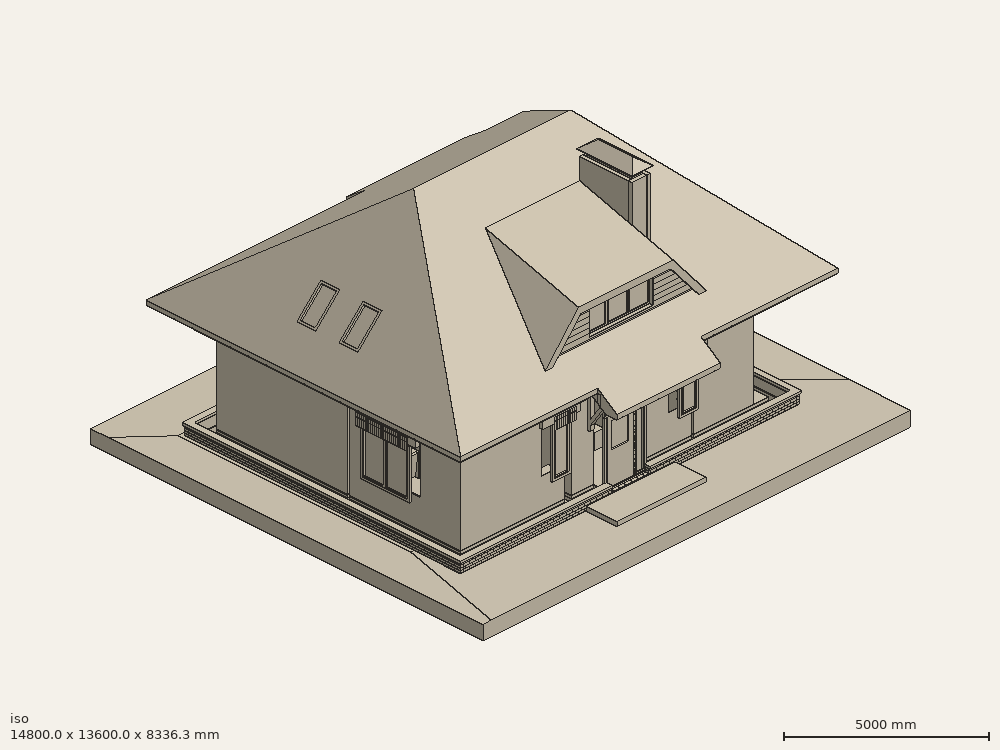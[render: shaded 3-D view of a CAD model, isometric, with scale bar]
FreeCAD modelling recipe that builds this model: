
FCSTD DOCUMENT  (FreeCAD 0.19R)
Label: 280522_90m2_w_smeta
License: All rights reserved
LicenseURL: http://en.wikipedia.org/wiki/All_rights_reserved
objects: Part::Part2DObjectPython×809, Part::FeaturePython×533, App::FeaturePython×150, Part::Feature×112, Part::Box×89, App::GeometryPython×67, Part::Extrusion×36, TechDraw::DrawViewAnnotation×36, Sketcher::SketchObject×34, Part::MultiFuse×31, Part::Cut×30, App::MaterialObjectPython×24, Part::MultiCommon×23, TechDraw::DrawLeaderLine×17, Part::Mirroring×17, App::DocumentObjectGroup×13, TechDraw::DrawViewArch×12, TechDraw::DrawSVGTemplate×10, TechDraw::DrawPage×10, Part::Cylinder×9, +10 more types
note: 1817 computed .brp shape members not serialized (recipe doc carries the construction recipe); baked Part::Feature solids carry a one-line shape summary decoded from their .brp

FEATURE [Part::Part2DObjectPython] Line1049  # Draft 2D object (typed FeaturePython)
  ChamferSize = 0
  Closed = true
  End = (3805,3080,0)
  FilletRadius = 0
  Length = 6815
  MakeFace = false
  Placement = pos=(4290,9800,0) rot=(0,0,1;1.5708rad)
  Points = (2) [(-6720,-6330,0),(-6720,485,0)]
  Start = (10620,3080,0)
  Subdivisions = 0
FEATURE [Sketcher::SketchObject] Sketch231  label="Профиль ПНО 120-8"
  FullyConstrained = false
  Placement = pos=(9420,5.68e-13,0) rot=(1,0,0;1.5708rad)
  sketch-geometry (19):
    g0: LineSegment StartX=0 StartY=0 StartZ=0 EndX=1190 EndY=0 EndZ=0
    g1: LineSegment StartX=1190 StartY=0 StartZ=0 EndX=1190 EndY=160 EndZ=0
    g2: LineSegment StartX=1190 StartY=160 StartZ=0 EndX=0 EndY=160 EndZ=0
    g3: LineSegment StartX=0 StartY=160 StartZ=0 EndX=0 EndY=0 EndZ=0
    g4: Circle CenterX=100 CenterY=80 CenterZ=0 NormalX=0 NormalY=0 NormalZ=1 AngleXU=0 Radius=50
    g5: Circle CenterX=240 CenterY=80 CenterZ=0 NormalX=0 NormalY=0 NormalZ=1 AngleXU=0 Radius=50
    g6: LineSegment StartX=100 StartY=80 StartZ=0 EndX=240 EndY=80 EndZ=0
    g7: Circle CenterX=380 CenterY=80 CenterZ=0 NormalX=0 NormalY=0 NormalZ=1 AngleXU=0 Radius=50
    g8: LineSegment StartX=240 StartY=80 StartZ=0 EndX=380 EndY=80 EndZ=0
    g9: Circle CenterX=520 CenterY=80 CenterZ=0 NormalX=0 NormalY=0 NormalZ=1 AngleXU=0 Radius=50
    g10: LineSegment StartX=380 StartY=80 StartZ=0 EndX=520 EndY=80 EndZ=0
    g11: Circle CenterX=660 CenterY=80 CenterZ=0 NormalX=0 NormalY=0 NormalZ=1 AngleXU=0 Radius=50
    g12: LineSegment StartX=520 StartY=80 StartZ=0 EndX=660 EndY=80 EndZ=0
    g13: Circle CenterX=800 CenterY=80 CenterZ=0 NormalX=0 NormalY=0 NormalZ=1 AngleXU=0 Radius=50
    g14: LineSegment StartX=660 StartY=80 StartZ=0 EndX=800 EndY=80 EndZ=0
    g15: Circle CenterX=940 CenterY=80 CenterZ=0 NormalX=0 NormalY=0 NormalZ=1 AngleXU=0 Radius=50
    g16: LineSegment StartX=800 StartY=80 StartZ=0 EndX=940 EndY=80 EndZ=0
    g17: Circle CenterX=1080 CenterY=80 CenterZ=0 NormalX=0 NormalY=0 NormalZ=1 AngleXU=0 Radius=50
    g18: LineSegment StartX=940 StartY=80 StartZ=0 EndX=1080 EndY=80 EndZ=0
  constraints (49):
    c: Coincident(g0,g1)
    c: Coincident(g1,g2)
    c: Coincident(g2,g3)
    c: Coincident(g3,g0)
    c: Horizontal(g0)
    c: Horizontal(g2)
    c: Vertical(g1)
    c: Vertical(g3)
    c: Coincident(g0,g-1)
    c: DistanceY(g3,g3) = 160
    c: DistanceX(g2,g2) = 1190
    c: Diameter(g4) = 100
    c: DistanceY(g4,g2) = 80
    c: Diameter(g5) = 100
    c: Coincident(g4,g6)
    c: Coincident(g5,g6)
    c: Distance(g6) = 140
    c: Angle(g6) = 0
    c: Diameter(g7) = 100
    c: Coincident(g5,g8)
    c: Coincident(g7,g8)
    c: Equal(g6,g8)
    c: Parallel(g8,g6)
    c: Diameter(g9) = 100
    c: Coincident(g7,g10)
    c: Coincident(g9,g10)
    c: Equal(g6,g10)
    c: Parallel(g10,g6)
    c: Diameter(g11) = 100
    c: Coincident(g9,g12)
    c: Coincident(g11,g12)
    c: Equal(g6,g12)
    c: Parallel(g12,g6)
    c: Diameter(g13) = 100
    c: Coincident(g11,g14)
    c: Coincident(g13,g14)
    c: Equal(g6,g14)
    c: Parallel(g14,g6)
    c: Diameter(g15) = 100
    c: Coincident(g13,g16)
    c: Coincident(g15,g16)
    c: Equal(g6,g16)
    c: Parallel(g16,g6)
    c: Diameter(g17) = 100
    c: Coincident(g15,g18)
    c: Coincident(g17,g18)
    c: Equal(g6,g18)
    c: Parallel(g18,g6)
    c: DistanceX(g2,g4) = 100
FEATURE [Part::Part2DObjectPython] Circle073  label="люк_контур 001"  # Draft 2D object (typed FeaturePython)
  FirstAngle = 0
  LastAngle = 0
  MakeFace = false
  Placement = pos=(32600,-2000,0) rot=(0,0,1;0rad)
  Radius = 350
FEATURE [Part::FeaturePython] Structure044  label="люк контур Д700"  # Arch/BIM 52 (typed FeaturePython)
  Base = -> Circle073
  FaceMaker = 0
  Height = 150
  HorizontalArea = 384845
  IfcData = complex_attributes={"OwnerHistory": {}, "IsNestedBy": {}, "IsDecomposedBy": {}, "IsDefinedBy": {}, "ObjectPlacement": {}, "Representation":... (+4 chars omitted)
  IfcType = 52
  Length = 0
  MoveBase = false
  MoveWithHost = false
  Nodes = (2) [(32600,-2000,0),(32600,-2000,-150)]
  NodesOffset = 0
  Normal = (0,0,-1)
  PerimeterLength = 2199.11
  VerticalArea = 329867
  Width = 100
FEATURE [Part::Part2DObjectPython] Line1077  # Draft 2D object (typed FeaturePython)
  ChamferSize = 0
  Closed = true
  End = (-50,-45,0)
  FilletRadius = 0
  Length = 10670
  MakeFace = false
  Placement = pos=(12060,265,0) rot=(0,0,1;0rad)
  Points = (2) [(-1440,-310,0),(-12110,-310,0)]
  Start = (10620,-45,0)
  Subdivisions = 0
FEATURE [App::FeaturePython] Dimension003  # Draft dimension (typed FeaturePython)
  Diameter = false
  Dimline = (12209.6,200,0)
  Direction = (0,0,0)
  Distance = 9480
  End = (11130,8925,0)
  Normal = (0,0,1)
  Start = (11130,-555,0)
FEATURE [Sketcher::SketchObject] Sketch248
  FullyConstrained = true
  Placement = pos=(2535,4425,0) rot=(1,0,0;1.5708rad)
  sketch-geometry (8):
    g0: LineSegment StartX=0 StartY=0 StartZ=0 EndX=900 EndY=0 EndZ=0
    g1: LineSegment StartX=900 StartY=0 StartZ=0 EndX=900 EndY=2400 EndZ=0
    g2: LineSegment StartX=900 StartY=2400 StartZ=0 EndX=0 EndY=2400 EndZ=0
    g3: LineSegment StartX=0 StartY=2400 StartZ=0 EndX=0 EndY=0 EndZ=0
    g4: LineSegment StartX=50 StartY=0 StartZ=0 EndX=850 EndY=0 EndZ=0
    g5: LineSegment StartX=850 StartY=0 StartZ=0 EndX=850 EndY=2350 EndZ=0
    g6: LineSegment StartX=850 StartY=2350 StartZ=0 EndX=50 EndY=2350 EndZ=0
    g7: LineSegment StartX=50 StartY=2350 StartZ=0 EndX=50 EndY=0 EndZ=0
  constraints (23):
    c: Coincident(g0,g1)
    c: Coincident(g1,g2)
    c: Coincident(g2,g3)
    c: Coincident(g3,g0)
    c: Horizontal(g0)
    c: Horizontal(g2)
    c: Vertical(g1)
    c: Vertical(g3)
    c: Coincident(g4,g5)
    c: Coincident(g5,g6)
    c: Coincident(g6,g7)
    c: Coincident(g7,g4)
    c: Horizontal(g4)
    c: Horizontal(g6)
    c: Vertical(g5)
    c: Vertical(g7)
    c: DistanceY(g1) = 2400  'Height'
    c: DistanceX(g0) = 900  'Width'
    c: DistanceY(g6,g2) = 50  'Frame1'
    c: DistanceX(g2,g6) = 50  'Frame2'
    c: DistanceX(g4,g0) = 50  'Frame3'
    c: DistanceY(g0,g4) = 0
    c: Coincident(g0,g-1)
FEATURE [Part::Part2DObjectPython] Wire460  label="границы участка"  # Draft 2D object (typed FeaturePython)
  ChamferSize = 0
  Closed = true
  End = (24467.8,29583.2,0)
  FilletRadius = 0
  Length = 156987
  MakeFace = false
  Placement = pos=(22704.1,-9881.8,0) rot=(0,0,1;0.025758rad)
  Points = (7) [(0,0,0),(-3118.22,176.296,0),(-9989.98,2199.83,0),(-22349.9,2518.26,0),(-33551.4,825.818,0),(-40981.4,39865.2,0),(2779.54,39406.5,0)]
  Start = (22704.1,-9881.8,0)
  Subdivisions = 0
FEATURE [Part::FeaturePython] Structure133  label="грунт в границах участка"  # Arch/BIM 52 (typed FeaturePython)
  Base = -> Wire460
  FaceMaker = 0
  Height = 1000
  HorizontalArea = 1.47224e+09
  IfcData = complex_attributes={"OwnerHistory": {}, "IsNestedBy": {}, "IsDecomposedBy": {}, "IsDefinedBy": {}, "ObjectPlacement": {}, "Representation":... (+4 chars omitted)
  IfcType = 52
  Length = 0
  MoveBase = false
  MoveWithHost = false
  Nodes = (2) [(5892.5,11504.2,0),(5892.5,11504.2,-1000)]
  NodesOffset = 0
  Normal = (0,0,-1)
  PerimeterLength = 156987
  Placement = pos=(0,0,-320) rot=(0,0,1;0rad)
  VerticalArea = 1.56987e+08
  Width = 100
FEATURE [Part::Part2DObjectPython] Wire464  label="мауэрлат003"  # Draft 2D object (typed FeaturePython)
  ChamferSize = 0
  Closed = true
  End = (14568.5,-7412.72,0)
  FilletRadius = 0
  Length = 30000
  MakeFace = false
  Placement = pos=(20304,-1451.15,0) rot=(0,0,-1;0.229406rad)
  Points = (4) [(3770.46,-7109.62,0),(3770.46,-109.624,0),(-4229.54,-109.624,0),(-4229.54,-7109.62,0)]
  Start = (22359,-9231.91,0)
  Subdivisions = 0
FEATURE [Part::Part2DObjectPython] Rectangle2375  # Draft 2D object (typed FeaturePython)
  ChamferSize = 0
  Columns = 1
  FilletRadius = 0
  Height = 150
  Length = 800
  MakeFace = true
  Placement = pos=(-1461.06,-5083.09,0) rot=(0,0,-1;1.39508rad)
  Rows = 1
FEATURE [Part::Part2DObjectPython] Rectangle2376  # Draft 2D object (typed FeaturePython)
  ChamferSize = 0
  Columns = 1
  FilletRadius = 0
  Height = 150
  Length = 500
  MakeFace = true
  Placement = pos=(-6959.67,-6719.51,0) rot=(0,0,1;1.74651rad)
  Rows = 1
FEATURE [Part::Part2DObjectPython] Rectangle2377  # Draft 2D object (typed FeaturePython)
  ChamferSize = 0
  Columns = 1
  FilletRadius = 0
  Height = 2300
  Length = 6000
  MakeFace = false
  Placement = pos=(-1444.48,-4318.42,0) rot=(0,0,1;3.31731rad)
  Rows = 1
FEATURE [Part::FeaturePython] Roof011  label="Навес над парковкой"  # Arch/BIM 113 (typed FeaturePython)
  Angles = [90,10,90,10]
  Base = -> Wire464
  BorderLength = 0
  Face = 0
  Flip = false
  Heights = [0,617.144,0,617.144]
  HorizontalArea = 5.6e+07
  IdRel = [0,0,0,0]
  IfcType = 113
  MoveBase = false
  MoveWithHost = false
  Overhang = [0,0,0,0]
  PerimeterLength = 30000
  Placement = pos=(0,0,2500) rot=(0,0,1;0rad)
  PredefinedType = 0
  RidgeLength = 0
  Runs = [0,3500,0,3500]
  Thickness = [150,150,150,150]
  VerticalArea = 7.00644e+06
FEATURE [Part::FeaturePython] Structure135  label="Structure134"  # Arch/BIM 52 (typed FeaturePython)
  Base = -> Rectangle2375
  FaceMaker = 0
  Height = 1800
  HorizontalArea = 120000
  IfcData = complex_attributes={"OwnerHistory": {}, "IsNestedBy": {}, "IsDecomposedBy": {}, "IsDefinedBy": {}, "ObjectPlacement": {}, "Representation":... (+4 chars omitted)
  IfcType = 52
  Length = 0
  MoveBase = false
  MoveWithHost = false
  Nodes = (2) [(-35.6948,-25773.1,0),(-35.6948,-25773.1,1800)]
  NodesOffset = 0
  Normal = (0,0,0)
  PerimeterLength = 1900
  VerticalArea = 3.42e+06
  Width = 100
FEATURE [Part::FeaturePython] Structure136  label="Structure135"  # Arch/BIM 52 (typed FeaturePython)
  Base = -> Rectangle2376
  FaceMaker = 0
  Height = 600
  HorizontalArea = 75000
  IfcData = complex_attributes={"OwnerHistory": {}, "IsNestedBy": {}, "IsDecomposedBy": {}, "IsDefinedBy": {}, "ObjectPlacement": {}, "Representation":... (+4 chars omitted)
  IfcType = 52
  Length = 0
  MoveBase = false
  MoveWithHost = false
  Nodes = (2) [(1351.07,-25965.1,0),(1351.07,-25965.1,600)]
  NodesOffset = 0
  Normal = (0,0,0)
  PerimeterLength = 1300
  Placement = pos=(0,-4e-15,1240) rot=(0,0,1;0rad)
  VerticalArea = 780000
  Width = 100
FEATURE [Part::FeaturePython] Wall097  label="Wall007"  # Arch/BIM 166 (typed FeaturePython)
  Align = 1
  Area = 4.067e+07
  Base = -> Rectangle2377
  BlockHeight = 0
  BlockLength = 0
  CountBroken = 0
  CountEntire = 0
  Face = 0
  Height = 2450
  HorizontalArea = 2.595e+06
  IfcType = 166
  Joint = 0
  Length = 16600
  MakeBlocks = false
  MoveBase = false
  MoveWithHost = false
  Normal = (0,0,0)
  OffsetFirst = 0
  OffsetSecond = 0
  PerimeterLength = 12600
  Placement = pos=(0,0,-150) rot=(0,0,1;0rad)
  PredefinedType = 0
  Subtractions = -> [Structure136,Structure135]
  VerticalArea = 7.564e+07
  Width = 150
FEATURE [Sketcher::SketchObject] Sketch250  label="Габарит человека"
  FullyConstrained = false
  Placement = pos=(0,0,0) rot=(1,0,0;1.5708rad)
  sketch-geometry (21):
    g0: LineSegment StartX=-250 StartY=0 StartZ=0 EndX=250 EndY=0 EndZ=0
    g1: LineSegment StartX=250 StartY=0 StartZ=0 EndX=250 EndY=1750 EndZ=0
    g2: LineSegment StartX=250 StartY=1750 StartZ=0 EndX=-250 EndY=1750 EndZ=0
    g3: LineSegment StartX=-250 StartY=1750 StartZ=0 EndX=-250 EndY=0 EndZ=0
    g4: LineSegment StartX=85 StartY=1500 StartZ=0 EndX=85 EndY=1750 EndZ=0
    g5: LineSegment StartX=85 StartY=1750 StartZ=0 EndX=-85 EndY=1750 EndZ=0
    g6: LineSegment StartX=-85 StartY=1750 StartZ=0 EndX=-85 EndY=1500 EndZ=0
    g7: LineSegment StartX=250 StartY=750 StartZ=0 EndX=250 EndY=1500 EndZ=0
    g8: LineSegment StartX=-250 StartY=1500 StartZ=0 EndX=-250 EndY=750 EndZ=0
    g9: LineSegment StartX=-110 StartY=0 StartZ=0 EndX=110 EndY=0 EndZ=0
    g10: LineSegment StartX=110 StartY=0 StartZ=0 EndX=175 EndY=750 EndZ=0
    g11: LineSegment StartX=-175 StartY=750 StartZ=0 EndX=-110 EndY=0 EndZ=0
    g12: GeomPoint X=0 Y=750 Z=0
    g13: GeomPoint X=-110 Y=0 Z=0
    g14: GeomPoint X=110 Y=0 Z=0
    g15: GeomPoint X=175 Y=750 Z=0
    g16: GeomPoint X=-175 Y=750 Z=0
    g17: LineSegment StartX=-250 StartY=1500 StartZ=0 EndX=-85 EndY=1500 EndZ=0
    g18: LineSegment StartX=85 StartY=1500 StartZ=0 EndX=250 EndY=1500 EndZ=0
    g19: LineSegment StartX=-250 StartY=750 StartZ=0 EndX=-175 EndY=750 EndZ=0
    g20: LineSegment StartX=175 StartY=750 StartZ=0 EndX=250 EndY=750 EndZ=0
  constraints (50):
    c: Coincident(g0,g1)
    c: Coincident(g1,g2)
    c: Coincident(g2,g3)
    c: Coincident(g3,g0)
    c: Horizontal(g0)
    c: Horizontal(g2)
    c: Vertical(g1)
    c: Vertical(g3)
    c: Symmetric(g0,g0,g-1)
    c: DistanceX(g2,g2) = 500
    c: DistanceY(g1,g1) = 1750
    c: Coincident(g4,g5)
    c: Coincident(g5,g6)
    c: Horizontal(g5)
    c: Vertical(g4)
    c: Vertical(g6)
    c: Vertical(g7)
    c: Vertical(g8)
    c: Coincident(g9,g10)
    c: DistanceX(g5,g5) = 170
    c: DistanceY(g4,g4) = 250
    c: PointOnObject(g4,g2)
    c: Symmetric(g6,g4,g-2)
    c: PointOnObject(g8,g3)
    c: PointOnObject(g7,g1)
    c: Coincident(g9,g11)
    c: DistanceX(g9,g9) = 220
    c: DistanceY(g0,g7) = 750
    c: PointOnObject(g12,g-2)
    c: Coincident(g13,g9)
    c: Coincident(g14,g9)
    c: Symmetric(g13,g14,g-2)
    c: PointOnObject(g14,g0)
    c: Coincident(g15,g10)
    c: Symmetric(g15,g16,g-2)
    c: DistanceX(g16,g15) = 350
    c: Coincident(g17,g8)
    c: Coincident(g17,g6)
    c: Horizontal(g17)
    c: Coincident(g18,g4)
    c: Coincident(g18,g7)
    c: Horizontal(g18)
    c: Coincident(g19,g8)
    c: Coincident(g19,g11)
    c: Horizontal(g19)
    c: Coincident(g20,g10)
    c: Coincident(g20,g7)
    c: Horizontal(g20)
    c: Equal(g19,g20)
    c: Equal(g11,g10)
FEATURE [Part::Extrusion] Extrude007  label="Габарит человека 001"
  Base = -> Sketch250
  Dir = (0,-1,2e-16)
  DirMode = 2
  FaceMakerClass = Part::FaceMakerBullseye
  LengthFwd = 290
  LengthRev = 0
  Placement = pos=(5755,5100,0) rot=(0,0,1;1.5708rad)
  Solid = true
  Symmetric = false
FEATURE [Part::Extrusion] Extrude008  label="Габарит человека 002"
  Base = -> Sketch250
  Dir = (0,-1,2e-16)
  DirMode = 2
  FaceMakerClass = Part::FaceMakerBullseye
  LengthFwd = 290
  LengthRev = 0
  Placement = pos=(6196.11,7744.63,925) rot=(0,0,1;0rad)
  Solid = true
  Symmetric = false
FEATURE [Part::Part2DObjectPython] Rectangle2381  # Draft 2D object (typed FeaturePython)
  ChamferSize = 0
  Columns = 1
  FilletRadius = 0
  Height = 1045
  Length = 3080
  MakeFace = false
  Placement = pos=(3745,-1680,0) rot=(0,0,1;0rad)
  Rows = 1
FEATURE [Image::ImagePlane] ImagePlane  label="План участка"
  Placement = pos=(-131.116,19324.2,-1100) rot=(0,0,1;3.16732rad)
  XSize = 103541
  YSize = 98696.8
FEATURE [Sketcher::SketchObject] Sketch251
  FullyConstrained = true
  Placement = pos=(6110,75,0) rot=(0.57735,0.57735,0.57735;2.0944rad)
  sketch-geometry (8):
    g0: LineSegment StartX=0 StartY=0 StartZ=0 EndX=900 EndY=0 EndZ=0
    g1: LineSegment StartX=900 StartY=0 StartZ=0 EndX=900 EndY=2400 EndZ=0
    g2: LineSegment StartX=900 StartY=2400 StartZ=0 EndX=0 EndY=2400 EndZ=0
    g3: LineSegment StartX=0 StartY=2400 StartZ=0 EndX=0 EndY=0 EndZ=0
    g4: LineSegment StartX=50 StartY=0 StartZ=0 EndX=850 EndY=0 EndZ=0
    g5: LineSegment StartX=850 StartY=0 StartZ=0 EndX=850 EndY=2350 EndZ=0
    g6: LineSegment StartX=850 StartY=2350 StartZ=0 EndX=50 EndY=2350 EndZ=0
    g7: LineSegment StartX=50 StartY=2350 StartZ=0 EndX=50 EndY=0 EndZ=0
  constraints (23):
    c: Coincident(g0,g1)
    c: Coincident(g1,g2)
    c: Coincident(g2,g3)
    c: Coincident(g3,g0)
    c: Horizontal(g0)
    c: Horizontal(g2)
    c: Vertical(g1)
    c: Vertical(g3)
    c: Coincident(g4,g5)
    c: Coincident(g5,g6)
    c: Coincident(g6,g7)
    c: Coincident(g7,g4)
    c: Horizontal(g4)
    c: Horizontal(g6)
    c: Vertical(g5)
    c: Vertical(g7)
    c: DistanceY(g1) = 2400  'Height'
    c: DistanceX(g0) = 900  'Width'
    c: DistanceY(g6,g2) = 50  'Frame1'
    c: DistanceX(g2,g6) = 50  'Frame2'
    c: DistanceX(g4,g0) = 50  'Frame3'
    c: DistanceY(g0,g4) = 0
    c: Coincident(g0,g-1)
FEATURE [App::FeaturePython] Dimension004  # Draft dimension (typed FeaturePython)
  Diameter = false
  Dimline = (-1400,-400,0)
  Direction = (0,0,0)
  Distance = 3315
  End = (-1654.18,3080,0)
  Normal = (0,0,1)
  Start = (-1654.18,-235,0)
FEATURE [App::FeaturePython] Dimension006  # Draft dimension (typed FeaturePython)
  Diameter = false
  Dimline = (-1400,3680,0)
  Direction = (0,0,0)
  Distance = 5525
  End = (-1654.18,8605,0)
  Normal = (0,0,1)
  Start = (-1654.18,3080,0)
FEATURE [Part::Part2DObjectPython] Line1184  label="Line1179"  # Draft 2D object (typed FeaturePython)
  ChamferSize = 0
  Closed = true
  End = (7880,-565,0)
  FilletRadius = 0
  Length = 770
  MakeFace = true
  Placement = pos=(7760,-565,0) rot=(0,0,-1;0rad)
  Points = (2) [(-650,1.36424e-12,0),(120,1.36424e-12,0)]
  Start = (7110,-565,0)
  Subdivisions = 0
FEATURE [Part::Part2DObjectPython] Line1186  # Draft 2D object (typed FeaturePython)
  ChamferSize = 0
  Closed = true
  End = (4890,8935,0)
  FilletRadius = 0
  Length = 3760
  MakeFace = true
  Placement = pos=(1650,8935,0) rot=(0,0,1;0rad)
  Points = (2) [(-520,0,0),(3240,0,0)]
  Start = (1130,8935,0)
  Subdivisions = 0
FEATURE [Part::Part2DObjectPython] Line1191  label="Line1184"  # Draft 2D object (typed FeaturePython)
  ChamferSize = 0
  Closed = true
  End = (3460,-565,0)
  FilletRadius = 0
  Length = 770
  MakeFace = true
  Placement = pos=(4120,-595,0) rot=(0,0,-1;0rad)
  Points = (2) [(-1430,30,0),(-660,30,0)]
  Start = (2690,-565,0)
  Subdivisions = 0
FEATURE [Sketcher::SketchObject] Sketch260
  FullyConstrained = true
  Placement = pos=(4160,4425,-180) rot=(1,0,0;1.5708rad)
  sketch-geometry (8):
    g0: LineSegment StartX=0 StartY=0 StartZ=0 EndX=900 EndY=0 EndZ=0
    g1: LineSegment StartX=900 StartY=0 StartZ=0 EndX=900 EndY=2400 EndZ=0
    g2: LineSegment StartX=900 StartY=2400 StartZ=0 EndX=0 EndY=2400 EndZ=0
    g3: LineSegment StartX=0 StartY=2400 StartZ=0 EndX=0 EndY=0 EndZ=0
    g4: LineSegment StartX=50 StartY=0 StartZ=0 EndX=850 EndY=0 EndZ=0
    g5: LineSegment StartX=850 StartY=0 StartZ=0 EndX=850 EndY=2350 EndZ=0
    g6: LineSegment StartX=850 StartY=2350 StartZ=0 EndX=50 EndY=2350 EndZ=0
    g7: LineSegment StartX=50 StartY=2350 StartZ=0 EndX=50 EndY=0 EndZ=0
  constraints (23):
    c: Coincident(g0,g1)
    c: Coincident(g1,g2)
    c: Coincident(g2,g3)
    c: Coincident(g3,g0)
    c: Horizontal(g0)
    c: Horizontal(g2)
    c: Vertical(g1)
    c: Vertical(g3)
    c: Coincident(g4,g5)
    c: Coincident(g5,g6)
    c: Coincident(g6,g7)
    c: Coincident(g7,g4)
    c: Horizontal(g4)
    c: Horizontal(g6)
    c: Vertical(g5)
    c: Vertical(g7)
    c: DistanceY(g1) = 2400  'Height'
    c: DistanceX(g0) = 900  'Width'
    c: DistanceY(g6,g2) = 50  'Frame1'
    c: DistanceX(g2,g6) = 50  'Frame2'
    c: DistanceX(g4,g0) = 50  'Frame3'
    c: DistanceY(g0,g4) = 0
    c: Coincident(g0,g-1)
FEATURE [Part::Part2DObjectPython] Line1200  label="Line1202"  # Draft 2D object (typed FeaturePython)
  ChamferSize = 0
  Closed = true
  End = (6155,1715,0)
  FilletRadius = 0
  Length = 1760
  MakeFace = false
  Placement = pos=(3685,600,0) rot=(0,0,-1;1.5708rad)
  Points = (2) [(645,2470,0),(-1115,2470,0)]
  Start = (6155,-45,0)
  Subdivisions = 0
FEATURE [Part::Extrusion] Extrude012  label="Габарит человека 003"
  Base = -> Sketch250
  Dir = (0,-1,2e-16)
  DirMode = 2
  FaceMakerClass = Part::FaceMakerBullseye
  LengthFwd = 290
  LengthRev = 0
  Placement = pos=(9805.7,6221.35,3145) rot=(0,0,1;0rad)
  Solid = true
  Symmetric = false
FEATURE [Part::Extrusion] Extrude022  label="Габарит человека 004"
  Base = -> Sketch250
  Dir = (0,-1,2e-16)
  DirMode = 2
  FaceMakerClass = Part::FaceMakerBullseye
  LengthFwd = 290
  LengthRev = 0
  Placement = pos=(5569.37,1334.73,3145) rot=(0,0,1;0rad)
  Solid = true
  Symmetric = false
FEATURE [Part::Part2DObjectPython] Rectangle556  label="вытяжка осн мал"  # Draft 2D object (typed FeaturePython)
  ChamferSize = 0
  Columns = 1
  FilletRadius = 0
  Height = 400
  Length = 300
  MakeFace = false
  Placement = pos=(9777.57,514.584,1900) rot=(0,0,-1;0.785398rad)
  Rows = 1
FEATURE [Part::Box] Box3145  label="ТВ"
  AttacherType = Attacher::AttachEngine3D
  Height = 750
  Length = 1400
  Placement = pos=(6905,7240,620) rot=(0,0,-1;1.5708rad)
  Width = 100
FEATURE [Part::Part2DObjectPython] Rectangle555  label="вытяжка осн бол"  # Draft 2D object (typed FeaturePython)
  ChamferSize = 0
  Columns = 1
  FilletRadius = 0
  Height = 600
  Length = 500
  MakeFace = false
  Placement = pos=(9636.15,514.584,1850) rot=(0,0,-1;0.785398rad)
  Rows = 1
FEATURE [Part::Loft] Loft001  label="вытяжка"
  Closed = false
  MaxDegree = 5
  Ruled = false
  Sections = -> [Rectangle555,Rectangle556]
  Solid = true
FEATURE [Part::Feature] Fusion013  label="стул005"
  Placement = pos=(9140,3600,0) rot=(0,0,1;0rad)
  shape: bbox 480 x 520 x 910 mm, 35 faces (baked)
FEATURE [Part::Feature] Fusion014  label="стул006"
  Placement = pos=(9160,3800,0) rot=(0,0,1;0rad)
  shape: bbox 480 x 520 x 910 mm, 35 faces (baked)
FEATURE [Part::Feature] Fusion015  label="стул007"
  Placement = pos=(9122.81,3800,0) rot=(0,0,1;0rad)
  shape: bbox 480 x 520 x 910 mm, 35 faces (baked)
FEATURE [Part::Feature] Fusion016  label="стул008"
  Placement = pos=(9122.81,3597.78,0) rot=(0,0,1;0rad)
  shape: bbox 480 x 520 x 910 mm, 35 faces (baked)
FEATURE [Part::Box] Box3157  label="шкаф 60 одежда 004"
  AttacherType = Attacher::AttachEngine3D
  Height = 2700
  Length = 2400
  Placement = pos=(-30,3875,0) rot=(0,0,1;0rad)
  Width = 600
FEATURE [Part::Box] Box3159  label="ТВ001"
  AttacherType = Attacher::AttachEngine3D
  Height = 750
  Length = 1200
  Placement = pos=(3400,7060,620) rot=(0,0,-1;1.5708rad)
  Width = 75
FEATURE [Part::Box] Box3163  label="обувница"
  AttacherType = Attacher::AttachEngine3D
  Height = 500
  Length = 350
  Placement = pos=(5727.31,1101.01,0) rot=(0,0,1;0rad)
  Width = 400
FEATURE [Part::Box] Box3175  label="Холодильник"
  AttacherType = Attacher::AttachEngine3D
  Height = 1600
  Length = 600
  Placement = pos=(8035,2385,0) rot=(0,0,1;3.14159rad)
  Width = 600
FEATURE [Part::Box] Box3179  label="шкаф 60 кухонный 003"
  AttacherType = Attacher::AttachEngine3D
  Height = 850
  Length = 600
  Placement = pos=(7435,1785,1600) rot=(0,0,1;0rad)
  Width = 600
FEATURE [Part::Box] Box3192  label="кофеварка"
  AttacherType = Attacher::AttachEngine3D
  Height = 250
  Length = 200
  Placement = pos=(10566,2712.21,850) rot=(0,0,1;1.5708rad)
  Width = 250
FEATURE [Part::Cylinder] Cylinder001  label="чайник"
  Angle = 360
  AttacherType = Attacher::AttachEngine3D
  Height = 250
  Placement = pos=(10499.3,2623.31,850) rot=(0,0,1;1.5708rad)
  Radius = 75
FEATURE [Part::Box] Box3195  label="шкаф 45 кухонный 003"
  AttacherType = Attacher::AttachEngine3D
  Height = 300
  Length = 1350
  Placement = pos=(8035,1185,2450) rot=(0,0,1;1.5708rad)
  Width = 600
FEATURE [Part::Part2DObjectPython] Rectangle2795  label="Д90-002"  # Draft 2D object (typed FeaturePython)
  ChamferSize = 0
  Columns = 1
  FilletRadius = 0
  Height = 150
  Length = 920
  MakeFace = true
  Placement = pos=(3825,4765,0) rot=(0,0,1;1.5708rad)
  Rows = 1
FEATURE [Part::FeaturePython] Structure023  label="Проём-ниша-Д90-018"  # Arch/BIM 52 (typed FeaturePython)
  Base = -> Rectangle2795
  FaceMaker = 0
  Height = 1859
  HorizontalArea = 138000
  IfcData = complex_attributes={"OwnerHistory": {}, "IsNestedBy": {}, "IsDecomposedBy": {}, "IsDefinedBy": {}, "ObjectPlacement": {}, "Representation":... (+4 chars omitted)
  IfcType = 52
  Length = 0
  MoveBase = false
  MoveWithHost = false
  Nodes = (2) [(8900,5350,0),(8900,5350,2180)]
  NodesOffset = 0
  Normal = (0,0,0)
  PerimeterLength = 2140
  Placement = pos=(0,0,262) rot=(0,0,1;0rad)
  VerticalArea = 3978260
  Width = 100
FEATURE [Part::Part2DObjectPython] Rectangle2807  label="ПР-003"  # Draft 2D object (typed FeaturePython)
  ChamferSize = 0
  Columns = 1
  FilletRadius = 0
  Height = 290
  Length = 1570
  MakeFace = true
  Placement = pos=(6025,3225,0) rot=(0,0,1;3.14159rad)
  Rows = 1
FEATURE [Part::FeaturePython] Structure020  label="Проём-ПР002"  # Arch/BIM 52 (typed FeaturePython)
  Base = -> Rectangle2807
  FaceMaker = 0
  Height = 2780
  HorizontalArea = 455300
  IfcData = complex_attributes={"OwnerHistory": {}, "IsNestedBy": {}, "IsDecomposedBy": {}, "IsDefinedBy": {}, "ObjectPlacement": {}, "Representation":... (+4 chars omitted)
  IfcType = 52
  Length = 0
  MoveBase = false
  MoveWithHost = false
  Nodes = (2) [(650,-4000,0),(650,-4000,2250)]
  NodesOffset = 0
  Normal = (0,0,0)
  PerimeterLength = 3720
  Placement = pos=(0,0,-200) rot=(0,0,1;0rad)
  VerticalArea = 10341600
  Width = 100
FEATURE [Part::Part2DObjectPython] Line1266  label="Line1267"  # Draft 2D object (typed FeaturePython)
  ChamferSize = 0
  Closed = true
  End = (-570,1265,0)
  FilletRadius = 0
  Length = 1810
  MakeFace = true
  Placement = pos=(-570,3075,0) rot=(0,0,-1;1.5708rad)
  Points = (2) [(0,0,0),(1810,0,0)]
  Start = (-570,3075,0)
  Subdivisions = 0
FEATURE [Part::Part2DObjectPython] Line1271  label="Line1272"  # Draft 2D object (typed FeaturePython)
  ChamferSize = 0
  Closed = true
  End = (7415,1135,0)
  FilletRadius = 0
  Length = 530
  MakeFace = false
  Placement = pos=(10065,4485,0) rot=(0,0,-1;1.5708rad)
  Points = (2) [(3350,-2120,0),(3350,-2650,0)]
  Start = (7945,1135,0)
  Subdivisions = 0
FEATURE [Part::Box] Box3204  label="шкаф 001"
  AttacherType = Attacher::AttachEngine3D
  Height = 2700
  Length = 600
  Placement = pos=(2370,3175,0) rot=(0,0,1;1.5708rad)
  Width = 600
FEATURE [Spreadsheet::Sheet] Spreadsheet
  cells = C1=N/N; D1=Помещение; E1=Площадь; C2=1); D2==<<Столовая>>.Label; E2==<<Столовая>>.Shape.Area; C3=2); D3==<<Кухня>>.Label; E3==<<Кухня>>.Shape.Area; C4=3); D4==<<Коридор>>.Label; E4==<<Коридор>>.Shape.Area; C5=4); D5==<<Санузел>>.Label; E5==<<Санузел>>.Shape.Area; C6=5); D6==<<Ванная>>.Label; E6==<<Ванная>>.Shape.Area; C7=6); D7==<<Прихожая (ТГ)>>.Label; E7==<<Прихожая (ТГ)>>.Shape.Area; C8=7); D8==<<Спальня>>.Label; E8==<<Спальня>>.Shape.Area; C9=8); D9==<<Кабинет>>.Label; E9==<<Кабинет>>.Shape.Area; D10=Итого:; E10==sum(E2:E9); D11==<<Тёплый контур (Площадь этажа)>>.Label; E11==<<Тёплый контур (Площадь этажа)>>.Shape.Area; C13=N/N; D13=Помещение; E13=Площадь; C14=1); D14==<<Холл мансарды>>.Label; E14==<<Холл мансарды>>.Shape.Area; C15=2); D15==<<СУ мансарды>>.Label; E15==<<СУ мансарды>>.Shape.Area; C16=3); D16==<<Спальня #1>>.Label; E16==<<Спальня #1>>.Shape.Area; C17=4); D17==<<Детская #1>>.Label; E17==<<Детская #1>>.Shape.Area; C18=5); D18==<<Детская #2>>.Label; E18==<<Детская #2>>.Shape.Area; C19=6); D19==<<Кладовка>>.Label; E19==<<Кладовка>>.Shape.Area; D20=Итого:; E20==sum(E14:E18); D21=Общая:; E21==E10 + E20; D24=Площадь остекления фрамуг в ТГ фактическая (без учёта остекл.двери):; E24==<<frame001>>.Shape.Area + <<frame002>>.Shape.Area; D25=Площадь ТГ; E25==<<Прихожая (ТГ)>>.Shape.Area; D26=Высота потолка h; E26=2800; D27=Объём ТГ; E27==E25 * E26; D28=Требуемая площадь остекления на 1m^3:; E28=30000; D29=Необходимая площадь остекления из расчета 0.03м^2 на 1m^3:; E29==E27 / E28; D31=Площадь кровли без учёта кукушки; E31==<<Wire1112>>.Shape.Area + <<Wire1113>>.Shape.Area + <<Wire1114>>.Shape.Area + <<Wire1115>>.Shape.Area; B34=Объёмы материалов:; B35=Кирпич полнотелый 1нф (кладка); D35=Итого:; E35==sum(E36:E40); D36==<<Несущая стена 2.1нф 250мм внутренняя001>>.Label; E36==<<Несущая стена 2.1нф 250мм внутренняя001>>.Shape.Volume; D37==<<Несущая стена 2.1нф 250мм внутренняя002>>.Label; E37==<<Несущая стена 2.1нф 250мм внутренняя002>>.Shape.Volume; D38==<<Несущая стена 2.1нф 250мм внутренняя 003>>.Label; E38==<<Несущая стена 2.1нф 250мм внутренняя 003>>.Shape.Volume; D39==<<Кладка под стойки>>.Label; E39==<<Кладка под стойки>>.Shape.Volume; D40==<<Кладка в уровне армпояса 2.1нф>>.Label; E40==<<Кладка в уровне армпояса 2.1нф>>.Shape.Volume; B42=Блок поризованый поротерм 38Т или аналог (кладка); D42=Итого:; E42==sum(E43:E44); D43==<<Внешняя стена Поротерм 38Т 380мм>>.Label; E43==<<Внешняя стена Поротерм 38Т 380мм>>.Shape.Volume; D44==<<Аттиковая стена Поротерм 38Т 380мм>>.Label; E44==<<Аттиковая стена Поротерм 38Т 380мм>>.Shape.Volume; B47=Кирпич облицовочный 1нф; D47=Итого:; E47==sum(E48:E49); D48==<<Облицовка 1nf кирпич>>.Label; E48==<<Облицовка 1nf кирпич>>.Shape.Volume; D49==<<облицовка дымохода шидель>>.Label; E49==<<облицовка дымохода шидель>>.Shape.Volume; B51=Отлив (вибропресс. бордюрный камень 1000х200х80мм); D51==<<Отлив (вибропресс. бордюрный камень 1000х200х80мм)>>.Label; E51==<<Отлив (вибропресс. бордюрный камень 1000х200х80мм)>>.Shape.Volume; B52=Облицовка цоколя (камень бетонный СКЦ2Л-24) ; D52==<<Отделка цоколя>>.Label; E52==<<Отделка цоколя>>.Shape.Volume; B54=Утеплитель XPS; D54=Итого:; E54==sum(E55:E61); D55==<<утепление торца ростверка XPS 50mm>>.Label; E55==<<утепление торца ростверка XPS 50mm>>.Shape.Volume; D56==<<Утепление цоколя XPS 50mm>>.Label; E56==<<Утепление цоколя XPS 50mm>>.Shape.Volume; D57==<<Утепление перемычек XPS 100+30mm>>.Label; E57==<<Утепление перемычек XPS 100+30mm>>.Shape.Volume; D58==<<Утепление пола 100мм XPS>>.Label; E58==<<Утепление пола 100мм XPS>>.Shape.Volume; D59==<<Утепление перекрытия XPS 100+20mm>>.Label; E59==<<Утепление пола 100мм XPS>>.Shape.Volume; D60==<<Утепление армпояса XPS 100mm>>.Label; E60==<<Утепление перекрытия XPS 100+20mm>>.Shape.Volume; D61==<<Утепление в уровне перекрытия XPS 100mm>>.Label; E61==<<Утепление в уровне перекрытия XPS 100mm>>.Shape.Volume; B63=Утеплитель PPS; D63=Итого:; E63==sum(E64:E65); D64==<<Деформационная подкладка и утепление PPS 50-100mm>>.Label; E64==<<Деформационная подкладка и утепление PPS 50-100mm>>.Shape.Volume; B66=Бетон (без учёта армирования):; D66=Итого:; E66==sum(E67:E74); D67==<<Плита ростверка 001>>.Label; E67==<<Плита ростверка 001>>.Shape.Volume; D68==<<Перемычки по ГОСТ 948-2016>>.Label; E68==<<Перемычки по ГОСТ 948-2016>>.Shape.Volume; D69==<<Внешние элементы>>.Label; E69==<<Внешние элементы>>.Shape.Volume; D70==<<Армпояс в уровне перекрытия 001>>.Label; E70==<<Армпояс в уровне перекрытия 001>>.Shape.Volume; D71==<<Армпояс под мауэрлат>>.Label; E71==<<Армпояс под мауэрлат>>.Shape.Volume; D72==<<Лестница забежная>>.Label; E72==<<Лестница забежная>>.Shape.Volume; D73==<<монолитный участок>>.Label; E73==<<монолитный участок>>.Shape.Volume; D74==<<монолитный участок001>>.Label; E74==<<монолитный участок001>>.Shape.Volume; B76=Перегородки (силикатный блок 80мм):; D76==<<Перегородки>>.Label; E76==<<Перегородки>>.Shape.Volume; B78=Стяжки:; D78=Итого:; E78==sum(E79:E80); D79==<<Стяжка мансарды 45мм>>.Label; E79==<<Стяжка мансарды 45мм>>.Shape.Volume; D80==<<Стяжка тёплого пола 80mm>>.Label; E80==<<Стяжка тёплого пола 80mm>>.Shape.Volume; B84=Дерево на стропильную систему  Сух. Ас.; D84=Итого:; E84==sum(E85:E87); D85==<<Стропилка (доска 50х200 сухая антисептированная)>>.Label; E85==<<Стропилка (доска 50х200 сухая антисептированная)>>.Shape.Volume; D86==<<Стойки и прогоны>>.Label; E86==<<Стойки и прогоны>>.Shape.Volume; D87==<<Элементы арх.декора>>.Label; E87==<<Элементы арх.декора>>.Shape.Volume
FEATURE [Part::Part2DObjectPython] ShapeString138  # Draft 2D object (typed FeaturePython)
  FontFile = <path>
  Placement = pos=(8506.65,5599.61,0) rot=(0,0,1;0rad)
  Size = 250
  String = 1
  Tracking = 0
FEATURE [Part::Part2DObjectPython] Circle088  # Draft 2D object (typed FeaturePython)
  Area = 0
  FirstAngle = 0
  LastAngle = 0
  MakeFace = false
  Placement = pos=(8600,5700,0) rot=(0,0,1;0rad)
  Radius = 200
FEATURE [Part::Part2DObjectPython] Circle089  label="Circle090"  # Draft 2D object (typed FeaturePython)
  Area = 0
  FirstAngle = 0
  LastAngle = 0
  MakeFace = false
  Placement = pos=(9000,1500,0) rot=(0,0,1;0rad)
  Radius = 200
FEATURE [Part::Part2DObjectPython] ShapeString139  # Draft 2D object (typed FeaturePython)
  FontFile = <path>
  Placement = pos=(8906.65,1399.61,0) rot=(0,0,1;0rad)
  Size = 250
  String = 2
  Tracking = 0
FEATURE [Part::Part2DObjectPython] Circle090  label="Circle091"  # Draft 2D object (typed FeaturePython)
  Area = 0
  FirstAngle = 0
  LastAngle = 0
  MakeFace = false
  Placement = pos=(4100,3800,0) rot=(0,0,1;0rad)
  Radius = 200
FEATURE [Part::Part2DObjectPython] ShapeString140  # Draft 2D object (typed FeaturePython)
  FontFile = <path>
  Placement = pos=(4006.65,3699.61,0) rot=(0,0,1;0rad)
  Size = 250
  String = 3
  Tracking = 0
FEATURE [Part::Part2DObjectPython] Circle091  label="Circle092"  # Draft 2D object (typed FeaturePython)
  Area = 0
  FirstAngle = 0
  LastAngle = 0
  MakeFace = false
  Placement = pos=(5300,1600,0) rot=(0,0,1;0rad)
  Radius = 200
FEATURE [Part::Part2DObjectPython] ShapeString141  # Draft 2D object (typed FeaturePython)
  FontFile = <path>
  Placement = pos=(5206.65,1499.61,0) rot=(0,0,1;0rad)
  Size = 250
  String = 6
  Tracking = 0
FEATURE [Part::Part2DObjectPython] Circle092  label="Circle093"  # Draft 2D object (typed FeaturePython)
  Area = 0
  FirstAngle = 0
  LastAngle = 0
  MakeFace = false
  Placement = pos=(6700,600,0) rot=(0,0,1;0rad)
  Radius = 200
FEATURE [Part::Part2DObjectPython] ShapeString142  # Draft 2D object (typed FeaturePython)
  FontFile = <path>
  Placement = pos=(6606.65,499.608,0) rot=(0,0,1;0rad)
  Size = 250
  String = 4
  Tracking = 0
FEATURE [Part::Part2DObjectPython] Circle093  label="Circle094"  # Draft 2D object (typed FeaturePython)
  Area = 0
  FirstAngle = 0
  LastAngle = 0
  MakeFace = false
  Placement = pos=(4731.92,5564.63,0) rot=(0,0,1;0rad)
  Radius = 200
FEATURE [Part::Part2DObjectPython] ShapeString143  # Draft 2D object (typed FeaturePython)
  FontFile = <path>
  Placement = pos=(4638.57,5464.24,0) rot=(0,0,1;0rad)
  Size = 250
  String = 5
  Tracking = 0
FEATURE [Part::Part2DObjectPython] Circle094  label="Circle095"  # Draft 2D object (typed FeaturePython)
  Area = 0
  FirstAngle = 0
  LastAngle = 0
  MakeFace = false
  Placement = pos=(2500,1900,0) rot=(0,0,1;0rad)
  Radius = 200
FEATURE [Part::Part2DObjectPython] ShapeString144  # Draft 2D object (typed FeaturePython)
  FontFile = <path>
  Placement = pos=(2406.65,1799.61,0) rot=(0,0,1;0rad)
  Size = 250
  String = 8
  Tracking = 0
FEATURE [Part::Part2DObjectPython] Circle095  label="Circle096"  # Draft 2D object (typed FeaturePython)
  Area = 0
  FirstAngle = 0
  LastAngle = 0
  MakeFace = false
  Placement = pos=(2653.52,6475,0) rot=(0,0,1;0rad)
  Radius = 200
FEATURE [Part::Part2DObjectPython] ShapeString145  # Draft 2D object (typed FeaturePython)
  FontFile = <path>
  Placement = pos=(2560.17,6374.61,0) rot=(0,0,1;0rad)
  Size = 250
  String = 7
  Tracking = 0
FEATURE [Part::Box] Box3209  label="ДШ001"
  AttacherType = Attacher::AttachEngine3D
  Height = 500
  Length = 500
  Placement = pos=(8035,1775,450) rot=(0,0,1;3.14159rad)
  Width = 580
FEATURE [Part::Box] Box3211  label="камин топка 700"
  AttacherType = Attacher::AttachEngine3D
  Height = 500
  Length = 750
  Placement = pos=(7285,2725,600) rot=(0,0,1;0rad)
  Width = 500
FEATURE [Part::Part2DObjectPython] Line1316  # Draft 2D object (typed FeaturePython)
  ChamferSize = 0
  Closed = true
  End = (2380,3165,0)
  FilletRadius = 0
  Length = 1175
  MakeFace = false
  Placement = pos=(1825,6465,0) rot=(0,0,-1;1.5708rad)
  Points = (2) [(3300,1730,0),(3300,555,0)]
  Start = (3555,3165,0)
  Subdivisions = 0
FEATURE [Part::Part2DObjectPython] Line1323  # Draft 2D object (typed FeaturePython)
  ChamferSize = 0
  Closed = true
  End = (7095,2655,0)
  FilletRadius = 0
  Length = 300
  MakeFace = false
  Placement = pos=(8675,3240,0) rot=(0,0,1;0rad)
  Points = (2) [(-1580,-285,0),(-1580,-585,0)]
  Start = (7095,2955,0)
  Subdivisions = 0
FEATURE [Part::Part2DObjectPython] Line1324  # Draft 2D object (typed FeaturePython)
  ChamferSize = 0
  Closed = true
  End = (7985,-45,0)
  FilletRadius = 0
  Length = 1220
  MakeFace = false
  Placement = pos=(9525,2015,0) rot=(0,0,1;0rad)
  Points = (2) [(-1540,-840,0),(-1540,-2060,0)]
  Start = (7985,1175,0)
  Subdivisions = 0
FEATURE [Part::Part2DObjectPython] Line1326  # Draft 2D object (typed FeaturePython)
  Area = 0
  ChamferSize = 0
  Closed = true
  End = (14200,6200,0)
  FilletRadius = 0
  Length = 1100
  MakeFace = true
  Placement = pos=(14200,7300,0) rot=(0,0,1;0rad)
  Points = (2) [(0,0,0),(0,-1100,0)]
  Start = (14200,7300,0)
  Subdivisions = 0
FEATURE [Part::Part2DObjectPython] Line1327  # Draft 2D object (typed FeaturePython)
  Area = 0
  ChamferSize = 0
  Closed = false
  End = (14200,7300,0)
  FilletRadius = 0
  Length = 282.843
  MakeFace = true
  Placement = pos=(14000,7500,0) rot=(0,0,1;0rad)
  Points = (2) [(0,0,0),(200,-200,0)]
  Start = (14000,7500,0)
  Subdivisions = 0
FEATURE [Part::Part2DObjectPython] Line1328  # Draft 2D object (typed FeaturePython)
  Area = 0
  ChamferSize = 0
  Closed = false
  End = (14400,7500,0)
  FilletRadius = 0
  Length = 282.843
  MakeFace = true
  Placement = pos=(14200,7300,0) rot=(0,0,1;0rad)
  Points = (2) [(0,0,0),(200,200,0)]
  Start = (14200,7300,0)
  Subdivisions = 0
FEATURE [Part::Part2DObjectPython] Line1329  # Draft 2D object (typed FeaturePython)
  Area = 0
  ChamferSize = 0
  Closed = false
  End = (14000,6600,0)
  FilletRadius = 0
  Length = 447.214
  MakeFace = true
  Placement = pos=(14200,6200,0) rot=(0,0,1;0rad)
  Points = (2) [(0,0,0),(-200,400,0)]
  Start = (14200,6200,0)
  Subdivisions = 0
FEATURE [Part::Part2DObjectPython] Line1330  # Draft 2D object (typed FeaturePython)
  Area = 0
  ChamferSize = 0
  Closed = false
  End = (14400,6600,0)
  FilletRadius = 0
  Length = 447.214
  MakeFace = true
  Placement = pos=(14200,6200,0) rot=(0,0,1;0rad)
  Points = (2) [(0,0,0),(200,400,0)]
  Start = (14200,6200,0)
  Subdivisions = 0
FEATURE [Part::Part2DObjectPython] ShapeString189  # Draft 2D object (typed FeaturePython)
  FontFile = <path>
  Placement = pos=(14073,5909.03,0) rot=(0,0,1;0rad)
  Size = 250
  String = С
  Tracking = 0
FEATURE [Part::Part2DObjectPython] ShapeString191  # Draft 2D object (typed FeaturePython)
  FontFile = <path>
  Placement = pos=(14006.7,7599.61,0) rot=(0,0,1;0rad)
  Size = 250
  String = Юг
  Tracking = 0
FEATURE [Part::Part2DObjectPython] Rectangle3074  label="Тёплый контур (Площадь этажа)"  # Draft 2D object (typed FeaturePython)
  Area = 89504600
  ChamferSize = 0
  Columns = 1
  FilletRadius = 0
  Height = 8420
  Length = 10630
  MakeFace = true
  Placement = pos=(-30,-25,0) rot=(0,0,1;0rad)
  Rows = 1
FEATURE [Part::Part2DObjectPython] Rectangle3095  label="ПР-001"  # Draft 2D object (typed FeaturePython)
  ChamferSize = 0
  Columns = 1
  FilletRadius = 0
  Height = 2655
  Length = 290
  MakeFace = true
  Placement = pos=(9840,2935,0) rot=(0,0,1;1.5708rad)
  Rows = 1
FEATURE [Part::FeaturePython] Structure317  label="Проём-ПР001"  # Arch/BIM 52 (typed FeaturePython)
  Base = -> Rectangle3095
  FaceMaker = 0
  Height = 2780
  HorizontalArea = 769950
  IfcData = complex_attributes={"OwnerHistory": {}, "IsNestedBy": {}, "IsDecomposedBy": {}, "IsDefinedBy": {}, "ObjectPlacement": {}, "Representation":... (+4 chars omitted)
  IfcType = 52
  Length = 0
  MoveBase = false
  MoveWithHost = false
  Nodes = (2) [(8200,3800,0),(8200,3800,2250)]
  NodesOffset = 0
  Normal = (0,0,0)
  PerimeterLength = 5890
  Placement = pos=(0,0,-200) rot=(0,0,1;0rad)
  VerticalArea = 16374200
  Width = 100
FEATURE [App::FeaturePython] Dimension002  # Draft dimension (typed FeaturePython)
  Diameter = false
  Dimline = (6500,-1110.73,0)
  Direction = (0,0,0)
  Distance = 11690
  End = (11130,-555,0)
  Normal = (0,0,1)
  Start = (-560,-555,0)
FEATURE [App::FeaturePython] Dimension012  # Draft dimension (typed FeaturePython)
  Diameter = false
  Dimline = (3300,1300,0)
  Direction = (0,0,0)
  Distance = 3250
  End = (3555,3205,0)
  Normal = (0,0,1)
  Start = (3555,-45,0)
FEATURE [App::FeaturePython] Dimension018  # Draft dimension (typed FeaturePython)
  Diameter = false
  Dimline = (6400,3500,0)
  Direction = (0,0,0)
  Distance = 290
  End = (6025,3225,0)
  Normal = (0,0,1)
  Start = (6025,2935,0)
FEATURE [Part::Part2DObjectPython] Line1357  # Draft 2D object (typed FeaturePython)
  ChamferSize = 0
  Closed = true
  End = (7105,4475,0)
  FilletRadius = 0
  Length = 4725
  MakeFace = false
  Placement = pos=(-600,5755,0) rot=(0,0,-1;0rad)
  Points = (2) [(2980,-1280,0),(7705,-1280,0)]
  Start = (2380,4475,0)
  Subdivisions = 0
FEATURE [Part::Part2DObjectPython] Line1358  # Draft 2D object (typed FeaturePython)
  ChamferSize = 0
  Closed = true
  End = (7055,1525,0)
  FilletRadius = 0
  Length = 860
  MakeFace = false
  Placement = pos=(8150,155,0) rot=(0,0,-1;0rad)
  Points = (2) [(-1955,1370,0),(-1095,1370,0)]
  Start = (6195,1525,0)
  Subdivisions = 0
FEATURE [Part::Part2DObjectPython] Line1360  # Draft 2D object (typed FeaturePython)
  ChamferSize = 0
  Closed = true
  End = (4945,6535,0)
  FilletRadius = 0
  Length = 800
  MakeFace = false
  Placement = pos=(5015,7415,0) rot=(0,0,1;1.5708rad)
  Points = (2) [(-880,-730,0),(-880,70,0)]
  Start = (5745,6535,0)
  Subdivisions = 0
FEATURE [Part::Part2DObjectPython] Rectangle3159  # Draft 2D object (typed FeaturePython)
  Area = 0
  ChamferSize = 0
  Columns = 1
  FilletRadius = 0
  Height = 250
  Length = 920
  MakeFace = false
  Placement = pos=(6940,5803.61,0) rot=(0,0,1;0rad)
  Rows = 1
FEATURE [Part::Extrusion] Extrude088  label="ПНО 55-12-8"
  Base = -> Sketch231
  Dir = (0,3880,0)
  DirMode = 0
  FaceMakerClass = Part::FaceMakerBullseye
  LengthFwd = 5480
  LengthRev = 0
  Placement = pos=(10,3085,2800) rot=(0,0,1;0rad)
  Solid = true
  Symmetric = false
FEATURE [Part::Box] Box3218  label="шкаф 003"
  AttacherType = Attacher::AttachEngine3D
  Height = 2650
  Length = 2960
  Placement = pos=(4425,-25,0) rot=(0,0,1;1.5708rad)
  Width = 600
FEATURE [Part::Cylinder] Cylinder002  label="БКН 150л"
  Angle = 360
  AttacherType = Attacher::AttachEngine3D
  Height = 1100
  Placement = pos=(6777.68,2563.8,0) rot=(0,0,1;0rad)
  Radius = 260
FEATURE [Part::Box] Box3220  label="Котёл 24кВт одноконтурн. закртытая камера"
  AttacherType = Attacher::AttachEngine3D
  Height = 700
  Length = 400
  Placement = pos=(6735,2195,1300) rot=(0,0,-1;1.5708rad)
  Width = 300
FEATURE [Part::Cylinder] Cylinder003  label="бак расширительный"
  Angle = 360
  AttacherType = Attacher::AttachEngine3D
  Height = 400
  Placement = pos=(6350.76,2737.83,2200) rot=(0,0,1;0rad)
  Radius = 175
FEATURE [Part::Box] Box3222  label="грёбенка и насосы"
  AttacherType = Attacher::AttachEngine3D
  Height = 900
  Length = 150
  Placement = pos=(7035,1575,0) rot=(0,0,1;1.5708rad)
  Width = 800
FEATURE [Part::Box] Box3223  label="Котёл электр. (резерв)"
  AttacherType = Attacher::AttachEngine3D
  Height = 700
  Length = 150
  Placement = pos=(6500,1575,1300) rot=(0,0,1;1.5708rad)
  Width = 200
FEATURE [Part::Part2DObjectPython] Line1390  # Draft 2D object (typed FeaturePython)
  ChamferSize = 0
  Closed = true
  End = (-50,3825,0)
  FilletRadius = 0
  Length = 2430
  MakeFace = false
  Placement = pos=(7425,5335,0) rot=(0,0,-1;1.5708rad)
  Points = (2) [(1510,-5045,0),(1510,-7475,0)]
  Start = (2380,3825,0)
  Subdivisions = 0
FEATURE [Part::FeaturePython] Structure342  label="Структура006"  # Arch/BIM 52 (typed FeaturePython)
  FaceMaker = 0
  Height = 450
  HorizontalArea = 1.04e+06
  IfcData = attributes={"GlobalId": {"name": "GlobalId", "type": "IfcGloballyUniqueId", "is_enum": false, "enum_values": []}, "Description": {"... (+484 chars omitted),+1 more (map truncated)
  IfcType = 52
  Length = 0
  MoveBase = false
  MoveWithHost = false
  Nodes = (2) [(6409.93,5722.83,0),(6409.93,5722.83,450)]
  NodesOffset = 0
  Normal = (0,0,1)
  PerimeterLength = 4500
  Placement = pos=(0,0,150) rot=(0,0,1;0rad)
  VerticalArea = 2.025e+06
  Width = 100
FEATURE [Part::Part2DObjectPython] Line1391  # Draft 2D object (typed FeaturePython)
  ChamferSize = 0
  Closed = true
  End = (6795,5675,0)
  FilletRadius = 0
  Length = 1200
  MakeFace = false
  Placement = pos=(6800,9505,0) rot=(0,0,1;0rad)
  Points = (2) [(-5,-2630,0),(-5,-3830,0)]
  Start = (6795,6875,0)
  Subdivisions = 0
FEATURE [Sketcher::SketchObject] Sketch309
  FullyConstrained = true
  Placement = pos=(3535,7375,0) rot=(0.57735,0.57735,0.57735;2.0944rad)
  sketch-geometry (8):
    g0: LineSegment StartX=0 StartY=0 StartZ=0 EndX=900 EndY=0 EndZ=0
    g1: LineSegment StartX=900 StartY=0 StartZ=0 EndX=900 EndY=2100 EndZ=0
    g2: LineSegment StartX=900 StartY=2100 StartZ=0 EndX=0 EndY=2100 EndZ=0
    g3: LineSegment StartX=0 StartY=2100 StartZ=0 EndX=0 EndY=0 EndZ=0
    g4: LineSegment StartX=50 StartY=0 StartZ=0 EndX=850 EndY=0 EndZ=0
    g5: LineSegment StartX=850 StartY=0 StartZ=0 EndX=850 EndY=2050 EndZ=0
    g6: LineSegment StartX=850 StartY=2050 StartZ=0 EndX=50 EndY=2050 EndZ=0
    g7: LineSegment StartX=50 StartY=2050 StartZ=0 EndX=50 EndY=0 EndZ=0
  constraints (23):
    c: Coincident(g0,g1)
    c: Coincident(g1,g2)
    c: Coincident(g2,g3)
    c: Coincident(g3,g0)
    c: Horizontal(g0)
    c: Horizontal(g2)
    c: Vertical(g1)
    c: Vertical(g3)
    c: Coincident(g4,g5)
    c: Coincident(g5,g6)
    c: Coincident(g6,g7)
    c: Coincident(g7,g4)
    c: Horizontal(g4)
    c: Horizontal(g6)
    c: Vertical(g5)
    c: Vertical(g7)
    c: DistanceY(g1) = 2100  'Height'
    c: DistanceX(g0) = 900  'Width'
    c: DistanceY(g6,g2) = 50  'Frame1'
    c: DistanceX(g2,g6) = 50  'Frame2'
    c: DistanceX(g4,g0) = 50  'Frame3'
    c: DistanceY(g0,g4) = 0
    c: Coincident(g0,g-1)
FEATURE [Part::Part2DObjectPython] Wire812  # Draft 2D object (typed FeaturePython)
  Area = 0
  ChamferSize = 0
  Closed = true
  End = (6020,5565,0)
  FilletRadius = 0
  Length = 2372.43
  MakeFace = false
  Placement = pos=(6875,5565,0) rot=(0,0,-1;1.5708rad)
  Points = (10) [(6.36646e-12,-45,0),(360,-45,0),(360,-184.29,0),(393.033,-216.967,0),(410,-275,0),(410,-625,0),(393.033,-683.033,0),(360,-715.711,0),(360,-855,0),+1 more]
  Start = (6830,5565,0)
  Subdivisions = 0
FEATURE [Part::FeaturePython] Structure346  label="Структура007"  # Arch/BIM 52 (typed FeaturePython)
  FaceMaker = 0
  Height = 100
  HorizontalArea = 120171
  IfcData = attributes={"GlobalId": {"name": "GlobalId", "type": "IfcGloballyUniqueId", "is_enum": false, "enum_values": []}, "Description": {"... (+484 chars omitted),+1 more (map truncated)
  IfcType = 52
  Length = 0
  MoveBase = false
  MoveWithHost = false
  Nodes = (2) [(6380,5325,0),(6380,5325,100)]
  NodesOffset = 0
  Normal = (0,0,1)
  PerimeterLength = 1371.24
  Placement = pos=(0,0,900) rot=(0,0,1;0rad)
  VerticalArea = 137124
  Width = 100
FEATURE [Part::Box] Box3228  label="Ниша-дровник"
  AttacherType = Attacher::AttachEngine3D
  Height = 350
  Length = 700
  Placement = pos=(7285,2725,150) rot=(0,0,1;0rad)
  Width = 500
FEATURE [Part::Box] Box3229  label="шкаф 60 кухонный 013"
  AttacherType = Attacher::AttachEngine3D
  Height = 850
  Length = 600
  Placement = pos=(7435,1785,1600) rot=(0,0,-1;1.5708rad)
  Width = 600
FEATURE [Part::Box] Box3230  label="шкаф 60 кухонный 001"
  AttacherType = Attacher::AttachEngine3D
  Height = 1600
  Length = 600
  Placement = pos=(7435,1785,0) rot=(0,0,-1;1.5708rad)
  Width = 600
FEATURE [Part::Box] Box3231  label="МВ_001"
  AttacherType = Attacher::AttachEngine3D
  Height = 350
  Length = 500
  Placement = pos=(8035,1775,1000) rot=(0,0,1;3.14159rad)
  Width = 580
FEATURE [Part::Box] Box3232  label="МВ_002"
  AttacherType = Attacher::AttachEngine3D
  Height = 350
  Length = 500
  Placement = pos=(7535,1195,1000) rot=(0,0,1;0rad)
  Width = 580
FEATURE [Part::Box] Box3233  label="ДШ_002"
  AttacherType = Attacher::AttachEngine3D
  Height = 500
  Length = 500
  Placement = pos=(7535,1195,450) rot=(0,0,1;0rad)
  Width = 580
FEATURE [Part::Part2DObjectPython] Wire817  label="кровля_контур_обрезки"  # Draft 2D object (typed FeaturePython)
  Area = 0
  ChamferSize = 0
  Closed = true
  End = (3495,-1255,0)
  FilletRadius = 0
  Length = 50640
  MakeFace = false
  Placement = pos=(-1210,-1210,0) rot=(0,0,1;0rad)
  Points = (12) [(-50,-45,0),(-50,10835,0),(7565,10835,0),(7565,11510,0),(11665,11510,0),(11665,10835,0),(13040,10835,0),(13040,-45,0),(8285,-45,0),(8285,-720,0),+2 more]
  Start = (-1260,-1255,0)
  Subdivisions = 0
FEATURE [Part::Part2DObjectPython] Rectangle3216  # Draft 2D object (typed FeaturePython)
  Area = 0
  ChamferSize = 0
  Columns = 1
  FilletRadius = 0
  Height = 5500
  Length = 13500
  MakeFace = false
  Placement = pos=(-1465,1435,0) rot=(0,0,-1;0rad)
  Rows = 1
FEATURE [Part::FeaturePython] Structure360  label="Вентстояк вычитаемы объём 003"  # Arch/BIM 52 (typed FeaturePython)
  FaceMaker = 0
  GlobalId = 0eTNl8duH9Xv7LHx2JWCfz
  Height = 8000
  HorizontalArea = 561600
  IfcData = IfcUID=0eTNl8duH9Xv7LHx2JWCfz,attributes={"GlobalId": {"value": "0eTNl8duH9Xv7LHx2JWCfz"}},+1 more (map truncated)
  IfcType = 52
  Length = 0
  MoveBase = false
  MoveWithHost = false
  Nodes = (2) [(4985,3930,0),(4985,3930,6000)]
  NodesOffset = 0
  Normal = (0,0,0)
  PerimeterLength = 3840
  Placement = pos=(0,0,-200) rot=(0,0,1;0rad)
  VerticalArea = 3.072e+07
  Width = 100
FEATURE [Part::Part2DObjectPython] Line1465  # Draft 2D object (typed FeaturePython)
  Area = 0
  ChamferSize = 0
  Closed = true
  End = (8191.11,4054.69,3200)
  FilletRadius = 0
  Length = 3200
  MakeFace = true
  Placement = pos=(7846.11,4054.69,0) rot=(0,0,1;0rad)
  Points = (2) [(345,1.81899e-12,0),(345,1.81899e-12,3200)]
  Start = (8191.11,4054.69,0)
  Subdivisions = 0
FEATURE [Part::Part2DObjectPython] Rectangle3284  # Draft 2D object (typed FeaturePython)
  Area = 0
  ChamferSize = 0
  Columns = 1
  FilletRadius = 0
  Height = 11690
  Length = 3590
  MakeFace = false
  Placement = pos=(-560,5980,0) rot=(0,0,-1;1.5708rad)
  Rows = 1
FEATURE [Part::Part2DObjectPython] Line1478  # Draft 2D object (typed FeaturePython)
  Area = 0
  ChamferSize = 0
  Closed = true
  End = (8915,2029.8,6981)
  FilletRadius = 0
  Length = 0
  MakeFace = false
  Placement = pos=(8915,2029.8,6981) rot=(0,0,1;0rad)
  Points = (2) [(0,0,0),(0,0,0)]
  Start = (8915,2029.8,6981)
  Subdivisions = 0
FEATURE [Part::Part2DObjectPython] Line1479  # Draft 2D object (typed FeaturePython)
  Area = 0
  ChamferSize = 0
  Closed = true
  End = (10270,682.149,2381)
  FilletRadius = 0
  Length = 400
  MakeFace = false
  Placement = pos=(10270,682.149,6981) rot=(0,0,1;0rad)
  Points = (2) [(0,2.50111e-12,-5000),(0,2.27374e-12,-4600)]
  Start = (10270,682.149,1981)
  Subdivisions = 0
FEATURE [Part::Part2DObjectPython] Line1481  # Draft 2D object (typed FeaturePython)
  Area = 0
  ChamferSize = 0
  Closed = false
  End = (9448,-1570,3275.2)
  FilletRadius = 0
  Length = 6000
  MakeFace = false
  Placement = pos=(3448,-1570,3275.2) rot=(1,0,0;0.610865rad)
  Points = (2) [(0,0,0),(6000,0,1.36424e-12)]
  Start = (3448,-1570,3275.2)
  Subdivisions = 0
FEATURE [Part::Part2DObjectPython] Line1482  # Draft 2D object (typed FeaturePython)
  Area = 0
  ChamferSize = 0
  Closed = false
  End = (9448,-1447.13,3361.23)
  FilletRadius = 0
  Length = 6000
  MakeFace = false
  Placement = pos=(3448,-1447.13,3361.23) rot=(1,0,0;0.610865rad)
  Points = (2) [(0,0,0),(6000,2.27374e-13,-9.09495e-13)]
  Start = (3448,-1447.13,3361.23)
  Subdivisions = 0
FEATURE [Part::Part2DObjectPython] Line1483  # Draft 2D object (typed FeaturePython)
  Area = 0
  ChamferSize = 0
  Closed = false
  End = (9448,-1447.13,3461.23)
  FilletRadius = 0
  Length = 6000
  MakeFace = false
  Placement = pos=(3448,-1447.13,3461.23) rot=(1,0,0;0.610865rad)
  Points = (2) [(0,0,0),(6000,2.27374e-13,-9.09495e-13)]
  Start = (3448,-1447.13,3461.23)
  Subdivisions = 0
FEATURE [Part::Part2DObjectPython] Line1484  # Draft 2D object (typed FeaturePython)
  Area = 0
  ChamferSize = 0
  Closed = false
  End = (9448,-1570,3375.2)
  FilletRadius = 0
  Length = 6000
  MakeFace = false
  Placement = pos=(3448,-1570,3375.2) rot=(1,0,0;0.610865rad)
  Points = (2) [(0,0,0),(6000,0,0)]
  Start = (3448,-1570,3375.2)
  Subdivisions = 0
FEATURE [Part::FeaturePython] Pipe014  label="Снегозадержатели 010"  # Arch/BIM 98 (typed FeaturePython)
  Base = -> Line1481
  Diameter = 25
  GlobalId = 3FGB4W65b7$RelxxBEC_I3
  HorizontalArea = 0
  IfcData = IfcUID=3FGB4W65b7$RelxxBEC_I3,+2 more (map truncated)
  IfcType = 98
  Length = 6000
  MoveBase = false
  MoveWithHost = false
  OffsetEnd = 0
  OffsetStart = 0
  PerimeterLength = 0
  Placement = pos=(0,0,50) rot=(0,0,1;0rad)
  PredefinedType = 0
  VerticalArea = 0
  WallThickness = 0
FEATURE [Part::FeaturePython] Pipe015  label="Снегозадержатели 011"  # Arch/BIM 98 (typed FeaturePython)
  Base = -> Line1482
  Diameter = 25
  GlobalId = 0m162zSxL9MvR8JxGsHhMh
  HorizontalArea = 0
  IfcData = IfcUID=0m162zSxL9MvR8JxGsHhMh,+2 more (map truncated)
  IfcType = 98
  Length = 6000
  MoveBase = false
  MoveWithHost = false
  OffsetEnd = 0
  OffsetStart = 0
  PerimeterLength = 0
  Placement = pos=(0,0,50) rot=(0,0,1;0rad)
  PredefinedType = 0
  VerticalArea = 0
  WallThickness = 0
FEATURE [Part::FeaturePython] Pipe016  label="Снегозадержатели 012"  # Arch/BIM 98 (typed FeaturePython)
  Base = -> Line1483
  Diameter = 25
  GlobalId = 1BHvc1NuD0qQo1xGtb2qrX
  HorizontalArea = 0
  IfcData = IfcUID=1BHvc1NuD0qQo1xGtb2qrX,+2 more (map truncated)
  IfcType = 98
  Length = 6000
  MoveBase = false
  MoveWithHost = false
  OffsetEnd = 0
  OffsetStart = 0
  PerimeterLength = 0
  Placement = pos=(0,0,50) rot=(0,0,1;0rad)
  PredefinedType = 0
  VerticalArea = 0
  WallThickness = 0
FEATURE [Part::FeaturePython] Pipe017  label="Снегозадержатели 001"  # Arch/BIM 98 (typed FeaturePython)
  Base = -> Line1484
  Diameter = 25
  GlobalId = 3Gvi8SLif8WfTz7jjSrXL2
  HorizontalArea = 0
  IfcData = IfcUID=3Gvi8SLif8WfTz7jjSrXL2,+2 more (map truncated)
  IfcType = 98
  Length = 6000
  MoveBase = false
  MoveWithHost = false
  OffsetEnd = 0
  OffsetStart = 0
  PerimeterLength = 0
  Placement = pos=(0,0,50) rot=(0,0,1;0rad)
  PredefinedType = 0
  VerticalArea = 0
  WallThickness = 0
FEATURE [Part::Part2DObjectPython] Line1486  # Draft 2D object (typed FeaturePython)
  Area = 0
  ChamferSize = 0
  Closed = true
  End = (3835,9940,3275.2)
  FilletRadius = 0
  Length = 4460
  MakeFace = false
  Placement = pos=(8295,9940,3275.2) rot=(0,0.300706,0.953717;3.14159rad)
  Points = (2) [(0,0,0),(4460,-5.92209e-05,-8.45762e-05)]
  Start = (8295,9940,3275.2)
  Subdivisions = 0
FEATURE [Part::Part2DObjectPython] Line1487  # Draft 2D object (typed FeaturePython)
  Area = 0
  ChamferSize = 0
  Closed = false
  End = (3835,9817.13,3361.23)
  FilletRadius = 0
  Length = 4460
  MakeFace = false
  Placement = pos=(8295,9817.13,3361.23) rot=(0,0.300706,0.953717;3.14159rad)
  Points = (2) [(0,0,0),(4460,0,0)]
  Start = (8295,9817.13,3361.23)
  Subdivisions = 0
FEATURE [Part::Part2DObjectPython] Line1488  # Draft 2D object (typed FeaturePython)
  Area = 0
  ChamferSize = 0
  Closed = false
  End = (3835,9817.13,3461.23)
  FilletRadius = 0
  Length = 4460
  MakeFace = false
  Placement = pos=(8295,9817.13,3461.23) rot=(0,0.300706,0.953717;3.14159rad)
  Points = (2) [(0,0,0),(4460,1.81899e-12,-1.81899e-12)]
  Start = (8295,9817.13,3461.23)
  Subdivisions = 0
FEATURE [Part::Part2DObjectPython] Line1489  # Draft 2D object (typed FeaturePython)
  Area = 0
  ChamferSize = 0
  Closed = false
  End = (3835,9940,3375.2)
  FilletRadius = 0
  Length = 4460
  MakeFace = false
  Placement = pos=(8295,9940,3375.2) rot=(0,0.300706,0.953717;3.14159rad)
  Points = (2) [(0,0,0),(4460,0,0)]
  Start = (8295,9940,3375.2)
  Subdivisions = 0
FEATURE [Part::FeaturePython] Pipe018  label="Снегозадержатели 013"  # Arch/BIM 98 (typed FeaturePython)
  Base = -> Line1486
  Diameter = 25
  GlobalId = 0psA13S1r3kfjsLgw5ftBB
  HorizontalArea = 0
  IfcData = IfcUID=0psA13S1r3kfjsLgw5ftBB,+2 more (map truncated)
  IfcType = 98
  Length = 4460
  MoveBase = false
  MoveWithHost = false
  OffsetEnd = 0
  OffsetStart = 0
  PerimeterLength = 0
  Placement = pos=(0,0,50) rot=(0,0,1;0rad)
  PredefinedType = 0
  VerticalArea = 0
  WallThickness = 0
FEATURE [Part::FeaturePython] Pipe019  label="Снегозадержатели 014"  # Arch/BIM 98 (typed FeaturePython)
  Base = -> Line1487
  Diameter = 25
  GlobalId = 1ajV3GjIH90PewpSEaAIL9
  HorizontalArea = 0
  IfcData = IfcUID=1ajV3GjIH90PewpSEaAIL9,+2 more (map truncated)
  IfcType = 98
  Length = 4460
  MoveBase = false
  MoveWithHost = false
  OffsetEnd = 0
  OffsetStart = 0
  PerimeterLength = 0
  Placement = pos=(0,0,50) rot=(0,0,1;0rad)
  PredefinedType = 0
  VerticalArea = 0
  WallThickness = 0
FEATURE [Part::FeaturePython] Pipe020  label="Снегозадержатели 015"  # Arch/BIM 98 (typed FeaturePython)
  Base = -> Line1488
  Diameter = 25
  GlobalId = 3F76V0rxL2cvmgn6TVRcv1
  HorizontalArea = 0
  IfcData = IfcUID=3F76V0rxL2cvmgn6TVRcv1,+2 more (map truncated)
  IfcType = 98
  Length = 4460
  MoveBase = false
  MoveWithHost = false
  OffsetEnd = 0
  OffsetStart = 0
  PerimeterLength = 0
  Placement = pos=(0,0,50) rot=(0,0,1;0rad)
  PredefinedType = 0
  VerticalArea = 0
  WallThickness = 0
FEATURE [Part::FeaturePython] Pipe021  label="Снегозадержатели 016"  # Arch/BIM 98 (typed FeaturePython)
  Base = -> Line1489
  Diameter = 25
  GlobalId = 2T$R0KaZDBcBfa4GgFt7Wm
  HorizontalArea = 0
  IfcData = IfcUID=2T$R0KaZDBcBfa4GgFt7Wm,+2 more (map truncated)
  IfcType = 98
  Length = 4460
  MoveBase = false
  MoveWithHost = false
  OffsetEnd = 0
  OffsetStart = 0
  PerimeterLength = 0
  Placement = pos=(0,0,50) rot=(0,0,1;0rad)
  PredefinedType = 0
  VerticalArea = 0
  WallThickness = 0
FEATURE [App::FeaturePython] Dimension024  # Draft dimension (typed FeaturePython)
  Diameter = false
  Dimline = (4200,3400,0)
  Direction = (0,0,0)
  Distance = 900
  End = (4455,3205,0)
  Normal = (0,0,1)
  Start = (3555,3205,0)
FEATURE [TechDraw::DrawSVGTemplate] Template001
  EditableTexts = Лист=6; Номер=ИЖС-2022.0003
  Height = 297
  Orientation = 1
  Width = 420
FEATURE [App::MaterialObjectPython] Material  label="Wood"  # material (typed FeaturePython)
  Description = A standard construction wood
  Material = AuthorAndLicense=Wood-Generic,CardName=Wood-Generic,Color=(1.0, 0.8196078431372549, 0.0, 1.0),Density=700 kg/m^3,+10 more (map truncated)
  ProductURL = https://en.wikipedia.org/wiki/Wood
  Transparency = 0
FEATURE [App::MaterialObjectPython] Material001  label="Concrete"  # material (typed FeaturePython)
  Description = A standard C-25 construction concrete
  Material = AuthorAndLicense=Concrete-Generic,CardName=Concrete-Generic,Color=(0.47058823529411764, 0.4627450980392157, 0.4627450980392157, 1.0),+13 more (map truncated)
  ProductURL = https://en.wikipedia.org/wiki/Concrete
  StandardCode = Masterformat 03 33 13
  Transparency = 50
FEATURE [App::MaterialObjectPython] Material002  label="XPS"  # material (typed FeaturePython)
  Description = XPS
  Material = AuthorAndLicense=ABS-Generic,CardName=ABS-Generic,Color=(0.9411764705882353, 0.5450980392156862, 0.5686274509803921, 1.0),Density=1060 kg/m^3,+15 more (map truncated)
  Transparency = 0
FEATURE [App::MaterialObjectPython] Material003  label="Red brick"  # material (typed FeaturePython)
  Description = A standard red brick
  Material = AuthorAndLicense=Concrete-Generic,CardName=Concrete-Generic,Color=(0.788235294117647, 0.2980392156862745, 0.18823529411764706, 1.0),+11 more (map truncated)
  Transparency = 0
FEATURE [Part::FeaturePython] Wall121  label="Перемычка облицовки 015"  # Arch/BIM 166 (typed FeaturePython)
  Align = 2
  Area = 1410000
  Base = -> Line1186
  BlockHeight = 250
  BlockLength = 66.7
  CountBroken = 51
  CountEntire = 47
  Face = 0
  GlobalId = 3Y7MnwAmX628ZvBXKl4dyB
  Height = 375
  HorizontalArea = 0
  IfcData = IfcUID=3Y7MnwAmX628ZvBXKl4dyB; attributes={"GlobalId": {"value": "3Y7MnwAmX628ZvBXKl4dyB"}}
  IfcType = 166
  Joint = 10
  Length = 3760
  MakeBlocks = true
  Material = -> Material003
  MoveBase = false
  MoveWithHost = false
  Normal = (0,0,1)
  OffsetFirst = 0
  OffsetSecond = 0
  PerimeterLength = 0
  Placement = pos=(0,0,2495) rot=(0,0,1;0rad)
  PredefinedType = 0
  VerticalArea = 0
  Width = 10
FEATURE [Part::FeaturePython] Wall123  label="Перемычка облицовки 017"  # Arch/BIM 166 (typed FeaturePython)
  Align = 2
  Area = 288750
  Base = -> Line1184
  BlockHeight = 250
  BlockLength = 66
  CountBroken = 12
  CountEntire = 8
  Face = 0
  GlobalId = 3lCsDqyJL5KvboFIYAEUQo
  Height = 375
  HorizontalArea = 0
  IfcData = IfcUID=3lCsDqyJL5KvboFIYAEUQo; attributes={"GlobalId": {"value": "3lCsDqyJL5KvboFIYAEUQo"}}
  IfcType = 166
  Joint = 10
  Length = 770
  MakeBlocks = true
  Material = -> Material003
  MoveBase = false
  MoveWithHost = false
  Normal = (0,0,1)
  OffsetFirst = 0
  OffsetSecond = 0
  PerimeterLength = 0
  Placement = pos=(0,0,2495) rot=(0,0,1;0rad)
  PredefinedType = 0
  VerticalArea = 0
  Width = 10
FEATURE [Part::FeaturePython] Wall124  label="Перемычка облицовки 018"  # Arch/BIM 166 (typed FeaturePython)
  Align = 2
  Area = 288750
  Base = -> Line1191
  BlockHeight = 250
  BlockLength = 66
  CountBroken = 12
  CountEntire = 8
  Face = 0
  GlobalId = 07ToIk0b17KwOPIvB7CAEx
  Height = 375
  HorizontalArea = 0
  IfcData = IfcUID=07ToIk0b17KwOPIvB7CAEx; attributes={"GlobalId": {"value": "07ToIk0b17KwOPIvB7CAEx"}}
  IfcType = 166
  Joint = 10
  Length = 770
  MakeBlocks = true
  Material = -> Material003
  MoveBase = false
  MoveWithHost = false
  Normal = (0,0,1)
  OffsetFirst = 0
  OffsetSecond = 0
  PerimeterLength = 0
  Placement = pos=(0,0,2495) rot=(0,0,1;0rad)
  PredefinedType = 0
  VerticalArea = 0
  Width = 10
FEATURE [Part::FeaturePython] Wall159  label="Перемычка облицовки 019"  # Arch/BIM 166 (typed FeaturePython)
  Align = 2
  Area = 678750
  Base = -> Line1266
  BlockHeight = 250
  BlockLength = 64
  CountBroken = 27
  CountEntire = 23
  Face = 0
  GlobalId = 0T7dyAI05B38PZhXyjg8rR
  Height = 375
  HorizontalArea = 0
  IfcData = IfcUID=0T7dyAI05B38PZhXyjg8rR; attributes={"GlobalId": {"value": "0T7dyAI05B38PZhXyjg8rR"}}
  IfcType = 166
  Joint = 10
  Length = 1810
  MakeBlocks = true
  Material = -> Material003
  MoveBase = false
  MoveWithHost = false
  Normal = (0,0,1)
  OffsetFirst = 0
  OffsetSecond = 0
  PerimeterLength = 0
  Placement = pos=(0,0,2495) rot=(0,0,1;0rad)
  PredefinedType = 0
  VerticalArea = 0
  Width = 10
FEATURE [App::MaterialObjectPython] Material004  label="Ceramic block"  # material (typed FeaturePython)
  Description = A standard Ceramic block LSR TK380
  Material = AuthorAndLicense=Concrete-Generic,CardName=Concrete-Generic,Color=(0.8627450980392157, 0.5803921568627451, 0.13725490196078433, 1.0),+11 more (map truncated)
  Transparency = 0
FEATURE [App::MaterialObjectPython] Material005  label="Wall ceramic plates"  # material (typed FeaturePython)
  Description = Wall ceramic plates
  Material = AuthorAndLicense=Concrete-Generic,CardName=Concrete-Generic,Color=(0.1450980392156863, 0.4745098039215686, 0.6980392156862745, 1.0),+11 more (map truncated)
  Transparency = 0
FEATURE [App::MaterialObjectPython] Material006  label="Glass mate"  # material (typed FeaturePython)
  Description = Generic soda-lime glass
  Material = AuthorAndLicense=Glass-Generic,CardName=Glass-Generic,Color=(0.8, 0.8, 0.8, 1.0),Density=2520 kg/m^3,Description=Generic soda-lime glass,+12 more (map truncated)
  ProductURL = https://en.wikipedia.org/wiki/Soda-lime_glass
  Transparency = 80
FEATURE [App::MaterialObjectPython] Material007  label="Stone wild"  # material (typed FeaturePython)
  Description = Stone wild
  Material = AuthorAndLicense=Concrete-Generic,CardName=Concrete-Generic,Color=(0.49019607843137253, 0.49019607843137253, 0.49019607843137253, 1.0),+11 more (map truncated)
  Transparency = 0
FEATURE [App::MaterialObjectPython] Material008  label="Wall cement"  # material (typed FeaturePython)
  Description = Wall cement
  Material = AuthorAndLicense=Concrete-Generic,CardName=Concrete-Generic,Color=(0.8, 0.8, 0.8, 1.0),CompressiveStrength=25 MPa,Density=2400 kg/m^3,+9 more (map truncated)
  Transparency = 0
FEATURE [App::MaterialObjectPython] Material009  label="Silicate blocks"  # material (typed FeaturePython)
  Description = Silicate blocks
  Material = AuthorAndLicense=Concrete-Generic,CardName=Concrete-Generic,Color=(0.8313725490196079, 0.7647058823529411, 0.7647058823529411, 1.0),+11 more (map truncated)
  Transparency = 0
FEATURE [Part::FeaturePython] Wall162  label="перегородка 042"  # Arch/BIM 166 (typed FeaturePython)
  Align = 2
  Area = 1.59e+06
  Base = -> Line1271
  BlockHeight = 250
  BlockLength = 0
  CountBroken = 0
  CountEntire = 0
  Face = 0
  Height = 3000
  HorizontalArea = 42400
  IfcType = 166
  Joint = 0
  Length = 530
  MakeBlocks = false
  Material = -> Material009
  MoveBase = false
  MoveWithHost = false
  Normal = (0,0,0)
  OffsetFirst = 0
  OffsetSecond = 300
  PerimeterLength = 1220
  Placement = pos=(0,0,-200) rot=(0,0,1;0rad)
  PredefinedType = 0
  VerticalArea = 3.66e+06
  Width = 80
FEATURE [Part::FeaturePython] Wall187  label="перегородка 044"  # Arch/BIM 166 (typed FeaturePython)
  Align = 2
  Area = 900000
  Base = -> Line1323
  BlockHeight = 250
  BlockLength = 0
  CountBroken = 0
  CountEntire = 0
  Face = 0
  Height = 3000
  HorizontalArea = 24000
  IfcType = 166
  Joint = 0
  Length = 300
  MakeBlocks = false
  Material = -> Material009
  MoveBase = false
  MoveWithHost = false
  Normal = (0,0,0)
  OffsetFirst = 0
  OffsetSecond = 300
  PerimeterLength = 760
  Placement = pos=(0,0,-200) rot=(0,0,1;0rad)
  PredefinedType = 0
  VerticalArea = 2280000
  Width = 80
FEATURE [Part::FeaturePython] Wall223  label="перегородка (сил.блок 500х250х80) 004"  # Arch/BIM 166 (typed FeaturePython)
  Align = 2
  Area = 2580000
  Base = -> Line1358
  BlockHeight = 250
  BlockLength = 0
  CountBroken = 0
  CountEntire = 0
  Face = 0
  GlobalId = 1OB118XG9DJPL5jtZdDHzR
  Height = 3000
  HorizontalArea = 68800
  IfcData = IfcUID=1OB118XG9DJPL5jtZdDHzR; attributes={"GlobalId": {"value": "1OB118XG9DJPL5jtZdDHzR"}}
  IfcType = 166
  Joint = 0
  Length = 860
  MakeBlocks = false
  Material = -> Material009
  MoveBase = false
  MoveWithHost = false
  Normal = (0,0,0)
  OffsetFirst = 300
  OffsetSecond = 50
  PerimeterLength = 1880
  Placement = pos=(0,0,-200) rot=(0,0,1;0rad)
  PredefinedType = 0
  VerticalArea = 5640000
  Width = 80
FEATURE [Part::FeaturePython] Wall225  label="перегородка 052"  # Arch/BIM 166 (typed FeaturePython)
  Align = 2
  Area = 2400000
  Base = -> Line1360
  BlockHeight = 250
  BlockLength = 0
  CountBroken = 0
  CountEntire = 0
  Face = 0
  Height = 3000
  HorizontalArea = 64000
  IfcType = 166
  Joint = 0
  Length = 800
  MakeBlocks = false
  Material = -> Material009
  MoveBase = false
  MoveWithHost = false
  Normal = (0,0,0)
  OffsetFirst = 0
  OffsetSecond = 300
  PerimeterLength = 1760
  Placement = pos=(0,0,-200) rot=(0,0,1;0rad)
  PredefinedType = 0
  VerticalArea = 5280000
  Width = 80
FEATURE [Part::FeaturePython] Wall230  label="перегородка (сил.блок 500х250х80) 006"  # Arch/BIM 166 (typed FeaturePython)
  Align = 2
  Area = 7290000
  Base = -> Line1390
  BlockHeight = 250
  BlockLength = 0
  CountBroken = 0
  CountEntire = 0
  Face = 0
  Height = 3000
  HorizontalArea = 194400
  IfcType = 166
  Joint = 0
  Length = 2430
  MakeBlocks = false
  Material = -> Material009
  MoveBase = false
  MoveWithHost = false
  Normal = (0,0,0)
  OffsetFirst = 300
  OffsetSecond = 50
  PerimeterLength = 5020
  Placement = pos=(0,0,-200) rot=(0,0,1;0rad)
  PredefinedType = 0
  VerticalArea = 15060000
  Width = 80
FEATURE [App::MaterialObjectPython] Material010  label="Steel-Generic"  # material (typed FeaturePython)
  Description = This is a blend Steel material card. The values are at the low end of the spectrum. If you need a more precise material definition use the more specialised steel cards.
  Material = AuthorAndLicense=Steel-Generic,CardName=Steel-Generic,Color=(0.3803921568627451, 0.3803921568627451, 0.3803921568627451, 1.0),Density=7900 kg/m^3,+13 more (map truncated)
  ProductURL = https://en.wikipedia.org/wiki/Steel
  Transparency = 0
FEATURE [Part::FeaturePython] Pipe008  label="Дымоход 120 коакс."  # Arch/BIM 98 (typed FeaturePython)
  Base = -> Line1479
  Diameter = 120
  GlobalId = 11JHR0lR55LRzzbgV05jpw
  HorizontalArea = 0
  IfcData = IfcUID=11JHR0lR55LRzzbgV05jpw,+2 more (map truncated)
  IfcType = 98
  Length = 400
  Material = -> Material010
  MoveBase = false
  MoveWithHost = false
  OffsetEnd = 0
  OffsetStart = 0
  PerimeterLength = 0
  Placement = pos=(-3385,1312.85,0) rot=(0,0,1;0rad)
  PredefinedType = 0
  VerticalArea = 0
  WallThickness = 0
FEATURE [App::MaterialObjectPython] Material011  label="Polypropylene"  # material (typed FeaturePython)
  Material = AuthorAndLicense=PP-Generic,CardName=PP-Generic,Color=(0.38823529411764707, 0.38823529411764707, 0.38823529411764707, 1.0),CompressiveStrength=10 MPa,+15 more (map truncated)
  ProductURL = https://en.wikipedia.org/wiki/Polypropylene
  Transparency = 0
FEATURE [Part::FeaturePython] Window020  label="Д-90-004"  # Arch/BIM 41 (typed FeaturePython)
  Area = 2160000
  Base = -> Sketch248
  Frame = 50
  GlobalId = 00iW5F1Zz0_RepVZ61wedb
  Height = 2400
  HoleDepth = 0
  HoleWire = 0
  HorizontalArea = 0
  IfcData = IfcUID=00iW5F1Zz0_RepVZ61wedb; attributes={"OverallHeight": {"value": 2400.0}, "OverallWidth": {"value": 900.0}, "GlobalId": {"value": "00iW5F1Zz0_RepVZ61wedb"}}
  IfcType = 41
  LouvreSpacing = 0
  LouvreWidth = 0
  Material = -> Material011
  MoveBase = false
  MoveWithHost = true
  Normal = (0,1,0)
  Opening = 0
  OperationType = 0
  OverallHeight = 2400
  OverallWidth = 900
  PerimeterLength = 0
  Placement = pos=(0,25,0) rot=(0,0,1;0rad)
  PredefinedType = 0
  Preset = 6
  SymbolElevation = false
  SymbolPlan = false
  VerticalArea = 0
  Width = 900
  WindowParts = OuterFrame | Frame | Wire0,Wire1 | 0.0+V | 0.00+V | Door | Solid panel | Wire1 | 50.0 | 0.0+V
  expr: OverallHeight = .Height.Value
  expr: OverallWidth = .Width.Value
FEATURE [Part::FeaturePython] Window021  label="Д-90-003"  # Arch/BIM 41 (typed FeaturePython)
  Area = 2160000
  Base = -> Sketch251
  Frame = 50
  GlobalId = 29QgZPyov5qAVey2RViV7P
  Height = 2400
  HoleDepth = 0
  HoleWire = 0
  HorizontalArea = 0
  IfcData = IfcUID=29QgZPyov5qAVey2RViV7P; attributes={"OverallHeight": {"value": 2400.0}, "OverallWidth": {"value": 900.0}, "GlobalId": {"value": "29QgZPyov5qAVey2RViV7P"}}
  IfcType = 41
  LouvreSpacing = 0
  LouvreWidth = 0
  Material = -> Material011
  MoveBase = false
  MoveWithHost = true
  Normal = (1,0,0)
  Opening = 0
  OperationType = 0
  OverallHeight = 2400
  OverallWidth = 900
  PerimeterLength = 0
  Placement = pos=(25,0,0) rot=(0,0,1;0rad)
  PredefinedType = 0
  Preset = 6
  SymbolElevation = false
  SymbolPlan = false
  VerticalArea = 0
  Width = 900
  WindowParts = OuterFrame | Frame | Wire0,Wire1 | 0.0+V | 0.00+V | Door | Solid panel | Wire1 | 50.0 | 0.0+V
  expr: OverallHeight = .Height.Value
  expr: OverallWidth = .Width.Value
FEATURE [Part::FeaturePython] Window026  label="Д-90-002"  # Arch/BIM 41 (typed FeaturePython)
  Area = 2160000
  Base = -> Sketch260
  Frame = 50
  GlobalId = 3IW9J8Pfn69QiBWvx91KEB
  Height = 2400
  HoleDepth = 0
  HoleWire = 0
  HorizontalArea = 0
  IfcData = IfcUID=3IW9J8Pfn69QiBWvx91KEB; attributes={"OverallHeight": {"value": 2400.0}, "OverallWidth": {"value": 900.0}, "GlobalId": {"value": "3IW9J8Pfn69QiBWvx91KEB"}}
  IfcType = 41
  LouvreSpacing = 0
  LouvreWidth = 0
  Material = -> Material011
  MoveBase = false
  MoveWithHost = true
  Normal = (0,1,0)
  Opening = 0
  OperationType = 0
  OverallHeight = 2400
  OverallWidth = 900
  PerimeterLength = 0
  Placement = pos=(0,30,180) rot=(0,0,1;0rad)
  PredefinedType = 0
  Preset = 6
  SymbolElevation = false
  SymbolPlan = false
  VerticalArea = 0
  Width = 900
  WindowParts = OuterFrame | Frame | Wire0,Wire1 | 0.0+V | 0.00+V | Door | Solid panel | Wire1 | 50.0 | 0.0+V
  expr: OverallHeight = .Height.Value
  expr: OverallWidth = .Width.Value
FEATURE [Part::FeaturePython] Window052  label="Д-90-001"  # Arch/BIM 41 (typed FeaturePython)
  Area = 1890000
  Base = -> Sketch309
  Frame = 50
  GlobalId = 1cijn4gZv3rAlY7HDrqfh6
  Height = 2100
  HoleDepth = 0
  HoleWire = 0
  HorizontalArea = 0
  IfcData = IfcUID=1cijn4gZv3rAlY7HDrqfh6; attributes={"OverallHeight": {"value": 2100.0}, "OverallWidth": {"value": 900.0}, "GlobalId": {"value": "1cijn4gZv3rAlY7HDrqfh6"}}
  IfcType = 41
  LouvreSpacing = 0
  LouvreWidth = 0
  Material = -> Material011
  MoveBase = false
  MoveWithHost = true
  Normal = (-1,0,0)
  Opening = 0
  OperationType = 0
  OverallHeight = 2100
  OverallWidth = 900
  PerimeterLength = 0
  Placement = pos=(50,1.819e-12,0) rot=(0,0,1;0rad)
  PredefinedType = 0
  Preset = 6
  SymbolElevation = false
  SymbolPlan = false
  VerticalArea = 0
  Width = 900
  WindowParts = OuterFrame | Frame | Wire0,Wire1 | 0.0+V | 0.00+V | Door | Solid panel | Wire1 | 50.0 | 0.0+V
  expr: OverallWidth = .Width.Value
  expr: OverallHeight = .Height.Value
FEATURE [Part::FeaturePython] Structure384  label="Вентстояк вычитаемы объём 007"  # Arch/BIM 52 (typed FeaturePython)
  FaceMaker = 0
  Height = 4000
  HorizontalArea = 1.1584e+06
  IfcData = complex_attributes={"OwnerHistory": {}, "IsNestedBy": {}, "IsDecomposedBy": {}, "IsDefinedBy": {}, "ObjectPlacement": {}, "Representation":... (+4 chars omitted)
  IfcType = 52
  Length = 0
  MoveBase = false
  MoveWithHost = false
  Nodes = (2) [(7235,1875,0),(7235,1875,4000)]
  NodesOffset = 0
  Normal = (0,0,0)
  PerimeterLength = 4900
  Placement = pos=(0,0,2800) rot=(0,0,1;0rad)
  VerticalArea = 19600000
  Width = 100
FEATURE [Part::Part2DObjectPython] Line1532  label="Перемычки_042"  # Draft 2D object (typed FeaturePython)
  Area = 0
  ChamferSize = 0
  Closed = true
  End = (10067.5,3080,0)
  FilletRadius = 0
  Length = 3110
  MakeFace = true
  Placement = pos=(6306.5,3080,0) rot=(0,0,1;0rad)
  Points = (2) [(651,0,0),(3761,0,0)]
  Start = (6957.5,3080,0)
  Subdivisions = 0
FEATURE [Part::Part2DObjectPython] Line1533  label="Перемычки_043"  # Draft 2D object (typed FeaturePython)
  Area = 0
  ChamferSize = 0
  Closed = true
  End = (6295,3080,0)
  FilletRadius = 0
  Length = 2070
  MakeFace = true
  Placement = pos=(3574,3080,0) rot=(0,0,1;0rad)
  Points = (2) [(651,0,0),(2721,0,0)]
  Start = (4225,3080,0)
  Subdivisions = 0
FEATURE [Part::Part2DObjectPython] Line1540  label="Перемычки_048"  # Draft 2D object (typed FeaturePython)
  Area = 0
  ChamferSize = 0
  Closed = true
  End = (3680,8470,0)
  FilletRadius = 0
  Length = 1290
  MakeFace = true
  Placement = pos=(3680,7097,0) rot=(0,0,1;1.5708rad)
  Points = (2) [(83,1.36424e-12,0),(1373,0,0)]
  Start = (3680,7180,0)
  Subdivisions = 0
FEATURE [Part::FeaturePython] Wall277  label="Перемычка 5ПБ 31-27 001"  # Arch/BIM 166 (typed FeaturePython)
  Align = 2
  Area = 684200
  Base = -> Line1532
  BlockHeight = 0
  BlockLength = 0
  CountBroken = 0
  CountEntire = 0
  Face = 0
  GlobalId = 0sYYehG3D7NAgPHO$7$lOP
  Height = 220
  HorizontalArea = 777500
  IfcData = IfcUID=0sYYehG3D7NAgPHO$7$lOP,+2 more (map truncated)
  IfcType = 166
  Joint = 0
  Length = 3110
  MakeBlocks = false
  Material = -> Material001
  MoveBase = false
  MoveWithHost = false
  Normal = (0,0,-1)
  OffsetFirst = 0
  OffsetSecond = 0
  PerimeterLength = 6720
  Placement = pos=(0,-1.819e-12,2800) rot=(0,0,1;0rad)
  PredefinedType = 0
  VerticalArea = 1478400
  Width = 250
FEATURE [Part::FeaturePython] Wall278  label="Перемычка 5ПБ 21-27 002"  # Arch/BIM 166 (typed FeaturePython)
  Align = 2
  Area = 455400
  Base = -> Line1533
  BlockHeight = 0
  BlockLength = 0
  CountBroken = 0
  CountEntire = 0
  Face = 0
  GlobalId = 0U$bER0DTA2wM7MkZ_5muC
  Height = 220
  HorizontalArea = 517500
  IfcData = IfcUID=0U$bER0DTA2wM7MkZ_5muC,+2 more (map truncated)
  IfcType = 166
  Joint = 0
  Length = 2070
  MakeBlocks = false
  Material = -> Material001
  MoveBase = false
  MoveWithHost = false
  Normal = (0,0,-1)
  OffsetFirst = 0
  OffsetSecond = 0
  PerimeterLength = 4640
  Placement = pos=(0,-1.819e-12,2800) rot=(0,0,1;0rad)
  PredefinedType = 0
  VerticalArea = 1020800
  Width = 250
FEATURE [Part::FeaturePython] Wall004  label="Несущая стена 2.1нф 250мм внутренняя 003"  # Arch/BIM 166 (typed FeaturePython)
  Align = 2
  Area = 2.0445e+07
  Base = -> Line1049
  BlockHeight = 231
  BlockLength = 0
  CountBroken = 0
  CountEntire = 0
  Face = 0
  GlobalId = 1uw9ZyZ5vAkuN6nr$sWkBP
  Height = 3000
  HorizontalArea = 0
  IfcData = IfcUID=1uw9ZyZ5vAkuN6nr$sWkBP; attributes={"GlobalId": {"value": "1uw9ZyZ5vAkuN6nr$sWkBP"}}
  IfcType = 166
  Joint = 0
  Length = 6815
  MakeBlocks = true
  Material = -> Material009
  MoveBase = false
  MoveWithHost = false
  Normal = (0,0,1)
  OffsetFirst = 0
  OffsetSecond = 500
  PerimeterLength = 0
  Placement = pos=(0,0,-200) rot=(0,0,1;0rad)
  PredefinedType = 0
  Subtractions = -> [Structure317,Structure020,Wall278,Wall277]
  VerticalArea = 0
  Width = 250
FEATURE [Part::FeaturePython] Wall281  label="Перем.2шт. 3ПБ 13-37 001"  # Arch/BIM 166 (typed FeaturePython)
  Align = 2
  Area = 283800
  Base = -> Line1540
  BlockHeight = 0
  BlockLength = 0
  CountBroken = 0
  CountEntire = 0
  Face = 0
  GlobalId = 0GYkMrihr4SvLL6ceY8F$x
  Height = 220
  HorizontalArea = 322500
  IfcData = IfcUID=0GYkMrihr4SvLL6ceY8F$x,+2 more (map truncated)
  IfcType = 166
  Joint = 0
  Length = 1290
  MakeBlocks = false
  Material = -> Material001
  MoveBase = false
  MoveWithHost = false
  Normal = (0,0,0)
  OffsetFirst = 0
  OffsetSecond = 0
  PerimeterLength = 3080
  Placement = pos=(-4.55e-13,-1.819e-12,2121) rot=(0,0,1;0rad)
  PredefinedType = 0
  VerticalArea = 677600
  Width = 250
FEATURE [TechDraw::DrawSVGTemplate] Template002
  EditableTexts = Лист=4; Номер=ИЖС-2022.0003
  Height = 297
  Orientation = 1
  Width = 420
FEATURE [App::FeaturePython] Dimension026  # Draft dimension (typed FeaturePython)
  Diameter = false
  Dimline = (4465.71,3338.72,0)
  Direction = (0,0,0)
  Distance = 1300
  End = (5890,3225,0)
  Normal = (0,0,1)
  Start = (4590,3225,0)
FEATURE [App::FeaturePython] Dimension027  # Draft dimension (typed FeaturePython)
  Diameter = false
  Dimline = (9700,3400,0)
  Direction = (0,0,0)
  Distance = 780
  End = (10600,3225,0)
  Normal = (0,0,1)
  Start = (9820,3225,0)
FEATURE [Part::Part2DObjectPython] Circle123  label="Circle124"  # Draft 2D object (typed FeaturePython)
  Area = 0
  FirstAngle = 0
  LastAngle = 0
  MakeFace = false
  Placement = pos=(-1854.18,8605,0) rot=(0,0,1;0rad)
  Radius = 200
FEATURE [Part::Part2DObjectPython] ShapeString193  # Draft 2D object (typed FeaturePython)
  FontFile = <path>
  Placement = pos=(-1950.61,8511.85,0) rot=(0,0,1;0rad)
  Size = 200
  String = C
  Tracking = 0
FEATURE [Part::Part2DObjectPython] Circle124  label="Circle125"  # Draft 2D object (typed FeaturePython)
  Area = 0
  FirstAngle = 0
  LastAngle = 0
  MakeFace = false
  Placement = pos=(-1854.18,3080,0) rot=(0,0,1;0rad)
  Radius = 200
FEATURE [Part::Part2DObjectPython] ShapeString194  # Draft 2D object (typed FeaturePython)
  FontFile = <path>
  Placement = pos=(-1933.86,2991.01,0) rot=(0,0,1;0rad)
  Size = 200
  String = B
  Tracking = 0
FEATURE [Part::Part2DObjectPython] Circle125  label="Circle126"  # Draft 2D object (typed FeaturePython)
  Area = 0
  FirstAngle = 0
  LastAngle = 0
  MakeFace = false
  Placement = pos=(-1854.18,-235,0) rot=(0,0,1;0rad)
  Radius = 200
FEATURE [Part::Part2DObjectPython] ShapeString195  # Draft 2D object (typed FeaturePython)
  FontFile = <path>
  Placement = pos=(-1941.5,-327.945,0) rot=(0,0,1;0rad)
  Size = 200
  String = A
  Tracking = 0
FEATURE [Part::Part2DObjectPython] Circle126  label="Circle127"  # Draft 2D object (typed FeaturePython)
  Area = 0
  FirstAngle = 0
  LastAngle = 0
  MakeFace = false
  Placement = pos=(-240,10797.3,0) rot=(0,0,1;0rad)
  Radius = 200
FEATURE [Part::Part2DObjectPython] ShapeString196  # Draft 2D object (typed FeaturePython)
  FontFile = <path>
  Placement = pos=(-319.076,10705,0) rot=(0,0,1;0rad)
  Size = 200
  String = 1
  Tracking = 0
FEATURE [Part::Part2DObjectPython] Circle127  label="Circle128"  # Draft 2D object (typed FeaturePython)
  Area = 0
  FirstAngle = 0
  LastAngle = 0
  MakeFace = false
  Placement = pos=(3680,10797.3,0) rot=(0,0,1;0rad)
  Radius = 200
FEATURE [Part::Part2DObjectPython] ShapeString197  # Draft 2D object (typed FeaturePython)
  FontFile = <path>
  Placement = pos=(3597.38,10713.8,0) rot=(0,0,1;0rad)
  Size = 200
  String = 2
  Tracking = 0
FEATURE [Part::Part2DObjectPython] Circle128  label="Circle129"  # Draft 2D object (typed FeaturePython)
  Area = 0
  FirstAngle = 0
  LastAngle = 0
  MakeFace = false
  Placement = pos=(6980,10797.3,0) rot=(0,0,1;0rad)
  Radius = 200
FEATURE [Part::Part2DObjectPython] ShapeString198  # Draft 2D object (typed FeaturePython)
  FontFile = <path>
  Placement = pos=(6908.07,10701.1,0) rot=(0,0,1;0rad)
  Size = 200
  String = 3
  Tracking = 0
FEATURE [Part::Part2DObjectPython] Circle129  label="Circle130"  # Draft 2D object (typed FeaturePython)
  Area = 0
  FirstAngle = 0
  LastAngle = 0
  MakeFace = false
  Placement = pos=(7230,10797.3,0) rot=(0,0,1;0rad)
  Radius = 200
FEATURE [Part::Part2DObjectPython] ShapeString199  # Draft 2D object (typed FeaturePython)
  FontFile = <path>
  Placement = pos=(7144.17,10703.7,0) rot=(0,0,1;0rad)
  Size = 200
  String = 4
  Tracking = 0
FEATURE [Part::Part2DObjectPython] Circle130  label="Circle131"  # Draft 2D object (typed FeaturePython)
  Area = 0
  FirstAngle = 0
  LastAngle = 0
  MakeFace = false
  Placement = pos=(10810,10797.3,0) rot=(0,0,1;0rad)
  Radius = 200
FEATURE [Part::Part2DObjectPython] ShapeString200  # Draft 2D object (typed FeaturePython)
  FontFile = <path>
  Placement = pos=(10740.3,10697.4,0) rot=(0,0,1;0rad)
  Size = 200
  String = 5
  Tracking = 0
FEATURE [TechDraw::DrawViewAnnotation] Annotation007
  Font = DejaVu Sans
  LineSpace = 80
  LockPosition = false
  MaxWidth = -1
  Rotation = 0
  ScaleType = 0
  Text = \u041f\u043b\u0430\u043d \u043f\u0435\u0440\u0432\u043e\u0433\u043e \u044d\u0442\u0430\u0436\u0430  \u043d\u0430 \u043e\u0442\u043c\u0435\u0442\u043a\u0435 +0.0
  TextSize = 6
  TextStyle = 0
  X = 335.399
  Y = 26.794
FEATURE [TechDraw::DrawViewAnnotation] Annotation008  label="Name001"
  Font = DejaVu Sans
  LineSpace = 80
  LockPosition = false
  MaxWidth = -1
  Rotation = 0
  ScaleType = 0
  Text = \u0420\u0430\u0437\u0440\u0435\u0437 \u043f\u043e \u0410-\u0410
  TextSize = 6
  TextStyle = 0
  X = 224.146
  Y = 272.252
FEATURE [App::FeaturePython] Dimension029  # Draft dimension (typed FeaturePython)
  Diameter = false
  Dimline = (0,5100,-400)
  Direction = (0,0,0)
  Distance = 200
  End = (0,8000,0)
  Normal = (1,0,0)
  Start = (0,8000,-200)
FEATURE [Part::Part2DObjectPython] Wire462  label="мауэрлат002"  # Draft 2D object (typed FeaturePython)
  ChamferSize = 0
  Closed = true
  End = (19975.3,6053.49,0)
  FilletRadius = 0
  Length = 12600
  MakeFace = false
  Placement = pos=(19796.7,2057.48,0) rot=(0,0,-1;1.61546rad)
  Points = (4) [(0,0,0),(0,2300,0),(-4000,2300,0),(-4000,-1.09139e-11,0)]
  Start = (19796.7,2057.48,0)
  Subdivisions = 0
FEATURE [Part::FeaturePython] Roof010  label="Крыша001"  # Arch/BIM 113 (typed FeaturePython)
  Angles = [90,14.6,90,14.6]
  Base = -> Wire462
  BorderLength = 15406.9
  Face = 0
  Flip = false
  Heights = [0,299.553,0,299.553]
  HorizontalArea = 1.26e+07
  IdRel = [0,0,0,0]
  IfcType = 113
  MoveBase = false
  MoveWithHost = false
  Overhang = [250,250,250,250]
  PerimeterLength = 14600
  Placement = pos=(0,0,2200) rot=(0,0,1;0rad)
  PredefinedType = 0
  RidgeLength = 10286.9
  Runs = [250,1150,250,1150]
  Thickness = [150,150,150,150]
  VerticalArea = 2.26308e+06
FEATURE [Part::Part2DObjectPython] Rectangle2373  # Draft 2D object (typed FeaturePython)
  ChamferSize = 0
  Columns = 1
  FilletRadius = 0
  Height = 150
  Length = 800
  MakeFace = true
  Placement = pos=(19854.7,3356.19,0) rot=(0,0,-1;1.61546rad)
  Rows = 1
FEATURE [Part::FeaturePython] Structure131  label="Structure130"  # Arch/BIM 52 (typed FeaturePython)
  Base = -> Rectangle2373
  FaceMaker = 0
  Height = 1800
  HorizontalArea = 120000
  IfcData = complex_attributes={"OwnerHistory": {}, "IsNestedBy": {}, "IsDecomposedBy": {}, "IsDefinedBy": {}, "ObjectPlacement": {}, "Representation":... (+4 chars omitted)
  IfcType = 52
  Length = 0
  MoveBase = false
  MoveWithHost = false
  Nodes = (2) [(-35.6948,-25773.1,0),(-35.6948,-25773.1,1800)]
  NodesOffset = 0
  Normal = (0,0,0)
  PerimeterLength = 1900
  VerticalArea = 3.42e+06
  Width = 100
FEATURE [Part::Part2DObjectPython] Rectangle2370  # Draft 2D object (typed FeaturePython)
  ChamferSize = 0
  Columns = 1
  FilletRadius = 0
  Height = 500
  Length = 150
  MakeFace = true
  Placement = pos=(20252.9,2187.24,0) rot=(0,0,-1;1.61546rad)
  Rows = 1
FEATURE [Part::FeaturePython] Structure130  label="Structure129"  # Arch/BIM 52 (typed FeaturePython)
  Base = -> Rectangle2370
  FaceMaker = 0
  Height = 600
  HorizontalArea = 75000
  IfcData = complex_attributes={"OwnerHistory": {}, "IsNestedBy": {}, "IsDecomposedBy": {}, "IsDefinedBy": {}, "ObjectPlacement": {}, "Representation":... (+4 chars omitted)
  IfcType = 52
  Length = 0
  MoveBase = false
  MoveWithHost = false
  Nodes = (2) [(-938.622,-26279,0),(-938.622,-26279,600)]
  NodesOffset = 0
  Normal = (0,0,0)
  PerimeterLength = 1300
  Placement = pos=(0,-4e-15,1240) rot=(0,0,1;0rad)
  VerticalArea = 780000
  Width = 100
FEATURE [Part::Part2DObjectPython] Rectangle2372  # Draft 2D object (typed FeaturePython)
  ChamferSize = 0
  Columns = 1
  FilletRadius = 0
  Height = 150
  Length = 500
  MakeFace = true
  Placement = pos=(19910.5,4604.94,0) rot=(0,0,-1;1.61546rad)
  Rows = 1
FEATURE [Part::FeaturePython] Structure128  label="Structure"  # Arch/BIM 52 (typed FeaturePython)
  Base = -> Rectangle2372
  FaceMaker = 0
  Height = 600
  HorizontalArea = 75000
  IfcData = complex_attributes={"OwnerHistory": {}, "IsNestedBy": {}, "IsDecomposedBy": {}, "IsDefinedBy": {}, "ObjectPlacement": {}, "Representation":... (+4 chars omitted)
  IfcType = 52
  Length = 0
  MoveBase = false
  MoveWithHost = false
  Nodes = (2) [(1351.07,-25965.1,0),(1351.07,-25965.1,600)]
  NodesOffset = 0
  Normal = (0,0,0)
  PerimeterLength = 1300
  Placement = pos=(0,-4e-15,1240) rot=(0,0,1;0rad)
  VerticalArea = 780000
  Width = 100
FEATURE [Part::Part2DObjectPython] Rectangle2368  # Draft 2D object (typed FeaturePython)
  ChamferSize = 0
  Columns = 1
  FilletRadius = 0
  Height = 2300
  Length = 4000
  MakeFace = false
  Placement = pos=(19975.3,6053.49,0) rot=(0,0,-1;1.61546rad)
  Rows = 1
FEATURE [Part::FeaturePython] Wall094  label="Wall005"  # Arch/BIM 166 (typed FeaturePython)
  Align = 1
  Area = 30870000
  Base = -> Rectangle2368
  BlockHeight = 0
  BlockLength = 0
  CountBroken = 0
  CountEntire = 0
  Face = 0
  Height = 2450
  HorizontalArea = 0
  IfcType = 166
  Joint = 0
  Length = 12600
  MakeBlocks = false
  MoveBase = false
  MoveWithHost = false
  Normal = (0,0,0)
  OffsetFirst = 0
  OffsetSecond = 0
  PerimeterLength = 0
  Placement = pos=(0,0,-150) rot=(0,0,1;0rad)
  PredefinedType = 0
  Subtractions = -> [Structure128,Structure130,Structure131]
  VerticalArea = 0
  Width = 150
FEATURE [Part::FeaturePython] Wall096  label="Wall006"  # Arch/BIM 166 (typed FeaturePython)
  Align = 0
  Area = 6300000
  Base = -> Rectangle2368
  BlockHeight = 0
  BlockLength = 0
  CountBroken = 0
  CountEntire = 0
  Face = 0
  Height = 500
  HorizontalArea = 1.18e+06
  IfcType = 166
  Joint = 0
  Length = 12600
  MakeBlocks = false
  MoveBase = false
  MoveWithHost = false
  Normal = (0,0,-1)
  Offset = 50
  OffsetFirst = 0
  OffsetSecond = 0
  PerimeterLength = 12200
  Placement = pos=(0,0,-150) rot=(0,0,1;0rad)
  PredefinedType = 0
  VerticalArea = 1.18e+07
  Width = 100
FEATURE [App::GeometryPython] BuildingPart032  label="Баня (перевозная)"  # Arch/BIM 10 (typed FeaturePython)
  Area = 37170000
  BuildingType = 0
  CompositionType = 0
  ElevationOfRefHeight = 0
  ElevationOfTerrain = 0
  Group = -> [Wall094,Roof010,Wall096]
  Height = 0
  HeightPropagate = true
  IfcType = 10
  LevelOffset = 0
  LongName = Баня (перевозная)
FEATURE [Part::Part2DObjectPython] Rectangle3343  label="Контур Строения001"  # Draft 2D object (typed FeaturePython)
  Area = 0
  ChamferSize = 0
  Columns = 1
  FilletRadius = 0
  Height = 9480
  Length = 11690
  MakeFace = false
  Placement = pos=(-560,-555,0) rot=(0,0,1;0rad)
  Rows = 1
FEATURE [App::FeaturePython] Text  label="1fl House"  # WARN: FeaturePython — macro-defined, semantics opaque (R4)
  Placement = pos=(60,-286,0) rot=(0,0,1;0rad)
FEATURE [Part::Feature] Human
  Placement = pos=(2300,-1000,-200) rot=(0,0,1;0rad)
  shape: bbox 490.6 x 1.43e-06 x 1712 mm, 1 faces, 0 solids (baked)
FEATURE [Part::FeaturePython] Axis001006  label="Горизонтальные оси"  # WARN: FeaturePython — macro-defined, semantics opaque (R4)
  Angles = [0,0,0]
  Distances = [320,3315,5525]
  Length = 13677.3
  Placement = pos=(12023.1,-555,0) rot=(0,0,1;1.5708rad)
  expr: .Placement.Base.y = Rectangle3343.Placement.Base.y
  expr: .Placement.Base.x = Rectangle3343.Placement.Base.x + Length * 0.92
  expr: Length = Rectangle3343.Length * 1.17
FEATURE [Part::FeaturePython] Axis001007  label="Вертикальные Оси"  # WARN: FeaturePython — macro-defined, semantics opaque (R4)
  Angles = [0,0,0,0,0]
  Distances = [320,3920,3300,250,3580]
  Length = 12892.8
  Placement = pos=(-560,-2295.53,0) rot=(0,0,1;0rad)
  expr: .Placement.Base.x = Rectangle3343.Placement.Base.x
  expr: .Placement.Base.y = Rectangle3343.Placement.Base.y - Length * 0.135
  expr: Length = Rectangle3343.Height * 1.36
FEATURE [App::FeaturePython] AxisSystem002  label="Оси 1й этаж"  # WARN: FeaturePython — macro-defined, semantics opaque (R4)
  Axes = -> [Axis001006,Axis001007]
FEATURE [App::DocumentObjectGroup] App__DocumentObjectGroup  label="Разметка Строения"
  Group = -> [Rectangle3343,Text,AxisSystem002]
FEATURE [Part::Part2DObjectPython] Line1583  label="облицовка_стены_032"  # Draft 2D object (typed FeaturePython)
  ChamferSize = 0
  Closed = true
  End = (11000,8925,0)
  FilletRadius = 0
  Length = 11560
  MakeFace = false
  Placement = pos=(-480,9475,0) rot=(0,0,1;0rad)
  Points = (2) [(-80,-550,0),(11480,-550,0)]
  Start = (-560,8925,0)
  Subdivisions = 0
FEATURE [Part::Part2DObjectPython] Line1584  label="облицовка_стены_033"  # Draft 2D object (typed FeaturePython)
  ChamferSize = 0
  Closed = true
  End = (-430,-555,0)
  FilletRadius = 0
  Length = 11430
  MakeFace = false
  Placement = pos=(12780,-555,0) rot=(0,0,1;0rad)
  Points = (2) [(-1780,2.84217e-12,0),(-13210,2.84217e-12,0)]
  Start = (11000,-555,0)
  Subdivisions = 0
FEATURE [Part::Part2DObjectPython] Line1585  label="облицовка_стены_034"  # Draft 2D object (typed FeaturePython)
  ChamferSize = 0
  Closed = true
  End = (-560,-555,0)
  FilletRadius = 0
  Length = 9350
  MakeFace = false
  Placement = pos=(-545,-765,0) rot=(0,0,1;0rad)
  Points = (2) [(-15,9560,0),(-15,210,0)]
  Start = (-560,8795,0)
  Subdivisions = 0
FEATURE [Part::Part2DObjectPython] Line1586  label="облицовка_стены_035"  # Draft 2D object (typed FeaturePython)
  ChamferSize = 0
  Closed = true
  End = (11130,8925,0)
  FilletRadius = 0
  Length = 9480
  MakeFace = false
  Placement = pos=(12865,4225,0) rot=(0,0,1;0rad)
  Points = (2) [(-1735,-4780,0),(-1735,4700,0)]
  Start = (11130,-555,0)
  Subdivisions = 0
FEATURE [Part::Part2DObjectPython] Line1587  label="контрфорс_линия_005"  # Draft 2D object (typed FeaturePython)
  ChamferSize = 0
  Closed = true
  End = (3730,-635,0)
  FilletRadius = 0
  Length = 380
  MakeFace = false
  Placement = pos=(3940,-635,0) rot=(0,0,1;0rad)
  Points = (2) [(170,1.02318e-12,0),(-210,9.09495e-13,0)]
  Start = (4110,-635,0)
  Subdivisions = 0
FEATURE [Part::FeaturePython] Wall306  label="Контрфорс 005"  # Arch/BIM 166 (typed FeaturePython)
  Align = 0
  Area = 702240
  Base = -> Line1587
  BlockHeight = 67
  BlockLength = 250
  CountBroken = 24
  CountEntire = 24
  Face = 0
  GlobalId = 342k6QohT2QOnSo3Rt4Yr5
  Height = 1848
  HorizontalArea = 0
  IfcData = IfcUID=342k6QohT2QOnSo3Rt4Yr5; attributes={"GlobalId": {"value": "342k6QohT2QOnSo3Rt4Yr5"}}
  IfcType = 166
  Joint = 10
  Length = 380
  MakeBlocks = true
  Material = -> Material003
  MoveBase = false
  MoveWithHost = false
  Normal = (0,0,0)
  OffsetFirst = 120
  OffsetSecond = 250
  PerimeterLength = 0
  Placement = pos=(0,0,185) rot=(0,0,1;0rad)
  PredefinedType = 0
  VerticalArea = 0
  Width = 120
FEATURE [Part::Part2DObjectPython] Line1588  label="контрфорс_линия_006"  # Draft 2D object (typed FeaturePython)
  ChamferSize = 0
  Closed = true
  End = (6460,-635,0)
  FilletRadius = 0
  Length = 380
  MakeFace = false
  Placement = pos=(6670,-635,0) rot=(0,0,1;0rad)
  Points = (2) [(170,1.02318e-12,0),(-210,9.09495e-13,0)]
  Start = (6840,-635,0)
  Subdivisions = 0
FEATURE [Part::FeaturePython] Wall307  label="Контрфорс 006"  # Arch/BIM 166 (typed FeaturePython)
  Align = 0
  Area = 702240
  Base = -> Line1588
  BlockHeight = 67
  BlockLength = 250
  CountBroken = 24
  CountEntire = 24
  Face = 0
  GlobalId = 2QQuq56G56SBKvMoDbUykg
  Height = 1848
  HorizontalArea = 0
  IfcData = IfcUID=2QQuq56G56SBKvMoDbUykg; attributes={"GlobalId": {"value": "2QQuq56G56SBKvMoDbUykg"}}
  IfcType = 166
  Joint = 10
  Length = 380
  MakeBlocks = true
  Material = -> Material003
  MoveBase = false
  MoveWithHost = false
  Normal = (0,0,0)
  OffsetFirst = 250
  OffsetSecond = 120
  PerimeterLength = 0
  Placement = pos=(0,0,185) rot=(0,0,1;0rad)
  PredefinedType = 0
  VerticalArea = 0
  Width = 120
FEATURE [Part::Part2DObjectPython] Line1589  label="контрфорс_линия_007"  # Draft 2D object (typed FeaturePython)
  ChamferSize = 0
  Closed = true
  End = (6590,9005,0)
  FilletRadius = 0
  Length = 380
  MakeFace = false
  Placement = pos=(6800,9005,0) rot=(0,0,1;0rad)
  Points = (2) [(170,0,0),(-210,0,0)]
  Start = (6970,9005,0)
  Subdivisions = 0
FEATURE [Part::FeaturePython] Wall308  label="Контрфорс 007"  # Arch/BIM 166 (typed FeaturePython)
  Align = 1
  Area = 702240
  Base = -> Line1589
  BlockHeight = 67
  BlockLength = 250
  CountBroken = 24
  CountEntire = 24
  Face = 0
  GlobalId = 3waotNP91F$e4vFRfeMs10
  Height = 1848
  HorizontalArea = 0
  IfcData = IfcUID=3waotNP91F$e4vFRfeMs10; attributes={"GlobalId": {"value": "3waotNP91F$e4vFRfeMs10"}}
  IfcType = 166
  Joint = 10
  Length = 380
  MakeBlocks = true
  Material = -> Material003
  MoveBase = false
  MoveWithHost = false
  Normal = (0,0,0)
  OffsetFirst = 120
  OffsetSecond = 250
  PerimeterLength = 0
  Placement = pos=(0,0,185) rot=(0,0,1;0rad)
  PredefinedType = 0
  VerticalArea = 0
  Width = 120
FEATURE [Part::Part2DObjectPython] Line1590  label="контрфорс_линия_008"  # Draft 2D object (typed FeaturePython)
  ChamferSize = 0
  Closed = true
  End = (9840,9005,0)
  FilletRadius = 0
  Length = 380
  MakeFace = false
  Placement = pos=(10050,9005,0) rot=(0,0,1;0rad)
  Points = (2) [(170,0,0),(-210,0,0)]
  Start = (10220,9005,0)
  Subdivisions = 0
FEATURE [Part::FeaturePython] Wall309  label="Контрфорс 008"  # Arch/BIM 166 (typed FeaturePython)
  Align = 1
  Area = 702240
  Base = -> Line1590
  BlockHeight = 67
  BlockLength = 250
  CountBroken = 24
  CountEntire = 24
  Face = 0
  GlobalId = 0Yg83kwN5EPeGAKGfacmqk
  Height = 1848
  HorizontalArea = 0
  IfcData = IfcUID=0Yg83kwN5EPeGAKGfacmqk; attributes={"GlobalId": {"value": "0Yg83kwN5EPeGAKGfacmqk"}}
  IfcType = 166
  Joint = 10
  Length = 380
  MakeBlocks = true
  Material = -> Material003
  MoveBase = false
  MoveWithHost = false
  Normal = (0,0,0)
  OffsetFirst = 250
  OffsetSecond = 120
  PerimeterLength = 0
  Placement = pos=(0,0,185) rot=(0,0,1;0rad)
  PredefinedType = 0
  VerticalArea = 0
  Width = 120
FEATURE [App::DocumentObjectGroup] Group128  label="NotSupportedForExport_to_IFC"
FEATURE [App::MaterialObjectPython] Material012  label="Wood_mebel"  # material (typed FeaturePython)
  Description = A standard construction wood
  Material = AuthorAndLicense=Wood-Generic,CardName=Wood-Generic,Color=(0.34509803921568627, 0.6627450980392157, 0.5058823529411764, 1.0),Density=700 kg/m^3,+10 more (map truncated)
  ProductURL = https://en.wikipedia.org/wiki/Wood
  Transparency = 0
FEATURE [App::MaterialObjectPython] Material013  label="ceramic other"  # material (typed FeaturePython)
  Description = ceramic other
  Material = AuthorAndLicense=Concrete-Generic,CardName=Concrete-Generic,Color=(0.8117647058823529, 0.8117647058823529, 0.8117647058823529, 1.0),+11 more (map truncated)
  Transparency = 0
FEATURE [Part::FeaturePython] Structure347  label="Раковина 81х45 Hatria Area"  # Arch/BIM 52 (typed FeaturePython)
  Base = -> Wire812
  FaceMaker = 0
  GlobalId = 2d5W_OQQf2Fxkoe6wMEOb9
  Height = 150
  HorizontalArea = 314998
  IfcData = IfcUID=2d5W_OQQf2Fxkoe6wMEOb9,+2 more (map truncated)
  IfcType = 52
  Length = 0
  Material = -> Material013
  MoveBase = false
  MoveWithHost = false
  Nodes = (2) [(-2856.79,7112.64,0),(-2856.79,7112.64,600)]
  NodesOffset = 0
  Normal = (0,0,1)
  PerimeterLength = 2372.43
  Placement = pos=(0,0,850) rot=(0,0,1;0rad)
  Subtractions = -> [Structure346]
  VerticalArea = 355865
  Width = 100
FEATURE [App::MaterialObjectPython] Material014  label="Wood (laminate)"  # material (typed FeaturePython)
  Description = A standard construction wood
  Material = AuthorAndLicense=Wood-Generic,CardName=Wood-Generic,Color=(0.8196078431372549, 0.8196078431372549, 0.8196078431372549, 1.0),Density=700 kg/m^3,+10 more (map truncated)
  ProductURL = https://en.wikipedia.org/wiki/Wood
  Transparency = 0
FEATURE [App::MaterialObjectPython] Material015  label="Other mebel"  # material (typed FeaturePython)
  Description = Other mebel
  Material = AuthorAndLicense=Wood-Generic,CardName=Wood-Generic,Color=(0.6196078431372549, 0.6941176470588235, 0.7568627450980392, 1.0),Density=700 kg/m^3,+9 more (map truncated)
  Transparency = 0
FEATURE [Part::FeaturePython] Structure277  label="Structure020"  # Arch/BIM 52 (typed FeaturePython)
  FaceMaker = 0
  GlobalId = 2DDa$j80P5hvQ3LPUQNes4
  Height = 200
  HorizontalArea = 236963
  IfcData = IfcUID=2DDa$j80P5hvQ3LPUQNes4,attributes={"GlobalId": {"value": "2DDa$j80P5hvQ3LPUQNes4"}},+1 more (map truncated)
  IfcType = 52
  Length = 0
  Material = -> Material015
  MoveBase = false
  MoveWithHost = false
  Nodes = (2) [(1656.58,7240.7,0),(1656.58,7240.7,200)]
  NodesOffset = 0
  Normal = (0,0,0)
  PerimeterLength = 2357.08
  Placement = pos=(0,0,400) rot=(0,0,1;0rad)
  VerticalArea = 471416
  Width = 100
FEATURE [Part::FeaturePython] Structure278  label="Structure021"  # Arch/BIM 52 (typed FeaturePython)
  FaceMaker = 0
  GlobalId = 3Z9IWRZuT13weCYbg7_Khd
  Height = 200
  HorizontalArea = 236963
  IfcData = IfcUID=3Z9IWRZuT13weCYbg7_Khd,attributes={"GlobalId": {"value": "3Z9IWRZuT13weCYbg7_Khd"}},+1 more (map truncated)
  IfcType = 52
  Length = 0
  Material = -> Material015
  MoveBase = false
  MoveWithHost = false
  Nodes = (2) [(156.577,7240.7,0),(156.577,7240.7,200)]
  NodesOffset = 0
  Normal = (0,0,0)
  PerimeterLength = 2357.08
  Placement = pos=(0,0,400) rot=(0,0,1;0rad)
  VerticalArea = 471416
  Width = 100
FEATURE [Part::FeaturePython] Structure275  label="Structure018"  # Arch/BIM 52 (typed FeaturePython)
  FaceMaker = 0
  GlobalId = 1sWNXrsjP3FQ$2jjEvDesy
  Height = 400
  HorizontalArea = 749463
  IfcData = IfcUID=1sWNXrsjP3FQ$2jjEvDesy,attributes={"GlobalId": {"value": "1sWNXrsjP3FQ$2jjEvDesy"}},+1 more (map truncated)
  IfcType = 52
  Length = 0
  Material = -> Material015
  MoveBase = false
  MoveWithHost = false
  Nodes = (2) [(182.895,-1383.89,0),(182.895,-1383.89,400)]
  NodesOffset = 0
  Normal = (0,0,0)
  PerimeterLength = 5557.08
  Placement = pos=(0,0,400) rot=(0,0,1;0rad)
  VerticalArea = 2.22283e+06
  Width = 100
FEATURE [Part::FeaturePython] Structure276  label="Structure019"  # Arch/BIM 52 (typed FeaturePython)
  FaceMaker = 0
  GlobalId = 3fmvKSc5DEWOPxKz6nUpvm
  Height = 400
  HorizontalArea = 2.37446e+06
  IfcData = IfcUID=3fmvKSc5DEWOPxKz6nUpvm,attributes={"GlobalId": {"value": "3fmvKSc5DEWOPxKz6nUpvm"}},+1 more (map truncated)
  IfcType = 52
  Length = 0
  Material = -> Material015
  MoveBase = false
  MoveWithHost = false
  Nodes = (2) [(906.577,7240.7,0),(906.577,7240.7,400)]
  NodesOffset = 0
  Normal = (0,0,0)
  PerimeterLength = 6857.08
  VerticalArea = 2.74283e+06
  Width = 100
FEATURE [Part::FeaturePython] Structure279  label="Structure143"  # Arch/BIM 52 (typed FeaturePython)
  FaceMaker = 0
  GlobalId = 3TZavIZkH49B1D2AaSuAzL
  Height = 400
  HorizontalArea = 434963
  IfcData = IfcUID=3TZavIZkH49B1D2AaSuAzL,attributes={"GlobalId": {"value": "3TZavIZkH49B1D2AaSuAzL"}},+1 more (map truncated)
  IfcType = 52
  Length = 0
  Material = -> Material015
  MoveBase = false
  MoveWithHost = false
  Nodes = (2) [(906.577,7240.7,0),(906.577,7240.7,400)]
  NodesOffset = 0
  Normal = (0,0,0)
  PerimeterLength = 2597.08
  VerticalArea = 1.03883e+06
  Width = 100
FEATURE [App::GeometryPython] BuildingPart065  label="Диван 250x162L"  # Arch/BIM 52 (typed FeaturePython)
  Area = 0
  GlobalId = 1oZyr4jbn08vwhGg8DOzPQ
  Group = -> [Structure275,Structure278,Structure276,Structure277,Structure279]
  Height = 0
  HeightPropagate = true
  IfcData = IfcUID=1oZyr4jbn08vwhGg8DOzPQ,attributes={"GlobalId": {"value": "1oZyr4jbn08vwhGg8DOzPQ"}},+1 more (map truncated)
  IfcType = 52
  LevelOffset = 0
FEATURE [App::MaterialObjectPython] Material016  label="PVC"  # material (typed FeaturePython)
  Material = AuthorAndLicense=PVC-Generic,CardName=PVC-Generic,Color=(0.10980392156862745, 0.050980392156862744, 0.050980392156862744, 1.0),Density=1380 kg/m^3,+13 more (map truncated)
  ProductURL = https://en.wikipedia.org/wiki/Polyvinyl_chloride
  Transparency = 0
FEATURE [App::MaterialObjectPython] Material017  label="Steel (white)"  # material (typed FeaturePython)
  Material = AuthorAndLicense=Steel-Generic,CardName=Steel-Generic,Color=(0.6549019607843137, 0.8823529411764706, 0.9058823529411765, 1.0),Density=7900 kg/m^3,+12 more (map truncated)
  ProductURL = https://en.wikipedia.org/wiki/Steel
  Transparency = 0
FEATURE [App::MaterialObjectPython] Material018  label="Concrete (not transparent)"  # material (typed FeaturePython)
  Description = A standard C-25 construction concrete
  Material = AuthorAndLicense=Concrete-Generic,CardName=Concrete-Generic,Color=(0.47058823529411764, 0.4627450980392157, 0.4627450980392157, 1.0),+13 more (map truncated)
  ProductURL = https://en.wikipedia.org/wiki/Concrete
  StandardCode = Masterformat 03 33 13
  Transparency = 0
FEATURE [Part::FeaturePython] Structure140  label="габарит крыльца001"  # Arch/BIM 52 (typed FeaturePython)
  Base = -> Rectangle2381
  FaceMaker = 0
  Height = 150
  HorizontalArea = 3218600
  IfcData = complex_attributes={"OwnerHistory": {}, "IsNestedBy": {}, "IsDecomposedBy": {}, "IsDefinedBy": {}, "ObjectPlacement": {}, "Representation":... (+4 chars omitted)
  IfcType = 52
  Length = 0
  Material = -> Material018
  MoveBase = false
  MoveWithHost = false
  Nodes = (2) [(5975,-1250,0),(5975,-1250,-350)]
  NodesOffset = 0
  Normal = (0,0,-1)
  PerimeterLength = 8250
  Placement = pos=(0,0,-50) rot=(0,0,1;0rad)
  VerticalArea = 1237500
  Width = 100
FEATURE [App::FeaturePython] Dimension032  # Draft dimension (typed FeaturePython)
  Diameter = false
  Dimline = (6200,3100,0)
  Direction = (0,0,0)
  Distance = 1200
  End = (2470,4425,0)
  Normal = (0,0,1)
  Start = (2470,3225,0)
FEATURE [App::FeaturePython] Dimension034  # Draft dimension (typed FeaturePython)
  Diameter = false
  Dimline = (5200,1000,0)
  Direction = (0,0,0)
  Distance = 1680
  End = (6105,2935,0)
  Normal = (0,0,1)
  Start = (4425,2935,0)
FEATURE [App::FeaturePython] Dimension035  # Draft dimension (typed FeaturePython)
  Diameter = false
  Dimline = (7645.91,7467.32,0)
  Direction = (0,0,0)
  Distance = 1000
  End = (7355,8395,0)
  Normal = (0,0,1)
  Start = (7355,7395,0)
FEATURE [App::FeaturePython] Dimension036  # Draft dimension (typed FeaturePython)
  Diameter = false
  Dimline = (6300,1900,0)
  Direction = (0,0,0)
  Distance = 940
  End = (7045,1635,0)
  Normal = (0,0,1)
  Start = (6105,1635,0)
FEATURE [App::FeaturePython] Dimension037  # Draft dimension (typed FeaturePython)
  Diameter = false
  Dimline = (6000,4700,0)
  Direction = (0,0,0)
  Distance = 1040
  End = (6690,5575,0)
  Normal = (0,0,1)
  Start = (6690,4535,0)
FEATURE [App::FeaturePython] Dimension038  # Draft dimension (typed FeaturePython)
  Diameter = false
  Dimline = (4700,1000,0)
  Direction = (0,0,0)
  Distance = 2960
  End = (3825,2935,0)
  Normal = (0,0,1)
  Start = (3825,-25,0)
FEATURE [App::FeaturePython] Dimension039  # Draft dimension (typed FeaturePython)
  Diameter = false
  Dimline = (6000,2300,0)
  Direction = (0,0,0)
  Distance = 1360
  End = (7045,2935,0)
  Normal = (0,0,1)
  Start = (7045,1575,0)
FEATURE [App::FeaturePython] Dimension047  # Draft dimension (typed FeaturePython)
  Diameter = false
  Dimline = (6800,100,0)
  Direction = (0,0,0)
  Distance = 1710
  End = (7925,-25,0)
  Normal = (0,0,1)
  Start = (6215,-25,0)
FEATURE [App::FeaturePython] Dimension048  # Draft dimension (typed FeaturePython)
  Diameter = false
  Dimline = (4500,4600,0)
  Direction = (0,0,0)
  Distance = 1900
  End = (5725,4535,0)
  Normal = (0,0,1)
  Start = (3825,4535,0)
FEATURE [App::FeaturePython] Dimension049  # Draft dimension (typed FeaturePython)
  Diameter = false
  Dimline = (2200,1800,0)
  Direction = (0,0,0)
  Distance = 3140
  End = (-30,3115,0)
  Normal = (0,0,1)
  Start = (-30,-25,0)
FEATURE [App::FeaturePython] Dimension050  # Draft dimension (typed FeaturePython)
  Diameter = false
  Dimline = (2900,600,0)
  Direction = (0,0,0)
  Distance = 3565
  End = (3535,-25,0)
  Normal = (0,0,1)
  Start = (-30,-25,0)
FEATURE [App::FeaturePython] Dimension053  # Draft dimension (typed FeaturePython)
  Diameter = false
  Dimline = (1770,9200,0)
  Direction = (0,0,0)
  Distance = 1830
  End = (3080,8925,0)
  Normal = (0,0,1)
  Start = (1250,8925,0)
FEATURE [App::FeaturePython] Dimension054  # Draft dimension (typed FeaturePython)
  Diameter = false
  Dimline = (2500,7900,0)
  Direction = (0,0,0)
  Distance = 3565
  End = (3535,8395,0)
  Normal = (0,0,1)
  Start = (-30,8395,0)
FEATURE [App::FeaturePython] Dimension055  # Draft dimension (typed FeaturePython)
  Diameter = false
  Dimline = (7370,5300,0)
  Direction = (0,0,0)
  Distance = 3475
  End = (10600,4395,0)
  Normal = (0,0,1)
  Start = (7125,4395,0)
FEATURE [App::FeaturePython] Dimension056  # Draft dimension (typed FeaturePython)
  Diameter = false
  Dimline = (4495,3400,0)
  Direction = (0,0,0)
  Distance = 1570
  End = (6025,3205,0)
  Normal = (0,0,1)
  Start = (4455,3205,0)
FEATURE [App::FeaturePython] Dimension057  # Draft dimension (typed FeaturePython)
  Diameter = false
  Dimline = (2200,4700,0)
  Direction = (0,0,0)
  Distance = 650
  End = (2370,4525,0)
  Normal = (0,0,1)
  Start = (2370,3875,0)
FEATURE [App::FeaturePython] Dimension058  # Draft dimension (typed FeaturePython)
  Diameter = false
  Dimline = (8400,1100,0)
  Direction = (0,0,0)
  Distance = 2565
  End = (10600,1185,0)
  Normal = (0,0,1)
  Start = (8035,1185,0)
FEATURE [App::FeaturePython] Dimension059  # Draft dimension (typed FeaturePython)
  Diameter = false
  Dimline = (10500,2600,0)
  Direction = (0,0,0)
  Distance = 2220
  End = (10270,3975,0)
  Normal = (0,0,1)
  Start = (10270,1755,0)
FEATURE [App::FeaturePython] Dimension060  # Draft dimension (typed FeaturePython)
  Diameter = false
  Dimline = (3100,5800,0)
  Direction = (0,0,0)
  Distance = 3870
  End = (3535,8395,0)
  Normal = (0,0,1)
  Start = (3535,4525,0)
FEATURE [App::FeaturePython] Dimension061  # Draft dimension (typed FeaturePython)
  Diameter = false
  Dimline = (8000,6000,0)
  Direction = (0,0,0)
  Distance = 5170
  End = (10600,8395,0)
  Normal = (0,0,1)
  Start = (10600,3225,0)
FEATURE [App::FeaturePython] Dimension062  # Draft dimension (typed FeaturePython)
  Diameter = false
  Dimline = (8300,2627.24,0)
  Direction = (0,0,0)
  Distance = 1370
  End = (8035,2555,0)
  Normal = (0,0,1)
  Start = (8035,1185,0)
FEATURE [App::FeaturePython] Dimension063  # Draft dimension (typed FeaturePython)
  Diameter = false
  Dimline = (9300,3400,0)
  Direction = (0,0,0)
  Distance = 2615
  End = (9820,3225,0)
  Normal = (0,0,1)
  Start = (7205,3225,0)
FEATURE [App::FeaturePython] Dimension064  # Draft dimension (typed FeaturePython)
  Diameter = false
  Dimline = (3500,4600,0)
  Direction = (0,0,0)
  Distance = 900
  End = (3435,4525,0)
  Normal = (0,0,1)
  Start = (2535,4525,0)
FEATURE [TechDraw::DrawViewAnnotation] Annotation009  label="a_077"
  Font = osifont
  LineSpace = 80
  LockPosition = true
  MaxWidth = -1
  Rotation = 0
  ScaleType = 0
  Text = \u0410\u0440\u043c\u043f\u043e\u044f\u0441 180x140mm
  TextSize = 4
  TextStyle = 0
  X = 256.728
  Y = 224.794
FEATURE [TechDraw::DrawViewAnnotation] Annotation010  label="a_078"
  Font = osifont
  LineSpace = 80
  LockPosition = true
  MaxWidth = -1
  Rotation = 0
  ScaleType = 0
  Text = XPS 80mm
  TextSize = 4
  TextStyle = 0
  X = 265.062
  Y = 229.944
FEATURE [TechDraw::DrawViewAnnotation] Annotation011  label="a_079"
  Font = osifont
  LineSpace = 80
  LockPosition = true
  MaxWidth = -1
  Rotation = 0
  ScaleType = 0
  Text = \u041a\u0438\u0440\u043f\u0438\u0447 2.1 \u043d\u0444
  TextSize = 4
  TextStyle = 0
  X = 260.909
  Y = 212.329
FEATURE [TechDraw::DrawViewAnnotation] Annotation012  label="a_080"
  Font = osifont
  LineSpace = 80
  LockPosition = true
  MaxWidth = -1
  Rotation = 0
  ScaleType = 0
  Text = \u041c\u0430\u0443\u044d\u0440\u043b\u0430\u0442 150\u0445150mm
  TextSize = 4
  TextStyle = 0
  X = 256.196
  Y = 218.755
FEATURE [TechDraw::DrawLeaderLine] LeaderLine
  AutoHorizontal = true
  EndSymbol = 7
  LeaderParent = -> Annotation010
  LockPosition = true
  Rotation = 0
  Scalable = false
  ScaleType = 0
  StartSymbol = 7
  WayPoints = (3) [(0,0,0),(9.82636,-670.069,0),(-263.143,-670.069,0)]
  X = 17.2239
  Y = -68.3719
FEATURE [TechDraw::DrawLeaderLine] LeaderLine001
  AutoHorizontal = true
  EndSymbol = 7
  LeaderParent = -> Annotation012
  LockPosition = true
  Rotation = 0
  Scalable = false
  ScaleType = 0
  StartSymbol = 7
  WayPoints = (3) [(0,0,0),(10.0885,-535.699,0),(-399.504,-535.699,0)]
  X = 22.6678
  Y = -54.1973
FEATURE [TechDraw::DrawLeaderLine] LeaderLine002
  AutoHorizontal = true
  EndSymbol = 7
  LeaderParent = -> Annotation009
  LockPosition = true
  Rotation = 0
  Scalable = false
  ScaleType = 0
  StartSymbol = 7
  WayPoints = (3) [(0,0,0),(10.0885,-626.495,0),(-400.513,-626.495,0)]
  X = 23.346
  Y = -63.2619
FEATURE [TechDraw::DrawLeaderLine] LeaderLine003
  AutoHorizontal = true
  EndSymbol = 7
  LeaderParent = -> Annotation011
  LockPosition = true
  Rotation = 0
  Scalable = false
  ScaleType = 0
  StartSymbol = 7
  WayPoints = (3) [(0,0,0),(11.2011,-497.917,0),(-281.712,-497.917,0)]
  X = 15.6278
  Y = -50.7269
FEATURE [TechDraw::DrawViewAnnotation] Annotation013  label="a_082"
  Font = osifont
  LineSpace = 80
  LockPosition = true
  MaxWidth = -1
  Rotation = 0
  ScaleType = 0
  Text = XPS 100mm
  TextSize = 4
  TextStyle = 0
  X = 118.3
  Y = 198.428
FEATURE [TechDraw::DrawViewAnnotation] Annotation014  label="a_083"
  Font = osifont
  LineSpace = 80
  LockPosition = true
  MaxWidth = -1
  Rotation = 0
  ScaleType = 0
  Text = \u041f\u043e\u043a\u0440\u044b\u0442\u0438\u0435 \u043f\u043e\u043b\u0430 20mm
  TextSize = 4
  TextStyle = 0
  X = 109.298
  Y = 208.784
FEATURE [TechDraw::DrawViewAnnotation] Annotation015  label="a_084"
  Font = osifont
  LineSpace = 80
  LockPosition = true
  MaxWidth = -1
  Rotation = 0
  ScaleType = 0
  Text = \u0421\u0442\u044f\u0436\u043a\u0430 \u043f\u043e\u043b\u0430 50mm
  TextSize = 4
  TextStyle = 0
  X = 111.999
  Y = 203.648
FEATURE [TechDraw::DrawViewAnnotation] Annotation016  label="a_076"
  Font = osifont
  LineSpace = 80
  LockPosition = true
  MaxWidth = -1
  Rotation = 0
  ScaleType = 0
  Text = \u041e\u0431\u043b\u0438\u0446\u043e\u0432\u043e\u0447\u043d\u044b\u0439 \u043a\u0438\u0440\u043f\u0438\u0447 1\u043d\u0444
  TextSize = 4
  TextStyle = 0
  X = 250.884
  Y = 234.906
FEATURE [TechDraw::DrawLeaderLine] LeaderLine004
  AutoHorizontal = true
  EndSymbol = 7
  LeaderParent = -> Annotation016
  LockPosition = true
  Rotation = 0
  Scalable = false
  ScaleType = 0
  StartSymbol = 7
  WayPoints = (3) [(0,0,0),(17.4485,-744.208,0),(-570.424,-744.208,0)]
  X = 33.3756
  Y = -74.7769
FEATURE [TechDraw::DrawViewAnnotation] Annotation017  label="a_001"
  Font = osifont
  LineSpace = 80
  LockPosition = true
  MaxWidth = -1
  Rotation = 0
  ScaleType = 0
  Text = XPS 100mm
  TextSize = 4
  TextStyle = 0
  X = 301.631
  Y = 118.628
FEATURE [TechDraw::DrawViewAnnotation] Annotation018  label="a_028"
  Font = osifont
  LineSpace = 80
  LockPosition = true
  MaxWidth = -1
  Rotation = 0
  ScaleType = 0
  Text = XPS 80mm
  TextSize = 4
  TextStyle = 0
  X = 313.482
  Y = 140.167
FEATURE [TechDraw::DrawViewAnnotation] Annotation019  label="a_029"
  Font = osifont
  LineSpace = 80
  LockPosition = true
  MaxWidth = -1
  Rotation = 0
  ScaleType = 0
  Text = \u041f\u0435\u0440\u0435\u043c\u044b\u0447\u043a\u0430 \u043c\u043e\u043d\u043e\u043b\u0438\u0442\u043d\u0430\u044f
  TextSize = 4
  TextStyle = 0
  X = 311.808
  Y = 112.937
FEATURE [TechDraw::DrawViewAnnotation] Annotation020  label="a_030"
  Font = osifont
  LineSpace = 80
  LockPosition = true
  MaxWidth = -1
  Rotation = 0
  ScaleType = 0
  Text = \u041a\u0430\u043c\u0435\u043d\u044c \u043e\u0431\u043b\u0438\u0446\u043e\u0432\u043e\u0447\u043d\u044b\u0439
  TextSize = 4
  TextStyle = 0
  X = 311.983
  Y = 123.571
FEATURE [TechDraw::DrawViewAnnotation] Annotation021  label="a_031"
  Font = osifont
  LineSpace = 80
  LockPosition = true
  MaxWidth = -1
  Rotation = 0
  ScaleType = 0
  Text = \u041a\u0438\u0440\u043f\u0438\u0447 1\u043d\u0444
  TextSize = 4
  TextStyle = 0
  X = 320.081
  Y = 135.139
FEATURE [TechDraw::DrawViewAnnotation] Annotation022  label="a_032"
  Font = osifont
  LineSpace = 80
  LockPosition = true
  MaxWidth = -1
  Rotation = 0
  ScaleType = 0
  Text = \u0411\u043b\u043e\u043a 380\u043c\u043c \u041b\u0421\u0420 10.7\u043d\u0444 "\u0422\u0451\u043f\u043b\u044b\u0439"
  TextSize = 4
  TextStyle = 0
  X = 68.8072
  Y = 136.929
FEATURE [TechDraw::DrawViewAnnotation] Annotation023  label="a_033"
  Font = osifont
  LineSpace = 80
  LockPosition = true
  MaxWidth = -1
  Rotation = 0
  ScaleType = 0
  Text = XPS 100mm
  TextSize = 4
  TextStyle = 0
  X = 97.5568
  Y = 118.043
FEATURE [TechDraw::DrawViewAnnotation] Annotation024  label="a_034"
  Font = osifont
  LineSpace = 80
  LockPosition = true
  MaxWidth = -1
  Rotation = 0
  ScaleType = 0
  Text = \u0421\u0442\u044f\u0436\u043a\u0430 \u0442\u0451\u043f\u043b\u043e\u0433\u043e \u043f\u043e\u043b\u0430 80mm
  TextSize = 4
  TextStyle = 0
  X = 83.3647
  Y = 122.395
FEATURE [TechDraw::DrawViewAnnotation] Annotation025  label="a_035"
  Font = osifont
  LineSpace = 80
  LockPosition = true
  MaxWidth = -1
  Rotation = 0
  ScaleType = 0
  Text = \u041f\u043e\u043a\u0440\u044b\u0442\u0438\u0435 \u043f\u043e\u043b\u0430 20mm
  TextSize = 4
  TextStyle = 0
  X = 88.1001
  Y = 127.174
FEATURE [TechDraw::DrawViewAnnotation] Annotation026  label="a_036"
  Font = osifont
  LineSpace = 80
  LockPosition = true
  MaxWidth = -1
  Rotation = 0
  ScaleType = 0
  Text = \u041f\u043b\u0438\u0442\u044b \u043e\u0431\u043b\u0435\u0433\u0447\u0451\u043d\u043d\u044b\u0435 160mm
  TextSize = 4
  TextStyle = 0
  X = 104.49
  Y = 193.218
FEATURE [TechDraw::DrawLeaderLine] LeaderLine005
  AutoHorizontal = true
  EndSymbol = 7
  LeaderParent = -> Annotation026
  LockPosition = true
  Rotation = 0
  Scalable = false
  ScaleType = 0
  StartSymbol = 7
  WayPoints = (3) [(0,0,0),(-2.30237,-441.288,0),(-511.894,-441.288,0)]
  X = 27.6874
  Y = -45.469
FEATURE [TechDraw::DrawLeaderLine] LeaderLine006
  AutoHorizontal = true
  EndSymbol = 7
  LeaderParent = -> Annotation023
  LockPosition = true
  Rotation = 0
  Scalable = false
  ScaleType = 0
  StartSymbol = 7
  WayPoints = (4) [(0,0,0),(0,-112.671,0),(-241.304,-298.052,0),(-700.128,-298.052,0)]
  X = 33.001
  Y = -31.105
FEATURE [TechDraw::DrawLeaderLine] LeaderLine007
  AutoHorizontal = true
  EndSymbol = 7
  LeaderParent = -> Annotation022
  LockPosition = true
  Rotation = 0
  Scalable = false
  ScaleType = 0
  StartSymbol = 7
  WayPoints = (3) [(0,0,0),(-234.053,-148.301,0),(-811.115,-148.301,0)]
  X = 52.2554
  Y = -15.2644
FEATURE [TechDraw::DrawLeaderLine] LeaderLine008
  AutoHorizontal = true
  EndSymbol = 7
  LeaderParent = -> Annotation019
  LockPosition = true
  Rotation = 0
  Scalable = false
  ScaleType = 0
  StartSymbol = 7
  WayPoints = (3) [(0,0,0),(123.191,316.527,0),(538.433,316.527,0)]
  X = -33.8955
  Y = 30.8346
FEATURE [TechDraw::DrawLeaderLine] LeaderLine009
  AutoHorizontal = true
  EndSymbol = 7
  LeaderParent = -> Annotation017
  LockPosition = true
  Rotation = 0
  Scalable = false
  ScaleType = 0
  StartSymbol = 7
  WayPoints = (3) [(0,0,0),(99.3175,258.506,0),(299.176,258.506,0)]
  X = -19.5842
  Y = 24.9219
FEATURE [TechDraw::DrawLeaderLine] LeaderLine010
  AutoHorizontal = true
  EndSymbol = 7
  LeaderParent = -> Annotation020
  LockPosition = true
  Rotation = 0
  Scalable = false
  ScaleType = 0
  StartSymbol = 7
  WayPoints = (3) [(0,0,0),(77.3527,184.314,0),(465.976,184.314,0)]
  X = -27.3933
  Y = 17.9304
FEATURE [TechDraw::DrawLeaderLine] LeaderLine011
  AutoHorizontal = true
  EndSymbol = 7
  LeaderParent = -> Annotation021
  LockPosition = true
  Rotation = 0
  Scalable = false
  ScaleType = 0
  StartSymbol = 7
  WayPoints = (3) [(0,0,0),(246.354,145.817,0),(563.314,145.817,0)]
  X = -40.3095
  Y = 13.3285
FEATURE [TechDraw::DrawLeaderLine] LeaderLine012
  AutoHorizontal = true
  EndSymbol = 7
  LeaderParent = -> Annotation018
  LockPosition = true
  Rotation = 0
  Scalable = false
  ScaleType = 0
  StartSymbol = 7
  WayPoints = (3) [(0,0,0),(226.991,110.973,0),(407.743,110.973,0)]
  X = -31.4229
  Y = 10.0706
FEATURE [App::FeaturePython] Dimension065  # Draft dimension (typed FeaturePython)
  Diameter = false
  Dimline = (0,5100,1600)
  Direction = (0,0,0)
  Distance = 2800
  End = (0,3665,2800)
  Normal = (1,0,0)
  Start = (0,3665,0)
FEATURE [App::FeaturePython] Dimension066  # Draft dimension (typed FeaturePython)
  Diameter = false
  Dimline = (0,5100,2700)
  Direction = (0,0,0)
  Distance = 335
  End = (0,3665,3135)
  Normal = (1,0,0)
  Start = (0,3665,2800)
FEATURE [App::FeaturePython] Dimension067  # Draft dimension (typed FeaturePython)
  Diameter = false
  Dimline = (0,5100,4100)
  Direction = (0,0,0)
  Distance = 498
  End = (0,3665,3633)
  Normal = (1,0,0)
  Start = (0,3665,3135)
FEATURE [App::FeaturePython] Dimension071  # Draft dimension (typed FeaturePython)
  Diameter = false
  Dimline = (0,11400,-400)
  Direction = (0,0,0)
  Distance = 7180
  End = (0,3730,6980)
  Normal = (1,0,0)
  Start = (0,3730,-200)
FEATURE [App::GeometryPython] BuildingPart100  label="Размеры (side)"  # Arch/BIM 52 (typed FeaturePython)
  Area = 0
  GlobalId = 27k3ICoRP4zxJkZ2CvXEQH
  Group = -> [Dimension029,Dimension065,Dimension066,Dimension067,Dimension071]
  Height = 0
  HeightPropagate = true
  IfcData = IfcUID=27k3ICoRP4zxJkZ2CvXEQH,+2 more (map truncated)
  IfcType = 52
  LevelOffset = 0
  Placement = pos=(0,0,0) rot=(0.57735,0.57735,0.57735;2.0944rad)
FEATURE [App::MaterialObjectPython] Material019  label="Red brick (solid)"  # material (typed FeaturePython)
  Description = A standard red brick
  Material = AuthorAndLicense=Concrete-Generic,CardName=Concrete-Generic,Color=(0.6666666666666666, 0.0, 0.0, 1.0),CompressiveStrength=25 MPa,Density=2400 kg/m^3,+9 more (map truncated)
  Transparency = 0
FEATURE [Part::Part2DObjectPython] Wire890  # Draft 2D object (typed FeaturePython)
  Area = 0
  ChamferSize = 0
  Closed = true
  End = (11000,-425,0)
  FilletRadius = 0
  Length = 41300
  MakeFace = false
  Placement = pos=(-430,-410,0) rot=(0,0,1;0rad)
  Points = (4) [(0,-15,0),(0,9205,0),(11430,9205,0),(11430,-15,0)]
  Start = (-430,-425,0)
  Subdivisions = 0
FEATURE [Part::FeaturePython] Wall312  label="Отделка цоколя 15mm"  # Arch/BIM 166 (typed FeaturePython)
  Align = 0
  Area = 14455000
  Base = -> Wire890
  BlockHeight = 80
  BlockLength = 1000
  CountBroken = 4
  CountEntire = 39
  Face = 0
  Height = 350
  HorizontalArea = 642000
  IfcData = attributes={"GlobalId": {"name": "GlobalId", "type": "IfcGloballyUniqueId", "is_enum": false, "enum_values": []}, "Description": {"... (+533 chars omitted),+1 more (map truncated)
  IfcType = 166
  Joint = 0
  Length = 41300
  MakeBlocks = false
  Material = -> Material018
  MoveBase = false
  MoveWithHost = false
  Normal = (0,0,-1)
  Offset = 180
  OffsetFirst = 0
  OffsetSecond = 0
  PerimeterLength = 42860
  Placement = pos=(0,0,-120) rot=(0,0,1;0rad)
  PredefinedType = 0
  VerticalArea = 29960000
  Width = 15
FEATURE [TechDraw::DrawViewAnnotation] Annotation  label="a_092"
  Font = osifont
  LineSpace = 80
  LockPosition = true
  MaxWidth = -1
  Rotation = 0
  Scale = 0.02
  ScaleType = 0
  Text = \u041e\u0442\u0434\u0435\u043b\u043a\u0430 \u0446\u043e\u043a\u043e\u043b\u044f 15mm
  TextSize = 4
  TextStyle = 0
  X = 85.2969
  Y = 88.0815
FEATURE [TechDraw::DrawViewAnnotation] Annotation027  label="a_093"
  Font = osifont
  LineSpace = 80
  LockPosition = true
  MaxWidth = -1
  Rotation = 0
  Scale = 0.02
  ScaleType = 0
  Text = XPS 50mm
  TextSize = 4
  TextStyle = 0
  X = 95.3409
  Y = 93.1161
FEATURE [TechDraw::DrawViewAnnotation] Annotation028  label="a_094"
  Font = osifont
  LineSpace = 80
  LockPosition = true
  MaxWidth = -1
  Rotation = 0
  Scale = 0.02
  ScaleType = 0
  Text = \u041a\u0430\u043c\u0435\u043d\u044c \u0431\u043e\u0440\u0434\u044e\u0440\u043d\u044b\u0439 1000\u044580\u0445200mm
  TextSize = 4
  TextStyle = 0
  X = 74.5727
  Y = 97.7244
FEATURE [TechDraw::DrawLeaderLine] LeaderLine013
  AutoHorizontal = true
  EndSymbol = 7
  LeaderParent = -> Annotation
  LockPosition = true
  Rotation = 0
  Scalable = false
  ScaleType = 0
  StartSymbol = 7
  WayPoints = (3) [(0,0,0),(-95.8036,-29.0684,0),(-464.748,-29.0684,0)]
  X = 1397.61
  Y = -181.771
FEATURE [TechDraw::DrawLeaderLine] LeaderLine014
  AutoHorizontal = true
  EndSymbol = 7
  LeaderParent = -> Annotation027
  LockPosition = true
  Rotation = 0
  Scalable = false
  ScaleType = 0
  StartSymbol = 7
  WayPoints = (3) [(0,0,0),(-103.814,-76.5886,0),(-277.347,-76.5886,0)]
  X = 939.794
  Y = -403.983
FEATURE [TechDraw::DrawLeaderLine] LeaderLine015
  AutoHorizontal = true
  EndSymbol = 7
  LeaderParent = -> Annotation028
  LockPosition = true
  Rotation = 0
  Scalable = false
  ScaleType = 0
  StartSymbol = 7
  WayPoints = (3) [(0,0,0),(-108.706,-86.9646,0),(-695.382,-86.9646,0)]
  X = 2006.85
  Y = -452.409
FEATURE [TechDraw::DrawViewAnnotation] Annotation029  label="a_095"
  Font = osifont
  LineSpace = 80
  LockPosition = true
  MaxWidth = -1
  Rotation = 0
  Scale = 0.02
  ScaleType = 0
  Text = \u041a\u0438\u0440\u043f\u0438\u0447 \u043f\u043e\u043b\u043d\u043e\u0442\u0435\u043b\u044b\u0439 1\u043d\u0444
  TextSize = 4
  TextStyle = 0
  X = 313.34
  Y = 91.6882
FEATURE [TechDraw::DrawLeaderLine] LeaderLine016
  AutoHorizontal = true
  EndSymbol = 7
  LeaderParent = -> Annotation029
  LockPosition = true
  Rotation = 0
  Scalable = false
  ScaleType = 0
  StartSymbol = 7
  WayPoints = (3) [(0,0,0),(77.064,-40.1375,0),(501.188,-40.1375,0)]
  X = -1439.22
  Y = -222.205
FEATURE [App::DocumentObjectGroup] Group127  label="Выноски"
  Group = -> [LeaderLine,LeaderLine001,LeaderLine002,LeaderLine003,LeaderLine004,LeaderLine005,LeaderLine006,LeaderLine007,LeaderLine008,LeaderLine009,LeaderLine010,LeaderLine011,LeaderLine012,LeaderLine013,LeaderLine014,LeaderLine015,LeaderLine016]
FEATURE [TechDraw::DrawSVGTemplate] Template
  EditableTexts = Лист=3; Номер=ИЖС-2022.0003
  Height = 297
  Orientation = 1
  Width = 420
FEATURE [TechDraw::DrawViewSpreadsheet] Sheet
  CellEnd = E11
  CellStart = C1
  Font = osifont
  LineWidth = 0.35
  LockPosition = false
  Rotation = 0
  Scale = 1.2
  ScaleType = 2
  Source = -> Spreadsheet
  Symbol = <blob: 7357 chars omitted>
  TextSize = 14
  X = 163.883
  Y = 205.479
FEATURE [TechDraw::DrawViewAnnotation] Annotation030
  Font = osifont
  LineSpace = 80
  LockPosition = false
  MaxWidth = -1
  Rotation = 0
  ScaleType = 0
  Text = \u042d\u043a\u0441\u043f\u043b\u0438\u043a\u0430\u0446\u0438\u044f \u043f\u043e\u043c\u0435\u0449\u0435\u043d\u0438\u0439 1-\u0433\u043e \u044d\u0442\u0430\u0436\u0430:
  TextSize = 8
  TextStyle = 0
  X = 122.298
  Y = 263.723
FEATURE [Part::Part2DObjectPython] Line1604  label="Калитка 001"  # Draft 2D object (typed FeaturePython)
  Area = 0
  ChamferSize = 0
  Closed = true
  End = (22239.4,-9321.03,0)
  FilletRadius = 0
  Length = 1200
  MakeFace = true
  Placement = pos=(10551.1,-7521.93,0) rot=(0,0,1;0.025758rad)
  Points = (2) [(11942.9,-938.898,0),(11638,-2099.53,0)]
  Start = (22514.2,-8152.93,0)
  Subdivisions = 0
FEATURE [Part::FeaturePython] Wall319  label="Калитка 002"  # Arch/BIM 166 (typed FeaturePython)
  Align = 1
  Area = 2.16e+06
  Base = -> Line1604
  BlockHeight = 2000
  BlockLength = 150
  CountBroken = 8
  CountEntire = 0
  Face = 0
  Height = 1800
  HorizontalArea = 0
  IfcData = attributes={"GlobalId": {"name": "GlobalId", "type": "IfcGloballyUniqueId", "is_enum": false, "enum_values": []}, "Description": {"... (+533 chars omitted),+1 more (map truncated)
  IfcType = 166
  Joint = 10
  Length = 1200
  MakeBlocks = true
  Material = -> Material010
  MoveBase = false
  MoveWithHost = false
  Normal = (0,0,0)
  Offset = 50
  OffsetFirst = 90
  OffsetSecond = 0
  PerimeterLength = 0
  Placement = pos=(0,0,-120) rot=(0,0,1;0rad)
  PredefinedType = 0
  VerticalArea = 0
  Width = 50
FEATURE [Part::Part2DObjectPython] Line1613  # Draft 2D object (typed FeaturePython)
  Area = 0
  ChamferSize = 0
  Closed = false
  End = (3735,5360,0)
  FilletRadius = 0
  Length = 250
  MakeFace = true
  Placement = pos=(3485,5360,0) rot=(0,0,1;0rad)
  Points = (2) [(0,0,0),(250,0,0)]
  Start = (3485,5360,0)
  Subdivisions = 0
FEATURE [Part::FeaturePython] Wall336  label="Кладка под стойки 001"  # Arch/BIM 166 (typed FeaturePython)
  Align = 2
  Area = 37500
  Base = -> Line1613
  BlockHeight = 65
  BlockLength = 250
  CountBroken = 1
  CountEntire = 0
  Face = 0
  Height = 150
  HorizontalArea = 62500
  IfcData = attributes={"GlobalId": {"name": "GlobalId", "type": "IfcGloballyUniqueId", "is_enum": false, "enum_values": []}, "Description": {"... (+533 chars omitted),+1 more (map truncated)
  IfcType = 166
  Joint = 12000
  Length = 250
  MakeBlocks = false
  Material = -> Material008
  MoveBase = false
  MoveWithHost = false
  Normal = (0,0,0)
  OffsetFirst = 120
  OffsetSecond = 200
  PerimeterLength = 1000
  Placement = pos=(0,0,2960) rot=(0,0,1;0rad)
  PredefinedType = 0
  VerticalArea = 150000
  Width = 250
FEATURE [Part::Part2DObjectPython] Line1614  # Draft 2D object (typed FeaturePython)
  Area = 0
  ChamferSize = 0
  Closed = true
  End = (6980,5675,0)
  FilletRadius = 0
  Length = 1160
  MakeFace = true
  Placement = pos=(6980,5155,0) rot=(0,0,1;1.5708rad)
  Points = (2) [(-640,0,0),(520,0,0)]
  Start = (6980,4515,0)
  Subdivisions = 0
FEATURE [Part::FeaturePython] Wall337  label="Кладка под стойки 002"  # Arch/BIM 166 (typed FeaturePython)
  Align = 2
  Area = 359600
  Base = -> Line1614
  BlockHeight = 65
  BlockLength = 250
  CountBroken = 1
  CountEntire = 0
  Face = 0
  Height = 310
  HorizontalArea = 290000
  IfcData = attributes={"GlobalId": {"name": "GlobalId", "type": "IfcGloballyUniqueId", "is_enum": false, "enum_values": []}, "Description": {"... (+533 chars omitted),+1 more (map truncated)
  IfcType = 166
  Joint = 12000
  Length = 1160
  MakeBlocks = false
  Material = -> Material008
  MoveBase = false
  MoveWithHost = false
  Normal = (0,0,0)
  OffsetFirst = 120
  OffsetSecond = 200
  PerimeterLength = 2820
  Placement = pos=(0,-1.819e-12,2800) rot=(0,0,1;0rad)
  PredefinedType = 0
  VerticalArea = 874200
  Width = 250
FEATURE [Part::Part2DObjectPython] Line1615  # Draft 2D object (typed FeaturePython)
  Area = 0
  ChamferSize = 0
  Closed = false
  End = (3735,3010,0)
  FilletRadius = 0
  Length = 250
  MakeFace = true
  Placement = pos=(3485,3010,0) rot=(0,0,1;0rad)
  Points = (2) [(0,0,0),(250,0,0)]
  Start = (3485,3010,0)
  Subdivisions = 0
FEATURE [Part::FeaturePython] Wall338  label="Кладка под стойки 003"  # Arch/BIM 166 (typed FeaturePython)
  Align = 2
  Area = 37500
  Base = -> Line1615
  BlockHeight = 65
  BlockLength = 250
  CountBroken = 1
  CountEntire = 0
  Face = 0
  Height = 150
  HorizontalArea = 62500
  IfcData = attributes={"GlobalId": {"name": "GlobalId", "type": "IfcGloballyUniqueId", "is_enum": false, "enum_values": []}, "Description": {"... (+533 chars omitted),+1 more (map truncated)
  IfcType = 166
  Joint = 12000
  Length = 250
  MakeBlocks = false
  Material = -> Material008
  MoveBase = false
  MoveWithHost = false
  Normal = (0,0,0)
  OffsetFirst = 120
  OffsetSecond = 200
  PerimeterLength = 1000
  Placement = pos=(0,0,2960) rot=(0,0,1;0rad)
  PredefinedType = 0
  VerticalArea = 150000
  Width = 250
FEATURE [Part::Part2DObjectPython] Line1616  # Draft 2D object (typed FeaturePython)
  Area = 0
  ChamferSize = 0
  Closed = false
  End = (7110,3010,0)
  FilletRadius = 0
  Length = 250
  MakeFace = true
  Placement = pos=(6860,3010,0) rot=(0,0,1;0rad)
  Points = (2) [(0,0,0),(250,0,0)]
  Start = (6860,3010,0)
  Subdivisions = 0
FEATURE [Part::FeaturePython] Wall339  label="Кладка под стойки 004"  # Arch/BIM 166 (typed FeaturePython)
  Align = 2
  Area = 37500
  Base = -> Line1616
  BlockHeight = 65
  BlockLength = 250
  CountBroken = 1
  CountEntire = 0
  Face = 0
  Height = 150
  HorizontalArea = 62500
  IfcData = attributes={"GlobalId": {"name": "GlobalId", "type": "IfcGloballyUniqueId", "is_enum": false, "enum_values": []}, "Description": {"... (+533 chars omitted),+1 more (map truncated)
  IfcType = 166
  Joint = 12000
  Length = 250
  MakeBlocks = false
  Material = -> Material008
  MoveBase = false
  MoveWithHost = false
  Normal = (0,0,0)
  OffsetFirst = 120
  OffsetSecond = 200
  PerimeterLength = 1000
  Placement = pos=(0,0,2960) rot=(0,0,1;0rad)
  PredefinedType = 0
  VerticalArea = 150000
  Width = 250
FEATURE [Part::Part2DObjectPython] Line1626  # Draft 2D object (typed FeaturePython)
  Area = 0
  ChamferSize = 0
  Closed = false
  End = (3200,-1930,0)
  FilletRadius = 0
  Length = 2
  MakeFace = true
  Placement = pos=(3198,-1930,0) rot=(0,0,1;0rad)
  Points = (2) [(0,0,0),(2,0,0)]
  Start = (3198,-1930,0)
  Subdivisions = 0
FEATURE [TechDraw::DrawSVGTemplate] Template003
  EditableTexts = Лист=5; Номер=ИЖС-2022.0003
  Height = 297
  Orientation = 1
  Width = 420
FEATURE [TechDraw::DrawViewAnnotation] Annotation031
  Font = osifont
  LineSpace = 80
  LockPosition = false
  MaxWidth = -1
  Rotation = 0
  ScaleType = 0
  Text = \u041f\u043b\u0430\u043d \u043c\u0430\u043d\u0441\u0430\u0440\u0434\u043d\u043e\u0433\u043e \u044d\u0442\u0430\u0436\u0430 \u043d\u0430 \u043e\u0442\u043c\u0435\u0442\u043a\u0435 +3.145
  TextSize = 6
  TextStyle = 0
  X = 199.786
  Y = 278.442
FEATURE [Part::Part2DObjectPython] Rectangle3398  # Draft 2D object (typed FeaturePython)
  Area = 0
  ChamferSize = 0
  Columns = 1
  FilletRadius = 0
  Height = 8000
  Length = 7000
  MakeFace = false
  Placement = pos=(21300,-8800,0) rot=(0,0,1;1.33971rad)
  Rows = 1
FEATURE [Part::FeaturePython] Structure437  label="Парковка"  # Arch/BIM 118 (typed FeaturePython)
  Base = -> Rectangle3398
  FaceMaker = 0
  Height = 200
  HorizontalArea = 5.6e+07
  IfcData = attributes={"GlobalId": {"name": "GlobalId", "type": "IfcGloballyUniqueId", "is_enum": false, "enum_values": []}, "Description": {"... (+453 chars omitted),+1 more (map truncated)
  IfcType = 118
  Length = 7000
  MoveBase = false
  MoveWithHost = false
  Nodes = (4) [(19575,-8688.32,0),(20865.3,-2828.71,0),(14029.1,-1323.35,0),(12738.8,-7182.97,0)]
  NodesOffset = 0
  Normal = (0,0,-1)
  PerimeterLength = 30000
  Placement = pos=(0,0,-210) rot=(0,0,1;0rad)
  PredefinedType = 0
  VerticalArea = 6e+06
  Width = 6500
FEATURE [Part::Part2DObjectPython] Rectangle3402  # Draft 2D object (typed FeaturePython)
  Area = 1.38e+07
  ChamferSize = 0
  Columns = 1
  FilletRadius = 0
  Height = 2300
  Length = 6000
  MakeFace = true
  Placement = pos=(-6950.03,-7631.87,0) rot=(0,0,1;0.175714rad)
  Rows = 1
FEATURE [Part::Part2DObjectPython] Line1707  # Draft 2D object (typed FeaturePython)
  Area = 0
  ChamferSize = 0
  Closed = false
  End = (17067.1,-8206.73,0)
  FilletRadius = 0
  Length = 5200
  MakeFace = true
  Placement = pos=(22128.9,-9397.73,0) rot=(0,0,-1;0.231091rad)
  Points = (2) [(0,0,0),(-5200,-3.00133e-11,0)]
  Start = (22128.9,-9397.73,0)
  Subdivisions = 0
FEATURE [Part::FeaturePython] Wall315  label="Створка ворот 4.7м"  # Arch/BIM 166 (typed FeaturePython)
  Align = 0
  Area = 9.36e+06
  Base = -> Line1707
  BlockHeight = 2000
  BlockLength = 150
  CountBroken = 33
  CountEntire = 0
  Face = 0
  Height = 1800
  HorizontalArea = 0
  IfcData = attributes={"GlobalId": {"name": "GlobalId", "type": "IfcGloballyUniqueId", "is_enum": false, "enum_values": []}, "Description": {"... (+533 chars omitted),+1 more (map truncated)
  IfcType = 166
  Joint = 10
  Length = 5200
  MakeBlocks = true
  Material = -> Material010
  MoveBase = false
  MoveWithHost = false
  Normal = (0,0,0)
  Offset = 125
  OffsetFirst = 100
  OffsetSecond = 0
  PerimeterLength = 0
  Placement = pos=(0,1.3642e-12,-120) rot=(0,0,1;0rad)
  PredefinedType = 0
  VerticalArea = 0
  Width = 50
FEATURE [Part::Part2DObjectPython] Line1708  # Draft 2D object (typed FeaturePython)
  Area = 0
  ChamferSize = 0
  Closed = true
  End = (17187.3,-8132.31,0)
  FilletRadius = 0
  Length = 5000
  MakeFace = true
  Placement = pos=(22054.4,-9277.51,0) rot=(0,0,1;1.33971rad)
  Points = (2) [(0.000188671,0.000898576,0),(0.000129816,5000,0)]
  Start = (22054.4,-9277.51,0)
  Subdivisions = 0
FEATURE [Part::FeaturePython] Wall314  label="Проём ворот 5м"  # Arch/BIM 166 (typed FeaturePython)
  Align = 0
  Area = 1e+07
  Base = -> Line1708
  BlockHeight = 0
  BlockLength = 0
  CountBroken = 0
  CountEntire = 0
  Face = 0
  Height = 2000
  HorizontalArea = 1e+06
  IfcData = attributes={"GlobalId": {"name": "GlobalId", "type": "IfcGloballyUniqueId", "is_enum": false, "enum_values": []}, "Description": {"... (+533 chars omitted),+1 more (map truncated)
  IfcType = 166
  Joint = 0
  Length = 5000
  MakeBlocks = false
  MoveBase = false
  MoveWithHost = false
  Normal = (0,0,0)
  OffsetFirst = 0
  OffsetSecond = 0
  PerimeterLength = 10400
  Placement = pos=(0,0,-320) rot=(0,0,1;0rad)
  PredefinedType = 0
  VerticalArea = 2.08e+07
  Width = 200
FEATURE [Part::FeaturePython] Space  label="Проём ворот"  # Arch/BIM 122 (typed FeaturePython)
  Area = 1e+06
  AutoPower = false
  Base = -> Wall314
  CompositionType = 0
  Conditioning = 0
  ElevationWithFlooring = -320
  EquipmentPower = 0
  FloorThickness = 0
  HorizontalArea = 1e+06
  IfcData = attributes={"GlobalId": {"name": "GlobalId", "type": "IfcGloballyUniqueId", "is_enum": false, "enum_values": []}, "Description": {"... (+888 chars omitted),+1 more (map truncated)
  IfcType = 122
  Internal = true
  LightingPower = 0
  LongName = Space
  MoveBase = false
  MoveWithHost = false
  NumberOfPeople = 0
  PerimeterLength = 10400
  PredefinedType = 0
  SpaceType = 0
  VerticalArea = 2.08e+07
  expr: ElevationWithFlooring = .Shape.BoundBox.ZMin
FEATURE [Part::Part2DObjectPython] Line1709  # Draft 2D object (typed FeaturePython)
  Area = 0
  ChamferSize = 0
  Closed = false
  End = (9400,-6300,0)
  FilletRadius = 0
  Length = 8000
  MakeFace = true
  Placement = pos=(17187.3,-8132.31,0) rot=(0,0,1;1.33971rad)
  Points = (2) [(0,0,0),(3.91992e-10,8000,0)]
  Start = (17187.3,-8132.31,0)
  Subdivisions = 0
FEATURE [Part::FeaturePython] Wall313  label="Зона отката ворот 7.5м"  # Arch/BIM 166 (typed FeaturePython)
  Align = 0
  Area = 1.6e+07
  Base = -> Line1709
  BlockHeight = 0
  BlockLength = 0
  CountBroken = 0
  CountEntire = 0
  Face = 0
  Height = 2000
  HorizontalArea = 1.6e+06
  IfcData = attributes={"GlobalId": {"name": "GlobalId", "type": "IfcGloballyUniqueId", "is_enum": false, "enum_values": []}, "Description": {"... (+533 chars omitted),+1 more (map truncated)
  IfcType = 166
  Joint = 0
  Length = 8000
  MakeBlocks = false
  MoveBase = false
  MoveWithHost = false
  Normal = (0,0,0)
  OffsetFirst = 0
  OffsetSecond = 0
  PerimeterLength = 16400
  Placement = pos=(0,0,-320) rot=(0,0,1;0rad)
  PredefinedType = 0
  VerticalArea = 3.28e+07
  Width = 200
FEATURE [Part::FeaturePython] Space001  label="Зона отката ворот "  # Arch/BIM 122 (typed FeaturePython)
  Area = 1.6e+06
  AutoPower = false
  Base = -> Wall313
  CompositionType = 0
  Conditioning = 0
  ElevationWithFlooring = -320
  EquipmentPower = 0
  FloorThickness = 0
  HorizontalArea = 1.6e+06
  IfcData = attributes={"GlobalId": {"name": "GlobalId", "type": "IfcGloballyUniqueId", "is_enum": false, "enum_values": []}, "Description": {"... (+888 chars omitted),+1 more (map truncated)
  IfcType = 122
  Internal = true
  LightingPower = 0
  LongName = Space
  MoveBase = false
  MoveWithHost = false
  NumberOfPeople = 0
  PerimeterLength = 16400
  PredefinedType = 0
  SpaceType = 0
  VerticalArea = 3.28e+07
  expr: ElevationWithFlooring = .Shape.BoundBox.ZMin
FEATURE [Part::FeaturePython] Structure458  label="Крыша бытовки"  # Arch/BIM 118 (typed FeaturePython)
  Base = -> Rectangle3402
  FaceMaker = 0
  Height = 50
  HorizontalArea = 1.38e+07
  IfcData = attributes={"GlobalId": {"name": "GlobalId", "type": "IfcGloballyUniqueId", "is_enum": false, "enum_values": []}, "Description": {"... (+453 chars omitted),+1 more (map truncated)
  IfcType = 118
  Length = 2300
  MoveBase = false
  MoveWithHost = false
  Nodes = (4) [(-5840.87,-8273.6,0),(66.7383,-7224.73,0),(-335.328,-4960.14,0),(-6242.94,-6009.01,0)]
  NodesOffset = 0
  Normal = (0,0,0)
  PerimeterLength = 16600
  Placement = pos=(0,0,2300) rot=(0,0,1;0rad)
  PredefinedType = 0
  VerticalArea = 830000
  Width = 6000
FEATURE [App::GeometryPython] BuildingPart033  label="хозблок (бытовка)"  # Arch/BIM 10 (typed FeaturePython)
  Area = 4.067e+07
  BuildingType = 0
  CompositionType = 0
  ElevationOfRefHeight = 0
  ElevationOfTerrain = 0
  Group = -> [Wall097,Structure458]
  Height = 0
  HeightPropagate = true
  IfcType = 10
  LevelOffset = 0
  LongName = хозблок (бытовка)
FEATURE [App::FeaturePython] Dimension072  # Draft dimension (typed FeaturePython)
  Diameter = false
  Dimline = (-1400,7200,0)
  Direction = (0,0,0)
  Distance = 738.353
  End = (-800,7685.58,0)
  Normal = (0,0,1)
  Start = (-800,6947.23,0)
FEATURE [App::FeaturePython] Dimension073  # Draft dimension (typed FeaturePython)
  Diameter = false
  Dimline = (-1400,7200,0)
  Direction = (0,0,0)
  Distance = 3217.23
  End = (-800,6947.23,0)
  Normal = (0,0,1)
  Start = (-800,3730,0)
FEATURE [App::FeaturePython] Dimension074  # Draft dimension (typed FeaturePython)
  Diameter = false
  Dimline = (-1400,7685.58,0)
  Direction = (0,0,0)
  Distance = 914.422
  End = (-800,8600,0)
  Normal = (0,0,1)
  Start = (-800,7685.58,0)
FEATURE [App::FeaturePython] Dimension075  # Draft dimension (typed FeaturePython)
  Diameter = false
  Dimline = (0,5100,2400)
  Direction = (0,0,0)
  Distance = 6448.76
  End = (0,6954.38,3045)
  Normal = (1,0,0)
  Start = (0,505.619,3045)
FEATURE [App::FeaturePython] Dimension076  # Draft dimension (typed FeaturePython)
  Diameter = false
  Dimline = (0,8900,4000)
  Direction = (0,0,0)
  Distance = 3013.88
  End = (0,9000,6796.88)
  Normal = (1,0,0)
  Start = (0,9000,3783)
FEATURE [App::FeaturePython] Dimension077  # Draft dimension (typed FeaturePython)
  Diameter = false
  Dimline = (0,5000,1500)
  Direction = (0,0,0)
  Distance = 9740
  End = (0,8600,3300)
  Normal = (1,0,0)
  Start = (0,-1140,3300)
FEATURE [App::FeaturePython] Dimension078  # Draft dimension (typed FeaturePython)
  Diameter = false
  Dimline = (0,5000,2000)
  Direction = (0,0,0)
  Distance = 7911.16
  End = (0,7685.58,2200)
  Normal = (1,0,0)
  Start = (0,-225.578,2200)
FEATURE [Part::Part2DObjectPython] Rectangle3389  # Draft 2D object (typed FeaturePython)
  Area = 2.45e+07
  ChamferSize = 0
  Columns = 1
  FilletRadius = 0
  Height = 7000
  Length = 3500
  MakeFace = true
  Placement = pos=(22359,-9231.91,0) rot=(0,0,1;1.34139rad)
  Rows = 1
FEATURE [Part::Part2DObjectPython] Line1687  # Draft 2D object (typed FeaturePython)
  Area = 0
  ChamferSize = 0
  Closed = false
  End = (-3580.3,-8530.19,0)
  FilletRadius = 0
  Length = 1000
  MakeFace = true
  Placement = pos=(-3755.12,-7545.59,0) rot=(0,0,1;1.52614rad)
  Points = (2) [(0,0,0),(-975.816,-218.595,0)]
  Start = (-3755.12,-7545.59,0)
  Subdivisions = 0
FEATURE [Part::Part2DObjectPython] Line1688  # Draft 2D object (typed FeaturePython)
  Area = 0
  ChamferSize = 0
  Closed = false
  End = (7519.32,-7540,0)
  FilletRadius = 0
  Length = 1000
  MakeFace = true
  Placement = pos=(7519.32,-6540,0) rot=(0,0,1;1.52614rad)
  Points = (2) [(0,0,0),(-999.003,-44.6455,0)]
  Start = (7519.32,-6540,0)
  Subdivisions = 0
FEATURE [Part::Part2DObjectPython] Line1689  # Draft 2D object (typed FeaturePython)
  Area = 0
  ChamferSize = 0
  Closed = false
  End = (9687.65,-6293.74,0)
  FilletRadius = 0
  Length = 12000
  MakeFace = true
  Placement = pos=(21282.4,-9385.88,0) rot=(0,0,1;1.52614rad)
  Points = (2) [(0,0,0),(2571.4,11721.3,0)]
  Start = (21282.4,-9385.88,0)
  Subdivisions = 0
FEATURE [Part::Part2DObjectPython] Line1690  # Draft 2D object (typed FeaturePython)
  Area = 0
  ChamferSize = 0
  Closed = false
  End = (1996.8,-7540,0)
  FilletRadius = 0
  Length = 1000
  MakeFace = true
  Placement = pos=(1996.8,-6540,0) rot=(0,0,1;1.52614rad)
  Points = (2) [(0,0,0),(-999.003,-44.6455,0)]
  Start = (1996.8,-6540,0)
  Subdivisions = 0
FEATURE [Part::Part2DObjectPython] Line1692  # Draft 2D object (typed FeaturePython)
  Area = 0
  ChamferSize = 0
  Closed = false
  End = (1996.8,-7540,0)
  FilletRadius = 0
  Length = 1000
  MakeFace = true
  Placement = pos=(1821.99,-6555.4,0) rot=(0,0,1;1.52614rad)
  Points = (2) [(0,0,0),(-975.816,-218.595,0)]
  Start = (1821.99,-6555.4,0)
  Subdivisions = 0
FEATURE [Part::Part2DObjectPython] Line1693  # Draft 2D object (typed FeaturePython)
  Area = 0
  ChamferSize = 0
  Closed = false
  End = (-9993.23,-8653.14,0)
  FilletRadius = 0
  Length = 12000
  MakeFace = true
  Placement = pos=(1821.99,-6555.4,0) rot=(0,0,1;1.52614rad)
  Points = (2) [(0,0,0),(-2623.14,11709.8,0)]
  Start = (1821.99,-6555.4,0)
  Subdivisions = 0
FEATURE [Part::Part2DObjectPython] Line1694  # Draft 2D object (typed FeaturePython)
  Area = 0
  ChamferSize = 0
  Closed = false
  End = (-9662.73,-8594.46,0)
  FilletRadius = 0
  Length = 12000
  MakeFace = true
  Placement = pos=(2152.5,-6496.72,0) rot=(0,0,1;1.52614rad)
  Points = (2) [(0,0,0),(-2623.14,11709.8,0)]
  Start = (2152.5,-6496.72,0)
  Subdivisions = 0
FEATURE [Part::Part2DObjectPython] Line1695  # Draft 2D object (typed FeaturePython)
  Area = 0
  ChamferSize = 0
  Closed = false
  End = (12611.1,-6540,0)
  FilletRadius = 0
  Length = 12000
  MakeFace = true
  Placement = pos=(611.062,-6540,0) rot=(0,0,1;1.52614rad)
  Points = (2) [(0,0,0),(535.746,-11988,0)]
  Start = (611.062,-6540,0)
  Subdivisions = 0
FEATURE [Part::Part2DObjectPython] Rectangle3390  # Draft 2D object (typed FeaturePython)
  Area = 144400
  ChamferSize = 0
  Columns = 1
  FilletRadius = 0
  Height = 380
  Length = 380
  MakeFace = true
  Placement = pos=(22825.7,-9411.26,0) rot=(0,0,1;1.52614rad)
  Rows = 1
FEATURE [Part::Part2DObjectPython] Rectangle3392  # Draft 2D object (typed FeaturePython)
  Area = 144400
  ChamferSize = 0
  Columns = 1
  FilletRadius = 0
  Height = 380
  Length = 380
  MakeFace = true
  Placement = pos=(24404.1,-9481.8,0) rot=(0,0,1;1.52614rad)
  Rows = 1
FEATURE [Part::Part2DObjectPython] Rectangle3393  # Draft 2D object (typed FeaturePython)
  Area = 144400
  ChamferSize = 0
  Columns = 1
  FilletRadius = 0
  Height = 380
  Length = 380
  MakeFace = true
  Placement = pos=(24644.3,-4107.17,0) rot=(0,0,1;1.52614rad)
  Rows = 1
FEATURE [Part::Part2DObjectPython] Rectangle3395  # Draft 2D object (typed FeaturePython)
  Area = 520000
  ChamferSize = 0
  Columns = 1
  FilletRadius = 0
  Height = 100
  Length = 5200
  MakeFace = true
  Placement = pos=(24037,-9185.12,0) rot=(0,0,1;1.52614rad)
  Rows = 1
FEATURE [Part::Part2DObjectPython] Circle135  label="Circle136"  # Draft 2D object (typed FeaturePython)
  Area = 1.05683e+06
  FirstAngle = 0
  LastAngle = 0
  MakeFace = true
  Placement = pos=(22885.9,-1376.75,0) rot=(0,0,1;1.52614rad)
  Radius = 580
FEATURE [Part::Part2DObjectPython] Line1697  # Draft 2D object (typed FeaturePython)
  Area = 0
  ChamferSize = 0
  Closed = false
  End = (24764.4,-1419.85,0)
  FilletRadius = 0
  Length = 1500
  MakeFace = false
  Placement = pos=(23265.9,-1352.88,0) rot=(0,0,1;1.52614rad)
  Points = (2) [(0,0,0),(-2.50111e-12,-1500,0)]
  Start = (23265.9,-1352.88,0)
  Subdivisions = 0
FEATURE [Part::Part2DObjectPython] Line1699  # Draft 2D object (typed FeaturePython)
  Area = 0
  ChamferSize = 0
  Closed = false
  End = (24840.3,278.455,0)
  FilletRadius = 0
  Length = 1300
  MakeFace = false
  Placement = pos=(23541.6,336.495,0) rot=(0,0,1;1.52614rad)
  Points = (2) [(0,0,0),(6.82121e-13,-1300,0)]
  Start = (23541.6,336.495,0)
  Subdivisions = 0
FEATURE [Part::Part2DObjectPython] Circle136  label="Circle137"  # Draft 2D object (typed FeaturePython)
  Area = 1.05683e+06
  FirstAngle = 0
  LastAngle = 0
  MakeFace = true
  Placement = pos=(22961.8,321.557,0) rot=(0,0,1;1.52614rad)
  Radius = 580
FEATURE [Part::Part2DObjectPython] Line1702  # Draft 2D object (typed FeaturePython)
  Area = 0
  ChamferSize = 0
  Closed = true
  End = (14388.6,662.218,0)
  FilletRadius = 0
  Length = 8000
  MakeFace = true
  Placement = pos=(22381.9,303.842,0) rot=(0,0,1;1.52614rad)
  Points = (2) [(38.1281,1.43103,0),(1.15288,8001.35,0)]
  Start = (22382.2,341.996,0)
  Subdivisions = 0
FEATURE [Part::Part2DObjectPython] Rectangle3400  # Draft 2D object (typed FeaturePython)
  Area = 2.45e+07
  ChamferSize = 0
  Columns = 1
  FilletRadius = 0
  Height = 7000
  Length = 3500
  MakeFace = true
  Placement = pos=(22181.1,-5596.2,0) rot=(0,0,1;1.34139rad)
  Rows = 1
FEATURE [Part::Part2DObjectPython] Line1704  # Draft 2D object (typed FeaturePython)
  Area = 0
  ChamferSize = 0
  Closed = false
  End = (14360.8,-420.719,0)
  FilletRadius = 0
  Length = 5100
  MakeFace = false
  Placement = pos=(19455.7,-648.412,0) rot=(0,0,1;0.025758rad)
  Points = (2) [(0,0,0),(-5087.36,358.837,0)]
  Start = (19455.7,-648.412,0)
  Subdivisions = 0
FEATURE [Part::Part2DObjectPython] Circle140  label="Circle141"  # Draft 2D object (typed FeaturePython)
  Area = 1.05683e+06
  FirstAngle = 0
  LastAngle = 0
  MakeFace = true
  Placement = pos=(21460.2,-1031.22,0) rot=(0,0,1;1.52614rad)
  Radius = 580
FEATURE [Part::Part2DObjectPython] Circle141  label="Circle142"  # Draft 2D object (typed FeaturePython)
  Area = 1.05683e+06
  FirstAngle = 0
  LastAngle = 0
  MakeFace = true
  Placement = pos=(20034.5,-685.694,0) rot=(0,0,1;1.52614rad)
  Radius = 580
FEATURE [Part::Part2DObjectPython] Line1705  # Draft 2D object (typed FeaturePython)
  Area = 0
  ChamferSize = 0
  Closed = true
  End = (22885.9,-1376.75,0)
  FilletRadius = 0
  Length = 2933.93
  MakeFace = false
  Placement = pos=(19875.5,-436.151,0) rot=(0,0,1;0.025758rad)
  Points = (2) [(152.568,-253.556,0),(2985.21,-1017.82,0)]
  Start = (20034.5,-685.694,0)
  Subdivisions = 0
FEATURE [Part::Part2DObjectPython] Circle142  label="Circle143"  # Draft 2D object (typed FeaturePython)
  Area = 1.05683e+06
  FirstAngle = 0
  LastAngle = 0
  MakeFace = true
  Placement = pos=(-7874.87,-6660.56,0) rot=(0,0,1;1.52614rad)
  Radius = 580
FEATURE [Part::Part2DObjectPython] Rectangle3401  # Draft 2D object (typed FeaturePython)
  Area = 9.2e+06
  ChamferSize = 0
  Columns = 1
  FilletRadius = 0
  Height = 2300
  Length = 4000
  MakeFace = true
  Placement = pos=(23704,1728.87,0) rot=(0,0,1;1.52614rad)
  Rows = 1
FEATURE [Part::Part2DObjectPython] Line1706  # Draft 2D object (typed FeaturePython)
  Area = 0
  ChamferSize = 0
  Closed = false
  End = (-8436.54,-6805.24,0)
  FilletRadius = 0
  Length = 1200
  MakeFace = true
  Placement = pos=(-9598.6,-7104.59,0) rot=(0,0,1;1.52614rad)
  Points = (2) [(0,0,0),(350.925,-1147.54,0)]
  Start = (-9598.6,-7104.59,0)
  Subdivisions = 0
FEATURE [Part::Part2DObjectPython] Line1710  # Draft 2D object (typed FeaturePython)
  Area = 0
  ChamferSize = 0
  Closed = false
  End = (14360.8,-7540,0)
  FilletRadius = 0
  Length = 6000
  MakeFace = true
  Placement = pos=(14360.8,-1540,0) rot=(0,0,-1;0.04466rad)
  Points = (2) [(0,0,0),(267.873,-5994.02,0)]
  Start = (14360.8,-1540,0)
  Subdivisions = 0
FEATURE [Part::Part2DObjectPython] Line1711  # Draft 2D object (typed FeaturePython)
  Area = 0
  ChamferSize = 0
  Closed = false
  End = (22185.4,-9292.56,0)
  FilletRadius = 0
  Length = 1800
  MakeFace = true
  Placement = pos=(23983.6,-9372.92,0) rot=(0,0,-1;0.04466rad)
  Points = (2) [(0,0,0),(-1800,-8.73115e-11,0)]
  Start = (23983.6,-9372.92,0)
  Subdivisions = 0
FEATURE [Part::Part2DObjectPython] Line1712  # Draft 2D object (typed FeaturePython)
  Area = 0
  ChamferSize = 0
  Closed = false
  End = (10611.1,-6540,0)
  FilletRadius = 0
  Length = 12157.5
  MakeFace = true
  Placement = pos=(22450.1,-9304.39,0) rot=(0,0,-1;0.04466rad)
  Points = (2) [(0,0,0),(-11950.7,2233.07,0)]
  Start = (22450.1,-9304.39,0)
  Subdivisions = 0
FEATURE [Part::Part2DObjectPython] Line1713  # Draft 2D object (typed FeaturePython)
  Area = 0
  ChamferSize = 0
  Closed = false
  End = (24571.4,-3723.53,0)
  FilletRadius = 0
  Length = 90
  MakeFace = true
  Placement = pos=(24661.3,-3727.55,0) rot=(0,0,-1;0.04466rad)
  Points = (2) [(0,0,0),(-90,1.36424e-12,0)]
  Start = (24661.3,-3727.55,0)
  Subdivisions = 0
FEATURE [Part::Part2DObjectPython] Rectangle3403  label="Контур Строения002"  # Draft 2D object (typed FeaturePython)
  Area = 0
  ChamferSize = 0
  Columns = 1
  FilletRadius = 0
  Height = 8540
  Length = 13640
  MakeFace = false
  Placement = pos=(-560,-540,0) rot=(0,0,1;0rad)
  Rows = 1
FEATURE [Part::Part2DObjectPython] Line1714  # Draft 2D object (typed FeaturePython)
  Area = 0
  ChamferSize = 0
  Closed = false
  End = (-34430.2,9739.91,0)
  FilletRadius = 0
  Length = 7432.67
  MakeFace = true
  Placement = pos=(-41420.8,7214.83,0) rot=(0,0,-1;0.04466rad)
  Points = (2) [(0,0,0),(6870.9,2834.66,0)]
  Start = (-41420.8,7214.83,0)
  Subdivisions = 0
FEATURE [Part::Part2DObjectPython] Line1715  # Draft 2D object (typed FeaturePython)
  Area = 0
  ChamferSize = 0
  Closed = false
  End = (-41420.8,7214.83,0)
  FilletRadius = 0
  Length = 5559.77
  MakeFace = true
  Placement = pos=(-39131,2148.46,0) rot=(0,0,-1;0.04466rad)
  Points = (2) [(0,0,0),(-2513.65,4959.09,0)]
  Start = (-39131,2148.46,0)
  Subdivisions = 0
FEATURE [Part::Part2DObjectPython] Line1716  # Draft 2D object (typed FeaturePython)
  Area = 0
  ChamferSize = 0
  Closed = false
  End = (39960.8,38650.8,0)
  FilletRadius = 0
  Length = 6490.01
  MakeFace = true
  Placement = pos=(37704.2,32565.7,0) rot=(0,0,-1;0.04466rad)
  Points = (2) [(0,0,0),(1982.64,6179.75,0)]
  Start = (37704.2,32565.7,0)
  Subdivisions = 0
FEATURE [Part::Part2DObjectPython] Line1717  # Draft 2D object (typed FeaturePython)
  Area = 0
  ChamferSize = 0
  Closed = false
  End = (39960.8,38650.8,0)
  FilletRadius = 0
  Length = 8107.57
  MakeFace = true
  Placement = pos=(32209.4,41027.5,0) rot=(0,0,-1;0.04466rad)
  Points = (2) [(0,0,0),(7849.75,-2028.32,0)]
  Start = (32209.4,41027.5,0)
  Subdivisions = 0
FEATURE [Part::Part2DObjectPython] Line1718  # Draft 2D object (typed FeaturePython)
  Area = 0
  ChamferSize = 0
  Closed = false
  End = (6260,-6540,0)
  FilletRadius = 0
  Length = 6000
  MakeFace = true
  Placement = pos=(6260,-540,0) rot=(0,0,1;1.52614rad)
  Points = (2) [(0,0,0),(-5994.02,-267.873,0)]
  Start = (6260,-540,0)
  Subdivisions = 0
FEATURE [Part::Part2DObjectPython] Line1719  # Draft 2D object (typed FeaturePython)
  Area = 0
  ChamferSize = 0
  Closed = false
  End = (6198,-7540,0)
  FilletRadius = 0
  Length = 5610
  MakeFace = true
  Placement = pos=(6198,-1930,0) rot=(0,0,1;1.52614rad)
  Points = (2) [(0,0,0),(-5604.41,-250.461,0)]
  Start = (6198,-1930,0)
  Subdivisions = 0
FEATURE [Sketcher::SketchObject] Sketch369
  FullyConstrained = true
  Placement = pos=(2535,3115,0) rot=(1,0,0;1.5708rad)
  sketch-geometry (8):
    g0: LineSegment StartX=0 StartY=0 StartZ=0 EndX=900 EndY=0 EndZ=0
    g1: LineSegment StartX=900 StartY=0 StartZ=0 EndX=900 EndY=2400 EndZ=0
    g2: LineSegment StartX=900 StartY=2400 StartZ=0 EndX=0 EndY=2400 EndZ=0
    g3: LineSegment StartX=0 StartY=2400 StartZ=0 EndX=0 EndY=0 EndZ=0
    g4: LineSegment StartX=50 StartY=0 StartZ=0 EndX=850 EndY=0 EndZ=0
    g5: LineSegment StartX=850 StartY=0 StartZ=0 EndX=850 EndY=2350 EndZ=0
    g6: LineSegment StartX=850 StartY=2350 StartZ=0 EndX=50 EndY=2350 EndZ=0
    g7: LineSegment StartX=50 StartY=2350 StartZ=0 EndX=50 EndY=0 EndZ=0
  constraints (23):
    c: Coincident(g0,g1)
    c: Coincident(g1,g2)
    c: Coincident(g2,g3)
    c: Coincident(g3,g0)
    c: Horizontal(g0)
    c: Horizontal(g2)
    c: Vertical(g1)
    c: Vertical(g3)
    c: Coincident(g4,g5)
    c: Coincident(g5,g6)
    c: Coincident(g6,g7)
    c: Coincident(g7,g4)
    c: Horizontal(g4)
    c: Horizontal(g6)
    c: Vertical(g5)
    c: Vertical(g7)
    c: DistanceY(g1) = 2400  'Height'
    c: DistanceX(g0) = 900  'Width'
    c: DistanceY(g6,g2) = 50  'Frame1'
    c: DistanceX(g2,g6) = 50  'Frame2'
    c: DistanceX(g4,g0) = 50  'Frame3'
    c: DistanceY(g0,g4) = 0
    c: Coincident(g0,g-1)
FEATURE [Part::FeaturePython] Window068  label="Д-90-006"  # Arch/BIM 41 (typed FeaturePython)
  Area = 2160000
  Base = -> Sketch369
  Frame = 50
  GlobalId = 00iW5F1Zz0_RepVZ61wedb
  Height = 2400
  HoleDepth = 0
  HoleWire = 0
  HorizontalArea = 0
  IfcData = IfcUID=00iW5F1Zz0_RepVZ61wedb; attributes={"OverallHeight": {"value": 2400.0}, "OverallWidth": {"value": 900.0}, "GlobalId": {"value": "00iW5F1Zz0_RepVZ61wedb"}}
  IfcType = 41
  LouvreSpacing = 0
  LouvreWidth = 0
  Material = -> Material011
  MoveBase = false
  MoveWithHost = true
  Normal = (0,1,0)
  Opening = 0
  OperationType = 0
  OverallHeight = 2400
  OverallWidth = 900
  PerimeterLength = 0
  Placement = pos=(0,30,0) rot=(0,0,1;0rad)
  PredefinedType = 0
  Preset = 6
  SymbolElevation = false
  SymbolPlan = false
  VerticalArea = 0
  Width = 900
  WindowParts = OuterFrame | Frame | Wire0,Wire1 | 0.0+V | 0.00+V | Door | Solid panel | Wire1 | 50.0 | 0.0+V
  expr: OverallWidth = .Width.Value
  expr: OverallHeight = .Height.Value
FEATURE [Sketcher::SketchObject] Sketch371
  FullyConstrained = true
  Placement = pos=(3145,8805,955) rot=(0,0.707107,0.707107;3.14159rad)
  sketch-geometry (24):
    g0: LineSegment StartX=0 StartY=0 StartZ=0 EndX=1960 EndY=0 EndZ=0
    g1: LineSegment StartX=1960 StartY=0 StartZ=0 EndX=1960 EndY=1605 EndZ=0
    g2: LineSegment StartX=1960 StartY=1605 StartZ=0 EndX=0 EndY=1605 EndZ=0
    g3: LineSegment StartX=0 StartY=1605 StartZ=0 EndX=0 EndY=0 EndZ=0
    g4: LineSegment StartX=70 StartY=70 StartZ=0 EndX=1890 EndY=70 EndZ=0
    g5: LineSegment StartX=1890 StartY=70 StartZ=0 EndX=1890 EndY=1535 EndZ=0
    g6: LineSegment StartX=1890 StartY=1535 StartZ=0 EndX=70 EndY=1535 EndZ=0
    g7: LineSegment StartX=70 StartY=1535 StartZ=0 EndX=70 EndY=70 EndZ=0
    g8: LineSegment StartX=77 StartY=77 StartZ=0 EndX=976.5 EndY=77 EndZ=0
    g9: LineSegment StartX=976.5 StartY=77 StartZ=0 EndX=976.5 EndY=1528 EndZ=0
    g10: LineSegment StartX=976.5 StartY=1528 StartZ=0 EndX=77 EndY=1528 EndZ=0
    g11: LineSegment StartX=77 StartY=1528 StartZ=0 EndX=77 EndY=77 EndZ=0
    g12: LineSegment StartX=117 StartY=117 StartZ=0 EndX=936.5 EndY=117 EndZ=0
    g13: LineSegment StartX=936.5 StartY=117 StartZ=0 EndX=936.5 EndY=1488 EndZ=0
    g14: LineSegment StartX=936.5 StartY=1488 StartZ=0 EndX=117 EndY=1488 EndZ=0
    g15: LineSegment StartX=117 StartY=1488 StartZ=0 EndX=117 EndY=117 EndZ=0
    g16: LineSegment StartX=983.5 StartY=77 StartZ=0 EndX=1883 EndY=77 EndZ=0
    g17: LineSegment StartX=1883 StartY=77 StartZ=0 EndX=1883 EndY=1528 EndZ=0
    g18: LineSegment StartX=1883 StartY=1528 StartZ=0 EndX=983.5 EndY=1528 EndZ=0
    g19: LineSegment StartX=983.5 StartY=1528 StartZ=0 EndX=983.5 EndY=77 EndZ=0
    g20: LineSegment StartX=1023.5 StartY=117 StartZ=0 EndX=1843 EndY=117 EndZ=0
    g21: LineSegment StartX=1843 StartY=117 StartZ=0 EndX=1843 EndY=1488 EndZ=0
    g22: LineSegment StartX=1843 StartY=1488 StartZ=0 EndX=1023.5 EndY=1488 EndZ=0
    g23: LineSegment StartX=1023.5 StartY=1488 StartZ=0 EndX=1023.5 EndY=117 EndZ=0
  constraints (71):
    c: Coincident(g0,g1)
    c: Coincident(g1,g2)
    c: Coincident(g2,g3)
    c: Coincident(g3,g0)
    c: Horizontal(g0)
    c: Horizontal(g2)
    c: Vertical(g1)
    c: Vertical(g3)
    c: Coincident(g4,g5)
    c: Coincident(g5,g6)
    c: Coincident(g6,g7)
    c: Coincident(g7,g4)
    c: Horizontal(g4)
    c: Horizontal(g6)
    c: Vertical(g5)
    c: Vertical(g7)
    c: DistanceY(g1) = 1605  'Height'
    c: DistanceX(g0) = 1960  'Width'
    c: DistanceY(g6,g2) = 70  'Frame1'
    c: DistanceX(g2,g6) = 70  'Frame2'
    c: DistanceX(g4,g0) = 70  'Frame3'
    c: DistanceY(g0,g4) = 70  'Frame4'
    c: Coincident(g0,g-1)
    c: Coincident(g8,g9)
    c: Coincident(g9,g10)
    c: Coincident(g10,g11)
    c: Coincident(g11,g8)
    c: Horizontal(g8)
    c: Horizontal(g10)
    c: Vertical(g9)
    c: Vertical(g11)
    c: Coincident(g12,g13)
    c: Coincident(g13,g14)
    c: Coincident(g14,g15)
    c: Coincident(g15,g12)
    c: Horizontal(g12)
    c: Horizontal(g14)
    c: Vertical(g13)
    c: Vertical(g15)
    c: Coincident(g16,g17)
    c: Coincident(g17,g18)
    c: Coincident(g18,g19)
    c: Coincident(g19,g16)
    c: Horizontal(g16)
    c: Horizontal(g18)
    c: Vertical(g17)
    c: Vertical(g19)
    c: Coincident(g20,g21)
    c: Coincident(g21,g22)
    c: Coincident(g22,g23)
    c: Coincident(g23,g20)
    c: Horizontal(g20)
    c: Horizontal(g22)
    c: Vertical(g21)
    c: Vertical(g23)
    c: DistanceY(g8,g12) = 40
    c: DistanceX(g8,g12) = 40
    c: DistanceX(g21,g17) = 40
    c: DistanceY(g21,g17) = 40
    c: DistanceX(g16,g20) = 40
    c: DistanceX(g14,g10) = 40
    c: Equal(g22,g14)
    c: DistanceY(g8,g16) = 0
    c: DistanceY(g10,g18) = 0
    c: DistanceX(g4,g8) = 7
    c: DistanceY(g4,g8) = 7
    c: DistanceX(g6,g18) = -7
    c: DistanceY(g6,g18) = -7
    c: DistanceX(g9,g19) = 7
    c: PointOnObject(g13,g22)
    c: PointOnObject(g20,g12)
FEATURE [Part::FeaturePython] Window069  label="ОК-5-001"  # Arch/BIM 170 (typed FeaturePython)
  Area = 3145800
  Base = -> Sketch371
  Frame = 70
  Height = 1605
  HoleDepth = 0
  HoleWire = 0
  HorizontalArea = 0
  IfcData = attributes={"GlobalId": {"name": "GlobalId", "type": "IfcGloballyUniqueId", "is_enum": false, "enum_values": []}, "Description": {"... (+1231 chars omitted),+1 more (map truncated)
  IfcType = 170
  LouvreSpacing = 0
  LouvreWidth = 0
  Material = -> Material011
  MoveBase = false
  MoveWithHost = true
  Normal = (0,-1,2e-16)
  Opening = 0
  OverallHeight = 1605
  OverallWidth = 1960
  PartitioningType = 0
  PerimeterLength = 0
  PredefinedType = 0
  Preset = 3
  SymbolElevation = false
  SymbolPlan = false
  VerticalArea = 0
  Width = 1960
  WindowParts = OuterFrame | Frame | Wire0,Wire1 | 0.0+V | 0.00+V | LeftFrame | Frame | Wire2,Wire3,Edge8,Mode1 | 0.00+V | 0.0+V | LeftGlass | Glass panel | Wire3 | 8.0 | 40.0+V | RightFrame | Frame | Wire4,Wire5,Edge6,Mode2 | 0.00+V | 0.0+V | RightGlass | Glass panel | Wire5 | 8.0 | 40.0+V
  expr: OverallWidth = .Width.Value
  expr: OverallHeight = .Height.Value
FEATURE [Sketcher::SketchObject] Sketch372
  FullyConstrained = true
  Placement = pos=(-440,3020,955) rot=(0.57735,-0.57735,-0.57735;2.0944rad)
  sketch-geometry (24):
    g0: LineSegment StartX=0 StartY=0 StartZ=0 EndX=1700 EndY=0 EndZ=0
    g1: LineSegment StartX=1700 StartY=0 StartZ=0 EndX=1700 EndY=1605 EndZ=0
    g2: LineSegment StartX=1700 StartY=1605 StartZ=0 EndX=0 EndY=1605 EndZ=0
    g3: LineSegment StartX=0 StartY=1605 StartZ=0 EndX=0 EndY=0 EndZ=0
    g4: LineSegment StartX=70 StartY=70 StartZ=0 EndX=1630 EndY=70 EndZ=0
    g5: LineSegment StartX=1630 StartY=70 StartZ=0 EndX=1630 EndY=1535 EndZ=0
    g6: LineSegment StartX=1630 StartY=1535 StartZ=0 EndX=70 EndY=1535 EndZ=0
    g7: LineSegment StartX=70 StartY=1535 StartZ=0 EndX=70 EndY=70 EndZ=0
    g8: LineSegment StartX=77 StartY=77 StartZ=0 EndX=846.5 EndY=77 EndZ=0
    g9: LineSegment StartX=846.5 StartY=77 StartZ=0 EndX=846.5 EndY=1528 EndZ=0
    g10: LineSegment StartX=846.5 StartY=1528 StartZ=0 EndX=77 EndY=1528 EndZ=0
    g11: LineSegment StartX=77 StartY=1528 StartZ=0 EndX=77 EndY=77 EndZ=0
    g12: LineSegment StartX=117 StartY=117 StartZ=0 EndX=806.5 EndY=117 EndZ=0
    g13: LineSegment StartX=806.5 StartY=117 StartZ=0 EndX=806.5 EndY=1488 EndZ=0
    g14: LineSegment StartX=806.5 StartY=1488 StartZ=0 EndX=117 EndY=1488 EndZ=0
    g15: LineSegment StartX=117 StartY=1488 StartZ=0 EndX=117 EndY=117 EndZ=0
    g16: LineSegment StartX=853.5 StartY=77 StartZ=0 EndX=1623 EndY=77 EndZ=0
    g17: LineSegment StartX=1623 StartY=77 StartZ=0 EndX=1623 EndY=1528 EndZ=0
    g18: LineSegment StartX=1623 StartY=1528 StartZ=0 EndX=853.5 EndY=1528 EndZ=0
    g19: LineSegment StartX=853.5 StartY=1528 StartZ=0 EndX=853.5 EndY=77 EndZ=0
    g20: LineSegment StartX=893.5 StartY=117 StartZ=0 EndX=1583 EndY=117 EndZ=0
    g21: LineSegment StartX=1583 StartY=117 StartZ=0 EndX=1583 EndY=1488 EndZ=0
    g22: LineSegment StartX=1583 StartY=1488 StartZ=0 EndX=893.5 EndY=1488 EndZ=0
    g23: LineSegment StartX=893.5 StartY=1488 StartZ=0 EndX=893.5 EndY=117 EndZ=0
  constraints (71):
    c: Coincident(g0,g1)
    c: Coincident(g1,g2)
    c: Coincident(g2,g3)
    c: Coincident(g3,g0)
    c: Horizontal(g0)
    c: Horizontal(g2)
    c: Vertical(g1)
    c: Vertical(g3)
    c: Coincident(g4,g5)
    c: Coincident(g5,g6)
    c: Coincident(g6,g7)
    c: Coincident(g7,g4)
    c: Horizontal(g4)
    c: Horizontal(g6)
    c: Vertical(g5)
    c: Vertical(g7)
    c: DistanceY(g1) = 1605  'Height'
    c: DistanceX(g0) = 1700  'Width'
    c: DistanceY(g6,g2) = 70  'Frame1'
    c: DistanceX(g2,g6) = 70  'Frame2'
    c: DistanceX(g4,g0) = 70  'Frame3'
    c: DistanceY(g0,g4) = 70  'Frame4'
    c: Coincident(g0,g-1)
    c: Coincident(g8,g9)
    c: Coincident(g9,g10)
    c: Coincident(g10,g11)
    c: Coincident(g11,g8)
    c: Horizontal(g8)
    c: Horizontal(g10)
    c: Vertical(g9)
    c: Vertical(g11)
    c: Coincident(g12,g13)
    c: Coincident(g13,g14)
    c: Coincident(g14,g15)
    c: Coincident(g15,g12)
    c: Horizontal(g12)
    c: Horizontal(g14)
    c: Vertical(g13)
    c: Vertical(g15)
    c: Coincident(g16,g17)
    c: Coincident(g17,g18)
    c: Coincident(g18,g19)
    c: Coincident(g19,g16)
    c: Horizontal(g16)
    c: Horizontal(g18)
    c: Vertical(g17)
    c: Vertical(g19)
    c: Coincident(g20,g21)
    c: Coincident(g21,g22)
    c: Coincident(g22,g23)
    c: Coincident(g23,g20)
    c: Horizontal(g20)
    c: Horizontal(g22)
    c: Vertical(g21)
    c: Vertical(g23)
    c: DistanceY(g8,g12) = 40
    c: DistanceX(g8,g12) = 40
    c: DistanceX(g21,g17) = 40
    c: DistanceY(g21,g17) = 40
    c: DistanceX(g16,g20) = 40
    c: DistanceX(g14,g10) = 40
    c: Equal(g22,g14)
    c: DistanceY(g8,g16) = 0
    c: DistanceY(g10,g18) = 0
    c: DistanceX(g4,g8) = 7
    c: DistanceY(g4,g8) = 7
    c: DistanceX(g6,g18) = -7
    c: DistanceY(g6,g18) = -7
    c: DistanceX(g9,g19) = 7
    c: PointOnObject(g13,g22)
    c: PointOnObject(g20,g12)
FEATURE [Part::FeaturePython] Window070  label="ОК-2-001"  # Arch/BIM 170 (typed FeaturePython)
  Area = 2728500
  Base = -> Sketch372
  Frame = 70
  Height = 1605
  HoleDepth = 0
  HoleWire = 0
  HorizontalArea = 0
  IfcData = attributes={"GlobalId": {"name": "GlobalId", "type": "IfcGloballyUniqueId", "is_enum": false, "enum_values": []}, "Description": {"... (+1231 chars omitted),+1 more (map truncated)
  IfcType = 170
  LouvreSpacing = 0
  LouvreWidth = 0
  Material = -> Material011
  MoveBase = false
  MoveWithHost = true
  Normal = (1,0,0)
  Opening = 0
  OverallHeight = 1605
  OverallWidth = 1700
  PartitioningType = 0
  PerimeterLength = 0
  PredefinedType = 0
  Preset = 3
  SymbolElevation = false
  SymbolPlan = false
  VerticalArea = 0
  Width = 1700
  WindowParts = <same value as first occurrence — deduplicated (x4 in doc)>
  expr: OverallWidth = .Width.Value
  expr: OverallHeight = .Height.Value
FEATURE [Sketcher::SketchObject] Sketch373
  FullyConstrained = true
  Placement = pos=(11010,3540,955) rot=(0.57735,0.57735,0.57735;2.0944rad)
  sketch-geometry (24):
    g0: LineSegment StartX=0 StartY=0 StartZ=0 EndX=1700 EndY=0 EndZ=0
    g1: LineSegment StartX=1700 StartY=0 StartZ=0 EndX=1700 EndY=1605 EndZ=0
    g2: LineSegment StartX=1700 StartY=1605 StartZ=0 EndX=0 EndY=1605 EndZ=0
    g3: LineSegment StartX=0 StartY=1605 StartZ=0 EndX=0 EndY=0 EndZ=0
    g4: LineSegment StartX=70 StartY=70 StartZ=0 EndX=1630 EndY=70 EndZ=0
    g5: LineSegment StartX=1630 StartY=70 StartZ=0 EndX=1630 EndY=1535 EndZ=0
    g6: LineSegment StartX=1630 StartY=1535 StartZ=0 EndX=70 EndY=1535 EndZ=0
    g7: LineSegment StartX=70 StartY=1535 StartZ=0 EndX=70 EndY=70 EndZ=0
    g8: LineSegment StartX=77 StartY=77 StartZ=0 EndX=846.5 EndY=77 EndZ=0
    g9: LineSegment StartX=846.5 StartY=77 StartZ=0 EndX=846.5 EndY=1528 EndZ=0
    g10: LineSegment StartX=846.5 StartY=1528 StartZ=0 EndX=77 EndY=1528 EndZ=0
    g11: LineSegment StartX=77 StartY=1528 StartZ=0 EndX=77 EndY=77 EndZ=0
    g12: LineSegment StartX=117 StartY=117 StartZ=0 EndX=806.5 EndY=117 EndZ=0
    g13: LineSegment StartX=806.5 StartY=117 StartZ=0 EndX=806.5 EndY=1488 EndZ=0
    g14: LineSegment StartX=806.5 StartY=1488 StartZ=0 EndX=117 EndY=1488 EndZ=0
    g15: LineSegment StartX=117 StartY=1488 StartZ=0 EndX=117 EndY=117 EndZ=0
    g16: LineSegment StartX=853.5 StartY=77 StartZ=0 EndX=1623 EndY=77 EndZ=0
    g17: LineSegment StartX=1623 StartY=77 StartZ=0 EndX=1623 EndY=1528 EndZ=0
    g18: LineSegment StartX=1623 StartY=1528 StartZ=0 EndX=853.5 EndY=1528 EndZ=0
    g19: LineSegment StartX=853.5 StartY=1528 StartZ=0 EndX=853.5 EndY=77 EndZ=0
    g20: LineSegment StartX=893.5 StartY=117 StartZ=0 EndX=1583 EndY=117 EndZ=0
    g21: LineSegment StartX=1583 StartY=117 StartZ=0 EndX=1583 EndY=1488 EndZ=0
    g22: LineSegment StartX=1583 StartY=1488 StartZ=0 EndX=893.5 EndY=1488 EndZ=0
    g23: LineSegment StartX=893.5 StartY=1488 StartZ=0 EndX=893.5 EndY=117 EndZ=0
  constraints (71):
    c: Coincident(g0,g1)
    c: Coincident(g1,g2)
    c: Coincident(g2,g3)
    c: Coincident(g3,g0)
    c: Horizontal(g0)
    c: Horizontal(g2)
    c: Vertical(g1)
    c: Vertical(g3)
    c: Coincident(g4,g5)
    c: Coincident(g5,g6)
    c: Coincident(g6,g7)
    c: Coincident(g7,g4)
    c: Horizontal(g4)
    c: Horizontal(g6)
    c: Vertical(g5)
    c: Vertical(g7)
    c: DistanceY(g1) = 1605  'Height'
    c: DistanceX(g0) = 1700  'Width'
    c: DistanceY(g6,g2) = 70  'Frame1'
    c: DistanceX(g2,g6) = 70  'Frame2'
    c: DistanceX(g4,g0) = 70  'Frame3'
    c: DistanceY(g0,g4) = 70  'Frame4'
    c: Coincident(g0,g-1)
    c: Coincident(g8,g9)
    c: Coincident(g9,g10)
    c: Coincident(g10,g11)
    c: Coincident(g11,g8)
    c: Horizontal(g8)
    c: Horizontal(g10)
    c: Vertical(g9)
    c: Vertical(g11)
    c: Coincident(g12,g13)
    c: Coincident(g13,g14)
    c: Coincident(g14,g15)
    c: Coincident(g15,g12)
    c: Horizontal(g12)
    c: Horizontal(g14)
    c: Vertical(g13)
    c: Vertical(g15)
    c: Coincident(g16,g17)
    c: Coincident(g17,g18)
    c: Coincident(g18,g19)
    c: Coincident(g19,g16)
    c: Horizontal(g16)
    c: Horizontal(g18)
    c: Vertical(g17)
    c: Vertical(g19)
    c: Coincident(g20,g21)
    c: Coincident(g21,g22)
    c: Coincident(g22,g23)
    c: Coincident(g23,g20)
    c: Horizontal(g20)
    c: Horizontal(g22)
    c: Vertical(g21)
    c: Vertical(g23)
    c: DistanceY(g8,g12) = 40
    c: DistanceX(g8,g12) = 40
    c: DistanceX(g21,g17) = 40
    c: DistanceY(g21,g17) = 40
    c: DistanceX(g16,g20) = 40
    c: DistanceX(g14,g10) = 40
    c: Equal(g22,g14)
    c: DistanceY(g8,g16) = 0
    c: DistanceY(g10,g18) = 0
    c: DistanceX(g4,g8) = 7
    c: DistanceY(g4,g8) = 7
    c: DistanceX(g6,g18) = -7
    c: DistanceY(g6,g18) = -7
    c: DistanceX(g9,g19) = 7
    c: PointOnObject(g13,g22)
    c: PointOnObject(g20,g12)
FEATURE [Part::FeaturePython] Window071  label="ОК-4-001"  # Arch/BIM 170 (typed FeaturePython)
  Area = 2728500
  Base = -> Sketch373
  Frame = 70
  Height = 1605
  HoleDepth = 0
  HoleWire = 0
  HorizontalArea = 0
  IfcData = attributes={"GlobalId": {"name": "GlobalId", "type": "IfcGloballyUniqueId", "is_enum": false, "enum_values": []}, "Description": {"... (+1231 chars omitted),+1 more (map truncated)
  IfcType = 170
  LouvreSpacing = 0
  LouvreWidth = 0
  Material = -> Material011
  MoveBase = false
  MoveWithHost = true
  Normal = (-1,0,0)
  Opening = 0
  OverallHeight = 1605
  OverallWidth = 1700
  PartitioningType = 0
  PerimeterLength = 0
  PredefinedType = 0
  Preset = 3
  SymbolElevation = false
  SymbolPlan = false
  VerticalArea = 0
  Width = 1700
  WindowParts = <same value as first occurrence — deduplicated (x4 in doc)>
  expr: OverallWidth = .Width.Value
  expr: OverallHeight = .Height.Value
FEATURE [Sketcher::SketchObject] Sketch375
  FullyConstrained = true
  Placement = pos=(2745,-435,955) rot=(1,0,0;1.5708rad)
  sketch-geometry (16):
    g0: LineSegment StartX=0 StartY=0 StartZ=0 EndX=660 EndY=0 EndZ=0
    g1: LineSegment StartX=660 StartY=0 StartZ=0 EndX=660 EndY=1605 EndZ=0
    g2: LineSegment StartX=660 StartY=1605 StartZ=0 EndX=0 EndY=1605 EndZ=0
    g3: LineSegment StartX=0 StartY=1605 StartZ=0 EndX=0 EndY=0 EndZ=0
    g4: LineSegment StartX=70 StartY=70 StartZ=0 EndX=590 EndY=70 EndZ=0
    g5: LineSegment StartX=590 StartY=70 StartZ=0 EndX=590 EndY=1535 EndZ=0
    g6: LineSegment StartX=590 StartY=1535 StartZ=0 EndX=70 EndY=1535 EndZ=0
    g7: LineSegment StartX=70 StartY=1535 StartZ=0 EndX=70 EndY=70 EndZ=0
    g8: LineSegment StartX=77 StartY=77 StartZ=0 EndX=583 EndY=77 EndZ=0
    g9: LineSegment StartX=583 StartY=77 StartZ=0 EndX=583 EndY=1528 EndZ=0
    g10: LineSegment StartX=583 StartY=1528 StartZ=0 EndX=77 EndY=1528 EndZ=0
    g11: LineSegment StartX=77 StartY=1528 StartZ=0 EndX=77 EndY=77 EndZ=0
    g12: LineSegment StartX=117 StartY=117 StartZ=0 EndX=543 EndY=117 EndZ=0
    g13: LineSegment StartX=543 StartY=117 StartZ=0 EndX=543 EndY=1488 EndZ=0
    g14: LineSegment StartX=543 StartY=1488 StartZ=0 EndX=117 EndY=1488 EndZ=0
    g15: LineSegment StartX=117 StartY=1488 StartZ=0 EndX=117 EndY=117 EndZ=0
  constraints (47):
    c: Coincident(g0,g1)
    c: Coincident(g1,g2)
    c: Coincident(g2,g3)
    c: Coincident(g3,g0)
    c: Horizontal(g0)
    c: Horizontal(g2)
    c: Vertical(g1)
    c: Vertical(g3)
    c: Coincident(g4,g5)
    c: Coincident(g5,g6)
    c: Coincident(g6,g7)
    c: Coincident(g7,g4)
    c: Horizontal(g4)
    c: Horizontal(g6)
    c: Vertical(g5)
    c: Vertical(g7)
    c: DistanceY(g1) = 1605  'Height'
    c: DistanceX(g0) = 660  'Width'
    c: DistanceY(g6,g2) = 70  'Frame1'
    c: DistanceX(g2,g6) = 70  'Frame2'
    c: DistanceX(g4,g0) = 70  'Frame3'
    c: DistanceY(g0,g4) = 70  'Frame4'
    c: Coincident(g0,g-1)
    c: Coincident(g8,g9)
    c: Coincident(g9,g10)
    c: Coincident(g10,g11)
    c: Coincident(g11,g8)
    c: Horizontal(g8)
    c: Horizontal(g10)
    c: Vertical(g9)
    c: Vertical(g11)
    c: Coincident(g12,g13)
    c: Coincident(g13,g14)
    c: Coincident(g14,g15)
    c: Coincident(g15,g12)
    c: Horizontal(g12)
    c: Horizontal(g14)
    c: Vertical(g13)
    c: Vertical(g15)
    c: DistanceX(g8,g12) = 40
    c: DistanceY(g8,g12) = 40
    c: DistanceX(g14,g10) = 40
    c: DistanceY(g14,g10) = 40
    c: DistanceX(g4,g8) = 7
    c: DistanceY(g4,g8) = 7
    c: DistanceX(g10,g6) = 7
    c: DistanceY(g10,g6) = 7
FEATURE [Part::FeaturePython] Window073  label="ОК-1-001"  # Arch/BIM 170 (typed FeaturePython)
  Area = 1059300
  Base = -> Sketch375
  Frame = 70
  Height = 1605
  HoleDepth = 0
  HoleWire = 0
  HorizontalArea = 0
  IfcData = attributes={"GlobalId": {"name": "GlobalId", "type": "IfcGloballyUniqueId", "is_enum": false, "enum_values": []}, "Description": {"... (+1230 chars omitted),+1 more (map truncated)
  IfcType = 170
  LouvreSpacing = 0
  LouvreWidth = 0
  Material = -> Material011
  MoveBase = false
  MoveWithHost = true
  Normal = (0,1,-2e-16)
  Opening = 0
  OverallHeight = 1605
  OverallWidth = 660
  PartitioningType = 0
  PerimeterLength = 0
  PredefinedType = 0
  Preset = 2
  SymbolElevation = false
  SymbolPlan = false
  VerticalArea = 0
  Width = 660
  WindowParts = OuterFrame | Frame | Wire0,Wire1 | 0.0+V | 0.00+V | InnerFrame | Frame | Wire2,Wire3,Edge8,Mode1 | 0.00+V | 0.0+V | InnerGlass | Glass panel | Wire3 | 8.0 | 40.0+V
  expr: OverallWidth = .Width.Value
  expr: OverallHeight = .Height.Value
FEATURE [Sketcher::SketchObject] Sketch376
  FullyConstrained = true
  Placement = pos=(7165,-435,955) rot=(1,0,0;1.5708rad)
  sketch-geometry (16):
    g0: LineSegment StartX=0 StartY=0 StartZ=0 EndX=660 EndY=0 EndZ=0
    g1: LineSegment StartX=660 StartY=0 StartZ=0 EndX=660 EndY=1605 EndZ=0
    g2: LineSegment StartX=660 StartY=1605 StartZ=0 EndX=0 EndY=1605 EndZ=0
    g3: LineSegment StartX=0 StartY=1605 StartZ=0 EndX=0 EndY=0 EndZ=0
    g4: LineSegment StartX=70 StartY=70 StartZ=0 EndX=590 EndY=70 EndZ=0
    g5: LineSegment StartX=590 StartY=70 StartZ=0 EndX=590 EndY=1535 EndZ=0
    g6: LineSegment StartX=590 StartY=1535 StartZ=0 EndX=70 EndY=1535 EndZ=0
    g7: LineSegment StartX=70 StartY=1535 StartZ=0 EndX=70 EndY=70 EndZ=0
    g8: LineSegment StartX=77 StartY=77 StartZ=0 EndX=583 EndY=77 EndZ=0
    g9: LineSegment StartX=583 StartY=77 StartZ=0 EndX=583 EndY=1528 EndZ=0
    g10: LineSegment StartX=583 StartY=1528 StartZ=0 EndX=77 EndY=1528 EndZ=0
    g11: LineSegment StartX=77 StartY=1528 StartZ=0 EndX=77 EndY=77 EndZ=0
    g12: LineSegment StartX=117 StartY=117 StartZ=0 EndX=543 EndY=117 EndZ=0
    g13: LineSegment StartX=543 StartY=117 StartZ=0 EndX=543 EndY=1488 EndZ=0
    g14: LineSegment StartX=543 StartY=1488 StartZ=0 EndX=117 EndY=1488 EndZ=0
    g15: LineSegment StartX=117 StartY=1488 StartZ=0 EndX=117 EndY=117 EndZ=0
  constraints (47):
    c: Coincident(g0,g1)
    c: Coincident(g1,g2)
    c: Coincident(g2,g3)
    c: Coincident(g3,g0)
    c: Horizontal(g0)
    c: Horizontal(g2)
    c: Vertical(g1)
    c: Vertical(g3)
    c: Coincident(g4,g5)
    c: Coincident(g5,g6)
    c: Coincident(g6,g7)
    c: Coincident(g7,g4)
    c: Horizontal(g4)
    c: Horizontal(g6)
    c: Vertical(g5)
    c: Vertical(g7)
    c: DistanceY(g1) = 1605  'Height'
    c: DistanceX(g0) = 660  'Width'
    c: DistanceY(g6,g2) = 70  'Frame1'
    c: DistanceX(g2,g6) = 70  'Frame2'
    c: DistanceX(g4,g0) = 70  'Frame3'
    c: DistanceY(g0,g4) = 70  'Frame4'
    c: Coincident(g0,g-1)
    c: Coincident(g8,g9)
    c: Coincident(g9,g10)
    c: Coincident(g10,g11)
    c: Coincident(g11,g8)
    c: Horizontal(g8)
    c: Horizontal(g10)
    c: Vertical(g9)
    c: Vertical(g11)
    c: Coincident(g12,g13)
    c: Coincident(g13,g14)
    c: Coincident(g14,g15)
    c: Coincident(g15,g12)
    c: Horizontal(g12)
    c: Horizontal(g14)
    c: Vertical(g13)
    c: Vertical(g15)
    c: DistanceX(g8,g12) = 40
    c: DistanceY(g8,g12) = 40
    c: DistanceX(g14,g10) = 40
    c: DistanceY(g14,g10) = 40
    c: DistanceX(g4,g8) = 7
    c: DistanceY(g4,g8) = 7
    c: DistanceX(g10,g6) = 7
    c: DistanceY(g10,g6) = 7
FEATURE [Part::FeaturePython] Window074  label="ОК-1-002"  # Arch/BIM 170 (typed FeaturePython)
  Area = 1059300
  Base = -> Sketch376
  Frame = 70
  Height = 1605
  HoleDepth = 0
  HoleWire = 0
  HorizontalArea = 0
  IfcData = attributes={"GlobalId": {"name": "GlobalId", "type": "IfcGloballyUniqueId", "is_enum": false, "enum_values": []}, "Description": {"... (+1230 chars omitted),+1 more (map truncated)
  IfcType = 170
  LouvreSpacing = 0
  LouvreWidth = 0
  Material = -> Material011
  MoveBase = false
  MoveWithHost = true
  Normal = (0,1,-2e-16)
  Opening = 0
  OverallHeight = 1605
  OverallWidth = 660
  PartitioningType = 0
  PerimeterLength = 0
  PredefinedType = 0
  Preset = 2
  SymbolElevation = false
  SymbolPlan = false
  VerticalArea = 0
  Width = 660
  WindowParts = OuterFrame | Frame | Wire0,Wire1 | 0.0+V | 0.00+V | InnerFrame | Frame | Wire2,Wire3,Edge6,Mode2 | 0.00+V | 0.0+V | InnerGlass | Glass panel | Wire3 | 8.0 | 40.0+V
  expr: OverallWidth = .Width.Value
  expr: OverallHeight = .Height.Value
FEATURE [Sketcher::SketchObject] Sketch379
  FullyConstrained = true
  Placement = pos=(9385,8805,-70) rot=(0,0.707107,0.707107;3.14159rad)
  sketch-geometry (24):
    g0: LineSegment StartX=0 StartY=0 StartZ=0 EndX=1960 EndY=0 EndZ=0
    g1: LineSegment StartX=1960 StartY=0 StartZ=0 EndX=1960 EndY=2630 EndZ=0
    g2: LineSegment StartX=1960 StartY=2630 StartZ=0 EndX=0 EndY=2630 EndZ=0
    g3: LineSegment StartX=0 StartY=2630 StartZ=0 EndX=0 EndY=0 EndZ=0
    g4: LineSegment StartX=70 StartY=70 StartZ=0 EndX=1890 EndY=70 EndZ=0
    g5: LineSegment StartX=1890 StartY=70 StartZ=0 EndX=1890 EndY=2560 EndZ=0
    g6: LineSegment StartX=1890 StartY=2560 StartZ=0 EndX=70 EndY=2560 EndZ=0
    g7: LineSegment StartX=70 StartY=2560 StartZ=0 EndX=70 EndY=70 EndZ=0
    g8: LineSegment StartX=77 StartY=77 StartZ=0 EndX=976.5 EndY=77 EndZ=0
    g9: LineSegment StartX=976.5 StartY=77 StartZ=0 EndX=976.5 EndY=2553 EndZ=0
    g10: LineSegment StartX=976.5 StartY=2553 StartZ=0 EndX=77 EndY=2553 EndZ=0
    g11: LineSegment StartX=77 StartY=2553 StartZ=0 EndX=77 EndY=77 EndZ=0
    g12: LineSegment StartX=117 StartY=117 StartZ=0 EndX=936.5 EndY=117 EndZ=0
    g13: LineSegment StartX=936.5 StartY=117 StartZ=0 EndX=936.5 EndY=2513 EndZ=0
    g14: LineSegment StartX=936.5 StartY=2513 StartZ=0 EndX=117 EndY=2513 EndZ=0
    g15: LineSegment StartX=117 StartY=2513 StartZ=0 EndX=117 EndY=117 EndZ=0
    g16: LineSegment StartX=983.5 StartY=77 StartZ=0 EndX=1883 EndY=77 EndZ=0
    g17: LineSegment StartX=1883 StartY=77 StartZ=0 EndX=1883 EndY=2553 EndZ=0
    g18: LineSegment StartX=1883 StartY=2553 StartZ=0 EndX=983.5 EndY=2553 EndZ=0
    g19: LineSegment StartX=983.5 StartY=2553 StartZ=0 EndX=983.5 EndY=77 EndZ=0
    g20: LineSegment StartX=1023.5 StartY=117 StartZ=0 EndX=1843 EndY=117 EndZ=0
    g21: LineSegment StartX=1843 StartY=117 StartZ=0 EndX=1843 EndY=2513 EndZ=0
    g22: LineSegment StartX=1843 StartY=2513 StartZ=0 EndX=1023.5 EndY=2513 EndZ=0
    g23: LineSegment StartX=1023.5 StartY=2513 StartZ=0 EndX=1023.5 EndY=117 EndZ=0
  constraints (71):
    c: Coincident(g0,g1)
    c: Coincident(g1,g2)
    c: Coincident(g2,g3)
    c: Coincident(g3,g0)
    c: Horizontal(g0)
    c: Horizontal(g2)
    c: Vertical(g1)
    c: Vertical(g3)
    c: Coincident(g4,g5)
    c: Coincident(g5,g6)
    c: Coincident(g6,g7)
    c: Coincident(g7,g4)
    c: Horizontal(g4)
    c: Horizontal(g6)
    c: Vertical(g5)
    c: Vertical(g7)
    c: DistanceY(g1) = 2630  'Height'
    c: DistanceX(g0) = 1960  'Width'
    c: DistanceY(g6,g2) = 70  'Frame1'
    c: DistanceX(g2,g6) = 70  'Frame2'
    c: DistanceX(g4,g0) = 70  'Frame3'
    c: DistanceY(g0,g4) = 70  'Frame4'
    c: Coincident(g0,g-1)
    c: Coincident(g8,g9)
    c: Coincident(g9,g10)
    c: Coincident(g10,g11)
    c: Coincident(g11,g8)
    c: Horizontal(g8)
    c: Horizontal(g10)
    c: Vertical(g9)
    c: Vertical(g11)
    c: Coincident(g12,g13)
    c: Coincident(g13,g14)
    c: Coincident(g14,g15)
    c: Coincident(g15,g12)
    c: Horizontal(g12)
    c: Horizontal(g14)
    c: Vertical(g13)
    c: Vertical(g15)
    c: Coincident(g16,g17)
    c: Coincident(g17,g18)
    c: Coincident(g18,g19)
    c: Coincident(g19,g16)
    c: Horizontal(g16)
    c: Horizontal(g18)
    c: Vertical(g17)
    c: Vertical(g19)
    c: Coincident(g20,g21)
    c: Coincident(g21,g22)
    c: Coincident(g22,g23)
    c: Coincident(g23,g20)
    c: Horizontal(g20)
    c: Horizontal(g22)
    c: Vertical(g21)
    c: Vertical(g23)
    c: DistanceY(g8,g12) = 40
    c: DistanceX(g8,g12) = 40
    c: DistanceX(g21,g17) = 40
    c: DistanceY(g21,g17) = 40
    c: DistanceX(g16,g20) = 40
    c: DistanceX(g14,g10) = 40
    c: Equal(g22,g14)
    c: DistanceY(g8,g16) = 0
    c: DistanceY(g10,g18) = 0
    c: DistanceX(g4,g8) = 7
    c: DistanceY(g4,g8) = 7
    c: DistanceX(g6,g18) = -7
    c: DistanceY(g6,g18) = -7
    c: DistanceX(g9,g19) = 7
    c: PointOnObject(g13,g22)
    c: PointOnObject(g12,g20)
FEATURE [Part::FeaturePython] Window077  label="ОК-6-001"  # Arch/BIM 170 (typed FeaturePython)
  Area = 5154800
  Base = -> Sketch379
  Frame = 70
  Height = 2630
  HoleDepth = 0
  HoleWire = 0
  HorizontalArea = 0
  IfcData = attributes={"GlobalId": {"name": "GlobalId", "type": "IfcGloballyUniqueId", "is_enum": false, "enum_values": []}, "Description": {"... (+1231 chars omitted),+1 more (map truncated)
  IfcType = 170
  LouvreSpacing = 0
  LouvreWidth = 0
  Material = -> Material011
  MoveBase = false
  MoveWithHost = true
  Normal = (0,-1,2e-16)
  Opening = 0
  OverallHeight = 2630
  OverallWidth = 1960
  PartitioningType = 0
  PerimeterLength = 0
  PredefinedType = 0
  Preset = 5
  SymbolElevation = false
  SymbolPlan = false
  VerticalArea = 0
  Width = 1960
  WindowParts = OuterFrame | Frame | Wire0,Wire1 | 50.0+V | 0.00+V | LeftFrame | Frame | Wire2,Wire3 | 50.0 | 0.0+V | LeftGlass | Glass panel | Wire3 | 5.0 | 25.0+V | RightFrame | Frame | Wire4,Wire5 | 50.0 | 50.0+V | RightGlass | Glass panel | Wire5 | 5.0 | 75.0+V
  expr: OverallWidth = .Width.Value
  expr: OverallHeight = .Height.Value
FEATURE [App::FeaturePython] Dimension079  # Draft dimension (typed FeaturePython)
  Diameter = false
  Dimline = (3400,1900,0)
  Direction = (0,0,0)
  Distance = 290
  End = (3825,2905,0)
  Normal = (0,0,1)
  Start = (3535,2905,0)
FEATURE [App::FeaturePython] Dimension080  # Draft dimension (typed FeaturePython)
  Diameter = false
  Dimline = (900,9200,0)
  Direction = (0,0,0)
  Distance = 1810
  End = (1250,8925,0)
  Normal = (0,0,1)
  Start = (-560,8925,0)
FEATURE [App::FeaturePython] Dimension081  # Draft dimension (typed FeaturePython)
  Diameter = false
  Dimline = (3080,9200,0)
  Direction = (0,0,0)
  Distance = 900
  End = (3980,8925,0)
  Normal = (0,0,1)
  Start = (3080,8925,0)
FEATURE [App::FeaturePython] Dimension082  # Draft dimension (typed FeaturePython)
  Diameter = false
  Dimline = (5150,9200,0)
  Direction = (0,0,0)
  Distance = 790
  End = (4770,8925,0)
  Normal = (0,0,1)
  Start = (3980,8925,0)
FEATURE [App::FeaturePython] Dimension083  # Draft dimension (typed FeaturePython)
  Diameter = false
  Dimline = (6980,9200,0)
  Direction = (0,0,0)
  Distance = 2720
  End = (7490,8925,0)
  Normal = (0,0,1)
  Start = (4770,8925,0)
FEATURE [App::FeaturePython] Dimension084  # Draft dimension (typed FeaturePython)
  Diameter = false
  Dimline = (9050,9200,0)
  Direction = (0,0,0)
  Distance = 1830
  End = (9320,8925,0)
  Normal = (0,0,1)
  Start = (7490,8925,0)
FEATURE [App::FeaturePython] Dimension085  # Draft dimension (typed FeaturePython)
  Diameter = false
  Dimline = (10360,9200,0)
  Direction = (0,0,0)
  Distance = 1810
  End = (11130,8925,0)
  Normal = (0,0,1)
  Start = (9320,8925,0)
FEATURE [App::FeaturePython] Dimension086  # Draft dimension (typed FeaturePython)
  Diameter = false
  Dimline = (4370,7900,0)
  Direction = (0,0,0)
  Distance = 4765
  End = (10600,8395,0)
  Normal = (0,0,1)
  Start = (5835,8395,0)
FEATURE [App::FeaturePython] Dimension092  # Draft dimension (typed FeaturePython)
  Diameter = false
  Dimline = (6900,-800,0)
  Direction = (0,0,0)
  Distance = 1290
  End = (7230,-555,0)
  Normal = (0,0,1)
  Start = (5940,-555,0)
FEATURE [App::FeaturePython] Dimension094  # Draft dimension (typed FeaturePython)
  Diameter = false
  Dimline = (8150,-800,0)
  Direction = (0,0,0)
  Distance = 3370
  End = (11130,-555,0)
  Normal = (0,0,1)
  Start = (7760,-555,0)
FEATURE [App::FeaturePython] Dimension095  # Draft dimension (typed FeaturePython)
  Diameter = false
  Dimline = (11700,1460,0)
  Direction = (0,0,0)
  Distance = 2080
  End = (11130,1525,0)
  Normal = (0,0,1)
  Start = (11130,-555,0)
FEATURE [App::FeaturePython] Dimension096  # Draft dimension (typed FeaturePython)
  Diameter = false
  Dimline = (11700,2640,0)
  Direction = (0,0,0)
  Distance = 1050
  End = (11130,2575,0)
  Normal = (0,0,1)
  Start = (11130,1525,0)
FEATURE [App::FeaturePython] Dimension097  # Draft dimension (typed FeaturePython)
  Diameter = false
  Dimline = (11700,3475,0)
  Direction = (0,0,0)
  Distance = 1030
  End = (11130,3605,0)
  Normal = (0,0,1)
  Start = (11130,2575,0)
FEATURE [App::FeaturePython] Dimension099  # Draft dimension (typed FeaturePython)
  Diameter = false
  Dimline = (11700,6725,0)
  Direction = (0,0,0)
  Distance = 3750
  End = (11130,8925,0)
  Normal = (0,0,1)
  Start = (11130,5175,0)
FEATURE [Part::Part2DObjectPython] Line1730  # Draft 2D object (typed FeaturePython)
  Area = 0
  ChamferSize = 0
  Closed = false
  End = (9000,9100,0)
  FilletRadius = 0
  Length = 200
  MakeFace = true
  Placement = pos=(9000,9300,0) rot=(0,0,1;0rad)
  Points = (2) [(0,0,0),(0,-200,0)]
  Start = (9000,9300,0)
  Subdivisions = 0
FEATURE [Part::Part2DObjectPython] Line1731  # Draft 2D object (typed FeaturePython)
  Area = 0
  ChamferSize = 0
  Closed = false
  End = (5900,9100,0)
  FilletRadius = 0
  Length = 200
  MakeFace = true
  Placement = pos=(5900,9300,0) rot=(0,0,1;0rad)
  Points = (2) [(0,0,0),(0,-200,0)]
  Start = (5900,9300,0)
  Subdivisions = 0
FEATURE [Part::Part2DObjectPython] Line1732  # Draft 2D object (typed FeaturePython)
  Area = 0
  ChamferSize = 0
  Closed = false
  End = (5900,-1400,0)
  FilletRadius = 0
  Length = 200
  MakeFace = true
  Placement = pos=(5900,-1600,0) rot=(0,0,1;0rad)
  Points = (2) [(0,0,0),(0,200,0)]
  Start = (5900,-1600,0)
  Subdivisions = 0
FEATURE [Part::Part2DObjectPython] Line1733  # Draft 2D object (typed FeaturePython)
  Area = 0
  ChamferSize = 0
  Closed = false
  End = (9000,-1400,0)
  FilletRadius = 0
  Length = 200
  MakeFace = true
  Placement = pos=(9000,-1600,0) rot=(0,0,1;0rad)
  Points = (2) [(0,0,0),(0,200,0)]
  Start = (9000,-1600,0)
  Subdivisions = 0
FEATURE [Part::Part2DObjectPython] Line1734  # Draft 2D object (typed FeaturePython)
  Area = 0
  ChamferSize = 0
  Closed = false
  End = (9000,-1600,0)
  FilletRadius = 0
  Length = 250
  MakeFace = true
  Placement = pos=(9250,-1600,0) rot=(0,0,1;0rad)
  Points = (2) [(0,0,0),(-250,0,0)]
  Start = (9250,-1600,0)
  Subdivisions = 0
FEATURE [Part::Part2DObjectPython] ShapeString205  # Draft 2D object (typed FeaturePython)
  FontFile = <path>
  Placement = pos=(9309.21,-1566.26,0) rot=(0,0,1;0rad)
  Size = 150
  String = А
  Tracking = 0
FEATURE [Part::Part2DObjectPython] ShapeString206  # Draft 2D object (typed FeaturePython)
  FontFile = <path>
  Placement = pos=(9309.21,9333.74,0) rot=(0,0,1;0rad)
  Size = 150
  String = А
  Tracking = 0
FEATURE [Part::Part2DObjectPython] Line1735  # Draft 2D object (typed FeaturePython)
  Area = 0
  ChamferSize = 0
  Closed = false
  End = (9000,9300,0)
  FilletRadius = 0
  Length = 250
  MakeFace = true
  Placement = pos=(9250,9300,0) rot=(0,0,1;0rad)
  Points = (2) [(0,0,0),(-250,0,0)]
  Start = (9250,9300,0)
  Subdivisions = 0
FEATURE [Part::Part2DObjectPython] Line1736  # Draft 2D object (typed FeaturePython)
  Area = 0
  ChamferSize = 0
  Closed = false
  End = (5900,-1600,0)
  FilletRadius = 0
  Length = 250
  MakeFace = true
  Placement = pos=(6150,-1600,0) rot=(0,0,1;0rad)
  Points = (2) [(0,0,0),(-250,0,0)]
  Start = (6150,-1600,0)
  Subdivisions = 0
FEATURE [Part::Part2DObjectPython] ShapeString207  # Draft 2D object (typed FeaturePython)
  FontFile = <path>
  Placement = pos=(6209.21,-1566.26,0) rot=(0,0,1;0rad)
  Size = 150
  String = B
  Tracking = 0
FEATURE [Part::Part2DObjectPython] ShapeString208  # Draft 2D object (typed FeaturePython)
  FontFile = <path>
  Placement = pos=(6209.21,9333.74,0) rot=(0,0,1;0rad)
  Size = 150
  String = B
  Tracking = 0
FEATURE [Part::Part2DObjectPython] Line1737  # Draft 2D object (typed FeaturePython)
  Area = 0
  ChamferSize = 0
  Closed = false
  End = (5900,9300,0)
  FilletRadius = 0
  Length = 250
  MakeFace = true
  Placement = pos=(6150,9300,0) rot=(0,0,1;0rad)
  Points = (2) [(0,0,0),(-250,0,0)]
  Start = (6150,9300,0)
  Subdivisions = 0
FEATURE [App::GeometryPython] BuildingPart114  label="разрезы"  # Arch/BIM 172 (typed FeaturePython)
  Area = 0
  Group = -> [Line1730,Line1731,Line1732,Line1733,Line1734,ShapeString205,ShapeString206,Line1735,Line1736,ShapeString207,ShapeString208,Line1737]
  Height = 0
  HeightPropagate = true
  IfcData = attributes={"GlobalId": {"name": "GlobalId", "type": "IfcGloballyUniqueId", "is_enum": false, "enum_values": []}, "Description": {"... (+484 chars omitted),+1 more (map truncated)
  IfcType = 172
  LevelOffset = 0
  PredefinedType = 0
FEATURE [TechDraw::DrawSVGTemplate] Template004
  EditableTexts = Дата_разработки=27.05.22,Лист=1,Листов=10,Масштаб=1:50,Материал1=Разработано @<owner>,Материал2=при участии сообщества "Forumhouse.ru",+7 more (map truncated)
  Height = 297
  Orientation = 1
  Width = 420
FEATURE [TechDraw::DrawViewAnnotation] Annotation032
  Font = osifont
  LineSpace = 80
  LockPosition = false
  MaxWidth = -1
  Rotation = 0
  ScaleType = 0
  Text = \u0440\u0438\u0441. 1   \u0421\u0435\u0432\u0435\u0440\u043d\u044b\u0439 \u0444\u0430\u0441\u0430\u0434
  TextSize = 6
  TextStyle = 0
  X = 142.66
  Y = 87.7129
FEATURE [TechDraw::DrawViewAnnotation] Annotation033
  Font = osifont
  LineSpace = 80
  LockPosition = false
  MaxWidth = -1
  Rotation = 0
  ScaleType = 0
  Text = \u0440\u0438\u0441. 2  \u042e\u0436\u043d\u044b\u0439 \u0444\u0430\u0441\u0430\u0434
  TextSize = 6
  TextStyle = 0
  X = 304.904
  Y = 88.6165
FEATURE [TechDraw::DrawSVGTemplate] Template005
  EditableTexts = Лист=7; Номер=ИЖС-2022.0003
  Height = 297
  Orientation = 1
  Width = 420
FEATURE [TechDraw::DrawViewAnnotation] Annotation034
  Font = osifont
  LineSpace = 80
  LockPosition = true
  MaxWidth = -1
  Rotation = 0
  ScaleType = 0
  Text = \u0416\u0438\u043b\u043e\u0439 \u0434\u043e\u043c \u0441 \u043c\u0430\u043d\u0441\u0430\u0440\u0434\u043e\u0439
  TextSize = 10
  TextStyle = 0
  X = 209.673
  Y = 248.467
FEATURE [TechDraw::DrawViewAnnotation] Annotation035
  Font = osifont
  LineSpace = 80
  LockPosition = true
  MaxWidth = -1
  Rotation = 0
  ScaleType = 0
  Text = \u044d\u0441\u043a\u0438\u0437\u043d\u044b\u0439 \u043f\u0440\u043e\u0435\u043a\u0442
  TextSize = 6
  TextStyle = 0
  X = 210.327
  Y = 238.34
FEATURE [TechDraw::DrawSVGTemplate] Template006
  EditableTexts = Лист=2; Номер=ИЖС-2022.0003
  Height = 297
  Orientation = 1
  Width = 420
FEATURE [TechDraw::DrawViewAnnotation] Annotation036
  Font = osifont
  LineSpace = 80
  LockPosition = false
  MaxWidth = -1
  Rotation = 0
  ScaleType = 0
  Text = \u0424\u0430\u0441\u0430\u0434\u044b
  TextSize = 8
  TextStyle = 0
  X = 215.522
  Y = 275.743
FEATURE [TechDraw::DrawViewAnnotation] Annotation037
  Font = Ubuntu Light
  LineSpace = 80
  LockPosition = false
  MaxWidth = -1
  Rotation = 0
  ScaleType = 0
  Text = \u0420\u0430\u0437\u0440\u0435\u0437 \u043f\u043e \u0412-\u0412
  TextSize = 6
  TextStyle = 0
  X = 223.092
  Y = 272.533
FEATURE [Part::FeaturePython] Component167  label="стул015"  # Arch/BIM 0 (typed FeaturePython)
  HorizontalArea = 0
  IfcData = attributes={"GlobalId": {"name": "GlobalId", "type": "IfcGloballyUniqueId", "is_enum": false, "enum_values": []}, "Description": {"... (+538 chars omitted),+1 more (map truncated)
  IfcType = 0
  Material = -> Material014
  MoveBase = false
  MoveWithHost = false
  PerimeterLength = 0
  Placement = pos=(-505.618,3912.19,3145) rot=(0,0,-1;1.5708rad)
  PredefinedType = 0
  VerticalArea = 0
FEATURE [Part::FeaturePython] Component169  label="стул016"  # Arch/BIM 0 (typed FeaturePython)
  HorizontalArea = 0
  IfcData = attributes={"GlobalId": {"name": "GlobalId", "type": "IfcGloballyUniqueId", "is_enum": false, "enum_values": []}, "Description": {"... (+538 chars omitted),+1 more (map truncated)
  IfcType = 0
  Material = -> Material014
  MoveBase = false
  MoveWithHost = false
  PerimeterLength = 0
  Placement = pos=(-505.618,5252.19,3145) rot=(0,0,-1;1.5708rad)
  PredefinedType = 0
  VerticalArea = 0
FEATURE [App::FeaturePython] Dimension101  # Draft dimension (typed FeaturePython)
  Diameter = false
  Dimline = (2600,4100,0)
  Direction = (0,0,0)
  Distance = 100
  End = (2470,4425,0)
  Normal = (0,0,1)
  Start = (2370,4425,0)
FEATURE [Part::Part2DObjectPython] Line1745  # Draft 2D object (typed FeaturePython)
  ChamferSize = 0
  Closed = true
  End = (2420,4435,0)
  FilletRadius = 0
  Length = 1230
  MakeFace = false
  Placement = pos=(4665,6735,0) rot=(0,0,-1;1.5708rad)
  Points = (2) [(3530,-2245,0),(2300,-2245,0)]
  Start = (2420,3205,0)
  Subdivisions = 0
FEATURE [Part::FeaturePython] Wall402  label="перегородка (сил.блок 500х250х80) 008"  # Arch/BIM 166 (typed FeaturePython)
  Align = 2
  Area = 3690000
  Base = -> Line1745
  BlockHeight = 250
  BlockLength = 0
  CountBroken = 0
  CountEntire = 0
  Face = 0
  Height = 3000
  HorizontalArea = 98400
  IfcType = 166
  Joint = 0
  Length = 1230
  MakeBlocks = false
  Material = -> Material009
  MoveBase = false
  MoveWithHost = false
  Normal = (0,0,0)
  OffsetFirst = 300
  OffsetSecond = 50
  PerimeterLength = 2620
  Placement = pos=(0,0,-200) rot=(0,0,1;0rad)
  PredefinedType = 0
  VerticalArea = 7.86e+06
  Width = 80
FEATURE [Part::FeaturePython] Component170  label="унитаз с инсталляцией 005"  # Arch/BIM 0 (typed FeaturePython)
  HorizontalArea = 0
  IfcData = attributes={"GlobalId": {"name": "GlobalId", "type": "IfcGloballyUniqueId", "is_enum": false, "enum_values": []}, "Description": {"... (+538 chars omitted),+1 more (map truncated)
  IfcType = 0
  Material = -> Material013
  MoveBase = false
  MoveWithHost = false
  PerimeterLength = 0
  Placement = pos=(-6025,425,0) rot=(0,0,1;0rad)
  PredefinedType = 0
  VerticalArea = 0
FEATURE [App::FeaturePython] Dimension102  # Draft dimension (typed FeaturePython)
  Diameter = false
  Dimline = (2810,4600,0)
  Direction = (0,0,0)
  Distance = 2400
  End = (2370,4395,0)
  Normal = (0,0,1)
  Start = (-30,4395,0)
FEATURE [App::FeaturePython] Dimension103  # Draft dimension (typed FeaturePython)
  Diameter = false
  Dimline = (9700,2000,0)
  Direction = (0,0,0)
  Distance = 2960
  End = (10600,2935,0)
  Normal = (0,0,1)
  Start = (10600,-25,0)
FEATURE [App::FeaturePython] Dimension104  # Draft dimension (typed FeaturePython)
  Diameter = false
  Dimline = (4561.04,7137.93,0)
  Direction = (0,0,0)
  Distance = 1100
  End = (4925,8395,0)
  Normal = (0,0,1)
  Start = (3825,8395,0)
FEATURE [Part::FeaturePython] Structure471  label="Раковина 81х45 Hatria Area001"  # Arch/BIM 172 (typed FeaturePython)
  CloneOf = -> Structure347
  FaceMaker = 0
  Height = 150
  HorizontalArea = 314998
  IfcData = attributes={"GlobalId": {"name": "GlobalId", "type": "IfcGloballyUniqueId", "is_enum": false, "enum_values": []}, "Description": {"... (+484 chars omitted),+1 more (map truncated)
  IfcType = 172
  Length = 0
  Material = -> Material013
  MoveBase = false
  MoveWithHost = false
  Nodes = (2) [(6425,5369.88,0),(6425,5369.88,150)]
  NodesOffset = 0
  Normal = (0,0,0)
  PerimeterLength = 2372.43
  Placement = pos=(-880,2225,850) rot=(0,0,1;0rad)
  PredefinedType = 0
  VerticalArea = 355865
  Width = 100
FEATURE [Part::Part2DObjectPython] ShapeString209  # Draft 2D object (typed FeaturePython)
  FontFile = <path>
  Placement = pos=(4889.17,3675.69,0) rot=(0,0,1;0rad)
  Size = 250
  String = 1
  Tracking = 0
FEATURE [Part::Part2DObjectPython] Circle145  label="Circle146"  # Draft 2D object (typed FeaturePython)
  Area = 0
  FirstAngle = 0
  LastAngle = 0
  MakeFace = false
  Placement = pos=(4982.52,3776.08,0) rot=(0,0,1;0rad)
  Radius = 200
FEATURE [Part::Part2DObjectPython] Circle146  label="Circle147"  # Draft 2D object (typed FeaturePython)
  Area = 0
  FirstAngle = 0
  LastAngle = 0
  MakeFace = false
  Placement = pos=(5584.01,1482.03,0) rot=(0,0,1;0rad)
  Radius = 200
FEATURE [Part::Part2DObjectPython] ShapeString210  # Draft 2D object (typed FeaturePython)
  FontFile = <path>
  Placement = pos=(5490.66,1381.63,0) rot=(0,0,1;0rad)
  Size = 250
  String = 2
  Tracking = 0
FEATURE [Part::Part2DObjectPython] Circle147  label="Circle148"  # Draft 2D object (typed FeaturePython)
  Area = 0
  FirstAngle = 0
  LastAngle = 0
  MakeFace = false
  Placement = pos=(8300,3700,0) rot=(0,0,1;0rad)
  Radius = 200
FEATURE [Part::Part2DObjectPython] ShapeString211  # Draft 2D object (typed FeaturePython)
  FontFile = <path>
  Placement = pos=(8206.65,3599.61,0) rot=(0,0,1;0rad)
  Size = 250
  String = 3
  Tracking = 0
FEATURE [Part::Part2DObjectPython] Circle149  label="Circle150"  # Draft 2D object (typed FeaturePython)
  Area = 0
  FirstAngle = 0
  LastAngle = 0
  MakeFace = false
  Placement = pos=(2000,5300,0) rot=(0,0,1;0rad)
  Radius = 200
FEATURE [Part::Part2DObjectPython] ShapeString213  # Draft 2D object (typed FeaturePython)
  FontFile = <path>
  Placement = pos=(1906.65,5199.61,0) rot=(0,0,1;0rad)
  Size = 250
  String = 4
  Tracking = 0
FEATURE [Part::Part2DObjectPython] Circle150  label="Circle151"  # Draft 2D object (typed FeaturePython)
  Area = 0
  FirstAngle = 0
  LastAngle = 0
  MakeFace = false
  Placement = pos=(2000,3100,0) rot=(0,0,1;0rad)
  Radius = 200
FEATURE [Part::Part2DObjectPython] ShapeString214  # Draft 2D object (typed FeaturePython)
  FontFile = <path>
  Placement = pos=(1906.65,2999.61,0) rot=(0,0,1;0rad)
  Size = 250
  String = 5
  Tracking = 0
FEATURE [Part::Part2DObjectPython] Line1746  # Draft 2D object (typed FeaturePython)
  Area = 0
  ChamferSize = 0
  Closed = true
  End = (13000,5100,0)
  FilletRadius = 0
  Length = 1100
  MakeFace = true
  Placement = pos=(13000,6200,0) rot=(0,0,1;0rad)
  Points = (2) [(0,0,0),(0,-1100,0)]
  Start = (13000,6200,0)
  Subdivisions = 0
FEATURE [Part::Part2DObjectPython] Line1747  # Draft 2D object (typed FeaturePython)
  Area = 0
  ChamferSize = 0
  Closed = false
  End = (13000,6200,0)
  FilletRadius = 0
  Length = 282.843
  MakeFace = true
  Placement = pos=(12800,6400,0) rot=(0,0,1;0rad)
  Points = (2) [(0,0,0),(200,-200,0)]
  Start = (12800,6400,0)
  Subdivisions = 0
FEATURE [Part::Part2DObjectPython] Line1748  # Draft 2D object (typed FeaturePython)
  Area = 0
  ChamferSize = 0
  Closed = false
  End = (13200,6400,0)
  FilletRadius = 0
  Length = 282.843
  MakeFace = true
  Placement = pos=(13000,6200,0) rot=(0,0,1;0rad)
  Points = (2) [(0,0,0),(200,200,0)]
  Start = (13000,6200,0)
  Subdivisions = 0
FEATURE [Part::Part2DObjectPython] Line1749  # Draft 2D object (typed FeaturePython)
  Area = 0
  ChamferSize = 0
  Closed = false
  End = (12800,5500,0)
  FilletRadius = 0
  Length = 447.214
  MakeFace = true
  Placement = pos=(13000,5100,0) rot=(0,0,1;0rad)
  Points = (2) [(0,0,0),(-200,400,0)]
  Start = (13000,5100,0)
  Subdivisions = 0
FEATURE [Part::Part2DObjectPython] Line1750  # Draft 2D object (typed FeaturePython)
  Area = 0
  ChamferSize = 0
  Closed = false
  End = (13200,5500,0)
  FilletRadius = 0
  Length = 447.214
  MakeFace = true
  Placement = pos=(13000,5100,0) rot=(0,0,1;0rad)
  Points = (2) [(0,0,0),(200,400,0)]
  Start = (13000,5100,0)
  Subdivisions = 0
FEATURE [Part::Part2DObjectPython] ShapeString218  # Draft 2D object (typed FeaturePython)
  FontFile = <path>
  Placement = pos=(12906.7,4699.61,0) rot=(0,0,1;0rad)
  Size = 250
  String = С
  Tracking = 0
FEATURE [Part::Part2DObjectPython] ShapeString219  # Draft 2D object (typed FeaturePython)
  FontFile = <path>
  Placement = pos=(12806.7,6499.61,0) rot=(0,0,1;0rad)
  Size = 250
  String = Юг
  Tracking = 0
FEATURE [App::FeaturePython] Dimension112  # Draft dimension (typed FeaturePython)
  Diameter = false
  Dimline = (7400,6400,0)
  Direction = (0,0,0)
  Distance = 3337.27
  End = (10397.3,7595,0)
  Normal = (0,0,1)
  Start = (7060,7595,0)
FEATURE [App::FeaturePython] Dimension126  # Draft dimension (typed FeaturePython)
  Diameter = false
  Dimline = (4900,2100,0)
  Direction = (0,0,0)
  Distance = 2810
  End = (4235,2785,0)
  Normal = (0,0,1)
  Start = (4235,-25,0)
FEATURE [App::FeaturePython] Dimension127  # Draft dimension (typed FeaturePython)
  Diameter = false
  Dimline = (7300,3300,0)
  Direction = (0,0,0)
  Distance = 900
  End = (7060,3985,0)
  Normal = (0,0,1)
  Start = (7060,3085,0)
FEATURE [App::FeaturePython] Dimension130  # Draft dimension (typed FeaturePython)
  Diameter = false
  Dimline = (8600,5100,0)
  Direction = (0,0,0)
  Distance = 6820
  End = (10128.6,7595,0)
  Normal = (0,0,1)
  Start = (10128.6,775,0)
FEATURE [App::FeaturePython] Dimension132  # Draft dimension (typed FeaturePython)
  Diameter = false
  Dimline = (8100,2200,0)
  Direction = (0,0,0)
  Distance = 2842.27
  End = (10397.3,775,0)
  Normal = (0,0,1)
  Start = (7555,775,0)
FEATURE [App::FeaturePython] Dimension133  # Draft dimension (typed FeaturePython)
  Diameter = false
  Dimline = (1200,3200,0)
  Direction = (0,0,0)
  Distance = 1245
  End = (-30,4135,0)
  Normal = (0,0,1)
  Start = (-30,2890,0)
FEATURE [App::FeaturePython] Dimension137  # Draft dimension (typed FeaturePython)
  Diameter = false
  Dimline = (5200,6200,0)
  Direction = (0,0,0)
  Distance = 850
  End = (5085,5485,0)
  Normal = (0,0,1)
  Start = (4235,5485,0)
FEATURE [App::FeaturePython] Dimension139  # Draft dimension (typed FeaturePython)
  Diameter = false
  Dimline = (5800,2600,0)
  Direction = (0,0,0)
  Distance = 2660
  End = (6895,-25,0)
  Normal = (0,0,1)
  Start = (4235,-25,0)
FEATURE [App::FeaturePython] Dimension145  # Draft dimension (typed FeaturePython)
  Diameter = false
  Dimline = (2336.59,6053.05,0)
  Direction = (0,0,0)
  Distance = 3362.27
  End = (3535,4235,0)
  Normal = (0,0,1)
  Start = (172.727,4235,0)
FEATURE [App::FeaturePython] Dimension148  # Draft dimension (typed FeaturePython)
  Diameter = false
  Dimline = (1600,5164.85,0)
  Direction = (0,0,0)
  Distance = 3360
  End = (-30,7595,0)
  Normal = (0,0,1)
  Start = (-30,4235,0)
FEATURE [App::FeaturePython] Dimension150  # Draft dimension (typed FeaturePython)
  Diameter = false
  Dimline = (9700,4300,0)
  Direction = (0,0,0)
  Distance = 2590
  End = (10590,5480,0)
  Normal = (0,0,1)
  Start = (10590,2890,0)
FEATURE [App::GeometryPython] BuildingPart128  label="Направление открывания дверей001"  # Arch/BIM 172 (typed FeaturePython)
  Area = 0
  Height = 0
  HeightPropagate = true
  IfcData = attributes={"GlobalId": {"name": "GlobalId", "type": "IfcGloballyUniqueId", "is_enum": false, "enum_values": []}, "Description": {"... (+484 chars omitted),+1 more (map truncated)
  IfcType = 172
  LevelOffset = 0
  PredefinedType = 0
FEATURE [App::FeaturePython] Dimension154  # Draft dimension (typed FeaturePython)
  Diameter = false
  Dimline = (4000,4400,0)
  Direction = (0,0,0)
  Distance = 2600
  End = (3685,5485,0)
  Normal = (0,0,1)
  Start = (3685,2885,0)
FEATURE [App::FeaturePython] Dimension155  # Draft dimension (typed FeaturePython)
  Diameter = false
  Dimline = (1600,4000,0)
  Direction = (0,0,0)
  Distance = 3360
  End = (4135,4135,0)
  Normal = (0,0,1)
  Start = (4135,775,0)
FEATURE [App::FeaturePython] Dimension159  # Draft dimension (typed FeaturePython)
  Diameter = false
  Dimline = (4454.17,6900,0)
  Direction = (0,0,0)
  Distance = 2110
  End = (4235,7595,0)
  Normal = (0,0,1)
  Start = (4235,5485,0)
FEATURE [App::FeaturePython] Dimension164  # Draft dimension (typed FeaturePython)
  Diameter = false
  Dimline = (2600,5300,0)
  Direction = (0,0,0)
  Distance = 900
  End = (3535,5205,0)
  Normal = (0,0,1)
  Start = (3535,4305,0)
FEATURE [App::FeaturePython] Dimension165  # Draft dimension (typed FeaturePython)
  Diameter = false
  Dimline = (1200,4185,0)
  Direction = (0,0,0)
  Distance = 1245
  End = (-30,5480,0)
  Normal = (0,0,1)
  Start = (-30,4235,0)
FEATURE [App::FeaturePython] Dimension167  # Draft dimension (typed FeaturePython)
  Diameter = false
  Dimline = (5400,1100,0)
  Direction = (0,0,0)
  Distance = 2660
  End = (6895,855,0)
  Normal = (0,0,1)
  Start = (4235,855,0)
FEATURE [App::FeaturePython] Dimension168  # Draft dimension (typed FeaturePython)
  Diameter = false
  Dimline = (2600,2600,0)
  Direction = (0,0,0)
  Distance = 900
  End = (3535,4065,0)
  Normal = (0,0,1)
  Start = (3535,3165,0)
FEATURE [App::FeaturePython] Dimension177  # Draft dimension (typed FeaturePython)
  Diameter = false
  Dimline = (3300,5700,0)
  Direction = (0,0,0)
  Distance = 2010
  End = (4135,7595,0)
  Normal = (0,0,1)
  Start = (4135,5585,0)
FEATURE [App::GeometryPython] BuildingPart129  label="разрезы001"  # Arch/BIM 172 (typed FeaturePython)
  Area = 0
  Height = 0
  HeightPropagate = true
  IfcData = attributes={"GlobalId": {"name": "GlobalId", "type": "IfcGloballyUniqueId", "is_enum": false, "enum_values": []}, "Description": {"... (+484 chars omitted),+1 more (map truncated)
  IfcType = 172
  LevelOffset = 0
  PredefinedType = 0
FEATURE [App::FeaturePython] Dimension180  # Draft dimension (typed FeaturePython)
  Diameter = false
  Dimline = (5400,4900,0)
  Direction = (0,0,0)
  Distance = 1000
  End = (5600,5485,0)
  Normal = (0,0,1)
  Start = (5600,4485,0)
FEATURE [App::MaterialObjectPython] Material020  label="Стекловата"  # material (typed FeaturePython)
  Description = Утепление стекловатой
  Material = AuthorAndLicense=ABS-Generic,CardName=ABS-Generic,Color=(0.9019607843137255, 0.8588235294117647, 0.5843137254901961, 1.0),Density=1060 kg/m^3,+15 more (map truncated)
  Transparency = 0
FEATURE [Part::Part2DObjectPython] Rectangle3445  label="Шкаф Cersanit Moduo 60_001"  # Draft 2D object (typed FeaturePython)
  Area = 84000
  ChamferSize = 0
  Columns = 1
  FilletRadius = 0
  Height = 600
  Length = 140
  MakeFace = true
  Placement = pos=(3825,6525,0) rot=(0,0,1;0rad)
  Rows = 1
FEATURE [Part::FeaturePython] Structure477  label="Шкаф Cersanit Moduo 60_002"  # Arch/BIM 52 (typed FeaturePython)
  Base = -> Rectangle3445
  FaceMaker = 0
  GlobalId = 2d5W_OQQf2Fxkoe6wMEOb9
  Height = 800
  HorizontalArea = 84000
  IfcData = IfcUID=2d5W_OQQf2Fxkoe6wMEOb9,+2 more (map truncated)
  IfcType = 52
  Length = 0
  Material = -> Material013
  MoveBase = false
  MoveWithHost = false
  Nodes = (2) [(-2856.79,7112.64,0),(-2856.79,7112.64,600)]
  NodesOffset = 0
  Normal = (0,0,-1)
  PerimeterLength = 1480
  Placement = pos=(0,0,1075) rot=(0,0,1;0rad)
  VerticalArea = 1184000
  Width = 100
FEATURE [Part::FeaturePython] Structure478  label="Шкаф Cersanit Moduo 60_003"  # Arch/BIM 52 (typed FeaturePython)
  Base = -> Rectangle3445
  FaceMaker = 0
  GlobalId = 2d5W_OQQf2Fxkoe6wMEOb9
  Height = 800
  HorizontalArea = 84000
  IfcData = IfcUID=2d5W_OQQf2Fxkoe6wMEOb9,+2 more (map truncated)
  IfcType = 52
  Length = 0
  Material = -> Material013
  MoveBase = false
  MoveWithHost = false
  Nodes = (2) [(-2856.79,7112.64,0),(-2856.79,7112.64,600)]
  NodesOffset = 0
  Normal = (0,0,1)
  PerimeterLength = 1480
  Placement = pos=(0,0,1075) rot=(0,0,1;0rad)
  VerticalArea = 1184000
  Width = 100
FEATURE [Part::Part2DObjectPython] Rectangle3463  # Draft 2D object (typed FeaturePython)
  Area = 400
  ChamferSize = 0
  Columns = 1
  FilletRadius = 0
  Height = 20
  Length = 20
  MakeFace = true
  Placement = pos=(-50,-45,0) rot=(0,0,1;0rad)
  Rows = 1
FEATURE [Part::Part2DObjectPython] Rectangle3518  # Draft 2D object (typed FeaturePython)
  Area = 0
  ChamferSize = 0
  Columns = 1
  FilletRadius = 75
  Height = 620
  Length = 235
  MakeFace = false
  Placement = pos=(4027.5,5535,0) rot=(0,0,1;3.14159rad)
  Rows = 1
FEATURE [Part::Part2DObjectPython] Rectangle3519  label="Раковина «Cersanit» Moduo 80 Slim_003"  # Draft 2D object (typed FeaturePython)
  Area = 312000
  ChamferSize = 0
  Columns = 1
  FilletRadius = 0
  Height = 390
  Length = 800
  MakeFace = true
  Placement = pos=(3695,5625,0) rot=(0,0,-1;1.5708rad)
  Rows = 1
FEATURE [Part::FeaturePython] Structure482  label="Структура025"  # Arch/BIM 52 (typed FeaturePython)
  Base = -> Rectangle3518
  FaceMaker = 0
  Height = 100
  HorizontalArea = 140871
  IfcData = attributes={"GlobalId": {"name": "GlobalId", "type": "IfcGloballyUniqueId", "is_enum": false, "enum_values": []}, "Description": {"... (+484 chars omitted),+1 more (map truncated)
  IfcType = 52
  Length = 0
  MoveBase = false
  MoveWithHost = false
  Nodes = (2) [(6380,5325,0),(6380,5325,100)]
  NodesOffset = 0
  Normal = (0,0,1)
  PerimeterLength = 1581.24
  Placement = pos=(0,0,800) rot=(0,0,1;0rad)
  VerticalArea = 158124
  Width = 100
FEATURE [Part::FeaturePython] Structure483  label="Раковина Cersanit Moduo 80 S-UM-MOD80SL/1 001"  # Arch/BIM 52 (typed FeaturePython)
  Base = -> Rectangle3519
  FaceMaker = 0
  GlobalId = 2d5W_OQQf2Fxkoe6wMEOb9
  Height = 55
  HorizontalArea = 171129
  IfcData = IfcUID=2d5W_OQQf2Fxkoe6wMEOb9,+2 more (map truncated)
  IfcType = 52
  Length = 0
  Material = -> Material013
  MoveBase = false
  MoveWithHost = false
  Nodes = (2) [(-2856.79,7112.64,0),(-2856.79,7112.64,600)]
  NodesOffset = 0
  Normal = (0,0,1)
  PerimeterLength = 2380
  Placement = pos=(0,0,845) rot=(0,0,1;0rad)
  Subtractions = -> [Structure482]
  VerticalArea = 217868
  Width = 100
FEATURE [Part::FeaturePython] Structure484  label="Раковина «Cersanit» Moduo 80 Slim (тумба)001"  # Arch/BIM 52 (typed FeaturePython)
  Base = -> Rectangle3519
  FaceMaker = 0
  GlobalId = 2d5W_OQQf2Fxkoe6wMEOb9
  Height = 570
  HorizontalArea = 312000
  IfcData = IfcUID=2d5W_OQQf2Fxkoe6wMEOb9,+2 more (map truncated)
  IfcType = 52
  Length = 0
  Material = -> Material013
  MoveBase = false
  MoveWithHost = false
  Nodes = (2) [(-2856.79,7112.64,0),(-2856.79,7112.64,600)]
  NodesOffset = 0
  Normal = (0,0,-1)
  PerimeterLength = 2380
  Placement = pos=(0,0,845) rot=(0,0,1;0rad)
  VerticalArea = 1356600
  Width = 100
FEATURE [Part::FeaturePython] Component183  label="унитаз с инсталляцией 006"  # Arch/BIM 0 (typed FeaturePython)
  HorizontalArea = 0
  IfcData = attributes={"GlobalId": {"name": "GlobalId", "type": "IfcGloballyUniqueId", "is_enum": false, "enum_values": []}, "Description": {"... (+538 chars omitted),+1 more (map truncated)
  IfcType = 0
  Material = -> Material013
  MoveBase = false
  MoveWithHost = false
  PerimeterLength = 0
  Placement = pos=(-3875,-5075,0) rot=(0,0,1;0rad)
  PredefinedType = 0
  VerticalArea = 0
FEATURE [Part::FeaturePython] Array073  label="ПНО 55-12-8 3шт. 001"  # Draft array (typed FeaturePython)
  Angle = 360
  ArrayType = 0
  Axis = (0,0,1)
  Base = -> Extrude088
  Center = (0,0,0)
  Fuse = false
  IntervalAxis = (0,0,0)
  IntervalX = (1230,0,0)
  IntervalY = (0,0,0)
  IntervalZ = (0,0,1)
  NumberPolar = 1
  NumberX = 3
  NumberY = 1
  NumberZ = 1
  Placement = pos=(-2485,1.364e-12,0) rot=(0,0,1;0rad)
FEATURE [Part::Cylinder] Cylinder005  label="труба вытяжки"
  Angle = 360
  AttacherType = Attacher::AttachEngine3D
  Height = 850
  Placement = pos=(10025.1,549.939,1900) rot=(0,0,1;0.785398rad)
  Radius = 100
FEATURE [Part::Part2DObjectPython] Wire975  # Draft 2D object (typed FeaturePython)
  Area = 0
  ChamferSize = 0
  Closed = true
  End = (4925,8395,0)
  FilletRadius = 0
  Length = 5200
  MakeFace = false
  Placement = pos=(5595,9270,0) rot=(0,0,1;3.14159rad)
  Points = (4) [(-130,875,0),(-130,2675,0),(670,2675,0),(670,875,0)]
  Start = (5725,8395,0)
  Subdivisions = 0
FEATURE [Part::FeaturePython] Wall240  label="Облицовка ванны плиткой 30мм"  # Arch/BIM 166 (typed FeaturePython)
  Align = 0
  Area = 2.964e+06
  Base = -> Wire975
  BlockHeight = 0
  BlockLength = 0
  CountBroken = 0
  CountEntire = 0
  Face = 0
  GlobalId = 36KkLHJl1D_AUwy3AkMKZ7
  Height = 570
  HorizontalArea = 250000
  IfcData = IfcUID=36KkLHJl1D_AUwy3AkMKZ7,+2 more (map truncated)
  IfcType = 166
  Joint = 0
  Length = 5200
  MakeBlocks = false
  Material = -> Material005
  MoveBase = false
  MoveWithHost = false
  Normal = (0,0,0)
  OffsetFirst = 0
  OffsetSecond = 0
  PerimeterLength = 5200
  PredefinedType = 0
  VerticalArea = 5.7e+06
  Width = 50
FEATURE [Part::FeaturePython] Structure343  label="Ванна 180х90"  # Arch/BIM 52 (typed FeaturePython)
  FaceMaker = 0
  GlobalId = 2VbcwV0QPCqROXcrzT3$_s
  Height = 600
  HorizontalArea = 1.44e+06
  IfcData = IfcUID=2VbcwV0QPCqROXcrzT3$_s,+2 more (map truncated)
  IfcType = 52
  Length = 0
  Material = -> Material013
  MoveBase = false
  MoveWithHost = false
  Nodes = (2) [(-2856.79,7112.64,0),(-2856.79,7112.64,600)]
  NodesOffset = 0
  Normal = (0,0,1)
  PerimeterLength = 5200
  Subtractions = -> [Structure342,Wall240]
  VerticalArea = 4.917e+06
  Width = 100
FEATURE [Part::FeaturePython] Structure523  label="LACK ЛАКК Тумба под ТВ, 160x35x36 см 001"  # Arch/BIM 52 (typed FeaturePython)
  FaceMaker = 0
  GlobalId = 02q3nx$AH4fB0PqHacSjsk
  Height = 360
  HorizontalArea = 560000
  IfcData = IfcUID=02q3nx$AH4fB0PqHacSjsk,+2 more (map truncated)
  IfcType = 52
  Length = 0
  Material = -> Material015
  MoveBase = false
  MoveWithHost = false
  Nodes = (2) [(4185,6330,0),(4185,6330,360)]
  NodesOffset = 0
  Normal = (0,0,1)
  PerimeterLength = 3900
  Placement = pos=(-825,130,0) rot=(0,0,1;0rad)
  VerticalArea = 1404000
  Width = 100
FEATURE [Part::Cylinder] Cylinder006  label="стул полубарный"
  Angle = 360
  AttacherType = Attacher::AttachEngine3D
  Height = 100
  Placement = pos=(9300,5580,500) rot=(0,0,1;1.5708rad)
  Radius = 200
FEATURE [Part::Cylinder] Cylinder007  label="стул полубарный001"
  Angle = 360
  AttacherType = Attacher::AttachEngine3D
  Height = 30
  Placement = pos=(9300,5580,0) rot=(0,0,1;1.5708rad)
  Radius = 200
FEATURE [Part::Cylinder] Cylinder008  label="стул полубарный002"
  Angle = 360
  AttacherType = Attacher::AttachEngine3D
  Height = 500
  Placement = pos=(9300,5580,30) rot=(0,0,1;1.5708rad)
  Radius = 25
FEATURE [Part::Compound] Compound006  label="стул полубарный003"
  Links = -> [Cylinder006,Cylinder007,Cylinder008]
FEATURE [Part::Box] Box3143  label="комод"
  AttacherType = Attacher::AttachEngine3D
  Height = 800
  Length = 450
  Placement = pos=(3500,0,0) rot=(0,0,1;1.5708rad)
  Width = 1200
FEATURE [Part::Box] Box3236  label="тумбочка 001"
  AttacherType = Attacher::AttachEngine3D
  Height = 500
  Length = 400
  Placement = pos=(-15,5145,0) rot=(0,0,1;0rad)
  Width = 400
FEATURE [Part::Box] Box3237  label="тумбочка 002"
  AttacherType = Attacher::AttachEngine3D
  Height = 500
  Length = 400
  Placement = pos=(-15,7375,0) rot=(0,0,1;0rad)
  Width = 400
FEATURE [Part::Part2DObjectPython] Rectangle3675  # Draft 2D object (typed FeaturePython)
  ChamferSize = 0
  Columns = 1
  FilletRadius = 25
  Height = 250
  Length = 2090
  MakeFace = false
  Placement = pos=(125,10,0) rot=(0,0,1;0rad)
  Rows = 1
FEATURE [Part::Part2DObjectPython] Rectangle3676  # Draft 2D object (typed FeaturePython)
  ChamferSize = 0
  Columns = 1
  FilletRadius = 25
  Height = 910
  Length = 2090
  MakeFace = false
  Placement = pos=(125,10,0) rot=(0,0,1;0rad)
  Rows = 1
  Support = -> [Rectangle3675]
FEATURE [Part::Part2DObjectPython] Rectangle3677  # Draft 2D object (typed FeaturePython)
  ChamferSize = 0
  Columns = 1
  FilletRadius = 25
  Height = 910
  Length = 230
  MakeFace = false
  Placement = pos=(125,10,0) rot=(0,0,1;0rad)
  Rows = 1
FEATURE [Part::FeaturePython] Structure524  # Arch/BIM 52 (typed FeaturePython)
  Base = -> Rectangle3677
  FaceMaker = 0
  GlobalId = 2DDa$j80P5hvQ3LPUQNes4
  Height = 200
  HorizontalArea = 208763
  IfcData = IfcUID=2DDa$j80P5hvQ3LPUQNes4,attributes={"GlobalId": {"value": "2DDa$j80P5hvQ3LPUQNes4"}},+1 more (map truncated)
  IfcType = 52
  Length = 0
  Material = -> Material015
  MoveBase = false
  MoveWithHost = false
  Nodes = (2) [(1656.58,7240.7,0),(1656.58,7240.7,200)]
  NodesOffset = 0
  Normal = (0,0,0)
  PerimeterLength = 2237.08
  Placement = pos=(0,0,400) rot=(0,0,1;0rad)
  VerticalArea = 447416
  Width = 100
FEATURE [Part::FeaturePython] Structure526  # Arch/BIM 52 (typed FeaturePython)
  Base = -> Rectangle3675
  FaceMaker = 0
  GlobalId = 1sWNXrsjP3FQ$2jjEvDesy
  Height = 400
  HorizontalArea = 521963
  IfcData = IfcUID=1sWNXrsjP3FQ$2jjEvDesy,attributes={"GlobalId": {"value": "1sWNXrsjP3FQ$2jjEvDesy"}},+1 more (map truncated)
  IfcType = 52
  Length = 0
  Material = -> Material015
  MoveBase = false
  MoveWithHost = false
  Nodes = (2) [(182.895,-1383.89,0),(182.895,-1383.89,400)]
  NodesOffset = 0
  Normal = (0,0,0)
  PerimeterLength = 4637.08
  Placement = pos=(0,0,400) rot=(0,0,1;0rad)
  VerticalArea = 1.85483e+06
  Width = 100
FEATURE [Part::Part2DObjectPython] Rectangle3678  # Draft 2D object (typed FeaturePython)
  ChamferSize = 0
  Columns = 1
  FilletRadius = 25
  Height = 910
  Length = 230
  MakeFace = false
  Placement = pos=(1985,10,0) rot=(0,0,1;0rad)
  Rows = 1
FEATURE [Part::FeaturePython] Structure525  # Arch/BIM 52 (typed FeaturePython)
  Base = -> Rectangle3678
  FaceMaker = 0
  GlobalId = 3Z9IWRZuT13weCYbg7_Khd
  Height = 200
  HorizontalArea = 208763
  IfcData = IfcUID=3Z9IWRZuT13weCYbg7_Khd,attributes={"GlobalId": {"value": "3Z9IWRZuT13weCYbg7_Khd"}},+1 more (map truncated)
  IfcType = 52
  Length = 0
  Material = -> Material015
  MoveBase = false
  MoveWithHost = false
  Nodes = (2) [(156.577,7240.7,0),(156.577,7240.7,200)]
  NodesOffset = 0
  Normal = (0,0,0)
  PerimeterLength = 2237.08
  Placement = pos=(0,0,400) rot=(0,0,1;0rad)
  VerticalArea = 447416
  Width = 100
FEATURE [Part::FeaturePython] Structure527  # Arch/BIM 52 (typed FeaturePython)
  Base = -> Rectangle3676
  FaceMaker = 0
  GlobalId = 3fmvKSc5DEWOPxKz6nUpvm
  Height = 400
  HorizontalArea = 1.90136e+06
  IfcData = IfcUID=3fmvKSc5DEWOPxKz6nUpvm,attributes={"GlobalId": {"value": "3fmvKSc5DEWOPxKz6nUpvm"}},+1 more (map truncated)
  IfcType = 52
  Length = 0
  Material = -> Material015
  MoveBase = false
  MoveWithHost = false
  Nodes = (2) [(906.577,7240.7,0),(906.577,7240.7,400)]
  NodesOffset = 0
  Normal = (0,0,0)
  PerimeterLength = 5957.08
  VerticalArea = 2.38283e+06
  Width = 100
FEATURE [App::GeometryPython] BuildingPart132  label="BACKABRO БАККАБРУ 3-местный диван-кровать, Идекулла 001"  # Arch/BIM 172 (typed FeaturePython)
  Area = 0
  Group = -> [Structure524,Structure525,Structure526,Structure527]
  Height = 0
  HeightPropagate = true
  IfcData = attributes={"GlobalId": {"name": "GlobalId", "type": "IfcGloballyUniqueId", "is_enum": false, "enum_values": []}, "Description": {"... (+484 chars omitted),+1 more (map truncated)
  IfcType = 172
  LevelOffset = 0
  PredefinedType = 0
FEATURE [Part::Part2DObjectPython] Line1899  # Draft 2D object (typed FeaturePython)
  ChamferSize = 0
  Closed = true
  End = (11140,5295,0)
  FilletRadius = 0
  Length = 3890
  MakeFace = true
  Placement = pos=(11140,1915,0) rot=(0,0,1;1.5708rad)
  Points = (2) [(-510,0,0),(3380,9.09495e-12,0)]
  Start = (11140,1405,0)
  Subdivisions = 0
FEATURE [Part::FeaturePython] Wall412  label="Перемычка облицовки 020"  # Arch/BIM 166 (typed FeaturePython)
  Align = 2
  Area = 1.45875e+06
  Base = -> Line1899
  BlockHeight = 250
  BlockLength = 66.3
  CountBroken = 53
  CountEntire = 49
  Face = 0
  GlobalId = 2CDkG$u1H6yg879o_wXiaT
  Height = 375
  HorizontalArea = 0
  IfcData = IfcUID=2CDkG$u1H6yg879o_wXiaT; attributes={"GlobalId": {"value": "2CDkG$u1H6yg879o_wXiaT"}}
  IfcType = 166
  Joint = 10
  Length = 3890
  MakeBlocks = true
  Material = -> Material003
  MoveBase = false
  MoveWithHost = false
  Normal = (0,0,1)
  OffsetFirst = 0
  OffsetSecond = 0
  PerimeterLength = 0
  Placement = pos=(0,0,2495) rot=(0,0,1;0rad)
  PredefinedType = 0
  VerticalArea = 0
  Width = 10
FEATURE [Part::Part2DObjectPython] Line1901  # Draft 2D object (typed FeaturePython)
  ChamferSize = 0
  Closed = true
  End = (9440,8935,0)
  FilletRadius = 0
  Length = 2070
  MakeFace = true
  Placement = pos=(7370,8935,0) rot=(0,0,1;0rad)
  Points = (2) [(0,0,0),(2070,0,0)]
  Start = (7370,8935,0)
  Subdivisions = 0
FEATURE [Part::FeaturePython] Wall414  label="Перемычка облицовки 022"  # Arch/BIM 166 (typed FeaturePython)
  Align = 2
  Area = 776250
  Base = -> Line1901
  BlockHeight = 250
  BlockLength = 66.5
  CountBroken = 29
  CountEntire = 25
  Face = 0
  GlobalId = 3Y7MnwAmX628ZvBXKl4dyB
  Height = 375
  HorizontalArea = 0
  IfcData = IfcUID=3Y7MnwAmX628ZvBXKl4dyB; attributes={"GlobalId": {"value": "3Y7MnwAmX628ZvBXKl4dyB"}}
  IfcType = 166
  Joint = 10
  Length = 2070
  MakeBlocks = true
  Material = -> Material003
  MoveBase = false
  MoveWithHost = false
  Normal = (0,0,1)
  OffsetFirst = 0
  OffsetSecond = 0
  PerimeterLength = 0
  Placement = pos=(0,0,2495) rot=(0,0,1;0rad)
  PredefinedType = 0
  VerticalArea = 0
  Width = 10
FEATURE [Part::Part2DObjectPython] Line1902  # Draft 2D object (typed FeaturePython)
  ChamferSize = 0
  Closed = true
  End = (6060,-565,0)
  FilletRadius = 0
  Length = 1550
  MakeFace = true
  Placement = pos=(5810,-595,0) rot=(0,0,-1;0rad)
  Points = (2) [(-1300,30,0),(250,30,0)]
  Start = (4510,-565,0)
  Subdivisions = 0
FEATURE [Part::FeaturePython] Wall415  label="Перемычка облицовки 023"  # Arch/BIM 166 (typed FeaturePython)
  Align = 2
  Area = 581250
  Base = -> Line1902
  BlockHeight = 250
  BlockLength = 67
  CountBroken = 22
  CountEntire = 18
  Face = 0
  GlobalId = 07ToIk0b17KwOPIvB7CAEx
  Height = 375
  HorizontalArea = 0
  IfcData = IfcUID=07ToIk0b17KwOPIvB7CAEx; attributes={"GlobalId": {"value": "07ToIk0b17KwOPIvB7CAEx"}}
  IfcType = 166
  Joint = 10
  Length = 1550
  MakeBlocks = true
  Material = -> Material003
  MoveBase = false
  MoveWithHost = false
  Normal = (0,0,1)
  OffsetFirst = 0
  OffsetSecond = 0
  PerimeterLength = 0
  Placement = pos=(0,0,2495) rot=(0,0,1;0rad)
  PredefinedType = 0
  VerticalArea = 0
  Width = 10
FEATURE [App::GeometryPython] BuildingPart038  label="Перемычки облицовки 1nf"  # Arch/BIM 52 (typed FeaturePython)
  Area = 5482500
  GlobalId = 0KtQz4WtXFJO7H9uDU_qkV
  Group = -> [Wall121,Wall123,Wall124,Wall159,Wall412,Wall414,Wall415]
  Height = 0
  HeightPropagate = true
  IfcData = IfcUID=0KtQz4WtXFJO7H9uDU_qkV,attributes={"GlobalId": {"value": "0KtQz4WtXFJO7H9uDU_qkV"}},+1 more (map truncated)
  IfcType = 52
  LevelOffset = 0
FEATURE [Sketcher::SketchObject] Sketch396
  FullyConstrained = true
  Placement = pos=(6005,-435,-70) rot=(0,0.707107,0.707107;3.14159rad)
  sketch-geometry (16):
    g0: LineSegment StartX=-2.84e-14 StartY=0 StartZ=0 EndX=450 EndY=0 EndZ=0
    g1: LineSegment StartX=450 StartY=0 StartZ=0 EndX=450 EndY=2155 EndZ=0
    g2: LineSegment StartX=450 StartY=2155 StartZ=0 EndX=0 EndY=2155 EndZ=0
    g3: LineSegment StartX=-2.84e-14 StartY=2155 StartZ=0 EndX=-2.84e-14 EndY=0 EndZ=0
    g4: LineSegment StartX=70 StartY=70 StartZ=0 EndX=380 EndY=70 EndZ=0
    g5: LineSegment StartX=380 StartY=70 StartZ=0 EndX=380 EndY=2085 EndZ=0
    g6: LineSegment StartX=380 StartY=2085 StartZ=0 EndX=70 EndY=2085 EndZ=0
    g7: LineSegment StartX=70 StartY=2085 StartZ=0 EndX=70 EndY=70 EndZ=0
    g8: LineSegment StartX=77 StartY=77 StartZ=0 EndX=373 EndY=77 EndZ=0
    g9: LineSegment StartX=373 StartY=77 StartZ=0 EndX=373 EndY=2078 EndZ=0
    g10: LineSegment StartX=373 StartY=2078 StartZ=0 EndX=77 EndY=2078 EndZ=0
    g11: LineSegment StartX=77 StartY=2078 StartZ=0 EndX=77 EndY=77 EndZ=0
    g12: LineSegment StartX=117 StartY=117 StartZ=0 EndX=333 EndY=117 EndZ=0
    g13: LineSegment StartX=333 StartY=117 StartZ=0 EndX=333 EndY=2038 EndZ=0
    g14: LineSegment StartX=333 StartY=2038 StartZ=0 EndX=117 EndY=2038 EndZ=0
    g15: LineSegment StartX=117 StartY=2038 StartZ=0 EndX=117 EndY=117 EndZ=0
  constraints (47):
    c: Coincident(g0,g1)
    c: Coincident(g1,g2)
    c: Coincident(g2,g3)
    c: Coincident(g3,g0)
    c: Horizontal(g0)
    c: Horizontal(g2)
    c: Vertical(g1)
    c: Vertical(g3)
    c: Coincident(g4,g5)
    c: Coincident(g5,g6)
    c: Coincident(g6,g7)
    c: Coincident(g7,g4)
    c: Horizontal(g4)
    c: Horizontal(g6)
    c: Vertical(g5)
    c: Vertical(g7)
    c: DistanceY(g1) = 2155  'Height'
    c: DistanceX(g0) = 450  'Width'
    c: DistanceY(g6,g2) = 70  'Frame1'
    c: DistanceX(g2,g6) = 70  'Frame2'
    c: DistanceX(g4,g0) = 70  'Frame3'
    c: DistanceY(g0,g4) = 70  'Frame4'
    c: Coincident(g0,g-1)
    c: Coincident(g8,g9)
    c: Coincident(g9,g10)
    c: Coincident(g10,g11)
    c: Coincident(g11,g8)
    c: Horizontal(g8)
    c: Horizontal(g10)
    c: Vertical(g9)
    c: Vertical(g11)
    c: Coincident(g12,g13)
    c: Coincident(g13,g14)
    c: Coincident(g14,g15)
    c: Coincident(g15,g12)
    c: Horizontal(g12)
    c: Horizontal(g14)
    c: Vertical(g13)
    c: Vertical(g15)
    c: DistanceX(g8,g12) = 40
    c: DistanceY(g8,g12) = 40
    c: DistanceX(g14,g10) = 40
    c: DistanceY(g14,g10) = 40
    c: DistanceX(g4,g8) = 7
    c: DistanceY(g4,g8) = 7
    c: DistanceX(g10,g6) = 7
    c: DistanceY(g10,g6) = 7
FEATURE [Part::FeaturePython] Window090  label="ОК-3-001"  # Arch/BIM 170 (typed FeaturePython)
  Area = 969750
  Base = -> Sketch396
  Frame = 70
  Height = 2155
  HoleDepth = 0
  HoleWire = 0
  HorizontalArea = 0
  IfcData = attributes={"GlobalId": {"name": "GlobalId", "type": "IfcGloballyUniqueId", "is_enum": false, "enum_values": []}, "Description": {"... (+1230 chars omitted),+1 more (map truncated)
  IfcType = 170
  LouvreSpacing = 0
  LouvreWidth = 0
  Material = -> Material011
  MoveBase = false
  MoveWithHost = true
  Normal = (0,0,0)
  Opening = 0
  OverallHeight = 2155
  OverallWidth = 450
  PartitioningType = 0
  PerimeterLength = 0
  PredefinedType = 0
  Preset = 2
  SymbolElevation = false
  SymbolPlan = false
  VerticalArea = 0
  Width = 450
  WindowParts = OuterFrame | Frame | Wire0,Wire1 | 0.0+V | 0.00+V | InnerFrame | Frame | Wire2,Wire3,Edge8,Mode2 | 0.00+V | 0.0+V | InnerGlass | Glass panel | Wire3 | 8.0 | 40.0+V
  expr: OverallHeight = .Height.Value
  expr: OverallWidth = .Width.Value
FEATURE [Sketcher::SketchObject] Sketch397
  FullyConstrained = true
  Placement = pos=(5625,-435,-70) rot=(0,0.707107,0.707107;3.14159rad)
  sketch-geometry (16):
    g0: LineSegment StartX=0 StartY=0 StartZ=0 EndX=1060 EndY=0 EndZ=0
    g1: LineSegment StartX=1060 StartY=0 StartZ=0 EndX=1060 EndY=2155 EndZ=0
    g2: LineSegment StartX=1060 StartY=2155 StartZ=0 EndX=0 EndY=2155 EndZ=0
    g3: LineSegment StartX=0 StartY=2155 StartZ=0 EndX=0 EndY=0 EndZ=0
    g4: LineSegment StartX=76 StartY=70 StartZ=0 EndX=990 EndY=70 EndZ=0
    g5: LineSegment StartX=990 StartY=70 StartZ=0 EndX=990 EndY=2085 EndZ=0
    g6: LineSegment StartX=990 StartY=2085 StartZ=0 EndX=76 EndY=2085 EndZ=0
    g7: LineSegment StartX=76 StartY=2085 StartZ=0 EndX=76 EndY=70 EndZ=0
    g8: LineSegment StartX=83 StartY=77 StartZ=0 EndX=983 EndY=77 EndZ=0
    g9: LineSegment StartX=983 StartY=77 StartZ=0 EndX=983 EndY=2078 EndZ=0
    g10: LineSegment StartX=983 StartY=2078 StartZ=0 EndX=83 EndY=2078 EndZ=0
    g11: LineSegment StartX=83 StartY=2078 StartZ=0 EndX=83 EndY=77 EndZ=0
    g12: LineSegment StartX=233 StartY=1112 StartZ=0 EndX=833 EndY=1112 EndZ=0
    g13: LineSegment StartX=833 StartY=1112 StartZ=0 EndX=833 EndY=1928 EndZ=0
    g14: LineSegment StartX=833 StartY=1928 StartZ=0 EndX=233 EndY=1928 EndZ=0
    g15: LineSegment StartX=233 StartY=1928 StartZ=0 EndX=233 EndY=1112 EndZ=0
  constraints (47):
    c: Coincident(g0,g1)
    c: Coincident(g1,g2)
    c: Coincident(g2,g3)
    c: Coincident(g3,g0)
    c: Horizontal(g0)
    c: Horizontal(g2)
    c: Vertical(g1)
    c: Vertical(g3)
    c: Coincident(g4,g5)
    c: Coincident(g5,g6)
    c: Coincident(g6,g7)
    c: Coincident(g7,g4)
    c: Horizontal(g4)
    c: Horizontal(g6)
    c: Vertical(g5)
    c: Vertical(g7)
    c: DistanceY(g1) = 2155  'Height'
    c: DistanceX(g0) = 1060  'Width'
    c: DistanceY(g6,g2) = 70  'Frame1'
    c: DistanceX(g2,g6) = 76  'Frame2'
    c: DistanceX(g4,g0) = 70  'Frame3'
    c: DistanceY(g0,g4) = 70  'Frame4'
    c: Coincident(g0,g-1)
    c: Coincident(g8,g9)
    c: Coincident(g9,g10)
    c: Coincident(g10,g11)
    c: Coincident(g11,g8)
    c: Horizontal(g8)
    c: Horizontal(g10)
    c: Vertical(g9)
    c: Vertical(g11)
    c: Coincident(g12,g13)
    c: Coincident(g13,g14)
    c: Coincident(g14,g15)
    c: Coincident(g15,g12)
    c: Horizontal(g12)
    c: Horizontal(g14)
    c: Vertical(g13)
    c: Vertical(g15)
    c: DistanceX(g8,g12) = 150
    c: DistanceY(g8,g12) = 1035
    c: DistanceX(g14,g10) = 150
    c: DistanceY(g14,g10) = 150
    c: DistanceX(g4,g8) = 7
    c: DistanceY(g4,g8) = 7
    c: DistanceX(g10,g6) = 7
    c: DistanceY(g10,g6) = 7
FEATURE [Part::FeaturePython] Window091  label="Д-2-001"  # Arch/BIM 170 (typed FeaturePython)
  Area = 2284300
  Base = -> Sketch397
  Frame = 70
  Height = 2155
  HoleDepth = 0
  HoleWire = 0
  HorizontalArea = 0
  IfcData = attributes={"GlobalId": {"name": "GlobalId", "type": "IfcGloballyUniqueId", "is_enum": false, "enum_values": []}, "Description": {"... (+1231 chars omitted),+1 more (map truncated)
  IfcType = 170
  LouvreSpacing = 0
  LouvreWidth = 0
  Material = -> Material011
  MoveBase = false
  MoveWithHost = true
  Normal = (0,0,0)
  Opening = 0
  OverallHeight = 2155
  OverallWidth = 1060
  PartitioningType = 0
  PerimeterLength = 0
  PredefinedType = 0
  Preset = 2
  SymbolElevation = false
  SymbolPlan = false
  VerticalArea = 0
  Width = 1060
  WindowParts = OuterFrame | Frame | Wire0,Wire1 | 0.0+V | 0.00+V | InnerFrame | Frame | Wire2,Wire3,Edge6,Mode2 | 0.00+V | 0.0+V | InnerGlass | Glass panel | Wire3 | 8.0 | 40.0+V
  expr: OverallWidth = .Width.Value
  expr: OverallHeight = .Height.Value
FEATURE [Part::Cut] Cut075
  Base = -> Box3230
  Tool = -> Box3231
FEATURE [Part::Cut] Cut076  label="Колонна с ДШ и МВ"
  Base = -> Cut075
  Tool = -> Box3209
FEATURE [Part::Part2DObjectPython] Line1903  # Draft 2D object (typed FeaturePython)
  ChamferSize = 0
  Closed = true
  End = (4455,3165,0)
  FilletRadius = 0
  Length = 1570
  MakeFace = false
  Placement = pos=(9225,3160,0) rot=(0,0,-1;1.5708rad)
  Points = (2) [(-5,-3200,0),(-5,-4770,0)]
  Start = (6025,3165,0)
  Subdivisions = 0
FEATURE [Part::Part2DObjectPython] Line1904  # Draft 2D object (typed FeaturePython)
  ChamferSize = 0
  Closed = true
  End = (8025,2605,0)
  FilletRadius = 0
  Length = 610
  MakeFace = false
  Placement = pos=(9510,1235,0) rot=(0,0,-1;0rad)
  Points = (2) [(-2095,1370,0),(-1485,1370,0)]
  Start = (7415,2605,0)
  Subdivisions = 0
FEATURE [Part::FeaturePython] Wall417  label="перегородка (сил.блок 500х250х80) 010"  # Arch/BIM 166 (typed FeaturePython)
  Align = 2
  Area = 1830000
  Base = -> Line1904
  BlockHeight = 250
  BlockLength = 0
  CountBroken = 0
  CountEntire = 0
  Face = 0
  GlobalId = 1OB118XG9DJPL5jtZdDHzR
  Height = 3000
  HorizontalArea = 48800
  IfcData = IfcUID=1OB118XG9DJPL5jtZdDHzR; attributes={"GlobalId": {"value": "1OB118XG9DJPL5jtZdDHzR"}}
  IfcType = 166
  Joint = 0
  Length = 610
  MakeBlocks = false
  Material = -> Material009
  MoveBase = false
  MoveWithHost = false
  Normal = (0,0,0)
  OffsetFirst = 300
  OffsetSecond = 50
  PerimeterLength = 1380
  Placement = pos=(0,0,-200) rot=(0,0,1;0rad)
  PredefinedType = 0
  VerticalArea = 4140000
  Width = 80
FEATURE [Part::Part2DObjectPython] Line1906  # Draft 2D object (typed FeaturePython)
  ChamferSize = 0
  Closed = true
  End = (5785,5595,4.547e-13)
  FilletRadius = 0
  Length = 2820
  MakeFace = false
  Placement = pos=(4415,6120,0) rot=(0,0,-1;1.5708rad)
  Points = (2) [(-2295,1370,0),(525,1370,4.54747e-13)]
  Start = (5785,8415,0)
  Subdivisions = 0
FEATURE [Part::Part2DObjectPython] Line1907  # Draft 2D object (typed FeaturePython)
  ChamferSize = 0
  Closed = true
  End = (5825,5635,0)
  FilletRadius = 0
  Length = 1030
  MakeFace = false
  Placement = pos=(10345,5630,0) rot=(0,0,-1;1.5708rad)
  Points = (2) [(-5,-3490,0),(-5,-4520,0)]
  Start = (6855,5635,0)
  Subdivisions = 0
FEATURE [Part::Part2DObjectPython] Wire985  label="Ванная"  # Draft 2D object (typed FeaturePython)
  Area = 8.3924e+06
  ChamferSize = 0
  Closed = true
  End = (5725,6475,0)
  FilletRadius = 0
  Length = 15340
  MakeFace = true
  Placement = pos=(5825,5575,0) rot=(0,0,1;3.14159rad)
  Points = (10) [(100,-3.63798e-12,0),(-1010,-3.63798e-12,0),(-1010,1040,0),(2000,1040,0),(2000,-2820,0),(100,-2820,0),(100,-1020,0),(900,-1020,0),(900,-900,0),+1 more]
  Start = (5725,5575,0)
  Subdivisions = 0
FEATURE [Part::Part2DObjectPython] Wire989  label="Санузел"  # Draft 2D object (typed FeaturePython)
  Area = 2200800
  ChamferSize = 0
  Closed = true
  End = (6215,1465,0)
  FilletRadius = 0
  Length = 6400
  MakeFace = true
  Placement = pos=(7550,2965,0) rot=(0,0,1;0rad)
  Points = (6) [(-1335,-2990,0),(375,-2990,0),(375,-1890,0),(-515,-1890,0),(-515,-1500,0),(-1335,-1500,0)]
  Start = (6215,-25,0)
  Subdivisions = 0
FEATURE [Part::Part2DObjectPython] Wire990  label="Коридор"  # Draft 2D object (typed FeaturePython)
  Area = 5586000
  ChamferSize = 0
  Closed = true
  End = (7125,3225,0)
  FilletRadius = 0
  Length = 11710
  MakeFace = true
  Placement = pos=(3220,2905,0) rot=(0,0,1;0rad)
  Points = (4) [(-750,320,0),(-750,1520,0),(3905,1520,0),(3905,320,0)]
  Start = (2470,3225,0)
  Subdivisions = 0
FEATURE [Part::Part2DObjectPython] Wire992  label="Спальня"  # Draft 2D object (typed FeaturePython)
  Area = 15356550
  ChamferSize = 0
  Closed = true
  End = (2370,3875,0)
  FilletRadius = 0
  Length = 16170
  MakeFace = true
  Placement = pos=(-30,4265,0) rot=(0,0,1;0rad)
  Points = (6) [(2.98428e-13,-390,0),(2.98428e-13,4130,0),(3565,4130,0),(3565,260,0),(2400,260,0),(2400,-390,0)]
  Start = (-30,3875,0)
  Subdivisions = 0
FEATURE [Part::Part2DObjectPython] Wire1000  label="санузел001"  # Draft 2D object (typed FeaturePython)
  Area = 0
  ChamferSize = 0
  Closed = true
  End = (7035,1465,0)
  FilletRadius = 0
  Length = 6400
  MakeFace = false
  Placement = pos=(7550,2965,0) rot=(0,0,1;0rad)
  Points = (6) [(-515,-1890,0),(375,-1890,0),(375,-2990,0),(-1335,-2990,0),(-1335,-1500,0),(-515,-1500,0)]
  Start = (7035,1075,0)
  Subdivisions = 0
FEATURE [Part::Part2DObjectPython] Rectangle3715  # Draft 2D object (typed FeaturePython)
  Area = 0
  ChamferSize = 0
  Columns = 1
  FilletRadius = 0
  Height = 1200
  Length = 2500
  MakeFace = false
  Placement = pos=(6835,5316.27,2220) rot=(0.664306,0.342629,-0.664306;3.80178rad)
  Rows = 1
FEATURE [Part::FeaturePython] Structure546  label="Структура028"  # Arch/BIM 172 (typed FeaturePython)
  Base = -> Rectangle3715
  FaceMaker = 0
  Height = 1000
  HorizontalArea = 0
  IfcData = attributes={"GlobalId": {"name": "GlobalId", "type": "IfcGloballyUniqueId", "is_enum": false, "enum_values": []}, "Description": {"... (+484 chars omitted),+1 more (map truncated)
  IfcType = 172
  Length = 0
  MoveBase = false
  MoveWithHost = false
  Nodes = (2) [(8788.46,3195,2817.12),(8788.46,5305,2817.12)]
  NodesOffset = 0
  Normal = (0,0,0)
  PerimeterLength = 0
  Placement = pos=(9.09e-13,217.459,1318.04) rot=(0,0,1;0rad)
  PredefinedType = 0
  VerticalArea = 6e+06
  Width = 100
FEATURE [Part::FeaturePython] Wall420  label="перегородка (сил.блок 500х250х80) 013"  # Arch/BIM 166 (typed FeaturePython)
  Align = 2
  Area = 2.2866e+06
  Base = -> Line1907
  BlockHeight = 250
  BlockLength = 0
  CountBroken = 0
  CountEntire = 0
  Face = 0
  GlobalId = 2YMQSCXEvDBOywm4rK59sv
  Height = 2220
  HorizontalArea = 82400
  IfcData = IfcUID=2YMQSCXEvDBOywm4rK59sv; attributes={"GlobalId": {"value": "2YMQSCXEvDBOywm4rK59sv"}}
  IfcType = 166
  Joint = 0
  Length = 1030
  MakeBlocks = false
  Material = -> Material009
  MoveBase = false
  MoveWithHost = false
  Normal = (0,0,0)
  OffsetFirst = 300
  OffsetSecond = 50
  PerimeterLength = 2220
  Placement = pos=(0,0,-200) rot=(0,0,1;0rad)
  PredefinedType = 0
  Subtractions = -> [Structure546]
  VerticalArea = 4.87744e+06
  Width = 80
FEATURE [Part::Cylinder] Cylinder010  label="ГА 80л вертикальный"
  Angle = 360
  AttacherType = Attacher::AttachEngine3D
  Height = 820
  Placement = pos=(6350.76,2737.83,0) rot=(0,0,1;0rad)
  Radius = 190
FEATURE [App::FeaturePython] Dimension184  # Draft dimension (typed FeaturePython)
  Diameter = false
  Dimline = (7165,-800,0)
  Direction = (0,0,0)
  Distance = 530
  End = (7760,-555,0)
  Normal = (0,0,1)
  Start = (7230,-555,0)
FEATURE [App::FeaturePython] Dimension185  # Draft dimension (typed FeaturePython)
  Diameter = false
  Dimline = (4800,7600,0)
  Direction = (0,0,0)
  Distance = 120
  End = (4925,6595,0)
  Normal = (0,0,1)
  Start = (4925,6475,0)
FEATURE [App::FeaturePython] Dimension186  # Draft dimension (typed FeaturePython)
  Diameter = false
  Dimline = (7100,900,0)
  Direction = (0,0,0)
  Distance = 820
  End = (7035,1525,0)
  Normal = (0,0,1)
  Start = (6215,1525,0)
FEATURE [Part::Part2DObjectPython] ShapeString238  # Draft 2D object (typed FeaturePython)
  FontFile = <path>
  Placement = pos=(907.682,395.127,0) rot=(0,0,1;0rad)
  Size = 130
  String = 209x91
  Tracking = 0
FEATURE [Part::Part2DObjectPython] ShapeString239  # Draft 2D object (typed FeaturePython)
  FontFile = <path>
  Placement = pos=(704.405,3541.96,0) rot=(0,0,1;0rad)
  Size = 130
  String = 170x60
  Tracking = 0
FEATURE [Part::Part2DObjectPython] ShapeString240  # Draft 2D object (typed FeaturePython)
  FontFile = <path>
  Placement = pos=(706.605,6422.3,0) rot=(0,0,1;0rad)
  Size = 130
  String = 210x180
  Tracking = 0
FEATURE [Part::Part2DObjectPython] ShapeString243  # Draft 2D object (typed FeaturePython)
  FontFile = <path>
  Placement = pos=(9521.61,4412.3,0) rot=(0,0,1;0rad)
  Size = 130
  String = 140x80
  Tracking = 0
FEATURE [Part::Part2DObjectPython] ShapeString244  # Draft 2D object (typed FeaturePython)
  FontFile = <path>
  Placement = pos=(10134.8,6665.28,0) rot=(0,0,1;1.5708rad)
  Size = 130
  String = 250x95
  Tracking = 0
FEATURE [Part::Part2DObjectPython] ShapeString245  # Draft 2D object (typed FeaturePython)
  FontFile = <path>
  Placement = pos=(5389.26,7203.62,0) rot=(0,0,1;1.5708rad)
  Size = 130
  String = 180x80
  Tracking = 0
FEATURE [Part::Part2DObjectPython] ShapeString246  # Draft 2D object (typed FeaturePython)
  FontFile = <path>
  Placement = pos=(6267.24,4814.55,0) rot=(0,0,1;1.5708rad)
  Size = 130
  String = 104x111
  Tracking = 0
FEATURE [App::FeaturePython] Dimension187  # Draft dimension (typed FeaturePython)
  Diameter = false
  Dimline = (7262.97,739.621,0)
  Direction = (0,0,0)
  Distance = 1100
  End = (7875,1075,0)
  Normal = (0,0,1)
  Start = (7875,-25,0)
FEATURE [Part::Part2DObjectPython] Rectangle3721  label="монолитный участок 001"  # Draft 2D object (typed FeaturePython)
  Area = 0
  ChamferSize = 0
  Columns = 1
  FilletRadius = 0
  Height = 1200
  Length = 1130
  MakeFace = false
  Placement = pos=(5815,3075,0) rot=(0,0,1;0rad)
  Rows = 1
FEATURE [Part::FeaturePython] Structure551  label="монолитный участок"  # Arch/BIM 172 (typed FeaturePython)
  Base = -> Rectangle3721
  FaceMaker = 0
  Height = 160
  HorizontalArea = 1356000
  IfcData = attributes={"GlobalId": {"name": "GlobalId", "type": "IfcGloballyUniqueId", "is_enum": false, "enum_values": []}, "Description": {"... (+484 chars omitted),+1 more (map truncated)
  IfcType = 172
  Length = 0
  Material = -> Material018
  MoveBase = false
  MoveWithHost = false
  Nodes = (2) [(6380,3675,0),(6380,3675,160)]
  NodesOffset = 0
  Normal = (0,0,0)
  PerimeterLength = 4660
  Placement = pos=(0,0,2800) rot=(0,0,1;0rad)
  PredefinedType = 0
  VerticalArea = 745600
  Width = 100
FEATURE [Part::FeaturePython] Component212  label="Компонент041"  # Arch/BIM 0 (typed FeaturePython)
  Base = -> Wire817
  HorizontalArea = 0
  IfcData = attributes={"GlobalId": {"name": "GlobalId", "type": "IfcGloballyUniqueId", "is_enum": false, "enum_values": []}, "Description": {"... (+538 chars omitted),+1 more (map truncated)
  IfcType = 0
  MoveBase = false
  MoveWithHost = false
  PerimeterLength = 0
  Placement = pos=(-1210,-1210,0) rot=(0,0,1;0rad)
  PredefinedType = 0
  VerticalArea = 0
FEATURE [Part::Part2DObjectPython] Wire1003  label="кровля_контур_002"  # Draft 2D object (typed FeaturePython)
  Area = 0
  ChamferSize = 0
  Closed = true
  End = (-1215,9580,0)
  FilletRadius = 0
  Length = 47580
  MakeFace = false
  Placement = pos=(15200,-1120,0) rot=(0,0,1;0rad)
  Points = (4) [(-16415,-90,0),(-3415,-90,0),(-3415,10700,0),(-16415,10700,0)]
  Start = (-1215,-1210,0)
  Subdivisions = 0
FEATURE [Part::Extrusion] Extrude099019  label="Extrude099021"
  Base = -> Wire817
  Dir = (0,0,1)
  DirMode = 2
  FaceMakerClass = Part::FaceMakerBullseye
  LengthFwd = 5000
  LengthRev = 0
  Placement = pos=(0,0,2720) rot=(0,0,1;0rad)
  Solid = true
  Symmetric = false
FEATURE [Part::FeaturePython] Roof026  label="roof_4_side_cut_inside"  # Arch/BIM 113 (typed FeaturePython)
  Angles = [35,45,35,45]
  Base = -> Wire1003
  BorderLength = 0
  Face = 0
  Flip = false
  Heights = [3777.62,5500,3777.62,5500]
  HorizontalArea = 186094500
  IdRel = [-1,-1,-1,-1]
  IfcData = attributes={"GlobalId": {"name": "GlobalId", "type": "IfcGloballyUniqueId", "is_enum": false, "enum_values": []}, "Description": {"... (+613 chars omitted),+1 more (map truncated)
  IfcType = 113
  Material = -> Material007
  MoveBase = false
  MoveWithHost = false
  Overhang = [1000,775,1000,775]
  PerimeterLength = 0
  Placement = pos=(0,-2.27e-13,3250) rot=(0,0,1;0rad)
  PredefinedType = 0
  RidgeLength = 0
  Runs = [5500,5500,5500,5500]
  Thickness = [5500,4750,5500,4750]
  VerticalArea = 3.67322e+08
FEATURE [Sketcher::SketchObject] Sketch364
  FullyConstrained = false
  MapMode = 5
  Placement = pos=(10929,-710.046,-122.202) rot=(0.57735,0.57735,0.57735;2.0944rad)
  sketch-geometry (10):
    g0: LineSegment StartX=8591.88 StartY=1733.04 StartZ=0 EndX=8591.88 EndY=3413.04 EndZ=0
    g1: LineSegment StartX=8591.88 StartY=3413.04 StartZ=0 EndX=9574.86 EndY=2724.75 EndZ=0
    g2: LineSegment StartX=9574.86 StartY=2724.75 StartZ=0 EndX=9517.51 EndY=2642.83 EndZ=0
    g3: LineSegment StartX=9517.51 StartY=2642.83 StartZ=0 EndX=9312.72 EndY=2786.22 EndZ=0
    g4: LineSegment StartX=9312.72 StartY=2786.22 StartZ=0 EndX=8691.88 EndY=1899.58 EndZ=0
    g5: LineSegment StartX=8691.88 StartY=1899.58 StartZ=0 EndX=8691.88 EndY=1733.04 EndZ=0
    g6: LineSegment StartX=8691.88 StartY=1733.04 StartZ=0 EndX=8591.88 EndY=1733.04 EndZ=0
    g7: LineSegment StartX=8691.88 StartY=2073.92 StartZ=0 EndX=8691.88 EndY=3220.94 EndZ=0
    g8: LineSegment StartX=8691.88 StartY=3220.94 StartZ=0 EndX=9230.8 EndY=2843.58 EndZ=0
    g9: LineSegment StartX=9230.8 StartY=2843.58 StartZ=0 EndX=8691.88 EndY=2073.92 EndZ=0
  constraints (28):
    c: Vertical(g0)
    c: Coincident(g1,g2)
    c: Coincident(g2,g3)
    c: Coincident(g3,g4)
    c: Coincident(g4,g5)
    c: Vertical(g5)
    c: Coincident(g5,g6)
    c: Coincident(g6,g0)
    c: Vertical(g7)
    c: Coincident(g7,g8)
    c: Coincident(g8,g9)
    c: Coincident(g9,g7)
    c: Parallel(g4,g9)
    c: Horizontal(g6)
    c: Parallel(g3,g1)
    c: Parallel(g9,g2)
    c: Parallel(g8,g3)
    c: Distance(g8,g4) = 100
    c: Distance(g8,g1) = 100
    c: Distance(g3,g1) = 100
    c: Distance(g7,g0) = 100
    c: DistanceX(g6,g6) = 100
    c: Coincident(g0,g1)
    c: Distance(g1) = 1200
    c: DistanceY(g0,g0) = 1680
    c: Angle(g4,g3) = 1.5708
    c: Distance(g3) = 250
    c: Angle(g1) = -0.610865
FEATURE [Part::Extrusion] Extrude099002  label="Подкосы крыльца 017"
  Base = -> Sketch364
  Dir = (1,0,0)
  DirMode = 2
  FaceMakerClass = Part::FaceMakerBullseye
  LengthFwd = 150
  LengthRev = 0
  Placement = pos=(17654,7326.23,420) rot=(0,0,1;3.14159rad)
  Solid = true
  Symmetric = false
FEATURE [Part::Extrusion] Extrude099003  label="Подкосы крыльца 018"
  Base = -> Sketch364
  Dir = (1,0,0)
  DirMode = 2
  FaceMakerClass = Part::FaceMakerBullseye
  LengthFwd = 150
  LengthRev = 0
  Placement = pos=(-974,1043.77,420) rot=(0,0,1;0rad)
  Solid = true
  Symmetric = false
FEATURE [Part::Extrusion] Extrude099004  label="Подкосы крыльца 019"
  Base = -> Sketch364
  Dir = (1,0,0)
  DirMode = 2
  FaceMakerClass = Part::FaceMakerBullseye
  LengthFwd = 150
  LengthRev = 0
  Placement = pos=(-4224,1043.77,420) rot=(0,0,1;0rad)
  Solid = true
  Symmetric = false
FEATURE [Part::Extrusion] Extrude099005  label="Подкосы крыльца 020"
  Base = -> Sketch364
  Dir = (1,0,0)
  DirMode = 2
  FaceMakerClass = Part::FaceMakerBullseye
  LengthFwd = 150
  LengthRev = 0
  Placement = pos=(14924,7326.23,420) rot=(0,0,1;3.14159rad)
  Solid = true
  Symmetric = false
FEATURE [Part::FeaturePython] Roof027  label="Кровля 2скатн003"  # Arch/BIM 113 (typed FeaturePython)
  Angles = [35,90,35,90]
  Base = -> Rectangle3216
  BorderLength = 40428.5
  Face = 0
  Flip = false
  Heights = [1925.57,0,1925.57,0]
  HorizontalArea = 7.425e+07
  IdRel = [-1,-1,-1,-1]
  IfcData = attributes={"GlobalId": {"name": "GlobalId", "type": "IfcGloballyUniqueId", "is_enum": false, "enum_values": []}, "Description": {"... (+613 chars omitted),+1 more (map truncated)
  IfcType = 113
  Material = -> Material007
  MoveBase = false
  MoveWithHost = false
  Overhang = [0,0,0,0]
  PerimeterLength = 38000
  Placement = pos=(0,0,4317.05) rot=(0,0,1;0rad)
  PredefinedType = 0
  RidgeLength = 13500
  Runs = [4500,4500,4500,4500]
  Thickness = [350,250,350,250]
  VerticalArea = 1.62363e+07
FEATURE [Part::Extrusion] Extrude099005002
  Base = -> Rectangle3284
  Dir = (0,0,1)
  DirMode = 2
  FaceMakerClass = Part::FaceMakerBullseye
  LengthFwd = 5000
  LengthRev = 0
  Placement = pos=(0,0,2500) rot=(0,0,1;0rad)
  Solid = true
  Symmetric = false
FEATURE [Part::FeaturePython] Structure560  label="Вентстояк вычитаемы объём 009"  # Arch/BIM 52 (typed FeaturePython)
  FaceMaker = 0
  GlobalId = 2VgUxAGbH6UvSFD9GbSn_n
  Height = 4000
  HorizontalArea = 1.1584e+06
  IfcData = IfcUID=2VgUxAGbH6UvSFD9GbSn_n,attributes={"GlobalId": {"value": "2VgUxAGbH6UvSFD9GbSn_n"}},+1 more (map truncated)
  IfcType = 52
  Length = 0
  MoveBase = false
  MoveWithHost = false
  Nodes = (2) [(7235,1875,0),(7235,1875,4000)]
  NodesOffset = 0
  Normal = (0,0,0)
  PerimeterLength = 4900
  Placement = pos=(0,0,2800) rot=(0,0,1;0rad)
  VerticalArea = 19600000
  Width = 100
FEATURE [Part::Part2DObjectPython] Line1936  label="облицовка ВШ_линия_009"  # Draft 2D object (typed FeaturePython)
  ChamferSize = 0
  Closed = true
  End = (6915,970,0)
  FilletRadius = 0
  Length = 510
  MakeFace = false
  Placement = pos=(7125,970,0) rot=(0,0,1;0rad)
  Points = (2) [(300,-9.09495e-13,0),(-210,0,0)]
  Start = (7425,970,0)
  Subdivisions = 0
FEATURE [Part::FeaturePython] Wall431  label="облицовка ВШ  005"  # Arch/BIM 166 (typed FeaturePython)
  Align = 0
  Area = 2142000
  Base = -> Line1936
  BlockHeight = 65
  BlockLength = 250
  CountBroken = 112
  CountEntire = 28
  Face = 0
  GlobalId = 0NV5Z8QsLE8RP4h00TMdTp
  Height = 4200
  HorizontalArea = 61200
  IfcData = IfcUID=0NV5Z8QsLE8RP4h00TMdTp; attributes={"GlobalId": {"value": "0NV5Z8QsLE8RP4h00TMdTp"}}
  IfcType = 166
  Joint = 10
  Length = 510
  MakeBlocks = false
  Material = -> Material003
  MoveBase = false
  MoveWithHost = false
  Normal = (0,0,0)
  OffsetFirst = 0
  OffsetSecond = 120
  PerimeterLength = 1260
  Placement = pos=(0,0,2960) rot=(0,0,1;0rad)
  PredefinedType = 0
  VerticalArea = 5292000
  Width = 120
FEATURE [Part::Part2DObjectPython] Line1937  label="облицовка ВШ_линия_010"  # Draft 2D object (typed FeaturePython)
  ChamferSize = 0
  Closed = true
  End = (7555,2780,0)
  FilletRadius = 0
  Length = 510
  MakeFace = false
  Placement = pos=(7345,2780,0) rot=(0,0,1;3.14159rad)
  Points = (2) [(300,9.09495e-13,0),(-210,9.09495e-13,0)]
  Start = (7045,2780,0)
  Subdivisions = 0
FEATURE [Part::FeaturePython] Wall432  label="облицовка ВШ  006"  # Arch/BIM 166 (typed FeaturePython)
  Align = 0
  Area = 2142000
  Base = -> Line1937
  BlockHeight = 65
  BlockLength = 250
  CountBroken = 112
  CountEntire = 28
  Face = 0
  GlobalId = 2TkovYGMD8r9zraP45mHkR
  Height = 4200
  HorizontalArea = 61200
  IfcData = IfcUID=2TkovYGMD8r9zraP45mHkR; attributes={"GlobalId": {"value": "2TkovYGMD8r9zraP45mHkR"}}
  IfcType = 166
  Joint = 10
  Length = 510
  MakeBlocks = false
  Material = -> Material003
  MoveBase = false
  MoveWithHost = false
  Normal = (0,0,0)
  OffsetFirst = 0
  OffsetSecond = 120
  PerimeterLength = 1260
  Placement = pos=(0,0,2960) rot=(0,0,1;0rad)
  PredefinedType = 0
  VerticalArea = 5292000
  Width = 120
FEATURE [Part::Part2DObjectPython] Line1938  label="облицовка ВШ_линия_011"  # Draft 2D object (typed FeaturePython)
  ChamferSize = 0
  Closed = true
  End = (6915,2780,0)
  FilletRadius = 0
  Length = 1680
  MakeFace = false
  Placement = pos=(7215,2000,0) rot=(0,0,1;3.14159rad)
  Points = (2) [(300,900,0),(300,-780,0)]
  Start = (6915,1100,0)
  Subdivisions = 0
FEATURE [Part::FeaturePython] Wall433  label="облицовка ВШ  007"  # Arch/BIM 166 (typed FeaturePython)
  Align = 0
  Area = 7.056e+06
  Base = -> Line1938
  BlockHeight = 65
  BlockLength = 250
  CountBroken = 84
  CountEntire = 308
  Face = 0
  GlobalId = 0woF2TLZD1r929WxYa3eSK
  Height = 4200
  HorizontalArea = 201600
  IfcData = IfcUID=0woF2TLZD1r929WxYa3eSK; attributes={"GlobalId": {"value": "0woF2TLZD1r929WxYa3eSK"}}
  IfcType = 166
  Joint = 10
  Length = 1680
  MakeBlocks = false
  Material = -> Material003
  MoveBase = false
  MoveWithHost = false
  Normal = (0,0,0)
  OffsetFirst = 0
  OffsetSecond = 120
  PerimeterLength = 3600
  Placement = pos=(0,0,2960) rot=(0,0,1;0rad)
  PredefinedType = 0
  VerticalArea = 1.512e+07
  Width = 120
FEATURE [Part::Part2DObjectPython] Line1939  label="облицовка ВШ_линия_012"  # Draft 2D object (typed FeaturePython)
  ChamferSize = 0
  Closed = true
  End = (7555,970,0)
  FilletRadius = 0
  Length = 1680
  MakeFace = false
  Placement = pos=(7255,710,0) rot=(0,0,1;0rad)
  Points = (2) [(300,1940,0),(300,260,0)]
  Start = (7555,2650,0)
  Subdivisions = 0
FEATURE [Part::FeaturePython] Wall434  label="облицовка ВШ  008"  # Arch/BIM 166 (typed FeaturePython)
  Align = 0
  Area = 7.056e+06
  Base = -> Line1939
  BlockHeight = 65
  BlockLength = 250
  CountBroken = 84
  CountEntire = 308
  Face = 0
  GlobalId = 0uV1Y0I5TBPurrni9deYxv
  Height = 4200
  HorizontalArea = 201600
  IfcData = IfcUID=0uV1Y0I5TBPurrni9deYxv; attributes={"GlobalId": {"value": "0uV1Y0I5TBPurrni9deYxv"}}
  IfcType = 166
  Joint = 10
  Length = 1680
  MakeBlocks = false
  Material = -> Material003
  MoveBase = false
  MoveWithHost = false
  Normal = (0,0,0)
  OffsetFirst = 0
  OffsetSecond = 120
  PerimeterLength = 3600
  Placement = pos=(0,0,2960) rot=(0,0,1;0rad)
  PredefinedType = 0
  VerticalArea = 1.512e+07
  Width = 120
FEATURE [Part::FeaturePython] Roof029  label="Крышка вентшахты001"  # Arch/BIM 113 (typed FeaturePython)
  Angles = [35,35,35,35]
  BorderLength = 5300
  Face = 0
  Flip = false
  GlobalId = 36hdyCWSLF5w0SQ7_aWhlx
  Heights = [224.066,245.073,224.066,245.073]
  HorizontalArea = 1.4134e+06
  IdRel = [-1,-1,-1,-1]
  IfcData = IfcUID=36hdyCWSLF5w0SQ7_aWhlx,+2 more (map truncated)
  IfcType = 113
  Material = -> Material007
  MoveBase = false
  MoveWithHost = false
  Overhang = [50,50,50,50]
  PerimeterLength = 0
  Placement = pos=(0,0,7400) rot=(0,0,1;0rad)
  PredefinedType = 0
  RidgeLength = 3505.54
  Runs = [350,350,350,350]
  Thickness = [10,10,10,10]
  VerticalArea = 64701.1
FEATURE [App::GeometryPython] BuildingPart133  label="облицовка дымохода шидель"  # Arch/BIM 172 (typed FeaturePython)
  Area = 1.8396e+07
  Group = -> [Wall434,Wall431,Wall432,Wall433,Roof029]
  Height = 0
  HeightPropagate = true
  IfcData = attributes={"GlobalId": {"name": "GlobalId", "type": "IfcGloballyUniqueId", "is_enum": false, "enum_values": []}, "Description": {"... (+484 chars omitted),+1 more (map truncated)
  IfcType = 172
  LevelOffset = 0
  Placement = pos=(0,0,5) rot=(0,0,1;0rad)
  PredefinedType = 0
FEATURE [App::MaterialObjectPython] Material021  label="Material"  # material (typed FeaturePython)
  Material = Name=Material; SectionColor=(0.0, 0.0, 0.0); Transparency=0
  Transparency = 0
FEATURE [Part::Part2DObjectPython] Wire1009  # Draft 2D object (typed FeaturePython)
  Area = 69637800
  ChamferSize = 0
  Closed = true
  End = (-1360,-1355,0)
  FilletRadius = 0
  Length = 37590
  MakeFace = true
  Placement = pos=(-1160,9525,0) rot=(0,0,1;0rad)
  Points = (6) [(-200,200,0),(7515,200,0),(7515,-5340,0),(4655,-5340,0),(4655,-10880,0),(-200,-10880,0)]
  Start = (-1360,9725,0)
  Subdivisions = 0
FEATURE [Part::Part2DObjectPython] Wire1010  # Draft 2D object (typed FeaturePython)
  Area = 35068200
  ChamferSize = 0
  Closed = true
  End = (10455,4185,0)
  FilletRadius = 0
  Length = 31870
  MakeFace = true
  Placement = pos=(8490,9525,0) rot=(0,0,1;0rad)
  Points = (6) [(1965,200,0),(3440,200,0),(3440,-10880,0),(-1415,-10880,0),(-1415,-5340,0),(1965,-5340,0)]
  Start = (10455,9725,0)
  Subdivisions = 0
FEATURE [Part::FeaturePython] Structure567  label="Структура031"  # Arch/BIM 172 (typed FeaturePython)
  Base = -> Wire1009
  FaceMaker = 0
  Height = 1000
  HorizontalArea = 69637800
  IfcData = attributes={"GlobalId": {"name": "GlobalId", "type": "IfcGloballyUniqueId", "is_enum": false, "enum_values": []}, "Description": {"... (+484 chars omitted),+1 more (map truncated)
  IfcType = 172
  Length = 0
  MoveBase = false
  MoveWithHost = false
  Nodes = (2) [(1146.63,4298.06,0),(1146.63,4298.06,1000)]
  NodesOffset = 0
  Normal = (0,0,1)
  PerimeterLength = 37590
  Placement = pos=(0,0,2495.76) rot=(0,0,1;0rad)
  PredefinedType = 0
  VerticalArea = 37590000
  Width = 100
FEATURE [Part::FeaturePython] Structure568  label="Структура032"  # Arch/BIM 172 (typed FeaturePython)
  Base = -> Wire1010
  FaceMaker = 0
  Height = 1000
  HorizontalArea = 35068200
  IfcData = attributes={"GlobalId": {"name": "GlobalId", "type": "IfcGloballyUniqueId", "is_enum": false, "enum_values": []}, "Description": {"... (+484 chars omitted),+1 more (map truncated)
  IfcType = 172
  Length = 0
  MoveBase = false
  MoveWithHost = false
  Nodes = (2) [(11141.9,4555.57,0),(11141.9,4555.57,1000)]
  NodesOffset = 0
  Normal = (0,0,1)
  PerimeterLength = 31870
  Placement = pos=(0,0,2495.76) rot=(0,0,1;0rad)
  PredefinedType = 0
  VerticalArea = 31870000
  Width = 100
FEATURE [Part::MultiFuse] Fusion076
  Shapes = -> [Structure568,Structure567]
FEATURE [Part::Part2DObjectPython] Line1949  # Draft 2D object (typed FeaturePython)
  Area = 0
  ChamferSize = 0
  Closed = false
  End = (6108.5,8805,0)
  FilletRadius = 0
  Length = 819.5
  MakeFace = true
  Placement = pos=(6928,8805,0) rot=(0,0,1;0rad)
  Points = (2) [(0,0,0),(-819.5,0,0)]
  Start = (6928,8805,0)
  Subdivisions = 0
FEATURE [Part::FeaturePython] Wall444  label="раскладка вычет 002"  # Arch/BIM 166 (typed FeaturePython)
  Align = 2
  Area = 1.8365e+06
  Base = -> Line1949
  BlockHeight = 275
  BlockLength = 260
  CountBroken = 17
  CountEntire = 7
  Face = 0
  Height = 2241
  HorizontalArea = 0
  IfcData = attributes={"GlobalId": {"name": "GlobalId", "type": "IfcGloballyUniqueId", "is_enum": false, "enum_values": []}, "Description": {"... (+533 chars omitted),+1 more (map truncated)
  IfcType = 166
  Joint = 10
  Length = 819.5
  MakeBlocks = true
  MoveBase = false
  MoveWithHost = false
  Normal = (0,0,0)
  OffsetFirst = 0
  OffsetSecond = 0
  PerimeterLength = 0
  Placement = pos=(0,-20,47) rot=(0,0,1;0rad)
  PredefinedType = 0
  VerticalArea = 0
  Width = 10
FEATURE [Part::FeaturePython] Wall443  label="раскладка окна 003"  # Arch/BIM 166 (typed FeaturePython)
  Align = 2
  Area = 1.8365e+06
  Base = -> Line1949
  BlockHeight = 0
  BlockLength = 0
  CountBroken = 0
  CountEntire = 0
  Face = 0
  Height = 2241
  HorizontalArea = 0
  IfcData = attributes={"GlobalId": {"name": "GlobalId", "type": "IfcGloballyUniqueId", "is_enum": false, "enum_values": []}, "Description": {"... (+533 chars omitted),+1 more (map truncated)
  IfcType = 166
  Joint = 0
  Length = 819.5
  MakeBlocks = false
  Material = -> Material011
  MoveBase = false
  MoveWithHost = false
  Normal = (0,0,0)
  OffsetFirst = 0
  OffsetSecond = 0
  PerimeterLength = 0
  Placement = pos=(0,-20,47) rot=(0,0,1;0rad)
  PredefinedType = 0
  Subtractions = -> [Wall444]
  VerticalArea = 0
  Width = 10
FEATURE [Part::FeaturePython] Wall445  label="раскладка окна 004"  # Arch/BIM 166 (typed FeaturePython)
  Align = 2
  Area = 1.8365e+06
  BlockHeight = 0
  BlockLength = 0
  CloneOf = -> Wall443
  CountBroken = 0
  CountEntire = 0
  Face = 0
  Height = 2241
  HorizontalArea = 0
  IfcData = attributes={"GlobalId": {"name": "GlobalId", "type": "IfcGloballyUniqueId", "is_enum": false, "enum_values": []}, "Description": {"... (+533 chars omitted),+1 more (map truncated)
  IfcType = 166
  Joint = 0
  Length = 819.5
  MakeBlocks = false
  Material = -> Material011
  MoveBase = false
  MoveWithHost = false
  Normal = (0,0,0)
  OffsetFirst = 0
  OffsetSecond = 0
  PerimeterLength = 0
  Placement = pos=(-906.5,-70,47) rot=(0,0,1;0rad)
  PredefinedType = 0
  VerticalArea = 0
  Width = 10
FEATURE [Part::Part2DObjectPython] Line1950  # Draft 2D object (typed FeaturePython)
  Area = 0
  ChamferSize = 0
  Closed = false
  End = (9750.5,8805,0)
  FilletRadius = 0
  Length = 539.5
  MakeFace = true
  Placement = pos=(10290,8805,0) rot=(0,0,1;0rad)
  Points = (2) [(0,0,0),(-539.5,0,0)]
  Start = (10290,8805,0)
  Subdivisions = 0
FEATURE [Part::FeaturePython] Wall446  label="раскладка вычет 003"  # Arch/BIM 166 (typed FeaturePython)
  Align = 2
  Area = 1.20902e+06
  Base = -> Line1950
  BlockHeight = 275
  BlockLength = 265
  CountBroken = 16
  CountEntire = 0
  Face = 0
  Height = 2241
  HorizontalArea = 0
  IfcData = attributes={"GlobalId": {"name": "GlobalId", "type": "IfcGloballyUniqueId", "is_enum": false, "enum_values": []}, "Description": {"... (+533 chars omitted),+1 more (map truncated)
  IfcType = 166
  Joint = 10
  Length = 539.5
  MakeBlocks = true
  MoveBase = false
  MoveWithHost = false
  Normal = (0,0,0)
  OffsetFirst = 0
  OffsetSecond = 0
  PerimeterLength = 0
  Placement = pos=(0,-20,47) rot=(0,0,1;0rad)
  PredefinedType = 0
  VerticalArea = 0
  Width = 10
FEATURE [Part::FeaturePython] Wall447  label="раскладка окна 005"  # Arch/BIM 166 (typed FeaturePython)
  Align = 2
  Area = 1.20902e+06
  Base = -> Line1950
  BlockHeight = 0
  BlockLength = 0
  CountBroken = 0
  CountEntire = 0
  Face = 0
  Height = 2241
  HorizontalArea = 0
  IfcData = attributes={"GlobalId": {"name": "GlobalId", "type": "IfcGloballyUniqueId", "is_enum": false, "enum_values": []}, "Description": {"... (+533 chars omitted),+1 more (map truncated)
  IfcType = 166
  Joint = 0
  Length = 539.5
  MakeBlocks = false
  Material = -> Material011
  MoveBase = false
  MoveWithHost = false
  Normal = (0,0,0)
  OffsetFirst = 0
  OffsetSecond = 0
  PerimeterLength = 0
  Placement = pos=(0,-20,47) rot=(0,0,1;0rad)
  PredefinedType = 0
  Subtractions = -> [Wall446]
  VerticalArea = 0
  Width = 10
FEATURE [Part::FeaturePython] Wall448  label="раскладка окна 006"  # Arch/BIM 166 (typed FeaturePython)
  Align = 2
  Area = 1.20902e+06
  BlockHeight = 0
  BlockLength = 0
  CloneOf = -> Wall447
  CountBroken = 0
  CountEntire = 0
  Face = 0
  Height = 2241
  HorizontalArea = 0
  IfcData = attributes={"GlobalId": {"name": "GlobalId", "type": "IfcGloballyUniqueId", "is_enum": false, "enum_values": []}, "Description": {"... (+533 chars omitted),+1 more (map truncated)
  IfcType = 166
  Joint = 0
  Length = 539.5
  MakeBlocks = false
  Material = -> Material011
  MoveBase = false
  MoveWithHost = false
  Normal = (0,0,0)
  OffsetFirst = 0
  OffsetSecond = 0
  PerimeterLength = 0
  Placement = pos=(-624.758,-20,47) rot=(0,0,1;0rad)
  PredefinedType = 0
  VerticalArea = 0
  Width = 10
FEATURE [Part::FeaturePython] Wall449  label="раскладка окна 007"  # Arch/BIM 166 (typed FeaturePython)
  Align = 2
  Area = 1.20902e+06
  BlockHeight = 0
  BlockLength = 0
  CloneOf = -> Wall447
  CountBroken = 0
  CountEntire = 0
  Face = 0
  Height = 2241
  HorizontalArea = 0
  IfcData = attributes={"GlobalId": {"name": "GlobalId", "type": "IfcGloballyUniqueId", "is_enum": false, "enum_values": []}, "Description": {"... (+533 chars omitted),+1 more (map truncated)
  IfcType = 166
  Joint = 0
  Length = 539.5
  MakeBlocks = false
  Material = -> Material011
  MoveBase = false
  MoveWithHost = false
  Normal = (0,0,0)
  OffsetFirst = 0
  OffsetSecond = 0
  PerimeterLength = 0
  Placement = pos=(-7280,-20,47) rot=(0,0,1;0rad)
  PredefinedType = 0
  VerticalArea = 0
  Width = 10
FEATURE [Part::FeaturePython] Wall450  label="раскладка окна 008"  # Arch/BIM 166 (typed FeaturePython)
  Align = 2
  Area = 1.20902e+06
  BlockHeight = 0
  BlockLength = 0
  CloneOf = -> Wall447
  CountBroken = 0
  CountEntire = 0
  Face = 0
  Height = 2241
  HorizontalArea = 0
  IfcData = attributes={"GlobalId": {"name": "GlobalId", "type": "IfcGloballyUniqueId", "is_enum": false, "enum_values": []}, "Description": {"... (+533 chars omitted),+1 more (map truncated)
  IfcType = 166
  Joint = 0
  Length = 539.5
  MakeBlocks = false
  Material = -> Material011
  MoveBase = false
  MoveWithHost = false
  Normal = (0,0,0)
  OffsetFirst = 0
  OffsetSecond = 0
  PerimeterLength = 0
  Placement = pos=(-7904.76,-20,47) rot=(0,0,1;0rad)
  PredefinedType = 0
  VerticalArea = 0
  Width = 10
FEATURE [Part::Part2DObjectPython] Line1952  # Draft 2D object (typed FeaturePython)
  Area = 0
  ChamferSize = 0
  Closed = false
  End = (12570,2438,0)
  FilletRadius = 0
  Length = 351
  MakeFace = true
  Placement = pos=(12570,2087,0) rot=(0,0,1;0rad)
  Points = (2) [(0,0,0),(0,351,0)]
  Start = (12570,2087,0)
  Subdivisions = 0
FEATURE [Part::Part2DObjectPython] Line1953  # Draft 2D object (typed FeaturePython)
  Area = 0
  ChamferSize = 0
  Closed = false
  End = (12570,3564,0)
  FilletRadius = 0
  Length = 417
  MakeFace = true
  Placement = pos=(12570,3147,0) rot=(0,0,1;0rad)
  Points = (2) [(0,0,0),(0,417,0)]
  Start = (12570,3147,0)
  Subdivisions = 0
FEATURE [Part::Part2DObjectPython] Line1954  # Draft 2D object (typed FeaturePython)
  Area = 0
  ChamferSize = 0
  Closed = false
  End = (8618,-435,0)
  FilletRadius = 0
  Length = 686
  MakeFace = true
  Placement = pos=(7932,-435,0) rot=(0,0,1;0rad)
  Points = (2) [(0,0,0),(686,-2.27374e-13,0)]
  Start = (7932,-435,0)
  Subdivisions = 0
FEATURE [Part::Part2DObjectPython] Line1955  # Draft 2D object (typed FeaturePython)
  Area = 0
  ChamferSize = 0
  Closed = false
  End = (-440,2603.5,0)
  FilletRadius = 0
  Length = 559.5
  MakeFace = true
  Placement = pos=(-440,3163,0) rot=(0,0,1;0rad)
  Points = (2) [(0,0,0),(-2.27374e-13,-559.5,0)]
  Start = (-440,3163,0)
  Subdivisions = 0
FEATURE [Part::Part2DObjectPython] Line1961  # Draft 2D object (typed FeaturePython)
  Area = 0
  ChamferSize = 0
  Closed = false
  End = (12570,5786.5,0)
  FilletRadius = 0
  Length = 559.5
  MakeFace = true
  Placement = pos=(12570,5227,0) rot=(0,0,-1;1.5708rad)
  Points = (2) [(0,0,0),(-559.5,0,0)]
  Start = (12570,5227,0)
  Subdivisions = 0
FEATURE [Part::FeaturePython] Wall451  label="раскладка вычет 004"  # Arch/BIM 166 (typed FeaturePython)
  Align = 2
  Area = 711124
  Base = -> Line1961
  BlockHeight = 310
  BlockLength = 265
  CountBroken = 8
  CountEntire = 0
  Face = 0
  Height = 1271
  HorizontalArea = 0
  IfcData = attributes={"GlobalId": {"name": "GlobalId", "type": "IfcGloballyUniqueId", "is_enum": false, "enum_values": []}, "Description": {"... (+533 chars omitted),+1 more (map truncated)
  IfcType = 166
  Joint = 10
  Length = 559.5
  MakeBlocks = true
  MoveBase = false
  MoveWithHost = false
  Normal = (0,0,0)
  OffsetFirst = 0
  OffsetSecond = 0
  PerimeterLength = 0
  Placement = pos=(-35,0,1007) rot=(0,0,1;0rad)
  PredefinedType = 0
  VerticalArea = 0
  Width = 10
FEATURE [Part::FeaturePython] Wall452  label="раскладка окна 009"  # Arch/BIM 166 (typed FeaturePython)
  Align = 2
  Area = 711124
  Base = -> Line1961
  BlockHeight = 0
  BlockLength = 0
  CountBroken = 0
  CountEntire = 0
  Face = 0
  Height = 1271
  HorizontalArea = 0
  IfcData = attributes={"GlobalId": {"name": "GlobalId", "type": "IfcGloballyUniqueId", "is_enum": false, "enum_values": []}, "Description": {"... (+533 chars omitted),+1 more (map truncated)
  IfcType = 166
  Joint = 0
  Length = 559.5
  MakeBlocks = false
  Material = -> Material011
  MoveBase = false
  MoveWithHost = false
  Normal = (0,0,0)
  OffsetFirst = 0
  OffsetSecond = 0
  PerimeterLength = 0
  Placement = pos=(-35,0,1007) rot=(0,0,1;0rad)
  PredefinedType = 0
  Subtractions = -> [Wall451]
  VerticalArea = 0
  Width = 10
FEATURE [Part::FeaturePython] Wall453  label="раскладка окна 010"  # Arch/BIM 166 (typed FeaturePython)
  Align = 2
  Area = 711124
  BlockHeight = 0
  BlockLength = 0
  CloneOf = -> Wall452
  CountBroken = 0
  CountEntire = 0
  Face = 0
  Height = 1271
  HorizontalArea = 0
  IfcData = attributes={"GlobalId": {"name": "GlobalId", "type": "IfcGloballyUniqueId", "is_enum": false, "enum_values": []}, "Description": {"... (+533 chars omitted),+1 more (map truncated)
  IfcType = 166
  Joint = 0
  Length = 559.5
  MakeBlocks = false
  Material = -> Material011
  MoveBase = false
  MoveWithHost = false
  Normal = (0,0,0)
  OffsetFirst = 0
  OffsetSecond = 0
  PerimeterLength = 0
  Placement = pos=(-35,616.394,1007.28) rot=(0,0,1;0rad)
  PredefinedType = 0
  VerticalArea = 0
  Width = 10
FEATURE [Part::FeaturePython] Wall454  label="раскладка вычет 005"  # Arch/BIM 166 (typed FeaturePython)
  Align = 2
  Area = 507072
  Base = -> Line1953
  BlockHeight = 310
  BlockLength = 199
  CountBroken = 8
  CountEntire = 0
  Face = 0
  Height = 1216
  HorizontalArea = 0
  IfcData = attributes={"GlobalId": {"name": "GlobalId", "type": "IfcGloballyUniqueId", "is_enum": false, "enum_values": []}, "Description": {"... (+533 chars omitted),+1 more (map truncated)
  IfcType = 166
  Joint = 10
  Length = 417
  MakeBlocks = true
  MoveBase = false
  MoveWithHost = false
  Normal = (0,0,0)
  OffsetFirst = 0
  OffsetSecond = 0
  PerimeterLength = 0
  Placement = pos=(-35,0,4077) rot=(0,0,1;0rad)
  PredefinedType = 0
  VerticalArea = 0
  Width = 10
FEATURE [Part::FeaturePython] Wall455  label="раскладка окна 011"  # Arch/BIM 166 (typed FeaturePython)
  Align = 2
  Area = 507072
  Base = -> Line1953
  BlockHeight = 0
  BlockLength = 0
  CountBroken = 0
  CountEntire = 0
  Face = 0
  Height = 1216
  HorizontalArea = 0
  IfcData = attributes={"GlobalId": {"name": "GlobalId", "type": "IfcGloballyUniqueId", "is_enum": false, "enum_values": []}, "Description": {"... (+533 chars omitted),+1 more (map truncated)
  IfcType = 166
  Joint = 0
  Length = 417
  MakeBlocks = false
  Material = -> Material011
  MoveBase = false
  MoveWithHost = false
  Normal = (0,0,0)
  OffsetFirst = 0
  OffsetSecond = 0
  PerimeterLength = 0
  Placement = pos=(-35,0,4077) rot=(0,0,1;0rad)
  PredefinedType = 0
  Subtractions = -> [Wall454]
  VerticalArea = 0
  Width = 10
FEATURE [Part::FeaturePython] Wall456  label="раскладка окна 012"  # Arch/BIM 166 (typed FeaturePython)
  Align = 2
  Area = 507072
  BlockHeight = 0
  BlockLength = 0
  CloneOf = -> Wall455
  CountBroken = 0
  CountEntire = 0
  Face = 0
  Height = 1216
  HorizontalArea = 0
  IfcData = attributes={"GlobalId": {"name": "GlobalId", "type": "IfcGloballyUniqueId", "is_enum": false, "enum_values": []}, "Description": {"... (+533 chars omitted),+1 more (map truncated)
  IfcType = 166
  Joint = 0
  Length = 417
  MakeBlocks = false
  Material = -> Material011
  MoveBase = false
  MoveWithHost = false
  Normal = (0,0,0)
  OffsetFirst = 0
  OffsetSecond = 0
  PerimeterLength = 0
  Placement = pos=(-35,504,4077) rot=(0,0,1;0rad)
  PredefinedType = 0
  VerticalArea = 0
  Width = 10
FEATURE [Part::FeaturePython] Wall457  label="раскладка окна 013"  # Arch/BIM 166 (typed FeaturePython)
  Align = 2
  Area = 507072
  BlockHeight = 0
  BlockLength = 0
  CloneOf = -> Wall455
  CountBroken = 0
  CountEntire = 0
  Face = 0
  Height = 1216
  HorizontalArea = 0
  IfcData = attributes={"GlobalId": {"name": "GlobalId", "type": "IfcGloballyUniqueId", "is_enum": false, "enum_values": []}, "Description": {"... (+533 chars omitted),+1 more (map truncated)
  IfcType = 166
  Joint = 0
  Length = 417
  MakeBlocks = false
  Material = -> Material011
  MoveBase = false
  MoveWithHost = false
  Normal = (0,0,0)
  OffsetFirst = 0
  OffsetSecond = 0
  PerimeterLength = 0
  Placement = pos=(-35,1155,4077) rot=(0,0,1;0rad)
  PredefinedType = 0
  VerticalArea = 0
  Width = 10
FEATURE [Part::FeaturePython] Wall458  label="раскладка окна 014"  # Arch/BIM 166 (typed FeaturePython)
  Align = 2
  Area = 507072
  BlockHeight = 0
  BlockLength = 0
  CloneOf = -> Wall455
  CountBroken = 0
  CountEntire = 0
  Face = 0
  Height = 1216
  HorizontalArea = 0
  IfcData = attributes={"GlobalId": {"name": "GlobalId", "type": "IfcGloballyUniqueId", "is_enum": false, "enum_values": []}, "Description": {"... (+533 chars omitted),+1 more (map truncated)
  IfcType = 166
  Joint = 0
  Length = 417
  MakeBlocks = false
  Material = -> Material011
  MoveBase = false
  MoveWithHost = false
  Normal = (0,0,0)
  OffsetFirst = 0
  OffsetSecond = 0
  PerimeterLength = 0
  Placement = pos=(-35,1659,4077) rot=(0,0,1;0rad)
  PredefinedType = 0
  VerticalArea = 0
  Width = 10
FEATURE [Part::Part2DObjectPython] Line1963  # Draft 2D object (typed FeaturePython)
  Area = 0
  ChamferSize = 0
  Closed = false
  End = (-440,4806,0)
  FilletRadius = 0
  Length = 417
  MakeFace = true
  Placement = pos=(-440,5223,0) rot=(0,0,1;0rad)
  Points = (2) [(0,0,0),(-5.68434e-14,-417,0)]
  Start = (-440,5223,0)
  Subdivisions = 0
FEATURE [Part::FeaturePython] Wall460  label="раскладка вычет 006"  # Arch/BIM 166 (typed FeaturePython)
  Align = 2
  Area = 507072
  Base = -> Line1963
  BlockHeight = 310
  BlockLength = 199
  CountBroken = 8
  CountEntire = 0
  Face = 0
  Height = 1216
  HorizontalArea = 0
  IfcData = attributes={"GlobalId": {"name": "GlobalId", "type": "IfcGloballyUniqueId", "is_enum": false, "enum_values": []}, "Description": {"... (+533 chars omitted),+1 more (map truncated)
  IfcType = 166
  Joint = 10
  Length = 417
  MakeBlocks = true
  MoveBase = false
  MoveWithHost = false
  Normal = (0,0,0)
  OffsetFirst = 0
  OffsetSecond = 0
  PerimeterLength = 0
  Placement = pos=(35,0,4077) rot=(0,0,1;0rad)
  PredefinedType = 0
  VerticalArea = 0
  Width = 10
FEATURE [Part::FeaturePython] Wall459  label="раскладка окна 015"  # Arch/BIM 166 (typed FeaturePython)
  Align = 2
  Area = 507072
  Base = -> Line1963
  BlockHeight = 0
  BlockLength = 0
  CountBroken = 0
  CountEntire = 0
  Face = 0
  Height = 1216
  HorizontalArea = 0
  IfcData = attributes={"GlobalId": {"name": "GlobalId", "type": "IfcGloballyUniqueId", "is_enum": false, "enum_values": []}, "Description": {"... (+533 chars omitted),+1 more (map truncated)
  IfcType = 166
  Joint = 0
  Length = 417
  MakeBlocks = false
  Material = -> Material011
  MoveBase = false
  MoveWithHost = false
  Normal = (0,0,0)
  OffsetFirst = 0
  OffsetSecond = 0
  PerimeterLength = 0
  Placement = pos=(35,0,4077) rot=(0,0,1;0rad)
  PredefinedType = 0
  Subtractions = -> [Wall460]
  VerticalArea = 0
  Width = 10
FEATURE [Part::FeaturePython] Wall461  label="раскладка окна 016"  # Arch/BIM 166 (typed FeaturePython)
  Align = 2
  Area = 507072
  BlockHeight = 0
  BlockLength = 0
  CloneOf = -> Wall459
  CountBroken = 0
  CountEntire = 0
  Face = 0
  Height = 1216
  HorizontalArea = 0
  IfcData = attributes={"GlobalId": {"name": "GlobalId", "type": "IfcGloballyUniqueId", "is_enum": false, "enum_values": []}, "Description": {"... (+533 chars omitted),+1 more (map truncated)
  IfcType = 166
  Joint = 0
  Length = 417
  MakeBlocks = false
  Material = -> Material011
  MoveBase = false
  MoveWithHost = false
  Normal = (0,0,0)
  OffsetFirst = 0
  OffsetSecond = 0
  PerimeterLength = 0
  Placement = pos=(35,-504,4077) rot=(0,0,1;0rad)
  PredefinedType = 0
  VerticalArea = 0
  Width = 10
FEATURE [Part::FeaturePython] Wall462  label="раскладка окна 017"  # Arch/BIM 166 (typed FeaturePython)
  Align = 2
  Area = 507072
  BlockHeight = 0
  BlockLength = 0
  CloneOf = -> Wall459
  CountBroken = 0
  CountEntire = 0
  Face = 0
  Height = 1216
  HorizontalArea = 0
  IfcData = attributes={"GlobalId": {"name": "GlobalId", "type": "IfcGloballyUniqueId", "is_enum": false, "enum_values": []}, "Description": {"... (+533 chars omitted),+1 more (map truncated)
  IfcType = 166
  Joint = 0
  Length = 417
  MakeBlocks = false
  Material = -> Material011
  MoveBase = false
  MoveWithHost = false
  Normal = (0,0,0)
  OffsetFirst = 0
  OffsetSecond = 0
  PerimeterLength = 0
  Placement = pos=(35,-1155,4077) rot=(0,0,1;0rad)
  PredefinedType = 0
  VerticalArea = 0
  Width = 10
FEATURE [Part::FeaturePython] Wall463  label="раскладка окна 018"  # Arch/BIM 166 (typed FeaturePython)
  Align = 2
  Area = 507072
  BlockHeight = 0
  BlockLength = 0
  CloneOf = -> Wall459
  CountBroken = 0
  CountEntire = 0
  Face = 0
  Height = 1216
  HorizontalArea = 0
  IfcData = attributes={"GlobalId": {"name": "GlobalId", "type": "IfcGloballyUniqueId", "is_enum": false, "enum_values": []}, "Description": {"... (+533 chars omitted),+1 more (map truncated)
  IfcType = 166
  Joint = 0
  Length = 417
  MakeBlocks = false
  Material = -> Material011
  MoveBase = false
  MoveWithHost = false
  Normal = (0,0,0)
  OffsetFirst = 0
  OffsetSecond = 0
  PerimeterLength = 0
  Placement = pos=(35,-1659,4077) rot=(0,0,1;0rad)
  PredefinedType = 0
  VerticalArea = 0
  Width = 10
FEATURE [Part::FeaturePython] Wall464  label="раскладка вычет 007"  # Arch/BIM 166 (typed FeaturePython)
  Align = 2
  Area = 711124
  Base = -> Line1955
  BlockHeight = 310
  BlockLength = 265
  CountBroken = 8
  CountEntire = 0
  Face = 0
  Height = 1271
  HorizontalArea = 0
  IfcData = attributes={"GlobalId": {"name": "GlobalId", "type": "IfcGloballyUniqueId", "is_enum": false, "enum_values": []}, "Description": {"... (+533 chars omitted),+1 more (map truncated)
  IfcType = 166
  Joint = 10
  Length = 559.5
  MakeBlocks = true
  MoveBase = false
  MoveWithHost = false
  Normal = (0,0,0)
  OffsetFirst = 0
  OffsetSecond = 0
  PerimeterLength = 0
  Placement = pos=(35,-9.91129,1007) rot=(0,0,1;0rad)
  PredefinedType = 0
  VerticalArea = 0
  Width = 10
FEATURE [Part::FeaturePython] Wall465  label="раскладка окна 019"  # Arch/BIM 166 (typed FeaturePython)
  Align = 2
  Area = 711124
  Base = -> Line1955
  BlockHeight = 0
  BlockLength = 0
  CountBroken = 0
  CountEntire = 0
  Face = 0
  Height = 1271
  HorizontalArea = 0
  IfcData = attributes={"GlobalId": {"name": "GlobalId", "type": "IfcGloballyUniqueId", "is_enum": false, "enum_values": []}, "Description": {"... (+533 chars omitted),+1 more (map truncated)
  IfcType = 166
  Joint = 0
  Length = 559.5
  MakeBlocks = false
  Material = -> Material011
  MoveBase = false
  MoveWithHost = false
  Normal = (0,0,0)
  OffsetFirst = 0
  OffsetSecond = 0
  PerimeterLength = 0
  Placement = pos=(35,-9.91129,1007) rot=(0,0,1;0rad)
  PredefinedType = 0
  Subtractions = -> [Wall464]
  VerticalArea = 0
  Width = 10
FEATURE [Part::FeaturePython] Wall466  label="раскладка окна 020"  # Arch/BIM 166 (typed FeaturePython)
  Align = 2
  Area = 711124
  BlockHeight = 0
  BlockLength = 0
  CloneOf = -> Wall465
  CountBroken = 0
  CountEntire = 0
  Face = 0
  Height = 1271
  HorizontalArea = 0
  IfcData = attributes={"GlobalId": {"name": "GlobalId", "type": "IfcGloballyUniqueId", "is_enum": false, "enum_values": []}, "Description": {"... (+533 chars omitted),+1 more (map truncated)
  IfcType = 166
  Joint = 0
  Length = 559.5
  MakeBlocks = false
  Material = -> Material011
  MoveBase = false
  MoveWithHost = false
  Normal = (0,0,0)
  OffsetFirst = 0
  OffsetSecond = 0
  PerimeterLength = 0
  Placement = pos=(35,-646.5,1007) rot=(0,0,1;0rad)
  PredefinedType = 0
  VerticalArea = 0
  Width = 10
FEATURE [Part::FeaturePython] Wall467  label="раскладка вычет 008"  # Arch/BIM 166 (typed FeaturePython)
  Align = 2
  Area = 786591
  Base = -> Line1952
  BlockHeight = 310
  BlockLength = 0
  CountBroken = 0
  CountEntire = 0
  Face = 0
  Height = 2241
  HorizontalArea = 0
  IfcData = attributes={"GlobalId": {"name": "GlobalId", "type": "IfcGloballyUniqueId", "is_enum": false, "enum_values": []}, "Description": {"... (+533 chars omitted),+1 more (map truncated)
  IfcType = 166
  Joint = 10
  Length = 351
  MakeBlocks = true
  MoveBase = false
  MoveWithHost = false
  Normal = (0,0,0)
  OffsetFirst = 0
  OffsetSecond = 0
  PerimeterLength = 0
  Placement = pos=(-35,0,77) rot=(0,0,1;0rad)
  PredefinedType = 0
  VerticalArea = 0
  Width = 10
FEATURE [Part::FeaturePython] Wall468  label="раскладка окна 021"  # Arch/BIM 166 (typed FeaturePython)
  Align = 2
  Area = 786591
  Base = -> Line1952
  BlockHeight = 0
  BlockLength = 0
  CountBroken = 0
  CountEntire = 0
  Face = 0
  Height = 2241
  HorizontalArea = 0
  IfcData = attributes={"GlobalId": {"name": "GlobalId", "type": "IfcGloballyUniqueId", "is_enum": false, "enum_values": []}, "Description": {"... (+533 chars omitted),+1 more (map truncated)
  IfcType = 166
  Joint = 0
  Length = 351
  MakeBlocks = false
  Material = -> Material011
  MoveBase = false
  MoveWithHost = false
  Normal = (0,0,0)
  OffsetFirst = 0
  OffsetSecond = 0
  PerimeterLength = 0
  Placement = pos=(-35,0,77) rot=(0,0,1;0rad)
  PredefinedType = 0
  Subtractions = -> [Wall467]
  VerticalArea = 0
  Width = 10
FEATURE [Part::FeaturePython] Wall469  label="раскладка вычет 009"  # Arch/BIM 166 (typed FeaturePython)
  Align = 2
  Area = 943936
  Base = -> Line1954
  BlockHeight = 270
  BlockLength = 335
  CountBroken = 10
  CountEntire = 0
  Face = 0
  Height = 1376
  HorizontalArea = 0
  IfcData = attributes={"GlobalId": {"name": "GlobalId", "type": "IfcGloballyUniqueId", "is_enum": false, "enum_values": []}, "Description": {"... (+533 chars omitted),+1 more (map truncated)
  IfcType = 166
  Joint = 10
  Length = 686
  MakeBlocks = true
  MoveBase = false
  MoveWithHost = false
  Normal = (0,0,0)
  OffsetFirst = 0
  OffsetSecond = 0
  PerimeterLength = 0
  Placement = pos=(0,35,1077) rot=(0,0,1;0rad)
  PredefinedType = 0
  VerticalArea = 0
  Width = 10
FEATURE [Part::FeaturePython] Wall470  label="раскладка окна 022"  # Arch/BIM 166 (typed FeaturePython)
  Align = 2
  Area = 943936
  Base = -> Line1954
  BlockHeight = 0
  BlockLength = 0
  CountBroken = 0
  CountEntire = 0
  Face = 0
  Height = 1376
  HorizontalArea = 0
  IfcData = attributes={"GlobalId": {"name": "GlobalId", "type": "IfcGloballyUniqueId", "is_enum": false, "enum_values": []}, "Description": {"... (+533 chars omitted),+1 more (map truncated)
  IfcType = 166
  Joint = 0
  Length = 686
  MakeBlocks = false
  Material = -> Material011
  MoveBase = false
  MoveWithHost = false
  Normal = (0,0,0)
  OffsetFirst = 0
  OffsetSecond = 0
  PerimeterLength = 0
  Placement = pos=(0,35,1077) rot=(0,0,1;0rad)
  PredefinedType = 0
  Subtractions = -> [Wall469]
  VerticalArea = 0
  Width = 10
FEATURE [Part::FeaturePython] Wall471  label="раскладка окна 023"  # Arch/BIM 166 (typed FeaturePython)
  Align = 2
  Area = 943936
  BlockHeight = 0
  BlockLength = 0
  CloneOf = -> Wall470
  CountBroken = 0
  CountEntire = 0
  Face = 0
  Height = 1376
  HorizontalArea = 0
  IfcData = attributes={"GlobalId": {"name": "GlobalId", "type": "IfcGloballyUniqueId", "is_enum": false, "enum_values": []}, "Description": {"... (+533 chars omitted),+1 more (map truncated)
  IfcType = 166
  Joint = 0
  Length = 686
  MakeBlocks = false
  Material = -> Material011
  MoveBase = false
  MoveWithHost = false
  Normal = (0,0,0)
  OffsetFirst = 0
  OffsetSecond = 0
  PerimeterLength = 0
  Placement = pos=(-3642.29,35,1099.86) rot=(0,0,1;0rad)
  PredefinedType = 0
  VerticalArea = 0
  Width = 10
FEATURE [Part::Part2DObjectPython] Line1966  # Draft 2D object (typed FeaturePython)
  Area = 0
  ChamferSize = 0
  Closed = false
  End = (6736,-535,0)
  FilletRadius = 0
  Length = 562
  MakeFace = true
  Placement = pos=(6174,-535,0) rot=(0,0,1;0rad)
  Points = (2) [(0,0,0),(562,1.13687e-13,0)]
  Start = (6174,-535,0)
  Subdivisions = 0
FEATURE [Part::FeaturePython] Wall472  label="раскладка вычет 010"  # Arch/BIM 166 (typed FeaturePython)
  Align = 2
  Area = 450724
  Base = -> Line1966
  BlockHeight = 260
  BlockLength = 270
  CountBroken = 6
  CountEntire = 0
  Face = 0
  Height = 802
  HorizontalArea = 0
  IfcData = attributes={"GlobalId": {"name": "GlobalId", "type": "IfcGloballyUniqueId", "is_enum": false, "enum_values": []}, "Description": {"... (+533 chars omitted),+1 more (map truncated)
  IfcType = 166
  Joint = 10
  Length = 562
  MakeBlocks = true
  MoveBase = false
  MoveWithHost = false
  Normal = (0,0,0)
  OffsetFirst = 0
  OffsetSecond = 0
  PerimeterLength = 0
  Placement = pos=(0,27,1114) rot=(0,0,1;0rad)
  PredefinedType = 0
  VerticalArea = 0
  Width = 10
FEATURE [Part::FeaturePython] Wall473  label="раскладка окна 024"  # Arch/BIM 166 (typed FeaturePython)
  Align = 2
  Area = 450724
  Base = -> Line1966
  BlockHeight = 0
  BlockLength = 0
  CountBroken = 0
  CountEntire = 0
  Face = 0
  Height = 802
  HorizontalArea = 0
  IfcData = attributes={"GlobalId": {"name": "GlobalId", "type": "IfcGloballyUniqueId", "is_enum": false, "enum_values": []}, "Description": {"... (+533 chars omitted),+1 more (map truncated)
  IfcType = 166
  Joint = 0
  Length = 562
  MakeBlocks = false
  Material = -> Material011
  MoveBase = false
  MoveWithHost = false
  Normal = (0,0,0)
  OffsetFirst = 0
  OffsetSecond = 0
  PerimeterLength = 0
  Placement = pos=(0,27,1114) rot=(0,0,1;0rad)
  PredefinedType = 0
  Subtractions = -> [Wall472]
  VerticalArea = 0
  Width = 10
FEATURE [Part::Part2DObjectPython] Line1967  # Draft 2D object (typed FeaturePython)
  Area = 0
  ChamferSize = 0
  Closed = false
  End = (12570,3213,0)
  FilletRadius = 0
  Length = 431
  MakeFace = true
  Placement = pos=(12570,2782,0) rot=(0,0,1;0rad)
  Points = (2) [(0,0,0),(0,431,0)]
  Start = (12570,2782,0)
  Subdivisions = 0
FEATURE [Part::FeaturePython] Wall475  label="раскладка вычет 011"  # Arch/BIM 166 (typed FeaturePython)
  Align = 2
  Area = 441775
  Base = -> Line1967
  BlockHeight = 250
  BlockLength = 210
  CountBroken = 8
  CountEntire = 0
  Face = 0
  Height = 1025
  HorizontalArea = 0
  IfcData = attributes={"GlobalId": {"name": "GlobalId", "type": "IfcGloballyUniqueId", "is_enum": false, "enum_values": []}, "Description": {"... (+533 chars omitted),+1 more (map truncated)
  IfcType = 166
  Joint = 10
  Length = 431
  MakeBlocks = true
  MoveBase = false
  MoveWithHost = false
  Normal = (0,0,0)
  OffsetFirst = 0
  OffsetSecond = 0
  PerimeterLength = 0
  Placement = pos=(-35,0,1187) rot=(0,0,1;0rad)
  PredefinedType = 0
  VerticalArea = 0
  Width = 10
FEATURE [Part::FeaturePython] Wall474  label="раскладка окна 025"  # Arch/BIM 166 (typed FeaturePython)
  Align = 2
  Area = 441775
  Base = -> Line1967
  BlockHeight = 0
  BlockLength = 0
  CountBroken = 0
  CountEntire = 0
  Face = 0
  Height = 1025
  HorizontalArea = 0
  IfcData = attributes={"GlobalId": {"name": "GlobalId", "type": "IfcGloballyUniqueId", "is_enum": false, "enum_values": []}, "Description": {"... (+533 chars omitted),+1 more (map truncated)
  IfcType = 166
  Joint = 0
  Length = 431
  MakeBlocks = false
  Material = -> Material011
  MoveBase = false
  MoveWithHost = false
  Normal = (0,0,0)
  OffsetFirst = 0
  OffsetSecond = 0
  PerimeterLength = 0
  Placement = pos=(-35,0,1187) rot=(0,0,1;0rad)
  PredefinedType = 0
  Subtractions = -> [Wall475]
  VerticalArea = 0
  Width = 10
FEATURE [Part::FeaturePython] Component223  label="Снегозадержатели 017"  # Arch/BIM 0 (typed FeaturePython)
  Base = -> Pipe014
  HorizontalArea = 0
  IfcData = attributes={"GlobalId": {"name": "GlobalId", "type": "IfcGloballyUniqueId", "is_enum": false, "enum_values": []}, "Description": {"... (+538 chars omitted),+1 more (map truncated)
  IfcType = 0
  Material = -> Material007
  MoveBase = false
  MoveWithHost = false
  PerimeterLength = 0
  Placement = pos=(0,0,50) rot=(0,0,1;0rad)
  PredefinedType = 0
  VerticalArea = 0
FEATURE [Part::FeaturePython] Component224  label="Снегозадержатели 018"  # Arch/BIM 0 (typed FeaturePython)
  Base = -> Pipe015
  HorizontalArea = 0
  IfcData = attributes={"GlobalId": {"name": "GlobalId", "type": "IfcGloballyUniqueId", "is_enum": false, "enum_values": []}, "Description": {"... (+538 chars omitted),+1 more (map truncated)
  IfcType = 0
  Material = -> Material007
  MoveBase = false
  MoveWithHost = false
  PerimeterLength = 0
  Placement = pos=(0,0,50) rot=(0,0,1;0rad)
  PredefinedType = 0
  VerticalArea = 0
FEATURE [Part::FeaturePython] Component225  label="Снегозадержатели 019"  # Arch/BIM 0 (typed FeaturePython)
  Base = -> Pipe016
  HorizontalArea = 0
  IfcData = attributes={"GlobalId": {"name": "GlobalId", "type": "IfcGloballyUniqueId", "is_enum": false, "enum_values": []}, "Description": {"... (+538 chars omitted),+1 more (map truncated)
  IfcType = 0
  Material = -> Material007
  MoveBase = false
  MoveWithHost = false
  PerimeterLength = 0
  Placement = pos=(0,0,50) rot=(0,0,1;0rad)
  PredefinedType = 0
  VerticalArea = 0
FEATURE [Part::FeaturePython] Component226  label="Снегозадержатели 020"  # Arch/BIM 0 (typed FeaturePython)
  Base = -> Pipe017
  HorizontalArea = 0
  IfcData = attributes={"GlobalId": {"name": "GlobalId", "type": "IfcGloballyUniqueId", "is_enum": false, "enum_values": []}, "Description": {"... (+538 chars omitted),+1 more (map truncated)
  IfcType = 0
  Material = -> Material007
  MoveBase = false
  MoveWithHost = false
  PerimeterLength = 0
  Placement = pos=(0,0,50) rot=(0,0,1;0rad)
  PredefinedType = 0
  VerticalArea = 0
FEATURE [Part::FeaturePython] Component227  label="Снегозадержатели 021"  # Arch/BIM 0 (typed FeaturePython)
  Base = -> Pipe018
  HorizontalArea = 0
  IfcData = attributes={"GlobalId": {"name": "GlobalId", "type": "IfcGloballyUniqueId", "is_enum": false, "enum_values": []}, "Description": {"... (+538 chars omitted),+1 more (map truncated)
  IfcType = 0
  Material = -> Material007
  MoveBase = false
  MoveWithHost = false
  PerimeterLength = 0
  Placement = pos=(0,0,50) rot=(0,0,1;0rad)
  PredefinedType = 0
  VerticalArea = 0
FEATURE [Part::FeaturePython] Component228  label="Снегозадержатели 022"  # Arch/BIM 0 (typed FeaturePython)
  Base = -> Pipe019
  HorizontalArea = 0
  IfcData = attributes={"GlobalId": {"name": "GlobalId", "type": "IfcGloballyUniqueId", "is_enum": false, "enum_values": []}, "Description": {"... (+538 chars omitted),+1 more (map truncated)
  IfcType = 0
  Material = -> Material007
  MoveBase = false
  MoveWithHost = false
  PerimeterLength = 0
  Placement = pos=(0,0,50) rot=(0,0,1;0rad)
  PredefinedType = 0
  VerticalArea = 0
FEATURE [Part::FeaturePython] Component229  label="Снегозадержатели 023"  # Arch/BIM 0 (typed FeaturePython)
  Base = -> Pipe020
  HorizontalArea = 0
  IfcData = attributes={"GlobalId": {"name": "GlobalId", "type": "IfcGloballyUniqueId", "is_enum": false, "enum_values": []}, "Description": {"... (+538 chars omitted),+1 more (map truncated)
  IfcType = 0
  Material = -> Material007
  MoveBase = false
  MoveWithHost = false
  PerimeterLength = 0
  Placement = pos=(0,0,50) rot=(0,0,1;0rad)
  PredefinedType = 0
  VerticalArea = 0
FEATURE [Part::FeaturePython] Component230  label="Снегозадержатели 024"  # Arch/BIM 0 (typed FeaturePython)
  Base = -> Pipe021
  HorizontalArea = 0
  IfcData = attributes={"GlobalId": {"name": "GlobalId", "type": "IfcGloballyUniqueId", "is_enum": false, "enum_values": []}, "Description": {"... (+538 chars omitted),+1 more (map truncated)
  IfcType = 0
  Material = -> Material007
  MoveBase = false
  MoveWithHost = false
  PerimeterLength = 0
  Placement = pos=(0,0,50) rot=(0,0,1;0rad)
  PredefinedType = 0
  VerticalArea = 0
FEATURE [App::GeometryPython] BuildingPart084  label="Снегозадержатели"  # Arch/BIM 52 (typed FeaturePython)
  Area = 0
  GlobalId = 10iOlZVPHFee_$fCiLahbp
  Group = -> [Component223,Component224,Component225,Component226,Component227,Component228,Component229,Component230]
  Height = 0
  HeightPropagate = true
  IfcData = IfcUID=10iOlZVPHFee_$fCiLahbp,+2 more (map truncated)
  IfcType = 52
  LevelOffset = 0
FEATURE [Part::FeaturePython] Structure574  label="облицовка камина 001"  # Arch/BIM 172 (typed FeaturePython)
  FaceMaker = 0
  Height = 2580
  HorizontalArea = 473100
  IfcData = attributes={"GlobalId": {"name": "GlobalId", "type": "IfcGloballyUniqueId", "is_enum": false, "enum_values": []}, "Description": {"... (+484 chars omitted),+1 more (map truncated)
  IfcType = 172
  Length = 0
  MoveBase = false
  MoveWithHost = false
  Nodes = (2) [(7620,2940,0),(7620,2940,2580)]
  NodesOffset = 0
  Normal = (0,0,0)
  PerimeterLength = 2800
  PredefinedType = 0
  VerticalArea = 7224000
  Width = 100
FEATURE [Part::Cut] Cut084
  Base = -> Structure574
  Tool = -> Box3211
FEATURE [Part::Cut] Cut085
  Base = -> Cut084
  Tool = -> Box3228
FEATURE [Part::FeaturePython] Component240  label="облицовка камина 01"  # Arch/BIM 0 (typed FeaturePython)
  Base = -> Cut085
  HorizontalArea = 0
  IfcData = attributes={"GlobalId": {"name": "GlobalId", "type": "IfcGloballyUniqueId", "is_enum": false, "enum_values": []}, "Description": {"... (+538 chars omitted),+1 more (map truncated)
  IfcType = 0
  MoveBase = false
  MoveWithHost = false
  PerimeterLength = 0
  PredefinedType = 0
  VerticalArea = 0
FEATURE [Part::FeaturePython] Structure575  label="Основание дымохода +300мм"  # Arch/BIM 172 (typed FeaturePython)
  FaceMaker = 0
  Height = 300
  HorizontalArea = 561600
  IfcData = attributes={"GlobalId": {"name": "GlobalId", "type": "IfcGloballyUniqueId", "is_enum": false, "enum_values": []}, "Description": {"... (+484 chars omitted),+1 more (map truncated)
  IfcType = 172
  Length = 0
  Material = -> Material007
  MoveBase = false
  MoveWithHost = false
  Nodes = (2) [(7235,1875,0),(7235,1875,300)]
  NodesOffset = 0
  Normal = (0,0,0)
  PerimeterLength = 3840
  PredefinedType = 0
  VerticalArea = 1.152e+06
  Width = 100
FEATURE [Part::Part2DObjectPython] Line1974  # Draft 2D object (typed FeaturePython)
  Area = 0
  ChamferSize = 0
  Closed = true
  End = (6893,-535,0)
  FilletRadius = 0
  Length = 876
  MakeFace = true
  Placement = pos=(6047,-535,0) rot=(0,0,1;0rad)
  Points = (2) [(-30,5.68434e-13,0),(846,5.68434e-13,0)]
  Start = (6017,-535,0)
  Subdivisions = 0
FEATURE [Part::FeaturePython] Wall483  label="раскладка вычет 012"  # Arch/BIM 166 (typed FeaturePython)
  Align = 2
  Area = 199728
  Base = -> Line1974
  BlockHeight = 260
  BlockLength = 285
  CountBroken = 3
  CountEntire = 0
  Face = 0
  Height = 228
  HorizontalArea = 8560
  IfcData = attributes={"GlobalId": {"name": "GlobalId", "type": "IfcGloballyUniqueId", "is_enum": false, "enum_values": []}, "Description": {"... (+533 chars omitted),+1 more (map truncated)
  IfcType = 166
  Joint = 10
  Length = 876
  MakeBlocks = true
  MoveBase = false
  MoveWithHost = false
  Normal = (0,0,0)
  OffsetFirst = 0
  OffsetSecond = 0
  PerimeterLength = 0
  Placement = pos=(0,35,2197) rot=(0,0,1;0rad)
  PredefinedType = 0
  VerticalArea = 404016
  Width = 10
FEATURE [Part::FeaturePython] Wall484  label="раскладка окна 026"  # Arch/BIM 166 (typed FeaturePython)
  Align = 2
  Area = 199728
  Base = -> Line1974
  BlockHeight = 0
  BlockLength = 0
  CountBroken = 0
  CountEntire = 0
  Face = 0
  Height = 228
  HorizontalArea = 200
  IfcData = attributes={"GlobalId": {"name": "GlobalId", "type": "IfcGloballyUniqueId", "is_enum": false, "enum_values": []}, "Description": {"... (+533 chars omitted),+1 more (map truncated)
  IfcType = 166
  Joint = 0
  Length = 876
  MakeBlocks = false
  Material = -> Material011
  MoveBase = false
  MoveWithHost = false
  Normal = (0,0,0)
  OffsetFirst = 0
  OffsetSecond = 0
  PerimeterLength = 1832
  Placement = pos=(0,35,2197) rot=(0,0,1;0rad)
  PredefinedType = 0
  Subtractions = -> [Wall483]
  VerticalArea = 18240
  Width = 10
FEATURE [Sketcher::SketchObject] Sketch406
  FullyConstrained = true
  Placement = pos=(6450,-175,4350) rot=(0,0.707107,0.707107;3.14159rad)
  sketch-geometry (32):
    g0: LineSegment StartX=0 StartY=0 StartZ=0 EndX=2350 EndY=0 EndZ=0
    g1: LineSegment StartX=2350 StartY=0 StartZ=0 EndX=2350 EndY=950 EndZ=0
    g2: LineSegment StartX=2350 StartY=950 StartZ=0 EndX=0 EndY=950 EndZ=0
    g3: LineSegment StartX=0 StartY=950 StartZ=0 EndX=0 EndY=0 EndZ=0
    g4: LineSegment StartX=70 StartY=70 StartZ=0 EndX=2280 EndY=70 EndZ=0
    g5: LineSegment StartX=2280 StartY=70 StartZ=0 EndX=2280 EndY=880 EndZ=0
    g6: LineSegment StartX=2280 StartY=880 StartZ=0 EndX=70 EndY=880 EndZ=0
    g7: LineSegment StartX=70 StartY=880 StartZ=0 EndX=70 EndY=70 EndZ=0
    g8: LineSegment StartX=77 StartY=77 StartZ=0 EndX=804.333 EndY=77 EndZ=0
    g9: LineSegment StartX=804.333 StartY=77 StartZ=0 EndX=804.333 EndY=873 EndZ=0
    g10: LineSegment StartX=804.333 StartY=873 StartZ=0 EndX=77 EndY=873 EndZ=0
    g11: LineSegment StartX=77 StartY=873 StartZ=0 EndX=77 EndY=77 EndZ=0
    g12: LineSegment StartX=117 StartY=117 StartZ=0 EndX=764.333 EndY=117 EndZ=0
    g13: LineSegment StartX=764.333 StartY=117 StartZ=0 EndX=764.333 EndY=833 EndZ=0
    g14: LineSegment StartX=764.333 StartY=833 StartZ=0 EndX=117 EndY=833 EndZ=0
    g15: LineSegment StartX=117 StartY=833 StartZ=0 EndX=117 EndY=117 EndZ=0
    g16: LineSegment StartX=1545.67 StartY=77 StartZ=0 EndX=2273 EndY=77 EndZ=0
    g17: LineSegment StartX=2273 StartY=77 StartZ=0 EndX=2273 EndY=873 EndZ=0
    g18: LineSegment StartX=2273 StartY=873 StartZ=0 EndX=1545.67 EndY=873 EndZ=0
    g19: LineSegment StartX=1545.67 StartY=873 StartZ=0 EndX=1545.67 EndY=77 EndZ=0
    g20: LineSegment StartX=1585.67 StartY=117 StartZ=0 EndX=2233 EndY=117 EndZ=0
    g21: LineSegment StartX=2233 StartY=117 StartZ=0 EndX=2233 EndY=833 EndZ=0
    g22: LineSegment StartX=2233 StartY=833 StartZ=0 EndX=1585.67 EndY=833 EndZ=0
    g23: LineSegment StartX=1585.67 StartY=833 StartZ=0 EndX=1585.67 EndY=117 EndZ=0
    g24: LineSegment StartX=1538.67 StartY=873 StartZ=0 EndX=811.333 EndY=873 EndZ=0
    g25: LineSegment StartX=811.333 StartY=873 StartZ=0 EndX=811.333 EndY=77 EndZ=0
    g26: LineSegment StartX=1498.67 StartY=833 StartZ=0 EndX=851.333 EndY=833 EndZ=0
    g27: LineSegment StartX=851.333 StartY=833 StartZ=0 EndX=851.333 EndY=117 EndZ=0
    g28: LineSegment StartX=851.333 StartY=117 StartZ=0 EndX=1498.67 EndY=117 EndZ=0
    g29: LineSegment StartX=811.333 StartY=77 StartZ=0 EndX=1538.67 EndY=77 EndZ=0
    g30: LineSegment StartX=1498.67 StartY=117 StartZ=0 EndX=1498.67 EndY=833 EndZ=0
    g31: LineSegment StartX=1538.67 StartY=77 StartZ=0 EndX=1538.67 EndY=873 EndZ=0
  constraints (95):
    c: Coincident(g0,g1)
    c: Coincident(g1,g2)
    c: Coincident(g2,g3)
    c: Coincident(g3,g0)
    c: Horizontal(g0)
    c: Horizontal(g2)
    c: Vertical(g1)
    c: Vertical(g3)
    c: Coincident(g4,g5)
    c: Coincident(g5,g6)
    c: Coincident(g6,g7)
    c: Coincident(g7,g4)
    c: Horizontal(g4)
    c: Horizontal(g6)
    c: Vertical(g5)
    c: Vertical(g7)
    c: DistanceY(g1) = 950  'Height'
    c: DistanceX(g0) = 2350  'Width'
    c: DistanceY(g6,g2) = 70  'Frame1'
    c: DistanceX(g2,g6) = 70  'Frame2'
    c: DistanceX(g4,g0) = 70  'Frame3'
    c: DistanceY(g0,g4) = 70  'Frame4'
    c: Coincident(g0,g-1)
    c: Coincident(g8,g9)
    c: Coincident(g9,g10)
    c: Coincident(g10,g11)
    c: Coincident(g11,g8)
    c: Horizontal(g8)
    c: Horizontal(g10)
    c: Vertical(g9)
    c: Vertical(g11)
    c: Coincident(g12,g13)
    c: Coincident(g13,g14)
    c: Coincident(g14,g15)
    c: Coincident(g15,g12)
    c: Horizontal(g12)
    c: Horizontal(g14)
    c: Vertical(g13)
    c: Vertical(g15)
    c: Coincident(g16,g17)
    c: Coincident(g17,g18)
    c: Coincident(g18,g19)
    c: Coincident(g19,g16)
    c: Horizontal(g16)
    c: Horizontal(g18)
    c: Vertical(g17)
    c: Vertical(g19)
    c: Coincident(g20,g21)
    c: Coincident(g21,g22)
    c: Coincident(g22,g23)
    c: Coincident(g23,g20)
    c: Horizontal(g20)
    c: Horizontal(g22)
    c: Vertical(g21)
    c: Vertical(g23)
    c: DistanceY(g8,g12) = 40
    c: DistanceX(g8,g12) = 40
    c: DistanceX(g21,g17) = 40
    c: DistanceY(g21,g17) = 40
    c: DistanceX(g16,g20) = 40
    c: DistanceX(g14,g10) = 40
    c: DistanceY(g8,g16) = 0
    c: DistanceY(g10,g18) = 0
    c: DistanceX(g4,g8) = 7
    c: DistanceY(g4,g8) = 7
    c: DistanceX(g6,g18) = -7
    c: DistanceY(g6,g18) = -7
    c: PointOnObject(g13,g22)
    c: PointOnObject(g20,g12)
    c: Coincident(g29,g31)
    c: Coincident(g31,g24)
    c: Coincident(g24,g25)
    c: Coincident(g25,g29)
    c: Horizontal(g29)
    c: Horizontal(g24)
    c: Vertical(g31)
    c: Vertical(g25)
    c: Coincident(g28,g30)
    c: Coincident(g30,g26)
    c: Coincident(g26,g27)
    c: Coincident(g27,g28)
    c: Horizontal(g28)
    c: Horizontal(g26)
    c: Vertical(g30)
    c: Vertical(g27)
    c: DistanceY(g29,g28) = 40
    c: DistanceX(g29,g28) = 40
    c: DistanceX(g26,g24) = 40
    c: DistanceY(g24,g9) = 0
    c: DistanceY(g26,g24) = 40
    c: DistanceY(g8,g25) = 0
    c: DistanceX(g8,g25) = 7
    c: DistanceX(g29,g16) = 7
    c: Equal(g14,g26)
    c: Equal(g26,g22)
FEATURE [Part::FeaturePython] Window100  label="ОК-10_1-001"  # Arch/BIM 170 (typed FeaturePython)
  Area = 2232500
  Base = -> Sketch406
  Frame = 70
  Height = 950
  HoleDepth = 0
  HoleWire = 0
  HorizontalArea = 0
  IfcData = attributes={"GlobalId": {"name": "GlobalId", "type": "IfcGloballyUniqueId", "is_enum": false, "enum_values": []}, "Description": {"... (+1230 chars omitted),+1 more (map truncated)
  IfcType = 170
  LouvreSpacing = 0
  LouvreWidth = 0
  Material = -> Material011
  MoveBase = false
  MoveWithHost = true
  Normal = (0,0,0)
  Opening = 0
  OverallHeight = 950
  OverallWidth = 2350
  PartitioningType = 0
  PerimeterLength = 0
  PredefinedType = 0
  Preset = 3
  SymbolElevation = false
  SymbolPlan = false
  VerticalArea = 0
  Width = 2350
  WindowParts = OuterFrame | Frame | Wire0,Wire1 | 0.0+V | 0.00+V | LeftFrame | Frame | Wire2,Wire3,Edge8,Mode2 | 0.00+V | 0.0+V | LeftGlass | Glass panel | Wire3 | 8.0 | 40.0+V | RightFrame | Frame | Wire4,Wire5,Edge6,Mode1 | 0.00+V | 0.0+V | RightGlass | Glass panel | Wire5 | 8.0 | 40.0+V
  expr: OverallHeight = .Height.Value
  expr: OverallWidth = .Width.Value
FEATURE [Sketcher::SketchObject] Sketch407
  ExternalGeometry = -> [Window100]
  FullyConstrained = true
  Placement = pos=(4380,-175,4242) rot=(1,0,0;1.5708rad)
  sketch-geometry (8):
    g0: LineSegment StartX=531.333 StartY=185 StartZ=0 EndX=1258.67 EndY=185 EndZ=0
    g1: LineSegment StartX=1258.67 StartY=185 StartZ=0 EndX=1258.67 EndY=981 EndZ=0
    g2: LineSegment StartX=1258.67 StartY=981 StartZ=0 EndX=531.333 EndY=981 EndZ=0
    g3: LineSegment StartX=531.333 StartY=981 StartZ=0 EndX=531.333 EndY=185 EndZ=0
    g4: LineSegment StartX=571.333 StartY=225 StartZ=0 EndX=1218.67 EndY=225 EndZ=0
    g5: LineSegment StartX=1218.67 StartY=225 StartZ=0 EndX=1218.67 EndY=941 EndZ=0
    g6: LineSegment StartX=1218.67 StartY=941 StartZ=0 EndX=571.333 EndY=941 EndZ=0
    g7: LineSegment StartX=571.333 StartY=941 StartZ=0 EndX=571.333 EndY=225 EndZ=0
  constraints (24):
    c: Coincident(g0,g1)
    c: Coincident(g1,g2)
    c: Coincident(g2,g3)
    c: Coincident(g3,g0)
    c: Horizontal(g0)
    c: Horizontal(g2)
    c: Vertical(g1)
    c: Vertical(g3)
    c: Coincident(g4,g5)
    c: Coincident(g5,g6)
    c: Coincident(g6,g7)
    c: Coincident(g7,g4)
    c: Horizontal(g4)
    c: Horizontal(g6)
    c: Vertical(g5)
    c: Vertical(g7)
    c: DistanceY(g6,g2) = 40  'Frame1'
    c: DistanceX(g2,g6) = 40  'Frame2'
    c: DistanceX(g4,g0) = 40  'Frame3'
    c: DistanceY(g0,g4) = 40  'Frame4'
    c: DistanceX(g-3,g2) = 7
    c: DistanceX(g1,g-4) = 7
    c: DistanceY(g1,g-4) = 0
    c: DistanceY(g-3,g0) = 0
FEATURE [Part::FeaturePython] Window101  label="ОК-10_2-001"  # Arch/BIM 170 (typed FeaturePython)
  Area = 792000
  Base = -> Sketch407
  Frame = 35
  Height = 880
  HoleDepth = 0
  HoleWire = 0
  HorizontalArea = 0
  IfcData = attributes={"GlobalId": {"name": "GlobalId", "type": "IfcGloballyUniqueId", "is_enum": false, "enum_values": []}, "Description": {"... (+1229 chars omitted),+1 more (map truncated)
  IfcType = 170
  LouvreSpacing = 0
  LouvreWidth = 0
  Material = -> Material011
  MoveBase = false
  MoveWithHost = true
  Normal = (2e-16,1,2e-16)
  Opening = 0
  OverallHeight = 880
  OverallWidth = 900
  PartitioningType = 0
  PerimeterLength = 0
  PredefinedType = 0
  Preset = 1
  SymbolElevation = false
  SymbolPlan = false
  VerticalArea = 0
  Width = 900
  WindowParts = OuterFrame | Frame | Wire0,Wire1 | 35.0+V | 0.00+V | Glass | Glass panel | Wire1 | 7.0 | 35.0+V
  expr: OverallWidth = .Width.Value
  expr: OverallHeight = .Height.Value
FEATURE [Part::Part2DObjectPython] Line1976  # Draft 2D object (typed FeaturePython)
  Area = 0
  ChamferSize = 0
  Closed = false
  End = (5957.67,-165,0)
  FilletRadius = 0
  Length = 820.667
  MakeFace = true
  Placement = pos=(5137,-165,0) rot=(0,0,1;0rad)
  Points = (2) [(0,0,0),(820.667,2.84217e-14,0)]
  Start = (5137,-165,0)
  Subdivisions = 0
FEATURE [Part::FeaturePython] Wall486  label="раскладка вычет 013"  # Arch/BIM 166 (typed FeaturePython)
  Align = 2
  Area = 530151
  Base = -> Line1976
  BlockHeight = 210
  BlockLength = 265
  CountBroken = 7
  CountEntire = 2
  Face = 0
  Height = 646
  HorizontalArea = 0
  IfcData = attributes={"GlobalId": {"name": "GlobalId", "type": "IfcGloballyUniqueId", "is_enum": false, "enum_values": []}, "Description": {"... (+533 chars omitted),+1 more (map truncated)
  IfcType = 166
  Joint = 10
  Length = 820.667
  MakeBlocks = true
  MoveBase = false
  MoveWithHost = false
  Normal = (0,0,0)
  OffsetFirst = 0
  OffsetSecond = 0
  PerimeterLength = 0
  Placement = pos=(0,35,4287) rot=(0,0,1;0rad)
  PredefinedType = 0
  VerticalArea = 0
  Width = 10
FEATURE [Part::FeaturePython] Wall485  label="раскладка окна 027"  # Arch/BIM 166 (typed FeaturePython)
  Align = 2
  Area = 530151
  Base = -> Line1976
  BlockHeight = 0
  BlockLength = 0
  CountBroken = 0
  CountEntire = 0
  Face = 0
  Height = 646
  HorizontalArea = 0
  IfcData = attributes={"GlobalId": {"name": "GlobalId", "type": "IfcGloballyUniqueId", "is_enum": false, "enum_values": []}, "Description": {"... (+533 chars omitted),+1 more (map truncated)
  IfcType = 166
  Joint = 0
  Length = 820.667
  MakeBlocks = false
  Material = -> Material011
  MoveBase = false
  MoveWithHost = false
  Normal = (0,0,0)
  OffsetFirst = 0
  OffsetSecond = 0
  PerimeterLength = 0
  Placement = pos=(0,35,4287) rot=(0,0,1;0rad)
  PredefinedType = 0
  Subtractions = -> [Wall486]
  VerticalArea = 0
  Width = 10
FEATURE [Part::FeaturePython] Wall487  label="раскладка окна 028"  # Arch/BIM 166 (typed FeaturePython)
  Align = 2
  Area = 530151
  BlockHeight = 0
  BlockLength = 0
  CloneOf = -> Wall485
  CountBroken = 0
  CountEntire = 0
  Face = 0
  Height = 646
  HorizontalArea = 0
  IfcData = attributes={"GlobalId": {"name": "GlobalId", "type": "IfcGloballyUniqueId", "is_enum": false, "enum_values": []}, "Description": {"... (+533 chars omitted),+1 more (map truncated)
  IfcType = 166
  Joint = 0
  Length = 820.667
  MakeBlocks = false
  Material = -> Material011
  MoveBase = false
  MoveWithHost = false
  Normal = (0,0,0)
  OffsetFirst = 0
  OffsetSecond = 0
  PerimeterLength = 0
  Placement = pos=(907.667,35,4287) rot=(0,0,1;0rad)
  PredefinedType = 0
  VerticalArea = 0
  Width = 10
FEATURE [Part::FeaturePython] Wall488  label="раскладка окна 029"  # Arch/BIM 166 (typed FeaturePython)
  Align = 2
  Area = 530151
  BlockHeight = 0
  BlockLength = 0
  CloneOf = -> Wall485
  CountBroken = 0
  CountEntire = 0
  Face = 0
  Height = 646
  HorizontalArea = 0
  IfcData = attributes={"GlobalId": {"name": "GlobalId", "type": "IfcGloballyUniqueId", "is_enum": false, "enum_values": []}, "Description": {"... (+533 chars omitted),+1 more (map truncated)
  IfcType = 166
  Joint = 0
  Length = 820.667
  MakeBlocks = false
  Material = -> Material011
  MoveBase = false
  MoveWithHost = false
  Normal = (0,0,0)
  OffsetFirst = 0
  OffsetSecond = 0
  PerimeterLength = 0
  Placement = pos=(1815.33,35,4287) rot=(0,0,1;0rad)
  PredefinedType = 0
  VerticalArea = 0
  Width = 10
FEATURE [App::GeometryPython] BuildingPart134  label="Раскладка окон"  # Arch/BIM 172 (typed FeaturePython)
  Area = 2.07673e+07
  Group = -> [Wall443,Wall445,Wall447,Wall448,Wall449,Wall450,Wall452,Wall453,Wall455,Wall456,Wall457,Wall458,Wall459,Wall461,Wall462,Wall463,Wall465,Wall466,Wall468,Wall470,Wall471,Wall473,Wall474,Wall484,Wall487,Wall485,Wall488]
  Height = 0
  HeightPropagate = true
  IfcData = attributes={"GlobalId": {"name": "GlobalId", "type": "IfcGloballyUniqueId", "is_enum": false, "enum_values": []}, "Description": {"... (+484 chars omitted),+1 more (map truncated)
  IfcType = 172
  LevelOffset = 0
  PredefinedType = 0
FEATURE [Part::Part2DObjectPython] Rectangle3793  # Draft 2D object (typed FeaturePython)
  Area = 0
  ChamferSize = 0
  Columns = 1
  FilletRadius = 0
  Height = 4250
  Length = 6000
  MakeFace = false
  Placement = pos=(2285,-450,0) rot=(0,0,1;0rad)
  Rows = 1
FEATURE [Part::Extrusion] Extrude099005005  label="cut_contour"
  Base = -> Rectangle3793
  Dir = (0,0,1)
  DirMode = 2
  FaceMakerClass = Part::FaceMakerBullseye
  LengthFwd = 7500
  LengthRev = 0
  Solid = true
  Symmetric = false
FEATURE [Part::Box] Box3075  label="спинка001"
  AttacherType = Attacher::AttachEngine3D
  Height = 510
  Length = 50
  Placement = pos=(3000,-3950,400) rot=(0,0,-1;1.5708rad)
  Width = 480
FEATURE [Part::Box] Box3074  label="ножка008"
  AttacherType = Attacher::AttachEngine3D
  Height = 400
  Length = 40
  Placement = pos=(3440,-3480,0) rot=(0,0,-1;1.5708rad)
  Width = 40
FEATURE [Part::Box] Box3072  label="ножка006"
  AttacherType = Attacher::AttachEngine3D
  Height = 400
  Length = 40
  Placement = pos=(3000,-3479.98,0) rot=(0,0,-1;1.5708rad)
  Width = 40
FEATURE [Part::Box] Box3070  label="сиденье001"
  AttacherType = Attacher::AttachEngine3D
  Height = 50
  Length = 520
  Placement = pos=(3000,-3480,400) rot=(0,0,-1;1.5708rad)
  Width = 480
FEATURE [Part::Box] Box3071  label="ножка005"
  AttacherType = Attacher::AttachEngine3D
  Height = 400
  Length = 40
  Placement = pos=(3440,-3960,0) rot=(0,0,-1;1.5708rad)
  Width = 40
FEATURE [Part::Box] Box3073  label="ножка007"
  AttacherType = Attacher::AttachEngine3D
  Height = 400
  Length = 40
  Placement = pos=(3000,-3960,0) rot=(0,0,-1;1.5708rad)
  Width = 40
FEATURE [Part::Part2DObjectPython] Rectangle007  label="кровать_2_сп_005"  # Draft 2D object (typed FeaturePython)
  ChamferSize = 0
  Columns = 1
  FilletRadius = 25
  Height = 1800
  Length = 2100
  MakeFace = false
  Placement = pos=(3000,-4100,0) rot=(1,0,0;3.14159rad)
  Rows = 1
FEATURE [Part::Extrusion] Extrude037  label="кровать_15_сп_002"
  Base = -> Rectangle007
  Dir = (0,0,1)
  DirMode = 0
  FaceMakerClass = Part::FaceMakerBullseye
  LengthFwd = 250
  LengthRev = 0
  Placement = pos=(0,0,250) rot=(0,0,1;0rad)
  Solid = true
  Symmetric = false
FEATURE [Part::Part2DObjectPython] Rectangle009  label="подушка_001"  # Draft 2D object (typed FeaturePython)
  ChamferSize = 0
  Columns = 1
  FilletRadius = 75
  Height = 600
  Length = 500
  MakeFace = false
  Placement = pos=(3100,-4335.52,0) rot=(1,0,0;3.14159rad)
  Rows = 1
FEATURE [Part::Extrusion] Extrude034  label="подушка_005"
  Base = -> Rectangle009
  Dir = (0,0,1)
  DirMode = 0
  FaceMakerClass = Part::FaceMakerBullseye
  LengthFwd = 150
  LengthRev = 0
  Placement = pos=(0,0,500) rot=(0,0,1;0rad)
  Solid = true
  Symmetric = false
FEATURE [Part::MultiFuse] Fusion003  label="стул001"
  Shapes = -> [Box3072,Box3073,Box3071,Box3070,Box3074,Box3075]
FEATURE [Part::Box] Box3148  label="ножка039"
  AttacherType = Attacher::AttachEngine3D
  Height = 720
  Length = 40
  Placement = pos=(4860,-3700,0) rot=(0,0,-1;1.5708rad)
  Width = 40
FEATURE [Part::Box] Box3147  label="ножка038"
  AttacherType = Attacher::AttachEngine3D
  Height = 720
  Length = 40
  Placement = pos=(6300,-3700,0) rot=(0,0,-1;1.5708rad)
  Width = 40
FEATURE [Part::Box] Box3149  label="ножка040"
  AttacherType = Attacher::AttachEngine3D
  Height = 720
  Length = 40
  Placement = pos=(4862.77,-3057.86,0) rot=(0,0,-1;1.5708rad)
  Width = 40
FEATURE [Part::Box] Box3146  label="ножка037"
  AttacherType = Attacher::AttachEngine3D
  Height = 720
  Length = 40
  Placement = pos=(6300,-3060,0) rot=(0,0,-1;1.5708rad)
  Width = 40
FEATURE [Part::Box] Box3150  label="столешница006"
  AttacherType = Attacher::AttachEngine3D
  Height = 30
  Length = 800
  Placement = pos=(4800,-3000,720) rot=(0,0,-1;1.5708rad)
  Width = 1600
FEATURE [Part::Fillet] Fillet002
  Base = -> Box3150
  Edges = 4 edges r=50: [Edge1,Edge3,Edge5,Edge7]
FEATURE [Part::MultiFuse] Fusion011  label="стол обед"
  Shapes = -> [Box3149,Box3146,Box3147,Box3148,Fillet002]
FEATURE [Part::Part2DObjectPython] Rectangle542  label="подушка_011"  # Draft 2D object (typed FeaturePython)
  ChamferSize = 0
  Columns = 1
  FilletRadius = 75
  Height = 600
  Length = 500
  MakeFace = false
  Placement = pos=(3100,-5064.48,0) rot=(1,0,0;3.14159rad)
  Rows = 1
FEATURE [Part::Extrusion] Extrude054  label="подушка_012"
  Base = -> Rectangle542
  Dir = (0,0,1)
  DirMode = 0
  FaceMakerClass = Part::FaceMakerBullseye
  LengthFwd = 150
  LengthRev = 0
  Placement = pos=(0,0,500) rot=(0,0,1;0rad)
  Solid = true
  Symmetric = false
FEATURE [Part::Feature] Fusion011001  label="стол обеденный 140х80 001"
  Placement = pos=(4350,7850,0) rot=(0,0,1;0rad)
  shape: bbox 1400 x 800 x 750 mm, 30 faces (baked)
FEATURE [Part::Box] Box3244  label="ножка041"
  AttacherType = Attacher::AttachEngine3D
  Height = 40
  Length = 650
  Placement = pos=(2038.54,-3659.82,0) rot=(0,0,-1;0.523599rad)
  Width = 40
FEATURE [Part::Box] Box3245  label="ножка042"
  AttacherType = Attacher::AttachEngine3D
  Height = 40
  Length = 650
  Placement = pos=(2601.46,-3625.18,0) rot=(0,0,1;3.66519rad)
  Width = 40
FEATURE [Part::Box] Box3246  label="спинка002"
  AttacherType = Attacher::AttachEngine3D
  Height = 700
  Length = 70
  Placement = pos=(2000,-4060.52,408.531) rot=(0.060935,0.060935,-0.99628;1.57452rad)
  Width = 660
FEATURE [Part::Box] Box3247  label="сиденье002"
  AttacherType = Attacher::AttachEngine3D
  Height = 70
  Length = 650
  Placement = pos=(2000,-3480,400) rot=(0,0,-1;1.5708rad)
  Width = 660
FEATURE [Part::Box] Box3249  label="ножка044"
  AttacherType = Attacher::AttachEngine3D
  Height = 40
  Length = 650
  Placement = pos=(2310,-3480,0) rot=(0,0,-1;1.5708rad)
  Width = 40
FEATURE [Part::Box] Box3250  label="ножка045"
  AttacherType = Attacher::AttachEngine3D
  Height = 30
  Length = 450
  Placement = pos=(2580,-3653.18,650) rot=(0,0,-1;1.5708rad)
  Width = 80
FEATURE [Part::Box] Box3251  label="ножка046"
  AttacherType = Attacher::AttachEngine3D
  Height = 30
  Length = 450
  Placement = pos=(2000,-3653.18,650) rot=(0,0,-1;1.5708rad)
  Width = 80
FEATURE [Part::Cylinder] Cylinder011  label="Пуфик001"
  Angle = 360
  AttacherType = Attacher::AttachEngine3D
  Height = 400
  Placement = pos=(2330,-3805,0) rot=(0,0,1;1.5708rad)
  Radius = 30
FEATURE [Part::MultiFuse] Fusion011003  label="кресло 001"
  Placement = pos=(-1318.79,6916.61,0) rot=(0,0,1;0rad)
  Shapes = -> [Box3244,Box3245,Box3246,Box3247,Box3249,Box3250,Box3251,Cylinder011]
FEATURE [Part::Feature] Fusion011003001  label="кресло 002"
  Placement = pos=(-1395,6951.91,0) rot=(0,0,1;0rad)
  shape: bbox 660 x 735.3 x 1103 mm, 80 faces (baked)
FEATURE [Part::Box] Box3252  label="ножка 001"
  AttacherType = Attacher::AttachEngine3D
  Height = 750
  Length = 50
  Placement = pos=(3007.32,-4107.32,0) rot=(0,0,-1;1.5708rad)
  Width = 50
FEATURE [Part::Box] Box3253  label="ножка 010"
  AttacherType = Attacher::AttachEngine3D
  Height = 300
  Length = 50
  Placement = pos=(5042.68,-4107.32,0) rot=(0,0,-1;1.5708rad)
  Width = 50
FEATURE [Part::Box] Box3254  label="ножка 011"
  AttacherType = Attacher::AttachEngine3D
  Height = 300
  Length = 50
  Placement = pos=(5042.68,-5842.68,0) rot=(0,0,-1;1.5708rad)
  Width = 50
FEATURE [Part::Box] Box3255  label="ножка 012"
  AttacherType = Attacher::AttachEngine3D
  Height = 750
  Length = 50
  Placement = pos=(3007.32,-5842.68,0) rot=(0,0,-1;1.5708rad)
  Width = 50
FEATURE [Part::Box] Box3256  label="стенка001"
  AttacherType = Attacher::AttachEngine3D
  Height = 250
  Length = 1685.36
  Placement = pos=(3007.32,-4157.32,500) rot=(0,0,-1;1.5708rad)
  Width = 40
FEATURE [Part::Fillet] Fillet
  Base = -> Extrude054
  Edges = 8 edges r=50: [Edge4,Edge7,Edge10,Edge13,Edge16,Edge19,Edge22,Edge24]
FEATURE [Part::Fillet] Fillet003
  Base = -> Extrude034
  Edges = 8 edges r=50: [Edge4,Edge7,Edge10,Edge13,Edge16,Edge19,Edge22,Edge24]
FEATURE [Part::MultiFuse] Fusion011003002  label="кровать 180х210 001"
  Shapes = -> [Fillet,Fillet003,Box3256,Box3255,Box3254,Box3253,Box3252,Extrude037]
FEATURE [Part::Feature] Fusion011003002001  label="кровать 180х210 002"
  Placement = pos=(-3015,11460,0) rot=(0,0,1;0rad)
  shape: bbox 2100 x 1800 x 750 mm, 84 faces (baked)
FEATURE [Part::Box] Box3257  label="ножка047"
  AttacherType = Attacher::AttachEngine3D
  Height = 720
  Length = 40
  Placement = pos=(-1000,-3200,0) rot=(0,0,-1;1.5708rad)
  Width = 40
FEATURE [Part::Box] Box3258  label="ножка048"
  AttacherType = Attacher::AttachEngine3D
  Height = 150
  Length = 40
  Placement = pos=(260,-3710,0) rot=(0,0,-1;1.5708rad)
  Width = 40
FEATURE [Part::Box] Box3259  label="ножка049"
  AttacherType = Attacher::AttachEngine3D
  Height = 150
  Length = 40
  Placement = pos=(260,-3200,0) rot=(0,0,-1;1.5708rad)
  Width = 40
FEATURE [Part::Box] Box3260  label="столешница007"
  AttacherType = Attacher::AttachEngine3D
  Height = 30
  Length = 550
  Placement = pos=(-1000,-3200,720) rot=(0,0,-1;1.5708rad)
  Width = 1300
FEATURE [Part::Box] Box3261  label="ножка050"
  AttacherType = Attacher::AttachEngine3D
  Height = 720
  Length = 40
  Placement = pos=(-1000,-3710,0) rot=(0,0,-1;1.5708rad)
  Width = 40
FEATURE [Part::Box] Box3262  label="тумбочка 003"
  AttacherType = Attacher::AttachEngine3D
  Height = 570
  Length = 400
  Placement = pos=(-100,-3750,150) rot=(0,0,1;0rad)
  Width = 550
FEATURE [Part::Box] Box3263  label="ножка051"
  AttacherType = Attacher::AttachEngine3D
  Height = 150
  Length = 40
  Placement = pos=(-100,-3200,0) rot=(0,0,-1;1.5708rad)
  Width = 40
FEATURE [Part::Box] Box3264  label="ножка052"
  AttacherType = Attacher::AttachEngine3D
  Height = 150
  Length = 40
  Placement = pos=(-100,-3710,0) rot=(0,0,-1;1.5708rad)
  Width = 40
FEATURE [Part::MultiFuse] Fusion011003002002  label="стол письменный 130х55х75 001"
  Shapes = -> [Box3257,Box3258,Box3259,Box3260,Box3261,Box3262,Box3263,Box3264]
FEATURE [Part::Mirroring] mirror016  label="стол письменный 130х55х75 001 (mirrored)"
  Base = (400,-3800,0)
  Normal = (1,0,0)
  Source = -> Fusion011003002002
FEATURE [Part::Feature] Fusion011003002002002  label="кровать 180х210 003"
  Placement = pos=(13498.4,10589.6,3145) rot=(0,0,-1;1.5708rad)
  shape: bbox 1800 x 2100 x 750 mm, 84 faces (baked)
FEATURE [Part::Box] Box3265  label="тумбочка 004"
  AttacherType = Attacher::AttachEngine3D
  Height = 500
  Length = 400
  Placement = pos=(9413.44,7585,3145) rot=(0,0,-1;1.5708rad)
  Width = 400
FEATURE [Part::Box] Box3266  label="тумбочка 005"
  AttacherType = Attacher::AttachEngine3D
  Height = 500
  Length = 400
  Placement = pos=(7183.44,7585,3145) rot=(0,0,-1;1.5708rad)
  Width = 400
FEATURE [Part::Feature] Fusion011003002002003  label="кресло 003"
  Placement = pos=(13649.2,6500,3145) rot=(0,0,-1;1.5708rad)
  shape: bbox 735.3 x 660 x 1103 mm, 80 faces (baked)
FEATURE [Part::Box] Box3267  label="стенка002"
  AttacherType = Attacher::AttachEngine3D
  Height = 250
  Length = 1085.36
  Placement = pos=(207.32,-5457.32,500) rot=(0,0,-1;1.5708rad)
  Width = 40
FEATURE [Part::Part2DObjectPython] Rectangle3798  label="кровать_2_сп_006"  # Draft 2D object (typed FeaturePython)
  ChamferSize = 0
  Columns = 1
  FilletRadius = 25
  Height = 1200
  Length = 2100
  MakeFace = false
  Placement = pos=(200,-5400,0) rot=(1,0,0;3.14159rad)
  Rows = 1
FEATURE [Part::Extrusion] Extrude099005007  label="кровать_15_сп_003"
  Base = -> Rectangle3798
  Dir = (0,0,1)
  DirMode = 0
  FaceMakerClass = Part::FaceMakerBullseye
  LengthFwd = 250
  LengthRev = 0
  Placement = pos=(0,0,250) rot=(0,0,1;0rad)
  Solid = true
  Symmetric = false
FEATURE [Part::Part2DObjectPython] Rectangle3799  label="подушка_014"  # Draft 2D object (typed FeaturePython)
  ChamferSize = 0
  Columns = 1
  FilletRadius = 75
  Height = 600
  Length = 500
  MakeFace = false
  Placement = pos=(300,-5700,0) rot=(1,0,0;3.14159rad)
  Rows = 1
FEATURE [Part::Extrusion] Extrude099005008  label="подушка_013"
  Base = -> Rectangle3799
  Dir = (0,0,1)
  DirMode = 0
  FaceMakerClass = Part::FaceMakerBullseye
  LengthFwd = 150
  LengthRev = 0
  Placement = pos=(0,0,500) rot=(0,0,1;0rad)
  Solid = true
  Symmetric = false
FEATURE [Part::Fillet] Fillet004
  Base = -> Extrude099005008
  Edges = 8 edges r=50: [Edge4,Edge7,Edge10,Edge13,Edge16,Edge19,Edge22,Edge24]
FEATURE [Part::Box] Box3268  label="ножка 013"
  AttacherType = Attacher::AttachEngine3D
  Height = 750
  Length = 50
  Placement = pos=(207.322,-6542.68,0) rot=(0,0,-1;1.5708rad)
  Width = 50
FEATURE [Part::Box] Box3269  label="ножка 014"
  AttacherType = Attacher::AttachEngine3D
  Height = 750
  Length = 50
  Placement = pos=(207.322,-5407.32,0) rot=(0,0,-1;1.5708rad)
  Width = 50
FEATURE [Part::Box] Box3270  label="ножка 015"
  AttacherType = Attacher::AttachEngine3D
  Height = 300
  Length = 50
  Placement = pos=(2242.68,-5407.32,0) rot=(0,0,-1;1.5708rad)
  Width = 50
FEATURE [Part::Box] Box3271  label="ножка 016"
  AttacherType = Attacher::AttachEngine3D
  Height = 300
  Length = 50
  Placement = pos=(2242.68,-6542.68,0) rot=(0,0,-1;1.5708rad)
  Width = 50
FEATURE [Part::MultiFuse] Fusion011003002002005  label="кровать 120х210 001"
  Shapes = -> [Extrude099005007,Fillet004,Box3267,Box3268,Box3269,Box3270,Box3271]
FEATURE [Part::Feature] Fusion011003002002005001  label="кровать 120х210 002"
  Placement = pos=(3080,-4615,3145) rot=(0,0,1;3.14159rad)
  shape: bbox 2100 x 1200 x 750 mm, 66 faces (baked)
FEATURE [Part::Feature] Fusion011003002002005002  label="кровать 120х210 003"
  Placement = pos=(3080,985,3145) rot=(0,0,1;3.14159rad)
  shape: bbox 2100 x 1200 x 750 mm, 66 faces (baked)
FEATURE [Part::Box] Box3272  label="ножка053"
  AttacherType = Attacher::AttachEngine3D
  Height = 650
  Length = 40
  Placement = pos=(-950,-4510,0) rot=(0,0,-1;1.5708rad)
  Width = 500
FEATURE [Part::Box] Box3273  label="столешница008"
  AttacherType = Attacher::AttachEngine3D
  Height = 30
  Length = 650
  Placement = pos=(-1000,-3200,720) rot=(0,0,-1;1.5708rad)
  Width = 1510
FEATURE [Part::Box] Box3274  label="ножка054"
  AttacherType = Attacher::AttachEngine3D
  Height = 720
  Length = 650
  Placement = pos=(470,-3200,0) rot=(0,0,-1;1.5708rad)
  Width = 40
FEATURE [Part::Box] Box3276  label="ножка055"
  AttacherType = Attacher::AttachEngine3D
  Height = 150
  Length = 40
  Placement = pos=(260,-3710,0) rot=(0,0,-1;1.5708rad)
  Width = 40
FEATURE [Part::Box] Box3280  label="столешница009"
  AttacherType = Attacher::AttachEngine3D
  Height = 30
  Length = 1350
  Placement = pos=(-950,-3200,650) rot=(0,0,-1;1.5708rad)
  Width = 500
FEATURE [Part::Box] Box3281  label="ножка059"
  AttacherType = Attacher::AttachEngine3D
  Height = 720
  Length = 650
  Placement = pos=(-1000,-3200,0) rot=(0,0,-1;1.5708rad)
  Width = 40
FEATURE [Part::Box] Box3283  label="ножка061"
  AttacherType = Attacher::AttachEngine3D
  Height = 200
  Length = 40
  Placement = pos=(-960,-3200,420) rot=(0,0,-1;1.5708rad)
  Width = 1430
FEATURE [Part::MultiFuse] Fusion011003002002005003  label="MALM МАЛЬМ Письменный стол с выдвижной панелью 151x65 см 001"
  Shapes = -> [Box3272,Box3273,Box3274,Box3276,Box3280,Box3281,Box3283]
FEATURE [Sketcher::SketchObject] Sketch408
  FullyConstrained = true
  Placement = pos=(3535,3165,3145) rot=(0.57735,0.57735,0.57735;2.0944rad)
  sketch-geometry (8):
    g0: LineSegment StartX=0 StartY=0 StartZ=0 EndX=900 EndY=0 EndZ=0
    g1: LineSegment StartX=900 StartY=0 StartZ=0 EndX=900 EndY=2400 EndZ=0
    g2: LineSegment StartX=900 StartY=2400 StartZ=0 EndX=0 EndY=2400 EndZ=0
    g3: LineSegment StartX=0 StartY=2400 StartZ=0 EndX=0 EndY=0 EndZ=0
    g4: LineSegment StartX=50 StartY=0 StartZ=0 EndX=850 EndY=0 EndZ=0
    g5: LineSegment StartX=850 StartY=0 StartZ=0 EndX=850 EndY=2350 EndZ=0
    g6: LineSegment StartX=850 StartY=2350 StartZ=0 EndX=50 EndY=2350 EndZ=0
    g7: LineSegment StartX=50 StartY=2350 StartZ=0 EndX=50 EndY=0 EndZ=0
  constraints (23):
    c: Coincident(g0,g1)
    c: Coincident(g1,g2)
    c: Coincident(g2,g3)
    c: Coincident(g3,g0)
    c: Horizontal(g0)
    c: Horizontal(g2)
    c: Vertical(g1)
    c: Vertical(g3)
    c: Coincident(g4,g5)
    c: Coincident(g5,g6)
    c: Coincident(g6,g7)
    c: Coincident(g7,g4)
    c: Horizontal(g4)
    c: Horizontal(g6)
    c: Vertical(g5)
    c: Vertical(g7)
    c: DistanceY(g1) = 2400  'Height'
    c: DistanceX(g0) = 900  'Width'
    c: DistanceY(g6,g2) = 50  'Frame1'
    c: DistanceX(g2,g6) = 50  'Frame2'
    c: DistanceX(g4,g0) = 50  'Frame3'
    c: DistanceY(g0,g4) = 0
    c: Coincident(g0,g-1)
FEATURE [Part::FeaturePython] Window102  label="Д-90-007"  # Arch/BIM 41 (typed FeaturePython)
  Area = 2160000
  Base = -> Sketch408
  Frame = 50
  GlobalId = 29QgZPyov5qAVey2RViV7P
  Height = 2400
  HoleDepth = 0
  HoleWire = 0
  HorizontalArea = 0
  IfcData = IfcUID=29QgZPyov5qAVey2RViV7P; attributes={"OverallHeight": {"value": 2400.0}, "OverallWidth": {"value": 900.0}, "GlobalId": {"value": "29QgZPyov5qAVey2RViV7P"}}
  IfcType = 41
  LouvreSpacing = 0
  LouvreWidth = 0
  Material = -> Material011
  MoveBase = false
  MoveWithHost = true
  Normal = (0,0,0)
  Opening = 0
  OperationType = 0
  OverallHeight = 2400
  OverallWidth = 900
  PerimeterLength = 0
  Placement = pos=(25,0,0) rot=(0,0,1;0rad)
  PredefinedType = 0
  Preset = 6
  SymbolElevation = false
  SymbolPlan = false
  VerticalArea = 0
  Width = 900
  WindowParts = OuterFrame | Frame | Wire0,Wire1 | 0.0+V | 0.00+V | Door | Solid panel | Wire1 | 50.0 | 0.0+V
  expr: OverallWidth = .Width.Value
  expr: OverallHeight = .Height.Value
FEATURE [Sketcher::SketchObject] Sketch409
  FullyConstrained = true
  Placement = pos=(4925,2785,3145) rot=(1,0,0;1.5708rad)
  sketch-geometry (8):
    g0: LineSegment StartX=0 StartY=0 StartZ=0 EndX=900 EndY=0 EndZ=0
    g1: LineSegment StartX=900 StartY=0 StartZ=0 EndX=900 EndY=2400 EndZ=0
    g2: LineSegment StartX=900 StartY=2400 StartZ=0 EndX=0 EndY=2400 EndZ=0
    g3: LineSegment StartX=0 StartY=2400 StartZ=0 EndX=0 EndY=0 EndZ=0
    g4: LineSegment StartX=50 StartY=0 StartZ=0 EndX=850 EndY=0 EndZ=0
    g5: LineSegment StartX=850 StartY=0 StartZ=0 EndX=850 EndY=2350 EndZ=0
    g6: LineSegment StartX=850 StartY=2350 StartZ=0 EndX=50 EndY=2350 EndZ=0
    g7: LineSegment StartX=50 StartY=2350 StartZ=0 EndX=50 EndY=0 EndZ=0
  constraints (23):
    c: Coincident(g0,g1)
    c: Coincident(g1,g2)
    c: Coincident(g2,g3)
    c: Coincident(g3,g0)
    c: Horizontal(g0)
    c: Horizontal(g2)
    c: Vertical(g1)
    c: Vertical(g3)
    c: Coincident(g4,g5)
    c: Coincident(g5,g6)
    c: Coincident(g6,g7)
    c: Coincident(g7,g4)
    c: Horizontal(g4)
    c: Horizontal(g6)
    c: Vertical(g5)
    c: Vertical(g7)
    c: DistanceY(g1) = 2400  'Height'
    c: DistanceX(g0) = 900  'Width'
    c: DistanceY(g6,g2) = 50  'Frame1'
    c: DistanceX(g2,g6) = 50  'Frame2'
    c: DistanceX(g4,g0) = 50  'Frame3'
    c: DistanceY(g0,g4) = 0
    c: Coincident(g0,g-1)
FEATURE [Part::FeaturePython] Window103  label="Д-90-008"  # Arch/BIM 41 (typed FeaturePython)
  Area = 2160000
  Base = -> Sketch409
  Frame = 50
  GlobalId = 00iW5F1Zz0_RepVZ61wedb
  Height = 2400
  HoleDepth = 0
  HoleWire = 0
  HorizontalArea = 0
  IfcData = IfcUID=00iW5F1Zz0_RepVZ61wedb; attributes={"OverallHeight": {"value": 2400.0}, "OverallWidth": {"value": 900.0}, "GlobalId": {"value": "00iW5F1Zz0_RepVZ61wedb"}}
  IfcType = 41
  LouvreSpacing = 0
  LouvreWidth = 0
  Material = -> Material011
  MoveBase = false
  MoveWithHost = true
  Normal = (0,0,0)
  Opening = 0
  OperationType = 0
  OverallHeight = 2400
  OverallWidth = 900
  PerimeterLength = 0
  Placement = pos=(0,75,0) rot=(0,0,1;0rad)
  PredefinedType = 0
  Preset = 6
  SymbolElevation = false
  SymbolPlan = false
  VerticalArea = 0
  Width = 900
  WindowParts = OuterFrame | Frame | Wire0,Wire1 | 0.0+V | 0.00+V | Door | Solid panel | Wire1 | 50.0 | 0.0+V
  expr: OverallHeight = .Height.Value
  expr: OverallWidth = .Width.Value
FEATURE [Sketcher::SketchObject] Sketch410
  FullyConstrained = true
  Placement = pos=(3535,4305,3145) rot=(0.57735,0.57735,0.57735;2.0944rad)
  sketch-geometry (8):
    g0: LineSegment StartX=0 StartY=0 StartZ=0 EndX=900 EndY=0 EndZ=0
    g1: LineSegment StartX=900 StartY=0 StartZ=0 EndX=900 EndY=2400 EndZ=0
    g2: LineSegment StartX=900 StartY=2400 StartZ=0 EndX=0 EndY=2400 EndZ=0
    g3: LineSegment StartX=0 StartY=2400 StartZ=0 EndX=0 EndY=0 EndZ=0
    g4: LineSegment StartX=50 StartY=0 StartZ=0 EndX=850 EndY=0 EndZ=0
    g5: LineSegment StartX=850 StartY=0 StartZ=0 EndX=850 EndY=2350 EndZ=0
    g6: LineSegment StartX=850 StartY=2350 StartZ=0 EndX=50 EndY=2350 EndZ=0
    g7: LineSegment StartX=50 StartY=2350 StartZ=0 EndX=50 EndY=0 EndZ=0
  constraints (23):
    c: Coincident(g0,g1)
    c: Coincident(g1,g2)
    c: Coincident(g2,g3)
    c: Coincident(g3,g0)
    c: Horizontal(g0)
    c: Horizontal(g2)
    c: Vertical(g1)
    c: Vertical(g3)
    c: Coincident(g4,g5)
    c: Coincident(g5,g6)
    c: Coincident(g6,g7)
    c: Coincident(g7,g4)
    c: Horizontal(g4)
    c: Horizontal(g6)
    c: Vertical(g5)
    c: Vertical(g7)
    c: DistanceY(g1) = 2400  'Height'
    c: DistanceX(g0) = 900  'Width'
    c: DistanceY(g6,g2) = 50  'Frame1'
    c: DistanceX(g2,g6) = 50  'Frame2'
    c: DistanceX(g4,g0) = 50  'Frame3'
    c: DistanceY(g0,g4) = 0
    c: Coincident(g0,g-1)
FEATURE [Part::FeaturePython] Window104  label="Д-90-009"  # Arch/BIM 41 (typed FeaturePython)
  Area = 2160000
  Base = -> Sketch410
  Frame = 50
  GlobalId = 29QgZPyov5qAVey2RViV7P
  Height = 2400
  HoleDepth = 0
  HoleWire = 0
  HorizontalArea = 0
  IfcData = IfcUID=29QgZPyov5qAVey2RViV7P; attributes={"OverallHeight": {"value": 2400.0}, "OverallWidth": {"value": 900.0}, "GlobalId": {"value": "29QgZPyov5qAVey2RViV7P"}}
  IfcType = 41
  LouvreSpacing = 0
  LouvreWidth = 0
  Material = -> Material011
  MoveBase = false
  MoveWithHost = true
  Normal = (0,0,0)
  Opening = 0
  OperationType = 0
  OverallHeight = 2400
  OverallWidth = 900
  PerimeterLength = 0
  Placement = pos=(25,0,0) rot=(0,0,1;0rad)
  PredefinedType = 0
  Preset = 6
  SymbolElevation = false
  SymbolPlan = false
  VerticalArea = 0
  Width = 900
  WindowParts = OuterFrame | Frame | Wire0,Wire1 | 0.0+V | 0.00+V | Door | Solid panel | Wire1 | 50.0 | 0.0+V
  expr: OverallHeight = .Height.Value
  expr: OverallWidth = .Width.Value
FEATURE [Sketcher::SketchObject] Sketch411
  FullyConstrained = true
  Placement = pos=(6960,3085,3145) rot=(0.57735,0.57735,0.57735;2.0944rad)
  sketch-geometry (8):
    g0: LineSegment StartX=0 StartY=0 StartZ=0 EndX=900 EndY=0 EndZ=0
    g1: LineSegment StartX=900 StartY=0 StartZ=0 EndX=900 EndY=2400 EndZ=0
    g2: LineSegment StartX=900 StartY=2400 StartZ=0 EndX=0 EndY=2400 EndZ=0
    g3: LineSegment StartX=0 StartY=2400 StartZ=0 EndX=0 EndY=0 EndZ=0
    g4: LineSegment StartX=50 StartY=0 StartZ=0 EndX=850 EndY=0 EndZ=0
    g5: LineSegment StartX=850 StartY=0 StartZ=0 EndX=850 EndY=2350 EndZ=0
    g6: LineSegment StartX=850 StartY=2350 StartZ=0 EndX=50 EndY=2350 EndZ=0
    g7: LineSegment StartX=50 StartY=2350 StartZ=0 EndX=50 EndY=0 EndZ=0
  constraints (23):
    c: Coincident(g0,g1)
    c: Coincident(g1,g2)
    c: Coincident(g2,g3)
    c: Coincident(g3,g0)
    c: Horizontal(g0)
    c: Horizontal(g2)
    c: Vertical(g1)
    c: Vertical(g3)
    c: Coincident(g4,g5)
    c: Coincident(g5,g6)
    c: Coincident(g6,g7)
    c: Coincident(g7,g4)
    c: Horizontal(g4)
    c: Horizontal(g6)
    c: Vertical(g5)
    c: Vertical(g7)
    c: DistanceY(g1) = 2400  'Height'
    c: DistanceX(g0) = 900  'Width'
    c: DistanceY(g6,g2) = 50  'Frame1'
    c: DistanceX(g2,g6) = 50  'Frame2'
    c: DistanceX(g4,g0) = 50  'Frame3'
    c: DistanceY(g0,g4) = 0
    c: Coincident(g0,g-1)
FEATURE [Part::FeaturePython] Window105  label="Д-90-010"  # Arch/BIM 41 (typed FeaturePython)
  Area = 2160000
  Base = -> Sketch411
  Frame = 50
  GlobalId = 29QgZPyov5qAVey2RViV7P
  Height = 2400
  HoleDepth = 0
  HoleWire = 0
  HorizontalArea = 0
  IfcData = IfcUID=29QgZPyov5qAVey2RViV7P; attributes={"OverallHeight": {"value": 2400.0}, "OverallWidth": {"value": 900.0}, "GlobalId": {"value": "29QgZPyov5qAVey2RViV7P"}}
  IfcType = 41
  LouvreSpacing = 0
  LouvreWidth = 0
  Material = -> Material011
  MoveBase = false
  MoveWithHost = true
  Normal = (0,0,0)
  Opening = 0
  OperationType = 0
  OverallHeight = 2400
  OverallWidth = 900
  PerimeterLength = 0
  Placement = pos=(30,0,0) rot=(0,0,1;0rad)
  PredefinedType = 0
  Preset = 6
  SymbolElevation = false
  SymbolPlan = false
  VerticalArea = 0
  Width = 900
  WindowParts = OuterFrame | Frame | Wire0,Wire1 | 0.0+V | 0.00+V | Door | Solid panel | Wire1 | 50.0 | 0.0+V
  expr: OverallHeight = .Height.Value
  expr: OverallWidth = .Width.Value
FEATURE [App::GeometryPython] BuildingPart  label="Окна и двери (мансарда)"  # Arch/BIM 52 (typed FeaturePython)
  Area = 8640000
  GlobalId = 2ZdcXw_FbERwG8YjxnAt$R
  Group = -> [Window102,Window103,Window104,Window105]
  Height = 0
  HeightPropagate = true
  IfcData = IfcUID=2ZdcXw_FbERwG8YjxnAt$R,+2 more (map truncated)
  IfcType = 52
  LevelOffset = 0
  Placement = pos=(0,0,5) rot=(0,0,1;0rad)
FEATURE [App::FeaturePython] Dimension188  # Draft dimension (typed FeaturePython)
  Diameter = false
  Dimline = (9416.95,2364.92,0)
  Direction = (0,0,0)
  Distance = 202.728
  End = (10600,2890,0)
  Normal = (0,0,1)
  Start = (10397.3,2890,0)
FEATURE [App::FeaturePython] Dimension189  # Draft dimension (typed FeaturePython)
  Diameter = false
  Dimline = (4800,4100,0)
  Direction = (0,0,0)
  Distance = 3225
  End = (6910,5485,0)
  Normal = (0,0,1)
  Start = (3685,5485,0)
FEATURE [Part::Part2DObjectPython] Wire1016  label="Детская #2"  # Draft 2D object (typed FeaturePython)
  Area = 1.27556e+07
  ChamferSize = 0
  Closed = true
  End = (4135,7595,0)
  FilletRadius = 0
  Length = 15050
  MakeFace = true
  Placement = pos=(9050,1075,0) rot=(0,0,1;3.14159rad)
  Points = (8) [(4915,-4510,0),(5515,-4510,0),(5515,-3160,0),(9080,-3160,0),(9080,-4405,0),(8877.27,-4405,0),(8877.27,-6520,0),(4915,-6520,0)]
  Start = (4135,5585,0)
  Subdivisions = 0
FEATURE [TechDraw::DrawViewSpreadsheet] Sheet001
  CellEnd = E21
  CellStart = C13
  Font = osifont
  LineWidth = 0.35
  LockPosition = false
  Rotation = 0
  Scale = 1.2
  ScaleType = 2
  Source = -> Spreadsheet
  Symbol = <blob: 6069 chars omitted>
  TextSize = 14
  X = 163.093
  Y = 91.4305
FEATURE [TechDraw::DrawViewAnnotation] Annotation038
  Font = osifont
  LineSpace = 80
  LockPosition = false
  MaxWidth = -1
  Rotation = 0
  ScaleType = 0
  Text = \u042d\u043a\u0441\u043f\u043b\u0438\u043a\u0430\u0446\u0438\u044f \u043f\u043e\u043c\u0435\u0449\u0435\u043d\u0438\u0439 \u043c\u0430\u043d\u0441\u0430\u0440\u0434\u043d\u043e\u0433\u043e \u044d\u0442\u0430\u0436\u0430:
  TextSize = 8
  TextStyle = 0
  X = 135.126
  Y = 138.264
FEATURE [TechDraw::DrawPage] Page  label="Экспликация"
  KeepUpdated = false
  NextBalloonIndex = 1
  ProjectionType = 0
  Template = -> Template
  Views = -> [Sheet,Annotation030,Sheet001,Annotation038]
FEATURE [Part::Part2DObjectPython] Wire1017  # Draft 2D object (typed FeaturePython)
  Area = 1.44e+06
  ChamferSize = 0
  Closed = true
  End = (6015,2785,0)
  FilletRadius = 0
  Length = 5200
  MakeFace = true
  Placement = pos=(6685,3660,0) rot=(0,0,1;3.14159rad)
  Points = (4) [(-130,875,0),(-130,2675,0),(670,2675,0),(670,875,0)]
  Start = (6815,2785,0)
  Subdivisions = 0
FEATURE [Part::Part2DObjectPython] Wire1018  # Draft 2D object (typed FeaturePython)
  Area = 0
  ChamferSize = 0
  Closed = true
  End = (6115,2680,0)
  FilletRadius = 0
  Length = 4400
  MakeFace = false
  Placement = pos=(6530,3615,0) rot=(0,0,1;3.14159rad)
  Points = (4) [(-185,935,0),(-185,2535,0),(415,2535,0),(415,935,0)]
  Start = (6715,2680,0)
  Subdivisions = 0
FEATURE [Part::FeaturePython] Structure601  label="Структура038"  # Arch/BIM 52 (typed FeaturePython)
  Base = -> Wire1018
  FaceMaker = 0
  Height = 450
  HorizontalArea = 960000
  IfcData = attributes={"GlobalId": {"name": "GlobalId", "type": "IfcGloballyUniqueId", "is_enum": false, "enum_values": []}, "Description": {"... (+484 chars omitted),+1 more (map truncated)
  IfcType = 52
  Length = 0
  MoveBase = false
  MoveWithHost = false
  Nodes = (2) [(6409.93,5722.83,0),(6409.93,5722.83,450)]
  NodesOffset = 0
  Normal = (0,0,1)
  PerimeterLength = 4400
  Placement = pos=(0,0,3295) rot=(0,0,1;0rad)
  VerticalArea = 1.98e+06
  Width = 100
FEATURE [Part::FeaturePython] Structure602  label="Ванна 180х091"  # Arch/BIM 52 (typed FeaturePython)
  Base = -> Wire1017
  FaceMaker = 0
  GlobalId = 2VbcwV0QPCqROXcrzT3$_s
  Height = 600
  HorizontalArea = 1.44e+06
  IfcData = IfcUID=2VbcwV0QPCqROXcrzT3$_s,+2 more (map truncated)
  IfcType = 52
  Length = 0
  Material = -> Material013
  MoveBase = false
  MoveWithHost = false
  Nodes = (2) [(-2856.79,7112.64,0),(-2856.79,7112.64,600)]
  NodesOffset = 0
  Normal = (0,0,1)
  PerimeterLength = 5200
  Placement = pos=(0,0,3145) rot=(0,0,1;0rad)
  Subtractions = -> [Structure601]
  VerticalArea = 5.1e+06
  Width = 100
FEATURE [Part::FeaturePython] Structure605  label="Структура039"  # Arch/BIM 52 (typed FeaturePython)
  FaceMaker = 0
  Height = 100
  HorizontalArea = 100921
  IfcData = attributes={"GlobalId": {"name": "GlobalId", "type": "IfcGloballyUniqueId", "is_enum": false, "enum_values": []}, "Description": {"... (+484 chars omitted),+1 more (map truncated)
  IfcType = 52
  Length = 0
  MoveBase = false
  MoveWithHost = false
  Nodes = (2) [(6380,5325,0),(6380,5325,100)]
  NodesOffset = 0
  Normal = (0,0,1)
  PerimeterLength = 1241.24
  Placement = pos=(0,-410,3945) rot=(0,0,1;0rad)
  VerticalArea = 124124
  Width = 100
FEATURE [Part::FeaturePython] Component241012  label="унитаз с инсталляцией 007"  # Arch/BIM 0 (typed FeaturePython)
  HorizontalArea = 0
  IfcData = attributes={"GlobalId": {"name": "GlobalId", "type": "IfcGloballyUniqueId", "is_enum": false, "enum_values": []}, "Description": {"... (+538 chars omitted),+1 more (map truncated)
  IfcType = 0
  Material = -> Material013
  MoveBase = false
  MoveWithHost = false
  PerimeterLength = 0
  Placement = pos=(-5025,-5125,3145) rot=(0,0,-1;0rad)
  PredefinedType = 0
  VerticalArea = 0
FEATURE [Part::Part2DObjectPython] Wire1019  # Draft 2D object (typed FeaturePython)
  Area = 0
  ChamferSize = 0
  Closed = true
  End = (6015,2785,0)
  FilletRadius = 0
  Length = 5380
  MakeFace = false
  Placement = pos=(6565,2725,0) rot=(0,0,1;3.14159rad)
  Points = (4) [(-330,-60,0),(-330,1750,0),(550,1750,0),(550,-60,0)]
  Start = (6895,2785,0)
  Subdivisions = 0
FEATURE [Part::FeaturePython] Structure609  label="Структура040"  # Arch/BIM 52 (typed FeaturePython)
  FaceMaker = 0
  Height = 100
  HorizontalArea = 100921
  IfcData = attributes={"GlobalId": {"name": "GlobalId", "type": "IfcGloballyUniqueId", "is_enum": false, "enum_values": []}, "Description": {"... (+484 chars omitted),+1 more (map truncated)
  IfcType = 52
  Length = 0
  MoveBase = false
  MoveWithHost = false
  Nodes = (2) [(6380,5325,0),(6380,5325,100)]
  NodesOffset = 0
  Normal = (0,0,1)
  PerimeterLength = 1241.24
  Placement = pos=(0,-410,3945) rot=(0,0,1;0rad)
  VerticalArea = 124124
  Width = 100
FEATURE [Part::FeaturePython] Structure608  label="Раковина 120x45 001"  # Arch/BIM 52 (typed FeaturePython)
  FaceMaker = 0
  GlobalId = 2d5W_OQQf2Fxkoe6wMEOb9
  Height = 55
  HorizontalArea = 0
  IfcData = IfcUID=2d5W_OQQf2Fxkoe6wMEOb9,+2 more (map truncated)
  IfcType = 52
  Length = 0
  Material = -> Material013
  MoveBase = false
  MoveWithHost = false
  Nodes = (2) [(-2856.79,7112.64,0),(-2856.79,7112.64,600)]
  NodesOffset = 0
  Normal = (0,0,1)
  PerimeterLength = 0
  Placement = pos=(0,-410,3990) rot=(0,0,1;0rad)
  Subtractions = -> [Structure609,Structure605]
  VerticalArea = 0
  Width = 100
FEATURE [Part::FeaturePython] Structure610  label="Раковина 120x45 001 (тумба)"  # Arch/BIM 52 (typed FeaturePython)
  FaceMaker = 0
  GlobalId = 2d5W_OQQf2Fxkoe6wMEOb9
  Height = 570
  HorizontalArea = 540000
  IfcData = IfcUID=2d5W_OQQf2Fxkoe6wMEOb9,+2 more (map truncated)
  IfcType = 52
  Length = 0
  Material = -> Material013
  MoveBase = false
  MoveWithHost = false
  Nodes = (2) [(-2856.79,7112.64,0),(-2856.79,7112.64,600)]
  NodesOffset = 0
  Normal = (0,0,-1)
  PerimeterLength = 3300
  Placement = pos=(0,-410,3990) rot=(0,0,1;0rad)
  VerticalArea = 1881000
  Width = 100
FEATURE [Part::Box] Box3284  label="СМ001"
  AttacherType = Attacher::AttachEngine3D
  Height = 850
  Length = 600
  Placement = pos=(4235,2180,3145) rot=(0,0,1;0rad)
  Width = 600
FEATURE [Part::Part2DObjectPython] Line1995  label="Перемычки_051"  # Draft 2D object (typed FeaturePython)
  Area = 0
  ChamferSize = 0
  Closed = true
  End = (3680,5805,0)
  FilletRadius = 0
  Length = 1290
  MakeFace = true
  Placement = pos=(3680,4432,0) rot=(0,0,1;1.5708rad)
  Points = (2) [(83,0,0),(1373,0,0)]
  Start = (3680,4515,0)
  Subdivisions = 0
FEATURE [Part::FeaturePython] Wall497  label="Перемычка 3ПБ 13-37 001"  # Arch/BIM 166 (typed FeaturePython)
  Align = 0
  Area = 283800
  Base = -> Line1995
  BlockHeight = 0
  BlockLength = 0
  CountBroken = 0
  CountEntire = 0
  Face = 0
  GlobalId = 0GYkMrihr4SvLL6ceY8F$x
  Height = 220
  HorizontalArea = 154800
  IfcData = IfcUID=0GYkMrihr4SvLL6ceY8F$x,+2 more (map truncated)
  IfcType = 166
  Joint = 0
  Length = 1290
  MakeBlocks = false
  Material = -> Material001
  MoveBase = false
  MoveWithHost = false
  Normal = (0,0,0)
  Offset = 5
  OffsetFirst = 0
  OffsetSecond = 0
  PerimeterLength = 2820
  Placement = pos=(-4.55e-13,-1.819e-12,2121) rot=(0,0,1;0rad)
  PredefinedType = 0
  VerticalArea = 620400
  Width = 120
FEATURE [Part::Mirroring] mirror016002  label="MALM МАЛЬМ Письменный стол с выдвижной панелью 151x65 см 001 (mirrored)"
  Base = (-1200,-3100,0)
  Normal = (-1,0,0)
  Source = -> Fusion011003002002005003
FEATURE [Part::Part2DObjectPython] Line2039  # Draft 2D object (typed FeaturePython)
  Area = 0
  ChamferSize = 0
  Closed = true
  End = (8285,3010,9.536e-13)
  FilletRadius = 0
  Length = 6000
  MakeFace = true
  Placement = pos=(3096.1,2990,0) rot=(0,0,1;0rad)
  Points = (2) [(-811.102,20,0),(5188.9,20,9.53648e-13)]
  Start = (2285,3010,0)
  Subdivisions = 0
FEATURE [Part::Part2DObjectPython] Line2040  # Draft 2D object (typed FeaturePython)
  Area = 0
  ChamferSize = 0
  Closed = true
  End = (6910,2935,0)
  FilletRadius = 0
  Length = 2500
  MakeFace = true
  Placement = pos=(15920,575,0) rot=(0,0,1;1.5708rad)
  Points = (2) [(4860,9010,0),(2360,9010,0)]
  Start = (6910,5435,0)
  Subdivisions = 0
FEATURE [Part::FeaturePython] Wall556  label="прогон 001"  # Arch/BIM 166 (typed FeaturePython)
  Align = 1
  Area = 500000
  Base = -> Line2040
  BlockHeight = 0
  BlockLength = 0
  CountBroken = 0
  CountEntire = 0
  Face = 0
  GlobalId = 1B71KP0Y9AOfuyJlUXW0eC
  Height = 200
  HorizontalArea = 375000
  IfcData = IfcUID=1B71KP0Y9AOfuyJlUXW0eC; attributes={"GlobalId": {"value": "1B71KP0Y9AOfuyJlUXW0eC"}}
  IfcType = 166
  Joint = 0
  Length = 2500
  MakeBlocks = false
  Material = -> Material
  MoveBase = false
  MoveWithHost = false
  Normal = (0,0,0)
  OffsetFirst = 0
  OffsetSecond = 0
  PerimeterLength = 5300
  Placement = pos=(0,0,6220) rot=(0,0,1;0rad)
  PredefinedType = 0
  VerticalArea = 1.06e+06
  Width = 150
FEATURE [Part::FeaturePython] Wall557  label="прогон 002"  # Arch/BIM 166 (typed FeaturePython)
  Align = 1
  Area = 1200000
  Base = -> Line2039
  BlockHeight = 0
  BlockLength = 0
  CountBroken = 0
  CountEntire = 0
  Face = 0
  GlobalId = 1B71KP0Y9AOfuyJlUXW0eC
  Height = 200
  HorizontalArea = 900000
  IfcData = IfcUID=1B71KP0Y9AOfuyJlUXW0eC; attributes={"GlobalId": {"value": "1B71KP0Y9AOfuyJlUXW0eC"}}
  IfcType = 166
  Joint = 0
  Length = 6000
  MakeBlocks = false
  Material = -> Material
  MoveBase = false
  MoveWithHost = false
  Normal = (0,0,0)
  Offset = 15
  OffsetFirst = 0
  OffsetSecond = 0
  PerimeterLength = 12300
  Placement = pos=(4.55e-13,-90,6070) rot=(0,0,1;0rad)
  PredefinedType = 0
  VerticalArea = 2.46e+06
  Width = 150
FEATURE [Part::Part2DObjectPython] Line2041  # Draft 2D object (typed FeaturePython)
  Area = 0
  ChamferSize = 0
  Closed = true
  End = (3535,5435,9.095e-13)
  FilletRadius = 0
  Length = 2500
  MakeFace = true
  Placement = pos=(3555,-7095,0) rot=(0,0,1;1.5708rad)
  Points = (2) [(10030,20,0),(12530,20,9.09495e-13)]
  Start = (3535,2935,0)
  Subdivisions = 0
FEATURE [Part::FeaturePython] Wall558  label="прогон 003"  # Arch/BIM 166 (typed FeaturePython)
  Align = 1
  Area = 500000
  Base = -> Line2041
  BlockHeight = 0
  BlockLength = 0
  CountBroken = 0
  CountEntire = 0
  Face = 0
  GlobalId = 1B71KP0Y9AOfuyJlUXW0eC
  Height = 200
  HorizontalArea = 375000
  IfcData = IfcUID=1B71KP0Y9AOfuyJlUXW0eC; attributes={"GlobalId": {"value": "1B71KP0Y9AOfuyJlUXW0eC"}}
  IfcType = 166
  Joint = 0
  Length = 2500
  MakeBlocks = false
  Material = -> Material
  MoveBase = false
  MoveWithHost = false
  Normal = (0,0,0)
  OffsetFirst = 0
  OffsetSecond = 0
  PerimeterLength = 5300
  Placement = pos=(0,0,6220) rot=(0,0,1;0rad)
  PredefinedType = 0
  VerticalArea = 1060000
  Width = 150
FEATURE [Part::Part2DObjectPython] Line2042  # Draft 2D object (typed FeaturePython)
  Area = 0
  ChamferSize = 0
  Closed = true
  End = (2285,5360,0)
  FilletRadius = 0
  Length = 6000
  MakeFace = true
  Placement = pos=(-211.102,-345,0) rot=(0,0,1;0rad)
  Points = (2) [(8496.1,5705,0),(2496.1,5705,0)]
  Start = (8285,5360,0)
  Subdivisions = 0
FEATURE [Part::FeaturePython] Wall559  label="прогон 004"  # Arch/BIM 166 (typed FeaturePython)
  Align = 2
  Area = 1200000
  Base = -> Line2042
  BlockHeight = 0
  BlockLength = 0
  CountBroken = 0
  CountEntire = 0
  Face = 0
  GlobalId = 1B71KP0Y9AOfuyJlUXW0eC
  Height = 200
  HorizontalArea = 900000
  IfcData = IfcUID=1B71KP0Y9AOfuyJlUXW0eC; attributes={"GlobalId": {"value": "1B71KP0Y9AOfuyJlUXW0eC"}}
  IfcType = 166
  Joint = 0
  Length = 6000
  MakeBlocks = false
  Material = -> Material
  MoveBase = false
  MoveWithHost = false
  Normal = (0,0,0)
  Offset = 15
  OffsetFirst = 0
  OffsetSecond = 0
  PerimeterLength = 12300
  Placement = pos=(0,0,6070) rot=(0,0,1;0rad)
  PredefinedType = 0
  VerticalArea = 2460000
  Width = 150
FEATURE [Part::FeaturePython] Structure621  label="Проём-Д90-027"  # Arch/BIM 52 (typed FeaturePython)
  Base = -> Rectangle2807
  FaceMaker = 0
  Height = 2340
  HorizontalArea = 455300
  IfcData = complex_attributes={"OwnerHistory": {}, "IsNestedBy": {}, "IsDecomposedBy": {}, "IsDefinedBy": {}, "ObjectPlacement": {}, "Representation":... (+4 chars omitted)
  IfcType = 52
  Length = 0
  MoveBase = false
  MoveWithHost = false
  Nodes = (2) [(650,-4000,0),(650,-4000,2250)]
  NodesOffset = 0
  Normal = (0,0,0)
  PerimeterLength = 3720
  Placement = pos=(0,0,-200) rot=(0,0,1;0rad)
  VerticalArea = 8704800
  Width = 100
FEATURE [Part::FeaturePython] Structure622  label="Проём-Д90-028"  # Arch/BIM 52 (typed FeaturePython)
  Base = -> Rectangle2795
  FaceMaker = 0
  Height = 2335
  HorizontalArea = 138000
  IfcData = complex_attributes={"OwnerHistory": {}, "IsNestedBy": {}, "IsDecomposedBy": {}, "IsDefinedBy": {}, "ObjectPlacement": {}, "Representation":... (+4 chars omitted)
  IfcType = 52
  Length = 0
  MoveBase = false
  MoveWithHost = false
  Nodes = (2) [(8900,5350,0),(8900,5350,2180)]
  NodesOffset = 0
  Normal = (0,0,0)
  PerimeterLength = 2140
  Placement = pos=(0,0,-200) rot=(0,0,1;0rad)
  VerticalArea = 4996900
  Width = 100
FEATURE [Part::FeaturePython] Structure623  label="Проём-ПР355"  # Arch/BIM 52 (typed FeaturePython)
  Base = -> Rectangle3095
  FaceMaker = 0
  Height = 2780
  HorizontalArea = 769950
  IfcData = complex_attributes={"OwnerHistory": {}, "IsNestedBy": {}, "IsDecomposedBy": {}, "IsDefinedBy": {}, "ObjectPlacement": {}, "Representation":... (+4 chars omitted)
  IfcType = 52
  Length = 0
  MoveBase = false
  MoveWithHost = false
  Nodes = (2) [(8200,3800,0),(8200,3800,2250)]
  NodesOffset = 0
  Normal = (0,0,0)
  PerimeterLength = 5890
  Placement = pos=(0,0,-200) rot=(0,0,1;0rad)
  VerticalArea = 16374200
  Width = 100
FEATURE [Part::FeaturePython] Structure624  label="Проём-ПР356"  # Arch/BIM 52 (typed FeaturePython)
  FaceMaker = 0
  Height = 2780
  HorizontalArea = 235500
  IfcData = complex_attributes={"OwnerHistory": {}, "IsNestedBy": {}, "IsDecomposedBy": {}, "IsDefinedBy": {}, "ObjectPlacement": {}, "Representation":... (+4 chars omitted)
  IfcType = 52
  Length = 0
  MoveBase = false
  MoveWithHost = false
  Nodes = (2) [(8200,3800,0),(8200,3800,2250)]
  NodesOffset = 0
  Normal = (0,0,0)
  PerimeterLength = 3440
  Placement = pos=(0,0,-200) rot=(0,0,1;0rad)
  VerticalArea = 9563200
  Width = 100
FEATURE [Part::FeaturePython] Structure625  label="Вентстояк вычитаемы объём 010"  # Arch/BIM 52 (typed FeaturePython)
  FaceMaker = 0
  GlobalId = 0eTNl8duH9Xv7LHx2JWCfz
  Height = 3350
  HorizontalArea = 60000
  IfcData = IfcUID=0eTNl8duH9Xv7LHx2JWCfz,attributes={"GlobalId": {"value": "0eTNl8duH9Xv7LHx2JWCfz"}},+1 more (map truncated)
  IfcType = 52
  Length = 0
  MoveBase = false
  MoveWithHost = false
  Nodes = (2) [(4985,3930,0),(4985,3930,6000)]
  NodesOffset = 0
  Normal = (0,0,0)
  PerimeterLength = 1100
  Placement = pos=(0,0,-200) rot=(0,0,1;0rad)
  VerticalArea = 3685000
  Width = 100
FEATURE [Part::FeaturePython] Wall560  label="Несущая стена 2.1нф 250мм внутренняя001 вычет"  # Arch/BIM 166 (typed FeaturePython)
  Align = 2
  Area = 2.0445e+07
  Base = -> Line1049
  BlockHeight = 140
  BlockLength = 0
  CountBroken = 0
  CountEntire = 0
  Face = 0
  GlobalId = 1uw9ZyZ5vAkuN6nr$sWkBP
  Height = 3000
  HorizontalArea = 1.70375e+06
  IfcData = IfcUID=1uw9ZyZ5vAkuN6nr$sWkBP; attributes={"GlobalId": {"value": "1uw9ZyZ5vAkuN6nr$sWkBP"}}
  IfcType = 166
  Joint = 10
  Length = 6815
  MakeBlocks = false
  Material = -> Material009
  MoveBase = false
  MoveWithHost = false
  Normal = (0,0,-1)
  OffsetFirst = 0
  OffsetSecond = 500
  PerimeterLength = 14130
  Placement = pos=(0,0,2800) rot=(0,0,1;0rad)
  PredefinedType = 0
  Subtractions = -> [Structure622,Structure623,Structure621,Structure624,Structure625]
  VerticalArea = 2.28406e+07
  Width = 250
FEATURE [Part::Part2DObjectPython] Rectangle3833  # Draft 2D object (typed FeaturePython)
  ChamferSize = 0
  Columns = 1
  FilletRadius = 0
  Height = 1040
  Length = 1110
  MakeFace = false
  Placement = pos=(6835,5575,0) rot=(0,0,1;3.14159rad)
  Rows = 1
FEATURE [TechDraw::DrawSVGTemplate] Template008
  EditableTexts = Лист=8; Номер=ИЖС-2022.0003
  Height = 297
  Orientation = 1
  Width = 420
FEATURE [TechDraw::DrawSVGTemplate] Template009
  EditableTexts = Лист=9; Номер=ИЖС-2022.0003
  Height = 297
  Orientation = 1
  Width = 420
FEATURE [Part::Part2DObjectPython] Rectangle3836  label="ОК-66-003"  # Draft 2D object (typed FeaturePython)
  ChamferSize = 0
  Columns = 1
  FilletRadius = 0
  Height = 410
  Length = 660
  MakeFace = true
  Placement = pos=(7165,-435,0) rot=(0,0,1;0rad)
  Rows = 1
FEATURE [Part::Part2DObjectPython] Rectangle3837  label="ОК-66-004"  # Draft 2D object (typed FeaturePython)
  ChamferSize = 0
  Columns = 1
  FilletRadius = 0
  Height = 410
  Length = 660
  MakeFace = true
  Placement = pos=(2745,-435,0) rot=(0,0,1;0rad)
  Rows = 1
FEATURE [Part::Part2DObjectPython] Rectangle3838  # Draft 2D object (typed FeaturePython)
  ChamferSize = 0
  Columns = 1
  FilletRadius = 50
  Height = 500
  Length = 400
  MakeFace = false
  Placement = pos=(10100,1785,0) rot=(0,0,1;0rad)
  Rows = 1
FEATURE [Part::Extrusion] Extrude057  label="мойка_вырез"
  Base = -> Rectangle3838
  Dir = (0,0,1)
  DirMode = 0
  FaceMakerClass = Part::FaceMakerBullseye
  LengthFwd = 150
  LengthRev = 0
  Placement = pos=(0,0,700) rot=(0,0,1;0rad)
  Solid = true
  Symmetric = false
FEATURE [Part::Part2DObjectPython] Rectangle3839  label="четверть_530-005"  # Draft 2D object (typed FeaturePython)
  ChamferSize = 0
  Columns = 1
  FilletRadius = 0
  Height = 120
  Length = 530
  MakeFace = true
  Placement = pos=(2810,-555,0) rot=(0,0,1;0rad)
  Rows = 1
FEATURE [Part::FeaturePython] Structure426  label="Проём_четв._048"  # Arch/BIM 52 (typed FeaturePython)
  Base = -> Rectangle3839
  FaceMaker = 0
  Height = 1540
  HorizontalArea = 63600
  IfcData = complex_attributes={"OwnerHistory": {}, "IsNestedBy": {}, "IsDecomposedBy": {}, "IsDefinedBy": {}, "ObjectPlacement": {}, "Representation":... (+4 chars omitted)
  IfcType = 52
  Length = 0
  MoveBase = false
  MoveWithHost = false
  Nodes = (2) [(4618,-450,0),(4618,-450,1320)]
  NodesOffset = 0
  Normal = (0,0,0)
  PerimeterLength = 1300
  Placement = pos=(0,0,955) rot=(0,0,1;0rad)
  VerticalArea = 2002000
  Width = 100
FEATURE [Part::Part2DObjectPython] Rectangle3841  label="четверть_183-004"  # Draft 2D object (typed FeaturePython)
  ChamferSize = 0
  Columns = 1
  FilletRadius = 0
  Height = 120
  Length = 920
  MakeFace = true
  Placement = pos=(5550,-435,0) rot=(0,0,1;3.14159rad)
  Rows = 1
FEATURE [Part::FeaturePython] Structure148  label="Проём_четв._031"  # Arch/BIM 52 (typed FeaturePython)
  Base = -> Rectangle3841
  FaceMaker = 0
  Height = 2535
  HorizontalArea = 110400
  IfcData = complex_attributes={"OwnerHistory": {}, "IsNestedBy": {}, "IsDecomposedBy": {}, "IsDefinedBy": {}, "ObjectPlacement": {}, "Representation":... (+4 chars omitted)
  IfcType = 52
  Length = 0
  MoveBase = false
  MoveWithHost = false
  Nodes = (2) [(5775,-395,0),(5775,-395,2335)]
  NodesOffset = 0
  Normal = (0,0,0)
  PerimeterLength = 2080
  Placement = pos=(0,0,-40) rot=(0,0,1;0rad)
  VerticalArea = 5272800
  Width = 100
FEATURE [Part::Part2DObjectPython] Rectangle3842  label="четверть_790-006"  # Draft 2D object (typed FeaturePython)
  ChamferSize = 0
  Columns = 1
  FilletRadius = 0
  Height = 120
  Length = 1570
  MakeFace = true
  Placement = pos=(11010,5175,0) rot=(0,0,-1;1.5708rad)
  Rows = 1
FEATURE [Part::FeaturePython] Structure432  label="Проём_четв._053"  # Arch/BIM 52 (typed FeaturePython)
  Base = -> Rectangle3842
  FaceMaker = 0
  Height = 1540
  HorizontalArea = 188400
  IfcData = complex_attributes={"OwnerHistory": {}, "IsNestedBy": {}, "IsDecomposedBy": {}, "IsDefinedBy": {}, "ObjectPlacement": {}, "Representation":... (+4 chars omitted)
  IfcType = 52
  Length = 0
  MoveBase = false
  MoveWithHost = false
  Nodes = (2) [(1035,460,0),(1035,460,535)]
  NodesOffset = 0
  Normal = (0,0,0)
  PerimeterLength = 3380
  Placement = pos=(0,0,955) rot=(0,0,1;0rad)
  VerticalArea = 5.2052e+06
  Width = 100
FEATURE [Part::Part2DObjectPython] Rectangle3843  label="четверть_530-006"  # Draft 2D object (typed FeaturePython)
  ChamferSize = 0
  Columns = 1
  FilletRadius = 0
  Height = 120
  Length = 530
  MakeFace = true
  Placement = pos=(7230,-555,0) rot=(0,0,1;0rad)
  Rows = 1
FEATURE [Part::FeaturePython] Structure428  label="Проём_четв._050"  # Arch/BIM 52 (typed FeaturePython)
  Base = -> Rectangle3843
  FaceMaker = 0
  Height = 1540
  HorizontalArea = 63600
  IfcData = complex_attributes={"OwnerHistory": {}, "IsNestedBy": {}, "IsDecomposedBy": {}, "IsDefinedBy": {}, "ObjectPlacement": {}, "Representation":... (+4 chars omitted)
  IfcType = 52
  Length = 0
  MoveBase = false
  MoveWithHost = false
  Nodes = (2) [(5775,-395,0),(5775,-395,2335)]
  NodesOffset = 0
  Normal = (0,0,0)
  PerimeterLength = 1300
  Placement = pos=(0,0,955) rot=(0,0,1;0rad)
  VerticalArea = 2002000
  Width = 100
FEATURE [Part::Part2DObjectPython] Rectangle3847  label="Д80-008"  # Draft 2D object (typed FeaturePython)
  ChamferSize = 0
  Columns = 1
  FilletRadius = 0
  Height = 110
  Length = 900
  MakeFace = true
  Placement = pos=(6105,975,0) rot=(0,0,-1;1.5708rad)
  Rows = 1
FEATURE [Part::FeaturePython] Structure543  label="Проём-Д90-022"  # Arch/BIM 52 (typed FeaturePython)
  Base = -> Rectangle3847
  FaceMaker = 0
  Height = 2400
  HorizontalArea = 99000
  IfcData = complex_attributes={"OwnerHistory": {}, "IsNestedBy": {}, "IsDecomposedBy": {}, "IsDefinedBy": {}, "ObjectPlacement": {}, "Representation":... (+4 chars omitted)
  IfcType = 52
  Length = 0
  MoveBase = false
  MoveWithHost = false
  Nodes = (2) [(13000,6050,0),(13000,6050,2180)]
  NodesOffset = 0
  Normal = (0,0,0)
  PerimeterLength = 2020
  VerticalArea = 4.848e+06
  Width = 100
FEATURE [Part::FeaturePython] Wall128  label="перегородка (сил.блок 500х250х80) 003"  # Arch/BIM 166 (typed FeaturePython)
  Align = 2
  Area = 5280000
  Base = -> Line1200
  BlockHeight = 250
  BlockLength = 0
  CountBroken = 0
  CountEntire = 0
  Face = 0
  GlobalId = 239nej2f15XxZ4oxwr6VZE
  Height = 3000
  HorizontalArea = 212800
  IfcData = IfcUID=239nej2f15XxZ4oxwr6VZE; attributes={"GlobalId": {"value": "239nej2f15XxZ4oxwr6VZE"}}
  IfcType = 166
  Joint = 0
  Length = 1760
  MakeBlocks = false
  Material = -> Material009
  MoveBase = false
  MoveWithHost = false
  Normal = (0,0,0)
  OffsetFirst = 300
  OffsetSecond = 50
  PerimeterLength = 3680
  Placement = pos=(0,0,-200) rot=(0,0,1;0rad)
  PredefinedType = 0
  Subtractions = -> [Structure543]
  VerticalArea = 7.104e+06
  Width = 80
FEATURE [Part::Part2DObjectPython] Rectangle3848  label="Д90-034"  # Draft 2D object (typed FeaturePython)
  ChamferSize = 0
  Columns = 1
  FilletRadius = 0
  Height = 110
  Length = 900
  MakeFace = true
  Placement = pos=(4160,4425,0) rot=(0,0,1;0rad)
  Rows = 1
FEATURE [Part::FeaturePython] Structure026  label="Проём-Д90-020"  # Arch/BIM 52 (typed FeaturePython)
  Base = -> Rectangle3848
  FaceMaker = 0
  Height = 2400
  HorizontalArea = 99000
  IfcData = complex_attributes={"OwnerHistory": {}, "IsNestedBy": {}, "IsDecomposedBy": {}, "IsDefinedBy": {}, "ObjectPlacement": {}, "Representation":... (+4 chars omitted)
  IfcType = 52
  Length = 0
  MoveBase = false
  MoveWithHost = false
  Nodes = (2) [(13000,6050,0),(13000,6050,2180)]
  NodesOffset = 0
  Normal = (0,0,0)
  PerimeterLength = 2020
  VerticalArea = 4.848e+06
  Width = 100
FEATURE [Part::Part2DObjectPython] Rectangle3850  label="Д90-035"  # Draft 2D object (typed FeaturePython)
  ChamferSize = 0
  Columns = 1
  FilletRadius = 0
  Height = 100
  Length = 900
  MakeFace = true
  Placement = pos=(2535,4425,0) rot=(0,0,1;0rad)
  Rows = 1
FEATURE [Part::FeaturePython] Structure021  label="Проём-Д90-017"  # Arch/BIM 52 (typed FeaturePython)
  Base = -> Rectangle3850
  FaceMaker = 0
  Height = 2400
  HorizontalArea = 90000
  IfcData = complex_attributes={"OwnerHistory": {}, "IsNestedBy": {}, "IsDecomposedBy": {}, "IsDefinedBy": {}, "ObjectPlacement": {}, "Representation":... (+4 chars omitted)
  IfcType = 52
  Length = 0
  MoveBase = false
  MoveWithHost = false
  Nodes = (2) [(7500,3050,0),(7500,3050,2180)]
  NodesOffset = 0
  Normal = (0,0,0)
  PerimeterLength = 2000
  VerticalArea = 4.8e+06
  Width = 100
FEATURE [Part::Part2DObjectPython] Rectangle3851  label="Д90-036"  # Draft 2D object (typed FeaturePython)
  ChamferSize = 0
  Columns = 1
  FilletRadius = 0
  Height = 290
  Length = 920
  MakeFace = true
  Placement = pos=(3825,7365,0) rot=(0,0,1;1.5708rad)
  Rows = 1
FEATURE [Part::Part2DObjectPython] Rectangle3852  label="Д90-037"  # Draft 2D object (typed FeaturePython)
  ChamferSize = 0
  Columns = 1
  FilletRadius = 0
  Height = 110
  Length = 900
  MakeFace = true
  Placement = pos=(3435,3225,0) rot=(0,0,1;3.14159rad)
  Rows = 1
FEATURE [Part::FeaturePython] Structure024  label="Проём-Д90-019"  # Arch/BIM 52 (typed FeaturePython)
  Base = -> Rectangle3852
  FaceMaker = 0
  Height = 2400
  HorizontalArea = 99000
  IfcData = complex_attributes={"OwnerHistory": {}, "IsNestedBy": {}, "IsDecomposedBy": {}, "IsDefinedBy": {}, "ObjectPlacement": {}, "Representation":... (+4 chars omitted)
  IfcType = 52
  Length = 0
  MoveBase = false
  MoveWithHost = false
  Nodes = (2) [(5000,3050,0),(5000,3050,2180)]
  NodesOffset = 0
  Normal = (0,0,0)
  PerimeterLength = 2020
  VerticalArea = 4.848e+06
  Width = 100
FEATURE [Part::FeaturePython] Wall186  label="перегородка (сил.блок 500х250х80) 002"  # Arch/BIM 166 (typed FeaturePython)
  Align = 2
  Area = 3.525e+06
  Base = -> Line1316
  BlockHeight = 250
  BlockLength = 0
  CountBroken = 0
  CountEntire = 0
  Face = 0
  GlobalId = 1Rj7XWwfD1TACQSKytQJ$J
  Height = 3000
  HorizontalArea = 166000
  IfcData = IfcUID=1Rj7XWwfD1TACQSKytQJ$J; attributes={"GlobalId": {"value": "1Rj7XWwfD1TACQSKytQJ$J"}}
  IfcType = 166
  Joint = 0
  Length = 1175
  MakeBlocks = false
  Material = -> Material009
  MoveBase = false
  MoveWithHost = false
  Normal = (0,0,0)
  OffsetFirst = 300
  OffsetSecond = 0
  PerimeterLength = 2510
  Placement = pos=(0,0,-200) rot=(0,0,1;0rad)
  PredefinedType = 0
  Subtractions = -> [Structure024]
  VerticalArea = 3.594e+06
  Width = 80
FEATURE [Part::Part2DObjectPython] Rectangle3854  label="контур по облицовке001"  # Draft 2D object (typed FeaturePython)
  ChamferSize = 0
  Columns = 1
  FilletRadius = 0
  Height = 9480
  Length = 11690
  MakeFace = false
  Placement = pos=(-560,-555,0) rot=(0,0,1;0rad)
  Rows = 1
FEATURE [Part::Part2DObjectPython] Rectangle3855  # Draft 2D object (typed FeaturePython)
  ChamferSize = 0
  Columns = 1
  FilletRadius = 25
  Height = 300
  Length = 2500
  MakeFace = false
  Placement = pos=(10572.1,5743.68,0) rot=(0,0,1;1.5708rad)
  Rows = 1
FEATURE [Part::Part2DObjectPython] Rectangle3856  # Draft 2D object (typed FeaturePython)
  ChamferSize = 0
  Columns = 1
  FilletRadius = 25
  Height = 950
  Length = 2500
  MakeFace = true
  Placement = pos=(10572.1,5743.68,0) rot=(0,0,1;1.5708rad)
  Rows = 1
  Support = -> [Rectangle3855]
FEATURE [Part::Part2DObjectPython] Rectangle3857  # Draft 2D object (typed FeaturePython)
  ChamferSize = 0
  Columns = 1
  FilletRadius = 25
  Height = 950
  Length = 250
  MakeFace = false
  Placement = pos=(10572.1,5743.68,0) rot=(0,0,1;1.5708rad)
  Rows = 1
FEATURE [Part::Part2DObjectPython] Rectangle3858  # Draft 2D object (typed FeaturePython)
  ChamferSize = 0
  Columns = 1
  FilletRadius = 25
  Height = 950
  Length = 250
  MakeFace = false
  Placement = pos=(10572.1,7993.68,0) rot=(0,0,1;1.5708rad)
  Rows = 1
FEATURE [Part::Part2DObjectPython] Rectangle3859  # Draft 2D object (typed FeaturePython)
  ChamferSize = 0
  Columns = 1
  FilletRadius = 25
  Height = 670
  Length = 650
  MakeFace = true
  Placement = pos=(9622.13,7320,0) rot=(0,0,1;1.5708rad)
  Rows = 1
FEATURE [Part::Part2DObjectPython] Rectangle3861  label="четверть_131-003"  # Draft 2D object (typed FeaturePython)
  ChamferSize = 0
  Columns = 1
  FilletRadius = 0
  Height = 120
  Length = 1570
  MakeFace = true
  Placement = pos=(-560,2955,0) rot=(0,0,-1;1.5708rad)
  Rows = 1
FEATURE [Part::FeaturePython] Structure430  label="Проём_четв._051"  # Arch/BIM 52 (typed FeaturePython)
  Base = -> Rectangle3861
  FaceMaker = 0
  Height = 1540
  HorizontalArea = 188400
  IfcData = complex_attributes={"OwnerHistory": {}, "IsNestedBy": {}, "IsDecomposedBy": {}, "IsDefinedBy": {}, "ObjectPlacement": {}, "Representation":... (+4 chars omitted)
  IfcType = 52
  Length = 0
  MoveBase = false
  MoveWithHost = false
  Nodes = (2) [(1035,460,0),(1035,460,535)]
  NodesOffset = 0
  Normal = (0,0,0)
  PerimeterLength = 3380
  Placement = pos=(0,0,955) rot=(0,0,1;0rad)
  VerticalArea = 5205200
  Width = 100
FEATURE [Part::FeaturePython] Wall300  label="облицовка 019"  # Arch/BIM 166 (typed FeaturePython)
  Align = 1
  Area = 34548250
  Base = -> Line1585
  BlockHeight = 67
  BlockLength = 250
  CountBroken = 104
  CountEntire = 1558
  Face = 0
  GlobalId = 2BxWlk8bv7HwfTqswZTI_V
  Height = 3695
  HorizontalArea = 1310400
  IfcData = IfcUID=2BxWlk8bv7HwfTqswZTI_V; attributes={"GlobalId": {"value": "2BxWlk8bv7HwfTqswZTI_V"}}
  IfcType = 166
  Joint = 10
  Length = 9350
  MakeBlocks = false
  Material = -> Material003
  MoveBase = false
  MoveWithHost = false
  Normal = (0,0,0)
  OffsetFirst = 120
  OffsetSecond = 250
  PerimeterLength = 0
  Placement = pos=(0,0,185) rot=(0,0,1;0rad)
  PredefinedType = 0
  Subtractions = -> [Structure430]
  VerticalArea = 6.55173e+07
  Width = 120
FEATURE [Part::Part2DObjectPython] Rectangle3862  # Draft 2D object (typed FeaturePython)
  ChamferSize = 0
  Columns = 1
  FilletRadius = 30
  Height = 800
  Length = 1400
  MakeFace = true
  Placement = pos=(10550,4850,0) rot=(0,0,1;3.14159rad)
  Rows = 1
FEATURE [Part::Part2DObjectPython] Rectangle3863  # Draft 2D object (typed FeaturePython)
  ChamferSize = 0
  Columns = 1
  FilletRadius = 0
  Height = 300
  Length = 480
  MakeFace = true
  Placement = pos=(10440,4050,0) rot=(0,0,1;3.14159rad)
  Rows = 1
FEATURE [Part::Part2DObjectPython] Rectangle3864  # Draft 2D object (typed FeaturePython)
  ChamferSize = 0
  Columns = 1
  FilletRadius = 0
  Height = 300
  Length = 480
  MakeFace = true
  Placement = pos=(10440,5150,0) rot=(0,0,1;3.14159rad)
  Rows = 1
FEATURE [Part::Part2DObjectPython] ShapeString248  # Draft 2D object (typed FeaturePython)
  FontFile = <path>
  Placement = pos=(7663.67,1874.56,0) rot=(0,0,1;0rad)
  Size = 300
  String = *
  Tracking = 0
FEATURE [Part::Part2DObjectPython] ShapeString249  # Draft 2D object (typed FeaturePython)
  FontFile = <path>
  Placement = pos=(8106.61,232.49,0) rot=(0,0,1;0rad)
  Size = 200
  String = СМ
  Tracking = 0
FEATURE [Part::Part2DObjectPython] ShapeString250  # Draft 2D object (typed FeaturePython)
  FontFile = <path>
  Placement = pos=(10388.1,1241.94,0) rot=(0,0,1;1.5708rad)
  Size = 200
  String = ПМ
  Tracking = 0
FEATURE [Part::Part2DObjectPython] Rectangle3865  label="Камин001"  # Draft 2D object (typed FeaturePython)
  Area = 375000
  ChamferSize = 0
  Columns = 1
  FilletRadius = 0
  Height = 500
  Length = 750
  MakeFace = true
  Placement = pos=(7285,2725,0) rot=(0,0,1;0rad)
  Rows = 1
FEATURE [Part::Part2DObjectPython] Circle196  # Draft 2D object (typed FeaturePython)
  Area = 0
  FirstAngle = 0
  LastAngle = 0
  MakeFace = false
  Placement = pos=(10027.9,368.982,0) rot=(0,0,-1;0.785398rad)
  Radius = 75
FEATURE [Part::FeaturePython] Array079  # Draft array (typed FeaturePython)
  Angle = 360
  ArrayType = 0
  Axis = (0,0,1)
  Base = -> Circle196
  Center = (0,0,0)
  Fuse = false
  IntervalAxis = (0,0,0)
  IntervalX = (250,0,0)
  IntervalY = (0,250,0)
  IntervalZ = (0,0,1)
  NumberPolar = 1
  NumberX = 2
  NumberY = 2
  NumberZ = 1
  Placement = pos=(2499.4,7375.61,0) rot=(0,0,-1;0.785398rad)
FEATURE [Part::Extrusion] Extrude058  label="Панель индукционная"
  Base = -> Array079
  Dir = (0,0,1)
  DirMode = 2
  FaceMakerClass = Part::FaceMakerBullseye
  LengthFwd = 50
  LengthRev = 0
  Placement = pos=(0,0,810) rot=(0,0,1;0rad)
  Solid = true
  Symmetric = false
FEATURE [Part::Part2DObjectPython] ShapeString252  # Draft 2D object (typed FeaturePython)
  FontFile = <path>
  Placement = pos=(7503.41,1431.11,0) rot=(0,0,1;0rad)
  Size = 200
  String = ДШ
  Tracking = 0
FEATURE [Part::Part2DObjectPython] Rectangle3867  # Draft 2D object (typed FeaturePython)
  ChamferSize = 0
  Columns = 1
  FilletRadius = 0
  Height = 300
  Length = 480
  MakeFace = true
  Placement = pos=(9760,4050,0) rot=(0,0,1;3.14159rad)
  Rows = 1
FEATURE [Part::Part2DObjectPython] Rectangle3868  # Draft 2D object (typed FeaturePython)
  ChamferSize = 0
  Columns = 1
  FilletRadius = 0
  Height = 300
  Length = 480
  MakeFace = true
  Placement = pos=(9760,5150,0) rot=(0,0,1;3.14159rad)
  Rows = 1
FEATURE [Part::Part2DObjectPython] Line2048  # Draft 2D object (typed FeaturePython)
  Area = 0
  ChamferSize = 0
  Closed = false
  End = (9970,2335,0)
  FilletRadius = 0
  Length = 600
  MakeFace = true
  Placement = pos=(9721.34,1788.95,0) rot=(0,0,1;0.877215rad)
  Points = (2) [(0,0,0),(578.858,157.87,0)]
  Start = (9721.34,1788.95,0)
  Subdivisions = 0
FEATURE [Part::Part2DObjectPython] Rectangle3870  label="Контур_по_кладке002"  # Draft 2D object (typed FeaturePython)
  Area = 0
  ChamferSize = 0
  Columns = 1
  FilletRadius = 0
  Height = 8460
  Length = 10670
  MakeFace = false
  Placement = pos=(-50,-45,0) rot=(0,0,1;0rad)
  Rows = 1
FEATURE [Part::Part2DObjectPython] Rectangle3871  label="ОК-196-004"  # Draft 2D object (typed FeaturePython)
  ChamferSize = 0
  Columns = 1
  FilletRadius = 0
  Height = 410
  Length = 1440
  MakeFace = true
  Placement = pos=(6005,-25,0) rot=(0,0,1;3.14159rad)
  Rows = 1
FEATURE [Part::FeaturePython] Structure069  label="утепление пола в проёмах XPS 100mm 002"  # Arch/BIM 52 (typed FeaturePython)
  Base = -> Rectangle3871
  FaceMaker = 0
  GlobalId = 3Shc3AjDz99AkEi1PjraMs
  Height = 100
  HorizontalArea = 590400
  IfcData = IfcUID=3Shc3AjDz99AkEi1PjraMs,attributes={"GlobalId": {"value": "3Shc3AjDz99AkEi1PjraMs"}},+1 more (map truncated)
  IfcType = 52
  Length = 0
  Material = -> Material002
  MoveBase = false
  MoveWithHost = false
  Nodes = (2) [(-5285,230,0),(-5285,230,100)]
  NodesOffset = 0
  Normal = (0,0,1)
  PerimeterLength = 3700
  Placement = pos=(0,0,-200) rot=(0,0,1;0rad)
  VerticalArea = 370000
  Width = 100
FEATURE [Part::FeaturePython] Structure368  label="Стяжка тёплого пола  80 мм 001"  # Arch/BIM 52 (typed FeaturePython)
  Base = -> Rectangle3871
  FaceMaker = 0
  GlobalId = 22FHYXjNfD0ge3TUS_JU1i
  Height = 80
  HorizontalArea = 590400
  IfcData = IfcUID=22FHYXjNfD0ge3TUS_JU1i,attributes={"GlobalId": {"value": "22FHYXjNfD0ge3TUS_JU1i"}},+1 more (map truncated)
  IfcType = 52
  Length = 0
  Material = -> Material001
  MoveBase = false
  MoveWithHost = false
  Nodes = (2) [(-5285,230,0),(-5285,230,80)]
  NodesOffset = 0
  Normal = (0,0,1)
  PerimeterLength = 3700
  Placement = pos=(0,0,-100) rot=(0,0,1;0rad)
  VerticalArea = 296000
  Width = 100
FEATURE [Part::FeaturePython] Structure374  label="покрытие пола 20мм 001"  # Arch/BIM 52 (typed FeaturePython)
  Base = -> Rectangle3871
  FaceMaker = 0
  GlobalId = 2zjFlxA7P7zeUfdNFV2euI
  Height = 20
  HorizontalArea = 590400
  IfcData = IfcUID=2zjFlxA7P7zeUfdNFV2euI,attributes={"GlobalId": {"value": "2zjFlxA7P7zeUfdNFV2euI"}},+1 more (map truncated)
  IfcType = 52
  Length = 0
  Material = -> Material001
  MoveBase = false
  MoveWithHost = false
  Nodes = (2) [(-5285,230,0),(-5285,230,20)]
  NodesOffset = 0
  Normal = (0,0,1)
  PerimeterLength = 3700
  Placement = pos=(0,0,-20) rot=(0,0,1;0rad)
  VerticalArea = 74000
  Width = 20
FEATURE [Part::Part2DObjectPython] Rectangle3872  label="ОК-92-006"  # Draft 2D object (typed FeaturePython)
  ChamferSize = 0
  Columns = 1
  FilletRadius = 0
  Height = 410
  Length = 1700
  MakeFace = true
  Placement = pos=(10600,5240,0) rot=(0,0,-1;1.5708rad)
  Rows = 1
FEATURE [Part::Part2DObjectPython] Rectangle3873  label="ОК-196-005"  # Draft 2D object (typed FeaturePython)
  ChamferSize = 0
  Columns = 1
  FilletRadius = 0
  Height = 410
  Length = 1180
  MakeFace = true
  Placement = pos=(10600,2640,0) rot=(0,0,-1;1.5708rad)
  Rows = 1
FEATURE [Part::Part2DObjectPython] Rectangle3875  label="ОК-196-006"  # Draft 2D object (typed FeaturePython)
  ChamferSize = 0
  Columns = 1
  FilletRadius = 0
  Height = 410
  Length = 1960
  MakeFace = true
  Placement = pos=(1185,8395,0) rot=(0,0,1;0rad)
  Rows = 1
FEATURE [Part::Part2DObjectPython] Rectangle3877  # Draft 2D object (typed FeaturePython)
  ChamferSize = 0
  Columns = 1
  FilletRadius = 0
  Height = 1710
  Length = 290
  MakeFace = true
  Placement = pos=(6835,5685,0) rot=(0,0,1;0rad)
  Rows = 1
FEATURE [Part::FeaturePython] Structure339  label="Тумба под ТВ"  # Arch/BIM 52 (typed FeaturePython)
  Base = -> Rectangle3877
  FaceMaker = 0
  GlobalId = 02q3nx$AH4fB0PqHacSjsk
  Height = 550
  HorizontalArea = 495900
  IfcData = IfcUID=02q3nx$AH4fB0PqHacSjsk,+2 more (map truncated)
  IfcType = 52
  Length = 0
  Material = -> Material015
  MoveBase = false
  MoveWithHost = false
  Nodes = (2) [(6980,6540,0),(6980,6540,550)]
  NodesOffset = 0
  Normal = (0,0,1)
  PerimeterLength = 4000
  VerticalArea = 2200000
  Width = 100
FEATURE [Part::Part2DObjectPython] Arc151  label="Arc152"  # Draft 2D object (typed FeaturePython)
  Area = 0
  FirstAngle = 90
  LastAngle = 180
  MakeFace = false
  Placement = pos=(3385,3115,0) rot=(0,0,1;1.5708rad)
  Radius = 800
FEATURE [Part::Part2DObjectPython] Arc152  label="Arc153"  # Draft 2D object (typed FeaturePython)
  Area = 0
  FirstAngle = 90
  LastAngle = 180
  MakeFace = true
  Placement = pos=(3395,4525,0) rot=(0,0,1;0rad)
  Radius = 800
FEATURE [Part::Part2DObjectPython] Line2056  # Draft 2D object (typed FeaturePython)
  Area = 0
  ChamferSize = 0
  Closed = false
  End = (3395,4525,0)
  FilletRadius = 0
  Length = 800
  MakeFace = true
  Placement = pos=(3395,5325,0) rot=(0,0,1;0rad)
  Points = (2) [(0,0,0),(0,-800,0)]
  Start = (3395,5325,0)
  Subdivisions = 0
FEATURE [Part::Part2DObjectPython] Arc153  label="Arc154"  # Draft 2D object (typed FeaturePython)
  Area = 0
  FirstAngle = -180
  LastAngle = -90
  MakeFace = true
  Placement = pos=(6105,925,0) rot=(0,0,1;0rad)
  Radius = 800
FEATURE [Part::Part2DObjectPython] Arc154  label="Arc155"  # Draft 2D object (typed FeaturePython)
  Area = 0
  FirstAngle = 180
  LastAngle = 270
  MakeFace = true
  Placement = pos=(5010,4425,0) rot=(0,0,1;0rad)
  Radius = 800
FEATURE [Part::Part2DObjectPython] Line2057  # Draft 2D object (typed FeaturePython)
  Area = 0
  ChamferSize = 0
  Closed = false
  End = (5010,4425,0)
  FilletRadius = 0
  Length = 800
  MakeFace = true
  Placement = pos=(4310,3625,0) rot=(0,0,1;0rad)
  Points = (2) [(700,0,0),(700,800,0)]
  Start = (5010,3625,0)
  Subdivisions = 0
FEATURE [Part::Part2DObjectPython] Line2059  # Draft 2D object (typed FeaturePython)
  Area = 0
  ChamferSize = 0
  Closed = false
  End = (3385,2315,0)
  FilletRadius = 0
  Length = 800
  MakeFace = true
  Placement = pos=(3385,3260,0) rot=(0,0,1;0rad)
  Points = (2) [(0,-145,0),(0,-945,0)]
  Start = (3385,3115,0)
  Subdivisions = 0
FEATURE [Part::Part2DObjectPython] Rectangle3879  label="Контур по блоку ЛСР38 внешний001"  # Draft 2D object (typed FeaturePython)
  Area = 0
  ChamferSize = 0
  Columns = 1
  FilletRadius = 0
  Height = 9220
  Length = 11430
  MakeFace = false
  Placement = pos=(-430,-425,0) rot=(0,0,1;0rad)
  Rows = 1
FEATURE [Part::Part2DObjectPython] Wire1023  # Draft 2D object (typed FeaturePython)
  Area = 0
  ChamferSize = 0
  Closed = true
  End = (4925,8395,0)
  FilletRadius = 0
  Length = 5200
  MakeFace = false
  Placement = pos=(5595,9270,0) rot=(0,0,1;3.14159rad)
  Points = (4) [(-130,875,0),(-130,2675,0),(670,2675,0),(670,875,0)]
  Start = (5725,8395,0)
  Subdivisions = 0
FEATURE [Part::Part2DObjectPython] Wire1024  # Draft 2D object (typed FeaturePython)
  Area = 0
  ChamferSize = 0
  Closed = true
  End = (5000,8295,0)
  FilletRadius = 0
  Length = 4500
  MakeFace = false
  Placement = pos=(5440,9225,0) rot=(0,0,1;3.14159rad)
  Points = (4) [(-210,930,0),(-210,2530,0),(440,2530,0),(440,930,0)]
  Start = (5650,8295,0)
  Subdivisions = 0
FEATURE [Part::Part2DObjectPython] Circle197  # Draft 2D object (typed FeaturePython)
  Area = 0
  FirstAngle = 0
  LastAngle = 0
  MakeFace = false
  Placement = pos=(6505,5055,0) rot=(0,0,1;0rad)
  Radius = 100
FEATURE [Part::Part2DObjectPython] Line2060  # Draft 2D object (typed FeaturePython)
  Area = 0
  ChamferSize = 0
  Closed = false
  End = (6835,5055,0)
  FilletRadius = 0
  Length = 330
  MakeFace = false
  Placement = pos=(6505,5085,0) rot=(0,0,1;0rad)
  Points = (2) [(0,-30,0),(330,-30,0)]
  Start = (6505,5055,0)
  Subdivisions = 0
FEATURE [Part::Part2DObjectPython] Rectangle3881  label="четверть_183-005"  # Draft 2D object (typed FeaturePython)
  ChamferSize = 0
  Columns = 1
  FilletRadius = 0
  Height = 120
  Length = 1830
  MakeFace = true
  Placement = pos=(1250,8805,0) rot=(0,0,1;0rad)
  Rows = 1
FEATURE [Part::FeaturePython] Structure421  label="Проём_четв._045"  # Arch/BIM 52 (typed FeaturePython)
  Base = -> Rectangle3881
  FaceMaker = 0
  Height = 1540
  HorizontalArea = 219600
  IfcData = complex_attributes={"OwnerHistory": {}, "IsNestedBy": {}, "IsDecomposedBy": {}, "IsDefinedBy": {}, "ObjectPlacement": {}, "Representation":... (+4 chars omitted)
  IfcType = 52
  Length = 0
  MoveBase = false
  MoveWithHost = false
  Nodes = (2) [(5775,-395,0),(5775,-395,2335)]
  NodesOffset = 0
  Normal = (0,0,0)
  PerimeterLength = 3900
  Placement = pos=(0,0,955) rot=(0,0,1;0rad)
  VerticalArea = 6.006e+06
  Width = 100
FEATURE [Part::Part2DObjectPython] Rectangle3883  label="четверть_183-006"  # Draft 2D object (typed FeaturePython)
  ChamferSize = 0
  Columns = 1
  FilletRadius = 0
  Height = 120
  Length = 1050
  MakeFace = true
  Placement = pos=(11010,2575,0) rot=(0,0,-1;1.5708rad)
  Rows = 1
FEATURE [Part::FeaturePython] Structure431  label="Проём_четв._052"  # Arch/BIM 52 (typed FeaturePython)
  Base = -> Rectangle3883
  FaceMaker = 0
  Height = 1540
  HorizontalArea = 126000
  IfcData = complex_attributes={"OwnerHistory": {}, "IsNestedBy": {}, "IsDecomposedBy": {}, "IsDefinedBy": {}, "ObjectPlacement": {}, "Representation":... (+4 chars omitted)
  IfcType = 52
  Length = 0
  MoveBase = false
  MoveWithHost = false
  Nodes = (2) [(1035,460,0),(1035,460,535)]
  NodesOffset = 0
  Normal = (0,0,0)
  PerimeterLength = 2340
  Placement = pos=(0,0,955) rot=(0,0,1;0rad)
  VerticalArea = 3.6036e+06
  Width = 100
FEATURE [Part::FeaturePython] Wall305  label="облицовка 020"  # Arch/BIM 166 (typed FeaturePython)
  Align = 1
  Area = 35028600
  Base = -> Line1586
  BlockHeight = 67
  BlockLength = 250
  CountBroken = 144
  CountEntire = 1452
  Face = 0
  GlobalId = 0ylFaZ_Q11vgSu8iyeHdyc
  Height = 3695
  HorizontalArea = 1452000
  IfcData = IfcUID=0ylFaZ_Q11vgSu8iyeHdyc; attributes={"GlobalId": {"value": "0ylFaZ_Q11vgSu8iyeHdyc"}}
  IfcType = 166
  Joint = 10
  Length = 9480
  MakeBlocks = false
  Material = -> Material003
  MoveBase = false
  MoveWithHost = false
  Normal = (0,0,0)
  OffsetFirst = 120
  OffsetSecond = 250
  PerimeterLength = 0
  Placement = pos=(0,0,185) rot=(0,0,1;0rad)
  PredefinedType = 0
  Subtractions = -> [Structure431,Structure432]
  VerticalArea = 63613600
  Width = 120
FEATURE [Part::Part2DObjectPython] Line2061  # Draft 2D object (typed FeaturePython)
  Area = 0
  ChamferSize = 0
  Closed = false
  End = (4675,-555,0)
  FilletRadius = 0
  Length = 800
  MakeFace = true
  Placement = pos=(4675,-1355,0) rot=(0,0,1;1.5708rad)
  Points = (2) [(0,0,0),(800,3.63798e-12,0)]
  Start = (4675,-1355,0)
  Subdivisions = 0
FEATURE [Part::Part2DObjectPython] Arc156  label="Arc157"  # Draft 2D object (typed FeaturePython)
  Area = 0
  FirstAngle = -180
  LastAngle = -90
  MakeFace = true
  Placement = pos=(4675,-555,0) rot=(0,0,1;1.5708rad)
  Radius = 800
FEATURE [Part::Part2DObjectPython] Rectangle3885  # Draft 2D object (typed FeaturePython)
  ChamferSize = 0
  Columns = 1
  FilletRadius = 10
  Height = 1700
  Length = 600
  MakeFace = true
  Placement = pos=(70,3775,0) rot=(0,0,-1;1.5708rad)
  Rows = 1
FEATURE [Sketcher::SketchObject] Sketch413  label="кресло 45'015"
  FullyConstrained = false
  Placement = pos=(935,3128.39,0) rot=(0,0,1;3.14159rad)
  sketch-geometry (11):
    g0: LineSegment StartX=-280 StartY=-350 StartZ=0 EndX=280 EndY=-350 EndZ=0
    g1: LineSegment StartX=330 StartY=-300 StartZ=0 EndX=330 EndY=300 EndZ=0
    g2: LineSegment StartX=280 StartY=350 StartZ=0 EndX=-280 EndY=350 EndZ=0
    g3: LineSegment StartX=-330 StartY=300 StartZ=0 EndX=-330 EndY=-300 EndZ=0
    g4: ArcOfCircle CenterX=-280 CenterY=300 CenterZ=0 NormalX=0 NormalY=0 NormalZ=1 AngleXU=0 Radius=50 StartAngle=1.5708 EndAngle=3.14159
    g5: ArcOfCircle CenterX=280 CenterY=300 CenterZ=0 NormalX=0 NormalY=0 NormalZ=1 AngleXU=0 Radius=50 StartAngle=-9e-16 EndAngle=1.5708
    g6: ArcOfCircle CenterX=280 CenterY=-300 CenterZ=0 NormalX=0 NormalY=0 NormalZ=1 AngleXU=0 Radius=50 StartAngle=4.71239 EndAngle=6.28319
    g7: ArcOfCircle CenterX=-280 CenterY=-300 CenterZ=0 NormalX=0 NormalY=0 NormalZ=1 AngleXU=0 Radius=50 StartAngle=3.14159 EndAngle=4.71239
    g8: LineSegment StartX=-330 StartY=200 StartZ=0 EndX=330 EndY=200 EndZ=0
    g9: LineSegment StartX=-230 StartY=200 StartZ=0 EndX=-230 EndY=-350 EndZ=0
    g10: LineSegment StartX=230 StartY=200 StartZ=0 EndX=230 EndY=-350 EndZ=0
  constraints (29):
    c: Horizontal(g0)
    c: Vertical(g1)
    c: Vertical(g3)
    c: Tangent(g2,g4) = -1.5708
    c: Tangent(g3,g4) = -1.5708
    c: Tangent(g2,g5) = -1.5708
    c: Tangent(g1,g5) = -1.5708
    c: Tangent(g0,g6) = -1.5708
    c: Tangent(g1,g6) = -1.5708
    c: Tangent(g3,g7) = -1.5708
    c: Tangent(g0,g7) = -1.5708
    c: DistanceY(g0,g2) = 700
    c: DistanceX(g3,g1) = 660
    c: Equal(g4,g5)
    c: Equal(g7,g6)
    c: Radius(g5) = 50
    c: Symmetric(g2,g2,g-2)
    c: Symmetric(g2,g0,g-1)
    c: PointOnObject(g8,g3)
    c: PointOnObject(g8,g1)
    c: Horizontal(g8)
    c: DistanceY(g8,g2) = 150
    c: PointOnObject(g9,g8)
    c: PointOnObject(g9,g0)
    c: Vertical(g9)
    c: PointOnObject(g10,g0)
    c: Vertical(g10)
    c: DistanceX(g10,g8) = 100
    c: Symmetric(g10,g9,g-2)
FEATURE [Part::Part2DObjectPython] Rectangle3886  label="Шкаф 60 043"  # Draft 2D object (typed FeaturePython)
  Area = 0
  ChamferSize = 0
  Columns = 1
  FilletRadius = 0
  Height = 600
  Length = 600
  MakeFace = false
  Placement = pos=(8035,-25,0) rot=(0,0,1;0rad)
  Rows = 1
FEATURE [Part::Part2DObjectPython] Rectangle3887  label="TV 65" 002"  # Draft 2D object (typed FeaturePython)
  ChamferSize = 0
  Columns = 1
  FilletRadius = 0
  Height = 1450
  Length = 75
  MakeFace = false
  Placement = pos=(6980,7265,0) rot=(0,0,1;3.14159rad)
  Rows = 1
FEATURE [Part::Part2DObjectPython] Rectangle3888  # Draft 2D object (typed FeaturePython)
  Area = 126000
  ChamferSize = 0
  Columns = 1
  FilletRadius = 0
  Height = 150
  Length = 840
  MakeFace = true
  Placement = pos=(6205,1575,0) rot=(0,0,1;0rad)
  Rows = 1
FEATURE [Part::Part2DObjectPython] Rectangle3890  label="отделка инсталляции 004"  # Draft 2D object (typed FeaturePython)
  Area = 55000
  ChamferSize = 0
  Columns = 1
  FilletRadius = 0
  Height = 1100
  Length = 50
  MakeFace = true
  Placement = pos=(7875,-25,0) rot=(0,0,1;0rad)
  Rows = 1
FEATURE [Part::Part2DObjectPython] Rectangle3895  # Draft 2D object (typed FeaturePython)
  Area = 10000
  ChamferSize = 0
  Columns = 1
  FilletRadius = 0
  Height = 100
  Length = 100
  MakeFace = true
  Placement = pos=(3435,4425,0) rot=(0,0,1;0rad)
  Rows = 1
FEATURE [Part::Part2DObjectPython] Rectangle3896  # Draft 2D object (typed FeaturePython)
  Area = 98600
  ChamferSize = 0
  Columns = 1
  FilletRadius = 0
  Height = 340
  Length = 290
  MakeFace = true
  Placement = pos=(3535,4425,0) rot=(0,0,1;0rad)
  Rows = 1
FEATURE [Part::Part2DObjectPython] Rectangle3897  # Draft 2D object (typed FeaturePython)
  Area = 66000
  ChamferSize = 0
  Columns = 1
  FilletRadius = 0
  Height = 600
  Length = 110
  MakeFace = true
  Placement = pos=(6105,975,0) rot=(0,0,1;0rad)
  Rows = 1
FEATURE [Part::Part2DObjectPython] Rectangle3898  # Draft 2D object (typed FeaturePython)
  Area = 11000
  ChamferSize = 0
  Columns = 1
  FilletRadius = 0
  Height = 100
  Length = 110
  MakeFace = true
  Placement = pos=(6105,-25,0) rot=(0,0,1;0rad)
  Rows = 1
FEATURE [Part::Part2DObjectPython] Rectangle3899  # Draft 2D object (typed FeaturePython)
  Area = 36850
  ChamferSize = 0
  Columns = 1
  FilletRadius = 0
  Height = 110
  Length = 335
  MakeFace = true
  Placement = pos=(3825,4425,0) rot=(0,0,1;0rad)
  Rows = 1
FEATURE [Part::Part2DObjectPython] Rectangle3900  # Draft 2D object (typed FeaturePython)
  Area = 1.27e+06
  ChamferSize = 0
  Columns = 1
  FilletRadius = 0
  Height = 400
  Length = 3175
  MakeFace = true
  Placement = pos=(-430,-425,0) rot=(0,0,1;0rad)
  Rows = 1
FEATURE [Part::Part2DObjectPython] Rectangle3901  # Draft 2D object (typed FeaturePython)
  Area = 646000
  ChamferSize = 0
  Columns = 1
  FilletRadius = 0
  Height = 400
  Length = 1615
  MakeFace = true
  Placement = pos=(-430,8395,0) rot=(0,0,1;0rad)
  Rows = 1
FEATURE [Part::Part2DObjectPython] Rectangle3902  # Draft 2D object (typed FeaturePython)
  Area = 538000
  ChamferSize = 0
  Columns = 1
  FilletRadius = 0
  Height = 1345
  Length = 400
  MakeFace = true
  Placement = pos=(-430,-25,0) rot=(0,0,1;0rad)
  Rows = 1
FEATURE [Part::Part2DObjectPython] Rectangle3903  # Draft 2D object (typed FeaturePython)
  Area = 594000
  ChamferSize = 0
  Columns = 1
  FilletRadius = 0
  Height = 1485
  Length = 400
  MakeFace = true
  Placement = pos=(10600,-25,0) rot=(0,0,1;0rad)
  Rows = 1
FEATURE [Part::Part2DObjectPython] Rectangle3904  # Draft 2D object (typed FeaturePython)
  Area = 226200
  ChamferSize = 0
  Columns = 1
  FilletRadius = 0
  Height = 290
  Length = 780
  MakeFace = true
  Placement = pos=(9820,2935,0) rot=(0,0,1;0rad)
  Rows = 1
FEATURE [Part::Part2DObjectPython] Rectangle3905  # Draft 2D object (typed FeaturePython)
  Area = 56100
  ChamferSize = 0
  Columns = 1
  FilletRadius = 0
  Height = 110
  Length = 510
  MakeFace = true
  Placement = pos=(7415,1075,0) rot=(0,0,1;0rad)
  Rows = 1
FEATURE [Part::Part2DObjectPython] Rectangle3906  # Draft 2D object (typed FeaturePython)
  Area = 110000
  ChamferSize = 0
  Columns = 1
  FilletRadius = 0
  Height = 110
  Length = 1000
  MakeFace = true
  Placement = pos=(5835,5575,0) rot=(0,0,1;0rad)
  Rows = 1
FEATURE [Part::Part2DObjectPython] Rectangle3907  # Draft 2D object (typed FeaturePython)
  Area = 942500
  ChamferSize = 0
  Columns = 1
  FilletRadius = 0
  Height = 290
  Length = 3250
  MakeFace = true
  Placement = pos=(3825,-25,0) rot=(0,0,1;1.5708rad)
  Rows = 1
FEATURE [Part::Part2DObjectPython] Rectangle3908  # Draft 2D object (typed FeaturePython)
  Area = 188500
  ChamferSize = 0
  Columns = 1
  FilletRadius = 0
  Height = 290
  Length = 650
  MakeFace = true
  Placement = pos=(3825,2935,0) rot=(0,0,1;0rad)
  Rows = 1
FEATURE [Part::Part2DObjectPython] Rectangle3911  # Draft 2D object (typed FeaturePython)
  Area = 310200
  ChamferSize = 0
  Columns = 1
  FilletRadius = 0
  Height = 2820
  Length = 110
  MakeFace = true
  Placement = pos=(5725,5575,0) rot=(0,0,1;0rad)
  Rows = 1
FEATURE [Part::Part2DObjectPython] Rectangle3912  # Draft 2D object (typed FeaturePython)
  ChamferSize = 0
  Columns = 1
  FilletRadius = 0
  Height = 600
  Length = 600
  MakeFace = false
  Placement = pos=(9607.87,542.868,0) rot=(0,0,-1;0.785398rad)
  Rows = 1
FEATURE [Part::Part2DObjectPython] Rectangle3913  # Draft 2D object (typed FeaturePython)
  ChamferSize = 0
  Columns = 1
  FilletRadius = 0
  Height = 600
  Length = 600
  MakeFace = false
  Placement = pos=(7435,1185,0) rot=(0,0,1;0rad)
  Rows = 1
FEATURE [Part::Part2DObjectPython] Rectangle3915  # Draft 2D object (typed FeaturePython)
  ChamferSize = 0
  Columns = 1
  FilletRadius = 0
  Height = 1350
  Length = 600
  MakeFace = true
  Placement = pos=(7435,1185,0) rot=(0,0,1;0rad)
  Rows = 1
FEATURE [Part::Part2DObjectPython] Rectangle3918  label="четверть_530-007"  # Draft 2D object (typed FeaturePython)
  ChamferSize = 0
  Columns = 1
  FilletRadius = 0
  Height = 120
  Length = 390
  MakeFace = true
  Placement = pos=(5550,-555,0) rot=(0,0,1;0rad)
  Rows = 1
FEATURE [Part::FeaturePython] Structure489  label="Проём_четв._055"  # Arch/BIM 52 (typed FeaturePython)
  Base = -> Rectangle3918
  FaceMaker = 0
  Height = 2535
  HorizontalArea = 46800
  IfcData = complex_attributes={"OwnerHistory": {}, "IsNestedBy": {}, "IsDecomposedBy": {}, "IsDefinedBy": {}, "ObjectPlacement": {}, "Representation":... (+4 chars omitted)
  IfcType = 52
  Length = 0
  MoveBase = false
  MoveWithHost = false
  Nodes = (2) [(5775,-395,0),(5775,-395,2335)]
  NodesOffset = 0
  Normal = (0,0,0)
  PerimeterLength = 1020
  Placement = pos=(0,0,-40) rot=(0,0,1;0rad)
  VerticalArea = 2585700
  Width = 100
FEATURE [Part::FeaturePython] Wall299  label="облицовка 018"  # Arch/BIM 166 (typed FeaturePython)
  Align = 0
  Area = 42233850
  Base = -> Line1584
  BlockHeight = 67
  BlockLength = 250
  CountBroken = 162
  CountEntire = 1779
  Face = 0
  GlobalId = 3SgCB7ImHBKRjTRpndNtdS
  Height = 3695
  HorizontalArea = 1498800
  IfcData = IfcUID=3SgCB7ImHBKRjTRpndNtdS; attributes={"GlobalId": {"value": "3SgCB7ImHBKRjTRpndNtdS"}}
  IfcType = 166
  Joint = 10
  Length = 11430
  MakeBlocks = false
  Material = -> Material003
  MoveBase = false
  MoveWithHost = false
  Normal = (0,0,0)
  OffsetFirst = 120
  OffsetSecond = 250
  PerimeterLength = 0
  Placement = pos=(0,0,185) rot=(0,0,1;0rad)
  PredefinedType = 0
  Subtractions = -> [Structure426,Structure428,Structure148,Structure489]
  VerticalArea = 77331100
  Width = 120
FEATURE [Part::Part2DObjectPython] Rectangle3922  # Draft 2D object (typed FeaturePython)
  Area = 0
  ChamferSize = 0
  Columns = 1
  FilletRadius = 0
  Height = 550
  Length = 600
  MakeFace = false
  Placement = pos=(10000,2335,0) rot=(0,0,1;1.5708rad)
  Rows = 1
FEATURE [Part::Part2DObjectPython] Rectangle3924  # Draft 2D object (typed FeaturePython)
  ChamferSize = 0
  Columns = 1
  FilletRadius = 0
  Height = 1040
  Length = 1110
  MakeFace = true
  Placement = pos=(6835,5575,0) rot=(0,0,1;3.14159rad)
  Rows = 1
FEATURE [Part::Part2DObjectPython] Rectangle3925  # Draft 2D object (typed FeaturePython)
  Area = 2150000
  ChamferSize = 0
  Columns = 1
  FilletRadius = 0
  Height = 5375
  Length = 400
  MakeFace = true
  Placement = pos=(-430,3020,0) rot=(0,0,1;0rad)
  Rows = 1
FEATURE [Part::Part2DObjectPython] Rectangle3926  # Draft 2D object (typed FeaturePython)
  Area = 308000
  ChamferSize = 0
  Columns = 1
  FilletRadius = 0
  Height = 400
  Length = 770
  MakeFace = true
  Placement = pos=(3145,8395,0) rot=(0,0,1;0rad)
  Rows = 1
FEATURE [Part::Part2DObjectPython] Rectangle3927  # Draft 2D object (typed FeaturePython)
  Area = 1036000
  ChamferSize = 0
  Columns = 1
  FilletRadius = 0
  Height = 400
  Length = 2590
  MakeFace = true
  Placement = pos=(4835,8395,0) rot=(0,0,1;0rad)
  Rows = 1
FEATURE [Part::Part2DObjectPython] Rectangle3928  # Draft 2D object (typed FeaturePython)
  Area = 360000
  ChamferSize = 0
  Columns = 1
  FilletRadius = 0
  Height = 900
  Length = 400
  MakeFace = true
  Placement = pos=(10600,2640,0) rot=(0,0,1;0rad)
  Rows = 1
FEATURE [Part::Part2DObjectPython] Rectangle3929  # Draft 2D object (typed FeaturePython)
  Area = 464000
  ChamferSize = 0
  Columns = 1
  FilletRadius = 0
  Height = 400
  Length = 1160
  MakeFace = true
  Placement = pos=(3405,-425,0) rot=(0,0,1;0rad)
  Rows = 1
FEATURE [Part::Part2DObjectPython] Rectangle3930  # Draft 2D object (typed FeaturePython)
  Area = 464000
  ChamferSize = 0
  Columns = 1
  FilletRadius = 0
  Height = 400
  Length = 1160
  MakeFace = true
  Placement = pos=(6005,-425,0) rot=(0,0,1;0rad)
  Rows = 1
FEATURE [Part::Part2DObjectPython] Rectangle3931  # Draft 2D object (typed FeaturePython)
  Area = 1.27e+06
  ChamferSize = 0
  Columns = 1
  FilletRadius = 0
  Height = 400
  Length = 3175
  MakeFace = true
  Placement = pos=(7825,-425,0) rot=(0,0,1;0rad)
  Rows = 1
FEATURE [Part::Part2DObjectPython] Rectangle3932  # Draft 2D object (typed FeaturePython)
  Area = 333500
  ChamferSize = 0
  Columns = 1
  FilletRadius = 0
  Height = 1150
  Length = 290
  MakeFace = true
  Placement = pos=(6835,4535,0) rot=(0,0,1;0rad)
  Rows = 1
FEATURE [Part::Part2DObjectPython] Rectangle3933  # Draft 2D object (typed FeaturePython)
  Area = 1262000
  ChamferSize = 0
  Columns = 1
  FilletRadius = 0
  Height = 3155
  Length = 400
  MakeFace = true
  Placement = pos=(10600,5240,0) rot=(0,0,1;0rad)
  Rows = 1
FEATURE [Part::Part2DObjectPython] Rectangle3934  # Draft 2D object (typed FeaturePython)
  Area = 227150
  ChamferSize = 0
  Columns = 1
  FilletRadius = 0
  Height = 110
  Length = 2065
  MakeFace = true
  Placement = pos=(5060,4425,0) rot=(0,0,1;0rad)
  Rows = 1
FEATURE [Part::Part2DObjectPython] Rectangle3935  # Draft 2D object (typed FeaturePython)
  Area = 137854
  ChamferSize = 0
  Columns = 1
  FilletRadius = 50
  Height = 400
  Length = 350
  MakeFace = true
  Placement = pos=(5727.31,1101.01,0) rot=(0,0,1;0rad)
  Rows = 1
FEATURE [Part::Part2DObjectPython] Rectangle3937  # Draft 2D object (typed FeaturePython)
  Area = 240000
  ChamferSize = 0
  Columns = 1
  FilletRadius = 0
  Height = 100
  Length = 2400
  MakeFace = true
  Placement = pos=(-30,3775,0) rot=(0,0,1;0rad)
  Rows = 1
FEATURE [Part::Part2DObjectPython] Rectangle3938  label="Шкаф 60 044"  # Draft 2D object (typed FeaturePython)
  Area = 1.776e+06
  ChamferSize = 0
  Columns = 1
  FilletRadius = 0
  Height = 2960
  Length = 600
  MakeFace = true
  Placement = pos=(3825,-25,0) rot=(0,0,1;0rad)
  Rows = 1
FEATURE [Part::Part2DObjectPython] Rectangle3939  # Draft 2D object (typed FeaturePython)
  Area = 147200
  ChamferSize = 0
  Columns = 1
  FilletRadius = 0
  Height = 920
  Length = 160
  MakeFace = true
  Placement = pos=(3535,4765,0) rot=(0,0,1;0rad)
  Rows = 1
FEATURE [Part::Part2DObjectPython] Line2068  # Draft 2D object (typed FeaturePython)
  Area = 0
  ChamferSize = 0
  Closed = false
  End = (8613.86,762.87,0)
  FilletRadius = 0
  Length = 600
  MakeFace = true
  Placement = pos=(8035,605,0) rot=(0,0,1;0rad)
  Points = (2) [(0,0,0),(578.858,157.87,0)]
  Start = (8035,605,0)
  Subdivisions = 0
FEATURE [Part::Part2DObjectPython] Rectangle3941  # Draft 2D object (typed FeaturePython)
  Area = 12650
  ChamferSize = 0
  Columns = 1
  FilletRadius = 0
  Height = 110
  Length = 115
  MakeFace = true
  Placement = pos=(4475,3115,0) rot=(0,0,1;0rad)
  Rows = 1
FEATURE [Part::Part2DObjectPython] Rectangle3942  # Draft 2D object (typed FeaturePython)
  Area = 220000
  ChamferSize = 0
  Columns = 1
  FilletRadius = 0
  Height = 400
  Length = 550
  MakeFace = true
  Placement = pos=(5175,5825,0) rot=(0,0,1;0rad)
  Rows = 1
FEATURE [Part::Part2DObjectPython] Rectangle3943  # Draft 2D object (typed FeaturePython)
  Area = 220000
  ChamferSize = 0
  Columns = 1
  FilletRadius = 0
  Height = 400
  Length = 550
  MakeFace = true
  Placement = pos=(7875,725,0) rot=(0,0,1;3.14159rad)
  Rows = 1
FEATURE [Part::Part2DObjectPython] Rectangle3944  # Draft 2D object (typed FeaturePython)
  Area = 487200
  ChamferSize = 0
  Columns = 1
  FilletRadius = 0
  Height = 1680
  Length = 290
  MakeFace = true
  Placement = pos=(3535,5685,0) rot=(0,0,1;0rad)
  Rows = 1
FEATURE [Part::Part2DObjectPython] Rectangle3945  label="BACKABRO БАККАБРУ 3-местный диван-кровать, Идекулла синий002"  # Draft 2D object (typed FeaturePython)
  ChamferSize = 0
  Columns = 1
  FilletRadius = 25
  Height = 2090
  Length = 910
  MakeFace = true
  Placement = pos=(125,920,0) rot=(0,0,-1;1.5708rad)
  Rows = 1
FEATURE [Part::Part2DObjectPython] Rectangle3946  # Draft 2D object (typed FeaturePython)
  ChamferSize = 0
  Columns = 1
  FilletRadius = 0
  Height = 1620
  Length = 2070
  MakeFace = false
  Placement = pos=(360,2130,0) rot=(0,0,-1;1.5708rad)
  Rows = 1
FEATURE [Part::Part2DObjectPython] Rectangle3947  # Draft 2D object (typed FeaturePython)
  Area = 96000
  ChamferSize = 0
  Columns = 1
  FilletRadius = 0
  Height = 120
  Length = 800
  MakeFace = true
  Placement = pos=(4925,6475,0) rot=(0,0,1;0rad)
  Rows = 1
FEATURE [Part::Part2DObjectPython] Rectangle3948  label="LACK ЛАКК Тумба под ТВ, 160x35x36 см001"  # Draft 2D object (typed FeaturePython)
  ChamferSize = 0
  Columns = 1
  FilletRadius = 0
  Height = 1600
  Length = 350
  MakeFace = true
  Placement = pos=(3185,5660,0) rot=(0,0,1;0rad)
  Rows = 1
FEATURE [Part::Part2DObjectPython] Rectangle3949  # Draft 2D object (typed FeaturePython)
  Area = 120000
  ChamferSize = 0
  Columns = 1
  FilletRadius = 0
  Height = 1200
  Length = 100
  MakeFace = true
  Placement = pos=(2370,3225,0) rot=(0,0,1;0rad)
  Rows = 1
FEATURE [Part::Part2DObjectPython] Rectangle3950  # Draft 2D object (typed FeaturePython)
  Area = 91300
  ChamferSize = 0
  Columns = 1
  FilletRadius = 0
  Height = 110
  Length = 830
  MakeFace = true
  Placement = pos=(6215,1465,0) rot=(0,0,1;0rad)
  Rows = 1
FEATURE [Part::Part2DObjectPython] Rectangle3952  # Draft 2D object (typed FeaturePython)
  Area = 133100
  ChamferSize = 0
  Columns = 1
  FilletRadius = 0
  Height = 1210
  Length = 110
  MakeFace = true
  Placement = pos=(7925,-25,0) rot=(0,0,1;0rad)
  Rows = 1
FEATURE [Part::Part2DObjectPython] Rectangle3953  # Draft 2D object (typed FeaturePython)
  Area = 62000
  ChamferSize = 0
  Columns = 1
  FilletRadius = 0
  Height = 100
  Length = 620
  MakeFace = true
  Placement = pos=(7415,2555,0) rot=(0,0,1;0rad)
  Rows = 1
FEATURE [Part::Part2DObjectPython] Rectangle3954  # Draft 2D object (typed FeaturePython)
  Area = 18150
  ChamferSize = 0
  Columns = 1
  FilletRadius = 0
  Height = 110
  Length = 165
  MakeFace = true
  Placement = pos=(2370,3115,0) rot=(0,0,1;0rad)
  Rows = 1
FEATURE [Part::Part2DObjectPython] Rectangle3955  # Draft 2D object (typed FeaturePython)
  Area = 7800
  ChamferSize = 0
  Columns = 1
  FilletRadius = 0
  Height = 390
  Length = 20
  MakeFace = true
  Placement = pos=(7035,1075,0) rot=(0,0,1;0rad)
  Rows = 1
FEATURE [Part::Part2DObjectPython] Rectangle3957  # Draft 2D object (typed FeaturePython)
  Area = 16500
  ChamferSize = 0
  Columns = 1
  FilletRadius = 0
  Height = 100
  Length = 165
  MakeFace = true
  Placement = pos=(2370,4425,0) rot=(0,0,1;0rad)
  Rows = 1
FEATURE [Part::Part2DObjectPython] Rectangle3960  # Draft 2D object (typed FeaturePython)
  Area = 28000
  ChamferSize = 0
  Columns = 1
  FilletRadius = 0
  Height = 280
  Length = 100
  MakeFace = true
  Placement = pos=(7045,2655,0) rot=(0,0,1;0rad)
  Rows = 1
FEATURE [Part::Part2DObjectPython] Rectangle3961  # Draft 2D object (typed FeaturePython)
  ChamferSize = 0
  Columns = 1
  FilletRadius = 0
  Height = 1800
  Length = 2100
  MakeFace = true
  Placement = pos=(2085,7360,0) rot=(0,0,1;3.14159rad)
  Rows = 1
FEATURE [Part::Part2DObjectPython] Rectangle3962  # Draft 2D object (typed FeaturePython)
  Area = 0
  ChamferSize = 0
  Columns = 1
  FilletRadius = 0
  Height = 600
  Length = 350
  MakeFace = false
  Placement = pos=(119.996,6560,0) rot=(0,0,1;0rad)
  Rows = 1
FEATURE [Part::Part2DObjectPython] Rectangle3963  # Draft 2D object (typed FeaturePython)
  Area = 0
  ChamferSize = 0
  Columns = 1
  FilletRadius = 0
  Height = 600
  Length = 350
  MakeFace = false
  Placement = pos=(119.996,5780,0) rot=(0,0,1;0rad)
  Rows = 1
FEATURE [Part::Part2DObjectPython] Rectangle3964  # Draft 2D object (typed FeaturePython)
  Area = 160000
  ChamferSize = 0
  Columns = 1
  FilletRadius = 0
  Height = 400
  Length = 400
  MakeFace = true
  Placement = pos=(-15,7375,0) rot=(0,0,1;0rad)
  Rows = 1
FEATURE [Part::Part2DObjectPython] Rectangle3965  # Draft 2D object (typed FeaturePython)
  Area = 160000
  ChamferSize = 0
  Columns = 1
  FilletRadius = 0
  Height = 400
  Length = 400
  MakeFace = true
  Placement = pos=(-15,5145,0) rot=(0,0,1;0rad)
  Rows = 1
FEATURE [Part::Part2DObjectPython] Rectangle3966  label="TV 54" 004"  # Draft 2D object (typed FeaturePython)
  ChamferSize = 0
  Columns = 1
  FilletRadius = 0
  Height = 1200
  Length = 75
  MakeFace = false
  Placement = pos=(3475,7060,0) rot=(0,0,1;3.14159rad)
  Rows = 1
FEATURE [Part::Part2DObjectPython] Rectangle3967  label="Шкаф 60 046"  # Draft 2D object (typed FeaturePython)
  Area = 1440000
  ChamferSize = 0
  Columns = 1
  FilletRadius = 0
  Height = 600
  Length = 2400
  MakeFace = true
  Placement = pos=(-30,3875,0) rot=(0,0,1;0rad)
  Rows = 1
FEATURE [Part::Part2DObjectPython] Rectangle3968  label="Шкаф 60 047"  # Draft 2D object (typed FeaturePython)
  Area = 360000
  ChamferSize = 0
  Columns = 1
  FilletRadius = 0
  Height = 600
  Length = 600
  MakeFace = true
  Placement = pos=(1770,3175,0) rot=(0,0,1;0rad)
  Rows = 1
FEATURE [Part::Part2DObjectPython] Rectangle3971  # Draft 2D object (typed FeaturePython)
  Area = 31900
  ChamferSize = 0
  Columns = 1
  FilletRadius = 0
  Height = 110
  Length = 290
  MakeFace = true
  Placement = pos=(3535,8285,0) rot=(0,0,1;0rad)
  Rows = 1
FEATURE [Part::Part2DObjectPython] Rectangle3972  # Draft 2D object (typed FeaturePython)
  Area = 348000
  ChamferSize = 0
  Columns = 1
  FilletRadius = 0
  Height = 290
  Length = 1200
  MakeFace = true
  Placement = pos=(6005,2935,0) rot=(0,0,1;0rad)
  Rows = 1
FEATURE [Part::Part2DObjectPython] Rectangle3979  # Draft 2D object (typed FeaturePython)
  Area = 0
  ChamferSize = 0
  Columns = 1
  FilletRadius = 0
  Height = 800
  Length = 700
  MakeFace = false
  Placement = pos=(8450,4050,0) rot=(0,0,1;0rad)
  Rows = 1
FEATURE [Part::Part2DObjectPython] Rectangle3980  # Draft 2D object (typed FeaturePython)
  Area = 0
  ChamferSize = 0
  Columns = 1
  FilletRadius = 0
  Height = 300
  Length = 500
  MakeFace = false
  Placement = pos=(8580.5,4850,0) rot=(0,0,1;0rad)
  Rows = 1
FEATURE [Part::Part2DObjectPython] Rectangle3981  # Draft 2D object (typed FeaturePython)
  Area = 0
  ChamferSize = 0
  Columns = 1
  FilletRadius = 0
  Height = 300
  Length = 500
  MakeFace = false
  Placement = pos=(8580.5,3750,0) rot=(0,0,1;0rad)
  Rows = 1
FEATURE [Part::Part2DObjectPython] Rectangle3983  # Draft 2D object (typed FeaturePython)
  ChamferSize = 0
  Columns = 1
  FilletRadius = 0
  Height = 600
  Length = 600
  MakeFace = false
  Placement = pos=(10000,1135,0) rot=(0,0,1;0rad)
  Rows = 1
FEATURE [Part::Part2DObjectPython] Rectangle3984  # Draft 2D object (typed FeaturePython)
  ChamferSize = 0
  Columns = 1
  FilletRadius = 0
  Height = 600
  Length = 600
  MakeFace = false
  Placement = pos=(10000,1735,0) rot=(0,0,1;0rad)
  Rows = 1
FEATURE [Part::Part2DObjectPython] Rectangle3985  # Draft 2D object (typed FeaturePython)
  ChamferSize = 0
  Columns = 1
  FilletRadius = 0
  Height = 600
  Length = 600
  MakeFace = false
  Placement = pos=(10000,2335,0) rot=(0,0,1;0rad)
  Rows = 1
FEATURE [Part::Part2DObjectPython] Rectangle3986  # Draft 2D object (typed FeaturePython)
  Area = 0
  ChamferSize = 0
  Columns = 1
  FilletRadius = 0
  Height = 550
  Length = 600
  MakeFace = false
  Placement = pos=(10000,1135,0) rot=(0,0,1;1.5708rad)
  Rows = 1
FEATURE [Part::Part2DObjectPython] Rectangle3987  # Draft 2D object (typed FeaturePython)
  ChamferSize = 0
  Columns = 1
  FilletRadius = 0
  Height = 600
  Length = 600
  MakeFace = false
  Placement = pos=(7435,1785,0) rot=(0,0,1;0rad)
  Rows = 1
FEATURE [Part::Part2DObjectPython] Rectangle3988  # Draft 2D object (typed FeaturePython)
  Area = 0
  ChamferSize = 0
  Columns = 1
  FilletRadius = 0
  Height = 550
  Length = 600
  MakeFace = false
  Placement = pos=(8585,1185,0) rot=(0,0,1;1.5708rad)
  Rows = 1
FEATURE [Part::Part2DObjectPython] Wire1025  label="гардины 017"  # Draft 2D object (typed FeaturePython)
  Area = 0
  ChamferSize = 0
  Closed = false
  End = (70.7107,3600,0)
  FilletRadius = 50
  Length = 3860.22
  MakeFace = false
  Placement = pos=(70.7107,400,0) rot=(0,0,1;1.5708rad)
  Points = (33) [(0,0,0),(100,100,0),(200,0,0),(300,100,0),(400,0,0),(500,100,0),(600,0,0),(700,100,0),(800,0,0),(900,100,0),(1000,0,0),(1100,100,0),(1200,0,0),+20 more]
  Start = (70.7107,400,0)
  Subdivisions = 0
FEATURE [Part::Part2DObjectPython] Wire1026  label="гардины 018"  # Draft 2D object (typed FeaturePython)
  Area = 0
  ChamferSize = 0
  Closed = false
  End = (10581.6,8300,0)
  FilletRadius = 50
  Length = 3860.22
  MakeFace = false
  Placement = pos=(7381.65,8300,0) rot=(0,0,1;0rad)
  Points = (33) [(0,0,0),(100,100,0),(200,0,0),(300,100,0),(400,0,0),(500,100,0),(600,0,0),(700,100,0),(800,0,0),(900,100,0),(1000,0,0),(1100,100,0),(1200,0,0),+20 more]
  Start = (7381.65,8300,0)
  Subdivisions = 0
FEATURE [Part::Part2DObjectPython] Wire1027  label="гардины 019"  # Draft 2D object (typed FeaturePython)
  Area = 0
  ChamferSize = 0
  Closed = false
  End = (3350,8300,0)
  FilletRadius = 50
  Length = 3860.22
  MakeFace = false
  Placement = pos=(150,8300,0) rot=(0,0,1;0rad)
  Points = (33) [(0,0,0),(100,100,0),(200,0,0),(300,100,0),(400,0,0),(500,100,0),(600,0,0),(700,100,0),(800,0,0),(900,100,0),(1000,0,0),(1100,100,0),(1200,0,0),+20 more]
  Start = (150,8300,0)
  Subdivisions = 0
FEATURE [Part::Part2DObjectPython] Rectangle3993  # Draft 2D object (typed FeaturePython)
  Area = 11000
  ChamferSize = 0
  Columns = 1
  FilletRadius = 0
  Height = 110
  Length = 100
  MakeFace = true
  Placement = pos=(3435,3115,0) rot=(0,0,1;0rad)
  Rows = 1
FEATURE [Part::Part2DObjectPython] Rectangle3994  label="колонна 250мм 025"  # Draft 2D object (typed FeaturePython)
  Area = 584600
  ChamferSize = 0
  Columns = 1
  FilletRadius = 0
  Height = 1580
  Length = 370
  MakeFace = true
  Placement = pos=(7045,1075,0) rot=(0,0,1;0rad)
  Rows = 1
FEATURE [Part::Part2DObjectPython] Rectangle3996  # Draft 2D object (typed FeaturePython)
  Area = 12650
  ChamferSize = 0
  Columns = 1
  FilletRadius = 0
  Height = 110
  Length = 115
  MakeFace = true
  Placement = pos=(5890,3115,0) rot=(0,0,1;0rad)
  Rows = 1
FEATURE [Part::Part2DObjectPython] Circle206  label="Выпуск 90 мм 004"  # Draft 2D object (typed FeaturePython)
  Area = 0
  FirstAngle = 0
  LastAngle = 0
  MakeFace = false
  Placement = pos=(5790,6025,0) rot=(0,0,1;0rad)
  Radius = 45
FEATURE [Part::Part2DObjectPython] Rectangle3999  label="Инсталляция для унитаза (8 см) TECE 9300040 004"  # Draft 2D object (typed FeaturePython)
  Area = 0
  ChamferSize = 0
  Columns = 1
  FilletRadius = 0
  Height = 645
  Length = 80
  MakeFace = false
  Placement = pos=(5745,5702.5,0) rot=(0,0,1;0rad)
  Rows = 1
FEATURE [Part::Part2DObjectPython] Circle207  label="Выпуск 90 мм 005"  # Draft 2D object (typed FeaturePython)
  Area = 0
  FirstAngle = 0
  LastAngle = 0
  MakeFace = false
  Placement = pos=(7940,525,0) rot=(0,0,1;0rad)
  Radius = 45
FEATURE [Part::Part2DObjectPython] Rectangle4000  label="Инсталляция для унитаза (8 см) TECE 9300040 005"  # Draft 2D object (typed FeaturePython)
  Area = 0
  ChamferSize = 0
  Columns = 1
  FilletRadius = 0
  Height = 645
  Length = 80
  MakeFace = false
  Placement = pos=(7895,202.5,0) rot=(0,0,1;0rad)
  Rows = 1
FEATURE [Part::FeaturePython] Structure550  label="Проём-инсталляция-002"  # Arch/BIM 52 (typed FeaturePython)
  Base = -> Rectangle4000
  FaceMaker = 0
  Height = 1200
  HorizontalArea = 51600
  IfcData = complex_attributes={"OwnerHistory": {}, "IsNestedBy": {}, "IsDecomposedBy": {}, "IsDefinedBy": {}, "ObjectPlacement": {}, "Representation":... (+4 chars omitted)
  IfcType = 52
  Length = 0
  MoveBase = false
  MoveWithHost = false
  Nodes = (2) [(13000,6050,0),(13000,6050,2180)]
  NodesOffset = 0
  Normal = (0,0,0)
  PerimeterLength = 1450
  Placement = pos=(0,0,-20) rot=(0,0,1;0rad)
  VerticalArea = 1740000
  Width = 100
FEATURE [Part::FeaturePython] Wall188  label="перегородка 045"  # Arch/BIM 166 (typed FeaturePython)
  Align = 2
  Area = 3660000
  Base = -> Line1324
  BlockHeight = 250
  BlockLength = 0
  CountBroken = 0
  CountEntire = 0
  Face = 0
  Height = 3000
  HorizontalArea = 116950
  IfcType = 166
  Joint = 0
  Length = 1220
  MakeBlocks = false
  Material = -> Material009
  MoveBase = false
  MoveWithHost = false
  Normal = (0,0,0)
  OffsetFirst = 0
  OffsetSecond = 300
  PerimeterLength = 2600
  Placement = pos=(0,0,-200) rot=(0,0,1;0rad)
  PredefinedType = 0
  Subtractions = -> [Structure550]
  VerticalArea = 7872000
  Width = 80
FEATURE [Part::Part2DObjectPython] Rectangle4006  label="облицовка камина001"  # Draft 2D object (typed FeaturePython)
  ChamferSize = 0
  Columns = 1
  FilletRadius = 0
  Height = 830
  Length = 570
  MakeFace = false
  Placement = pos=(8035,2655,0) rot=(0,0,1;1.5708rad)
  Rows = 1
FEATURE [Part::Part2DObjectPython] Line2088  # Draft 2D object (typed FeaturePython)
  Area = 0
  ChamferSize = 0
  Closed = false
  End = (5813,2315,0)
  FilletRadius = 0
  Length = 800
  MakeFace = false
  Placement = pos=(5793,3115,0) rot=(0,0,1;3.14159rad)
  Points = (2) [(-20,0,0),(-20,800,0)]
  Start = (5813,3115,0)
  Subdivisions = 0
FEATURE [Part::Part2DObjectPython] Arc158  label="Arc159"  # Draft 2D object (typed FeaturePython)
  Area = 0
  FirstAngle = 0
  LastAngle = 90
  MakeFace = false
  Placement = pos=(4664.46,3114.95,3.1832e-12) rot=(0,0,-1;1.5708rad)
  Radius = 340
FEATURE [Part::Part2DObjectPython] Rectangle4009  # Draft 2D object (typed FeaturePython)
  Area = 0
  ChamferSize = 0
  Columns = 1
  FilletRadius = 0
  Height = 550
  Length = 150
  MakeFace = false
  Placement = pos=(8585,2385,0) rot=(0,0,1;1.5708rad)
  Rows = 1
FEATURE [Part::Part2DObjectPython] Line2089  # Draft 2D object (typed FeaturePython)
  Area = 0
  ChamferSize = 0
  Closed = false
  End = (8293.46,1843.52,0)
  FilletRadius = 0
  Length = 600
  MakeFace = true
  Placement = pos=(8035,2385,0) rot=(0,0,-1;1.39171rad)
  Points = (2) [(0,0,0),(578.858,157.87,0)]
  Start = (8035,2385,0)
  Subdivisions = 0
FEATURE [Part::Feature] Compound006003  label="шкаф 60х60 секция 001"
  Placement = pos=(-17875,-1045,0) rot=(0,0,1;0rad)
  shape: bbox 600 x 600 x 2e-07 mm, 0 faces, 0 solids (baked)
FEATURE [Part::Feature] Compound006004  label="шкаф 60х60 секция 002"
  Placement = pos=(-17875,-445,0) rot=(0,0,1;0rad)
  shape: bbox 600 x 600 x 2e-07 mm, 0 faces, 0 solids (baked)
FEATURE [Part::Feature] Compound006005  label="шкаф 60х60 секция 003"
  Placement = pos=(-17875,155,0) rot=(0,0,1;0rad)
  shape: bbox 600 x 600 x 2e-07 mm, 0 faces, 0 solids (baked)
FEATURE [Part::Feature] Compound006006  label="шкаф 60х60 секция 004"
  Placement = pos=(-17875,755,0) rot=(0,0,1;0rad)
  shape: bbox 600 x 600 x 2e-07 mm, 0 faces, 0 solids (baked)
FEATURE [Part::Part2DObjectPython] Rectangle4017  # Draft 2D object (typed FeaturePython)
  Area = 0
  ChamferSize = 0
  Columns = 1
  FilletRadius = 0
  Height = 150
  Length = 600
  MakeFace = false
  Placement = pos=(7435,2385,0) rot=(0,0,1;0rad)
  Rows = 1
FEATURE [Part::Part2DObjectPython] Line2091  # Draft 2D object (typed FeaturePython)
  Area = 0
  ChamferSize = 0
  Closed = false
  End = (6025,3080,0)
  FilletRadius = 0
  Length = 1530
  MakeFace = true
  Placement = pos=(4495,3080,0) rot=(0,0,1;0rad)
  Points = (2) [(0,0,0),(1530,0,0)]
  Start = (4495,3080,0)
  Subdivisions = 0
FEATURE [Part::Part2DObjectPython] Rectangle4018  label="Котёл газ 003"  # Draft 2D object (typed FeaturePython)
  Area = 120000
  ChamferSize = 0
  Columns = 1
  FilletRadius = 0
  Height = 300
  Length = 400
  MakeFace = true
  Placement = pos=(6735,2195,0) rot=(0,0,-1;1.5708rad)
  Rows = 1
FEATURE [Part::Part2DObjectPython] Circle208  # Draft 2D object (typed FeaturePython)
  Area = 212372
  FirstAngle = 0
  LastAngle = 0
  MakeFace = true
  Placement = pos=(6777.68,2563.8,0) rot=(0,0,1;0rad)
  Radius = 260
FEATURE [Part::Feature] Compound006012  label="шкаф 60х60 секция 007"
  Placement = pos=(-19930,2155,0) rot=(0,0,1;0rad)
  shape: bbox 600 x 600 x 2e-07 mm, 0 faces, 0 solids (baked)
FEATURE [Part::Feature] Compound006013  label="шкаф 60х60 секция 008"
  Placement = pos=(-19930,2855,0) rot=(0,0,1;0rad)
  shape: bbox 600 x 600 x 2e-07 mm, 0 faces, 0 solids (baked)
FEATURE [Part::Feature] Compound006014  label="шкаф 60х60 секция 009"
  Placement = pos=(-20530,2855,0) rot=(0,0,1;0rad)
  shape: bbox 600 x 600 x 2e-07 mm, 0 faces, 0 solids (baked)
FEATURE [Part::Feature] Compound006015  label="шкаф 60х60 секция 010"
  Placement = pos=(-21130,2855,0) rot=(0,0,1;0rad)
  shape: bbox 600 x 600 x 2e-07 mm, 0 faces, 0 solids (baked)
FEATURE [Part::Part2DObjectPython] Line2096  # Draft 2D object (typed FeaturePython)
  Area = 0
  ChamferSize = 0
  Closed = false
  End = (-30,8395,0)
  FilletRadius = 0
  Length = 10630
  MakeFace = true
  Placement = pos=(10600,8395,0) rot=(0,0,1;0rad)
  Points = (2) [(0,0,0),(-10630,0,0)]
  Start = (10600,8395,0)
  Subdivisions = 0
FEATURE [Part::Part2DObjectPython] Line2097  # Draft 2D object (typed FeaturePython)
  Area = 0
  ChamferSize = 0
  Closed = false
  End = (6105,925,0)
  FilletRadius = 0
  Length = 800
  MakeFace = true
  Placement = pos=(2735,8225,0) rot=(0,0,1;0rad)
  Points = (2) [(2570,-7300,0),(3370,-7300,0)]
  Start = (5305,925,0)
  Subdivisions = 0
FEATURE [Part::Part2DObjectPython] Arc160  label="Arc161"  # Draft 2D object (typed FeaturePython)
  Area = 0
  FirstAngle = -180
  LastAngle = -90
  MakeFace = true
  Placement = pos=(3535,8225,0) rot=(0,0,1;0rad)
  Radius = 800
FEATURE [Part::Part2DObjectPython] Line2098  # Draft 2D object (typed FeaturePython)
  Area = 0
  ChamferSize = 0
  Closed = false
  End = (3535,8225,0)
  FilletRadius = 0
  Length = 800
  MakeFace = true
  Placement = pos=(165,15525,0) rot=(0,0,1;0rad)
  Points = (2) [(2570,-7300,0),(3370,-7300,0)]
  Start = (2735,8225,0)
  Subdivisions = 0
FEATURE [Part::Part2DObjectPython] Rectangle4021  label="ОК-196-007"  # Draft 2D object (typed FeaturePython)
  ChamferSize = 0
  Columns = 1
  FilletRadius = 0
  Height = 410
  Length = 920
  MakeFace = true
  Placement = pos=(3915,8395,0) rot=(0,0,1;0rad)
  Rows = 1
FEATURE [Part::Part2DObjectPython] Rectangle4022  label="четверть_183-007"  # Draft 2D object (typed FeaturePython)
  ChamferSize = 0
  Columns = 1
  FilletRadius = 0
  Height = 120
  Length = 790
  MakeFace = true
  Placement = pos=(3980,8805,0) rot=(0,0,1;0rad)
  Rows = 1
FEATURE [Part::FeaturePython] Structure422  label="Проём_четв._046"  # Arch/BIM 52 (typed FeaturePython)
  Base = -> Rectangle4022
  FaceMaker = 0
  Height = 1540
  HorizontalArea = 94800
  IfcData = complex_attributes={"OwnerHistory": {}, "IsNestedBy": {}, "IsDecomposedBy": {}, "IsDefinedBy": {}, "ObjectPlacement": {}, "Representation":... (+4 chars omitted)
  IfcType = 52
  Length = 0
  MoveBase = false
  MoveWithHost = false
  Nodes = (2) [(5775,-395,0),(5775,-395,2335)]
  NodesOffset = 0
  Normal = (0,0,0)
  PerimeterLength = 1820
  Placement = pos=(0,0,955) rot=(0,0,1;0rad)
  VerticalArea = 2.8028e+06
  Width = 100
FEATURE [Part::Part2DObjectPython] Rectangle4023  # Draft 2D object (typed FeaturePython)
  Area = 646000
  ChamferSize = 0
  Columns = 1
  FilletRadius = 0
  Height = 400
  Length = 1615
  MakeFace = true
  Placement = pos=(9385,8395,0) rot=(0,0,1;0rad)
  Rows = 1
FEATURE [Part::Part2DObjectPython] Rectangle4024  label="четверть_790-008"  # Draft 2D object (typed FeaturePython)
  ChamferSize = 0
  Columns = 1
  FilletRadius = 0
  Height = 120
  Length = 1830
  MakeFace = true
  Placement = pos=(7490,8805,0) rot=(0,0,1;0rad)
  Rows = 1
FEATURE [Part::FeaturePython] Structure350  label="Проём_четв._044"  # Arch/BIM 52 (typed FeaturePython)
  Base = -> Rectangle4024
  FaceMaker = 0
  Height = 2535
  HorizontalArea = 219600
  IfcData = complex_attributes={"OwnerHistory": {}, "IsNestedBy": {}, "IsDecomposedBy": {}, "IsDefinedBy": {}, "ObjectPlacement": {}, "Representation":... (+4 chars omitted)
  IfcType = 52
  Length = 0
  MoveBase = false
  MoveWithHost = false
  Nodes = (2) [(5775,-395,0),(5775,-395,2335)]
  NodesOffset = 0
  Normal = (0,0,0)
  PerimeterLength = 3900
  Placement = pos=(0,0,-40) rot=(0,0,1;0rad)
  VerticalArea = 9.8865e+06
  Width = 100
FEATURE [Part::FeaturePython] Wall298  label="облицовка 017"  # Arch/BIM 166 (typed FeaturePython)
  Align = 0
  Area = 42714200
  Base = -> Line1583
  BlockHeight = 67
  BlockLength = 250
  CountBroken = 162
  CountEntire = 1623
  Face = 0
  GlobalId = 2NuME8GJTD0RJft756pcFm
  Height = 3695
  HorizontalArea = 1701600
  IfcData = IfcUID=2NuME8GJTD0RJft756pcFm; attributes={"GlobalId": {"value": "2NuME8GJTD0RJft756pcFm"}}
  IfcType = 166
  Joint = 10
  Length = 11560
  MakeBlocks = false
  Material = -> Material003
  MoveBase = false
  MoveWithHost = false
  Normal = (0,0,0)
  OffsetFirst = 120
  OffsetSecond = 250
  PerimeterLength = 0
  Placement = pos=(0,0,185) rot=(0,0,1;0rad)
  PredefinedType = 0
  Subtractions = -> [Structure421,Structure422,Structure350]
  VerticalArea = 71084600
  Width = 120
FEATURE [App::GeometryPython] BuildingPart102  label="Облицовка 1nf кирпич"  # Arch/BIM 52 (typed FeaturePython)
  Area = 157333860
  GlobalId = 28tVz6in97ivETWCX3RcDU
  Group = -> [Wall298,Wall299,Wall300,Wall305,Wall306,Wall307,Wall308,Wall309]
  Height = 0
  HeightPropagate = true
  IfcData = IfcUID=28tVz6in97ivETWCX3RcDU,attributes={"GlobalId": {"value": "28tVz6in97ivETWCX3RcDU"}},+1 more (map truncated)
  IfcType = 52
  LevelOffset = 0
FEATURE [Part::Part2DObjectPython] Rectangle4025  label="ОК-92-008"  # Draft 2D object (typed FeaturePython)
  ChamferSize = 0
  Columns = 1
  FilletRadius = 0
  Height = 410
  Length = 1960
  MakeFace = true
  Placement = pos=(7425,8395,0) rot=(0,0,1;0rad)
  Rows = 1
FEATURE [Part::FeaturePython] Structure066  label="утепление пола в проёмах XPS 100mm 001"  # Arch/BIM 52 (typed FeaturePython)
  Base = -> Rectangle4025
  FaceMaker = 0
  GlobalId = 3EKnpUeW1ADw6RKJbe9Fmo
  Height = 100
  HorizontalArea = 803600
  IfcData = IfcUID=3EKnpUeW1ADw6RKJbe9Fmo,attributes={"GlobalId": {"value": "3EKnpUeW1ADw6RKJbe9Fmo"}},+1 more (map truncated)
  IfcType = 52
  Length = 0
  Material = -> Material002
  MoveBase = false
  MoveWithHost = false
  Nodes = (2) [(4000,4250,0),(4000,4250,100)]
  NodesOffset = 0
  Normal = (0,0,1)
  PerimeterLength = 4740
  Placement = pos=(0,0,-200) rot=(0,0,1;0rad)
  VerticalArea = 474000
  Width = 100
FEATURE [Part::FeaturePython] Structure371  label="Стяжка тёплого пола  80 мм 008"  # Arch/BIM 52 (typed FeaturePython)
  Base = -> Rectangle4025
  FaceMaker = 0
  GlobalId = 1aGZ9vCCD9wP_BshGDICol
  Height = 80
  HorizontalArea = 803600
  IfcData = IfcUID=1aGZ9vCCD9wP_BshGDICol,attributes={"GlobalId": {"value": "1aGZ9vCCD9wP_BshGDICol"}},+1 more (map truncated)
  IfcType = 52
  Length = 0
  Material = -> Material001
  MoveBase = false
  MoveWithHost = false
  Nodes = (2) [(4000,4250,0),(4000,4250,100)]
  NodesOffset = 0
  Normal = (0,0,1)
  PerimeterLength = 4740
  Placement = pos=(0,0,-100) rot=(0,0,1;0rad)
  VerticalArea = 379200
  Width = 100
FEATURE [Part::FeaturePython] Structure377  label="покрытие пола 20мм 003"  # Arch/BIM 52 (typed FeaturePython)
  Base = -> Rectangle4025
  FaceMaker = 0
  GlobalId = 2T3KnpypPEbv6OyL_zSjC5
  Height = 20
  HorizontalArea = 803600
  IfcData = IfcUID=2T3KnpypPEbv6OyL_zSjC5,attributes={"GlobalId": {"value": "2T3KnpypPEbv6OyL_zSjC5"}},+1 more (map truncated)
  IfcType = 52
  Length = 0
  Material = -> Material001
  MoveBase = false
  MoveWithHost = false
  Nodes = (2) [(4000,4250,0),(4000,4250,100)]
  NodesOffset = 0
  Normal = (0,0,1)
  PerimeterLength = 4740
  Placement = pos=(0,0,-20) rot=(0,0,1;0rad)
  VerticalArea = 94800
  Width = 20
FEATURE [Part::Feature] Compound006016  label="шкаф 60х60 секция 011"
  Placement = pos=(-21730,2855,0) rot=(0,0,1;0rad)
  shape: bbox 600 x 600 x 2e-07 mm, 0 faces, 0 solids (baked)
FEATURE [Part::Part2DObjectPython] Line2099  # Draft 2D object (typed FeaturePython)
  Area = 0
  ChamferSize = 0
  Closed = false
  End = (4770,8925,0)
  FilletRadius = 0
  Length = 3260
  MakeFace = false
  Placement = pos=(1510,8925,0) rot=(0,0,1;0rad)
  Points = (2) [(0,0,0),(3260,0,0)]
  Start = (1510,8925,0)
  Subdivisions = 0
FEATURE [Part::Part2DObjectPython] Wire1031  # Draft 2D object (typed FeaturePython)
  Area = 0
  ChamferSize = 0
  Closed = false
  End = (6173.39,2925.02,0)
  FilletRadius = 50
  Length = 1460.99
  MakeFace = false
  Placement = pos=(6173.39,1725.02,0) rot=(0,0,1;3.14159rad)
  Points = (13) [(0,0,0),(100,-100,0),(0,-200,0),(100,-300,0),(0,-400,0),(100,-500,0),(0,-600,0),(100,-700,0),(0,-800,0),(100,-900,0),(0,-1000,0),(100,-1100,0),+1 more]
  Start = (6173.39,1725.02,0)
  Subdivisions = 0
FEATURE [Part::Feature] Compound006018  label="VENT 2-12x17 001"
  Placement = pos=(1015,-3950,0) rot=(0,0,1;0rad)
  shape: bbox 360 x 250 x 2e-07 mm, 0 faces, 0 solids (baked)
FEATURE [Part::Feature] Compound006019  label="VENT 2-12x17 002"
  Placement = pos=(1015,-3700,0) rot=(0,0,1;0rad)
  shape: bbox 360 x 250 x 2e-07 mm, 0 faces, 0 solids (baked)
FEATURE [Part::Feature] Compound006020  label="VENT 2-12x17 003"
  Placement = pos=(1015,-4200,0) rot=(0,0,1;0rad)
  shape: bbox 360 x 250 x 2e-07 mm, 0 faces, 0 solids (baked)
FEATURE [Part::Feature] Compound006021  label="UNI 14L20 001"
  Placement = pos=(115,-3450,0) rot=(0,0,1;0rad)
  shape: bbox 360 x 810 x 2e-07 mm, 0 faces, 0 solids (baked)
FEATURE [Part::Part2DObjectPython] Arc161  label="Arc162"  # Draft 2D object (typed FeaturePython)
  Area = 0
  FirstAngle = 0
  LastAngle = 90
  MakeFace = false
  Placement = pos=(5813,3115,0) rot=(0,0,1;3.14159rad)
  Radius = 800
FEATURE [Part::Part2DObjectPython] Line2101  # Draft 2D object (typed FeaturePython)
  Area = 0
  ChamferSize = 0
  Closed = false
  End = (4664.46,2774.95,3.1832e-12)
  FilletRadius = 0
  Length = 340
  MakeFace = false
  Placement = pos=(4644.46,3114.95,3.183e-12) rot=(0,0,1;3.14159rad)
  Points = (2) [(-20,0,0),(-20,340,0)]
  Start = (4664.46,3114.95,3.1832e-12)
  Subdivisions = 0
FEATURE [Part::Part2DObjectPython] Rectangle4038  label="Д130-001"  # Draft 2D object (typed FeaturePython)
  Area = 143000
  ChamferSize = 0
  Columns = 1
  FilletRadius = 0
  Height = 110
  Length = 1300
  MakeFace = true
  Placement = pos=(5890,3225,0) rot=(0,0,1;3.14159rad)
  Rows = 1
FEATURE [Part::Part2DObjectPython] Wire1035  # Draft 2D object (typed FeaturePython)
  Area = 0
  ChamferSize = 0
  Closed = true
  End = (10600,475,0)
  FilletRadius = 0
  Length = 1707.11
  MakeFace = false
  Placement = pos=(10300,-25,0) rot=(0,0,1;0rad)
  Points = (3) [(-200,0,0),(300,0,0),(300,500,0)]
  Start = (10100,-25,0)
  Subdivisions = 0
FEATURE [Part::Part2DObjectPython] Wire1036  # Draft 2D object (typed FeaturePython)
  Area = 2.67085e+06
  ChamferSize = 0
  Closed = true
  End = (8635,-25,0)
  FilletRadius = 0
  Length = 9308.58
  MakeFace = true
  Placement = pos=(8035,605,0) rot=(0,0,1;0rad)
  Points = (8) [(600,5.45697e-12,0),(1510.74,2.72848e-12,0),(1935,424.264,0),(1935,2330,0),(2565,2330,0),(2565,-130,0),(2065,-630,0),(600,-630,0)]
  Start = (8635,605,0)
  Subdivisions = 0
FEATURE [Part::Part2DObjectPython] Rectangle4039  # Draft 2D object (typed FeaturePython)
  ChamferSize = 0
  Columns = 1
  FilletRadius = 0
  Height = 600
  Length = 900
  MakeFace = false
  Placement = pos=(8635,-25,0) rot=(0,0,-1;0rad)
  Rows = 1
FEATURE [Part::Part2DObjectPython] Rectangle4040  # Draft 2D object (typed FeaturePython)
  Area = 0
  ChamferSize = 0
  Columns = 1
  FilletRadius = 0
  Height = 550
  Length = 900
  MakeFace = false
  Placement = pos=(8635,575,0) rot=(0,0,1;0rad)
  Rows = 1
FEATURE [Part::Part2DObjectPython] Rectangle4041  # Draft 2D object (typed FeaturePython)
  Area = 0
  ChamferSize = 0
  Columns = 1
  FilletRadius = 0
  Height = 100
  Length = 100
  MakeFace = false
  Placement = pos=(6835,7295,0) rot=(0,0,1;0rad)
  Rows = 1
FEATURE [Part::Part2DObjectPython] Line2105  # Draft 2D object (typed FeaturePython)
  Area = 0
  ChamferSize = 0
  Closed = true
  End = (6335.19,4275,0)
  FilletRadius = 0
  Length = 3120
  MakeFace = false
  Placement = pos=(6335.19,7441.51,0) rot=(0,0,1;0rad)
  Points = (2) [(0,-46.5137,0),(-0.00026024,-3166.51,0)]
  Start = (6335.19,7395,0)
  Subdivisions = 0
FEATURE [Part::Part2DObjectPython] Rectangle4042  # Draft 2D object (typed FeaturePython)
  Area = 0
  ChamferSize = 0
  Columns = 1
  FilletRadius = 0
  Height = 1000
  Length = 260
  MakeFace = false
  Placement = pos=(7095,7395,0) rot=(0,0,1;0rad)
  Rows = 1
FEATURE [Part::Part2DObjectPython] Rectangle4043  # Draft 2D object (typed FeaturePython)
  Area = 0
  ChamferSize = 0
  Columns = 1
  FilletRadius = 0
  Height = 260
  Length = 1000
  MakeFace = false
  Placement = pos=(5835,6875,0) rot=(0,0,1;0rad)
  Rows = 1
FEATURE [Part::FeaturePython] Array080  # Draft array (typed FeaturePython)
  Angle = 360
  ArrayType = 0
  Axis = (0,0,1)
  Base = -> Rectangle4043
  Center = (0,0,0)
  Fuse = false
  IntervalAxis = (0,0,0)
  IntervalX = (1,0,0)
  IntervalY = (0,-260,0)
  IntervalZ = (0,0,50)
  NumberCircles = 3
  NumberPolar = 5
  NumberX = 1
  NumberY = 11
  NumberZ = 1
  Placement = pos=(0,-2.728e-12,0) rot=(0,0,1;0rad)
  RadialDistance = 50
  Symmetry = 1
  TangentialDistance = 25
FEATURE [Part::Part2DObjectPython] Line2114  # Draft 2D object (typed FeaturePython)
  Area = 0
  ChamferSize = 0
  Closed = false
  End = (6584.54,7827.75,0)
  FilletRadius = 0
  Length = 257.794
  MakeFace = false
  Placement = pos=(6402.25,7645.46,0) rot=(0,0,1;0rad)
  Points = (2) [(0,0,0),(182.288,182.288,0)]
  Start = (6402.25,7645.46,0)
  Subdivisions = 0
FEATURE [Part::Part2DObjectPython] Line2115  # Draft 2D object (typed FeaturePython)
  Area = 0
  ChamferSize = 0
  Closed = false
  End = (6835.69,7895,0)
  FilletRadius = 0
  Length = 260
  MakeFace = false
  Placement = pos=(6584.54,7827.75,0) rot=(0,0,1;0rad)
  Points = (2) [(0,0,0),(251.152,67.2524,0)]
  Start = (6584.54,7827.75,0)
  Subdivisions = 0
FEATURE [Part::Part2DObjectPython] Line2116  # Draft 2D object (typed FeaturePython)
  Area = 0
  ChamferSize = 0
  Closed = false
  End = (6402.25,7645.46,0)
  FilletRadius = 0
  Length = 260
  MakeFace = false
  Placement = pos=(6335,7394.31,0) rot=(0,0,1;0rad)
  Points = (2) [(0,0,0),(67.2524,251.152,0)]
  Start = (6335,7394.31,0)
  Subdivisions = 0
FEATURE [Part::Part2DObjectPython] Wire1037  # Draft 2D object (typed FeaturePython)
  Area = 0
  ChamferSize = 0
  Closed = true
  End = (6835,7135,0)
  FilletRadius = 0
  Length = 2533.86
  MakeFace = false
  Placement = pos=(5835,7135,0) rot=(0,0,1;0rad)
  Points = (4) [(0,0,0),(0,343.39,0),(1000,176.672,0),(1000,0,0)]
  Start = (5835,7135,0)
  Subdivisions = 0
FEATURE [Part::Part2DObjectPython] Wire1038  # Draft 2D object (typed FeaturePython)
  Area = 0
  ChamferSize = 0
  Closed = true
  End = (6835,7311.67,0)
  FilletRadius = 0
  Length = 2800.12
  MakeFace = false
  Placement = pos=(5835,7478.39,0) rot=(0,0,1;0rad)
  Points = (4) [(0,0,0),(0,540.228,0),(1000,-117.607,0),(1000,-166.718,0)]
  Start = (5835,7478.39,0)
  Subdivisions = 0
FEATURE [Part::Part2DObjectPython] Wire1039  # Draft 2D object (typed FeaturePython)
  Area = 0
  ChamferSize = 0
  Closed = true
  End = (6835,7360.78,0)
  FilletRadius = 0
  Length = 3195.1
  MakeFace = false
  Placement = pos=(5835,8018.62,0) rot=(0,0,1;0rad)
  Points = (5) [(0,0,0),(0,376.382,0),(376.382,376.382,0),(1034.22,-623.618,0),(1000,-657.835,0)]
  Start = (5835,8018.62,0)
  Subdivisions = 0
FEATURE [Part::Part2DObjectPython] Wire1040  # Draft 2D object (typed FeaturePython)
  Area = 0
  ChamferSize = 0
  Closed = true
  End = (6918.33,7395,0)
  FilletRadius = 0
  Length = 2800.12
  MakeFace = false
  Placement = pos=(6869.22,7395,0) rot=(0,0,1;0rad)
  Points = (4) [(0,0,0),(-657.835,1000,0),(-117.607,1000,0),(49.1116,0,0)]
  Start = (6869.22,7395,0)
  Subdivisions = 0
FEATURE [Part::Part2DObjectPython] Wire1041  # Draft 2D object (typed FeaturePython)
  Area = 0
  ChamferSize = 0
  Closed = true
  End = (7095,7395,0)
  FilletRadius = 0
  Length = 2533.86
  MakeFace = false
  Placement = pos=(6918.33,7395,0) rot=(0,0,1;0rad)
  Points = (4) [(0,0,0),(-166.718,1000,0),(176.672,1000,0),(176.672,0,0)]
  Start = (6918.33,7395,0)
  Subdivisions = 0
FEATURE [Part::Part2DObjectPython] Wire1042  # Draft 2D object (typed FeaturePython)
  Area = 0
  ChamferSize = 0
  Closed = true
  End = (5575,5315,0)
  FilletRadius = 0
  Length = 2533.86
  MakeFace = false
  Placement = pos=(5751.67,5315,0) rot=(0,0,1;3.14159rad)
  Points = (4) [(0,0,0),(-166.718,1000,0),(176.672,1000,0),(176.672,0,0)]
  Start = (5751.67,5315,0)
  Subdivisions = 0
FEATURE [Part::Part2DObjectPython] Wire1043  # Draft 2D object (typed FeaturePython)
  Area = 0
  ChamferSize = 0
  Closed = true
  End = (5751.67,5315,0)
  FilletRadius = 0
  Length = 2800.12
  MakeFace = false
  Placement = pos=(5800.78,5315,0) rot=(0,0,1;3.14159rad)
  Points = (4) [(0,0,0),(-657.835,1000,0),(-117.607,1000,0),(49.1116,0,0)]
  Start = (5800.78,5315,0)
  Subdivisions = 0
FEATURE [Part::Part2DObjectPython] Wire1044  # Draft 2D object (typed FeaturePython)
  Area = 0
  ChamferSize = 0
  Closed = true
  End = (5835,5349.22,0)
  FilletRadius = 0
  Length = 3195.1
  MakeFace = false
  Placement = pos=(6835,4691.38,0) rot=(0,0,1;3.14159rad)
  Points = (5) [(0,0,0),(0,376.382,0),(376.382,376.382,0),(1034.22,-623.618,0),(1000,-657.835,0)]
  Start = (6835,4691.38,0)
  Subdivisions = 0
FEATURE [Part::Part2DObjectPython] Wire1045  # Draft 2D object (typed FeaturePython)
  Area = 0
  ChamferSize = 0
  Closed = true
  End = (5835,5398.33,0)
  FilletRadius = 0
  Length = 2800.12
  MakeFace = false
  Placement = pos=(6835,5231.61,0) rot=(0,0,1;3.14159rad)
  Points = (4) [(0,0,0),(0,540.228,0),(1000,-117.607,0),(1000,-166.718,0)]
  Start = (6835,5231.61,0)
  Subdivisions = 0
FEATURE [Part::Part2DObjectPython] Wire1046  # Draft 2D object (typed FeaturePython)
  Area = 0
  ChamferSize = 0
  Closed = true
  End = (5835,5575,0)
  FilletRadius = 0
  Length = 2533.86
  MakeFace = false
  Placement = pos=(6835,5575,0) rot=(0,0,1;3.14159rad)
  Points = (4) [(0,0,0),(0,343.39,0),(1000,176.672,0),(1000,0,0)]
  Start = (6835,5575,0)
  Subdivisions = 0
FEATURE [Part::Part2DObjectPython] Rectangle4045  # Draft 2D object (typed FeaturePython)
  Area = 0
  ChamferSize = 0
  Columns = 1
  FilletRadius = 0
  Height = 100
  Length = 100
  MakeFace = false
  Placement = pos=(5835.72,5415,0) rot=(0,0,1;3.14159rad)
  Rows = 1
FEATURE [Part::Part2DObjectPython] Line2121  # Draft 2D object (typed FeaturePython)
  Area = 0
  ChamferSize = 0
  Closed = false
  End = (6835,7895,0)
  FilletRadius = 0
  Length = 520
  MakeFace = true
  Placement = pos=(7355,7895,0) rot=(0,0,1;0rad)
  Points = (2) [(0,0,0),(-520,0,0)]
  Start = (7355,7895,0)
  Subdivisions = 0
FEATURE [Part::Part2DObjectPython] Line2122  # Draft 2D object (typed FeaturePython)
  Area = 0
  ChamferSize = 0
  Closed = false
  End = (9950,3080,0)
  FilletRadius = 0
  Length = 2725
  MakeFace = true
  Placement = pos=(7225,3080,0) rot=(0,0,1;0rad)
  Points = (2) [(0,0,0),(2725,-1.81899e-12,0)]
  Start = (7225,3080,0)
  Subdivisions = 0
FEATURE [Part::Part2DObjectPython] Line2124  # Draft 2D object (typed FeaturePython)
  Area = 0
  ChamferSize = 0
  Closed = false
  End = (11130,4185,0)
  FilletRadius = 0
  Length = 11690
  MakeFace = true
  Placement = pos=(-560,4185,0) rot=(0,0,1;0rad)
  Points = (2) [(0,0,0),(11690,0,0)]
  Start = (-560,4185,0)
  Subdivisions = 0
FEATURE [Part::Part2DObjectPython] Circle198  # Draft 2D object (typed FeaturePython)
  Area = 0
  FirstAngle = 0
  LastAngle = 0
  MakeFace = false
  Placement = pos=(4790,5755,0) rot=(0,0,1;0rad)
  Radius = 100
FEATURE [Part::Part2DObjectPython] Circle199  # Draft 2D object (typed FeaturePython)
  Area = 0
  FirstAngle = 0
  LastAngle = 0
  MakeFace = false
  Placement = pos=(4790,5755,0) rot=(0,0,1;0rad)
  Radius = 140
FEATURE [Part::Part2DObjectPython] Rectangle3889  label="проём в перекрытии под фан.стояк004"  # Draft 2D object (typed FeaturePython)
  ChamferSize = 0
  Columns = 1
  FilletRadius = 0
  Height = 640
  Length = 360
  MakeFace = false
  Placement = pos=(4610,5295,0) rot=(0,0,1;0rad)
  Rows = 1
FEATURE [Part::Part2DObjectPython] Circle209  # Draft 2D object (typed FeaturePython)
  Area = 0
  FirstAngle = 0
  LastAngle = 0
  MakeFace = false
  Placement = pos=(4790,5445,0) rot=(0,0,1;0rad)
  Radius = 110
FEATURE [Part::Part2DObjectPython] Circle210  # Draft 2D object (typed FeaturePython)
  Area = 0
  FirstAngle = 0
  LastAngle = 0
  MakeFace = false
  Placement = pos=(4790,5445,0) rot=(0,0,1;0rad)
  Radius = 70
FEATURE [Part::Feature] Compound006017  label="UNI 1420_001"
  Placement = pos=(3090,205,0) rot=(0,0,1;0rad)
  shape: bbox 360 x 640 x 2e-07 mm, 0 faces, 0 solids (baked)
FEATURE [Part::Part2DObjectPython] Rectangle4032  label="проём в перекрытии под фан.стояк006"  # Draft 2D object (typed FeaturePython)
  ChamferSize = 0
  Columns = 1
  FilletRadius = 0
  Height = 250
  Length = 360
  MakeFace = false
  Placement = pos=(6040,5295,0) rot=(0,0,1;0rad)
  Rows = 1
FEATURE [Part::Part2DObjectPython] Rectangle4033  label="проём в перекрытии под фан.стояк007"  # Draft 2D object (typed FeaturePython)
  ChamferSize = 0
  Columns = 1
  FilletRadius = 0
  Height = 170
  Length = 120
  MakeFace = false
  Placement = pos=(6240,5335,0) rot=(0,0,1;0rad)
  Rows = 1
FEATURE [Part::Part2DObjectPython] Rectangle4034  label="проём в перекрытии под фан.стояк008"  # Draft 2D object (typed FeaturePython)
  ChamferSize = 0
  Columns = 1
  FilletRadius = 0
  Height = 170
  Length = 120
  MakeFace = false
  Placement = pos=(6080,5335,0) rot=(0,0,1;0rad)
  Rows = 1
FEATURE [Part::Part2DObjectPython] Rectangle4035  label="проём в перекрытии под фан.стояк009"  # Draft 2D object (typed FeaturePython)
  ChamferSize = 0
  Columns = 1
  FilletRadius = 0
  Height = 810
  Length = 360
  MakeFace = false
  Placement = pos=(6940,5295,0) rot=(0,0,1;0rad)
  Rows = 1
FEATURE [Part::Part2DObjectPython] Circle213  # Draft 2D object (typed FeaturePython)
  Area = 0
  FirstAngle = 0
  LastAngle = 0
  MakeFace = false
  Placement = pos=(7120,5445,0) rot=(0,0,1;0rad)
  Radius = 110
FEATURE [Part::Part2DObjectPython] Circle214  # Draft 2D object (typed FeaturePython)
  Area = 0
  FirstAngle = 0
  LastAngle = 0
  MakeFace = false
  Placement = pos=(7120,5445,0) rot=(0,0,1;0rad)
  Radius = 70
FEATURE [Part::Part2DObjectPython] Circle215  # Draft 2D object (typed FeaturePython)
  Area = 0
  FirstAngle = 0
  LastAngle = 0
  MakeFace = false
  Placement = pos=(7120,5925,0) rot=(0,0,1;0rad)
  Radius = 140
FEATURE [Part::Part2DObjectPython] Circle216  # Draft 2D object (typed FeaturePython)
  Area = 0
  FirstAngle = 0
  LastAngle = 0
  MakeFace = false
  Placement = pos=(7120,5925,0) rot=(0,0,1;0rad)
  Radius = 100
FEATURE [Part::Part2DObjectPython] Rectangle4036  # Draft 2D object (typed FeaturePython)
  Area = 0
  ChamferSize = 0
  Columns = 1
  FilletRadius = 20
  Height = 100
  Length = 220
  MakeFace = false
  Placement = pos=(7010,5620,0) rot=(0,0,1;0rad)
  Rows = 1
FEATURE [Part::Part2DObjectPython] Clone2D011  label="Контур_по_кладке002 (2D)"  # Draft 2D object (typed FeaturePython)
  Fuse = false
  Objects = -> [Rectangle3870]
  Placement = pos=(-50,-45,0) rot=(0,0,1;0rad)
  Scale = (1,1,1)
FEATURE [Part::Part2DObjectPython] Clone2D012  label="Контур по блоку ЛСР38 внешний001 (2D)"  # Draft 2D object (typed FeaturePython)
  Fuse = false
  Objects = -> [Rectangle3879]
  Placement = pos=(-430,-425,0) rot=(0,0,1;0rad)
  Scale = (1,1,1)
FEATURE [Part::Part2DObjectPython] Clone2D013  label="контур по облицовке001 (2D)"  # Draft 2D object (typed FeaturePython)
  Fuse = false
  Objects = -> [Rectangle3854]
  Placement = pos=(-560,-555,0) rot=(0,0,1;0rad)
  Scale = (1,1,1)
FEATURE [Part::Part2DObjectPython] Rectangle4046  # Draft 2D object (typed FeaturePython)
  Area = 0
  ChamferSize = 0
  Columns = 1
  FilletRadius = 0
  Height = 8420
  Length = 10630
  MakeFace = false
  Placement = pos=(-30,-25,0) rot=(0,0,1;0rad)
  Rows = 1
FEATURE [Part::Part2DObjectPython] Clone2D015  label="Wire1041 (2D)"  # Draft 2D object (typed FeaturePython)
  Fuse = false
  Objects = -> [Wire1041]
  Placement = pos=(6918.33,7395,0) rot=(0,0,1;0rad)
  Scale = (1,1,1)
FEATURE [Part::Part2DObjectPython] Clone2D016  label="Wire1040 (2D)"  # Draft 2D object (typed FeaturePython)
  Fuse = false
  Objects = -> [Wire1040]
  Placement = pos=(6869.22,7395,0) rot=(0,0,1;0rad)
  Scale = (1,1,1)
FEATURE [Part::Part2DObjectPython] Clone2D017  label="Wire1039 (2D)"  # Draft 2D object (typed FeaturePython)
  Fuse = false
  Objects = -> [Wire1039]
  Placement = pos=(5835,8018.62,0) rot=(0,0,1;0rad)
  Scale = (1,1,1)
FEATURE [Part::Part2DObjectPython] Clone2D018  label="Wire1038 (2D)"  # Draft 2D object (typed FeaturePython)
  Fuse = false
  Objects = -> [Wire1038]
  Placement = pos=(5835,7478.39,0) rot=(0,0,1;0rad)
  Scale = (1,1,1)
FEATURE [Part::Part2DObjectPython] Clone2D019  label="Wire1037 (2D)"  # Draft 2D object (typed FeaturePython)
  Fuse = false
  Objects = -> [Wire1037]
  Placement = pos=(5835,7135,0) rot=(0,0,1;0rad)
  Scale = (1,1,1)
FEATURE [Part::Part2DObjectPython] Rectangle4051  label="четверть_790-010"  # Draft 2D object (typed FeaturePython)
  ChamferSize = 0
  Columns = 1
  FilletRadius = 0
  Height = 150
  Length = 2200
  MakeFace = true
  Placement = pos=(6385,-175,0) rot=(0,0,1;3.14159rad)
  Rows = 1
FEATURE [Part::FeaturePython] Structure577  label="Проём_четв._059"  # Arch/BIM 52 (typed FeaturePython)
  Base = -> Rectangle4051
  FaceMaker = 0
  Height = 820
  HorizontalArea = 330000
  IfcData = complex_attributes={"OwnerHistory": {}, "IsNestedBy": {}, "IsDecomposedBy": {}, "IsDefinedBy": {}, "ObjectPlacement": {}, "Representation":... (+4 chars omitted)
  IfcType = 52
  Length = 0
  MoveBase = false
  MoveWithHost = false
  Nodes = (2) [(1035,460,0),(1035,460,535)]
  NodesOffset = 0
  Normal = (0,0,0)
  PerimeterLength = 4700
  Placement = pos=(0,0,4415) rot=(0,0,1;0rad)
  VerticalArea = 3854000
  Width = 100
FEATURE [Part::Part2DObjectPython] Rectangle4052  label="ОК-92-010"  # Draft 2D object (typed FeaturePython)
  ChamferSize = 0
  Columns = 1
  FilletRadius = 0
  Height = 150
  Length = 2350
  MakeFace = true
  Placement = pos=(6450,-25,0) rot=(0,0,1;3.14159rad)
  Rows = 1
FEATURE [Part::FeaturePython] Structure578  label="Проём-ОК-92-005"  # Arch/BIM 52 (typed FeaturePython)
  Base = -> Rectangle4052
  FaceMaker = 0
  Height = 950
  HorizontalArea = 352500
  IfcData = complex_attributes={"OwnerHistory": {}, "IsNestedBy": {}, "IsDecomposedBy": {}, "IsDefinedBy": {}, "ObjectPlacement": {}, "Representation":... (+4 chars omitted)
  IfcType = 52
  Length = 0
  MoveBase = false
  MoveWithHost = false
  Nodes = (2) [(1035,250,0),(1035,250,600)]
  NodesOffset = 0
  Normal = (0,0,0)
  PerimeterLength = 5000
  Placement = pos=(0,0,4350) rot=(0,0,1;0rad)
  VerticalArea = 4750000
  Width = 100
FEATURE [Part::FeaturePython] Roof025  label="roof_4_side002"  # Arch/BIM 113 (typed FeaturePython)
  Angles = [35,45,35,45]
  Base = -> Wire1003
  BorderLength = 0
  Face = 0
  Flip = false
  Heights = [3777.62,5500,3777.62,5500]
  HorizontalArea = 0
  IdRel = [-1,-1,-1,-1]
  IfcData = attributes={"GlobalId": {"name": "GlobalId", "type": "IfcGloballyUniqueId", "is_enum": false, "enum_values": []}, "Description": {"... (+613 chars omitted),+1 more (map truncated)
  IfcType = 113
  Material = -> Material007
  MoveBase = false
  MoveWithHost = false
  Overhang = [1000,835,1000,835]
  PerimeterLength = 0
  Placement = pos=(0,0,3250) rot=(0,0,1;0rad)
  PredefinedType = 0
  RidgeLength = 0
  Runs = [5500,5500,5500,5500]
  Subtractions = -> [Structure578,Structure577]
  Thickness = [350,302,350,302]
  VerticalArea = 0
FEATURE [Part::MultiCommon] Common084  label="roof_4_side_001"
  Shapes = -> [Roof025,Extrude099019]
FEATURE [Part::FeaturePython] Clone006  label="UNI 14L20 002"  # Draft clone (typed FeaturePython)
  AttacherType = Attacher::AttachEngine3D
  Fuse = false
  Objects = -> [Compound006021]
  Placement = pos=(115,-3450,0) rot=(0,0,1;0rad)
  Scale = (1,1,1)
FEATURE [Part::FeaturePython] Clone007  label="VENT 2-12x17 004"  # Draft clone (typed FeaturePython)
  AttacherType = Attacher::AttachEngine3D
  Fuse = false
  Objects = -> [Compound006019]
  Placement = pos=(1015,-3700,0) rot=(0,0,1;0rad)
  Scale = (1,1,1)
FEATURE [Part::FeaturePython] Clone008  label="VENT 2-12x17 005"  # Draft clone (typed FeaturePython)
  AttacherType = Attacher::AttachEngine3D
  Fuse = false
  Objects = -> [Compound006018]
  Placement = pos=(1015,-3950,0) rot=(0,0,1;0rad)
  Scale = (1,1,1)
FEATURE [Part::FeaturePython] Clone009  label="VENT 2-12x17 006"  # Draft clone (typed FeaturePython)
  AttacherType = Attacher::AttachEngine3D
  Fuse = false
  Objects = -> [Compound006020]
  Placement = pos=(1015,-4200,0) rot=(0,0,1;0rad)
  Scale = (1,1,1)
FEATURE [Part::Part2DObjectPython] Rectangle4054  # Draft 2D object (typed FeaturePython)
  Area = 22500
  ChamferSize = 0
  Columns = 1
  FilletRadius = 0
  Height = 150
  Length = 150
  MakeFace = true
  Placement = pos=(3535,2935,0) rot=(0,0,1;0rad)
  Rows = 1
FEATURE [Part::FeaturePython] Structure441  label="Стойка под конёк 010"  # Arch/BIM 172 (typed FeaturePython)
  Base = -> Rectangle4054
  FaceMaker = 0
  Height = 2935
  HorizontalArea = 22500
  IfcData = attributes={"GlobalId": {"name": "GlobalId", "type": "IfcGloballyUniqueId", "is_enum": false, "enum_values": []}, "Description": {"... (+484 chars omitted),+1 more (map truncated)
  IfcType = 172
  Length = 0
  Material = -> Material
  MoveBase = false
  MoveWithHost = false
  Nodes = (2) [(3610,3010,0),(3610,3010,2935)]
  NodesOffset = 0
  Normal = (0,0,0)
  PerimeterLength = 600
  Placement = pos=(0,0,3135) rot=(0,0,1;0rad)
  PredefinedType = 0
  VerticalArea = 1761000
  Width = 100
FEATURE [Part::Part2DObjectPython] Rectangle4055  # Draft 2D object (typed FeaturePython)
  Area = 22500
  ChamferSize = 0
  Columns = 1
  FilletRadius = 0
  Height = 150
  Length = 150
  MakeFace = true
  Placement = pos=(3535,5285,0) rot=(0,0,1;0rad)
  Rows = 1
FEATURE [Part::FeaturePython] Structure442  label="Стойка под конёк 011"  # Arch/BIM 172 (typed FeaturePython)
  Base = -> Rectangle4055
  FaceMaker = 0
  Height = 2935
  HorizontalArea = 22500
  IfcData = attributes={"GlobalId": {"name": "GlobalId", "type": "IfcGloballyUniqueId", "is_enum": false, "enum_values": []}, "Description": {"... (+484 chars omitted),+1 more (map truncated)
  IfcType = 172
  Length = 0
  Material = -> Material
  MoveBase = false
  MoveWithHost = false
  Nodes = (2) [(3610,5360,0),(3610,5360,2935)]
  NodesOffset = 0
  Normal = (0,0,0)
  PerimeterLength = 600
  Placement = pos=(0,0,3135) rot=(0,0,1;0rad)
  PredefinedType = 0
  VerticalArea = 1761000
  Width = 100
FEATURE [Part::Part2DObjectPython] Rectangle4056  # Draft 2D object (typed FeaturePython)
  Area = 22500
  ChamferSize = 0
  Columns = 1
  FilletRadius = 0
  Height = 150
  Length = 150
  MakeFace = true
  Placement = pos=(6910,5285,0) rot=(0,0,1;0rad)
  Rows = 1
FEATURE [Part::FeaturePython] Structure440  label="Стойка под конёк 001"  # Arch/BIM 172 (typed FeaturePython)
  Base = -> Rectangle4056
  FaceMaker = 0
  Height = 2935
  HorizontalArea = 22500
  IfcData = attributes={"GlobalId": {"name": "GlobalId", "type": "IfcGloballyUniqueId", "is_enum": false, "enum_values": []}, "Description": {"... (+484 chars omitted),+1 more (map truncated)
  IfcType = 172
  Length = 0
  Material = -> Material
  MoveBase = false
  MoveWithHost = false
  Nodes = (2) [(6960,5360,0),(6960,5360,2935)]
  NodesOffset = 0
  Normal = (0,0,0)
  PerimeterLength = 600
  Placement = pos=(0,0,3135) rot=(0,0,1;0rad)
  PredefinedType = 0
  VerticalArea = 1761000
  Width = 100
FEATURE [Part::Part2DObjectPython] Rectangle4057  # Draft 2D object (typed FeaturePython)
  Area = 22500
  ChamferSize = 0
  Columns = 1
  FilletRadius = 0
  Height = 150
  Length = 150
  MakeFace = true
  Placement = pos=(6910,2935,0) rot=(0,0,1;0rad)
  Rows = 1
FEATURE [Part::FeaturePython] Structure443  label="Стойка под конёк 012"  # Arch/BIM 172 (typed FeaturePython)
  Base = -> Rectangle4057
  FaceMaker = 0
  Height = 2935
  HorizontalArea = 22500
  IfcData = attributes={"GlobalId": {"name": "GlobalId", "type": "IfcGloballyUniqueId", "is_enum": false, "enum_values": []}, "Description": {"... (+484 chars omitted),+1 more (map truncated)
  IfcType = 172
  Length = 0
  Material = -> Material
  MoveBase = false
  MoveWithHost = false
  Nodes = (2) [(6960,3010,0),(6960,3010,2935)]
  NodesOffset = 0
  Normal = (0,0,0)
  PerimeterLength = 600
  Placement = pos=(0,0,3135) rot=(0,0,1;0rad)
  PredefinedType = 0
  VerticalArea = 1761000
  Width = 100
FEATURE [Part::Part2DObjectPython] Line2125  # Draft 2D object (typed FeaturePython)
  Area = 0
  ChamferSize = 0
  Closed = false
  End = (5285,2800,0)
  FilletRadius = 0
  Length = 2965
  MakeFace = false
  Placement = pos=(5285,-165,0) rot=(0,0,1;0rad)
  Points = (2) [(0,0,0),(0,2965,0)]
  Start = (5285,-165,0)
  Subdivisions = 0
FEATURE [Part::Part2DObjectPython] Rectangle4059  label="Д90-210-001"  # Draft 2D object (typed FeaturePython)
  ChamferSize = 0
  Columns = 1
  FilletRadius = 0
  Height = 150
  Length = 900
  MakeFace = true
  Placement = pos=(3535,5205,0) rot=(0,0,-1;1.5708rad)
  Rows = 1
FEATURE [Part::FeaturePython] Structure558  label="Проём-Д90-024"  # Arch/BIM 52 (typed FeaturePython)
  Base = -> Rectangle4059
  FaceMaker = 0
  Height = 2400
  HorizontalArea = 135000
  IfcData = complex_attributes={"OwnerHistory": {}, "IsNestedBy": {}, "IsDecomposedBy": {}, "IsDefinedBy": {}, "ObjectPlacement": {}, "Representation":... (+4 chars omitted)
  IfcType = 52
  Length = 0
  MoveBase = false
  MoveWithHost = false
  Nodes = (2) [(13000,6050,0),(13000,6050,2180)]
  NodesOffset = 0
  Normal = (0,0,0)
  PerimeterLength = 2100
  Placement = pos=(0,0,3145) rot=(0,0,1;0rad)
  VerticalArea = 5.04e+06
  Width = 100
FEATURE [Part::Part2DObjectPython] Arc162  label="Arc163"  # Draft 2D object (typed FeaturePython)
  Area = 0
  FirstAngle = -180
  LastAngle = -90
  MakeFace = true
  Placement = pos=(3535,4355,0) rot=(0,0,-1;1.5708rad)
  Radius = 800
FEATURE [Part::Part2DObjectPython] Line2126  # Draft 2D object (typed FeaturePython)
  Area = 0
  ChamferSize = 0
  Closed = false
  End = (3535,4355,0)
  FilletRadius = 0
  Length = 800
  MakeFace = true
  Placement = pos=(2735,4355,0) rot=(0,0,1;0rad)
  Points = (2) [(0,0,0),(800,1.81899e-12,0)]
  Start = (2735,4355,0)
  Subdivisions = 0
FEATURE [Part::Part2DObjectPython] Line2127  # Draft 2D object (typed FeaturePython)
  Area = 0
  ChamferSize = 0
  Closed = false
  End = (3535,4015,0)
  FilletRadius = 0
  Length = 800
  MakeFace = true
  Placement = pos=(2735,4015,0) rot=(0,0,1;0rad)
  Points = (2) [(0,0,0),(800,1.36424e-12,0)]
  Start = (2735,4015,0)
  Subdivisions = 0
FEATURE [Part::Part2DObjectPython] Arc163  label="Arc164"  # Draft 2D object (typed FeaturePython)
  Area = 0
  FirstAngle = -180
  LastAngle = -90
  MakeFace = true
  Placement = pos=(3535,4015,0) rot=(0,0,1;0rad)
  Radius = 800
FEATURE [Part::Part2DObjectPython] Rectangle4060  label="Д90-210-010"  # Draft 2D object (typed FeaturePython)
  ChamferSize = 0
  Columns = 1
  FilletRadius = 0
  Height = 150
  Length = 900
  MakeFace = true
  Placement = pos=(3535,4065,0) rot=(0,0,-1;1.5708rad)
  Rows = 1
FEATURE [Part::FeaturePython] Structure559  label="Проём-Д90-025"  # Arch/BIM 52 (typed FeaturePython)
  Base = -> Rectangle4060
  FaceMaker = 0
  Height = 2400
  HorizontalArea = 135000
  IfcData = complex_attributes={"OwnerHistory": {}, "IsNestedBy": {}, "IsDecomposedBy": {}, "IsDefinedBy": {}, "ObjectPlacement": {}, "Representation":... (+4 chars omitted)
  IfcType = 52
  Length = 0
  MoveBase = false
  MoveWithHost = false
  Nodes = (2) [(13000,6050,0),(13000,6050,2180)]
  NodesOffset = 0
  Normal = (0,0,0)
  PerimeterLength = 2100
  Placement = pos=(0,0,3145) rot=(0,0,1;0rad)
  VerticalArea = 5.04e+06
  Width = 100
FEATURE [Part::Part2DObjectPython] Rectangle4061  label="Д90-210-011"  # Draft 2D object (typed FeaturePython)
  ChamferSize = 0
  Columns = 1
  FilletRadius = 0
  Height = 150
  Length = 900
  MakeFace = true
  Placement = pos=(7060,3085,0) rot=(0,0,1;1.5708rad)
  Rows = 1
FEATURE [Part::FeaturePython] Structure576  label="Проём-Д110-001"  # Arch/BIM 52 (typed FeaturePython)
  Base = -> Rectangle4061
  FaceMaker = 0
  Height = 2400
  HorizontalArea = 135000
  IfcData = complex_attributes={"OwnerHistory": {}, "IsNestedBy": {}, "IsDecomposedBy": {}, "IsDefinedBy": {}, "ObjectPlacement": {}, "Representation":... (+4 chars omitted)
  IfcType = 52
  Length = 0
  MoveBase = false
  MoveWithHost = false
  Nodes = (2) [(13000,6050,0),(13000,6050,2180)]
  NodesOffset = 0
  Normal = (0,0,0)
  PerimeterLength = 2100
  Placement = pos=(0,0,3145) rot=(0,0,1;0rad)
  VerticalArea = 5.04e+06
  Width = 100
FEATURE [Part::Part2DObjectPython] Arc164  label="Arc165"  # Draft 2D object (typed FeaturePython)
  Area = 0
  FirstAngle = -180
  LastAngle = -90
  MakeFace = true
  Placement = pos=(7060,3135,0) rot=(0,0,1;3.14159rad)
  Radius = 800
FEATURE [Part::Part2DObjectPython] Line2128  # Draft 2D object (typed FeaturePython)
  Area = 0
  ChamferSize = 0
  Closed = false
  End = (7860,3135,0)
  FilletRadius = 0
  Length = 800
  MakeFace = true
  Placement = pos=(7060,3135,0) rot=(0,0,1;0rad)
  Points = (2) [(0,0,0),(800,1.81899e-12,0)]
  Start = (7060,3135,0)
  Subdivisions = 0
FEATURE [Part::Part2DObjectPython] Rectangle4063  # Draft 2D object (typed FeaturePython)
  Area = 36000
  ChamferSize = 0
  Columns = 1
  FilletRadius = 0
  Height = 240
  Length = 150
  MakeFace = true
  Placement = pos=(3535,4065,0) rot=(0,0,1;0rad)
  Rows = 1
FEATURE [Part::Part2DObjectPython] Rectangle4064  # Draft 2D object (typed FeaturePython)
  Area = 195000
  ChamferSize = 0
  Columns = 1
  FilletRadius = 0
  Height = 1300
  Length = 150
  MakeFace = true
  Placement = pos=(6910,3985,0) rot=(0,0,1;0rad)
  Rows = 1
FEATURE [Part::Part2DObjectPython] Rectangle4066  # Draft 2D object (typed FeaturePython)
  Area = 561227
  ChamferSize = 0
  Columns = 1
  FilletRadius = 0
  Height = 100
  Length = 5612.27
  MakeFace = true
  Placement = pos=(72.7272,7595,0) rot=(0,0,1;0rad)
  Rows = 1
FEATURE [Part::Part2DObjectPython] Rectangle4067  # Draft 2D object (typed FeaturePython)
  Area = 343727
  ChamferSize = 0
  Columns = 1
  FilletRadius = 0
  Height = 100
  Length = 3437.27
  MakeFace = true
  Placement = pos=(7060,7595,0) rot=(0,0,1;0rad)
  Rows = 1
FEATURE [Part::Part2DObjectPython] Rectangle4068  # Draft 2D object (typed FeaturePython)
  Area = 366227
  ChamferSize = 0
  Columns = 1
  FilletRadius = 0
  Height = 100
  Length = 3662.27
  MakeFace = true
  Placement = pos=(72.7272,675,0) rot=(0,0,1;0rad)
  Rows = 1
FEATURE [Part::Part2DObjectPython] Rectangle4069  # Draft 2D object (typed FeaturePython)
  Area = 193000
  ChamferSize = 0
  Columns = 1
  FilletRadius = 0
  Height = 1930
  Length = 100
  MakeFace = true
  Placement = pos=(4135,855,0) rot=(0,0,1;0rad)
  Rows = 1
FEATURE [Part::Part2DObjectPython] Rectangle4070  # Draft 2D object (typed FeaturePython)
  Area = 296000
  ChamferSize = 0
  Columns = 1
  FilletRadius = 0
  Height = 2960
  Length = 100
  MakeFace = true
  Placement = pos=(6960,5435,0) rot=(0,0,1;0rad)
  Rows = 1
FEATURE [Part::Part2DObjectPython] Line2130  # Draft 2D object (typed FeaturePython)
  Area = 0
  ChamferSize = 0
  Closed = false
  End = (4975,1985,0)
  FilletRadius = 0
  Length = 800
  MakeFace = true
  Placement = pos=(4975,2785,0) rot=(0,0,-1;1.5708rad)
  Points = (2) [(0,0,0),(800,1.81899e-12,0)]
  Start = (4975,2785,0)
  Subdivisions = 0
FEATURE [Part::Part2DObjectPython] Arc166  label="Arc167"  # Draft 2D object (typed FeaturePython)
  Area = 0
  FirstAngle = -180
  LastAngle = -90
  MakeFace = true
  Placement = pos=(4975,2785,0) rot=(0,0,1;1.5708rad)
  Radius = 800
FEATURE [Part::Part2DObjectPython] Rectangle4071  label="Д90-210-012"  # Draft 2D object (typed FeaturePython)
  ChamferSize = 0
  Columns = 1
  FilletRadius = 0
  Height = 100
  Length = 900
  MakeFace = true
  Placement = pos=(5825,2885,0) rot=(0,0,1;3.14159rad)
  Rows = 1
FEATURE [Part::FeaturePython] Structure564  label="Проём-Д90-026"  # Arch/BIM 52 (typed FeaturePython)
  Base = -> Rectangle4071
  FaceMaker = 0
  Height = 2400
  HorizontalArea = 90000
  IfcData = complex_attributes={"OwnerHistory": {}, "IsNestedBy": {}, "IsDecomposedBy": {}, "IsDefinedBy": {}, "ObjectPlacement": {}, "Representation":... (+4 chars omitted)
  IfcType = 52
  Length = 0
  MoveBase = false
  MoveWithHost = false
  Nodes = (2) [(13000,6050,0),(13000,6050,2180)]
  NodesOffset = 0
  Normal = (0,0,0)
  PerimeterLength = 2000
  Placement = pos=(0,0,3145) rot=(0,0,1;0rad)
  VerticalArea = 4.8e+06
  Width = 100
FEATURE [Part::Part2DObjectPython] Rectangle4072  # Draft 2D object (typed FeaturePython)
  Area = 139000
  ChamferSize = 0
  Columns = 1
  FilletRadius = 0
  Height = 100
  Length = 1390
  MakeFace = true
  Placement = pos=(4925,2885,0) rot=(0,0,1;3.14159rad)
  Rows = 1
FEATURE [Part::Feature] Compound006022  label="шкаф 60х60 секция 012"
  Placement = pos=(-18165,1165,0) rot=(0,0,1;0rad)
  shape: bbox 600 x 600 x 2e-07 mm, 0 faces, 0 solids (baked)
FEATURE [Part::Part2DObjectPython] Rectangle4073  label="Шкаф 60 048"  # Draft 2D object (typed FeaturePython)
  Area = 1206000
  ChamferSize = 0
  Columns = 1
  FilletRadius = 0
  Height = 2010
  Length = 600
  MakeFace = true
  Placement = pos=(3535,5585,0) rot=(0,0,1;0rad)
  Rows = 1
FEATURE [Part::Feature] Compound006023  label="шкаф 60х60 секция 013"
  Placement = pos=(-18165,565,0) rot=(0,0,1;0rad)
  shape: bbox 600 x 600 x 2e-07 mm, 0 faces, 0 solids (baked)
FEATURE [Part::Feature] Compound006024  label="шкаф 60х60 секция 014"
  Placement = pos=(-18165,-35,0) rot=(0,0,1;0rad)
  shape: bbox 600 x 600 x 2e-07 mm, 0 faces, 0 solids (baked)
FEATURE [Part::Feature] Compound006025  label="шкаф 60х60 секция 015"
  Placement = pos=(-18165,5765,0) rot=(0,0,1;0rad)
  shape: bbox 600 x 600 x 2e-07 mm, 0 faces, 0 solids (baked)
FEATURE [Part::Feature] Compound006026  label="шкаф 60х60 секция 016"
  Placement = pos=(-18165,5165,0) rot=(0,0,1;0rad)
  shape: bbox 600 x 600 x 2e-07 mm, 0 faces, 0 solids (baked)
FEATURE [Part::Feature] Compound006027  label="шкаф 60х60 секция 017"
  Placement = pos=(-18165,4565,0) rot=(0,0,1;0rad)
  shape: bbox 600 x 600 x 2e-07 mm, 0 faces, 0 solids (baked)
FEATURE [Part::Part2DObjectPython] Line2132  # Draft 2D object (typed FeaturePython)
  Area = 0
  ChamferSize = 0
  Closed = false
  End = (3535,975,0)
  FilletRadius = 0
  Length = 160
  MakeFace = false
  Placement = pos=(3535,1135,0) rot=(0,0,1;0rad)
  Points = (2) [(0,0,0),(0,-160,0)]
  Start = (3535,1135,0)
  Subdivisions = 0
FEATURE [Part::Part2DObjectPython] Rectangle4076  # Draft 2D object (typed FeaturePython)
  Area = 100000
  ChamferSize = 0
  Columns = 1
  FilletRadius = 0
  Height = 1000
  Length = 100
  MakeFace = true
  Placement = pos=(6725,-25,0) rot=(0,0,1;0rad)
  Rows = 1
FEATURE [Part::Part2DObjectPython] Rectangle4077  # Draft 2D object (typed FeaturePython)
  Area = 12000
  ChamferSize = 0
  Columns = 1
  FilletRadius = 0
  Height = 80
  Length = 150
  MakeFace = true
  Placement = pos=(3535,3085,0) rot=(0,0,1;0rad)
  Rows = 1
FEATURE [Part::Part2DObjectPython] Rectangle4078  # Draft 2D object (typed FeaturePython)
  Area = 12000
  ChamferSize = 0
  Columns = 1
  FilletRadius = 0
  Height = 80
  Length = 150
  MakeFace = true
  Placement = pos=(3535,5205,0) rot=(0,0,1;0rad)
  Rows = 1
FEATURE [Part::Part2DObjectPython] Rectangle4079  # Draft 2D object (typed FeaturePython)
  Area = 70000
  ChamferSize = 0
  Columns = 1
  FilletRadius = 0
  Height = 100
  Length = 700
  MakeFace = true
  Placement = pos=(4235,5585,0) rot=(0,0,1;3.14159rad)
  Rows = 1
FEATURE [Part::Part2DObjectPython] Rectangle4080  # Draft 2D object (typed FeaturePython)
  Area = 7500
  ChamferSize = 0
  Columns = 1
  FilletRadius = 0
  Height = 50
  Length = 150
  MakeFace = true
  Placement = pos=(3535,2885,0) rot=(0,0,1;0rad)
  Rows = 1
FEATURE [Part::Part2DObjectPython] Rectangle4081  # Draft 2D object (typed FeaturePython)
  Area = 22500
  ChamferSize = 0
  Columns = 1
  FilletRadius = 0
  Height = 150
  Length = 150
  MakeFace = true
  Placement = pos=(6910,5435,0) rot=(0,0,1;0rad)
  Rows = 1
FEATURE [Part::Part2DObjectPython] Rectangle4082  # Draft 2D object (typed FeaturePython)
  Area = 281000
  ChamferSize = 0
  Columns = 1
  FilletRadius = 0
  Height = 2810
  Length = 100
  MakeFace = true
  Placement = pos=(4135,5585,0) rot=(0,0,1;0rad)
  Rows = 1
FEATURE [Part::Part2DObjectPython] Rectangle4087  # Draft 2D object (typed FeaturePython)
  Area = 123500
  ChamferSize = 0
  Columns = 1
  FilletRadius = 0
  Height = 100
  Length = 1235
  MakeFace = true
  Placement = pos=(7060,2885,0) rot=(0,0,1;3.14159rad)
  Rows = 1
FEATURE [Part::Part2DObjectPython] Rectangle4088  # Draft 2D object (typed FeaturePython)
  Area = 7500
  ChamferSize = 0
  Columns = 1
  FilletRadius = 0
  Height = 50
  Length = 150
  MakeFace = true
  Placement = pos=(6910,2885,0) rot=(0,0,1;0rad)
  Rows = 1
FEATURE [Part::Part2DObjectPython] Rectangle4093  # Draft 2D object (typed FeaturePython)
  Area = 391000
  ChamferSize = 0
  Columns = 1
  FilletRadius = 0
  Height = 3910
  Length = 100
  MakeFace = true
  Placement = pos=(5685,4485,0) rot=(0,0,1;0rad)
  Rows = 1
FEATURE [Part::Part2DObjectPython] Rectangle4094  # Draft 2D object (typed FeaturePython)
  Area = 60000
  ChamferSize = 0
  Columns = 1
  FilletRadius = 0
  Height = 100
  Length = 600
  MakeFace = true
  Placement = pos=(5685,5585,0) rot=(0,0,1;3.14159rad)
  Rows = 1
FEATURE [Part::Part2DObjectPython] Rectangle4095  # Draft 2D object (typed FeaturePython)
  Area = 7500
  ChamferSize = 0
  Columns = 1
  FilletRadius = 0
  Height = 50
  Length = 150
  MakeFace = true
  Placement = pos=(3535,5435,0) rot=(0,0,1;0rad)
  Rows = 1
FEATURE [Part::Part2DObjectPython] Rectangle4096  # Draft 2D object (typed FeaturePython)
  Area = 294227
  ChamferSize = 0
  Columns = 1
  FilletRadius = 0
  Height = 100
  Length = 2942.27
  MakeFace = true
  Placement = pos=(7555,675,0) rot=(0,0,1;0rad)
  Rows = 1
FEATURE [Part::Part2DObjectPython] Wire1050  # Draft 2D object (typed FeaturePython)
  Area = 0
  ChamferSize = 0
  Closed = true
  End = (7555,2780,0)
  FilletRadius = 0
  Length = 4900
  MakeFace = false
  Placement = pos=(5565,2905,0) rot=(0,0,1;0rad)
  Points = (4) [(1350,-125,0),(1350,-1935,0),(1990,-1935,0),(1990,-125,0)]
  Start = (6915,2780,0)
  Subdivisions = 0
FEATURE [Part::Part2DObjectPython] Rectangle4101  # Draft 2D object (typed FeaturePython)
  Area = 0
  ChamferSize = 0
  Columns = 1
  FilletRadius = 0
  Height = 1810
  Length = 640
  MakeFace = false
  Placement = pos=(6915,970,0) rot=(0,0,1;0rad)
  Rows = 1
FEATURE [Part::Part2DObjectPython] Rectangle4102  label="Шкаф 60 051"  # Draft 2D object (typed FeaturePython)
  Area = 360000
  ChamferSize = 0
  Columns = 1
  FilletRadius = 0
  Height = 600
  Length = 600
  MakeFace = true
  Placement = pos=(4235,2180,0) rot=(0,0,1;0rad)
  Rows = 1
FEATURE [Part::Part2DObjectPython] ShapeString254  # Draft 2D object (typed FeaturePython)
  FontFile = <path>
  Placement = pos=(4253.19,2402.94,0) rot=(0,0,1;0rad)
  Size = 200
  String = СМ
  Tracking = 0
FEATURE [Part::Part2DObjectPython] Rectangle4104  # Draft 2D object (typed FeaturePython)
  Area = 220000
  ChamferSize = 0
  Columns = 1
  FilletRadius = 0
  Height = 400
  Length = 550
  MakeFace = true
  Placement = pos=(6725,675,0) rot=(0,0,1;3.14159rad)
  Rows = 1
FEATURE [Part::Part2DObjectPython] Rectangle4107  label="Инсталляция для унитаза (8 см) TECE 9300040 006"  # Draft 2D object (typed FeaturePython)
  Area = 0
  ChamferSize = 0
  Columns = 1
  FilletRadius = 0
  Height = 645
  Length = 80
  MakeFace = false
  Placement = pos=(6745,152.5,0) rot=(0,0,1;0rad)
  Rows = 1
FEATURE [Part::Part2DObjectPython] Circle217  label="Выпуск 90 мм 006"  # Draft 2D object (typed FeaturePython)
  Area = 0
  FirstAngle = 0
  LastAngle = 0
  MakeFace = false
  Placement = pos=(6790,475,0) rot=(0,0,1;0rad)
  Radius = 45
FEATURE [Part::Part2DObjectPython] Rectangle4108  label="Шкаф 60 052"  # Draft 2D object (typed FeaturePython)
  Area = 510000
  ChamferSize = 0
  Columns = 1
  FilletRadius = 0
  Height = 600
  Length = 850
  MakeFace = true
  Placement = pos=(4235,6995,0) rot=(0,0,1;0rad)
  Rows = 1
FEATURE [Part::Part2DObjectPython] Rectangle4109  label="Шкаф 60 053"  # Draft 2D object (typed FeaturePython)
  Area = 1206000
  ChamferSize = 0
  Columns = 1
  FilletRadius = 0
  Height = 2010
  Length = 600
  MakeFace = true
  Placement = pos=(5085,5585,0) rot=(0,0,1;0rad)
  Rows = 1
FEATURE [Part::Part2DObjectPython] Rectangle4112  # Draft 2D object (typed FeaturePython)
  Area = 0
  ChamferSize = 0
  Columns = 1
  FilletRadius = 0
  Height = 800
  Length = 800
  MakeFace = false
  Placement = pos=(9800,-25,0) rot=(0,0,1;0rad)
  Rows = 1
FEATURE [Part::Part2DObjectPython] Rectangle4117  # Draft 2D object (typed FeaturePython)
  Area = 202500
  ChamferSize = 0
  Columns = 1
  FilletRadius = 0
  Height = 450
  Length = 450
  MakeFace = true
  Placement = pos=(9713.44,7585,0) rot=(0,0,1;3.14159rad)
  Rows = 1
FEATURE [Part::Feature] Compound006034  label="шкаф 60х60 секция 018"
  Placement = pos=(-14145,-245,0) rot=(0,0,1;0rad)
  shape: bbox 600 x 600 x 2e-07 mm, 0 faces, 0 solids (baked)
FEATURE [Part::Feature] Compound006035  label="шкаф 60х60 секция 019"
  Placement = pos=(-12502.7,-245,0) rot=(0,0,1;0rad)
  shape: bbox 600 x 600 x 2e-07 mm, 0 faces, 0 solids (baked)
FEATURE [Part::Feature] Compound006036  label="шкаф 60х60 секция 020"
  Placement = pos=(-11902.7,-245,0) rot=(0,0,1;0rad)
  shape: bbox 600 x 600 x 2e-07 mm, 0 faces, 0 solids (baked)
FEATURE [Sketcher::SketchObject] Sketch414  label="кресло 45'016"
  FullyConstrained = false
  Placement = pos=(9853.39,4170,0) rot=(0,0,1;1.5708rad)
  sketch-geometry (11):
    g0: LineSegment StartX=-280 StartY=-350 StartZ=0 EndX=280 EndY=-350 EndZ=0
    g1: LineSegment StartX=330 StartY=-300 StartZ=0 EndX=330 EndY=300 EndZ=0
    g2: LineSegment StartX=280 StartY=350 StartZ=0 EndX=-280 EndY=350 EndZ=0
    g3: LineSegment StartX=-330 StartY=300 StartZ=0 EndX=-330 EndY=-300 EndZ=0
    g4: ArcOfCircle CenterX=-280 CenterY=300 CenterZ=0 NormalX=0 NormalY=0 NormalZ=1 AngleXU=0 Radius=50 StartAngle=1.5708 EndAngle=3.14159
    g5: ArcOfCircle CenterX=280 CenterY=300 CenterZ=0 NormalX=0 NormalY=0 NormalZ=1 AngleXU=0 Radius=50 StartAngle=-9e-16 EndAngle=1.5708
    g6: ArcOfCircle CenterX=280 CenterY=-300 CenterZ=0 NormalX=0 NormalY=0 NormalZ=1 AngleXU=0 Radius=50 StartAngle=4.71239 EndAngle=6.28319
    g7: ArcOfCircle CenterX=-280 CenterY=-300 CenterZ=0 NormalX=0 NormalY=0 NormalZ=1 AngleXU=0 Radius=50 StartAngle=3.14159 EndAngle=4.71239
    g8: LineSegment StartX=-330 StartY=200 StartZ=0 EndX=330 EndY=200 EndZ=0
    g9: LineSegment StartX=-230 StartY=200 StartZ=0 EndX=-230 EndY=-350 EndZ=0
    g10: LineSegment StartX=230 StartY=200 StartZ=0 EndX=230 EndY=-350 EndZ=0
  constraints (29):
    c: Horizontal(g0)
    c: Vertical(g1)
    c: Vertical(g3)
    c: Tangent(g2,g4) = -1.5708
    c: Tangent(g3,g4) = -1.5708
    c: Tangent(g2,g5) = -1.5708
    c: Tangent(g1,g5) = -1.5708
    c: Tangent(g0,g6) = -1.5708
    c: Tangent(g1,g6) = -1.5708
    c: Tangent(g3,g7) = -1.5708
    c: Tangent(g0,g7) = -1.5708
    c: DistanceY(g0,g2) = 700
    c: DistanceX(g3,g1) = 660
    c: Equal(g4,g5)
    c: Equal(g7,g6)
    c: Radius(g5) = 50
    c: Symmetric(g2,g2,g-2)
    c: Symmetric(g2,g0,g-1)
    c: PointOnObject(g8,g3)
    c: PointOnObject(g8,g1)
    c: Horizontal(g8)
    c: DistanceY(g8,g2) = 150
    c: PointOnObject(g9,g8)
    c: PointOnObject(g9,g0)
    c: Vertical(g9)
    c: PointOnObject(g10,g0)
    c: Vertical(g10)
    c: DistanceX(g10,g8) = 100
    c: Symmetric(g10,g9,g-2)
FEATURE [Part::Part2DObjectPython] Rectangle4125  # Draft 2D object (typed FeaturePython)
  Area = 390500
  ChamferSize = 0
  Columns = 1
  FilletRadius = 0
  Height = 100
  Length = 3905
  MakeFace = true
  Placement = pos=(-370,4135,0) rot=(0,0,1;0rad)
  Rows = 1
FEATURE [Part::Part2DObjectPython] Rectangle4127  # Draft 2D object (typed FeaturePython)
  ChamferSize = 0
  Columns = 1
  FilletRadius = 10
  Height = 1200
  Length = 700
  MakeFace = true
  Placement = pos=(-20,2915,0) rot=(0,0,1;0rad)
  Rows = 1
FEATURE [Sketcher::SketchObject] Sketch416  label="кресло 45'018"
  FullyConstrained = false
  Placement = pos=(696.606,3515,0) rot=(0,0,-1;1.5708rad)
  sketch-geometry (11):
    g0: LineSegment StartX=-280 StartY=-350 StartZ=0 EndX=280 EndY=-350 EndZ=0
    g1: LineSegment StartX=330 StartY=-300 StartZ=0 EndX=330 EndY=300 EndZ=0
    g2: LineSegment StartX=280 StartY=350 StartZ=0 EndX=-280 EndY=350 EndZ=0
    g3: LineSegment StartX=-330 StartY=300 StartZ=0 EndX=-330 EndY=-300 EndZ=0
    g4: ArcOfCircle CenterX=-280 CenterY=300 CenterZ=0 NormalX=0 NormalY=0 NormalZ=1 AngleXU=0 Radius=50 StartAngle=1.5708 EndAngle=3.14159
    g5: ArcOfCircle CenterX=280 CenterY=300 CenterZ=0 NormalX=0 NormalY=0 NormalZ=1 AngleXU=0 Radius=50 StartAngle=-9e-16 EndAngle=1.5708
    g6: ArcOfCircle CenterX=280 CenterY=-300 CenterZ=0 NormalX=0 NormalY=0 NormalZ=1 AngleXU=0 Radius=50 StartAngle=4.71239 EndAngle=6.28319
    g7: ArcOfCircle CenterX=-280 CenterY=-300 CenterZ=0 NormalX=0 NormalY=0 NormalZ=1 AngleXU=0 Radius=50 StartAngle=3.14159 EndAngle=4.71239
    g8: LineSegment StartX=-330 StartY=200 StartZ=0 EndX=330 EndY=200 EndZ=0
    g9: LineSegment StartX=-230 StartY=200 StartZ=0 EndX=-230 EndY=-350 EndZ=0
    g10: LineSegment StartX=230 StartY=200 StartZ=0 EndX=230 EndY=-350 EndZ=0
  constraints (29):
    c: Horizontal(g0)
    c: Vertical(g1)
    c: Vertical(g3)
    c: Tangent(g2,g4) = -1.5708
    c: Tangent(g3,g4) = -1.5708
    c: Tangent(g2,g5) = -1.5708
    c: Tangent(g1,g5) = -1.5708
    c: Tangent(g0,g6) = -1.5708
    c: Tangent(g1,g6) = -1.5708
    c: Tangent(g3,g7) = -1.5708
    c: Tangent(g0,g7) = -1.5708
    c: DistanceY(g0,g2) = 700
    c: DistanceX(g3,g1) = 660
    c: Equal(g4,g5)
    c: Equal(g7,g6)
    c: Radius(g5) = 50
    c: Symmetric(g2,g2,g-2)
    c: Symmetric(g2,g0,g-1)
    c: PointOnObject(g8,g3)
    c: PointOnObject(g8,g1)
    c: Horizontal(g8)
    c: DistanceY(g8,g2) = 150
    c: PointOnObject(g9,g8)
    c: PointOnObject(g9,g0)
    c: Vertical(g9)
    c: PointOnObject(g10,g0)
    c: Vertical(g10)
    c: DistanceX(g10,g8) = 100
    c: Symmetric(g10,g9,g-2)
FEATURE [Part::Part2DObjectPython] Rectangle4128  # Draft 2D object (typed FeaturePython)
  ChamferSize = 0
  Columns = 1
  FilletRadius = 0
  Height = 1200
  Length = 2100
  MakeFace = true
  Placement = pos=(780,785,0) rot=(0,0,1;0rad)
  Rows = 1
FEATURE [Part::Mirroring] mirror016002002  label="Rectangle4127 (mirrored)"
  Base = (5285,4185,0)
  Normal = (0,-1,0)
  Source = -> Rectangle4127
FEATURE [Part::Mirroring] mirror016002003  label="кресло 45'018 (mirrored)"
  Base = (5285,4185,0)
  Normal = (0,-1,0)
  Source = -> Sketch416
FEATURE [Part::Mirroring] mirror016002004  label="Rectangle4128 (mirrored)"
  Base = (5285,4185,0)
  Normal = (0,-1,0)
  Source = -> Rectangle4128
FEATURE [Part::Part2DObjectPython] Wire1052  # Draft 2D object (typed FeaturePython)
  Area = 0
  ChamferSize = 0
  Closed = false
  End = (5054.98,5600,0)
  FilletRadius = 50
  Length = 981.15
  MakeFace = false
  Placement = pos=(4254.98,5600,0) rot=(0,0,1;0rad)
  Points = (9) [(0,0,0),(100,-100,0),(200,0,0),(300,-100,0),(400,0,0),(500,-100,0),(600,0,0),(700,-100,0),(800,0,0)]
  Start = (4254.98,5600,0)
  Subdivisions = 0
FEATURE [Part::Part2DObjectPython] Rectangle4129  label="Шкаф 60 054"  # Draft 2D object (typed FeaturePython)
  Area = 3.41073e+06
  ChamferSize = 0
  Columns = 1
  FilletRadius = 0
  Height = 1200
  Length = 2842.27
  MakeFace = true
  Placement = pos=(7555,775,0) rot=(0,0,1;0rad)
  Rows = 1
FEATURE [Part::Part2DObjectPython] Rectangle4132  # Draft 2D object (typed FeaturePython)
  ChamferSize = 0
  Columns = 1
  FilletRadius = 0
  Height = 1600
  Length = 2100
  MakeFace = true
  Placement = pos=(7653.44,7585,0) rot=(0,0,-1;1.5708rad)
  Rows = 1
FEATURE [Part::Part2DObjectPython] Rectangle4133  # Draft 2D object (typed FeaturePython)
  Area = 211500
  ChamferSize = 0
  Columns = 1
  FilletRadius = 0
  Height = 2115
  Length = 100
  MakeFace = true
  Placement = pos=(10397.3,775,0) rot=(0,0,1;0rad)
  Rows = 1
FEATURE [Part::Part2DObjectPython] Rectangle4135  # Draft 2D object (typed FeaturePython)
  Area = 202500
  ChamferSize = 0
  Columns = 1
  FilletRadius = 0
  Height = 450
  Length = 450
  MakeFace = true
  Placement = pos=(7643.44,7585,0) rot=(0,0,1;3.14159rad)
  Rows = 1
FEATURE [Part::Part2DObjectPython] Rectangle4140  # Draft 2D object (typed FeaturePython)
  Area = 0
  ChamferSize = 0
  Columns = 1
  FilletRadius = 0
  Height = 1260
  Length = 290
  MakeFace = false
  Placement = pos=(6835,4425,0) rot=(0,0,1;0rad)
  Rows = 1
FEATURE [Part::Part2DObjectPython] Rectangle4142  # Draft 2D object (typed FeaturePython)
  Area = 73000
  ChamferSize = 0
  Columns = 1
  FilletRadius = 0
  Height = 100
  Length = 730
  MakeFace = true
  Placement = pos=(7555,975,0) rot=(0,0,1;3.14159rad)
  Rows = 1
FEATURE [Part::Part2DObjectPython] Rectangle4143  # Draft 2D object (typed FeaturePython)
  Area = 90000
  ChamferSize = 0
  Columns = 1
  FilletRadius = 0
  Height = 900
  Length = 100
  MakeFace = true
  Placement = pos=(7455,-25,0) rot=(0,0,1;0rad)
  Rows = 1
FEATURE [Part::Part2DObjectPython] Rectangle4144  # Draft 2D object (typed FeaturePython)
  Area = 10272.8
  ChamferSize = 0
  Columns = 1
  FilletRadius = 0
  Height = 100
  Length = 102.728
  MakeFace = true
  Placement = pos=(10600,5580,0) rot=(0,0,1;3.14159rad)
  Rows = 1
FEATURE [Part::Part2DObjectPython] Rectangle4145  # Draft 2D object (typed FeaturePython)
  Area = 211500
  ChamferSize = 0
  Columns = 1
  FilletRadius = 0
  Height = 2115
  Length = 100
  MakeFace = true
  Placement = pos=(10397.3,5480,0) rot=(0,0,1;0rad)
  Rows = 1
FEATURE [Part::Part2DObjectPython] Rectangle4146  # Draft 2D object (typed FeaturePython)
  Area = 10272.8
  ChamferSize = 0
  Columns = 1
  FilletRadius = 0
  Height = 100
  Length = 102.728
  MakeFace = true
  Placement = pos=(10600,2890,0) rot=(0,0,1;3.14159rad)
  Rows = 1
FEATURE [Part::Part2DObjectPython] Rectangle4147  # Draft 2D object (typed FeaturePython)
  ChamferSize = 0
  Columns = 1
  FilletRadius = 10
  Height = 2500
  Length = 700
  MakeFace = true
  Placement = pos=(10590,5435,0) rot=(0,0,1;3.14159rad)
  Rows = 1
FEATURE [Part::Part2DObjectPython] Rectangle4148  # Draft 2D object (typed FeaturePython)
  Area = 10272.7
  ChamferSize = 0
  Columns = 1
  FilletRadius = 0
  Height = 100
  Length = 102.727
  MakeFace = true
  Placement = pos=(72.7272,5580,0) rot=(0,0,1;3.14159rad)
  Rows = 1
FEATURE [Part::Part2DObjectPython] Rectangle4149  # Draft 2D object (typed FeaturePython)
  Area = 10272.7
  ChamferSize = 0
  Columns = 1
  FilletRadius = 0
  Height = 100
  Length = 102.727
  MakeFace = true
  Placement = pos=(72.7272,2890,0) rot=(0,0,1;3.14159rad)
  Rows = 1
FEATURE [Part::Part2DObjectPython] Rectangle4150  # Draft 2D object (typed FeaturePython)
  Area = 211500
  ChamferSize = 0
  Columns = 1
  FilletRadius = 0
  Height = 2115
  Length = 100
  MakeFace = true
  Placement = pos=(72.7272,775,0) rot=(0,0,1;0rad)
  Rows = 1
FEATURE [Part::Part2DObjectPython] Rectangle4151  # Draft 2D object (typed FeaturePython)
  Area = 211500
  ChamferSize = 0
  Columns = 1
  FilletRadius = 0
  Height = 2115
  Length = 100
  MakeFace = true
  Placement = pos=(72.7272,5480,0) rot=(0,0,1;0rad)
  Rows = 1
FEATURE [Part::Part2DObjectPython] Rectangle4152  # Draft 2D object (typed FeaturePython)
  Area = 0
  ChamferSize = 0
  Columns = 1
  FilletRadius = 75
  Height = 450
  Length = 235
  MakeFace = false
  Placement = pos=(4352.5,1650,0) rot=(0,0,1;0rad)
  Rows = 1
FEATURE [Part::Part2DObjectPython] Rectangle4153  # Draft 2D object (typed FeaturePython)
  Area = 0
  ChamferSize = 0
  Columns = 1
  FilletRadius = 75
  Height = 450
  Length = 235
  MakeFace = false
  Placement = pos=(4352.5,1050,0) rot=(0,0,1;0rad)
  Rows = 1
FEATURE [Part::Part2DObjectPython] Rectangle4154  label="Раковина 120x45 003"  # Draft 2D object (typed FeaturePython)
  Area = 540000
  ChamferSize = 0
  Columns = 1
  FilletRadius = 0
  Height = 450
  Length = 1200
  MakeFace = true
  Placement = pos=(4685,975,0) rot=(0,0,1;1.5708rad)
  Rows = 1
FEATURE [Part::Part2DObjectPython] Rectangle4156  # Draft 2D object (typed FeaturePython)
  Area = 54000
  ChamferSize = 0
  Columns = 1
  FilletRadius = 0
  Height = 120
  Length = 450
  MakeFace = true
  Placement = pos=(4685,975,0) rot=(0,0,1;3.14159rad)
  Rows = 1
FEATURE [Part::Part2DObjectPython] Rectangle4162  # Draft 2D object (typed FeaturePython)
  Area = 0
  ChamferSize = 0
  Columns = 1
  FilletRadius = 0
  Height = 600
  Length = 600
  MakeFace = false
  Placement = pos=(3507.5,195,0) rot=(0,0,1;1.5708rad)
  Rows = 1
FEATURE [Part::Mirroring] mirror016002012  label="Rectangle4162 (mirrored)"
  Base = (5285,4185,0)
  Normal = (0,1,0)
  Source = -> Rectangle4162
FEATURE [Part::Part2DObjectPython] Wire1053  label="Столовая"  # Draft 2D object (typed FeaturePython)
  Area = 2.14616e+07
  ChamferSize = 0
  Closed = true
  End = (7125,5685,0)
  FilletRadius = 0
  Length = 19870
  MakeFace = true
  Placement = pos=(7125,3225,0) rot=(0,0,1;0rad)
  Points = (6) [(0,0,0),(3475,-4.54747e-12,0),(3475,5170,0),(-1290,5170,0),(-1290,2460,0),(0,2460,0)]
  Start = (7125,3225,0)
  Subdivisions = 0
FEATURE [Part::Part2DObjectPython] Wire1054  label="Кухня"  # Draft 2D object (typed FeaturePython)
  Area = 8.87215e+06
  ChamferSize = 0
  Closed = true
  End = (9950,3225,0)
  FilletRadius = 0
  Length = 12577.1
  MakeFace = true
  Placement = pos=(8035,3225,0) rot=(0,0,1;0rad)
  Points = (11) [(0,0,0),(0,-670,0),(-620,-670,0),(-620,-2040,0),(0,-2040,0),(0,-3250,0),(2065,-3250,0),(2565,-2750,0),(2565,-290,0),(1915,-290,0),(1915,0,0)]
  Start = (8035,3225,0)
  Subdivisions = 0
FEATURE [Part::Part2DObjectPython] Wire1055  label="Кабинет"  # Draft 2D object (typed FeaturePython)
  Area = 1.27898e+07
  ChamferSize = 0
  Closed = true
  End = (3535,-25,0)
  FilletRadius = 0
  Length = 14730
  MakeFace = true
  Placement = pos=(-30,-25,0) rot=(0,0,1;0rad)
  Points = (6) [(0,0,0),(0,3800,0),(2400,3800,0),(2400,3150,0),(3565,3150,0),(3565,-1.75504e-12,0)]
  Start = (-30,-25,0)
  Subdivisions = 0
FEATURE [Part::Part2DObjectPython] Wire1056  label="Холл мансарды"  # Draft 2D object (typed FeaturePython)
  Area = 7160000
  ChamferSize = 0
  Closed = true
  End = (6910,2885,0)
  FilletRadius = 0
  Length = 11650
  MakeFace = true
  Placement = pos=(3685,2885,0) rot=(0,0,1;0rad)
  Points = (6) [(0,0,0),(0,2600,0),(2000,2600,0),(2000,1600,0),(3225,1600,0),(3225,0,0)]
  Start = (3685,2885,0)
  Subdivisions = 0
FEATURE [Part::Part2DObjectPython] Wire1057  label="Кладовка"  # Draft 2D object (typed FeaturePython)
  Area = 2.9145e+06
  ChamferSize = 0
  Closed = true
  End = (5685,5585,0)
  FilletRadius = 0
  Length = 6920
  MakeFace = true
  Placement = pos=(4235,5585,0) rot=(0,0,1;0rad)
  Points = (4) [(0,0,0),(1.81899e-12,2010,0),(1450,2010,0),(1450,0,0)]
  Start = (4235,5585,0)
  Subdivisions = 0
FEATURE [Part::Part2DObjectPython] Wire1058  label="Спальня #1"  # Draft 2D object (typed FeaturePython)
  Area = 2.22915e+07
  ChamferSize = 0
  Closed = true
  End = (7060,5435,0)
  FilletRadius = 0
  Length = 20715
  MakeFace = true
  Placement = pos=(7100,7595,0) rot=(0,0,1;0rad)
  Points = (12) [(-40,0,0),(3297.27,-0.000488281,0),(3297.27,-2115,0),(3500,-2115,0),(3500,-4705,0),(3297.27,-4705,0),(3297.27,-6820,0),(455,-6820,0),(455,-4815,0),+3 more]
  Start = (7060,7595,0)
  Subdivisions = 0
FEATURE [Part::FeaturePython] Structure626  label="Структура041"  # Arch/BIM 172 (typed FeaturePython)
  Base = -> Rectangle4043
  FaceMaker = 0
  Height = 1295
  HorizontalArea = 260000
  IfcData = attributes={"GlobalId": {"name": "GlobalId", "type": "IfcGloballyUniqueId", "is_enum": false, "enum_values": []}, "Description": {"... (+484 chars omitted),+1 more (map truncated)
  IfcType = 172
  Length = 0
  MoveBase = false
  MoveWithHost = false
  Nodes = (2) [(6335,7005,0),(6335,7005,1295)]
  NodesOffset = 0
  Normal = (0,0,0)
  PerimeterLength = 2520
  PredefinedType = 0
  VerticalArea = 3.2634e+06
  Width = 100
FEATURE [Part::FeaturePython] Structure627  label="Структура042"  # Arch/BIM 172 (typed FeaturePython)
  Base = -> Wire1037
  FaceMaker = 0
  Height = 1110
  HorizontalArea = 260031
  IfcData = attributes={"GlobalId": {"name": "GlobalId", "type": "IfcGloballyUniqueId", "is_enum": false, "enum_values": []}, "Description": {"... (+484 chars omitted),+1 more (map truncated)
  IfcType = 172
  Length = 0
  MoveBase = false
  MoveWithHost = false
  Nodes = (2) [(6281.57,7269.47,0),(6281.57,7269.47,1110)]
  NodesOffset = 0
  Normal = (0,0,1)
  PerimeterLength = 2533.86
  PredefinedType = 0
  VerticalArea = 2.81259e+06
  Width = 100
FEATURE [Part::FeaturePython] Structure628  label="Структура043"  # Arch/BIM 172 (typed FeaturePython)
  Base = -> Wire1038
  FaceMaker = 0
  Height = 925
  HorizontalArea = 294670
  IfcData = attributes={"GlobalId": {"name": "GlobalId", "type": "IfcGloballyUniqueId", "is_enum": false, "enum_values": []}, "Description": {"... (+484 chars omitted),+1 more (map truncated)
  IfcType = 172
  Length = 0
  MoveBase = false
  MoveWithHost = false
  Nodes = (2) [(6196.11,7599.63,0),(6196.11,7599.63,925)]
  NodesOffset = 0
  Normal = (0,0,1)
  PerimeterLength = 2800.12
  PredefinedType = 0
  VerticalArea = 2.59011e+06
  Width = 100
FEATURE [Part::FeaturePython] Structure629  label="Структура044"  # Arch/BIM 172 (typed FeaturePython)
  Base = -> Wire1039
  FaceMaker = 0
  Height = 740
  HorizontalArea = 411184
  IfcData = attributes={"GlobalId": {"name": "GlobalId", "type": "IfcGloballyUniqueId", "is_enum": false, "enum_values": []}, "Description": {"... (+484 chars omitted),+1 more (map truncated)
  IfcType = 172
  Length = 0
  MoveBase = false
  MoveWithHost = false
  Nodes = (2) [(6260.15,7969.85,0),(6260.15,7969.85,740)]
  NodesOffset = 0
  Normal = (0,0,1)
  PerimeterLength = 3195.1
  PredefinedType = 0
  VerticalArea = 2.36437e+06
  Width = 100
FEATURE [Part::FeaturePython] Structure630  label="Структура045"  # Arch/BIM 172 (typed FeaturePython)
  Base = -> Wire1040
  FaceMaker = 0
  Height = 555
  HorizontalArea = 294670
  IfcData = attributes={"GlobalId": {"name": "GlobalId", "type": "IfcGloballyUniqueId", "is_enum": false, "enum_values": []}, "Description": {"... (+484 chars omitted),+1 more (map truncated)
  IfcType = 172
  Length = 0
  MoveBase = false
  MoveWithHost = false
  Nodes = (2) [(6630.37,8033.89,0),(6630.37,8033.89,555)]
  NodesOffset = 0
  Normal = (0,0,1)
  PerimeterLength = 2800.12
  PredefinedType = 0
  VerticalArea = 1.55406e+06
  Width = 100
FEATURE [Part::FeaturePython] Structure631  label="Структура046"  # Arch/BIM 172 (typed FeaturePython)
  Base = -> Wire1041
  FaceMaker = 0
  Height = 370
  HorizontalArea = 260031
  IfcData = attributes={"GlobalId": {"name": "GlobalId", "type": "IfcGloballyUniqueId", "is_enum": false, "enum_values": []}, "Description": {"... (+484 chars omitted),+1 more (map truncated)
  IfcType = 172
  Length = 0
  MoveBase = false
  MoveWithHost = false
  Nodes = (2) [(6960.53,7948.43,0),(6960.53,7948.43,370)]
  NodesOffset = 0
  Normal = (0,0,1)
  PerimeterLength = 2533.86
  PredefinedType = 0
  VerticalArea = 937530
  Width = 100
FEATURE [Part::FeaturePython] Structure632  label="Структура047"  # Arch/BIM 172 (typed FeaturePython)
  Base = -> Rectangle4042
  FaceMaker = 0
  Height = 185
  HorizontalArea = 260000
  IfcData = attributes={"GlobalId": {"name": "GlobalId", "type": "IfcGloballyUniqueId", "is_enum": false, "enum_values": []}, "Description": {"... (+484 chars omitted),+1 more (map truncated)
  IfcType = 172
  Length = 0
  MoveBase = false
  MoveWithHost = false
  Nodes = (2) [(7225,7895,0),(7225,7895,185)]
  NodesOffset = 0
  Normal = (0,0,0)
  PerimeterLength = 2520
  PredefinedType = 0
  VerticalArea = 466200
  Width = 100
FEATURE [Part::FeaturePython] Structure633  label="Структура048"  # Arch/BIM 172 (typed FeaturePython)
  Base = -> Wire1042
  FaceMaker = 0
  Height = 925
  HorizontalArea = 260031
  IfcData = attributes={"GlobalId": {"name": "GlobalId", "type": "IfcGloballyUniqueId", "is_enum": false, "enum_values": []}, "Description": {"... (+484 chars omitted),+1 more (map truncated)
  IfcType = 172
  Length = 0
  MoveBase = false
  MoveWithHost = false
  Nodes = (2) [(5709.47,4761.57,0),(5709.47,4761.57,-925)]
  NodesOffset = 0
  Normal = (0,0,0)
  PerimeterLength = 2533.86
  Placement = pos=(0,0,3145) rot=(0,0,1;0rad)
  PredefinedType = 0
  VerticalArea = 2.34382e+06
  Width = 100
FEATURE [Part::FeaturePython] Structure634  label="Структура049"  # Arch/BIM 172 (typed FeaturePython)
  Base = -> Wire1043
  FaceMaker = 0
  Height = 740
  HorizontalArea = 294670
  IfcData = attributes={"GlobalId": {"name": "GlobalId", "type": "IfcGloballyUniqueId", "is_enum": false, "enum_values": []}, "Description": {"... (+484 chars omitted),+1 more (map truncated)
  IfcType = 172
  Length = 0
  MoveBase = false
  MoveWithHost = false
  Nodes = (2) [(6039.63,4676.11,0),(6039.63,4676.11,-740)]
  NodesOffset = 0
  Normal = (0,0,0)
  PerimeterLength = 2800.12
  Placement = pos=(0,0,2960) rot=(0,0,1;0rad)
  PredefinedType = 0
  VerticalArea = 2.07209e+06
  Width = 100
FEATURE [Part::FeaturePython] Structure635  label="Структура050"  # Arch/BIM 172 (typed FeaturePython)
  Base = -> Wire1044
  FaceMaker = 0
  Height = 555
  HorizontalArea = 411184
  IfcData = attributes={"GlobalId": {"name": "GlobalId", "type": "IfcGloballyUniqueId", "is_enum": false, "enum_values": []}, "Description": {"... (+484 chars omitted),+1 more (map truncated)
  IfcType = 172
  Length = 0
  MoveBase = false
  MoveWithHost = false
  Nodes = (2) [(6409.85,4740.15,0),(6409.85,4740.15,-555)]
  NodesOffset = 0
  Normal = (0,0,0)
  PerimeterLength = 3195.1
  Placement = pos=(0,0,2775) rot=(0,0,1;0rad)
  PredefinedType = 0
  VerticalArea = 1.77328e+06
  Width = 100
FEATURE [Part::FeaturePython] Structure636  label="Структура051"  # Arch/BIM 172 (typed FeaturePython)
  Base = -> Wire1045
  FaceMaker = 0
  Height = 370
  HorizontalArea = 294670
  IfcData = attributes={"GlobalId": {"name": "GlobalId", "type": "IfcGloballyUniqueId", "is_enum": false, "enum_values": []}, "Description": {"... (+484 chars omitted),+1 more (map truncated)
  IfcType = 172
  Length = 0
  MoveBase = false
  MoveWithHost = false
  Nodes = (2) [(6473.89,5110.37,0),(6473.89,5110.37,-370)]
  NodesOffset = 0
  Normal = (0,0,0)
  PerimeterLength = 2800.12
  Placement = pos=(0,0,2590) rot=(0,0,1;0rad)
  PredefinedType = 0
  VerticalArea = 1.03604e+06
  Width = 100
FEATURE [Part::FeaturePython] Structure637  label="Структура052"  # Arch/BIM 172 (typed FeaturePython)
  Base = -> Wire1046
  FaceMaker = 0
  Height = 185
  HorizontalArea = 260031
  IfcData = attributes={"GlobalId": {"name": "GlobalId", "type": "IfcGloballyUniqueId", "is_enum": false, "enum_values": []}, "Description": {"... (+484 chars omitted),+1 more (map truncated)
  IfcType = 172
  Length = 0
  MoveBase = false
  MoveWithHost = false
  Nodes = (2) [(6388.43,5440.53,0),(6388.43,5440.53,-185)]
  NodesOffset = 0
  Normal = (0,0,0)
  PerimeterLength = 2533.86
  Placement = pos=(0,0,2405) rot=(0,0,1;0rad)
  PredefinedType = 0
  VerticalArea = 468765
  Width = 100
FEATURE [Part::Part2DObjectPython] Rectangle4163  # Draft 2D object (typed FeaturePython)
  Area = 327600
  ChamferSize = 0
  Columns = 1
  FilletRadius = 0
  Height = 1260
  Length = 260
  MakeFace = true
  Placement = pos=(5575,4315,0) rot=(0,0,1;0rad)
  Rows = 1
FEATURE [Part::FeaturePython] Structure638  label="Структура053"  # Arch/BIM 172 (typed FeaturePython)
  Base = -> Rectangle4163
  FaceMaker = 0
  Height = 2590
  HorizontalArea = 327600
  IfcData = attributes={"GlobalId": {"name": "GlobalId", "type": "IfcGloballyUniqueId", "is_enum": false, "enum_values": []}, "Description": {"... (+484 chars omitted),+1 more (map truncated)
  IfcType = 172
  Length = 0
  MoveBase = false
  MoveWithHost = false
  Nodes = (2) [(5705,4945,0),(5705,4945,2590)]
  NodesOffset = 0
  Normal = (0,0,0)
  PerimeterLength = 3040
  PredefinedType = 0
  VerticalArea = 7873600
  Width = 100
FEATURE [Part::Part2DObjectPython] Rectangle4165  # Draft 2D object (typed FeaturePython)
  Area = 100800
  ChamferSize = 0
  Columns = 1
  FilletRadius = 0
  Height = 1260
  Length = 80
  MakeFace = true
  Placement = pos=(5575,4315,0) rot=(0,0,1;0rad)
  Rows = 1
FEATURE [Part::FeaturePython] Structure640  label="Структура055"  # Arch/BIM 172 (typed FeaturePython)
  Base = -> Rectangle4165
  FaceMaker = 0
  Height = 2960
  HorizontalArea = 100800
  IfcData = attributes={"GlobalId": {"name": "GlobalId", "type": "IfcGloballyUniqueId", "is_enum": false, "enum_values": []}, "Description": {"... (+484 chars omitted),+1 more (map truncated)
  IfcType = 172
  Length = 0
  MoveBase = false
  MoveWithHost = false
  Nodes = (2) [(5615,4945,0),(5615,4945,2960)]
  NodesOffset = 0
  Normal = (0,0,0)
  PerimeterLength = 2680
  PredefinedType = 0
  VerticalArea = 7932800
  Width = 100
FEATURE [Part::FeaturePython] Stairs  # Arch/BIM 128 (typed FeaturePython)
  AbsTop = (0,0,1480)
  Align = 0
  BlondelRatio = 0
  Flight = 0
  Height = 3000
  HorizontalArea = 0
  IfcData = attributes={"GlobalId": {"name": "GlobalId", "type": "IfcGloballyUniqueId", "is_enum": false, "enum_values": []}, "Description": {"... (+760 chars omitted),+1 more (map truncated)
  IfcType = 128
  LandingDepth = 0
  Landings = 0
  Length = 4500
  MoveBase = false
  MoveWithHost = false
  Nosing = 0
  NumberOfSteps = 8
  OutlineLeft = (2) [(0,-60,1085),(1820,-60,2380)]
  OutlineLeftAll = (2) [(0,-60,1085),(1820,-60,2380)]
  OutlineRight = (2) [(1820,-940,2380),(0,-940,1085)]
  OutlineRightAll = (2) [(1820,-940,2380),(0,-940,1085)]
  PerimeterLength = 0
  Placement = pos=(6835,7135,1110) rot=(0,0,-1;1.5708rad)
  PredefinedType = 0
  RailingHeightLeft = 900
  RailingHeightRight = 900
  RailingLeft = Rail
  RailingOffsetLeft = 60
  RailingOffsetRight = 60
  RailingRight = Rail001
  RiserHeight = 185
  RiserHeightEnforce = 185
  RiserThickness = 0
  StringerOverlap = 0
  StringerWidth = 0
  Structure = 1
  StructureOffset = 0
  StructureThickness = 150
  TreadDepth = 260
  TreadDepthEnforce = 260
  TreadThickness = 0
  VerticalArea = 0
  Width = 1000
  Winders = 0
FEATURE [Part::MultiFuse] Fusion011003002002005003006
  Shapes = -> [Structure626,Structure627,Structure628,Structure629,Structure630,Structure631,Structure632,Structure633,Structure634,Structure635,Structure636,Structure637,Stairs]
FEATURE [Part::MultiFuse] Fusion011003002002005003007
  Shapes = -> [Structure638,Structure640]
FEATURE [Part::Cut] Cut105002
  Base = -> Fusion011003002002005003006
  Tool = -> Fusion011003002002005003007
FEATURE [Part::Part2DObjectPython] Wire1061  # Draft 2D object (typed FeaturePython)
  Area = 68485.6
  ChamferSize = 0
  Closed = true
  End = (0,4535,2220)
  FilletRadius = 0
  Length = 1126.73
  MakeFace = true
  Placement = pos=(0,4315,2220) rot=(0.57735,0.57735,0.57735;2.0944rad)
  Points = (5) [(0,0,0),(0,370,0),(110,291.731,0),(220,291.731,0),(220,0,0)]
  Start = (0,4315,2220)
  Subdivisions = 0
FEATURE [Part::FeaturePython] Structure642  label="Структура057"  # Arch/BIM 172 (typed FeaturePython)
  Base = -> Wire1061
  FaceMaker = 0
  Height = 1200
  HorizontalArea = 0
  IfcData = attributes={"GlobalId": {"name": "GlobalId", "type": "IfcGloballyUniqueId", "is_enum": false, "enum_values": []}, "Description": {"... (+484 chars omitted),+1 more (map truncated)
  IfcType = 172
  Length = 0
  MoveBase = false
  MoveWithHost = false
  Nodes = (2) [(-4420.39,-105.39,2271.28),(-5620.39,-105.39,2271.28)]
  NodesOffset = 0
  Normal = (0,0,0)
  PerimeterLength = 1952.76
  Placement = pos=(6835,0,0) rot=(0,0,1;0rad)
  PredefinedType = 0
  VerticalArea = 931048
  Width = 100
FEATURE [Part::Cut] Cut105003
  Base = -> Cut105002
  Tool = -> Structure642
FEATURE [Part::Feature] Cut105003001
  shape: bbox 1780 x 4080 x 3145 mm, 90 faces (baked)
FEATURE [Part::FeaturePython] Component241023  label="лестница_001"  # Arch/BIM 0 (typed FeaturePython)
  Base = -> Cut105003001
  HorizontalArea = 0
  IfcData = attributes={"GlobalId": {"name": "GlobalId", "type": "IfcGloballyUniqueId", "is_enum": false, "enum_values": []}, "Description": {"... (+538 chars omitted),+1 more (map truncated)
  IfcType = 0
  Material = -> Material018
  MoveBase = false
  MoveWithHost = false
  PerimeterLength = 0
  PredefinedType = 0
  VerticalArea = 0
FEATURE [Part::Part2DObjectPython] Line2141  # Draft 2D object (typed FeaturePython)
  ChamferSize = 0
  Closed = true
  End = (3680,-45,0)
  FilletRadius = 0
  Length = 8460
  MakeFace = false
  Placement = pos=(-3040,2085,0) rot=(0,0,1;3.14159rad)
  Points = (2) [(-6720,-6330,0),(-6720,2130,0)]
  Start = (3680,8415,0)
  Subdivisions = 0
FEATURE [Part::FeaturePython] Structure643  label="Проём-Д90-029"  # Arch/BIM 52 (typed FeaturePython)
  Base = -> Rectangle3851
  FaceMaker = 0
  Height = 2321
  HorizontalArea = 266800
  IfcData = complex_attributes={"OwnerHistory": {}, "IsNestedBy": {}, "IsDecomposedBy": {}, "IsDefinedBy": {}, "ObjectPlacement": {}, "Representation":... (+4 chars omitted)
  IfcType = 52
  Length = 0
  MoveBase = false
  MoveWithHost = false
  Nodes = (2) [(650,-4000,0),(650,-4000,2250)]
  NodesOffset = 0
  Normal = (0,0,0)
  PerimeterLength = 2420
  Placement = pos=(0,0,-200) rot=(0,0,1;0rad)
  VerticalArea = 5.61682e+06
  Width = 100
FEATURE [Part::Part2DObjectPython] Rectangle4167  label="ПР13_001"  # Draft 2D object (typed FeaturePython)
  ChamferSize = 0
  Columns = 1
  FilletRadius = 0
  Height = 1310
  Length = 290
  MakeFace = true
  Placement = pos=(3825,4515,0) rot=(0,0,1;3.14159rad)
  Rows = 1
FEATURE [Part::FeaturePython] Structure644  label="Проём-ПР13"  # Arch/BIM 52 (typed FeaturePython)
  Base = -> Rectangle4167
  FaceMaker = 0
  Height = 2780
  HorizontalArea = 379900
  IfcData = complex_attributes={"OwnerHistory": {}, "IsNestedBy": {}, "IsDecomposedBy": {}, "IsDefinedBy": {}, "ObjectPlacement": {}, "Representation":... (+4 chars omitted)
  IfcType = 52
  Length = 0
  MoveBase = false
  MoveWithHost = false
  Nodes = (2) [(8200,3800,0),(8200,3800,2250)]
  NodesOffset = 0
  Normal = (0,0,0)
  PerimeterLength = 3200
  Placement = pos=(0,0,-200) rot=(0,0,1;0rad)
  VerticalArea = 8.896e+06
  Width = 100
FEATURE [Part::Part2DObjectPython] Line2143  label="Перемычки_066"  # Draft 2D object (typed FeaturePython)
  Area = 0
  ChamferSize = 0
  Closed = true
  End = (3680,4765,0)
  FilletRadius = 0
  Length = 1810
  MakeFace = true
  Placement = pos=(3680,2304,0) rot=(0,0,1;1.5708rad)
  Points = (2) [(651,0,0),(2461,0,0)]
  Start = (3680,2955,0)
  Subdivisions = 0
FEATURE [Part::FeaturePython] Wall564  label="Перемычка 5ПБ 18-27 001"  # Arch/BIM 166 (typed FeaturePython)
  Align = 2
  Area = 398200
  Base = -> Line2143
  BlockHeight = 0
  BlockLength = 0
  CountBroken = 0
  CountEntire = 0
  Face = 0
  GlobalId = 0U$bER0DTA2wM7MkZ_5muC
  Height = 220
  HorizontalArea = 452500
  IfcData = IfcUID=0U$bER0DTA2wM7MkZ_5muC,+2 more (map truncated)
  IfcType = 166
  Joint = 0
  Length = 1810
  MakeBlocks = false
  Material = -> Material001
  MoveBase = false
  MoveWithHost = false
  Normal = (0,0,-1)
  OffsetFirst = 0
  OffsetSecond = 0
  PerimeterLength = 4120
  Placement = pos=(0,-1.819e-12,2800) rot=(0,0,1;0rad)
  PredefinedType = 0
  VerticalArea = 906400
  Width = 250
FEATURE [Part::FeaturePython] Wall222  label="перегородка (сил.блок 500х250х80) 025"  # Arch/BIM 166 (typed FeaturePython)
  Align = 2
  Area = 14175000
  Base = -> Line1357
  BlockHeight = 250
  BlockLength = 0
  CountBroken = 0
  CountEntire = 0
  Face = 0
  Height = 3000
  HorizontalArea = 522000
  IfcType = 166
  Joint = 0
  Length = 4725
  MakeBlocks = false
  Material = -> Material009
  MoveBase = false
  MoveWithHost = false
  Normal = (0,0,0)
  OffsetFirst = 300
  OffsetSecond = 50
  PerimeterLength = 0
  Placement = pos=(0,0,-200) rot=(0,0,1;0rad)
  PredefinedType = 0
  Subtractions = -> [Structure026,Structure021,Wall564]
  VerticalArea = 20883200
  Width = 80
FEATURE [Part::Part2DObjectPython] Rectangle4168  label="ОК-144-006"  # Draft 2D object (typed FeaturePython)
  ChamferSize = 0
  Columns = 1
  FilletRadius = 0
  Height = 410
  Length = 1700
  MakeFace = true
  Placement = pos=(-30,1320,0) rot=(0,0,1;1.5708rad)
  Rows = 1
FEATURE [Part::FeaturePython] Structure645  label="Проём_внеш.стена_029"  # Arch/BIM 52 (typed FeaturePython)
  Base = -> Rectangle4168
  FaceMaker = 0
  Height = 1617
  HorizontalArea = 697000
  IfcData = complex_attributes={"OwnerHistory": {}, "IsNestedBy": {}, "IsDecomposedBy": {}, "IsDefinedBy": {}, "ObjectPlacement": {}, "Representation":... (+4 chars omitted)
  IfcType = 52
  Length = 0
  MoveBase = false
  MoveWithHost = false
  Nodes = (2) [(-8120,-170,0),(-8120,-170,1500)]
  NodesOffset = 0
  Normal = (0,0,0)
  PerimeterLength = 4220
  Placement = pos=(0,0,955) rot=(0,0,1;0rad)
  VerticalArea = 6.82374e+06
  Width = 100
FEATURE [Part::FeaturePython] Structure646  label="Проём_внеш.стена_030"  # Arch/BIM 52 (typed FeaturePython)
  Base = -> Rectangle3871
  FaceMaker = 0
  Height = 2772
  HorizontalArea = 590400
  IfcData = complex_attributes={"OwnerHistory": {}, "IsNestedBy": {}, "IsDecomposedBy": {}, "IsDefinedBy": {}, "ObjectPlacement": {}, "Representation":... (+4 chars omitted)
  IfcType = 52
  Length = 0
  MoveBase = false
  MoveWithHost = false
  Nodes = (2) [(6195,-230,0),(6195,-230,2541)]
  NodesOffset = 0
  Normal = (0,0,0)
  PerimeterLength = 3700
  Placement = pos=(0,0,-200) rot=(0,0,1;0rad)
  VerticalArea = 10256400
  Width = 100
FEATURE [Part::FeaturePython] Structure647  label="Проём_внеш.стена_028"  # Arch/BIM 52 (typed FeaturePython)
  Base = -> Rectangle3872
  FaceMaker = 0
  Height = 1617
  HorizontalArea = 697000
  IfcData = complex_attributes={"OwnerHistory": {}, "IsNestedBy": {}, "IsDecomposedBy": {}, "IsDefinedBy": {}, "ObjectPlacement": {}, "Representation":... (+4 chars omitted)
  IfcType = 52
  Length = 0
  MoveBase = false
  MoveWithHost = false
  Nodes = (2) [(4745,-225,0),(4745,-225,1350)]
  NodesOffset = 0
  Normal = (0,0,0)
  PerimeterLength = 4220
  Placement = pos=(0,0,955) rot=(0,0,1;0rad)
  VerticalArea = 6.82374e+06
  Width = 100
FEATURE [Part::FeaturePython] Structure648  label="Проём_внеш.стена_001"  # Arch/BIM 52 (typed FeaturePython)
  Base = -> Rectangle3873
  FaceMaker = 0
  Height = 1617
  HorizontalArea = 483800
  IfcData = complex_attributes={"OwnerHistory": {}, "IsNestedBy": {}, "IsDecomposedBy": {}, "IsDefinedBy": {}, "ObjectPlacement": {}, "Representation":... (+4 chars omitted)
  IfcType = 52
  Length = 0
  MoveBase = false
  MoveWithHost = false
  Nodes = (2) [(1035,250,0),(1035,250,600)]
  NodesOffset = 0
  Normal = (0,0,0)
  PerimeterLength = 3180
  Placement = pos=(0,0,955) rot=(0,0,1;0rad)
  VerticalArea = 5142060
  Width = 100
FEATURE [Part::FeaturePython] Structure649  label="Проём_внеш.стена_027"  # Arch/BIM 52 (typed FeaturePython)
  Base = -> Rectangle4025
  FaceMaker = 0
  Height = 2772
  HorizontalArea = 803600
  IfcData = complex_attributes={"OwnerHistory": {}, "IsNestedBy": {}, "IsDecomposedBy": {}, "IsDefinedBy": {}, "ObjectPlacement": {}, "Representation":... (+4 chars omitted)
  IfcType = 52
  Length = 0
  MoveBase = false
  MoveWithHost = false
  Nodes = (2) [(1035,250,0),(1035,250,600)]
  NodesOffset = 0
  Normal = (0,0,0)
  PerimeterLength = 4740
  Placement = pos=(0,0,-200) rot=(0,0,1;0rad)
  VerticalArea = 13139280
  Width = 100
FEATURE [Part::FeaturePython] Structure650  label="Проём_внеш.стена_026"  # Arch/BIM 52 (typed FeaturePython)
  Base = -> Rectangle4021
  FaceMaker = 0
  Height = 1617
  HorizontalArea = 377200
  IfcData = complex_attributes={"OwnerHistory": {}, "IsNestedBy": {}, "IsDecomposedBy": {}, "IsDefinedBy": {}, "ObjectPlacement": {}, "Representation":... (+4 chars omitted)
  IfcType = 52
  Length = 0
  MoveBase = false
  MoveWithHost = false
  Nodes = (2) [(1035,250,0),(1035,250,600)]
  NodesOffset = 0
  Normal = (0,0,0)
  PerimeterLength = 2660
  Placement = pos=(0,0,955) rot=(0,0,1;0rad)
  VerticalArea = 4301220
  Width = 100
FEATURE [Part::FeaturePython] Structure651  label="Проём_внеш.стена_025"  # Arch/BIM 52 (typed FeaturePython)
  Base = -> Rectangle3875
  FaceMaker = 0
  Height = 1617
  HorizontalArea = 803600
  IfcData = complex_attributes={"OwnerHistory": {}, "IsNestedBy": {}, "IsDecomposedBy": {}, "IsDefinedBy": {}, "ObjectPlacement": {}, "Representation":... (+4 chars omitted)
  IfcType = 52
  Length = 0
  MoveBase = false
  MoveWithHost = false
  Nodes = (2) [(1035,250,0),(1035,250,600)]
  NodesOffset = 0
  Normal = (0,0,0)
  PerimeterLength = 4740
  Placement = pos=(0,0,955) rot=(0,0,1;0rad)
  VerticalArea = 7664580
  Width = 100
FEATURE [Part::FeaturePython] Structure652  label="Проём_внеш.стена_031"  # Arch/BIM 52 (typed FeaturePython)
  Base = -> Rectangle3837
  FaceMaker = 0
  Height = 1617
  HorizontalArea = 270600
  IfcData = complex_attributes={"OwnerHistory": {}, "IsNestedBy": {}, "IsDecomposedBy": {}, "IsDefinedBy": {}, "ObjectPlacement": {}, "Representation":... (+4 chars omitted)
  IfcType = 52
  Length = 0
  MoveBase = false
  MoveWithHost = false
  Nodes = (2) [(4618,-185,0),(4618,-185,1386)]
  NodesOffset = 0
  Normal = (0,0,0)
  PerimeterLength = 2140
  Placement = pos=(0,0,955) rot=(0,0,1;0rad)
  VerticalArea = 3.46038e+06
  Width = 100
FEATURE [Part::FeaturePython] Structure653  label="Проём_внеш.стена_032"  # Arch/BIM 52 (typed FeaturePython)
  Base = -> Rectangle3836
  FaceMaker = 0
  Height = 1617
  HorizontalArea = 270600
  IfcData = complex_attributes={"OwnerHistory": {}, "IsNestedBy": {}, "IsDecomposedBy": {}, "IsDefinedBy": {}, "ObjectPlacement": {}, "Representation":... (+4 chars omitted)
  IfcType = 52
  Length = 0
  MoveBase = false
  MoveWithHost = false
  Nodes = (2) [(7495,-230,0),(7495,-230,1617)]
  NodesOffset = 0
  Normal = (0,0,0)
  PerimeterLength = 2140
  Placement = pos=(0,0,955) rot=(0,0,1;0rad)
  VerticalArea = 3.46038e+06
  Width = 100
FEATURE [Part::FeaturePython] Wall232  label="Покрытие СУ плиткой 20мм"  # Arch/BIM 166 (typed FeaturePython)
  Align = 1
  Area = 17920000
  Base = -> Wire1000
  BlockHeight = 0
  BlockLength = 0
  CountBroken = 0
  CountEntire = 0
  Face = 0
  GlobalId = 0fSn5rz2v1yx1CM9t4dxRk
  Height = 2800
  HorizontalArea = 0
  IfcData = IfcUID=0fSn5rz2v1yx1CM9t4dxRk,+2 more (map truncated)
  IfcType = 166
  Joint = 0
  Length = 6400
  MakeBlocks = false
  Material = -> Material005
  MoveBase = false
  MoveWithHost = false
  Normal = (0,0,0)
  OffsetFirst = 0
  OffsetSecond = 0
  PerimeterLength = 0
  PredefinedType = 0
  Subtractions = -> [Structure550,Structure543,Structure653]
  VerticalArea = 0
  Width = 20
FEATURE [Part::Part2DObjectPython] Line2146  label="Перемычки_067"  # Draft 2D object (typed FeaturePython)
  Area = 0
  ChamferSize = 0
  Closed = true
  End = (3395,8540,0)
  FilletRadius = 0
  Length = 2460
  MakeFace = true
  Placement = pos=(852,8540,0) rot=(0,0,1;0rad)
  Points = (2) [(83,0,0),(2543,0,0)]
  Start = (935,8540,0)
  Subdivisions = 0
FEATURE [Part::FeaturePython] Wall282  label="Утепление перемычки XPS 100+30mm 001"  # Arch/BIM 166 (typed FeaturePython)
  Align = 1
  Area = 560880
  Base = -> Line2146
  BlockHeight = 0
  BlockLength = 0
  CountBroken = 0
  CountEntire = 0
  Face = 0
  Height = 228
  HorizontalArea = 319800
  IfcData = attributes={"GlobalId": {"name": "GlobalId", "type": "IfcGloballyUniqueId", "is_enum": false, "enum_values": []}, "Description": {"... (+533 chars omitted),+1 more (map truncated)
  IfcType = 166
  Joint = 0
  Length = 2460
  MakeBlocks = false
  Material = -> Material002
  MoveBase = false
  MoveWithHost = false
  Normal = (0,0,0)
  Offset = 125
  OffsetFirst = 0
  OffsetSecond = 0
  PerimeterLength = 5180
  Placement = pos=(0,0,2572) rot=(0,0,1;0rad)
  PredefinedType = 0
  VerticalArea = 1181040
  Width = 130
FEATURE [Part::Part2DObjectPython] Line2147  label="Перемычки_068"  # Draft 2D object (typed FeaturePython)
  Area = 0
  ChamferSize = 0
  Closed = true
  End = (5020,8540,0)
  FilletRadius = 0
  Length = 1290
  MakeFace = true
  Placement = pos=(3079,8540,0) rot=(0,0,1;0rad)
  Points = (2) [(651,0,0),(1941,0,0)]
  Start = (3730,8540,0)
  Subdivisions = 0
FEATURE [Part::FeaturePython] Wall284  label="Утепление перемычки XPS 100+30mm 002"  # Arch/BIM 166 (typed FeaturePython)
  Align = 1
  Area = 294120
  Base = -> Line2147
  BlockHeight = 0
  BlockLength = 0
  CountBroken = 0
  CountEntire = 0
  Face = 0
  Height = 228
  HorizontalArea = 167700
  IfcData = attributes={"GlobalId": {"name": "GlobalId", "type": "IfcGloballyUniqueId", "is_enum": false, "enum_values": []}, "Description": {"... (+533 chars omitted),+1 more (map truncated)
  IfcType = 166
  Joint = 0
  Length = 1290
  MakeBlocks = false
  Material = -> Material002
  MoveBase = false
  MoveWithHost = false
  Normal = (0,0,0)
  Offset = 125
  OffsetFirst = 0
  OffsetSecond = 0
  PerimeterLength = 2840
  Placement = pos=(0,0,2572) rot=(0,0,1;0rad)
  PredefinedType = 0
  VerticalArea = 647520
  Width = 130
FEATURE [Part::Part2DObjectPython] Line2148  label="Перемычки_069"  # Draft 2D object (typed FeaturePython)
  Area = 0
  ChamferSize = 0
  Closed = true
  End = (6190,-170,0)
  FilletRadius = 0
  Length = 1810
  MakeFace = true
  Placement = pos=(3795,-170,0) rot=(0,0,1;0rad)
  Points = (2) [(585,0,0),(2395,0,0)]
  Start = (4380,-170,0)
  Subdivisions = 0
FEATURE [Part::FeaturePython] Wall288  label="Утепление перемычки XPS 100+30mm 048"  # Arch/BIM 166 (typed FeaturePython)
  Align = 0
  Area = 412680
  Base = -> Line2148
  BlockHeight = 0
  BlockLength = 0
  CountBroken = 0
  CountEntire = 0
  Face = 0
  Height = 228
  HorizontalArea = 235300
  IfcData = attributes={"GlobalId": {"name": "GlobalId", "type": "IfcGloballyUniqueId", "is_enum": false, "enum_values": []}, "Description": {"... (+533 chars omitted),+1 more (map truncated)
  IfcType = 166
  Joint = 0
  Length = 1810
  MakeBlocks = false
  Material = -> Material002
  MoveBase = false
  MoveWithHost = false
  Normal = (0,0,0)
  Offset = 125
  OffsetFirst = 0
  OffsetSecond = 0
  PerimeterLength = 3880
  Placement = pos=(0,0,2572) rot=(0,0,1;0rad)
  PredefinedType = 0
  VerticalArea = 884640
  Width = 130
FEATURE [Part::Part2DObjectPython] Line2149  label="Перемычки_070"  # Draft 2D object (typed FeaturePython)
  Area = 0
  ChamferSize = 0
  Closed = true
  End = (8140,-170,0)
  FilletRadius = 0
  Length = 1290
  MakeFace = true
  Placement = pos=(6070,-170,0) rot=(0,0,1;0rad)
  Points = (2) [(780,1.13687e-12,0),(2070,1.13687e-12,0)]
  Start = (6850,-170,0)
  Subdivisions = 0
FEATURE [Part::FeaturePython] Wall286  label="Утепление перемычки XPS 100+30mm 028"  # Arch/BIM 166 (typed FeaturePython)
  Align = 0
  Area = 294120
  Base = -> Line2149
  BlockHeight = 0
  BlockLength = 0
  CountBroken = 0
  CountEntire = 0
  Face = 0
  Height = 228
  HorizontalArea = 167700
  IfcData = attributes={"GlobalId": {"name": "GlobalId", "type": "IfcGloballyUniqueId", "is_enum": false, "enum_values": []}, "Description": {"... (+533 chars omitted),+1 more (map truncated)
  IfcType = 166
  Joint = 0
  Length = 1290
  MakeBlocks = false
  Material = -> Material002
  MoveBase = false
  MoveWithHost = false
  Normal = (0,0,0)
  Offset = 125
  OffsetFirst = 0
  OffsetSecond = 0
  PerimeterLength = 2840
  Placement = pos=(0,0,2572) rot=(0,0,1;0rad)
  PredefinedType = 0
  VerticalArea = 647520
  Width = 130
FEATURE [Part::Part2DObjectPython] Line2150  label="Перемычки_071"  # Draft 2D object (typed FeaturePython)
  Area = 0
  ChamferSize = 0
  Closed = true
  End = (10745,1275,0)
  FilletRadius = 0
  Length = 1550
  MakeFace = true
  Placement = pos=(7435,130,0) rot=(0,0,1;0rad)
  Points = (2) [(3310,2695,0),(3310,1145,0)]
  Start = (10745,2825,0)
  Subdivisions = 0
FEATURE [Part::FeaturePython] Wall289  label="Утепление перемычки XPS 100+30mm 047"  # Arch/BIM 166 (typed FeaturePython)
  Align = 1
  Area = 353400
  Base = -> Line2150
  BlockHeight = 0
  BlockLength = 0
  CountBroken = 0
  CountEntire = 0
  Face = 0
  Height = 228
  HorizontalArea = 201500
  IfcData = attributes={"GlobalId": {"name": "GlobalId", "type": "IfcGloballyUniqueId", "is_enum": false, "enum_values": []}, "Description": {"... (+533 chars omitted),+1 more (map truncated)
  IfcType = 166
  Joint = 0
  Length = 1550
  MakeBlocks = false
  Material = -> Material002
  MoveBase = false
  MoveWithHost = false
  Normal = (0,0,0)
  Offset = 125
  OffsetFirst = 0
  OffsetSecond = 0
  PerimeterLength = 3360
  Placement = pos=(0,0,2572) rot=(0,0,1;0rad)
  PredefinedType = 0
  VerticalArea = 766080
  Width = 130
FEATURE [Part::Part2DObjectPython] Line2151  label="Перемычки_072"  # Draft 2D object (typed FeaturePython)
  Area = 0
  ChamferSize = 0
  Closed = true
  End = (-175,1135,0)
  FilletRadius = 0
  Length = 2070
  MakeFace = true
  Placement = pos=(-3485,755,0) rot=(0,0,1;0rad)
  Points = (2) [(3310,2450,0),(3310,380,0)]
  Start = (-175,3205,0)
  Subdivisions = 0
FEATURE [Part::FeaturePython] Wall285  label="Утепление перемычки XPS 100+30mm 050"  # Arch/BIM 166 (typed FeaturePython)
  Align = 0
  Area = 471960
  Base = -> Line2151
  BlockHeight = 0
  BlockLength = 0
  CountBroken = 0
  CountEntire = 0
  Face = 0
  Height = 228
  HorizontalArea = 269100
  IfcData = attributes={"GlobalId": {"name": "GlobalId", "type": "IfcGloballyUniqueId", "is_enum": false, "enum_values": []}, "Description": {"... (+533 chars omitted),+1 more (map truncated)
  IfcType = 166
  Joint = 0
  Length = 2070
  MakeBlocks = false
  Material = -> Material002
  MoveBase = false
  MoveWithHost = false
  Normal = (0,0,0)
  Offset = 125
  OffsetFirst = 0
  OffsetSecond = 0
  PerimeterLength = 4400
  Placement = pos=(0,0,2572) rot=(0,0,1;0rad)
  PredefinedType = 0
  VerticalArea = 1003200
  Width = 130
FEATURE [Part::Part2DObjectPython] Line2152  label="Перемычки_073"  # Draft 2D object (typed FeaturePython)
  Area = 0
  ChamferSize = 0
  Closed = true
  End = (10745,3355,0)
  FilletRadius = 0
  Length = 2070
  MakeFace = true
  Placement = pos=(7435,3284,0) rot=(0,0,1;0rad)
  Points = (2) [(3310,2141,0),(3310,71,0)]
  Start = (10745,5425,0)
  Subdivisions = 0
FEATURE [Part::FeaturePython] Wall290  label="Утепление перемычки XPS 100+30mm 046"  # Arch/BIM 166 (typed FeaturePython)
  Align = 1
  Area = 471960
  Base = -> Line2152
  BlockHeight = 0
  BlockLength = 0
  CountBroken = 0
  CountEntire = 0
  Face = 0
  Height = 228
  HorizontalArea = 269100
  IfcData = attributes={"GlobalId": {"name": "GlobalId", "type": "IfcGloballyUniqueId", "is_enum": false, "enum_values": []}, "Description": {"... (+533 chars omitted),+1 more (map truncated)
  IfcType = 166
  Joint = 0
  Length = 2070
  MakeBlocks = false
  Material = -> Material002
  MoveBase = false
  MoveWithHost = false
  Normal = (0,0,0)
  Offset = 125
  OffsetFirst = 0
  OffsetSecond = 0
  PerimeterLength = 4400
  Placement = pos=(0,0,2572) rot=(0,0,1;0rad)
  PredefinedType = 0
  VerticalArea = 1003200
  Width = 130
FEATURE [Part::Part2DObjectPython] Line2153  label="Перемычки_074"  # Draft 2D object (typed FeaturePython)
  Area = 0
  ChamferSize = 0
  Closed = true
  End = (3720,-170,0)
  FilletRadius = 0
  Length = 1290
  MakeFace = true
  Placement = pos=(1650,-170,0) rot=(0,0,1;0rad)
  Points = (2) [(780,1.13687e-12,0),(2070,1.13687e-12,0)]
  Start = (2430,-170,0)
  Subdivisions = 0
FEATURE [Part::FeaturePython] Wall565  label="Перем.2шт. 3ПБ 13-37 003"  # Arch/BIM 166 (typed FeaturePython)
  Align = 2
  Area = 297990
  Base = -> Line2153
  BlockHeight = 0
  BlockLength = 0
  CountBroken = 0
  CountEntire = 0
  Face = 0
  GlobalId = 2dIW8Z8qb1VQVoHMf0gHj5
  Height = 231
  HorizontalArea = 322500
  IfcData = IfcUID=2dIW8Z8qb1VQVoHMf0gHj5,+2 more (map truncated)
  IfcType = 166
  Joint = 0
  Length = 1290
  MakeBlocks = false
  Material = -> Material001
  MoveBase = false
  MoveWithHost = false
  Normal = (0,0,0)
  OffsetFirst = 0
  OffsetSecond = 0
  PerimeterLength = 3080
  Placement = pos=(0,0,2572) rot=(0,0,1;0rad)
  PredefinedType = 0
  VerticalArea = 711480
  Width = 250
FEATURE [Part::FeaturePython] Wall283  label="Утепление перемычки XPS 100+30mm 049"  # Arch/BIM 166 (typed FeaturePython)
  Align = 0
  Area = 294120
  Base = -> Line2153
  BlockHeight = 0
  BlockLength = 0
  CountBroken = 0
  CountEntire = 0
  Face = 0
  Height = 228
  HorizontalArea = 167700
  IfcData = attributes={"GlobalId": {"name": "GlobalId", "type": "IfcGloballyUniqueId", "is_enum": false, "enum_values": []}, "Description": {"... (+533 chars omitted),+1 more (map truncated)
  IfcType = 166
  Joint = 0
  Length = 1290
  MakeBlocks = false
  Material = -> Material002
  MoveBase = false
  MoveWithHost = false
  Normal = (0,0,0)
  Offset = 125
  OffsetFirst = 0
  OffsetSecond = 0
  PerimeterLength = 2840
  Placement = pos=(0,0,2572) rot=(0,0,1;0rad)
  PredefinedType = 0
  VerticalArea = 647520
  Width = 130
FEATURE [Part::Part2DObjectPython] Line2154  label="Перемычки_075"  # Draft 2D object (typed FeaturePython)
  Area = 0
  ChamferSize = 0
  Closed = true
  End = (9635,8540,0)
  FilletRadius = 0
  Length = 2460
  MakeFace = true
  Placement = pos=(7092,8540,0) rot=(0,0,1;0rad)
  Points = (2) [(83,0,0),(2543,0,0)]
  Start = (7175,8540,0)
  Subdivisions = 0
FEATURE [Part::FeaturePython] Wall566  label="Перемычка 5ПБ 25-27 002"  # Arch/BIM 166 (typed FeaturePython)
  Align = 2
  Area = 560880
  Base = -> Line2154
  BlockHeight = 0
  BlockLength = 0
  CountBroken = 0
  CountEntire = 0
  Face = 0
  GlobalId = 3keULZXVT8QA_IAgUQCOo2
  Height = 228
  HorizontalArea = 615000
  IfcData = IfcUID=3keULZXVT8QA_IAgUQCOo2,+2 more (map truncated)
  IfcType = 166
  Joint = 0
  Length = 2460
  MakeBlocks = false
  Material = -> Material001
  MoveBase = false
  MoveWithHost = false
  Normal = (0,0,0)
  OffsetFirst = 0
  OffsetSecond = 0
  PerimeterLength = 5420
  Placement = pos=(0,-9.09e-13,2572) rot=(0,0,1;0rad)
  PredefinedType = 0
  VerticalArea = 1.23576e+06
  Width = 250
FEATURE [Part::FeaturePython] Wall287  label="Утепление перемычки XPS 100+30mm 045"  # Arch/BIM 166 (typed FeaturePython)
  Align = 1
  Area = 560880
  Base = -> Line2154
  BlockHeight = 0
  BlockLength = 0
  CountBroken = 0
  CountEntire = 0
  Face = 0
  Height = 228
  HorizontalArea = 319800
  IfcData = attributes={"GlobalId": {"name": "GlobalId", "type": "IfcGloballyUniqueId", "is_enum": false, "enum_values": []}, "Description": {"... (+533 chars omitted),+1 more (map truncated)
  IfcType = 166
  Joint = 0
  Length = 2460
  MakeBlocks = false
  Material = -> Material002
  MoveBase = false
  MoveWithHost = false
  Normal = (0,0,0)
  Offset = 125
  OffsetFirst = 0
  OffsetSecond = 0
  PerimeterLength = 5180
  Placement = pos=(0,-9.09e-13,2572) rot=(0,0,1;0rad)
  PredefinedType = 0
  VerticalArea = 1.18104e+06
  Width = 130
FEATURE [App::GeometryPython] BuildingPart089  label="Утепление перемычек XPS 100+30mm"  # Arch/BIM 52 (typed FeaturePython)
  Area = 3714120
  GlobalId = 1IqJZ7MUv7eQPyUTFsu7$l
  Group = -> [Wall285,Wall282,Wall284,Wall287,Wall290,Wall289,Wall283,Wall288,Wall286]
  Height = 0
  HeightPropagate = true
  IfcData = IfcUID=1IqJZ7MUv7eQPyUTFsu7$l,+2 more (map truncated)
  IfcType = 52
  LevelOffset = 0
FEATURE [Part::FeaturePython] Wall568  label="Перемычка 5ПБ 25-27 001"  # Arch/BIM 166 (typed FeaturePython)
  Align = 2
  Area = 560880
  Base = -> Line2146
  BlockHeight = 0
  BlockLength = 0
  CountBroken = 0
  CountEntire = 0
  Face = 0
  GlobalId = 2_OOPfC1L9nOo2BwNBJ59E
  Height = 228
  HorizontalArea = 615000
  IfcData = IfcUID=2_OOPfC1L9nOo2BwNBJ59E,+2 more (map truncated)
  IfcType = 166
  Joint = 0
  Length = 2460
  MakeBlocks = false
  Material = -> Material001
  MoveBase = false
  MoveWithHost = false
  Normal = (0,0,0)
  OffsetFirst = 0
  OffsetSecond = 0
  PerimeterLength = 5420
  Placement = pos=(0,0,2572) rot=(0,0,1;0rad)
  PredefinedType = 0
  VerticalArea = 1235760
  Width = 250
FEATURE [Part::FeaturePython] Wall569  label="Перем.2шт. 3ПБ 13-37 002"  # Arch/BIM 166 (typed FeaturePython)
  Align = 2
  Area = 294120
  Base = -> Line2147
  BlockHeight = 0
  BlockLength = 0
  CountBroken = 0
  CountEntire = 0
  Face = 0
  GlobalId = 02zZ5o_1DBJf0p5Hr4GWva
  Height = 228
  HorizontalArea = 322500
  IfcData = IfcUID=02zZ5o_1DBJf0p5Hr4GWva,+2 more (map truncated)
  IfcType = 166
  Joint = 0
  Length = 1290
  MakeBlocks = false
  Material = -> Material001
  MoveBase = false
  MoveWithHost = false
  Normal = (0,0,0)
  OffsetFirst = 0
  OffsetSecond = 0
  PerimeterLength = 3080
  Placement = pos=(0,0,2572) rot=(0,0,1;0rad)
  PredefinedType = 0
  VerticalArea = 702240
  Width = 250
FEATURE [Part::FeaturePython] Wall570  label="Перемычка 5ПБ 18-27 003"  # Arch/BIM 166 (typed FeaturePython)
  Align = 2
  Area = 418110
  Base = -> Line2148
  BlockHeight = 0
  BlockLength = 0
  CountBroken = 0
  CountEntire = 0
  Face = 0
  GlobalId = 2Km2nGMYj6_hkYj1EJr8Pd
  Height = 231
  HorizontalArea = 452500
  IfcData = IfcUID=2Km2nGMYj6_hkYj1EJr8Pd,+2 more (map truncated)
  IfcType = 166
  Joint = 0
  Length = 1810
  MakeBlocks = false
  Material = -> Material001
  MoveBase = false
  MoveWithHost = false
  Normal = (0,0,0)
  OffsetFirst = 0
  OffsetSecond = 0
  PerimeterLength = 4120
  Placement = pos=(0,0,2572) rot=(0,0,1;0rad)
  PredefinedType = 0
  VerticalArea = 951720
  Width = 250
FEATURE [Part::FeaturePython] Wall571  label="Перем.2шт. 3ПБ 13-37 004"  # Arch/BIM 166 (typed FeaturePython)
  Align = 2
  Area = 297990
  Base = -> Line2149
  BlockHeight = 0
  BlockLength = 0
  CountBroken = 0
  CountEntire = 0
  Face = 0
  GlobalId = 16$DxRw$TB6BfQSNqz60Qz
  Height = 231
  HorizontalArea = 322500
  IfcData = IfcUID=16$DxRw$TB6BfQSNqz60Qz,+2 more (map truncated)
  IfcType = 166
  Joint = 0
  Length = 1290
  MakeBlocks = false
  Material = -> Material001
  MoveBase = false
  MoveWithHost = false
  Normal = (0,0,0)
  OffsetFirst = 0
  OffsetSecond = 0
  PerimeterLength = 3080
  Placement = pos=(0,0,2572) rot=(0,0,1;0rad)
  PredefinedType = 0
  VerticalArea = 711480
  Width = 250
FEATURE [Part::FeaturePython] Wall572  label="Перем.2шт. 3ПБ 16-37 001"  # Arch/BIM 166 (typed FeaturePython)
  Align = 2
  Area = 353400
  Base = -> Line2150
  BlockHeight = 0
  BlockLength = 0
  CountBroken = 0
  CountEntire = 0
  Face = 0
  GlobalId = 0AqGC86W9B8PvMAPbhOTte
  Height = 228
  HorizontalArea = 387500
  IfcData = IfcUID=0AqGC86W9B8PvMAPbhOTte,+2 more (map truncated)
  IfcType = 166
  Joint = 0
  Length = 1550
  MakeBlocks = false
  Material = -> Material001
  MoveBase = false
  MoveWithHost = false
  Normal = (0,0,0)
  OffsetFirst = 0
  OffsetSecond = 0
  PerimeterLength = 3600
  Placement = pos=(0,0,2572) rot=(0,0,1;0rad)
  PredefinedType = 0
  VerticalArea = 820800
  Width = 250
FEATURE [Part::FeaturePython] Wall573  label="Перемычка 5ПБ 18-27 002"  # Arch/BIM 166 (typed FeaturePython)
  Align = 2
  Area = 471960
  Base = -> Line2151
  BlockHeight = 0
  BlockLength = 0
  CountBroken = 0
  CountEntire = 0
  Face = 0
  GlobalId = 23sFNS3FX7B9N2mOSbHlu1
  Height = 228
  HorizontalArea = 517500
  IfcData = IfcUID=23sFNS3FX7B9N2mOSbHlu1,+2 more (map truncated)
  IfcType = 166
  Joint = 0
  Length = 2070
  MakeBlocks = false
  Material = -> Material001
  MoveBase = false
  MoveWithHost = false
  Normal = (0,0,0)
  OffsetFirst = 0
  OffsetSecond = 0
  PerimeterLength = 4640
  Placement = pos=(0,0,2572) rot=(0,0,1;0rad)
  PredefinedType = 0
  VerticalArea = 1057920
  Width = 250
FEATURE [Part::FeaturePython] Wall574  label="Перемычка 5ПБ 21-27 001"  # Arch/BIM 166 (typed FeaturePython)
  Align = 2
  Area = 471960
  Base = -> Line2152
  BlockHeight = 0
  BlockLength = 0
  CountBroken = 0
  CountEntire = 0
  Face = 0
  GlobalId = 2TdxzIhfb2oA4zfHjvmbo2
  Height = 228
  HorizontalArea = 517500
  IfcData = IfcUID=2TdxzIhfb2oA4zfHjvmbo2,+2 more (map truncated)
  IfcType = 166
  Joint = 0
  Length = 2070
  MakeBlocks = false
  Material = -> Material001
  MoveBase = false
  MoveWithHost = false
  Normal = (0,0,0)
  OffsetFirst = 0
  OffsetSecond = 0
  PerimeterLength = 4640
  Placement = pos=(0,0,2572) rot=(0,0,1;0rad)
  PredefinedType = 0
  VerticalArea = 1057920
  Width = 250
FEATURE [App::GeometryPython] BuildingPart088  label="Перемычки по ГОСТ 948-2016"  # Arch/BIM 52 (typed FeaturePython)
  Area = 5832690
  GlobalId = 3$YVGVb81DNfcCDGoK7nvQ
  Group = -> [Wall277,Wall278,Wall281,Wall497,Wall564,Wall568,Wall569,Wall566,Wall574,Wall572,Wall573,Wall565,Wall570,Wall571]
  Height = 0
  HeightPropagate = true
  IfcData = IfcUID=3$YVGVb81DNfcCDGoK7nvQ,+2 more (map truncated)
  IfcType = 52
  LevelOffset = 0
FEATURE [Part::FeaturePython] Wall567  label="Внешняя стена Поротерм 38Т 380мм"  # Arch/BIM 166 (typed FeaturePython)
  Align = 0
  Area = 114780000
  Base = -> Rectangle3870
  BlockHeight = 231
  BlockLength = 0
  CountBroken = 0
  CountEntire = 0
  Face = 0
  GlobalId = 15i3vb4BrBERo7sMNULkP3
  Height = 3000
  HorizontalArea = 0
  IfcData = IfcUID=15i3vb4BrBERo7sMNULkP3,+2 more (map truncated)
  IfcType = 166
  Joint = 0
  Length = 38260
  MakeBlocks = true
  Material = -> Material004
  MoveBase = false
  MoveWithHost = false
  Normal = (0,0,1)
  OffsetFirst = 0
  OffsetSecond = 0
  PerimeterLength = 0
  Placement = pos=(0,0,-200) rot=(0,0,1;0rad)
  PredefinedType = 0
  Subtractions = -> [Structure651,Structure650,Structure649,Structure647,Structure645,Structure646,Structure652,Structure653,Structure648,Wall568,Wall569,Wall566,Wall574,Wall572,Wall573,Wall565,Wall570,Wall571,Wall285,Wall282,Wall284,Wall287,Wall290,Wall289,Wall283,Wall288,Wall286]
  VerticalArea = 0
  Width = 380
FEATURE [Part::Part2DObjectPython] Line2159  # Draft 2D object (typed FeaturePython)
  ChamferSize = 0
  Closed = true
  End = (6980,5675,0)
  FilletRadius = 0
  Length = 1160
  MakeFace = false
  Placement = pos=(4290,9790,0) rot=(0,0,1;1.5708rad)
  Points = (2) [(-5275,-2690,0),(-4115,-2690,0)]
  Start = (6980,4515,0)
  Subdivisions = 0
FEATURE [Part::FeaturePython] Wall579  label="Несущая стена 2.1нф 250мм внутренняя002"  # Arch/BIM 166 (typed FeaturePython)
  Align = 2
  Area = 3.48e+06
  Base = -> Line2159
  BlockHeight = 231
  BlockLength = 0
  CountBroken = 0
  CountEntire = 0
  Face = 0
  GlobalId = 1uw9ZyZ5vAkuN6nr$sWkBP
  Height = 3000
  HorizontalArea = 0
  IfcData = IfcUID=1uw9ZyZ5vAkuN6nr$sWkBP; attributes={"GlobalId": {"value": "1uw9ZyZ5vAkuN6nr$sWkBP"}}
  IfcType = 166
  Joint = 0
  Length = 1160
  MakeBlocks = true
  Material = -> Material009
  MoveBase = false
  MoveWithHost = false
  Normal = (0,0,1)
  OffsetFirst = 0
  OffsetSecond = 500
  PerimeterLength = 0
  Placement = pos=(0,0,-200) rot=(0,0,1;0rad)
  PredefinedType = 0
  VerticalArea = 0
  Width = 250
FEATURE [Part::FeaturePython] Structure663  label="отделка инсталляции 003"  # Arch/BIM 52 (typed FeaturePython)
  Base = -> Rectangle3890
  FaceMaker = 0
  GlobalId = 2d5W_OQQf2Fxkoe6wMEOb9
  Height = 1200
  HorizontalArea = 55000
  IfcData = IfcUID=2d5W_OQQf2Fxkoe6wMEOb9,+2 more (map truncated)
  IfcType = 52
  Length = 0
  Material = -> Material013
  MoveBase = false
  MoveWithHost = false
  Nodes = (2) [(-2856.79,7112.64,0),(-2856.79,7112.64,600)]
  NodesOffset = 0
  Normal = (0,0,1)
  PerimeterLength = 2300
  VerticalArea = 2760000
  Width = 100
FEATURE [Part::Part2DObjectPython] Rectangle4184  label="Шкаф Cersanit Moduo 60_010"  # Draft 2D object (typed FeaturePython)
  Area = 84000
  ChamferSize = 0
  Columns = 1
  FilletRadius = 0
  Height = 600
  Length = 140
  MakeFace = true
  Placement = pos=(3825,5925,0) rot=(0,0,1;0rad)
  Rows = 1
FEATURE [Part::FeaturePython] Structure664  label="Шкаф Cersanit Moduo 60_011"  # Arch/BIM 52 (typed FeaturePython)
  Base = -> Rectangle4184
  FaceMaker = 0
  GlobalId = 2d5W_OQQf2Fxkoe6wMEOb9
  Height = 800
  HorizontalArea = 84000
  IfcData = IfcUID=2d5W_OQQf2Fxkoe6wMEOb9,+2 more (map truncated)
  IfcType = 52
  Length = 0
  Material = -> Material013
  MoveBase = false
  MoveWithHost = false
  Nodes = (2) [(-2856.79,7112.64,0),(-2856.79,7112.64,600)]
  NodesOffset = 0
  Normal = (0,0,-1)
  PerimeterLength = 1480
  Placement = pos=(0,0,1075) rot=(0,0,1;0rad)
  VerticalArea = 1184000
  Width = 100
FEATURE [Part::FeaturePython] Structure665  label="Шкаф Cersanit Moduo 60_012"  # Arch/BIM 52 (typed FeaturePython)
  Base = -> Rectangle4184
  FaceMaker = 0
  GlobalId = 2d5W_OQQf2Fxkoe6wMEOb9
  Height = 800
  HorizontalArea = 84000
  IfcData = IfcUID=2d5W_OQQf2Fxkoe6wMEOb9,+2 more (map truncated)
  IfcType = 52
  Length = 0
  Material = -> Material013
  MoveBase = false
  MoveWithHost = false
  Nodes = (2) [(-2856.79,7112.64,0),(-2856.79,7112.64,600)]
  NodesOffset = 0
  Normal = (0,0,1)
  PerimeterLength = 1480
  Placement = pos=(0,0,1075) rot=(0,0,1;0rad)
  VerticalArea = 1184000
  Width = 100
FEATURE [Part::FeaturePython] Structure666  label="Проём-Д130-001"  # Arch/BIM 52 (typed FeaturePython)
  Base = -> Rectangle4038
  FaceMaker = 0
  Height = 2400
  HorizontalArea = 143000
  IfcData = complex_attributes={"OwnerHistory": {}, "IsNestedBy": {}, "IsDecomposedBy": {}, "IsDefinedBy": {}, "ObjectPlacement": {}, "Representation":... (+4 chars omitted)
  IfcType = 52
  Length = 0
  MoveBase = false
  MoveWithHost = false
  Nodes = (2) [(13000,6050,0),(13000,6050,2180)]
  NodesOffset = 0
  Normal = (0,0,0)
  PerimeterLength = 2820
  VerticalArea = 6768000
  Width = 100
FEATURE [Part::FeaturePython] Wall416  label="перегородка (сил.блок 500х250х80) 009"  # Arch/BIM 166 (typed FeaturePython)
  Align = 2
  Area = 4.71e+06
  Base = -> Line1903
  BlockHeight = 250
  BlockLength = 0
  CountBroken = 0
  CountEntire = 0
  Face = 0
  GlobalId = 2YMQSCXEvDBOywm4rK59sv
  Height = 3000
  HorizontalArea = 229600
  IfcData = IfcUID=2YMQSCXEvDBOywm4rK59sv; attributes={"GlobalId": {"value": "2YMQSCXEvDBOywm4rK59sv"}}
  IfcType = 166
  Joint = 0
  Length = 1570
  MakeBlocks = false
  Material = -> Material009
  MoveBase = false
  MoveWithHost = false
  Normal = (0,0,0)
  OffsetFirst = 300
  OffsetSecond = 50
  PerimeterLength = 3300
  Placement = pos=(0,0,-200) rot=(0,0,1;0rad)
  PredefinedType = 0
  Subtractions = -> [Structure666]
  VerticalArea = 4.044e+06
  Width = 80
FEATURE [Part::FeaturePython] Wall231  label="перегородка (сил.блок 500х250х80) 005"  # Arch/BIM 166 (typed FeaturePython)
  Align = 2
  Area = 3e+06
  Base = -> Line1391
  BlockHeight = 250
  BlockLength = 0
  CountBroken = 0
  CountEntire = 0
  Face = 0
  GlobalId = 2YMQSCXEvDBOywm4rK59sv
  Height = 2500
  HorizontalArea = 96000
  IfcData = IfcUID=2YMQSCXEvDBOywm4rK59sv; attributes={"GlobalId": {"value": "2YMQSCXEvDBOywm4rK59sv"}}
  IfcType = 166
  Joint = 0
  Length = 1200
  MakeBlocks = false
  Material = -> Material009
  MoveBase = false
  MoveWithHost = false
  Normal = (0,0,0)
  OffsetFirst = 300
  OffsetSecond = 50
  PerimeterLength = 2560
  Placement = pos=(0,0,-200) rot=(0,0,1;0rad)
  PredefinedType = 0
  Subtractions = -> [Structure546]
  VerticalArea = 4.44884e+06
  Width = 80
FEATURE [Part::FeaturePython] Structure668  label="ВК_001"  # Arch/BIM 172 (typed FeaturePython)
  Base = -> Compound006018
  FaceMaker = 0
  Height = 6900
  HorizontalArea = 90000
  IfcData = attributes={"GlobalId": {"name": "GlobalId", "type": "IfcGloballyUniqueId", "is_enum": false, "enum_values": []}, "Description": {"... (+484 chars omitted),+1 more (map truncated)
  IfcType = 172
  Length = 0
  MoveBase = false
  MoveWithHost = false
  Nodes = (12) [(7055,1345,0),(7415,1345,0),(7055,1595,0),(7415,1595,0),(7095,1385,0),(7215,1385,0),(7095,1555,0),(7215,1555,0),(7255,1385,0),(7375,1385,0),+2 more]
  NodesOffset = 0
  Normal = (0,0,0)
  PerimeterLength = 0
  Placement = pos=(0,0,300) rot=(0,0,1;0rad)
  PredefinedType = 0
  VerticalArea = 16422000
  Width = 100
FEATURE [Part::FeaturePython] Structure669  label="ВК_010"  # Arch/BIM 172 (typed FeaturePython)
  Base = -> Compound006021
  FaceMaker = 0
  Height = 6900
  HorizontalArea = 0
  IfcData = attributes={"GlobalId": {"name": "GlobalId", "type": "IfcGloballyUniqueId", "is_enum": false, "enum_values": []}, "Description": {"... (+484 chars omitted),+1 more (map truncated)
  IfcType = 172
  Length = 0
  MoveBase = false
  MoveWithHost = false
  Nodes = (16) [(7055,1845,0),(7415,1845,0),(7055,2655,0),(7415,2655,0),(7345,1995,0),(7145,2170,0),(7325,2170,0),(7125,2190,0),(7345,2190,0),(7125,2250,0),+6 more]
  NodesOffset = 0
  Normal = (0,0,0)
  PerimeterLength = 0
  Placement = pos=(0,0,300) rot=(0,0,1;0rad)
  PredefinedType = 0
  VerticalArea = 0
  Width = 100
FEATURE [Part::FeaturePython] Structure670  label="ВК_011"  # Arch/BIM 172 (typed FeaturePython)
  Base = -> Compound006019
  FaceMaker = 0
  Height = 6900
  HorizontalArea = 90000
  IfcData = attributes={"GlobalId": {"name": "GlobalId", "type": "IfcGloballyUniqueId", "is_enum": false, "enum_values": []}, "Description": {"... (+484 chars omitted),+1 more (map truncated)
  IfcType = 172
  Length = 0
  MoveBase = false
  MoveWithHost = false
  Nodes = (12) [(7055,1595,0),(7415,1595,0),(7055,1845,0),(7415,1845,0),(7095,1635,0),(7215,1635,0),(7095,1805,0),(7215,1805,0),(7255,1635,0),(7375,1635,0),+2 more]
  NodesOffset = 0
  Normal = (0,0,0)
  PerimeterLength = 0
  Placement = pos=(0,0,300) rot=(0,0,1;0rad)
  PredefinedType = 0
  VerticalArea = 16422000
  Width = 100
FEATURE [Part::FeaturePython] Structure671  label="ВК_012"  # Arch/BIM 172 (typed FeaturePython)
  Base = -> Compound006020
  FaceMaker = 0
  Height = 6900
  HorizontalArea = 90000
  IfcData = attributes={"GlobalId": {"name": "GlobalId", "type": "IfcGloballyUniqueId", "is_enum": false, "enum_values": []}, "Description": {"... (+484 chars omitted),+1 more (map truncated)
  IfcType = 172
  Length = 0
  MoveBase = false
  MoveWithHost = false
  Nodes = (12) [(7055,1095,0),(7415,1095,0),(7055,1345,0),(7415,1345,0),(7095,1135,0),(7215,1135,0),(7095,1305,0),(7215,1305,0),(7255,1135,0),(7375,1135,0),+2 more]
  NodesOffset = 0
  Normal = (0,0,0)
  PerimeterLength = 0
  Placement = pos=(0,0,300) rot=(0,0,1;0rad)
  PredefinedType = 0
  VerticalArea = 16422000
  Width = 100
FEATURE [Part::Part2DObjectPython] Wire1062  # Draft 2D object (typed FeaturePython)
  Area = 0
  ChamferSize = 0
  Closed = true
  End = (6835,4535,0)
  FilletRadius = 0
  Length = 15340
  MakeFace = false
  Placement = pos=(3825,4535,0) rot=(0,0,1;0rad)
  Points = (10) [(0,0,0),(4.54747e-13,3860,0),(1900,3860,0),(1900,2060,0),(1100,2060,0),(1100,1940,0),(1900,1940,0),(1900,1040,0),(3010,1040,0),(3010,0,0)]
  Start = (3825,4535,0)
  Subdivisions = 0
FEATURE [Part::Part2DObjectPython] Wire1063  # Draft 2D object (typed FeaturePython)
  Area = 0
  ChamferSize = 0
  Closed = true
  End = (-30,3875,0)
  FilletRadius = 0
  Length = 16170
  MakeFace = false
  Placement = pos=(-30,8395,0) rot=(0,0,1;0rad)
  Points = (6) [(0,0,0),(3565,0,0),(3565,-3870,0),(2400,-3870,0),(2400,-4520,0),(-4.15668e-13,-4520,0)]
  Start = (-30,8395,0)
  Subdivisions = 0
FEATURE [Part::FeaturePython] Wall233  label="Штукатурка 20мм 001"  # Arch/BIM 166 (typed FeaturePython)
  Align = 1
  Area = 4.5276e+07
  Base = -> Wire1063
  BlockHeight = 0
  BlockLength = 0
  CountBroken = 0
  CountEntire = 0
  Face = 0
  GlobalId = 1_tpg5Ww11ef5dsryiIvTa
  Height = 2800
  HorizontalArea = 0
  IfcData = IfcUID=1_tpg5Ww11ef5dsryiIvTa,+2 more (map truncated)
  IfcType = 166
  Joint = 0
  Length = 16170
  MakeBlocks = false
  Material = -> Material008
  MoveBase = false
  MoveWithHost = false
  Normal = (0,0,0)
  OffsetFirst = 0
  OffsetSecond = 0
  PerimeterLength = 0
  PredefinedType = 0
  Subtractions = -> [Structure021,Wall402,Wall222,Structure643,Wall230,Structure651]
  VerticalArea = 0
  Width = 20
FEATURE [Part::Part2DObjectPython] Wire1064  # Draft 2D object (typed FeaturePython)
  Area = 0
  ChamferSize = 0
  Closed = true
  End = (-30,-25,0)
  FilletRadius = 0
  Length = 14730
  MakeFace = false
  Placement = pos=(-30,3775,0) rot=(0,0,1;0rad)
  Points = (6) [(0,0,0),(2400,0,0),(2400,-660,0),(3565,-660,0),(3565,-3800,0),(-3.48166e-13,-3800,0)]
  Start = (-30,3775,0)
  Subdivisions = 0
FEATURE [Part::FeaturePython] Wall234  label="Штукатурка 20мм 002"  # Arch/BIM 166 (typed FeaturePython)
  Align = 1
  Area = 4.1244e+07
  Base = -> Wire1064
  BlockHeight = 0
  BlockLength = 0
  CountBroken = 0
  CountEntire = 0
  Face = 0
  GlobalId = 3UxVpvSNzClhJFqsCgM8Mc
  Height = 2800
  HorizontalArea = 0
  IfcData = IfcUID=3UxVpvSNzClhJFqsCgM8Mc,+2 more (map truncated)
  IfcType = 166
  Joint = 0
  Length = 14730
  MakeBlocks = false
  Material = -> Material008
  MoveBase = false
  MoveWithHost = false
  Normal = (0,0,0)
  OffsetFirst = 0
  OffsetSecond = 0
  PerimeterLength = 0
  PredefinedType = 0
  Subtractions = -> [Structure023,Wall277,Structure024,Wall186,Wall230,Wall402,Structure645,Structure652]
  VerticalArea = 0
  Width = 20
FEATURE [Part::Part2DObjectPython] Wire1066  # Draft 2D object (typed FeaturePython)
  Area = 0
  ChamferSize = 0
  Closed = true
  End = (5835,5685,0)
  FilletRadius = 0
  Length = 29180
  MakeFace = false
  Placement = pos=(5835,8395,0) rot=(0,0,1;0rad)
  Points = (8) [(0,0,0),(4765,0,0),(4765,-5170,0),(-3365,-5170,0),(-3365,-3970,0),(1290,-3970,0),(1290,-2710,0),(-9.09495e-13,-2710,0)]
  Start = (5835,8395,0)
  Subdivisions = 0
FEATURE [Part::Part2DObjectPython] Wire1067  # Draft 2D object (typed FeaturePython)
  Area = 0
  ChamferSize = 0
  Closed = true
  End = (8035,1185,0)
  FilletRadius = 0
  Length = 11997.1
  MakeFace = false
  Placement = pos=(8035,-25,0) rot=(0,0,1;0rad)
  Points = (9) [(0,0,0),(2065,2.79243e-12,0),(2565,500,0),(2565,2960,0),(0,2960,0),(0,2580,0),(-620,2580,0),(-620,1210,0),(0,1210,0)]
  Start = (8035,-25,0)
  Subdivisions = 0
FEATURE [Part::FeaturePython] Wall236  label="Штукатурка 20мм 004"  # Arch/BIM 166 (typed FeaturePython)
  Align = 0
  Area = 3.35919e+07
  Base = -> Wire1067
  BlockHeight = 0
  BlockLength = 0
  CountBroken = 0
  CountEntire = 0
  Face = 0
  GlobalId = 1rvNhjPI97_QqIjlSx0NrH
  Height = 2800
  HorizontalArea = 0
  IfcData = IfcUID=1rvNhjPI97_QqIjlSx0NrH,+2 more (map truncated)
  IfcType = 166
  Joint = 0
  Length = 11997.1
  MakeBlocks = false
  Material = -> Material008
  MoveBase = false
  MoveWithHost = false
  Normal = (0,0,0)
  OffsetFirst = 0
  OffsetSecond = 0
  PerimeterLength = 0
  PredefinedType = 0
  Subtractions = -> [Structure317,Structure360,Structure648,Structure574,Wall417,Wall162,Wall188]
  VerticalArea = 0
  Width = 20
FEATURE [Part::Box] Box3285  label="бутулочница 15 см 002"
  AttacherType = Attacher::AttachEngine3D
  Height = 850
  Length = 600
  Placement = pos=(7435,2385,1600) rot=(0,0,1;0rad)
  Width = 150
FEATURE [Part::Box] Box3286  label="бутулочница 15 см 001"
  AttacherType = Attacher::AttachEngine3D
  Height = 1600
  Length = 600
  Placement = pos=(8035,2535,0) rot=(0,0,1;3.14159rad)
  Width = 150
FEATURE [Part::FeaturePython] Structure672  label="столешница 001"  # Arch/BIM 172 (typed FeaturePython)
  Base = -> Wire1036
  FaceMaker = 0
  Height = 40
  HorizontalArea = 2.473e+06
  IfcData = attributes={"GlobalId": {"name": "GlobalId", "type": "IfcGloballyUniqueId", "is_enum": false, "enum_values": []}, "Description": {"... (+484 chars omitted),+1 more (map truncated)
  IfcType = 172
  Length = 0
  MoveBase = false
  MoveWithHost = false
  Nodes = (2) [(9953.29,1125.73,0),(9953.29,1125.73,-40)]
  NodesOffset = 0
  Normal = (0,0,0)
  PerimeterLength = 9308.58
  Placement = pos=(0,0,850) rot=(0,0,1;0rad)
  PredefinedType = 0
  Subtractions = -> [Extrude057]
  VerticalArea = 440910
  Width = 100
FEATURE [Part::Part2DObjectPython] Wire1068  # Draft 2D object (typed FeaturePython)
  Area = 0
  ChamferSize = 0
  Closed = true
  End = (8635,-25,0)
  FilletRadius = 0
  Length = 9298.28
  MakeFace = false
  Placement = pos=(8035,605,0) rot=(0,0,1;0rad)
  Points = (8) [(600,-30,0),(1523.16,-30,0),(1965,411.838,0),(1965,2330,0),(2565,2330,0),(2565,-130,0),(2065,-630,0),(600,-630,0)]
  Start = (8635,575,0)
  Subdivisions = 0
FEATURE [Part::FeaturePython] Structure673  label="шкаф кухонный"  # Arch/BIM 172 (typed FeaturePython)
  Base = -> Wire1068
  FaceMaker = 0
  Height = 810
  HorizontalArea = 2.56761e+06
  IfcData = attributes={"GlobalId": {"name": "GlobalId", "type": "IfcGloballyUniqueId", "is_enum": false, "enum_values": []}, "Description": {"... (+484 chars omitted),+1 more (map truncated)
  IfcType = 172
  Length = 0
  MoveBase = false
  MoveWithHost = false
  Nodes = (2) [(9963.11,1114.69,0),(9963.11,1114.69,-810)]
  NodesOffset = 0
  Normal = (0,0,0)
  PerimeterLength = 9298.28
  Placement = pos=(0,0,810) rot=(0,0,1;0rad)
  PredefinedType = 0
  Subtractions = -> [Extrude057]
  VerticalArea = 7.72017e+06
  Width = 100
FEATURE [Part::Box] Box3287  label="шкаф 60 кухонный 014"
  AttacherType = Attacher::AttachEngine3D
  Height = 850
  Length = 600
  Placement = pos=(8035,-25,1600) rot=(0,0,1;0rad)
  Width = 630
FEATURE [Part::Box] Box3288  label="Холодильник001"
  AttacherType = Attacher::AttachEngine3D
  Height = 800
  Length = 600
  Placement = pos=(8035,-25,0) rot=(0,0,1;0rad)
  Width = 630
FEATURE [Part::Box] Box3289  label="шкаф 60 кухонный 015"
  AttacherType = Attacher::AttachEngine3D
  Height = 800
  Length = 600
  Placement = pos=(8035,-25,800) rot=(0,0,1;0rad)
  Width = 630
FEATURE [Part::Box] Box3290  label="шкаф 45 кухонный 004"
  AttacherType = Attacher::AttachEngine3D
  Height = 300
  Length = 630
  Placement = pos=(8635,-25,2450) rot=(0,0,1;1.5708rad)
  Width = 600
FEATURE [App::GeometryPython] BuildingPart045  label="Мебель кухонная"  # Arch/BIM 52 (typed FeaturePython)
  Area = 0
  GlobalId = 32uBXoaMr36Ak6fKsSPIPb
  Group = -> [Loft001,Box3175,Box3179,Box3192,Cylinder001,Box3195,Box3229,Box3232,Box3233,Cylinder005,Fusion013,Fusion014,Fusion015,Fusion016,Cut076,Fusion011001,Extrude058,Box3285,Box3286,Structure672,Structure673,Box3287,Box3288,Box3289,Box3290]
  Height = 0
  HeightPropagate = true
  IfcData = IfcUID=32uBXoaMr36Ak6fKsSPIPb,attributes={"GlobalId": {"value": "32uBXoaMr36Ak6fKsSPIPb"}},+1 more (map truncated)
  IfcType = 52
  LevelOffset = 0
FEATURE [Part::Box] Box3291  label="столешница010"
  AttacherType = Attacher::AttachEngine3D
  Height = 30
  Length = 600
  Placement = pos=(-1000,-3200,720) rot=(0,0,-1;1.5708rad)
  Width = 1700
FEATURE [Part::Box] Box3292  label="ножка062"
  AttacherType = Attacher::AttachEngine3D
  Height = 720
  Length = 600
  Placement = pos=(660,-3200,0) rot=(0,0,-1;1.5708rad)
  Width = 40
FEATURE [Part::Box] Box3293  label="ножка063"
  AttacherType = Attacher::AttachEngine3D
  Height = 720
  Length = 600
  Placement = pos=(-1000,-3200,0) rot=(0,0,-1;1.5708rad)
  Width = 40
FEATURE [Part::Box] Box3294  label="ножка064"
  AttacherType = Attacher::AttachEngine3D
  Height = 200
  Length = 40
  Placement = pos=(-960,-3200,420) rot=(0,0,-1;1.5708rad)
  Width = 1620
FEATURE [Part::Compound] Compound  label="стол 1700х600"
  Links = -> [Box3294,Box3291,Box3292,Box3293]
FEATURE [Part::Feature] Compound006038
  Placement = pos=(1070,6975,0) rot=(0,0,1;0rad)
  shape: bbox 1700 x 600 x 750 mm, 24 faces, 4 solids (baked)
FEATURE [Part::FeaturePython] Component241025  label="Стол 170х60"  # Arch/BIM 0 (typed FeaturePython)
  Base = -> Compound006038
  HorizontalArea = 0
  IfcData = attributes={"GlobalId": {"name": "GlobalId", "type": "IfcGloballyUniqueId", "is_enum": false, "enum_values": []}, "Description": {"... (+538 chars omitted),+1 more (map truncated)
  IfcType = 0
  MoveBase = false
  MoveWithHost = false
  PerimeterLength = 0
  Placement = pos=(1070,6975,0) rot=(0,0,1;0rad)
  PredefinedType = 0
  VerticalArea = 0
FEATURE [App::GeometryPython] BuildingPart047  label="Мебель другая"  # Arch/BIM 52 (typed FeaturePython)
  Area = 0
  GlobalId = 1Dl8CuxJnEPxKEPVOok4FA
  Group = -> [BuildingPart065,Structure339,Structure523,Box3145,Box3143,Box3157,Box3159,Box3163,Box3204,Box3218,Box3236,Box3237,BuildingPart132,Fusion011003001,Fusion011003002001,Component241025]
  Height = 0
  HeightPropagate = true
  IfcData = IfcUID=1Dl8CuxJnEPxKEPVOok4FA,attributes={"GlobalId": {"value": "1Dl8CuxJnEPxKEPVOok4FA"}},+1 more (map truncated)
  IfcType = 52
  LevelOffset = 0
FEATURE [Sketcher::SketchObject] Sketch418
  FullyConstrained = true
  Placement = pos=(3915,8805,955) rot=(1,0,0;1.5708rad)
  sketch-geometry (16):
    g0: LineSegment StartX=0 StartY=0 StartZ=0 EndX=920 EndY=0 EndZ=0
    g1: LineSegment StartX=920 StartY=0 StartZ=0 EndX=920 EndY=1605 EndZ=0
    g2: LineSegment StartX=920 StartY=1605 StartZ=0 EndX=0 EndY=1605 EndZ=0
    g3: LineSegment StartX=0 StartY=1605 StartZ=0 EndX=0 EndY=0 EndZ=0
    g4: LineSegment StartX=70 StartY=70 StartZ=0 EndX=850 EndY=70 EndZ=0
    g5: LineSegment StartX=850 StartY=70 StartZ=0 EndX=850 EndY=1535 EndZ=0
    g6: LineSegment StartX=850 StartY=1535 StartZ=0 EndX=70 EndY=1535 EndZ=0
    g7: LineSegment StartX=70 StartY=1535 StartZ=0 EndX=70 EndY=70 EndZ=0
    g8: LineSegment StartX=77 StartY=77 StartZ=0 EndX=843 EndY=77 EndZ=0
    g9: LineSegment StartX=843 StartY=77 StartZ=0 EndX=843 EndY=1528 EndZ=0
    g10: LineSegment StartX=843 StartY=1528 StartZ=0 EndX=77 EndY=1528 EndZ=0
    g11: LineSegment StartX=77 StartY=1528 StartZ=0 EndX=77 EndY=77 EndZ=0
    g12: LineSegment StartX=117 StartY=117 StartZ=0 EndX=803 EndY=117 EndZ=0
    g13: LineSegment StartX=803 StartY=117 StartZ=0 EndX=803 EndY=1488 EndZ=0
    g14: LineSegment StartX=803 StartY=1488 StartZ=0 EndX=117 EndY=1488 EndZ=0
    g15: LineSegment StartX=117 StartY=1488 StartZ=0 EndX=117 EndY=117 EndZ=0
  constraints (47):
    c: Coincident(g0,g1)
    c: Coincident(g1,g2)
    c: Coincident(g2,g3)
    c: Coincident(g3,g0)
    c: Horizontal(g0)
    c: Horizontal(g2)
    c: Vertical(g1)
    c: Vertical(g3)
    c: Coincident(g4,g5)
    c: Coincident(g5,g6)
    c: Coincident(g6,g7)
    c: Coincident(g7,g4)
    c: Horizontal(g4)
    c: Horizontal(g6)
    c: Vertical(g5)
    c: Vertical(g7)
    c: DistanceY(g1) = 1605  'Height'
    c: DistanceX(g0) = 920  'Width'
    c: DistanceY(g6,g2) = 70  'Frame1'
    c: DistanceX(g2,g6) = 70  'Frame2'
    c: DistanceX(g4,g0) = 70  'Frame3'
    c: DistanceY(g0,g4) = 70  'Frame4'
    c: Coincident(g0,g-1)
    c: Coincident(g8,g9)
    c: Coincident(g9,g10)
    c: Coincident(g10,g11)
    c: Coincident(g11,g8)
    c: Horizontal(g8)
    c: Horizontal(g10)
    c: Vertical(g9)
    c: Vertical(g11)
    c: Coincident(g12,g13)
    c: Coincident(g13,g14)
    c: Coincident(g14,g15)
    c: Coincident(g15,g12)
    c: Horizontal(g12)
    c: Horizontal(g14)
    c: Vertical(g13)
    c: Vertical(g15)
    c: DistanceX(g8,g12) = 40
    c: DistanceY(g8,g12) = 40
    c: DistanceX(g14,g10) = 40
    c: DistanceY(g14,g10) = 40
    c: DistanceX(g4,g8) = 7
    c: DistanceY(g4,g8) = 7
    c: DistanceX(g10,g6) = 7
    c: DistanceY(g10,g6) = 7
FEATURE [Part::FeaturePython] Window108  label="ОК-1-004"  # Arch/BIM 170 (typed FeaturePython)
  Area = 1476600
  Base = -> Sketch418
  Frame = 70
  Height = 1605
  HoleDepth = 0
  HoleWire = 0
  HorizontalArea = 0
  IfcData = attributes={"GlobalId": {"name": "GlobalId", "type": "IfcGloballyUniqueId", "is_enum": false, "enum_values": []}, "Description": {"... (+1230 chars omitted),+1 more (map truncated)
  IfcType = 170
  LouvreSpacing = 0
  LouvreWidth = 0
  Material = -> Material011
  MoveBase = false
  MoveWithHost = true
  Normal = (0,0,0)
  Opening = 0
  OverallHeight = 1605
  OverallWidth = 920
  PartitioningType = 0
  PerimeterLength = 0
  PredefinedType = 0
  Preset = 2
  SymbolElevation = false
  SymbolPlan = false
  VerticalArea = 0
  Width = 920
  WindowParts = OuterFrame | Frame | Wire0,Wire1 | 0.0+V | 0.00+V | InnerFrame | Frame | Wire2,Wire3,Edge8,Mode2 | 0.00+V | 0.0+V | InnerGlass | Glass panel | Wire3 | 8.0 | 40.0+V
  expr: OverallHeight = .Height.Value
  expr: OverallWidth = .Width.Value
FEATURE [Sketcher::SketchObject] Sketch419
  FullyConstrained = true
  Placement = pos=(11010,2640,955) rot=(0.57735,-0.57735,-0.57735;2.0944rad)
  sketch-geometry (16):
    g0: LineSegment StartX=0 StartY=0 StartZ=0 EndX=1180 EndY=0 EndZ=0
    g1: LineSegment StartX=1180 StartY=0 StartZ=0 EndX=1180 EndY=1605 EndZ=0
    g2: LineSegment StartX=1180 StartY=1605 StartZ=0 EndX=0 EndY=1605 EndZ=0
    g3: LineSegment StartX=0 StartY=1605 StartZ=0 EndX=0 EndY=0 EndZ=0
    g4: LineSegment StartX=70 StartY=70 StartZ=0 EndX=1110 EndY=70 EndZ=0
    g5: LineSegment StartX=1110 StartY=70 StartZ=0 EndX=1110 EndY=1535 EndZ=0
    g6: LineSegment StartX=1110 StartY=1535 StartZ=0 EndX=70 EndY=1535 EndZ=0
    g7: LineSegment StartX=70 StartY=1535 StartZ=0 EndX=70 EndY=70 EndZ=0
    g8: LineSegment StartX=77 StartY=77 StartZ=0 EndX=1103 EndY=77 EndZ=0
    g9: LineSegment StartX=1103 StartY=77 StartZ=0 EndX=1103 EndY=1528 EndZ=0
    g10: LineSegment StartX=1103 StartY=1528 StartZ=0 EndX=77 EndY=1528 EndZ=0
    g11: LineSegment StartX=77 StartY=1528 StartZ=0 EndX=77 EndY=77 EndZ=0
    g12: LineSegment StartX=117 StartY=117 StartZ=0 EndX=1063 EndY=117 EndZ=0
    g13: LineSegment StartX=1063 StartY=117 StartZ=0 EndX=1063 EndY=1488 EndZ=0
    g14: LineSegment StartX=1063 StartY=1488 StartZ=0 EndX=117 EndY=1488 EndZ=0
    g15: LineSegment StartX=117 StartY=1488 StartZ=0 EndX=117 EndY=117 EndZ=0
  constraints (47):
    c: Coincident(g0,g1)
    c: Coincident(g1,g2)
    c: Coincident(g2,g3)
    c: Coincident(g3,g0)
    c: Horizontal(g0)
    c: Horizontal(g2)
    c: Vertical(g1)
    c: Vertical(g3)
    c: Coincident(g4,g5)
    c: Coincident(g5,g6)
    c: Coincident(g6,g7)
    c: Coincident(g7,g4)
    c: Horizontal(g4)
    c: Horizontal(g6)
    c: Vertical(g5)
    c: Vertical(g7)
    c: DistanceY(g1) = 1605  'Height'
    c: DistanceX(g0) = 1180  'Width'
    c: DistanceY(g6,g2) = 70  'Frame1'
    c: DistanceX(g2,g6) = 70  'Frame2'
    c: DistanceX(g4,g0) = 70  'Frame3'
    c: DistanceY(g0,g4) = 70  'Frame4'
    c: Coincident(g0,g-1)
    c: Coincident(g8,g9)
    c: Coincident(g9,g10)
    c: Coincident(g10,g11)
    c: Coincident(g11,g8)
    c: Horizontal(g8)
    c: Horizontal(g10)
    c: Vertical(g9)
    c: Vertical(g11)
    c: Coincident(g12,g13)
    c: Coincident(g13,g14)
    c: Coincident(g14,g15)
    c: Coincident(g15,g12)
    c: Horizontal(g12)
    c: Horizontal(g14)
    c: Vertical(g13)
    c: Vertical(g15)
    c: DistanceX(g8,g12) = 40
    c: DistanceY(g8,g12) = 40
    c: DistanceX(g14,g10) = 40
    c: DistanceY(g14,g10) = 40
    c: DistanceX(g4,g8) = 7
    c: DistanceY(g4,g8) = 7
    c: DistanceX(g10,g6) = 7
    c: DistanceY(g10,g6) = 7
FEATURE [Part::FeaturePython] Window109  label="ОК-1-005"  # Arch/BIM 170 (typed FeaturePython)
  Area = 1893900
  Base = -> Sketch419
  Frame = 70
  Height = 1605
  HoleDepth = 0
  HoleWire = 0
  HorizontalArea = 0
  IfcData = attributes={"GlobalId": {"name": "GlobalId", "type": "IfcGloballyUniqueId", "is_enum": false, "enum_values": []}, "Description": {"... (+1231 chars omitted),+1 more (map truncated)
  IfcType = 170
  LouvreSpacing = 0
  LouvreWidth = 0
  Material = -> Material011
  MoveBase = false
  MoveWithHost = true
  Normal = (0,0,0)
  Opening = 0
  OverallHeight = 1605
  OverallWidth = 1180
  PartitioningType = 0
  PerimeterLength = 0
  PredefinedType = 0
  Preset = 2
  SymbolElevation = false
  SymbolPlan = false
  VerticalArea = 0
  Width = 1180
  WindowParts = OuterFrame | Frame | Wire0,Wire1 | 0.0+V | 0.00+V | InnerFrame | Frame | Wire2,Wire3,Edge8,Mode2 | 0.00+V | 0.0+V | InnerGlass | Glass panel | Wire3 | 8.0 | 40.0+V
  expr: OverallWidth = .Width.Value
  expr: OverallHeight = .Height.Value
FEATURE [Sketcher::SketchObject] Sketch420
  FullyConstrained = true
  Placement = pos=(6005,-435,2015) rot=(0,0.707107,0.707107;3.14159rad)
  sketch-geometry (16):
    g0: LineSegment StartX=0 StartY=0 StartZ=0 EndX=1440 EndY=0 EndZ=0
    g1: LineSegment StartX=1440 StartY=0 StartZ=0 EndX=1440 EndY=545 EndZ=0
    g2: LineSegment StartX=1440 StartY=545 StartZ=0 EndX=0 EndY=545 EndZ=0
    g3: LineSegment StartX=0 StartY=545 StartZ=0 EndX=0 EndY=0 EndZ=0
    g4: LineSegment StartX=70 StartY=70 StartZ=0 EndX=1370 EndY=70 EndZ=0
    g5: LineSegment StartX=1370 StartY=70 StartZ=0 EndX=1370 EndY=475 EndZ=0
    g6: LineSegment StartX=1370 StartY=475 StartZ=0 EndX=70 EndY=475 EndZ=0
    g7: LineSegment StartX=70 StartY=475 StartZ=0 EndX=70 EndY=70 EndZ=0
    g8: LineSegment StartX=77 StartY=77 StartZ=0 EndX=1363 EndY=77 EndZ=0
    g9: LineSegment StartX=1363 StartY=77 StartZ=0 EndX=1363 EndY=468 EndZ=0
    g10: LineSegment StartX=1363 StartY=468 StartZ=0 EndX=77 EndY=468 EndZ=0
    g11: LineSegment StartX=77 StartY=468 StartZ=0 EndX=77 EndY=77 EndZ=0
    g12: LineSegment StartX=117 StartY=117 StartZ=0 EndX=1323 EndY=117 EndZ=0
    g13: LineSegment StartX=1323 StartY=117 StartZ=0 EndX=1323 EndY=428 EndZ=0
    g14: LineSegment StartX=1323 StartY=428 StartZ=0 EndX=117 EndY=428 EndZ=0
    g15: LineSegment StartX=117 StartY=428 StartZ=0 EndX=117 EndY=117 EndZ=0
  constraints (47):
    c: Coincident(g0,g1)
    c: Coincident(g1,g2)
    c: Coincident(g2,g3)
    c: Coincident(g3,g0)
    c: Horizontal(g0)
    c: Horizontal(g2)
    c: Vertical(g1)
    c: Vertical(g3)
    c: Coincident(g4,g5)
    c: Coincident(g5,g6)
    c: Coincident(g6,g7)
    c: Coincident(g7,g4)
    c: Horizontal(g4)
    c: Horizontal(g6)
    c: Vertical(g5)
    c: Vertical(g7)
    c: DistanceY(g1) = 545  'Height'
    c: DistanceX(g0) = 1440  'Width'
    c: DistanceY(g6,g2) = 70  'Frame1'
    c: DistanceX(g2,g6) = 70  'Frame2'
    c: DistanceX(g4,g0) = 70  'Frame3'
    c: DistanceY(g0,g4) = 70  'Frame4'
    c: Coincident(g0,g-1)
    c: Coincident(g8,g9)
    c: Coincident(g9,g10)
    c: Coincident(g10,g11)
    c: Coincident(g11,g8)
    c: Horizontal(g8)
    c: Horizontal(g10)
    c: Vertical(g9)
    c: Vertical(g11)
    c: Coincident(g12,g13)
    c: Coincident(g13,g14)
    c: Coincident(g14,g15)
    c: Coincident(g15,g12)
    c: Horizontal(g12)
    c: Horizontal(g14)
    c: Vertical(g13)
    c: Vertical(g15)
    c: DistanceX(g8,g12) = 40
    c: DistanceY(g8,g12) = 40
    c: DistanceX(g14,g10) = 40
    c: DistanceY(g14,g10) = 40
    c: DistanceX(g4,g8) = 7
    c: DistanceY(g4,g8) = 7
    c: DistanceX(g10,g6) = 7
    c: DistanceY(g10,g6) = 7
FEATURE [Part::FeaturePython] Window110  label="ОК-3-002"  # Arch/BIM 170 (typed FeaturePython)
  Area = 784800
  Base = -> Sketch420
  Frame = 70
  Height = 545
  HoleDepth = 0
  HoleWire = 0
  HorizontalArea = 0
  IfcData = attributes={"GlobalId": {"name": "GlobalId", "type": "IfcGloballyUniqueId", "is_enum": false, "enum_values": []}, "Description": {"... (+1230 chars omitted),+1 more (map truncated)
  IfcType = 170
  LouvreSpacing = 0
  LouvreWidth = 0
  Material = -> Material011
  MoveBase = false
  MoveWithHost = true
  Normal = (0,0,0)
  Opening = 0
  OverallHeight = 545
  OverallWidth = 1440
  PartitioningType = 0
  PerimeterLength = 0
  PredefinedType = 0
  Preset = 2
  SymbolElevation = false
  SymbolPlan = false
  VerticalArea = 0
  Width = 1440
  WindowParts = OuterFrame | Frame | Wire0,Wire1 | 0.0+V | 0.00+V | InnerFrame | Frame | Wire2,Wire3,Edge6,Mode1 | 0.00+V | 0.0+V | InnerGlass | Glass panel | Wire3 | 8.0 | 40.0+V
  expr: OverallWidth = .Width.Value
  expr: OverallHeight = .Height.Value
FEATURE [Part::Part2DObjectPython] Rectangle4186  label="frame001"  # Draft 2D object (typed FeaturePython)
  Area = 375066
  ChamferSize = 0
  Columns = 1
  FilletRadius = 0
  Height = 311
  Length = 1206
  MakeFace = true
  Placement = pos=(4682,0,2132) rot=(1,0,0;1.5708rad)
  Rows = 1
FEATURE [Part::Part2DObjectPython] Rectangle4187  label="frame002"  # Draft 2D object (typed FeaturePython)
  Area = 414936
  ChamferSize = 0
  Columns = 1
  FilletRadius = 0
  Height = 1921
  Length = 216
  MakeFace = true
  Placement = pos=(5672,0,47) rot=(1,0,0;1.5708rad)
  Rows = 1
FEATURE [Part::Part2DObjectPython] Wire1069  label="Прихожая (ТГ)"  # Draft 2D object (typed FeaturePython)
  Area = 8.3026e+06
  ChamferSize = 0
  Closed = true
  End = (3825,-25,0)
  FilletRadius = 0
  Length = 12720
  MakeFace = true
  Placement = pos=(3825,2935,0) rot=(0,0,1;0rad)
  Points = (10) [(0,0,0),(650,1.81899e-12,0),(650,180,0),(2180,180,0),(2180,1.81899e-12,0),(3220,-4.54747e-13,0),(3220,-1360,0),(2280,-1360,0),(2280,-2960,0),+1 more]
  Start = (3825,2935,0)
  Subdivisions = 0
FEATURE [Sketcher::SketchObject] Sketch421  label="Профиль ПНО 120-009"
  FullyConstrained = false
  Placement = pos=(-200,-25,0) rot=(0.57735,0.57735,0.57735;2.0944rad)
  sketch-geometry (19):
    g0: LineSegment StartX=0 StartY=0 StartZ=0 EndX=1190 EndY=0 EndZ=0
    g1: LineSegment StartX=1190 StartY=0 StartZ=0 EndX=1190 EndY=160 EndZ=0
    g2: LineSegment StartX=1190 StartY=160 StartZ=0 EndX=0 EndY=160 EndZ=0
    g3: LineSegment StartX=0 StartY=160 StartZ=0 EndX=0 EndY=0 EndZ=0
    g4: Circle CenterX=100 CenterY=80 CenterZ=0 NormalX=0 NormalY=0 NormalZ=1 AngleXU=0 Radius=50
    g5: Circle CenterX=240 CenterY=80 CenterZ=0 NormalX=0 NormalY=0 NormalZ=1 AngleXU=0 Radius=50
    g6: LineSegment StartX=100 StartY=80 StartZ=0 EndX=240 EndY=80 EndZ=0
    g7: Circle CenterX=380 CenterY=80 CenterZ=0 NormalX=0 NormalY=0 NormalZ=1 AngleXU=0 Radius=50
    g8: LineSegment StartX=240 StartY=80 StartZ=0 EndX=380 EndY=80 EndZ=0
    g9: Circle CenterX=520 CenterY=80 CenterZ=0 NormalX=0 NormalY=0 NormalZ=1 AngleXU=0 Radius=50
    g10: LineSegment StartX=380 StartY=80 StartZ=0 EndX=520 EndY=80 EndZ=0
    g11: Circle CenterX=660 CenterY=80 CenterZ=0 NormalX=0 NormalY=0 NormalZ=1 AngleXU=0 Radius=50
    g12: LineSegment StartX=520 StartY=80 StartZ=0 EndX=660 EndY=80 EndZ=0
    g13: Circle CenterX=800 CenterY=80 CenterZ=0 NormalX=0 NormalY=0 NormalZ=1 AngleXU=0 Radius=50
    g14: LineSegment StartX=660 StartY=80 StartZ=0 EndX=800 EndY=80 EndZ=0
    g15: Circle CenterX=940 CenterY=80 CenterZ=0 NormalX=0 NormalY=0 NormalZ=1 AngleXU=0 Radius=50
    g16: LineSegment StartX=800 StartY=80 StartZ=0 EndX=940 EndY=80 EndZ=0
    g17: Circle CenterX=1080 CenterY=80 CenterZ=0 NormalX=0 NormalY=0 NormalZ=1 AngleXU=0 Radius=50
    g18: LineSegment StartX=940 StartY=80 StartZ=0 EndX=1080 EndY=80 EndZ=0
  constraints (49):
    c: Coincident(g0,g1)
    c: Coincident(g1,g2)
    c: Coincident(g2,g3)
    c: Coincident(g3,g0)
    c: Horizontal(g0)
    c: Horizontal(g2)
    c: Vertical(g1)
    c: Vertical(g3)
    c: Coincident(g0,g-1)
    c: DistanceY(g3,g3) = 160
    c: DistanceX(g2,g2) = 1190
    c: Diameter(g4) = 100
    c: DistanceY(g4,g2) = 80
    c: Diameter(g5) = 100
    c: Coincident(g4,g6)
    c: Coincident(g5,g6)
    c: Distance(g6) = 140
    c: Angle(g6) = 0
    c: Diameter(g7) = 100
    c: Coincident(g5,g8)
    c: Coincident(g7,g8)
    c: Equal(g6,g8)
    c: Parallel(g8,g6)
    c: Diameter(g9) = 100
    c: Coincident(g7,g10)
    c: Coincident(g9,g10)
    c: Equal(g6,g10)
    c: Parallel(g10,g6)
    c: Diameter(g11) = 100
    c: Coincident(g9,g12)
    c: Coincident(g11,g12)
    c: Equal(g6,g12)
    c: Parallel(g12,g6)
    c: Diameter(g13) = 100
    c: Coincident(g11,g14)
    c: Coincident(g13,g14)
    c: Equal(g6,g14)
    c: Parallel(g14,g6)
    c: Diameter(g15) = 100
    c: Coincident(g13,g16)
    c: Coincident(g15,g16)
    c: Equal(g6,g16)
    c: Parallel(g16,g6)
    c: Diameter(g17) = 100
    c: Coincident(g15,g18)
    c: Coincident(g17,g18)
    c: Equal(g6,g18)
    c: Parallel(g18,g6)
    c: DistanceX(g2,g4) = 100
FEATURE [Part::Extrusion] Extrude099005010  label="ПНО 40-12-8"
  Base = -> Sketch421
  Dir = (3880,0,0)
  DirMode = 0
  FaceMakerClass = Part::FaceMakerBullseye
  LengthFwd = 3980
  LengthRev = 0
  Placement = pos=(0,0,2800) rot=(0,0,1;0rad)
  Solid = true
  Symmetric = false
FEATURE [Part::FeaturePython] Array081  label="ПНО 40-12-8 7шт. 001"  # Draft array (typed FeaturePython)
  Angle = 360
  ArrayType = 0
  Axis = (0,0,1)
  Base = -> Extrude099005010
  Center = (0,0,0)
  Fuse = false
  IntervalAxis = (0,0,0)
  IntervalX = (0,0,0)
  IntervalY = (0,1205,0)
  IntervalZ = (0,0,1)
  NumberPolar = 1
  NumberX = 1
  NumberY = 7
  NumberZ = 1
  Placement = pos=(0,1.364e-12,0) rot=(0,0,1;0rad)
FEATURE [Part::FeaturePython] Component241026  label="ПНО 40-12-8 7шт."  # Arch/BIM 0 (typed FeaturePython)
  Base = -> Array081
  HorizontalArea = 0
  IfcData = attributes={"GlobalId": {"name": "GlobalId", "type": "IfcGloballyUniqueId", "is_enum": false, "enum_values": []}, "Description": {"... (+538 chars omitted),+1 more (map truncated)
  IfcType = 0
  Material = -> Material018
  MoveBase = false
  MoveWithHost = false
  PerimeterLength = 0
  Placement = pos=(0,1.364e-12,0) rot=(0,0,1;0rad)
  PredefinedType = 0
  VerticalArea = 0
FEATURE [Sketcher::SketchObject] Sketch422  label="Профиль ПНО 100-007"
  FullyConstrained = false
  Placement = pos=(3815,2.27e-13,0) rot=(1,0,0;1.5708rad)
  sketch-geometry (15):
    g0: LineSegment StartX=0 StartY=0 StartZ=0 EndX=990 EndY=0 EndZ=0
    g1: LineSegment StartX=990 StartY=0 StartZ=0 EndX=990 EndY=160 EndZ=0
    g2: LineSegment StartX=990 StartY=160 StartZ=0 EndX=0 EndY=160 EndZ=0
    g3: LineSegment StartX=0 StartY=160 StartZ=0 EndX=0 EndY=0 EndZ=0
    g4: Circle CenterX=145 CenterY=80 CenterZ=0 NormalX=0 NormalY=0 NormalZ=1 AngleXU=0 Radius=50
    g5: Circle CenterX=285 CenterY=80 CenterZ=0 NormalX=0 NormalY=0 NormalZ=1 AngleXU=0 Radius=50
    g6: LineSegment StartX=145 StartY=80 StartZ=0 EndX=285 EndY=80 EndZ=0
    g7: Circle CenterX=425 CenterY=80 CenterZ=0 NormalX=0 NormalY=0 NormalZ=1 AngleXU=0 Radius=50
    g8: LineSegment StartX=285 StartY=80 StartZ=0 EndX=425 EndY=80 EndZ=0
    g9: Circle CenterX=565 CenterY=80 CenterZ=0 NormalX=0 NormalY=0 NormalZ=1 AngleXU=0 Radius=50
    g10: LineSegment StartX=425 StartY=80 StartZ=0 EndX=565 EndY=80 EndZ=0
    g11: Circle CenterX=705 CenterY=80 CenterZ=0 NormalX=0 NormalY=0 NormalZ=1 AngleXU=0 Radius=50
    g12: LineSegment StartX=565 StartY=80 StartZ=0 EndX=705 EndY=80 EndZ=0
    g13: Circle CenterX=845 CenterY=80 CenterZ=0 NormalX=0 NormalY=0 NormalZ=1 AngleXU=0 Radius=50
    g14: LineSegment StartX=705 StartY=80 StartZ=0 EndX=845 EndY=80 EndZ=0
  constraints (39):
    c: Coincident(g0,g1)
    c: Coincident(g1,g2)
    c: Coincident(g2,g3)
    c: Coincident(g3,g0)
    c: Horizontal(g0)
    c: Horizontal(g2)
    c: Vertical(g1)
    c: Vertical(g3)
    c: Coincident(g0,g-1)
    c: DistanceY(g3,g3) = 160
    c: DistanceX(g2,g2) = 990
    c: Diameter(g4) = 100
    c: DistanceY(g4,g2) = 80
    c: Diameter(g5) = 100
    c: Coincident(g4,g6)
    c: Coincident(g5,g6)
    c: Distance(g6) = 140
    c: Angle(g6) = 0
    c: Diameter(g7) = 100
    c: Coincident(g5,g8)
    c: Coincident(g7,g8)
    c: Equal(g6,g8)
    c: Parallel(g8,g6)
    c: Diameter(g9) = 100
    c: Coincident(g7,g10)
    c: Coincident(g9,g10)
    c: Equal(g6,g10)
    c: Parallel(g10,g6)
    c: Diameter(g11) = 100
    c: Coincident(g9,g12)
    c: Coincident(g11,g12)
    c: Equal(g6,g12)
    c: Parallel(g12,g6)
    c: Diameter(g13) = 100
    c: Coincident(g11,g14)
    c: Coincident(g13,g14)
    c: Equal(g6,g14)
    c: Parallel(g14,g6)
    c: DistanceX(g2,g4) = 145
FEATURE [Part::Extrusion] Extrude099005011  label="ПНО 55-10-6"
  Base = -> Sketch422
  Dir = (0,3880,0)
  DirMode = 0
  FaceMakerClass = Part::FaceMakerBullseye
  LengthFwd = 5480
  LengthRev = 0
  Placement = pos=(10,3085,2800) rot=(0,0,1;0rad)
  Solid = true
  Symmetric = false
FEATURE [Part::FeaturePython] Array082  label="ПНО 55-10-8 2шт. 001"  # Draft array (typed FeaturePython)
  Angle = 360
  ArrayType = 0
  Axis = (0,0,1)
  Base = -> Extrude099005011
  Center = (0,0,0)
  Fuse = false
  IntervalAxis = (0,0,0)
  IntervalX = (1000,0,0)
  IntervalY = (0,0,0)
  IntervalZ = (0,0,1)
  NumberPolar = 1
  NumberX = 2
  NumberY = 1
  NumberZ = 1
  Placement = pos=(0,-9.09e-13,0) rot=(0,0,1;0rad)
FEATURE [Part::FeaturePython] Component241027  label="ПНО 55-10-8 2шт."  # Arch/BIM 0 (typed FeaturePython)
  Base = -> Array082
  HorizontalArea = 0
  IfcData = attributes={"GlobalId": {"name": "GlobalId", "type": "IfcGloballyUniqueId", "is_enum": false, "enum_values": []}, "Description": {"... (+538 chars omitted),+1 more (map truncated)
  IfcType = 0
  Material = -> Material018
  MoveBase = false
  MoveWithHost = false
  PerimeterLength = 0
  Placement = pos=(0,-9.09e-13,0) rot=(0,0,1;0rad)
  PredefinedType = 0
  VerticalArea = 0
FEATURE [Part::Part2DObjectPython] Rectangle4189  label="Вырез в плите 001"  # Draft 2D object (typed FeaturePython)
  ChamferSize = 0
  Columns = 1
  FilletRadius = 0
  Height = 1180
  Length = 180
  MakeFace = true
  Placement = pos=(6945,4505,0) rot=(0,0,1;0rad)
  Rows = 1
FEATURE [Part::FeaturePython] Structure675  label="Проём-лестн-006"  # Arch/BIM 52 (typed FeaturePython)
  Base = -> Rectangle4189
  FaceMaker = 0
  Height = 500
  HorizontalArea = 212400
  IfcData = complex_attributes={"OwnerHistory": {}, "IsNestedBy": {}, "IsDecomposedBy": {}, "IsDefinedBy": {}, "ObjectPlacement": {}, "Representation":... (+4 chars omitted)
  IfcType = 52
  Length = 0
  MoveBase = false
  MoveWithHost = false
  Nodes = (2) [(13000,6050,0),(13000,6050,2180)]
  NodesOffset = 0
  Normal = (0,0,0)
  PerimeterLength = 2720
  Placement = pos=(0,1.819e-12,2511.73) rot=(0,0,1;0rad)
  VerticalArea = 1.36e+06
  Width = 100
FEATURE [Part::FeaturePython] Component197  label="ПНО 55-12-8 3шт."  # Arch/BIM 0 (typed FeaturePython)
  Base = -> Array073
  HorizontalArea = 0
  IfcData = attributes={"GlobalId": {"name": "GlobalId", "type": "IfcGloballyUniqueId", "is_enum": false, "enum_values": []}, "Description": {"... (+538 chars omitted),+1 more (map truncated)
  IfcType = 0
  Material = -> Material018
  MoveBase = false
  MoveWithHost = false
  PerimeterLength = 0
  Placement = pos=(-9.09e-13,4.55e-13,0) rot=(0,0,1;0rad)
  PredefinedType = 0
  Subtractions = -> [Structure675]
  VerticalArea = 0
FEATURE [Part::Extrusion] Extrude099005012  label="ПНО 33-10-007"
  Base = -> Sketch422
  Dir = (0,3880,0)
  DirMode = 0
  FaceMakerClass = Part::FaceMakerBullseye
  LengthFwd = 3280
  LengthRev = 0
  Placement = pos=(10,-205,2800) rot=(0,0,1;0rad)
  Solid = true
  Symmetric = false
FEATURE [Part::FeaturePython] Array083  label="ПНО 33-10-8 2шт. 002"  # Draft array (typed FeaturePython)
  Angle = 360
  ArrayType = 0
  Axis = (0,0,1)
  Base = -> Extrude099005012
  Center = (0,0,0)
  Fuse = false
  IntervalAxis = (0,0,0)
  IntervalX = (5800,0,0)
  IntervalY = (0,0,0)
  IntervalZ = (0,0,1)
  NumberPolar = 1
  NumberX = 2
  NumberY = 1
  NumberZ = 1
  Placement = pos=(0,-9.09e-13,0) rot=(0,0,1;0rad)
FEATURE [Part::FeaturePython] Component241028  label="ПНО 33-10-8 2шт.001"  # Arch/BIM 0 (typed FeaturePython)
  Base = -> Array083
  HorizontalArea = 0
  IfcData = attributes={"GlobalId": {"name": "GlobalId", "type": "IfcGloballyUniqueId", "is_enum": false, "enum_values": []}, "Description": {"... (+538 chars omitted),+1 more (map truncated)
  IfcType = 0
  Material = -> Material018
  MoveBase = false
  MoveWithHost = false
  PerimeterLength = 0
  Placement = pos=(0,-9.09e-13,0) rot=(0,0,1;0rad)
  PredefinedType = 0
  VerticalArea = 0
FEATURE [Part::Extrusion] Extrude099005013  label="ПНО 33-12-009"
  Base = -> Sketch231
  Dir = (0,3880,0)
  DirMode = 0
  FaceMakerClass = Part::FaceMakerBullseye
  LengthFwd = 3280
  LengthRev = 0
  Placement = pos=(10,-205,2800) rot=(0,0,1;0rad)
  Solid = true
  Symmetric = false
FEATURE [Part::FeaturePython] Array084  label="ПНО 33-12-8 4шт. 002"  # Draft array (typed FeaturePython)
  Angle = 360
  ArrayType = 0
  Axis = (0,0,1)
  Base = -> Extrude099005013
  Center = (0,0,0)
  Fuse = false
  IntervalAxis = (0,0,0)
  IntervalX = (1200,0,0)
  IntervalY = (0,0,0)
  IntervalZ = (0,0,1)
  NumberPolar = 1
  NumberX = 4
  NumberY = 1
  NumberZ = 1
  Placement = pos=(-4605,1.364e-12,0) rot=(0,0,1;0rad)
FEATURE [Part::FeaturePython] Component241029  label="ПНО 33-12-8 4шт.001"  # Arch/BIM 0 (typed FeaturePython)
  Base = -> Array084
  HorizontalArea = 0
  IfcData = attributes={"GlobalId": {"name": "GlobalId", "type": "IfcGloballyUniqueId", "is_enum": false, "enum_values": []}, "Description": {"... (+538 chars omitted),+1 more (map truncated)
  IfcType = 0
  Material = -> Material018
  MoveBase = false
  MoveWithHost = false
  PerimeterLength = 0
  Placement = pos=(0,9.1e-13,0) rot=(0,0,1;0rad)
  PredefinedType = 0
  Subtractions = -> [Structure360]
  VerticalArea = 0
FEATURE [Part::FeaturePython] Clone005  label="Array081"  # Draft clone (typed FeaturePython)
  AttacherType = Attacher::AttachEngine3D
  Fuse = false
  Objects = -> [Array080]
  Placement = pos=(0,9.1e-13,0) rot=(0,0,1;0rad)
  Scale = (1,1,1)
FEATURE [Part::FeaturePython] Wall583  label="Утепление в уровне перекрытия XPS 100mm"  # Arch/BIM 166 (typed FeaturePython)
  Align = 0
  Area = 6608000
  Base = -> Rectangle3879
  BlockHeight = 0
  BlockLength = 0
  CountBroken = 0
  CountEntire = 0
  Face = 0
  Height = 160
  HorizontalArea = 4.09e+06
  IfcData = attributes={"GlobalId": {"name": "GlobalId", "type": "IfcGloballyUniqueId", "is_enum": false, "enum_values": []}, "Description": {"... (+533 chars omitted),+1 more (map truncated)
  IfcType = 166
  Joint = 0
  Length = 41300
  MakeBlocks = false
  Material = -> Material002
  MoveBase = false
  MoveWithHost = false
  Normal = (0,0,-1)
  OffsetFirst = 0
  OffsetSecond = 0
  PerimeterLength = 41300
  Placement = pos=(0,0,2960) rot=(0,0,1;0rad)
  PredefinedType = 0
  VerticalArea = 13088000
  Width = 100
FEATURE [Part::Part2DObjectPython] Wire1070  # Draft 2D object (typed FeaturePython)
  Area = 9.31595e+07
  ChamferSize = 0
  Closed = true
  End = (-200,-25,0)
  FilletRadius = 0
  Length = 39470
  MakeFace = true
  Placement = pos=(-200,8395,0) rot=(0,0,1;0rad)
  Points = (15) [(0,0,0),(4025,0,0),(4025,170,0),(6015,170,0),(6015,170,0),(6015,20,0),(7145,20,0),(7145,170,0),(10795,170,0),(10795,-5320,0),(10815,-5320,0),+4 more]
  Start = (-200,8395,0)
  Subdivisions = 0
FEATURE [Part::FeaturePython] Structure676  label="Вычет армпояса перекрытия"  # Arch/BIM 172 (typed FeaturePython)
  Base = -> Wire1070
  FaceMaker = 0
  Height = 160
  HorizontalArea = 9.31595e+07
  IfcData = attributes={"GlobalId": {"name": "GlobalId", "type": "IfcGloballyUniqueId", "is_enum": false, "enum_values": []}, "Description": {"... (+484 chars omitted),+1 more (map truncated)
  IfcType = 172
  Length = 0
  MoveBase = false
  MoveWithHost = false
  Nodes = (2) [(5250.34,4172.04,0),(5250.34,4172.04,-160)]
  NodesOffset = 0
  Normal = (0,0,0)
  PerimeterLength = 39470
  Placement = pos=(0,0,2960) rot=(0,0,1;0rad)
  PredefinedType = 0
  VerticalArea = 6.3152e+06
  Width = 100
FEATURE [Part::FeaturePython] Wall242  label="Армпояс в уровне перекрытия 001"  # Arch/BIM 166 (typed FeaturePython)
  Align = 0
  Area = 6608000
  Base = -> Rectangle3879
  BlockHeight = 140
  BlockLength = 250
  CountBroken = 4
  CountEntire = 148
  Face = 0
  GlobalId = 0JF6Mj3WnAXwUaXoCorPV_
  Height = 160
  HorizontalArea = 8.1351e+06
  IfcData = IfcUID=0JF6Mj3WnAXwUaXoCorPV_,+2 more (map truncated)
  IfcType = 166
  Joint = 10
  Length = 41300
  MakeBlocks = false
  Material = -> Material001
  MoveBase = false
  MoveWithHost = false
  Normal = (0,0,-1)
  Offset = 100
  OffsetFirst = 0
  OffsetSecond = 0
  PerimeterLength = 40500
  Placement = pos=(5.68e-14,0,2960) rot=(0,0,1;0rad)
  PredefinedType = 0
  Subtractions = -> [Structure676]
  VerticalArea = 1.27952e+07
  Width = 500
FEATURE [Part::Part2DObjectPython] Rectangle4190  label="Корпус для щита распред. встраиваемый ЩРВ-48 (650х340х120) IP31 EKF PROxima"  # Draft 2D object (typed FeaturePython)
  Area = 0
  ChamferSize = 0
  Columns = 1
  FilletRadius = 0
  Height = 380
  Length = 150
  MakeFace = false
  Placement = pos=(3675,2415,0) rot=(0,0,1;0rad)
  Rows = 1
FEATURE [Part::FeaturePython] Structure677  label="Электрощит ЩРВ-48"  # Arch/BIM 52 (typed FeaturePython)
  Base = -> Rectangle4190
  FaceMaker = 0
  Height = 693
  HorizontalArea = 57000
  IfcData = complex_attributes={"OwnerHistory": {}, "IsNestedBy": {}, "IsDecomposedBy": {}, "IsDefinedBy": {}, "ObjectPlacement": {}, "Representation":... (+4 chars omitted)
  IfcType = 52
  Length = 0
  Material = -> Material010
  MoveBase = false
  MoveWithHost = false
  Nodes = (2) [(13000,6050,0),(13000,6050,2180)]
  NodesOffset = 0
  Normal = (0,0,0)
  PerimeterLength = 1060
  Placement = pos=(0,0,955) rot=(0,0,1;0rad)
  VerticalArea = 734580
  Width = 100
FEATURE [App::GeometryPython] BuildingPart087  label="Инженерные системы"  # Arch/BIM 52 (typed FeaturePython)
  Area = 0
  GlobalId = 0dgo77$PP7IAddqr4C3YZS
  Group = -> [Cylinder002,Box3220,Cylinder003,Box3222,Box3223,Pipe008,Cylinder010,Box3211,Box3228,Component240,Structure575,Structure668,Structure669,Structure670,Structure671,Structure677]
  Height = 0
  HeightPropagate = true
  IfcData = IfcUID=0dgo77$PP7IAddqr4C3YZS,+2 more (map truncated)
  IfcType = 52
  LevelOffset = 0
FEATURE [Part::FeaturePython] Wall562  label="Несущая стена 2.1нф 250мм внутренняя001"  # Arch/BIM 166 (typed FeaturePython)
  Align = 2
  Area = 2.538e+07
  Base = -> Line2141
  BlockHeight = 231
  BlockLength = 0
  CountBroken = 0
  CountEntire = 0
  Face = 0
  GlobalId = 1uw9ZyZ5vAkuN6nr$sWkBP
  Height = 3000
  HorizontalArea = 0
  IfcData = IfcUID=1uw9ZyZ5vAkuN6nr$sWkBP; attributes={"GlobalId": {"value": "1uw9ZyZ5vAkuN6nr$sWkBP"}}
  IfcType = 166
  Joint = 0
  Length = 8460
  MakeBlocks = true
  Material = -> Material009
  MoveBase = false
  MoveWithHost = false
  Normal = (0,0,1)
  OffsetFirst = 0
  OffsetSecond = 500
  PerimeterLength = 0
  Placement = pos=(0,0,-200) rot=(0,0,1;0rad)
  PredefinedType = 0
  Subtractions = -> [Structure644,Structure643,Wall564,Wall281,Structure023,Wall497,Structure677]
  VerticalArea = 0
  Width = 250
FEATURE [App::GeometryPython] BuildingPart002  label="Стены несущие"  # Arch/BIM 52 (typed FeaturePython)
  Area = 173631810
  GlobalId = 3CS7VrtqL2RQvRhQ1$1d0X
  Group = -> [BuildingPart088,BuildingPart089,Wall004,Wall562,Wall579,Wall567]
  Height = 0
  HeightPropagate = true
  IfcData = IfcUID=3CS7VrtqL2RQvRhQ1$1d0X,attributes={"GlobalId": {"value": "3CS7VrtqL2RQvRhQ1$1d0X"}},+1 more (map truncated)
  IfcType = 52
  LevelOffset = 0
FEATURE [Part::Part2DObjectPython] Rectangle4191  label="ЭЩ48"  # Draft 2D object (typed FeaturePython)
  Area = 57000
  ChamferSize = 0
  Columns = 1
  FilletRadius = 0
  Height = 150
  Length = 380
  MakeFace = true
  Placement = pos=(3675,2795,0) rot=(0,0,-1;1.5708rad)
  Rows = 1
FEATURE [Part::FeaturePython] Wall584  label="Аттиковая стена Поротерм 38Т 380мм"  # Arch/BIM 166 (typed FeaturePython)
  Align = 0
  Area = 26399400
  Base = -> Rectangle3870
  BlockHeight = 231
  BlockLength = 0
  CountBroken = 0
  CountEntire = 0
  Face = 0
  GlobalId = 15i3vb4BrBERo7sMNULkP3
  Height = 690
  HorizontalArea = 0
  IfcData = IfcUID=15i3vb4BrBERo7sMNULkP3,+2 more (map truncated)
  IfcType = 166
  Joint = 0
  Length = 38260
  MakeBlocks = true
  Material = -> Material004
  MoveBase = false
  MoveWithHost = false
  Normal = (0,0,1)
  OffsetFirst = 0
  OffsetSecond = 0
  PerimeterLength = 0
  Placement = pos=(0,0,2960) rot=(0,0,1;0rad)
  PredefinedType = 0
  VerticalArea = 0
  Width = 380
FEATURE [Part::Part2DObjectPython] Wire1071  # Draft 2D object (typed FeaturePython)
  Area = 4076000
  ChamferSize = 0
  Closed = true
  End = (5835,4275,0)
  FilletRadius = 0
  Length = 9930
  MakeFace = true
  Placement = pos=(5575,5315,0) rot=(0,0,1;0rad)
  Points = (9) [(260,-515,0),(260,-115,0),(260,34.2165,0),(260,2850,0),(1335,2850,0),(1335,370,0),(1260,370,0),(1260,-1040,0),(260,-1040,0)]
  Start = (5835,4800,0)
  Subdivisions = 0
FEATURE [Part::FeaturePython] Structure037  label="проём в утеплении и стяжке перекрытия"  # Arch/BIM 52 (typed FeaturePython)
  Base = -> Wire1071
  FaceMaker = 0
  Height = 4500
  HorizontalArea = 4076000
  IfcData = complex_attributes={"OwnerHistory": {}, "IsNestedBy": {}, "IsDecomposedBy": {}, "IsDefinedBy": {}, "ObjectPlacement": {}, "Representation":... (+4 chars omitted)
  IfcType = 52
  Length = 0
  MoveBase = false
  MoveWithHost = false
  Nodes = (2) [(4500,6910,0),(4500,6910,4500)]
  NodesOffset = 0
  Normal = (0,0,1)
  PerimeterLength = 9930
  VerticalArea = 4.4685e+07
  Width = 100
FEATURE [Part::FeaturePython] Wall054  label="Утепление перекрытия XPS 100+20mm"  # Arch/BIM 166 (typed FeaturePython)
  Align = 0
  Area = 90268200
  Base = -> Line1077
  BlockHeight = 600
  BlockLength = 1200
  CountBroken = 113
  CountEntire = 88
  Face = 0
  GlobalId = 3kr3_7iVj0bR5GirXoWo2v
  Height = 8460
  HorizontalArea = 0
  IfcData = IfcUID=3kr3_7iVj0bR5GirXoWo2v; attributes={"GlobalId": {"value": "3kr3_7iVj0bR5GirXoWo2v"}}
  IfcType = 166
  Joint = 0
  Length = 10670
  MakeBlocks = false
  Material = -> Material002
  MoveBase = false
  MoveWithHost = false
  Normal = (0,1,0)
  OffsetFirst = 80
  OffsetSecond = 600
  PerimeterLength = 0
  Placement = pos=(0,0,3080) rot=(0,0,1;0rad)
  PredefinedType = 0
  Subtractions = -> [Structure037,Structure384,Wall336,Wall337,Wall338,Wall339]
  VerticalArea = 0
  Width = 120
FEATURE [Part::FeaturePython] Wall098  label="Стяжка мансарды 45мм"  # Arch/BIM 166 (typed FeaturePython)
  Align = 0
  Area = 90268200
  Base = -> Line1077
  BlockHeight = 0
  BlockLength = 0
  CountBroken = 53
  CountEntire = 111
  Face = 0
  GlobalId = 2jmC5X6fbFRwmp_GUsZLMp
  Height = 8460
  HorizontalArea = 0
  IfcData = IfcUID=2jmC5X6fbFRwmp_GUsZLMp; attributes={"GlobalId": {"value": "2jmC5X6fbFRwmp_GUsZLMp"}}
  IfcType = 166
  Joint = 0
  Length = 10670
  MakeBlocks = false
  Material = -> Material018
  MoveBase = false
  MoveWithHost = false
  Normal = (0,1,0)
  OffsetFirst = 0
  OffsetSecond = 0
  PerimeterLength = 0
  Placement = pos=(0,1.1e-15,3125) rot=(0,0,1;0rad)
  PredefinedType = 0
  Subtractions = -> [Structure037,Structure384,Wall336,Wall337,Wall338,Wall339]
  VerticalArea = 0
  Width = 45
FEATURE [Part::FeaturePython] Wall295  label="Покрытие пола мансарды 20мм 001"  # Arch/BIM 166 (typed FeaturePython)
  Align = 0
  Area = 90268200
  Base = -> Line1077
  BlockHeight = 0
  BlockLength = 0
  CountBroken = 53
  CountEntire = 111
  Face = 0
  GlobalId = 3s3if1WDv6dQOvhmOxYeJ$
  Height = 8460
  HorizontalArea = 85033800
  IfcData = IfcUID=3s3if1WDv6dQOvhmOxYeJ$; attributes={"GlobalId": {"value": "3s3if1WDv6dQOvhmOxYeJ$"}}
  IfcType = 166
  Joint = 0
  Length = 10670
  MakeBlocks = false
  Material = -> Material018
  MoveBase = false
  MoveWithHost = false
  Normal = (0,1,0)
  OffsetFirst = 0
  OffsetSecond = 0
  PerimeterLength = 38260
  Placement = pos=(0,1.1e-15,3145) rot=(0,0,1;0rad)
  PredefinedType = 0
  Subtractions = -> [Structure037,Structure384,Wall336,Wall337,Wall339,Wall338]
  VerticalArea = 1061800
  Width = 20
FEATURE [App::GeometryPython] BuildingPart099  label="Пол мансарды"  # Arch/BIM 52 (typed FeaturePython)
  Area = 270804600
  GlobalId = 0Uv4k6v0XBk8Mx6e_8kGVf
  Group = -> [Wall098,Wall054,Wall295]
  Height = 0
  HeightPropagate = true
  IfcData = IfcUID=0Uv4k6v0XBk8Mx6e_8kGVf,+2 more (map truncated)
  IfcType = 52
  LevelOffset = 0
  Placement = pos=(0,0,5) rot=(0,0,1;0rad)
FEATURE [Part::FeaturePython] Wall585  label="Армпояс под мауэрлат"  # Arch/BIM 166 (typed FeaturePython)
  Align = 0
  Area = 9292500
  Base = -> Rectangle3879
  BlockHeight = 140
  BlockLength = 250
  CountBroken = 4
  CountEntire = 148
  Face = 0
  GlobalId = 0JF6Mj3WnAXwUaXoCorPV_
  Height = 225
  HorizontalArea = 6377600
  IfcData = IfcUID=0JF6Mj3WnAXwUaXoCorPV_,+2 more (map truncated)
  IfcType = 166
  Joint = 10
  Length = 41300
  MakeBlocks = false
  Material = -> Material001
  MoveBase = false
  MoveWithHost = false
  Normal = (0,0,-1)
  Offset = 100
  OffsetFirst = 0
  OffsetSecond = 0
  PerimeterLength = 40500
  Placement = pos=(5.68e-14,0,3875) rot=(0,0,1;0rad)
  PredefinedType = 0
  VerticalArea = 17937000
  Width = 160
FEATURE [Part::FeaturePython] Wall586  label="Утепление армпояса XPS 100mm"  # Arch/BIM 166 (typed FeaturePython)
  Align = 0
  Area = 9292500
  Base = -> Rectangle3879
  BlockHeight = 0
  BlockLength = 0
  CountBroken = 0
  CountEntire = 0
  Face = 0
  Height = 225
  HorizontalArea = 4.09e+06
  IfcData = attributes={"GlobalId": {"name": "GlobalId", "type": "IfcGloballyUniqueId", "is_enum": false, "enum_values": []}, "Description": {"... (+533 chars omitted),+1 more (map truncated)
  IfcType = 166
  Joint = 0
  Length = 41300
  MakeBlocks = false
  Material = -> Material002
  MoveBase = false
  MoveWithHost = false
  Normal = (0,0,-1)
  OffsetFirst = 0
  OffsetSecond = 0
  PerimeterLength = 41300
  Placement = pos=(0,0,3875) rot=(0,0,1;0rad)
  PredefinedType = 0
  VerticalArea = 18405000
  Width = 100
FEATURE [Part::FeaturePython] Wall587  label="Кладка в уровне армпояса 2.1нф"  # Arch/BIM 166 (typed FeaturePython)
  Align = 0
  Area = 9292500
  Base = -> Rectangle3879
  BlockHeight = 140
  BlockLength = 250
  CountBroken = 4
  CountEntire = 148
  Face = 0
  GlobalId = 0JF6Mj3WnAXwUaXoCorPV_
  Height = 225
  HorizontalArea = 4.6488e+06
  IfcData = IfcUID=0JF6Mj3WnAXwUaXoCorPV_,+2 more (map truncated)
  IfcType = 166
  Joint = 10
  Length = 41300
  MakeBlocks = false
  Material = -> Material009
  MoveBase = false
  MoveWithHost = false
  Normal = (0,0,-1)
  Offset = 260
  OffsetFirst = 0
  OffsetSecond = 0
  PerimeterLength = 39220
  Placement = pos=(5.68e-14,0,3875) rot=(0,0,1;0rad)
  PredefinedType = 0
  VerticalArea = 17433000
  Width = 120
FEATURE [App::GeometryPython] BuildingPart097  label="Армпояс"  # Arch/BIM 52 (typed FeaturePython)
  Area = 27877500
  GlobalId = 2GdC2J3IrBqAFOXYdeO3oM
  Group = -> [Wall585,Wall586,Wall587]
  Height = 0
  HeightPropagate = true
  IfcData = IfcUID=2GdC2J3IrBqAFOXYdeO3oM,+2 more (map truncated)
  IfcType = 52
  LevelOffset = 0
  Placement = pos=(0,0,5) rot=(0,0,1;0rad)
FEATURE [Part::FeaturePython] Structure681  label="Структура060"  # Arch/BIM 172 (typed FeaturePython)
  Base = -> Wire817
  FaceMaker = 0
  Height = 1000
  HorizontalArea = 147603200
  IfcData = attributes={"GlobalId": {"name": "GlobalId", "type": "IfcGloballyUniqueId", "is_enum": false, "enum_values": []}, "Description": {"... (+484 chars omitted),+1 more (map truncated)
  IfcType = 172
  Length = 0
  MoveBase = false
  MoveWithHost = false
  Nodes = (2) [(1146.63,4298.06,0),(1146.63,4298.06,1000)]
  NodesOffset = 0
  Normal = (0,0,1)
  PerimeterLength = 50640
  Placement = pos=(0,0,2023.12) rot=(0,0,1;0rad)
  PredefinedType = 0
  VerticalArea = 50640000
  Width = 100
FEATURE [Part::Cut] Cut105003002  label="roof_4_side_002"
  Base = -> Common084
  Tool = -> Structure681
FEATURE [Part::Cut] Cut105003003  label="roof_4_side_003"
  Base = -> Cut105003002
  Tool = -> Fusion076
FEATURE [Part::MultiCommon] Common085
  Shapes = -> [Roof027,Extrude099005002]
FEATURE [Part::FeaturePython] Structure682  label="Структура061"  # Arch/BIM 172 (typed FeaturePython)
  Base = -> Rectangle3284
  FaceMaker = 0
  Height = 1000
  HorizontalArea = 41967100
  IfcData = attributes={"GlobalId": {"name": "GlobalId", "type": "IfcGloballyUniqueId", "is_enum": false, "enum_values": []}, "Description": {"... (+484 chars omitted),+1 more (map truncated)
  IfcType = 172
  Length = 0
  MoveBase = false
  MoveWithHost = false
  Nodes = (2) [(5285,4185,0),(5285,4185,1000)]
  NodesOffset = 0
  Normal = (0,0,0)
  PerimeterLength = 30560
  Placement = pos=(0,0,4182.65) rot=(0,0,1;0rad)
  PredefinedType = 0
  VerticalArea = 30560000
  Width = 100
FEATURE [Part::Cut] Cut105003004  label="roof_2_side_004"
  Base = -> Common085
  Tool = -> Structure682
FEATURE [Part::Part2DObjectPython] Rectangle4198  # Draft 2D object (typed FeaturePython)
  Area = 8.2203e+06
  ChamferSize = 0
  Columns = 1
  FilletRadius = 0
  Height = 2660.29
  Length = 3090
  MakeFace = true
  Placement = pos=(3735,-125,0) rot=(0,0,1;0rad)
  Rows = 1
FEATURE [Part::Extrusion] Extrude099005015  label="Кукушка север 001"
  Base = -> Rectangle4198
  Dir = (0,0,1)
  DirMode = 2
  FaceMakerClass = Part::FaceMakerBullseye
  LengthFwd = 5000
  LengthRev = 0
  Placement = pos=(0,0,2500) rot=(0,0,1;0rad)
  Solid = false
  Symmetric = false
FEATURE [Part::Part2DObjectPython] Wire1073  label="кровля_контур_003"  # Draft 2D object (typed FeaturePython)
  Area = 0
  ChamferSize = 0
  Closed = true
  End = (-1215,9580,0)
  FilletRadius = 0
  Length = 47580
  MakeFace = false
  Placement = pos=(15200,-1120,0) rot=(0,0,1;0rad)
  Points = (4) [(-16415,-90,0),(-3415,-90,0),(-3415,10700,0),(-16415,10700,0)]
  Start = (-1215,-1210,0)
  Subdivisions = 0
FEATURE [Part::FeaturePython] Roof035  label="roof_4_side003_cut_1"  # Arch/BIM 113 (typed FeaturePython)
  Angles = [35,40,35,40]
  Base = -> Wire1073
  BorderLength = 0
  Face = 0
  Flip = false
  Heights = [3777.62,4615.05,3777.62,4615.05]
  HorizontalArea = 187629300
  IdRel = [-1,-1,-1,-1]
  IfcData = attributes={"GlobalId": {"name": "GlobalId", "type": "IfcGloballyUniqueId", "is_enum": false, "enum_values": []}, "Description": {"... (+613 chars omitted),+1 more (map truncated)
  IfcType = 113
  Material = -> Material007
  MoveBase = false
  MoveWithHost = false
  Overhang = [1000,835,1000,835]
  PerimeterLength = 0
  Placement = pos=(0,0,-980) rot=(0,0,1;0rad)
  PredefinedType = 0
  RidgeLength = 0
  Runs = [5500,5500,5500,5500]
  Thickness = [3500,3270,3500,3270]
  VerticalArea = 2.34688e+08
FEATURE [Part::FeaturePython] Roof036  label="roof_4_side003_cut_2"  # Arch/BIM 113 (typed FeaturePython)
  Angles = [35,40,35,40]
  Base = -> Wire1073
  BorderLength = 0
  Face = 0
  Flip = false
  Heights = [3777.62,4615.05,3777.62,4615.05]
  HorizontalArea = 187629300
  IdRel = [-1,-1,-1,-1]
  IfcData = attributes={"GlobalId": {"name": "GlobalId", "type": "IfcGloballyUniqueId", "is_enum": false, "enum_values": []}, "Description": {"... (+613 chars omitted),+1 more (map truncated)
  IfcType = 113
  Material = -> Material007
  MoveBase = false
  MoveWithHost = false
  Overhang = [1000,835,1000,835]
  PerimeterLength = 0
  Placement = pos=(0,0,3672.18) rot=(0,0,1;0rad)
  PredefinedType = 0
  RidgeLength = 0
  Runs = [5500,5500,5500,5500]
  Thickness = [3500,3270,3500,3270]
  VerticalArea = 2.34688e+08
FEATURE [Part::Part2DObjectPython] Line2176  # Draft 2D object (typed FeaturePython)
  ChamferSize = 0
  Closed = true
  End = (3735,-25,0)
  FilletRadius = 0
  Length = 3090
  MakeFace = false
  Placement = pos=(4205,855,0) rot=(0,0,1;1.5708rad)
  Points = (2) [(-880,-2620,0),(-880,470,0)]
  Start = (6825,-25,0)
  Subdivisions = 0
FEATURE [Part::FeaturePython] Wall588  label="перегородка 053"  # Arch/BIM 166 (typed FeaturePython)
  Align = 1
  Area = 6628050
  Base = -> Line2176
  BlockHeight = 250
  BlockLength = 0
  CountBroken = 0
  CountEntire = 0
  Face = 0
  Height = 2145
  HorizontalArea = 544000
  IfcType = 166
  Joint = 0
  Length = 3090
  MakeBlocks = false
  Material = -> Material008
  MoveBase = false
  MoveWithHost = false
  Normal = (0,0,0)
  OffsetFirst = 0
  OffsetSecond = 300
  PerimeterLength = 4780
  Placement = pos=(0,0,3800) rot=(0,0,1;0rad)
  PredefinedType = 0
  Subtractions = -> [Structure578]
  VerticalArea = 9.4101e+06
  Width = 100
FEATURE [Part::Part2DObjectPython] Wire1074  # Draft 2D object (typed FeaturePython)
  Area = 0
  ChamferSize = 0
  Closed = true
  End = (6775,2890,0)
  FilletRadius = 0
  Length = 12830
  MakeFace = false
  Placement = pos=(8886.35,6005,0) rot=(0,0,-1;1.5708rad)
  Points = (4) [(525,-2111.35,0),(525,1713.65,0),(3115,1713.65,0),(3115,-2111.35,0)]
  Start = (6775,5480,0)
  Subdivisions = 0
FEATURE [Part::FeaturePython] Wall589  label="отделка кукушки 008"  # Arch/BIM 166 (typed FeaturePython)
  Align = 1
  Area = 3.849e+07
  Base = -> Wire1074
  BlockHeight = 0
  BlockLength = 0
  CountBroken = 0
  CountEntire = 0
  Face = 0
  Height = 3000
  HorizontalArea = 373250
  IfcData = attributes={"GlobalId": {"name": "GlobalId", "type": "IfcGloballyUniqueId", "is_enum": false, "enum_values": []}, "Description": {"... (+533 chars omitted),+1 more (map truncated)
  IfcType = 166
  Joint = 0
  Length = 12830
  MakeBlocks = false
  Material = -> Material007
  MoveBase = false
  MoveWithHost = false
  Normal = (0,0,0)
  Offset = 250
  OffsetFirst = 0
  OffsetSecond = 0
  PerimeterLength = 15030
  Placement = pos=(0,0,3300) rot=(0,0,1;0rad)
  PredefinedType = 0
  VerticalArea = 8.958e+07
  Width = 25
FEATURE [Part::FeaturePython] Wall590  label="утепление кукушки 006"  # Arch/BIM 166 (typed FeaturePython)
  Align = 1
  Area = 3.849e+07
  Base = -> Wire1074
  BlockHeight = 0
  BlockLength = 0
  CountBroken = 0
  CountEntire = 0
  Face = 0
  Height = 3000
  HorizontalArea = 2134500
  IfcData = attributes={"GlobalId": {"name": "GlobalId", "type": "IfcGloballyUniqueId", "is_enum": false, "enum_values": []}, "Description": {"... (+533 chars omitted),+1 more (map truncated)
  IfcType = 166
  Joint = 0
  Length = 12830
  MakeBlocks = false
  Material = -> Material020
  MoveBase = false
  MoveWithHost = false
  Normal = (0,0,0)
  Offset = 100
  OffsetFirst = 0
  OffsetSecond = 0
  PerimeterLength = 14830
  Placement = pos=(0,0,3300) rot=(0,0,1;0rad)
  PredefinedType = 0
  VerticalArea = 8.538e+07
  Width = 150
FEATURE [Part::Part2DObjectPython] Line2178  # Draft 2D object (typed FeaturePython)
  ChamferSize = 0
  Closed = true
  End = (6825,975,0)
  FilletRadius = 0
  Length = 1000
  MakeFace = false
  Placement = pos=(4605,855,0) rot=(0,0,1;1.5708rad)
  Points = (2) [(-880,-2220,0),(120,-2220,0)]
  Start = (6825,-25,0)
  Subdivisions = 0
FEATURE [Part::FeaturePython] Wall591  label="перегородка 054"  # Arch/BIM 166 (typed FeaturePython)
  Align = 1
  Area = 2.8e+06
  Base = -> Line2178
  BlockHeight = 250
  BlockLength = 0
  CountBroken = 0
  CountEntire = 0
  Face = 0
  Height = 2800
  HorizontalArea = 100000
  IfcType = 166
  Joint = 0
  Length = 1000
  MakeBlocks = false
  Material = -> Material008
  MoveBase = false
  MoveWithHost = false
  Normal = (0,0,0)
  OffsetFirst = 0
  OffsetSecond = 300
  PerimeterLength = 2200
  Placement = pos=(0,0,3145) rot=(0,0,1;0rad)
  PredefinedType = 0
  VerticalArea = 6.16e+06
  Width = 100
FEATURE [Part::Part2DObjectPython] Line2179  # Draft 2D object (typed FeaturePython)
  ChamferSize = 0
  Closed = true
  End = (3735,-25,0)
  FilletRadius = 0
  Length = 980
  MakeFace = false
  Placement = pos=(3805,855,0) rot=(0,0,1;1.5708rad)
  Points = (2) [(100,70,0),(-880,70,0)]
  Start = (3735,955,0)
  Subdivisions = 0
FEATURE [Part::FeaturePython] Wall592  label="перегородка 055"  # Arch/BIM 166 (typed FeaturePython)
  Align = 1
  Area = 3283000
  Base = -> Line2179
  BlockHeight = 250
  BlockLength = 0
  CountBroken = 0
  CountEntire = 0
  Face = 0
  Height = 3350
  HorizontalArea = 98000
  IfcType = 166
  Joint = 0
  Length = 980
  MakeBlocks = false
  Material = -> Material008
  MoveBase = false
  MoveWithHost = false
  Normal = (0,0,0)
  OffsetFirst = 0
  OffsetSecond = 300
  PerimeterLength = 2160
  Placement = pos=(0,0,3145) rot=(0,0,1;0rad)
  PredefinedType = 0
  VerticalArea = 7236000
  Width = 100
FEATURE [Part::FeaturePython] Roof039  label="Кровля 2скатн005"  # Arch/BIM 113 (typed FeaturePython)
  Angles = [35,90,35,90]
  Base = -> Rectangle3216
  BorderLength = 40428.5
  Face = 0
  Flip = false
  Heights = [1925.57,0,1925.57,0]
  HorizontalArea = 7.425e+07
  IdRel = [-1,-1,-1,-1]
  IfcData = attributes={"GlobalId": {"name": "GlobalId", "type": "IfcGloballyUniqueId", "is_enum": false, "enum_values": []}, "Description": {"... (+613 chars omitted),+1 more (map truncated)
  IfcType = 113
  Material = -> Material007
  MoveBase = false
  MoveWithHost = false
  Overhang = [0,0,0,0]
  PerimeterLength = 38000
  Placement = pos=(0,0,4387.72) rot=(0,0,1;0rad)
  PredefinedType = 0
  RidgeLength = 13500
  Runs = [4500,4500,4500,4500]
  Thickness = [2500,2500,2500,2500]
  VerticalArea = 1.15974e+08
FEATURE [Part::Cut] Cut105003006  label="отделка кукушки 010"
  Base = -> Wall589
  Tool = -> Roof039
FEATURE [Part::Cut] Cut105003007  label="утепление кукушки 008"
  Base = -> Wall590
  Tool = -> Roof039
FEATURE [Part::MultiCommon] Common095  label="отделка кукушки 011"
  Shapes = -> [Roof036,Cut105003006]
FEATURE [Part::MultiCommon] Common096  label="утепление кукушки 009"
  Shapes = -> [Roof036,Cut105003007]
FEATURE [Part::Part2DObjectPython] Wire1075  label="проём окна фронтонов 001"  # Draft 2D object (typed FeaturePython)
  Area = 3.0084e+06
  ChamferSize = 0
  Closed = true
  End = (0,5360,4350)
  FilletRadius = 0
  Length = 6893.21
  MakeFace = true
  Placement = pos=(0,3010,4350) rot=(0.57735,0.57735,0.57735;2.0944rad)
  Points = (6) [(0,0,0),(0,880,0),(981.11,1566.98,0),(1368.89,1566.98,0),(2350,880,0),(2350,0,0)]
  Start = (0,3010,4350)
  Subdivisions = 0
FEATURE [Part::Part2DObjectPython] Wire1076  label="проём четверти окна фронтонов 001"  # Draft 2D object (typed FeaturePython)
  Area = 2.54387e+06
  ChamferSize = 0
  Closed = true
  End = (0,5290,4420)
  FilletRadius = 0
  Length = 6379.17
  MakeFace = true
  Placement = pos=(0,3080,4420) rot=(0.57735,0.57735,0.57735;2.0944rad)
  Points = (6) [(0,0,0),(0,773.56,0),(933.181,1426.98,0),(1276.82,1426.98,0),(2210,773.56,0),(2210,0,0)]
  Start = (0,3080,4420)
  Subdivisions = 0
FEATURE [Part::FeaturePython] Structure685  label="Вычет окна фронтона"  # Arch/BIM 172 (typed FeaturePython)
  Base = -> Wire1075
  FaceMaker = 0
  Height = 150
  HorizontalArea = 0
  IfcData = attributes={"GlobalId": {"name": "GlobalId", "type": "IfcGloballyUniqueId", "is_enum": false, "enum_values": []}, "Description": {"... (+484 chars omitted),+1 more (map truncated)
  IfcType = 172
  Length = 0
  MoveBase = false
  MoveWithHost = false
  Nodes = (2) [(-4185,-1175,3834.26),(-4335,-1175,3834.26)]
  NodesOffset = 0
  Normal = (0,0,0)
  PerimeterLength = 0
  Placement = pos=(10750,9.09e-13,120) rot=(0,0,1;0rad)
  PredefinedType = 0
  VerticalArea = 6.2808e+06
  Width = 100
FEATURE [Part::FeaturePython] Structure686  label="Вычет окна фронтона001"  # Arch/BIM 172 (typed FeaturePython)
  Base = -> Wire1076
  FaceMaker = 0
  Height = 150
  HorizontalArea = 0
  IfcData = attributes={"GlobalId": {"name": "GlobalId", "type": "IfcGloballyUniqueId", "is_enum": false, "enum_values": []}, "Description": {"... (+484 chars omitted),+1 more (map truncated)
  IfcType = 172
  Length = 0
  MoveBase = false
  MoveWithHost = false
  Nodes = (2) [(-4185,-1105,3909.68),(-4335,-1105,3909.68)]
  NodesOffset = 0
  Normal = (0,0,0)
  PerimeterLength = 0
  Placement = pos=(10900,9.09e-13,120) rot=(0,0,1;0rad)
  PredefinedType = 0
  VerticalArea = 5.3198e+06
  Width = 100
FEATURE [Part::MultiFuse] Fusion011003002002005003009  label="Вычет окна фронтона002"
  Shapes = -> [Structure685,Structure686]
FEATURE [Part::Cut] Cut105003011  label="отделка кукушки 012"
  Base = -> Common095
  Tool = -> Fusion011003002002005003009
FEATURE [Part::Cut] Cut105003012  label="утепление кукушки 010"
  Base = -> Common096
  Tool = -> Fusion011003002002005003009
FEATURE [Part::Mirroring] mirror016002015  label="отделка кукушки 012 (mirrored)"
  Base = (5285,2800,0)
  Normal = (-1,0,0)
  Source = -> Cut105003011
FEATURE [Part::Mirroring] mirror016002016  label="утепление кукушки 010 (mirrored)"
  Base = (5285,2800,0)
  Normal = (-1,0,0)
  Source = -> Cut105003012
FEATURE [Part::MultiFuse] Fusion011003002002005003010  label="утепление кукушки фронтон 001"
  Shapes = -> [mirror016002016,Cut105003012]
FEATURE [Part::MultiFuse] Fusion011003002002005003011  label="отделка кукушки фронтон 001"
  Shapes = -> [mirror016002015,Cut105003011]
FEATURE [Part::Mirroring] mirror016002017  label="Вычет окна фронтона002 (mirrored)"
  Base = (5285,2785,0)
  Normal = (-1,0,0)
  Source = -> Fusion011003002002005003009
FEATURE [Part::MultiFuse] Fusion011003002002005003012  label="Вычет окна фронтонов 001"
  Shapes = -> [Fusion011003002002005003009,mirror016002017]
FEATURE [Part::FeaturePython] Component241032  label="отделка кукушки боковые 001"  # Arch/BIM 0 (typed FeaturePython)
  Base = -> Fusion011003002002005003011
  HorizontalArea = 0
  IfcData = attributes={"GlobalId": {"name": "GlobalId", "type": "IfcGloballyUniqueId", "is_enum": false, "enum_values": []}, "Description": {"... (+538 chars omitted),+1 more (map truncated)
  IfcType = 0
  Material = -> Material007
  MoveBase = false
  MoveWithHost = false
  PerimeterLength = 0
  PredefinedType = 0
  VerticalArea = 0
FEATURE [Part::FeaturePython] Component241033  label="утепление кукушки боковые 001"  # Arch/BIM 0 (typed FeaturePython)
  Base = -> Fusion011003002002005003010
  HorizontalArea = 0
  IfcData = attributes={"GlobalId": {"name": "GlobalId", "type": "IfcGloballyUniqueId", "is_enum": false, "enum_values": []}, "Description": {"... (+538 chars omitted),+1 more (map truncated)
  IfcType = 0
  Material = -> Material020
  MoveBase = false
  MoveWithHost = false
  PerimeterLength = 0
  PredefinedType = 0
  VerticalArea = 0
FEATURE [Part::FeaturePython] Component241035  label="Cut_vol_001"  # Arch/BIM 0 (typed FeaturePython)
  Base = -> Roof026
  HorizontalArea = 0
  IfcData = attributes={"GlobalId": {"name": "GlobalId", "type": "IfcGloballyUniqueId", "is_enum": false, "enum_values": []}, "Description": {"... (+538 chars omitted),+1 more (map truncated)
  IfcType = 0
  MoveBase = false
  MoveWithHost = false
  PerimeterLength = 0
  Placement = pos=(0,-2.27e-13,3250) rot=(0,0,1;0rad)
  PredefinedType = 0
  VerticalArea = 0
FEATURE [Part::FeaturePython] Structure580  label="стеллаж встроенный 013"  # Arch/BIM 172 (typed FeaturePython)
  Base = -> Rectangle4073
  FaceMaker = 0
  Height = 3500
  HorizontalArea = 1.206e+06
  IfcData = attributes={"GlobalId": {"name": "GlobalId", "type": "IfcGloballyUniqueId", "is_enum": false, "enum_values": []}, "Description": {"... (+484 chars omitted),+1 more (map truncated)
  IfcType = 172
  Length = 0
  MoveBase = false
  MoveWithHost = false
  Nodes = (2) [(3835,6590,0),(3835,6590,3500)]
  NodesOffset = 0
  Normal = (0,0,0)
  PerimeterLength = 5220
  Placement = pos=(0,0,3145) rot=(0,0,1;0rad)
  PredefinedType = 0
  Subtractions = -> [Component241035]
  VerticalArea = 1.14768e+07
  Width = 100
FEATURE [Part::FeaturePython] Structure581  label="шкаф встроенный 014"  # Arch/BIM 172 (typed FeaturePython)
  Base = -> Rectangle4108
  FaceMaker = 0
  Height = 3500
  HorizontalArea = 510000
  IfcData = attributes={"GlobalId": {"name": "GlobalId", "type": "IfcGloballyUniqueId", "is_enum": false, "enum_values": []}, "Description": {"... (+484 chars omitted),+1 more (map truncated)
  IfcType = 172
  Length = 0
  MoveBase = false
  MoveWithHost = false
  Nodes = (2) [(4692.5,7370,0),(4692.5,7370,3500)]
  NodesOffset = 0
  Normal = (0,0,0)
  PerimeterLength = 2900
  Placement = pos=(0,0,3145) rot=(0,0,1;0rad)
  PredefinedType = 0
  Subtractions = -> [Component241035]
  VerticalArea = 4.94443e+06
  Width = 100
FEATURE [Part::FeaturePython] Structure582  label="шкаф встроенный 015"  # Arch/BIM 172 (typed FeaturePython)
  Base = -> Rectangle4129
  FaceMaker = 0
  Height = 3500
  HorizontalArea = 3.41073e+06
  IfcData = attributes={"GlobalId": {"name": "GlobalId", "type": "IfcGloballyUniqueId", "is_enum": false, "enum_values": []}, "Description": {"... (+484 chars omitted),+1 more (map truncated)
  IfcType = 172
  Length = 0
  MoveBase = false
  MoveWithHost = false
  Nodes = (2) [(8976.14,1375,0),(8976.14,1375,3500)]
  NodesOffset = 0
  Normal = (0,0,0)
  PerimeterLength = 8084.54
  Placement = pos=(0,0,3145) rot=(0,0,1;0rad)
  PredefinedType = 0
  Subtractions = -> [Component241035]
  VerticalArea = 1.46206e+07
  Width = 100
FEATURE [Part::FeaturePython] Structure583  label="шкаф встроенный 016"  # Arch/BIM 172 (typed FeaturePython)
  Base = -> Rectangle4109
  FaceMaker = 0
  Height = 3500
  HorizontalArea = 1.206e+06
  IfcData = attributes={"GlobalId": {"name": "GlobalId", "type": "IfcGloballyUniqueId", "is_enum": false, "enum_values": []}, "Description": {"... (+484 chars omitted),+1 more (map truncated)
  IfcType = 172
  Length = 0
  MoveBase = false
  MoveWithHost = false
  Nodes = (2) [(5375,6590,0),(5375,6590,3500)]
  NodesOffset = 0
  Normal = (0,0,0)
  PerimeterLength = 5220
  Placement = pos=(0,0,3145) rot=(0,0,1;0rad)
  PredefinedType = 0
  Subtractions = -> [Component241035]
  VerticalArea = 1.14768e+07
  Width = 100
FEATURE [Part::Part2DObjectPython] Line2182  # Draft 2D object (typed FeaturePython)
  ChamferSize = 0
  Closed = true
  End = (10600,5580,0)
  FilletRadius = 0
  Length = 2790
  MakeFace = false
  Placement = pos=(4205,855,0) rot=(0,0,1;1.5708rad)
  Points = (2) [(1935,-6395,0),(4725,-6395,0)]
  Start = (10600,2790,0)
  Subdivisions = 0
FEATURE [Part::FeaturePython] Wall595  label="перегородка 058"  # Arch/BIM 166 (typed FeaturePython)
  Align = 0
  Area = 8.091e+06
  Base = -> Line2182
  BlockHeight = 250
  BlockLength = 0
  CountBroken = 0
  CountEntire = 0
  Face = 0
  Height = 2900
  HorizontalArea = 514000
  IfcType = 166
  Joint = 0
  Length = 2790
  MakeBlocks = false
  Material = -> Material008
  MoveBase = false
  MoveWithHost = false
  Normal = (0,0,0)
  OffsetFirst = 0
  OffsetSecond = 300
  PerimeterLength = 5780
  Placement = pos=(0,0,3800) rot=(0,0,1;0rad)
  PredefinedType = 0
  Subtractions = -> [Fusion011003002002005003012]
  VerticalArea = 1.09212e+07
  Width = 100
FEATURE [Sketcher::SketchObject] Sketch  label="Sketch001"
  ExternalGeometry = -> [Wall592,Wall591]
  FullyConstrained = false
  Placement = pos=(0,0,0) rot=(1,0,0;1.5708rad)
  sketch-geometry (13):
    g0: LineSegment StartX=3730 StartY=5225 StartZ=0 EndX=6830 EndY=5225 EndZ=0
    g1: LineSegment StartX=5280 StartY=5425 StartZ=0 EndX=5280 EndY=5225 EndZ=0
    g2: LineSegment StartX=3730 StartY=5425 StartZ=0 EndX=3730 EndY=5225 EndZ=0
    g3: LineSegment StartX=6830 StartY=5425 StartZ=0 EndX=6830 EndY=5225 EndZ=0
    g4: LineSegment StartX=3730 StartY=5325 StartZ=0 EndX=5280 EndY=5325 EndZ=0
    g5: LineSegment StartX=5280 StartY=5325 StartZ=0 EndX=6830 EndY=5325 EndZ=0
    g6: LineSegment StartX=6830 StartY=5225 StartZ=0 EndX=8180.61 EndY=3725 EndZ=0
    g7: LineSegment StartX=8180.61 StartY=3725 StartZ=0 EndX=8449.73 EndY=3725 EndZ=0
    g8: LineSegment StartX=8449.73 StartY=3725 StartZ=0 EndX=6919.05 EndY=5425 EndZ=0
    g9: LineSegment StartX=3730 StartY=5225 StartZ=0 EndX=2379.39 EndY=3725 EndZ=0
    g10: LineSegment StartX=2379.39 StartY=3725 StartZ=0 EndX=2110.27 EndY=3725 EndZ=0
    g11: LineSegment StartX=2110.27 StartY=3725 StartZ=0 EndX=3640.95 EndY=5425 EndZ=0
    g12: LineSegment StartX=3640.95 StartY=5425 StartZ=0 EndX=6919.05 EndY=5425 EndZ=0
  constraints (39):
    c: Horizontal(g0)
    c: DistanceY(g0,g2) = 200
    c: DistanceX(g0,g0) = 3100
    c: DistanceY(g-1,g0) = 5225
    c: PointOnObject(g1,g0)
    c: Vertical(g1)
    c: Coincident(g2,g0)
    c: Vertical(g2)
    c: Coincident(g3,g0)
    c: Vertical(g3)
    c: PointOnObject(g4,g2)
    c: PointOnObject(g4,g1)
    c: Horizontal(g4)
    c: Coincident(g5,g4)
    c: PointOnObject(g5,g3)
    c: Horizontal(g5)
    c: Equal(g4,g5)
    c: DistanceX(g-1,g1) = 5280
    c: DistanceY(g0,g4) = 100
    c: Coincident(g6,g0)
    c: Coincident(g7,g6)
    c: Horizontal(g7)
    c: Coincident(g8,g7)
    c: Coincident(g9,g0)
    c: Coincident(g10,g9)
    c: Horizontal(g10)
    c: Coincident(g11,g10)
    c: Coincident(g12,g11)
    c: Coincident(g12,g8)
    c: Horizontal(g12)
    c: PointOnObject(g2,g12)
    c: Parallel(g11,g9)
    c: Parallel(g6,g8)
    c: Angle(g8) = 2.30383
    c: Angle(g11) = 0.837758
    c: Distance(g9,g11) = 200
    c: Distance(g6,g8) = 200
    c: Equal(g9,g6)
    c: DistanceY(g9,g0) = 1500
FEATURE [Part::Extrusion] Extrude099005016  label="roof_N_001"
  Base = -> Sketch
  Dir = (0,-1,2e-16)
  DirMode = 2
  FaceMakerClass = Part::FaceMakerBullseye
  LengthFwd = 6000
  LengthRev = 0
  Placement = pos=(0,663.503,220) rot=(1,0,0;0.279253rad)
  Reversed = true
  Solid = true
  Symmetric = false
FEATURE [Part::MultiCommon] Common097  label="roof_N_002"
  Shapes = -> [Extrude099005016,Extrude099005005]
FEATURE [Part::MultiCommon] Common098  label="roof_N_003"
  Shapes = -> [Common097,Roof036]
FEATURE [Sketcher::SketchObject] Sketch428
  ExternalGeometry = -> [Sketch]
  FullyConstrained = true
  Placement = pos=(0,0,0) rot=(1,0,0;1.5708rad)
  sketch-geometry (6):
    g0: LineSegment StartX=3730 StartY=5225 StartZ=0 EndX=6830 EndY=5225 EndZ=0
    g1: LineSegment StartX=6830 StartY=5225 StartZ=0 EndX=8180.61 EndY=3725 EndZ=0
    g2: LineSegment StartX=2379.39 StartY=3725 StartZ=0 EndX=3730 EndY=5225 EndZ=0
    g3: LineSegment StartX=2379.39 StartY=3725 StartZ=0 EndX=2379.39 EndY=8225 EndZ=0
    g4: LineSegment StartX=8180.61 StartY=3725 StartZ=0 EndX=8180.61 EndY=8225 EndZ=0
    g5: LineSegment StartX=2379.39 StartY=8225 StartZ=0 EndX=8180.61 EndY=8225 EndZ=0
  constraints (14):
    c: Coincident(g1,g0)
    c: Coincident(g2,g0)
    c: Coincident(g0,g-3)
    c: Coincident(g0,g-4)
    c: Coincident(g1,g-4)
    c: Coincident(g2,g-3)
    c: Coincident(g3,g2)
    c: Vertical(g3)
    c: Coincident(g4,g1)
    c: Vertical(g4)
    c: Coincident(g5,g3)
    c: Coincident(g5,g4)
    c: Horizontal(g5)
    c: DistanceY(g3,g3) = 4500
FEATURE [Part::Extrusion] Extrude099005017  label="roof_N_004"
  Base = -> Sketch428
  Dir = (0,-1,2e-16)
  DirMode = 2
  FaceMakerClass = Part::FaceMakerBullseye
  LengthFwd = 6000
  LengthRev = 0
  Placement = pos=(0,663.503,220) rot=(1,0,0;0.279253rad)
  Reversed = true
  Solid = true
  Symmetric = false
FEATURE [Part::Part2DObjectPython] Line2200  # Draft 2D object (typed FeaturePython)
  ChamferSize = 0
  Closed = true
  End = (9150,5580,0)
  FilletRadius = 0
  Length = 978.567
  MakeFace = false
  Placement = pos=(9780,5080,0) rot=(0,0,1;1.5708rad)
  Points = (2) [(500,-348.567,0),(500,630,0)]
  Start = (10128.6,5580,0)
  Subdivisions = 0
FEATURE [Part::FeaturePython] Wall596  label="перегородка 059"  # Arch/BIM 166 (typed FeaturePython)
  Align = 1
  Area = 2.73999e+06
  Base = -> Line2200
  BlockHeight = 250
  BlockLength = 0
  CountBroken = 0
  CountEntire = 0
  Face = 0
  Height = 2800
  HorizontalArea = 97856.7
  IfcType = 166
  Joint = 0
  Length = 978.567
  MakeBlocks = false
  Material = -> Material008
  MoveBase = false
  MoveWithHost = false
  Normal = (0,0,0)
  OffsetFirst = 0
  OffsetSecond = 300
  PerimeterLength = 2157.13
  Placement = pos=(0,0,3145) rot=(0,0,1;0rad)
  PredefinedType = 0
  VerticalArea = 6.03998e+06
  Width = 100
FEATURE [Part::Part2DObjectPython] Line2201  # Draft 2D object (typed FeaturePython)
  ChamferSize = 0
  Closed = true
  End = (10600,2790,0)
  FilletRadius = 0
  Length = 471.433
  MakeFace = false
  Placement = pos=(9780,5080,0) rot=(0,0,1;1.5708rad)
  Points = (2) [(-2290,-348.567,0),(-2290,-820,0)]
  Start = (10128.6,2790,0)
  Subdivisions = 0
FEATURE [Part::FeaturePython] Wall597  label="перегородка 060"  # Arch/BIM 166 (typed FeaturePython)
  Align = 1
  Area = 1.32001e+06
  Base = -> Line2201
  BlockHeight = 250
  BlockLength = 0
  CountBroken = 0
  CountEntire = 0
  Face = 0
  Height = 2800
  HorizontalArea = 47143.3
  IfcType = 166
  Joint = 0
  Length = 471.433
  MakeBlocks = false
  Material = -> Material008
  MoveBase = false
  MoveWithHost = false
  Normal = (0,0,0)
  OffsetFirst = 0
  OffsetSecond = 300
  PerimeterLength = 1142.87
  Placement = pos=(0,0,3145) rot=(0,0,1;0rad)
  PredefinedType = 0
  VerticalArea = 3.20002e+06
  Width = 100
FEATURE [Part::Part2DObjectPython] Line2202  # Draft 2D object (typed FeaturePython)
  ChamferSize = 0
  Closed = true
  End = (10128.6,2790,0)
  FilletRadius = 0
  Length = 978.567
  MakeFace = false
  Placement = pos=(9780,2290,0) rot=(0,0,1;1.5708rad)
  Points = (2) [(500,630,0),(500,-348.567,0)]
  Start = (9150,2790,0)
  Subdivisions = 0
FEATURE [Part::FeaturePython] Wall598  label="перегородка 061"  # Arch/BIM 166 (typed FeaturePython)
  Align = 1
  Area = 2.73999e+06
  Base = -> Line2202
  BlockHeight = 250
  BlockLength = 0
  CountBroken = 0
  CountEntire = 0
  Face = 0
  Height = 2800
  HorizontalArea = 97856.7
  IfcType = 166
  Joint = 0
  Length = 978.567
  MakeBlocks = false
  Material = -> Material008
  MoveBase = false
  MoveWithHost = false
  Normal = (0,0,0)
  OffsetFirst = 0
  OffsetSecond = 300
  PerimeterLength = 2157.13
  Placement = pos=(0,0,3145) rot=(0,0,1;0rad)
  PredefinedType = 0
  VerticalArea = 6.03998e+06
  Width = 100
FEATURE [Part::Part2DObjectPython] Line2203  # Draft 2D object (typed FeaturePython)
  ChamferSize = 0
  Closed = true
  End = (10128.6,5580,0)
  FilletRadius = 0
  Length = 471.433
  MakeFace = false
  Placement = pos=(9780,2290,0) rot=(0,0,1;1.5708rad)
  Points = (2) [(3290,-820,0),(3290,-348.567,0)]
  Start = (10600,5580,0)
  Subdivisions = 0
FEATURE [Part::FeaturePython] Wall599  label="перегородка 062"  # Arch/BIM 166 (typed FeaturePython)
  Align = 1
  Area = 1.32001e+06
  Base = -> Line2203
  BlockHeight = 250
  BlockLength = 0
  CountBroken = 0
  CountEntire = 0
  Face = 0
  Height = 2800
  HorizontalArea = 47143.3
  IfcType = 166
  Joint = 0
  Length = 471.433
  MakeBlocks = false
  Material = -> Material008
  MoveBase = false
  MoveWithHost = false
  Normal = (0,0,0)
  OffsetFirst = 0
  OffsetSecond = 300
  PerimeterLength = 1142.87
  Placement = pos=(0,0,3145) rot=(0,0,1;0rad)
  PredefinedType = 0
  VerticalArea = 3.20002e+06
  Width = 100
FEATURE [Part::MultiFuse] Fusion011003002002005003014  label="перегородка_кукушки_001"
  Shapes = -> [Wall598,Wall596]
FEATURE [Part::MultiFuse] Fusion011003002002005003015  label="перегородка_кукушки_002"
  Shapes = -> [Wall599,Wall597,Wall595]
FEATURE [Part::MultiCommon] Common099  label="перегородка_кукушки_003"
  Shapes = -> [Fusion011003002002005003014,Roof026]
FEATURE [Part::MultiFuse] Fusion011003002002005003016  label="перегородка_кукушки_004"
  Shapes = -> [Fusion011003002002005003015,Common099]
FEATURE [Part::Cut] Cut105003018  label="перегородка_кукушки_005"
  Base = -> Fusion011003002002005003016
  Tool = -> Roof039
FEATURE [Part::Mirroring] mirror016002018  label="перегородка_кукушки_005 (mirrored)"
  Base = (5285,2800,0)
  Normal = (-1,0,0)
  Source = -> Cut105003018
FEATURE [Part::MultiFuse] Fusion011003002002005003017  label="перегородка_кукушки_006"
  Shapes = -> [Cut105003018,mirror016002018]
FEATURE [Part::FeaturePython] Component241039  label="перегородки_кукушки_боковые_007"  # Arch/BIM 0 (typed FeaturePython)
  Base = -> Fusion011003002002005003017
  HorizontalArea = 0
  IfcData = attributes={"GlobalId": {"name": "GlobalId", "type": "IfcGloballyUniqueId", "is_enum": false, "enum_values": []}, "Description": {"... (+538 chars omitted),+1 more (map truncated)
  IfcType = 0
  Material = -> Material008
  MoveBase = false
  MoveWithHost = false
  PerimeterLength = 0
  PredefinedType = 0
  VerticalArea = 0
FEATURE [Part::Part2DObjectPython] Line2204  # Draft 2D object (typed FeaturePython)
  ChamferSize = 0
  Closed = true
  End = (6825,2785,0)
  FilletRadius = 0
  Length = 1810
  MakeFace = false
  Placement = pos=(4605,1855,0) rot=(0,0,1;1.5708rad)
  Points = (2) [(-880,-2220,0),(930,-2220,0)]
  Start = (6825,975,0)
  Subdivisions = 0
FEATURE [Part::FeaturePython] Wall600  label="перегородка 063"  # Arch/BIM 166 (typed FeaturePython)
  Align = 1
  Area = 6.0635e+06
  Base = -> Line2204
  BlockHeight = 250
  BlockLength = 0
  CountBroken = 0
  CountEntire = 0
  Face = 0
  Height = 3350
  HorizontalArea = 181000
  IfcType = 166
  Joint = 0
  Length = 1810
  MakeBlocks = false
  Material = -> Material008
  MoveBase = false
  MoveWithHost = false
  Normal = (0,0,0)
  OffsetFirst = 0
  OffsetSecond = 300
  PerimeterLength = 3820
  Placement = pos=(0,0,3145) rot=(0,0,1;0rad)
  PredefinedType = 0
  VerticalArea = 1.2797e+07
  Width = 100
FEATURE [Part::MultiCommon] Common100  label="перегородка_север_001"
  Shapes = -> [Wall600,Roof026]
FEATURE [Part::MultiFuse] Fusion011003002002005003018  label="перегородка_север_002"
  Shapes = -> [Common100,Wall592,Wall591,Wall588]
FEATURE [Part::Cut] Cut105003019  label="перегородка_север_003"
  Base = -> Fusion011003002002005003018
  Tool = -> Extrude099005017
FEATURE [Part::FeaturePython] Component241040  label="перегородка_север_004"  # Arch/BIM 0 (typed FeaturePython)
  Base = -> Cut105003019
  HorizontalArea = 0
  IfcData = attributes={"GlobalId": {"name": "GlobalId", "type": "IfcGloballyUniqueId", "is_enum": false, "enum_values": []}, "Description": {"... (+538 chars omitted),+1 more (map truncated)
  IfcType = 0
  Material = -> Material008
  MoveBase = false
  MoveWithHost = false
  PerimeterLength = 0
  PredefinedType = 0
  VerticalArea = 0
FEATURE [Part::Part2DObjectPython] Line2205  # Draft 2D object (typed FeaturePython)
  ChamferSize = 0
  Closed = true
  End = (3735,675,0)
  FilletRadius = 0
  Length = 3662.27
  MakeFace = false
  Placement = pos=(4205,855,0) rot=(0,0,1;1.5708rad)
  Points = (2) [(-180,4132.27,0),(-180,470,0)]
  Start = (72.7272,675,0)
  Subdivisions = 0
FEATURE [Part::FeaturePython] Wall601  label="перегородка 064"  # Arch/BIM 166 (typed FeaturePython)
  Align = 1
  Area = 1.06206e+07
  Base = -> Line2205
  BlockHeight = 250
  BlockLength = 0
  CountBroken = 0
  CountEntire = 0
  Face = 0
  Height = 2900
  HorizontalArea = 366227
  IfcType = 166
  Joint = 0
  Length = 3662.27
  MakeBlocks = false
  Material = -> Material008
  MoveBase = false
  MoveWithHost = false
  Normal = (0,0,0)
  OffsetFirst = 0
  OffsetSecond = 300
  PerimeterLength = 7524.55
  Placement = pos=(0,0,3145) rot=(0,0,1;0rad)
  PredefinedType = 0
  VerticalArea = 2.18212e+07
  Width = 100
FEATURE [Part::Part2DObjectPython] Line2206  # Draft 2D object (typed FeaturePython)
  ChamferSize = 0
  Closed = true
  End = (5685,7595,0)
  FilletRadius = 0
  Length = 5612.27
  MakeFace = false
  Placement = pos=(4205,7775,0) rot=(0,0,1;1.5708rad)
  Points = (2) [(-180,4132.27,0),(-180,-1480,0)]
  Start = (72.7272,7595,0)
  Subdivisions = 0
FEATURE [Part::FeaturePython] Wall602  label="перегородка 065"  # Arch/BIM 166 (typed FeaturePython)
  Align = 1
  Area = 1.62756e+07
  Base = -> Line2206
  BlockHeight = 250
  BlockLength = 0
  CountBroken = 0
  CountEntire = 0
  Face = 0
  Height = 2900
  HorizontalArea = 561227
  IfcType = 166
  Joint = 0
  Length = 5612.27
  MakeBlocks = false
  Material = -> Material008
  MoveBase = false
  MoveWithHost = false
  Normal = (0,0,0)
  OffsetFirst = 0
  OffsetSecond = 300
  PerimeterLength = 11424.5
  Placement = pos=(0,0,3145) rot=(0,0,1;0rad)
  PredefinedType = 0
  VerticalArea = 3.31312e+07
  Width = 100
FEATURE [Part::Part2DObjectPython] Line2207  # Draft 2D object (typed FeaturePython)
  ChamferSize = 0
  Closed = true
  End = (3535,4135,0)
  FilletRadius = 0
  Length = 3645
  MakeFace = false
  Placement = pos=(4205,4315,0) rot=(0,0,1;1.5708rad)
  Points = (2) [(-180,4315,0),(-180,670,0)]
  Start = (-110,4135,0)
  Subdivisions = 0
FEATURE [Part::FeaturePython] Wall603  label="перегородка 066"  # Arch/BIM 166 (typed FeaturePython)
  Align = 1
  Area = 10570500
  Base = -> Line2207
  BlockHeight = 250
  BlockLength = 0
  CountBroken = 0
  CountEntire = 0
  Face = 0
  Height = 2900
  HorizontalArea = 364500
  IfcType = 166
  Joint = 0
  Length = 3645
  MakeBlocks = false
  Material = -> Material008
  MoveBase = false
  MoveWithHost = false
  Normal = (0,0,0)
  OffsetFirst = 0
  OffsetSecond = 300
  PerimeterLength = 7490
  Placement = pos=(0,0,3145) rot=(0,0,1;0rad)
  PredefinedType = 0
  Subtractions = -> [Roof026]
  VerticalArea = 1.86959e+07
  Width = 100
FEATURE [Part::Part2DObjectPython] Line2209  # Draft 2D object (typed FeaturePython)
  ChamferSize = 0
  Closed = true
  End = (7060,2785,0)
  FilletRadius = 0
  Length = 3525
  MakeFace = false
  Placement = pos=(7070,2965,0) rot=(0,0,1;1.5708rad)
  Points = (2) [(-180,3535,0),(-180,10,0)]
  Start = (3535,2785,0)
  Subdivisions = 0
FEATURE [Part::FeaturePython] Wall605  label="перегородка 068"  # Arch/BIM 166 (typed FeaturePython)
  Align = 1
  Area = 1.02225e+07
  Base = -> Line2209
  BlockHeight = 250
  BlockLength = 0
  CountBroken = 0
  CountEntire = 0
  Face = 0
  Height = 2900
  HorizontalArea = 352500
  IfcType = 166
  Joint = 0
  Length = 3525
  MakeBlocks = false
  Material = -> Material008
  MoveBase = false
  MoveWithHost = false
  Normal = (0,0,0)
  OffsetFirst = 0
  OffsetSecond = 300
  PerimeterLength = 7250
  Placement = pos=(0,0,3145) rot=(0,0,1;0rad)
  PredefinedType = 0
  Subtractions = -> [Structure564]
  VerticalArea = 1.7185e+07
  Width = 100
FEATURE [Part::Part2DObjectPython] Line2210  # Draft 2D object (typed FeaturePython)
  ChamferSize = 0
  Closed = true
  End = (7455,875,0)
  FilletRadius = 0
  Length = 630
  MakeFace = false
  Placement = pos=(9960,1055,0) rot=(0,0,1;1.5708rad)
  Points = (2) [(-180,3135,0),(-180,2505,0)]
  Start = (6825,875,0)
  Subdivisions = 0
FEATURE [Part::FeaturePython] Wall606  label="перегородка 069"  # Arch/BIM 166 (typed FeaturePython)
  Align = 1
  Area = 1827000
  Base = -> Line2210
  BlockHeight = 250
  BlockLength = 0
  CountBroken = 0
  CountEntire = 0
  Face = 0
  Height = 2900
  HorizontalArea = 63000
  IfcType = 166
  Joint = 0
  Length = 630
  MakeBlocks = false
  Material = -> Material008
  MoveBase = false
  MoveWithHost = false
  Normal = (0,0,0)
  OffsetFirst = 0
  OffsetSecond = 300
  PerimeterLength = 1460
  Placement = pos=(0,0,3145) rot=(0,0,1;0rad)
  PredefinedType = 0
  VerticalArea = 4234000
  Width = 100
FEATURE [Part::Part2DObjectPython] Line2211  # Draft 2D object (typed FeaturePython)
  ChamferSize = 0
  Closed = true
  End = (10497.3,675,0)
  FilletRadius = 0
  Length = 2942.27
  MakeFace = false
  Placement = pos=(11090,855,0) rot=(0,0,1;1.5708rad)
  Points = (2) [(-180,3535,0),(-180,592.728,0)]
  Start = (7555,675,0)
  Subdivisions = 0
FEATURE [Part::FeaturePython] Wall607  label="перегородка 070"  # Arch/BIM 166 (typed FeaturePython)
  Align = 1
  Area = 8.53259e+06
  Base = -> Line2211
  BlockHeight = 250
  BlockLength = 0
  CountBroken = 0
  CountEntire = 0
  Face = 0
  Height = 2900
  HorizontalArea = 294227
  IfcType = 166
  Joint = 0
  Length = 2942.27
  MakeBlocks = false
  Material = -> Material008
  MoveBase = false
  MoveWithHost = false
  Normal = (0,0,0)
  OffsetFirst = 0
  OffsetSecond = 300
  PerimeterLength = 6084.54
  Placement = pos=(0,0,3145) rot=(0,0,1;0rad)
  PredefinedType = 0
  VerticalArea = 1.76452e+07
  Width = 100
FEATURE [Part::Part2DObjectPython] Line2213  # Draft 2D object (typed FeaturePython)
  ChamferSize = 0
  Closed = true
  End = (4235,5485,0)
  FilletRadius = 0
  Length = 700
  MakeFace = false
  Placement = pos=(7070,5665,0) rot=(0,0,1;1.5708rad)
  Points = (2) [(-180,3535,0),(-180,2835,0)]
  Start = (3535,5485,0)
  Subdivisions = 0
FEATURE [Part::FeaturePython] Wall609  label="перегородка 072"  # Arch/BIM 166 (typed FeaturePython)
  Align = 1
  Area = 2.03e+06
  Base = -> Line2213
  BlockHeight = 250
  BlockLength = 0
  CountBroken = 0
  CountEntire = 0
  Face = 0
  Height = 2900
  HorizontalArea = 70000
  IfcType = 166
  Joint = 0
  Length = 700
  MakeBlocks = false
  Material = -> Material008
  MoveBase = false
  MoveWithHost = false
  Normal = (0,0,0)
  OffsetFirst = 0
  OffsetSecond = 300
  PerimeterLength = 1600
  Placement = pos=(-9.09e-13,0,3145) rot=(0,0,1;0rad)
  PredefinedType = 0
  VerticalArea = 4.64e+06
  Width = 100
FEATURE [Part::Part2DObjectPython] Line2214  # Draft 2D object (typed FeaturePython)
  ChamferSize = 0
  Closed = true
  End = (4235,8395,0)
  FilletRadius = 0
  Length = 2810
  MakeFace = false
  Placement = pos=(13335,5660,0) rot=(0,0,1;1.5708rad)
  Points = (2) [(-75,9100,0),(2735,9100,0)]
  Start = (4235,5585,0)
  Subdivisions = 0
FEATURE [Part::FeaturePython] Wall610  label="перегородка 073"  # Arch/BIM 166 (typed FeaturePython)
  Align = 1
  Area = 8.149e+06
  Base = -> Line2214
  BlockHeight = 250
  BlockLength = 0
  CountBroken = 0
  CountEntire = 0
  Face = 0
  Height = 2900
  HorizontalArea = 281000
  IfcType = 166
  Joint = 0
  Length = 2810
  MakeBlocks = false
  Material = -> Material008
  MoveBase = false
  MoveWithHost = false
  Normal = (0,0,0)
  OffsetFirst = 0
  OffsetSecond = 300
  PerimeterLength = 5820
  Placement = pos=(0,0,3145) rot=(0,0,1;0rad)
  PredefinedType = 0
  VerticalArea = 16878000
  Width = 100
FEATURE [Part::Part2DObjectPython] Line2215  # Draft 2D object (typed FeaturePython)
  ChamferSize = 0
  Closed = true
  End = (10497.3,7595,0)
  FilletRadius = 0
  Length = 3437.27
  MakeFace = false
  Placement = pos=(10635,7775,0) rot=(0,0,1;1.5708rad)
  Points = (2) [(-180,3575,0),(-180,137.728,0)]
  Start = (7060,7595,0)
  Subdivisions = 0
FEATURE [Part::FeaturePython] Wall611  label="перегородка 074"  # Arch/BIM 166 (typed FeaturePython)
  Align = 1
  Area = 9.96809e+06
  Base = -> Line2215
  BlockHeight = 250
  BlockLength = 0
  CountBroken = 0
  CountEntire = 0
  Face = 0
  Height = 2900
  HorizontalArea = 343727
  IfcType = 166
  Joint = 0
  Length = 3437.27
  MakeBlocks = false
  Material = -> Material008
  MoveBase = false
  MoveWithHost = false
  Normal = (0,0,0)
  OffsetFirst = 0
  OffsetSecond = 300
  PerimeterLength = 7074.54
  Placement = pos=(0,0,3145) rot=(0,0,1;0rad)
  PredefinedType = 0
  VerticalArea = 2.05162e+07
  Width = 100
FEATURE [Part::Part2DObjectPython] Line2216  # Draft 2D object (typed FeaturePython)
  ChamferSize = 0
  Closed = true
  End = (172.727,7595,0)
  FilletRadius = 0
  Length = 2015
  MakeFace = false
  Placement = pos=(2907.73,5660,0) rot=(0,0,1;1.5708rad)
  Points = (2) [(-80,2735,0),(1935,2735,0)]
  Start = (172.727,5580,0)
  Subdivisions = 0
FEATURE [Part::FeaturePython] Wall612  label="перегородка 075"  # Arch/BIM 166 (typed FeaturePython)
  Align = 1
  Area = 5843500
  Base = -> Line2216
  BlockHeight = 250
  BlockLength = 0
  CountBroken = 0
  CountEntire = 0
  Face = 0
  Height = 2900
  HorizontalArea = 201500
  IfcType = 166
  Joint = 0
  Length = 2015
  MakeBlocks = false
  Material = -> Material008
  MoveBase = false
  MoveWithHost = false
  Normal = (0,0,0)
  OffsetFirst = 0
  OffsetSecond = 300
  PerimeterLength = 4230
  Placement = pos=(0,0,3145) rot=(0,0,1;0rad)
  PredefinedType = 0
  VerticalArea = 1.2267e+07
  Width = 100
FEATURE [Part::Part2DObjectPython] Line2217  # Draft 2D object (typed FeaturePython)
  ChamferSize = 0
  Closed = true
  End = (5685,5485,0)
  FilletRadius = 0
  Length = 600
  MakeFace = false
  Placement = pos=(8685,5665,0) rot=(0,0,1;1.5708rad)
  Points = (2) [(-180,3600,0),(-180,3000,0)]
  Start = (5085,5485,0)
  Subdivisions = 0
FEATURE [Part::FeaturePython] Wall613  label="перегородка 076"  # Arch/BIM 166 (typed FeaturePython)
  Align = 1
  Area = 1.74e+06
  Base = -> Line2217
  BlockHeight = 250
  BlockLength = 0
  CountBroken = 0
  CountEntire = 0
  Face = 0
  Height = 2900
  HorizontalArea = 60000
  IfcType = 166
  Joint = 0
  Length = 600
  MakeBlocks = false
  Material = -> Material008
  MoveBase = false
  MoveWithHost = false
  Normal = (0,0,0)
  OffsetFirst = 0
  OffsetSecond = 300
  PerimeterLength = 1400
  Placement = pos=(0,0,3145) rot=(0,0,1;0rad)
  PredefinedType = 0
  VerticalArea = 4.06e+06
  Width = 100
FEATURE [Part::Part2DObjectPython] Line2218  # Draft 2D object (typed FeaturePython)
  ChamferSize = 0
  Closed = true
  End = (5685,4485,0)
  FilletRadius = 0
  Length = 1000
  MakeFace = false
  Placement = pos=(5865,1950,0) rot=(0,0,1;0rad)
  Points = (2) [(-180,3535,0),(-180,2535,0)]
  Start = (5685,5485,0)
  Subdivisions = 0
FEATURE [Part::FeaturePython] Wall614  label="перегородка 077"  # Arch/BIM 166 (typed FeaturePython)
  Align = 1
  Area = 1150000
  Base = -> Line2218
  BlockHeight = 250
  BlockLength = 0
  CountBroken = 0
  CountEntire = 0
  Face = 0
  Height = 1150
  HorizontalArea = 100000
  IfcType = 166
  Joint = 0
  Length = 1000
  MakeBlocks = false
  Material = -> Material008
  MoveBase = false
  MoveWithHost = false
  Normal = (0,0,0)
  OffsetFirst = 0
  OffsetSecond = 300
  PerimeterLength = 2200
  Placement = pos=(0,0,3145) rot=(0,0,1;0rad)
  PredefinedType = 0
  VerticalArea = 2.53e+06
  Width = 100
FEATURE [Part::Part2DObjectPython] Line2220  # Draft 2D object (typed FeaturePython)
  ChamferSize = 0
  Closed = true
  End = (7455,-25,0)
  FilletRadius = 0
  Length = 1000
  MakeFace = false
  Placement = pos=(4205,855,0) rot=(0,0,1;1.5708rad)
  Points = (2) [(120,-3250,0),(-880,-3250,0)]
  Start = (7455,975,0)
  Subdivisions = 0
FEATURE [Part::FeaturePython] Wall616  label="перегородка 079"  # Arch/BIM 166 (typed FeaturePython)
  Align = 1
  Area = 2.9e+06
  Base = -> Line2220
  BlockHeight = 250
  BlockLength = 0
  CountBroken = 0
  CountEntire = 0
  Face = 0
  Height = 2900
  HorizontalArea = 100000
  IfcType = 166
  Joint = 0
  Length = 1000
  MakeBlocks = false
  Material = -> Material008
  MoveBase = false
  MoveWithHost = false
  Normal = (0,0,0)
  OffsetFirst = 0
  OffsetSecond = 300
  PerimeterLength = 2200
  Placement = pos=(0,0,3145) rot=(0,0,1;0rad)
  PredefinedType = 0
  VerticalArea = 6.38e+06
  Width = 100
FEATURE [Part::Part2DObjectPython] Line2221  # Draft 2D object (typed FeaturePython)
  ChamferSize = 0
  Closed = true
  End = (10397.3,775,0)
  FilletRadius = 0
  Length = 2015
  MakeFace = false
  Placement = pos=(7147.27,2670,0) rot=(0,0,1;1.5708rad)
  Points = (2) [(120,-3250,0),(-1895,-3250,0)]
  Start = (10397.3,2790,0)
  Subdivisions = 0
FEATURE [Part::FeaturePython] Wall617  label="перегородка 080"  # Arch/BIM 166 (typed FeaturePython)
  Align = 1
  Area = 5.8435e+06
  Base = -> Line2221
  BlockHeight = 250
  BlockLength = 0
  CountBroken = 0
  CountEntire = 0
  Face = 0
  Height = 2900
  HorizontalArea = 201500
  IfcType = 166
  Joint = 0
  Length = 2015
  MakeBlocks = false
  Material = -> Material008
  MoveBase = false
  MoveWithHost = false
  Normal = (0,0,0)
  OffsetFirst = 0
  OffsetSecond = 300
  PerimeterLength = 4230
  Placement = pos=(0,0,3145) rot=(0,0,1;0rad)
  PredefinedType = 0
  VerticalArea = 1.2267e+07
  Width = 100
FEATURE [Part::Part2DObjectPython] Line2222  # Draft 2D object (typed FeaturePython)
  ChamferSize = 0
  Closed = true
  End = (10397.3,5580,0)
  FilletRadius = 0
  Length = 2015
  MakeFace = false
  Placement = pos=(7147.27,7475,0) rot=(0,0,1;1.5708rad)
  Points = (2) [(120,-3250,0),(-1895,-3250,0)]
  Start = (10397.3,7595,0)
  Subdivisions = 0
FEATURE [Part::FeaturePython] Wall618  label="перегородка 081"  # Arch/BIM 166 (typed FeaturePython)
  Align = 1
  Area = 5.8435e+06
  Base = -> Line2222
  BlockHeight = 250
  BlockLength = 0
  CountBroken = 0
  CountEntire = 0
  Face = 0
  Height = 2900
  HorizontalArea = 201500
  IfcType = 166
  Joint = 0
  Length = 2015
  MakeBlocks = false
  Material = -> Material008
  MoveBase = false
  MoveWithHost = false
  Normal = (0,0,0)
  OffsetFirst = 0
  OffsetSecond = 300
  PerimeterLength = 4230
  Placement = pos=(0,0,3145) rot=(0,0,1;0rad)
  PredefinedType = 0
  VerticalArea = 1.2267e+07
  Width = 100
FEATURE [Part::Part2DObjectPython] Line2223  # Draft 2D object (typed FeaturePython)
  ChamferSize = 0
  Closed = true
  End = (72.7272,775,0)
  FilletRadius = 0
  Length = 2015
  MakeFace = false
  Placement = pos=(-3177.27,955,0) rot=(0,0,1;1.5708rad)
  Points = (2) [(1835,-3250,0),(-180,-3250,0)]
  Start = (72.7272,2790,0)
  Subdivisions = 0
FEATURE [Part::FeaturePython] Wall619  label="перегородка 082"  # Arch/BIM 166 (typed FeaturePython)
  Align = 1
  Area = 5.8435e+06
  Base = -> Line2223
  BlockHeight = 250
  BlockLength = 0
  CountBroken = 0
  CountEntire = 0
  Face = 0
  Height = 2900
  HorizontalArea = 201500
  IfcType = 166
  Joint = 0
  Length = 2015
  MakeBlocks = false
  Material = -> Material008
  MoveBase = false
  MoveWithHost = false
  Normal = (0,0,0)
  OffsetFirst = 0
  OffsetSecond = 300
  PerimeterLength = 4230
  Placement = pos=(0,0,3145) rot=(0,0,1;0rad)
  PredefinedType = 0
  VerticalArea = 1.2267e+07
  Width = 100
FEATURE [Part::Part2DObjectPython] Line2224  # Draft 2D object (typed FeaturePython)
  ChamferSize = 0
  Closed = true
  End = (6910,2885,0)
  FilletRadius = 0
  Length = 2700
  MakeFace = false
  Placement = pos=(3660,5465,0) rot=(0,0,1;1.5708rad)
  Points = (2) [(120,-3250,0),(-2580,-3250,0)]
  Start = (6910,5585,0)
  Subdivisions = 0
FEATURE [Part::FeaturePython] Wall620  label="перегородка 083"  # Arch/BIM 166 (typed FeaturePython)
  Align = 1
  Area = 7.83e+06
  Base = -> Line2224
  BlockHeight = 250
  BlockLength = 0
  CountBroken = 0
  CountEntire = 0
  Face = 0
  Height = 2900
  HorizontalArea = 405000
  IfcType = 166
  Joint = 0
  Length = 2700
  MakeBlocks = false
  Material = -> Material008
  MoveBase = false
  MoveWithHost = false
  Normal = (0,0,0)
  OffsetFirst = 0
  OffsetSecond = 300
  PerimeterLength = 5700
  Placement = pos=(0,0,3145) rot=(0,0,1;0rad)
  PredefinedType = 0
  Subtractions = -> [Structure576]
  VerticalArea = 1.293e+07
  Width = 150
FEATURE [Part::Part2DObjectPython] Line2225  # Draft 2D object (typed FeaturePython)
  ChamferSize = 0
  Closed = true
  End = (5685,5485,0)
  FilletRadius = 0
  Length = 2910
  MakeFace = false
  Placement = pos=(2435,8275,0) rot=(0,0,1;1.5708rad)
  Points = (2) [(120,-3250,0),(-2790,-3250,0)]
  Start = (5685,8395,0)
  Subdivisions = 0
FEATURE [Part::FeaturePython] Wall621  label="перегородка 084"  # Arch/BIM 166 (typed FeaturePython)
  Align = 1
  Area = 8.439e+06
  Base = -> Line2225
  BlockHeight = 250
  BlockLength = 0
  CountBroken = 0
  CountEntire = 0
  Face = 0
  Height = 2900
  HorizontalArea = 291000
  IfcType = 166
  Joint = 0
  Length = 2910
  MakeBlocks = false
  Material = -> Material008
  MoveBase = false
  MoveWithHost = false
  Normal = (0,0,0)
  OffsetFirst = 0
  OffsetSecond = 300
  PerimeterLength = 6020
  Placement = pos=(0,0,3145) rot=(0,0,1;0rad)
  PredefinedType = 0
  VerticalArea = 1.7458e+07
  Width = 100
FEATURE [Part::Part2DObjectPython] Line2226  # Draft 2D object (typed FeaturePython)
  ChamferSize = 0
  Closed = true
  End = (6960,5585,0)
  FilletRadius = 0
  Length = 2810
  MakeFace = false
  Placement = pos=(3710,8275,0) rot=(0,0,1;1.5708rad)
  Points = (2) [(120,-3250,0),(-2690,-3250,0)]
  Start = (6960,8395,0)
  Subdivisions = 0
FEATURE [Part::FeaturePython] Wall622  label="перегородка 085"  # Arch/BIM 166 (typed FeaturePython)
  Align = 1
  Area = 8.149e+06
  Base = -> Line2226
  BlockHeight = 250
  BlockLength = 0
  CountBroken = 0
  CountEntire = 0
  Face = 0
  Height = 2900
  HorizontalArea = 281000
  IfcType = 166
  Joint = 0
  Length = 2810
  MakeBlocks = false
  Material = -> Material008
  MoveBase = false
  MoveWithHost = false
  Normal = (0,0,0)
  OffsetFirst = 0
  OffsetSecond = 300
  PerimeterLength = 5820
  Placement = pos=(0,0,3145) rot=(0,0,1;0rad)
  PredefinedType = 0
  VerticalArea = 1.6878e+07
  Width = 100
FEATURE [Part::Part2DObjectPython] Line2227  # Draft 2D object (typed FeaturePython)
  ChamferSize = 0
  Closed = true
  End = (3535,2885,0)
  FilletRadius = 0
  Length = 2600
  MakeFace = false
  Placement = pos=(285,5365,0) rot=(0,0,1;1.5708rad)
  Points = (2) [(120,-3250,0),(-2480,-3250,0)]
  Start = (3535,5485,0)
  Subdivisions = 0
FEATURE [Part::FeaturePython] Wall623  label="перегородка 086"  # Arch/BIM 166 (typed FeaturePython)
  Align = 1
  Area = 7540000
  Base = -> Line2227
  BlockHeight = 250
  BlockLength = 0
  CountBroken = 0
  CountEntire = 0
  Face = 0
  Height = 2900
  HorizontalArea = 390000
  IfcType = 166
  Joint = 0
  Length = 2600
  MakeBlocks = false
  Material = -> Material008
  MoveBase = false
  MoveWithHost = false
  Normal = (0,0,0)
  OffsetFirst = 0
  OffsetSecond = 300
  PerimeterLength = 5500
  Placement = pos=(0,0,3145) rot=(0,0,1;0rad)
  PredefinedType = 0
  Subtractions = -> [Structure559,Structure558]
  VerticalArea = 8750000
  Width = 150
FEATURE [Part::MultiFuse] Fusion011003002002005003020  label="перегородки мансарды 001"
  Shapes = -> [Wall601,Wall602,Wall605,Wall606,Wall607,Wall609,Wall610,Wall611,Wall612,Wall613,Wall616,Wall617,Wall618,Wall619,Wall620,Wall621,Wall622,Wall623]
FEATURE [Part::Cut] Cut105003021  label="перегородки мансарды габарит 054"
  Base = -> Fusion011003002002005003020
  Tool = -> Roof026
FEATURE [Part::FeaturePython] Component241042  label="перегородки мансарды габарит 055"  # Arch/BIM 0 (typed FeaturePython)
  Base = -> Cut105003021
  HorizontalArea = 0
  IfcData = attributes={"GlobalId": {"name": "GlobalId", "type": "IfcGloballyUniqueId", "is_enum": false, "enum_values": []}, "Description": {"... (+538 chars omitted),+1 more (map truncated)
  IfcType = 0
  Material = -> Material008
  MoveBase = false
  MoveWithHost = false
  PerimeterLength = 0
  PredefinedType = 0
  VerticalArea = 0
FEATURE [Part::FeaturePython] Structure689  label="Ванна 180х092"  # Arch/BIM 52 (typed FeaturePython)
  Base = -> Wire1017
  FaceMaker = 0
  GlobalId = 2VbcwV0QPCqROXcrzT3$_s
  Height = 600
  HorizontalArea = 1.44e+06
  IfcData = IfcUID=2VbcwV0QPCqROXcrzT3$_s,+2 more (map truncated)
  IfcType = 52
  Length = 0
  Material = -> Material013
  MoveBase = false
  MoveWithHost = false
  Nodes = (2) [(-2856.79,7112.64,0),(-2856.79,7112.64,600)]
  NodesOffset = 0
  Normal = (0,0,1)
  PerimeterLength = 5200
  Placement = pos=(0,0,3145) rot=(0,0,1;0rad)
  VerticalArea = 3.12e+06
  Width = 100
FEATURE [Part::FeaturePython] Wall495  label="Облицовка ванны плиткой 30мм001"  # Arch/BIM 166 (typed FeaturePython)
  Align = 0
  Area = 3.228e+06
  Base = -> Wire1019
  BlockHeight = 0
  BlockLength = 0
  CountBroken = 0
  CountEntire = 0
  Face = 0
  GlobalId = 36KkLHJl1D_AUwy3AkMKZ7
  Height = 600
  HorizontalArea = 152800
  IfcData = IfcUID=36KkLHJl1D_AUwy3AkMKZ7,+2 more (map truncated)
  IfcType = 166
  Joint = 0
  Length = 5380
  MakeBlocks = false
  Material = -> Material013
  MoveBase = false
  MoveWithHost = false
  Normal = (0,0,0)
  OffsetFirst = 0
  OffsetSecond = 0
  PerimeterLength = 5380
  Placement = pos=(0,0,3145) rot=(0,0,1;0rad)
  PredefinedType = 0
  Subtractions = -> [Structure689]
  VerticalArea = 3.228e+06
  Width = 300
FEATURE [App::GeometryPython] BuildingPart124  label="Сантехника и мебель в ванной (мансарда)"  # Arch/BIM 172 (typed FeaturePython)
  Area = 3.228e+06
  Group = -> [Structure602,Component241012,Structure608,Structure610,Wall495,Box3284]
  Height = 3130
  HeightPropagate = true
  IfcData = attributes={"GlobalId": {"name": "GlobalId", "type": "IfcGloballyUniqueId", "is_enum": false, "enum_values": []}, "Description": {"... (+484 chars omitted),+1 more (map truncated)
  IfcType = 172
  LevelOffset = 0
  Placement = pos=(0,0,3135) rot=(0,0,1;0rad)
  PredefinedType = 0
FEATURE [Part::Feature] Compound006039  label="шкаф 60х60 секция 021"
  Placement = pos=(-11902.7,355,0) rot=(0,0,1;0rad)
  shape: bbox 600 x 600 x 2e-07 mm, 0 faces, 0 solids (baked)
FEATURE [Part::Feature] Compound006040  label="шкаф 60х60 секция 022"
  Placement = pos=(-14145,355,0) rot=(0,0,1;0rad)
  shape: bbox 600 x 600 x 2e-07 mm, 0 faces, 0 solids (baked)
FEATURE [Part::Box] Box3295  label="столешница011"
  AttacherType = Attacher::AttachEngine3D
  Height = 30
  Length = 700
  Placement = pos=(-1000,-3200,720) rot=(0,0,-1;1.5708rad)
  Width = 1200
FEATURE [Part::Box] Box3296  label="ножка065"
  AttacherType = Attacher::AttachEngine3D
  Height = 720
  Length = 600
  Placement = pos=(160,-3200,0) rot=(0,0,-1;1.5708rad)
  Width = 40
FEATURE [Part::Box] Box3297  label="ножка066"
  AttacherType = Attacher::AttachEngine3D
  Height = 720
  Length = 600
  Placement = pos=(-1000,-3200,0) rot=(0,0,-1;1.5708rad)
  Width = 40
FEATURE [Part::Box] Box3298  label="ножка067"
  AttacherType = Attacher::AttachEngine3D
  Height = 200
  Length = 40
  Placement = pos=(-960,-3200,420) rot=(0,0,-1;1.5708rad)
  Width = 1120
FEATURE [Part::Compound] Compound006041  label="стол 1200х700"
  Links = -> [Box3298,Box3295,Box3296,Box3297]
FEATURE [Part::Box] Box3299  label="столешница012"
  AttacherType = Attacher::AttachEngine3D
  Height = 30
  Length = 700
  Placement = pos=(-1000,-3200,720) rot=(0,0,-1;1.5708rad)
  Width = 2500
FEATURE [Part::Box] Box3300  label="ножка068"
  AttacherType = Attacher::AttachEngine3D
  Height = 720
  Length = 600
  Placement = pos=(1460,-3200,0) rot=(0,0,-1;1.5708rad)
  Width = 40
FEATURE [Part::Box] Box3301  label="ножка069"
  AttacherType = Attacher::AttachEngine3D
  Height = 720
  Length = 600
  Placement = pos=(-1000,-3200,0) rot=(0,0,-1;1.5708rad)
  Width = 40
FEATURE [Part::Box] Box3302  label="ножка070"
  AttacherType = Attacher::AttachEngine3D
  Height = 200
  Length = 40
  Placement = pos=(-960,-3200,420) rot=(0,0,-1;1.5708rad)
  Width = 2420
FEATURE [Part::Compound] Compound006042  label="стол 2500*700"
  Links = -> [Box3302,Box3299,Box3300,Box3301]
FEATURE [App::GeometryPython] BuildingPart138  label="Мебель (редактируемая)"  # Arch/BIM 172 (typed FeaturePython)
  Area = 0
  Group = -> [Fusion003,Fusion011,Fusion011003,Fusion011003002,mirror016,Fusion011003002002005,mirror016002,Compound006,Compound,Structure347,Structure471,Cut105003,Compound006041,Compound006042]
  Height = 0
  HeightPropagate = true
  IfcData = attributes={"GlobalId": {"name": "GlobalId", "type": "IfcGloballyUniqueId", "is_enum": false, "enum_values": []}, "Description": {"... (+484 chars omitted),+1 more (map truncated)
  IfcType = 172
  LevelOffset = 0
  PredefinedType = 0
FEATURE [Part::Feature] Compound006041001  label="стол 1200х701"
  Placement = pos=(-3220,5255,3145) rot=(0,0,1;1.5708rad)
  shape: bbox 700 x 1200 x 750 mm, 24 faces, 4 solids (baked)
FEATURE [Part::Feature] Compound006042001  label="стол 2500*701"
  Placement = pos=(13790,4435,3145) rot=(0,0,-1;1.5708rad)
  shape: bbox 700 x 2500 x 750 mm, 24 faces, 4 solids (baked)
FEATURE [Part::Feature] Compound006041002  label="стол 1200х702"
  Placement = pos=(-3220,3915,3145) rot=(0,0,1;1.5708rad)
  shape: bbox 700 x 1200 x 750 mm, 24 faces, 4 solids (baked)
FEATURE [Part::Part2DObjectPython] Clone2D025  label="кровля_контур_обрезки (2D)"  # Draft 2D object (typed FeaturePython)
  Fuse = false
  Objects = -> [Wire817]
  Placement = pos=(-1210,-1210,0) rot=(0,0,1;0rad)
  Scale = (1,1,1)
FEATURE [Part::Part2DObjectPython] Line2230  # Draft 2D object (typed FeaturePython)
  Area = 0
  ChamferSize = 0
  Closed = false
  End = (1499.34,5580,0)
  FilletRadius = 0
  Length = 499.341
  MakeFace = true
  Placement = pos=(1000,5580,0) rot=(0,0,1;0rad)
  Points = (2) [(0,0,0),(499.341,0,0)]
  Start = (1000,5580,0)
  Subdivisions = 0
FEATURE [Part::Part2DObjectPython] Line2231  # Draft 2D object (typed FeaturePython)
  Area = 0
  ChamferSize = 0
  Closed = false
  End = (1587.84,2790,0)
  FilletRadius = 0
  Length = 587.841
  MakeFace = true
  Placement = pos=(1000,2790,0) rot=(0,0,1;0rad)
  Points = (2) [(0,0,0),(587.841,0,0)]
  Start = (1000,2790,0)
  Subdivisions = 0
FEATURE [Part::Part2DObjectPython] Line2232  # Draft 2D object (typed FeaturePython)
  Area = 0
  ChamferSize = 0
  Closed = false
  End = (-130,2790,0)
  FilletRadius = 0
  Length = 2790
  MakeFace = true
  Placement = pos=(-130,5580,0) rot=(0,0,1;0rad)
  Points = (2) [(0,0,0),(-2.55795e-13,-2790,0)]
  Start = (-130,5580,0)
  Subdivisions = 0
FEATURE [Part::Part2DObjectPython] Line2233  # Draft 2D object (typed FeaturePython)
  Area = 0
  ChamferSize = 0
  Closed = false
  End = (2305.36,4185,0)
  FilletRadius = 0
  Length = 1971.62
  MakeFace = true
  Placement = pos=(1042.14,2671.21,0) rot=(0,0,1;0rad)
  Points = (2) [(0,0,0),(1263.22,1513.79,0)]
  Start = (1042.14,2671.21,0)
  Subdivisions = 0
FEATURE [Part::Part2DObjectPython] Line2234  # Draft 2D object (typed FeaturePython)
  Area = 0
  ChamferSize = 0
  Closed = false
  End = (1042.14,5698.79,0)
  FilletRadius = 0
  Length = 1971.62
  MakeFace = true
  Placement = pos=(2305.36,4185,0) rot=(0,0,1;0rad)
  Points = (2) [(0,0,0),(-1263.22,1513.79,0)]
  Start = (2305.36,4185,0)
  Subdivisions = 0
FEATURE [Part::Feature] Compound006042002  label="шкаф 60х60 секция 023"
  Placement = pos=(-13545,-245,0) rot=(0,0,1;0rad)
  shape: bbox 600 x 600 x 2e-07 mm, 0 faces, 0 solids (baked)
FEATURE [Part::Extrusion] Extrude099005019  label="Габарит человека 006"
  Base = -> Sketch250
  Dir = (0,-1,2e-16)
  DirMode = 2
  FaceMakerClass = Part::FaceMakerBullseye
  LengthFwd = 290
  LengthRev = 0
  Placement = pos=(1155,4800,3145) rot=(0,0,1;1.5708rad)
  Solid = true
  Symmetric = false
FEATURE [Part::Part2DObjectPython] Line2238  # Draft 2D object (typed FeaturePython)
  Area = 0
  ChamferSize = 0
  Closed = true
  End = (-175,-170,0)
  FilletRadius = 0
  Length = 8710
  MakeFace = true
  Placement = pos=(11433.9,575,0) rot=(0,0,1;1.5708rad)
  Points = (2) [(7965,11608.9,0),(-745,11608.9,0)]
  Start = (-175,8540,0)
  Subdivisions = 0
FEATURE [Part::FeaturePython] Wall624  label="мауэрлат надставка 002"  # Arch/BIM 166 (typed FeaturePython)
  Align = 0
  Area = 1742000
  Base = -> Line2238
  BlockHeight = 0
  BlockLength = 0
  CountBroken = 0
  CountEntire = 0
  Face = 0
  GlobalId = 1B71KP0Y9AOfuyJlUXW0eC
  Height = 200
  HorizontalArea = 1306500
  IfcData = IfcUID=1B71KP0Y9AOfuyJlUXW0eC; attributes={"GlobalId": {"value": "1B71KP0Y9AOfuyJlUXW0eC"}}
  IfcType = 166
  Joint = 0
  Length = 8710
  MakeBlocks = false
  Material = -> Material
  MoveBase = false
  MoveWithHost = false
  Normal = (0,0,0)
  OffsetFirst = 0
  OffsetSecond = 0
  PerimeterLength = 17720
  Placement = pos=(0,0,3975) rot=(0,0,1;0rad)
  PredefinedType = 0
  VerticalArea = 3544000
  Width = 150
FEATURE [Part::Part2DObjectPython] Line2239  # Draft 2D object (typed FeaturePython)
  Area = 0
  ChamferSize = 0
  Closed = true
  End = (10745,-170,0)
  FilletRadius = 0
  Length = 8710
  MakeFace = true
  Placement = pos=(22353.9,575,0) rot=(0,0,1;1.5708rad)
  Points = (2) [(7965,11608.9,0),(-745,11608.9,0)]
  Start = (10745,8540,0)
  Subdivisions = 0
FEATURE [Part::FeaturePython] Wall625  label="мауэрлат надставка 001"  # Arch/BIM 166 (typed FeaturePython)
  Align = 1
  Area = 1.742e+06
  Base = -> Line2239
  BlockHeight = 0
  BlockLength = 0
  CountBroken = 0
  CountEntire = 0
  Face = 0
  GlobalId = 1B71KP0Y9AOfuyJlUXW0eC
  Height = 200
  HorizontalArea = 1.3065e+06
  IfcData = IfcUID=1B71KP0Y9AOfuyJlUXW0eC; attributes={"GlobalId": {"value": "1B71KP0Y9AOfuyJlUXW0eC"}}
  IfcType = 166
  Joint = 0
  Length = 8710
  MakeBlocks = false
  Material = -> Material
  MoveBase = false
  MoveWithHost = false
  Normal = (0,0,0)
  OffsetFirst = 0
  OffsetSecond = 0
  PerimeterLength = 17720
  Placement = pos=(0,0,3975) rot=(0,0,1;0rad)
  PredefinedType = 0
  VerticalArea = 3.544e+06
  Width = 150
FEATURE [Part::Part2DObjectPython] Wire1078  # Draft 2D object (typed FeaturePython)
  Area = 0
  ChamferSize = 0
  Closed = true
  End = (26138,-9920.38,0)
  FilletRadius = 0
  Length = 169864
  MakeFace = false
  Placement = pos=(-19290.4,-9920.38,0) rot=(0,0,1;0rad)
  Points = (4) [(0,0,0),(0,39503.6,0),(45428.4,39503.6,0),(45428.4,3.27418e-11,0)]
  Start = (-19290.4,-9920.38,0)
  Subdivisions = 0
FEATURE [Part::Extrusion] Extrude099005020
  Base = -> Wire1078
  Dir = (0,0,-1)
  DirMode = 0
  FaceMakerClass = Part::FaceMakerBullseye
  LengthFwd = 3000
  LengthRev = 0
  Placement = pos=(0,5.91525,-3200) rot=(1,0,0;0.009948rad)
  Reversed = true
  Solid = true
  Symmetric = false
FEATURE [Part::FeaturePython] Structure690  label="грунт в границах участка001"  # Arch/BIM 52 (typed FeaturePython)
  Base = -> Wire460
  FaceMaker = 0
  Height = 1000
  HorizontalArea = 1.47224e+09
  IfcData = complex_attributes={"OwnerHistory": {}, "IsNestedBy": {}, "IsDecomposedBy": {}, "IsDefinedBy": {}, "ObjectPlacement": {}, "Representation":... (+4 chars omitted)
  IfcType = 52
  Length = 0
  MoveBase = false
  MoveWithHost = false
  Nodes = (2) [(5892.5,11504.2,0),(5892.5,11504.2,-1000)]
  NodesOffset = 0
  Normal = (0,0,-1)
  PerimeterLength = 156987
  Placement = pos=(0,0,-190) rot=(0,0,1;0rad)
  VerticalArea = 1.56987e+08
  Width = 100
FEATURE [Part::MultiCommon] Common101  label="грунт в границах участка с уклоном 001"
  Shapes = -> [Extrude099005020,Structure690]
FEATURE [Part::Part2DObjectPython] Rectangle4200  # Draft 2D object (typed FeaturePython)
  ChamferSize = 0
  Columns = 1
  FilletRadius = 0
  Height = 1045
  Length = 3600
  MakeFace = false
  Placement = pos=(6605,9005,0) rot=(0,0,1;0rad)
  Rows = 1
FEATURE [Part::FeaturePython] Structure692  label="габарит терассы 001"  # Arch/BIM 52 (typed FeaturePython)
  Base = -> Rectangle4200
  FaceMaker = 0
  Height = 180
  HorizontalArea = 3.762e+06
  IfcData = complex_attributes={"OwnerHistory": {}, "IsNestedBy": {}, "IsDecomposedBy": {}, "IsDefinedBy": {}, "ObjectPlacement": {}, "Representation":... (+4 chars omitted)
  IfcType = 52
  Length = 0
  Material = -> Material018
  MoveBase = false
  MoveWithHost = false
  Nodes = (2) [(5975,-1250,0),(5975,-1250,-350)]
  NodesOffset = 0
  Normal = (0,0,-1)
  PerimeterLength = 9290
  Placement = pos=(0,0,-50) rot=(0,0,1;0rad)
  VerticalArea = 1.6722e+06
  Width = 100
FEATURE [App::GeometryPython] BuildingPart035  label="Внешние элементы"  # Arch/BIM 52 (typed FeaturePython)
  Area = 0
  Group = -> [Structure140,Structure692]
  Height = 0
  HeightPropagate = true
  IfcData = complex_attributes={"OwnerHistory": {}, "IsNestedBy": {}, "IsDecomposedBy": {}, "IsDefinedBy": {}, "ObjectPlacement": {}, "Representation":... (+4 chars omitted)
  IfcType = 52
  LevelOffset = 0
FEATURE [Part::Extrusion] Extrude099005021
  Base = -> Wire1078
  Dir = (0,0,-1)
  DirMode = 0
  FaceMakerClass = Part::FaceMakerBullseye
  LengthFwd = 3000
  LengthRev = 0
  Placement = pos=(0,5.91525,-2830) rot=(-1,0,0;0.039968rad)
  Reversed = true
  Solid = true
  Symmetric = false
FEATURE [Part::MultiCommon] Common102  label="грунт в границах участка с уклонами 001"
  Shapes = -> [Common101,Extrude099005021]
FEATURE [Part::Extrusion] Extrude099005022
  Base = -> Wire1078
  Dir = (0,0,-1)
  DirMode = 0
  FaceMakerClass = Part::FaceMakerBullseye
  LengthFwd = 3000
  LengthRev = 0
  Placement = pos=(-3.85716,0,-3164) rot=(0,-1,0;0.039968rad)
  Reversed = true
  Solid = true
  Symmetric = false
FEATURE [Part::MultiCommon] Common103  label="грунт в границах участка с уклонами 002"
  Shapes = -> [Common102,Extrude099005022]
FEATURE [Part::Extrusion] Extrude099005023
  Base = -> Wire1078
  Dir = (0,0,-1)
  DirMode = 0
  FaceMakerClass = Part::FaceMakerBullseye
  LengthFwd = 3000
  LengthRev = 0
  Placement = pos=(1.36922,0,-3078) rot=(0,1,0;0.009948rad)
  Reversed = true
  Solid = true
  Symmetric = false
FEATURE [Part::MultiCommon] Common104  label="грунт в границах участка с уклонами  (4 ската)"
  Shapes = -> [Extrude099005023,Common103]
FEATURE [Part::Part2DObjectPython] Wire1079  # Draft 2D object (typed FeaturePython)
  Area = 0
  ChamferSize = 0
  Closed = true
  End = (22054.4,-9277.51,0)
  FilletRadius = 0
  Length = 1520
  MakeFace = false
  Placement = pos=(21967.4,-9647.41,0) rot=(0,0,1;1.38437rad)
  Points = (4) [(0,0,0),(-16.9653,-379.621,0),(362.656,-396.586,0),(379.621,-16.9653,0)]
  Start = (21967.4,-9647.41,0)
  Subdivisions = 0
FEATURE [Part::FeaturePython] Roof018  label="Крышка столба 001"  # Arch/BIM 113 (typed FeaturePython)
  Angles = [15,15,15,15]
  Base = -> Wire1079
  BorderLength = 1920
  Face = 0
  Flip = false
  Heights = [50.9103,50.9103,50.9103,50.9103]
  HorizontalArea = 230400
  IdRel = [-1,-1,-1,-1]
  IfcData = attributes={"GlobalId": {"name": "GlobalId", "type": "IfcGloballyUniqueId", "is_enum": false, "enum_values": []}, "Description": {"... (+613 chars omitted),+1 more (map truncated)
  IfcType = 113
  Material = -> Material018
  MoveBase = false
  MoveWithHost = false
  Overhang = [50,50,50,50]
  PerimeterLength = 0
  Placement = pos=(0,0,1900) rot=(0,0,1;0rad)
  PredefinedType = 0
  RidgeLength = 1381.8
  Runs = [190,190,190,190]
  Thickness = [50,50,50,50]
  VerticalArea = 99386.5
FEATURE [Part::Part2DObjectPython] Line2240  # Draft 2D object (typed FeaturePython)
  Area = 0
  ChamferSize = 0
  Closed = false
  End = (22054.4,-9277.51,0)
  FilletRadius = 0
  Length = 380
  MakeFace = false
  Placement = pos=(21967.4,-9647.41,0) rot=(0,0,-1;0.062584rad)
  Points = (2) [(0,0,0),(63.7299,374.618,0)]
  Start = (21967.4,-9647.41,0)
  Subdivisions = 0
FEATURE [Part::FeaturePython] Wall316  label="Столб 001"  # Arch/BIM 166 (typed FeaturePython)
  Align = 0
  Area = 836000
  Base = -> Line2240
  BlockHeight = 0
  BlockLength = 0
  CountBroken = 0
  CountEntire = 0
  Face = 0
  Height = 2200
  HorizontalArea = 144400
  IfcData = attributes={"GlobalId": {"name": "GlobalId", "type": "IfcGloballyUniqueId", "is_enum": false, "enum_values": []}, "Description": {"... (+533 chars omitted),+1 more (map truncated)
  IfcType = 166
  Joint = 0
  Length = 380
  MakeBlocks = false
  Material = -> Material003
  MoveBase = false
  MoveWithHost = false
  Normal = (0,0,0)
  OffsetFirst = 0
  OffsetSecond = 0
  PerimeterLength = 1520
  Placement = pos=(0,0,-320) rot=(0,0,1;0rad)
  PredefinedType = 0
  VerticalArea = 3.344e+06
  Width = 380
FEATURE [App::GeometryPython] BuildingPart108  label="Откатные ворота 4.5 с калиткой 1м"  # Arch/BIM 172 (typed FeaturePython)
  Area = 1.4956e+07
  Group = -> [Wall315,Wall316,Wall319,Space,Space001,Roof018]
  Height = 0
  HeightPropagate = true
  IfcData = attributes={"GlobalId": {"name": "GlobalId", "type": "IfcGloballyUniqueId", "is_enum": false, "enum_values": []}, "Description": {"... (+484 chars omitted),+1 more (map truncated)
  IfcType = 172
  LevelOffset = 0
  PredefinedType = 0
FEATURE [Part::FeaturePython] Roof  label="Крышка столба 002"  # Arch/BIM 113 (typed FeaturePython)
  BorderLength = 0
  CloneOf = -> Roof018
  Face = 0
  Flip = false
  HorizontalArea = 230400
  IfcData = attributes={"GlobalId": {"name": "GlobalId", "type": "IfcGloballyUniqueId", "is_enum": false, "enum_values": []}, "Description": {"... (+613 chars omitted),+1 more (map truncated)
  IfcType = 113
  Material = -> Material018
  MoveBase = false
  MoveWithHost = false
  PerimeterLength = 0
  Placement = pos=(361.882,1538,1900) rot=(0,0,1;0rad)
  PredefinedType = 0
  RidgeLength = 0
  Thickness = [50,50,50,50]
  VerticalArea = 99386.5
FEATURE [Part::FeaturePython] Wall626  label="Столб 002"  # Arch/BIM 166 (typed FeaturePython)
  Align = 2
  Area = 836000
  BlockHeight = 0
  BlockLength = 0
  CloneOf = -> Wall316
  CountBroken = 0
  CountEntire = 0
  Face = 0
  Height = 2200
  HorizontalArea = 144400
  IfcData = attributes={"GlobalId": {"name": "GlobalId", "type": "IfcGloballyUniqueId", "is_enum": false, "enum_values": []}, "Description": {"... (+533 chars omitted),+1 more (map truncated)
  IfcType = 166
  Joint = 0
  Length = 380
  MakeBlocks = false
  Material = -> Material003
  MoveBase = false
  MoveWithHost = false
  Normal = (0,0,0)
  OffsetFirst = 0
  OffsetSecond = 0
  PerimeterLength = 1520
  Placement = pos=(361.882,1538,-320) rot=(0,0,1;0rad)
  PredefinedType = 0
  VerticalArea = 3.344e+06
  Width = 380
FEATURE [Part::FeaturePython] Wall627  label="Столб 003"  # Arch/BIM 166 (typed FeaturePython)
  Align = 2
  Area = 836000
  BlockHeight = 0
  BlockLength = 0
  CloneOf = -> Wall316
  CountBroken = 0
  CountEntire = 0
  Face = 0
  Height = 2200
  HorizontalArea = 144400
  IfcData = attributes={"GlobalId": {"name": "GlobalId", "type": "IfcGloballyUniqueId", "is_enum": false, "enum_values": []}, "Description": {"... (+533 chars omitted),+1 more (map truncated)
  IfcType = 166
  Joint = 0
  Length = 380
  MakeBlocks = false
  Material = -> Material003
  MoveBase = false
  MoveWithHost = false
  Normal = (0,0,0)
  OffsetFirst = 0
  OffsetSecond = 0
  PerimeterLength = 1520
  Placement = pos=(-5236.99,1232.23,-320) rot=(0,0,1;0rad)
  PredefinedType = 0
  VerticalArea = 3.344e+06
  Width = 380
FEATURE [Part::FeaturePython] Roof040  label="Крышка столба 003"  # Arch/BIM 113 (typed FeaturePython)
  BorderLength = 0
  CloneOf = -> Roof018
  Face = 0
  Flip = false
  HorizontalArea = 230400
  IfcData = attributes={"GlobalId": {"name": "GlobalId", "type": "IfcGloballyUniqueId", "is_enum": false, "enum_values": []}, "Description": {"... (+613 chars omitted),+1 more (map truncated)
  IfcType = 113
  Material = -> Material018
  MoveBase = false
  MoveWithHost = false
  PerimeterLength = 0
  Placement = pos=(-5236.99,1232.23,1900) rot=(0,0,1;0rad)
  PredefinedType = 0
  RidgeLength = 0
  Thickness = [50,50,50,50]
  VerticalArea = 99386.5
FEATURE [Part::Part2DObjectPython] Wire1085  # Draft 2D object (typed FeaturePython)
  Area = 0
  ChamferSize = 0
  Closed = false
  End = (16773.9,-8230.23,0)
  FilletRadius = 0
  Length = 34934
  MakeFace = false
  Placement = pos=(-17500,-6600,0) rot=(0,0,1;0rad)
  Points = (5) [(0,0,0),(6349.64,-1849.27,0),(17618.1,149.315,0),(27200,149.315,0),(34273.9,-1630.23,0)]
  Start = (-17500,-6600,0)
  Subdivisions = 0
FEATURE [Part::FeaturePython] Wall320  label="Забор 002"  # Arch/BIM 166 (typed FeaturePython)
  Align = 0
  Area = 6.9868e+07
  Base = -> Wire1085
  BlockHeight = 2000
  BlockLength = 150
  CountBroken = 5
  CountEntire = 214
  Face = 0
  Height = 2000
  HorizontalArea = 0
  IfcData = attributes={"GlobalId": {"name": "GlobalId", "type": "IfcGloballyUniqueId", "is_enum": false, "enum_values": []}, "Description": {"... (+533 chars omitted),+1 more (map truncated)
  IfcType = 166
  Joint = 10
  Length = 34934
  MakeBlocks = true
  Material = -> Material010
  MoveBase = false
  MoveWithHost = false
  Normal = (0,0,0)
  OffsetFirst = 100
  OffsetSecond = 0
  PerimeterLength = 0
  Placement = pos=(0,0,-220) rot=(0,0,1;0rad)
  PredefinedType = 0
  VerticalArea = 0
  Width = 50
FEATURE [Part::Part2DObjectPython] Wire1086  # Draft 2D object (typed FeaturePython)
  Area = 0
  ChamferSize = 0
  Closed = false
  End = (22601.3,-7783.03,0)
  FilletRadius = 0
  Length = 10550.8
  MakeFace = false
  Placement = pos=(27001.9,-1339.67,0) rot=(0,0,1;0rad)
  Points = (4) [(0,0,0),(-3908.23,174.659,0),(-4040.62,-2787.88,0),(-4400.67,-6443.36,0)]
  Start = (27001.9,-1339.67,0)
  Subdivisions = 0
FEATURE [Part::FeaturePython] Wall321  label="Забор 001"  # Arch/BIM 166 (typed FeaturePython)
  Align = 0
  Area = 2.11016e+07
  Base = -> Wire1086
  BlockHeight = 2000
  BlockLength = 150
  CountBroken = 4
  CountEntire = 62
  Face = 0
  Height = 2000
  HorizontalArea = 0
  IfcData = attributes={"GlobalId": {"name": "GlobalId", "type": "IfcGloballyUniqueId", "is_enum": false, "enum_values": []}, "Description": {"... (+533 chars omitted),+1 more (map truncated)
  IfcType = 166
  Joint = 10
  Length = 10550.8
  MakeBlocks = true
  Material = -> Material010
  MoveBase = false
  MoveWithHost = false
  Normal = (0,0,0)
  OffsetFirst = 0
  OffsetSecond = 0
  PerimeterLength = 0
  Placement = pos=(0,0,-220) rot=(0,0,1;0rad)
  PredefinedType = 0
  VerticalArea = 0
  Width = 50
FEATURE [App::GeometryPython] BuildingPart067  label="Участок с ограждением"  # Arch/BIM 52 (typed FeaturePython)
  Area = 1.07598e+08
  Group = -> [BuildingPart108,Wall320,Wall321,Structure437,Roof040,Wall627,Wall626,Roof,Common104]
  Height = 0
  HeightPropagate = true
  IfcData = attributes={"GlobalId": {"name": "GlobalId", "type": "IfcGloballyUniqueId", "is_enum": false, "enum_values": []}, "Description": {"... (+484 chars omitted),+1 more (map truncated)
  IfcType = 52
  LevelOffset = 0
FEATURE [Part::Part2DObjectPython] Circle218  label="люк_контур 002"  # Draft 2D object (typed FeaturePython)
  FirstAngle = 0
  LastAngle = 0
  MakeFace = false
  Placement = pos=(32600,-4700,0) rot=(0,0,1;0rad)
  Radius = 350
FEATURE [Part::FeaturePython] Structure696  label="люк контур Д701"  # Arch/BIM 52 (typed FeaturePython)
  Base = -> Circle218
  FaceMaker = 0
  Height = 300
  HorizontalArea = 384845
  IfcData = complex_attributes={"OwnerHistory": {}, "IsNestedBy": {}, "IsDecomposedBy": {}, "IsDefinedBy": {}, "ObjectPlacement": {}, "Representation":... (+4 chars omitted)
  IfcType = 52
  Length = 0
  MoveBase = false
  MoveWithHost = false
  Nodes = (2) [(32600,-4700,0),(32600,-4700,-300)]
  NodesOffset = 0
  Normal = (0,0,-1)
  PerimeterLength = 2199.11
  VerticalArea = 659734
  Width = 150
FEATURE [Part::Part2DObjectPython] Circle219  # Draft 2D object (typed FeaturePython)
  FirstAngle = 0
  LastAngle = 0
  MakeFace = false
  Placement = pos=(32600,-5000,0) rot=(0,0,1;0rad)
  Radius = 750
FEATURE [Part::FeaturePython] Structure694  label="кольцо с днищем ДК-15.9 внутр.001"  # Arch/BIM 52 (typed FeaturePython)
  Base = -> Circle219
  FaceMaker = 0
  Height = 800
  HorizontalArea = 1.76715e+06
  IfcData = complex_attributes={"OwnerHistory": {}, "IsNestedBy": {}, "IsDecomposedBy": {}, "IsDefinedBy": {}, "ObjectPlacement": {}, "Representation":... (+4 chars omitted)
  IfcType = 52
  Length = 0
  MoveBase = false
  MoveWithHost = false
  Nodes = (2) [(32600,-2100,0),(32600,-2100,-800)]
  NodesOffset = 0
  Normal = (0,0,-1)
  PerimeterLength = 4712.39
  Placement = pos=(0,0,-300) rot=(0,0,1;0rad)
  VerticalArea = 3.76991e+06
  Width = 100
FEATURE [Part::Part2DObjectPython] Circle220  # Draft 2D object (typed FeaturePython)
  FirstAngle = 0
  LastAngle = 0
  MakeFace = false
  Placement = pos=(32600,-5000,0) rot=(0,0,1;0rad)
  Radius = 840
FEATURE [Part::FeaturePython] Structure693  label="крышка ПП 15.2 001"  # Arch/BIM 52 (typed FeaturePython)
  Base = -> Circle220
  FaceMaker = 0
  Height = 150
  HorizontalArea = 1.83186e+06
  IfcData = complex_attributes={"OwnerHistory": {}, "IsNestedBy": {}, "IsDecomposedBy": {}, "IsDefinedBy": {}, "ObjectPlacement": {}, "Representation":... (+4 chars omitted)
  IfcType = 52
  Length = 0
  MoveBase = false
  MoveWithHost = false
  Nodes = (2) [(32600,-2100,0),(32600,-2100,-100)]
  NodesOffset = 0
  Normal = (0,0,-1)
  PerimeterLength = 5277.88
  Placement = pos=(0,0,-150) rot=(0,0,1;0rad)
  Subtractions = -> [Structure696]
  VerticalArea = 1.12155e+06
  Width = 100
FEATURE [Part::FeaturePython] Structure695  label="кольцо с днищем ДК-15.9 габарит001"  # Arch/BIM 52 (typed FeaturePython)
  Base = -> Circle220
  FaceMaker = 0
  Height = 900
  HorizontalArea = 2.21671e+06
  IfcData = complex_attributes={"OwnerHistory": {}, "IsNestedBy": {}, "IsDecomposedBy": {}, "IsDefinedBy": {}, "ObjectPlacement": {}, "Representation":... (+4 chars omitted)
  IfcType = 52
  Length = 0
  MoveBase = false
  MoveWithHost = false
  Nodes = (2) [(32600,-2100,0),(32600,-2100,-900)]
  NodesOffset = 0
  Normal = (0,0,-1)
  PerimeterLength = 5277.88
  Placement = pos=(0,0,-300) rot=(0,0,1;0rad)
  Subtractions = -> [Structure694]
  VerticalArea = 8.52e+06
  Width = 100
FEATURE [Part::Feature] Structure695001  label="кольцо с днищем ДК-15.9 001"
  Placement = pos=(-15400,5213.03,-2300) rot=(0,0,1;0rad)
  shape: bbox 1680 x 1680 x 900 mm, 5 faces (baked)
FEATURE [Part::Feature] Structure695002  label="кольцо стеновое КС-15.9 001"
  Placement = pos=(-15400,5213.03,-1400) rot=(0,0,1;0rad)
  shape: bbox 1680 x 1680 x 900 mm, 4 faces (baked)
FEATURE [Part::Feature] Structure693001  label="крышка ПП-15.2 001"
  Placement = pos=(-10987,-16911.6,-1250) rot=(0,0,1;0.698132rad)
  shape: bbox 1680 x 1680 x 150 mm, 4 faces (baked)
FEATURE [Part::FeaturePython] Structure695004  label="кольцо сперекрытия ПК-15.9 внутр.002"  # Arch/BIM 52 (typed FeaturePython)
  Base = -> Circle219
  FaceMaker = 0
  Height = 800
  HorizontalArea = 1.76715e+06
  IfcData = complex_attributes={"OwnerHistory": {}, "IsNestedBy": {}, "IsDecomposedBy": {}, "IsDefinedBy": {}, "ObjectPlacement": {}, "Representation":... (+4 chars omitted)
  IfcType = 52
  Length = 0
  MoveBase = false
  MoveWithHost = false
  Nodes = (2) [(32600,-2100,0),(32600,-2100,-800)]
  NodesOffset = 0
  Normal = (0,0,-1)
  PerimeterLength = 4712.39
  Placement = pos=(0,0,-400) rot=(0,0,1;0rad)
  VerticalArea = 3.76991e+06
  Width = 100
FEATURE [Part::FeaturePython] Structure695005  label="люк контур Д702"  # Arch/BIM 52 (typed FeaturePython)
  Base = -> Circle218
  FaceMaker = 0
  Height = 300
  HorizontalArea = 384845
  IfcData = complex_attributes={"OwnerHistory": {}, "IsNestedBy": {}, "IsDecomposedBy": {}, "IsDefinedBy": {}, "ObjectPlacement": {}, "Representation":... (+4 chars omitted)
  IfcType = 52
  Length = 0
  MoveBase = false
  MoveWithHost = false
  Nodes = (2) [(32600,-4700,0),(32600,-4700,-300)]
  NodesOffset = 0
  Normal = (0,0,-1)
  PerimeterLength = 2199.11
  Placement = pos=(0,0,-100) rot=(0,0,1;0rad)
  VerticalArea = 659734
  Width = 150
FEATURE [Part::FeaturePython] Structure695003  label="кольцо перекрытия ПК-15.9 габарит002"  # Arch/BIM 52 (typed FeaturePython)
  Base = -> Circle220
  FaceMaker = 0
  Height = 900
  HorizontalArea = 1.83186e+06
  IfcData = complex_attributes={"OwnerHistory": {}, "IsNestedBy": {}, "IsDecomposedBy": {}, "IsDefinedBy": {}, "ObjectPlacement": {}, "Representation":... (+4 chars omitted)
  IfcType = 52
  Length = 0
  MoveBase = false
  MoveWithHost = false
  Nodes = (2) [(32600,-2100,0),(32600,-2100,-900)]
  NodesOffset = 0
  Normal = (0,0,-1)
  PerimeterLength = 5277.88
  Placement = pos=(0,0,-300) rot=(0,0,1;0rad)
  Subtractions = -> [Structure695004,Structure695005]
  VerticalArea = 8.73991e+06
  Width = 100
FEATURE [Part::Feature] Structure695003001  label="кольцо перекрытия ПК-15.9 001"
  Placement = pos=(45387,17337.7,-350) rot=(0,0,1;3.83972rad)
  shape: bbox 1680 x 1680 x 900 mm, 6 faces (baked)
FEATURE [Part::Feature] Structure695003002  label="кольцо с днищем ДК-15.9 002"
  Placement = pos=(-15350,6940,-2300) rot=(0,0,1;0rad)
  shape: bbox 1680 x 1680 x 900 mm, 5 faces (baked)
FEATURE [Part::Feature] Structure695003003  label="кольцо стеновое КС-15.9 002"
  Placement = pos=(-15350,6940,-1400) rot=(0,0,1;0rad)
  shape: bbox 1680 x 1680 x 900 mm, 4 faces (baked)
FEATURE [Part::Feature] Structure695003004  label="крышка ПП-15.2 002"
  Placement = pos=(-9337.21,-17576.1,-1250) rot=(0,0,1;0.785398rad)
  shape: bbox 1680 x 1680 x 150 mm, 4 faces (baked)
FEATURE [Part::Feature] Structure695003005  label="кольцо перекрытия ПК-15.9 002"
  Placement = pos=(43837.2,21456.1,-350) rot=(0,0,1;3.92699rad)
  shape: bbox 1680 x 1680 x 900 mm, 6 faces (baked)
FEATURE [Part::Feature] Structure044001  label="люк Д700 001"
  Placement = pos=(-7003.76,-19909.6,-200) rot=(0,0,1;0.785398rad)
  shape: bbox 700 x 700 x 150 mm, 3 faces (baked)
FEATURE [Part::Feature] Structure695003006  label="люк Д700 002"
  Placement = pos=(43651.5,19406,-200) rot=(0,0,1;3.83972rad)
  shape: bbox 700 x 700 x 150 mm, 3 faces (baked)
FEATURE [Part::Feature] Structure695003007001  label="П5-8/2 001"
  Placement = pos=(16721.1,783.728,-1930) rot=(0,0,-1;0.872665rad)
  shape: bbox 1011 x 1186 x 780 mm, 6 faces (baked)
FEATURE [Part::Feature] Structure695003007005  label="П5-8/2 с вырезом 002"
  Placement = pos=(17776.8,1413.21,-2710) rot=(0,0,1;2.35619rad)
  shape: bbox 1103 x 1103 x 780 mm, 10 faces (baked)
FEATURE [Part::Feature] Structure695003007006  label="П5-8/2 с вырезом 001"
  Placement = pos=(16721.1,783.728,-2710) rot=(0,0,-1;0.872665rad)
  shape: bbox 1011 x 1186 x 780 mm, 10 faces (baked)
FEATURE [Part::Feature] Structure695003007007  label="П5-8/2 002"
  Placement = pos=(17776.8,1413.21,-1930) rot=(0,0,1;2.35619rad)
  shape: bbox 1103 x 1103 x 780 mm, 6 faces (baked)
FEATURE [Part::Part2DObjectPython] Circle221  # Draft 2D object (typed FeaturePython)
  Area = 0
  FirstAngle = 0
  LastAngle = 0
  MakeFace = false
  Placement = pos=(16566.9,306.459,0) rot=(0,0,1;0rad)
  Radius = 80
FEATURE [Part::Part2DObjectPython] Line2241  # Draft 2D object (typed FeaturePython)
  Area = 0
  ChamferSize = 0
  Closed = true
  End = (16369,335.657,0)
  FilletRadius = 0
  Length = 9516.73
  MakeFace = false
  Placement = pos=(6954.23,1725.01,0) rot=(0,0,1;0rad)
  Points = (2) [(0,0,0),(9414.77,-1389.36,0)]
  Start = (6954.23,1725.01,0)
  Subdivisions = 0
FEATURE [Part::Part2DObjectPython] Circle222  # Draft 2D object (typed FeaturePython)
  Area = 0
  FirstAngle = 0
  LastAngle = 0
  MakeFace = false
  Placement = pos=(17200,213.025,0) rot=(0,0,1;0rad)
  Radius = 840
FEATURE [Part::Part2DObjectPython] Line2242  # Draft 2D object (typed FeaturePython)
  Area = 0
  ChamferSize = 0
  Closed = false
  End = (6954.23,1725.01,200)
  FilletRadius = 0
  Length = 200
  MakeFace = false
  Placement = pos=(6954.23,1725.01,0) rot=(0,0,1;0rad)
  Points = (2) [(0,0,0),(0,0,200)]
  Start = (6954.23,1725.01,0)
  Subdivisions = 0
FEATURE [Part::Part2DObjectPython] Line2243  # Draft 2D object (typed FeaturePython)
  Area = 0
  ChamferSize = 0
  Closed = false
  End = (16566.9,306.459,0)
  FilletRadius = 0
  Length = 200
  MakeFace = false
  Placement = pos=(16369,335.657,0) rot=(0,0,1;0rad)
  Points = (2) [(0,0,0),(197.857,-29.1982,0)]
  Start = (16369,335.657,0)
  Subdivisions = 0
FEATURE [Part::Part2DObjectPython] Line2245  # Draft 2D object (typed FeaturePython)
  Area = 0
  ChamferSize = 0
  Closed = false
  End = (17218.5,852.757,0)
  FilletRadius = 0
  Length = 200
  MakeFace = false
  Placement = pos=(17224.3,1052.67,0) rot=(0,0,1;0rad)
  Points = (2) [(0,0,0),(-5.78805,-199.916,0)]
  Start = (17224.3,1052.67,0)
  Subdivisions = 0
FEATURE [Part::Part2DObjectPython] Circle223  # Draft 2D object (typed FeaturePython)
  Area = 0
  FirstAngle = 0
  LastAngle = 0
  MakeFace = false
  Placement = pos=(6954.23,1725.01,0) rot=(0,0,1;0rad)
  Radius = 80
FEATURE [Part::Part2DObjectPython] Circle224  # Draft 2D object (typed FeaturePython)
  Area = 0
  FirstAngle = 0
  LastAngle = 0
  MakeFace = false
  Placement = pos=(17218.5,852.757,0) rot=(0,0,1;0rad)
  Radius = 80
FEATURE [Part::Part2DObjectPython] Circle225  # Draft 2D object (typed FeaturePython)
  Area = 0
  FirstAngle = 0
  LastAngle = 0
  MakeFace = false
  Placement = pos=(17250,1940,0) rot=(0,0,1;0rad)
  Radius = 840
FEATURE [Part::Part2DObjectPython] Line2246  # Draft 2D object (typed FeaturePython)
  Area = 0
  ChamferSize = 0
  Closed = false
  End = (17231.5,1300.27,0)
  FilletRadius = 0
  Length = 200
  MakeFace = false
  Placement = pos=(17225.7,1100.35,0) rot=(0,0,1;0rad)
  Points = (2) [(0,0,0),(5.78805,199.916,0)]
  Start = (17225.7,1100.35,0)
  Subdivisions = 0
FEATURE [Part::Part2DObjectPython] Line2247  # Draft 2D object (typed FeaturePython)
  Area = 0
  ChamferSize = 0
  Closed = false
  End = (17274.3,2779.65,0)
  FilletRadius = 0
  Length = 200
  MakeFace = false
  Placement = pos=(17268.5,2579.73,0) rot=(0,0,1;0rad)
  Points = (2) [(0,0,0),(5.78805,199.916,0)]
  Start = (17268.5,2579.73,0)
  Subdivisions = 0
FEATURE [Part::Part2DObjectPython] Circle226  # Draft 2D object (typed FeaturePython)
  Area = 0
  FirstAngle = 0
  LastAngle = 0
  MakeFace = false
  Placement = pos=(17231.5,1300.27,0) rot=(0,0,1;0rad)
  Radius = 80
FEATURE [Part::Part2DObjectPython] Circle227  # Draft 2D object (typed FeaturePython)
  Area = 0
  FirstAngle = 0
  LastAngle = 0
  MakeFace = false
  Placement = pos=(17268.5,2579.73,0) rot=(0,0,1;0rad)
  Radius = 80
FEATURE [Part::Part2DObjectPython] Line2248  # Draft 2D object (typed FeaturePython)
  Area = 0
  ChamferSize = 0
  Closed = false
  End = (16566.9,306.459,0)
  FilletRadius = 0
  Length = 9718.79
  MakeFace = false
  Placement = pos=(6954.23,1725.01,200) rot=(0,0,1;0rad)
  Points = (2) [(0,0,0),(9612.63,-1418.55,-200)]
  Start = (6954.23,1725.01,200)
  Subdivisions = 0
FEATURE [Part::Part2DObjectPython] Line2249  # Draft 2D object (typed FeaturePython)
  Area = 0
  ChamferSize = 0
  Closed = false
  End = (16566.9,306.459,600)
  FilletRadius = 0
  Length = 600
  MakeFace = false
  Placement = pos=(16566.9,306.459,0) rot=(0,0,1;0rad)
  Points = (2) [(0,0,0),(0,0,600)]
  Start = (16566.9,306.459,0)
  Subdivisions = 0
FEATURE [Part::FeaturePython] Pipe022  label="Наружная канализация D160 001"  # Arch/BIM 98 (typed FeaturePython)
  Base = -> Line2249
  Diameter = 160
  HorizontalArea = 0
  IfcData = attributes={"GlobalId": {"name": "GlobalId", "type": "IfcGloballyUniqueId", "is_enum": false, "enum_values": []}, "Description": {"... (+487 chars omitted),+1 more (map truncated)
  IfcType = 98
  Length = 600
  MoveBase = false
  MoveWithHost = false
  OffsetEnd = 0
  OffsetStart = 0
  PerimeterLength = 0
  Placement = pos=(0,0,-1800) rot=(0,0,1;0rad)
  PredefinedType = 0
  VerticalArea = 0
  WallThickness = 0
FEATURE [Part::Part2DObjectPython] Line2250  # Draft 2D object (typed FeaturePython)
  Area = 0
  ChamferSize = 0
  Closed = true
  End = (6954.23,1725.01,-1320)
  FilletRadius = 0
  Length = 1320
  MakeFace = false
  Placement = pos=(6954.23,1725.01,0) rot=(0,0,-1;0rad)
  Points = (2) [(0,0,0),(-2.14844e-05,1.07422e-05,-1320)]
  Start = (6954.23,1725.01,0)
  Subdivisions = 0
FEATURE [Part::Part2DObjectPython] Line2251  # Draft 2D object (typed FeaturePython)
  Area = 0
  ChamferSize = 0
  Closed = false
  End = (17274.3,2779.65,0)
  FilletRadius = 0
  Length = 840
  MakeFace = false
  Placement = pos=(17250,1940,0) rot=(0,0,1;0rad)
  Points = (2) [(0,0,0),(24.3098,839.648,0)]
  Start = (17250,1940,0)
  Subdivisions = 0
FEATURE [Part::Part2DObjectPython] Line2252  # Draft 2D object (typed FeaturePython)
  Area = 0
  ChamferSize = 0
  Closed = false
  End = (17332.2,4778.81,0)
  FilletRadius = 0
  Length = 2000
  MakeFace = false
  Placement = pos=(17274.3,2779.65,0) rot=(0,0,1;0rad)
  Points = (2) [(0,0,0),(57.8805,1999.16,0)]
  Start = (17274.3,2779.65,0)
  Subdivisions = 0
FEATURE [Part::Part2DObjectPython] Line2253  # Draft 2D object (typed FeaturePython)
  Area = 0
  ChamferSize = 0
  Closed = false
  End = (17332.2,4778.81,-20)
  FilletRadius = 0
  Length = 20
  MakeFace = false
  Placement = pos=(17332.2,4778.81,0) rot=(0,0,1;0rad)
  Points = (2) [(0,0,0),(0,0,-20)]
  Start = (17332.2,4778.81,0)
  Subdivisions = 0
FEATURE [Part::Part2DObjectPython] Line2254  # Draft 2D object (typed FeaturePython)
  Area = 0
  ChamferSize = 0
  Closed = false
  End = (17326.4,4578.89,-20)
  FilletRadius = 0
  Length = 2000.1
  MakeFace = false
  Placement = pos=(17268.5,2579.73,0) rot=(0,0,1;0rad)
  Points = (2) [(0,0,0),(57.8805,1999.16,-20)]
  Start = (17268.5,2579.73,0)
  Subdivisions = 0
FEATURE [Part::FeaturePython] Pipe024  label="Наружная канализация D160 025"  # Arch/BIM 98 (typed FeaturePython)
  Base = -> Line2254
  Diameter = 160
  HorizontalArea = 0
  IfcData = attributes={"GlobalId": {"name": "GlobalId", "type": "IfcGloballyUniqueId", "is_enum": false, "enum_values": []}, "Description": {"... (+487 chars omitted),+1 more (map truncated)
  IfcType = 98
  Length = 2000.1
  MoveBase = false
  MoveWithHost = false
  OffsetEnd = 0
  OffsetStart = 0
  PerimeterLength = 0
  Placement = pos=(0,0,-1710) rot=(0,0,1;0rad)
  PredefinedType = 0
  VerticalArea = 0
  WallThickness = 0
FEATURE [Part::Part2DObjectPython] Line2255  # Draft 2D object (typed FeaturePython)
  Area = 0
  ChamferSize = 0
  Closed = false
  End = (17268.5,2579.73,800)
  FilletRadius = 0
  Length = 800
  MakeFace = false
  Placement = pos=(17268.5,2579.73,0) rot=(0,0,1;0rad)
  Points = (2) [(0,0,0),(0,0,800)]
  Start = (17268.5,2579.73,0)
  Subdivisions = 0
FEATURE [Part::FeaturePython] Pipe025  label="Наружная канализация D160 026"  # Arch/BIM 98 (typed FeaturePython)
  Base = -> Line2255
  Diameter = 160
  HorizontalArea = 0
  IfcData = attributes={"GlobalId": {"name": "GlobalId", "type": "IfcGloballyUniqueId", "is_enum": false, "enum_values": []}, "Description": {"... (+487 chars omitted),+1 more (map truncated)
  IfcType = 98
  Length = 800
  MoveBase = false
  MoveWithHost = false
  OffsetEnd = 0
  OffsetStart = 0
  PerimeterLength = 0
  Placement = pos=(0,0,-2000) rot=(0,0,1;0rad)
  PredefinedType = 0
  VerticalArea = 0
  WallThickness = 0
FEATURE [Part::Part2DObjectPython] Line2256  # Draft 2D object (typed FeaturePython)
  Area = 0
  ChamferSize = 0
  Closed = false
  End = (17231.5,1300.27,-10)
  FilletRadius = 0
  Length = 447.809
  MakeFace = false
  Placement = pos=(17218.5,852.757,0) rot=(0,0,1;0rad)
  Points = (2) [(0,0,0),(12.96,447.51,-10)]
  Start = (17218.5,852.757,0)
  Subdivisions = 0
FEATURE [Part::FeaturePython] Pipe026  label="Наружная канализация D160 027"  # Arch/BIM 98 (typed FeaturePython)
  Base = -> Line2256
  Diameter = 160
  HorizontalArea = 0
  IfcData = attributes={"GlobalId": {"name": "GlobalId", "type": "IfcGloballyUniqueId", "is_enum": false, "enum_values": []}, "Description": {"... (+487 chars omitted),+1 more (map truncated)
  IfcType = 98
  Length = 447.809
  MoveBase = false
  MoveWithHost = false
  OffsetEnd = 0
  OffsetStart = 0
  PerimeterLength = 0
  Placement = pos=(0,0,-1620) rot=(0,0,1;0rad)
  PredefinedType = 0
  VerticalArea = 0
  WallThickness = 0
FEATURE [Part::Part2DObjectPython] Line2257  # Draft 2D object (typed FeaturePython)
  Area = 0
  ChamferSize = 0
  Closed = false
  End = (17218.5,852.757,800)
  FilletRadius = 0
  Length = 800
  MakeFace = false
  Placement = pos=(17218.5,852.757,0) rot=(0,0,1;0rad)
  Points = (2) [(0,0,0),(0,0,800)]
  Start = (17218.5,852.757,0)
  Subdivisions = 0
FEATURE [Part::FeaturePython] Pipe027  label="Наружная канализация D160 028"  # Arch/BIM 98 (typed FeaturePython)
  Base = -> Line2257
  Diameter = 160
  HorizontalArea = 0
  IfcData = attributes={"GlobalId": {"name": "GlobalId", "type": "IfcGloballyUniqueId", "is_enum": false, "enum_values": []}, "Description": {"... (+487 chars omitted),+1 more (map truncated)
  IfcType = 98
  Length = 800
  MoveBase = false
  MoveWithHost = false
  OffsetEnd = 0
  OffsetStart = 0
  PerimeterLength = 0
  Placement = pos=(0,0,-2000) rot=(0,0,1;0rad)
  PredefinedType = 0
  VerticalArea = 0
  WallThickness = 0
FEATURE [Part::Part2DObjectPython] Line2258  # Draft 2D object (typed FeaturePython)
  Area = 0
  ChamferSize = 0
  Closed = false
  End = (17268.5,2579.73,800)
  FilletRadius = 0
  Length = 800
  MakeFace = false
  Placement = pos=(17268.5,2579.73,0) rot=(0,0,1;0rad)
  Points = (2) [(0,0,0),(0,0,800)]
  Start = (17268.5,2579.73,0)
  Subdivisions = 0
FEATURE [Part::FeaturePython] Pipe028  label="Наружная канализация D160 029"  # Arch/BIM 98 (typed FeaturePython)
  Base = -> Line2258
  Diameter = 160
  HorizontalArea = 0
  IfcData = attributes={"GlobalId": {"name": "GlobalId", "type": "IfcGloballyUniqueId", "is_enum": false, "enum_values": []}, "Description": {"... (+487 chars omitted),+1 more (map truncated)
  IfcType = 98
  Length = 800
  MoveBase = false
  MoveWithHost = false
  OffsetEnd = 0
  OffsetStart = 0
  PerimeterLength = 0
  Placement = pos=(-37.0435,-1279.46,-2000) rot=(0,0,1;0rad)
  PredefinedType = 0
  VerticalArea = 0
  WallThickness = 0
FEATURE [Part::Part2DObjectPython] Line2259  # Draft 2D object (typed FeaturePython)
  Area = 0
  ChamferSize = 0
  Closed = false
  End = (0,4600,-200)
  FilletRadius = 0
  Length = 1800
  MakeFace = false
  Placement = pos=(0,4600,-2000) rot=(0.57735,0.57735,0.57735;2.0944rad)
  Points = (2) [(0,0,0),(0,1800,0)]
  Start = (0,4600,-2000)
  Subdivisions = 0
FEATURE [Part::FeaturePython] Pipe029  label="Наружная канализация D160 030"  # Arch/BIM 98 (typed FeaturePython)
  Base = -> Line2256
  Diameter = 160
  HorizontalArea = 0
  IfcData = attributes={"GlobalId": {"name": "GlobalId", "type": "IfcGloballyUniqueId", "is_enum": false, "enum_values": []}, "Description": {"... (+487 chars omitted),+1 more (map truncated)
  IfcType = 98
  Length = 447.809
  MoveBase = false
  MoveWithHost = false
  OffsetEnd = 0
  OffsetStart = 0
  PerimeterLength = 0
  Placement = pos=(0,0,-550) rot=(0,0,1;0rad)
  PredefinedType = 0
  VerticalArea = 0
  WallThickness = 0
FEATURE [Part::Part2DObjectPython] Line2260  # Draft 2D object (typed FeaturePython)
  Area = 0
  ChamferSize = 0
  Closed = false
  End = (17268.5,2579.73,500)
  FilletRadius = 0
  Length = 500
  MakeFace = false
  Placement = pos=(17268.5,2579.73,0) rot=(0,0,1;0rad)
  Points = (2) [(0,0,0),(0,0,500)]
  Start = (17268.5,2579.73,0)
  Subdivisions = 0
FEATURE [Part::FeaturePython] Pipe030  label="Наружная канализация D160 031"  # Arch/BIM 98 (typed FeaturePython)
  Base = -> Line2260
  Diameter = 160
  HorizontalArea = 0
  IfcData = attributes={"GlobalId": {"name": "GlobalId", "type": "IfcGloballyUniqueId", "is_enum": false, "enum_values": []}, "Description": {"... (+487 chars omitted),+1 more (map truncated)
  IfcType = 98
  Length = 500
  MoveBase = false
  MoveWithHost = false
  OffsetEnd = 0
  OffsetStart = 0
  PerimeterLength = 0
  Placement = pos=(0,0,-500) rot=(0,0,1;0rad)
  PredefinedType = 0
  VerticalArea = 0
  WallThickness = 0
FEATURE [App::GeometryPython] BuildingPart144  label="Наружная канализация"  # Arch/BIM 172 (typed FeaturePython)
  Area = 0
  Height = 0
  HeightPropagate = true
  IfcData = attributes={"GlobalId": {"name": "GlobalId", "type": "IfcGloballyUniqueId", "is_enum": false, "enum_values": []}, "Description": {"... (+484 chars omitted),+1 more (map truncated)
  IfcType = 172
  LevelOffset = 0
  Placement = pos=(0,0,0) rot=(0.57735,0.57735,0.57735;2.0944rad)
  PredefinedType = 0
FEATURE [Part::Part2DObjectPython] Wire1087  # Draft 2D object (typed FeaturePython)
  Area = 0
  ChamferSize = 200
  Closed = false
  End = (6954.23,1725.01,0)
  FilletRadius = 0
  Length = 10958.8
  MakeFace = true
  Placement = pos=(16566.9,306.459,-1520) rot=(0.57735,0.57735,0.57735;2.0944rad)
  Points = (3) [(0,0,0),(1418.55,200,-9612.63),(1418.55,1520,-9612.63)]
  Start = (16566.9,306.459,-1520)
  Subdivisions = 0
FEATURE [Part::FeaturePython] Pipe031  label="Наружная канализация D160 032"  # Arch/BIM 98 (typed FeaturePython)
  Base = -> Wire1087
  Diameter = 160
  HorizontalArea = 0
  IfcData = attributes={"GlobalId": {"name": "GlobalId", "type": "IfcGloballyUniqueId", "is_enum": false, "enum_values": []}, "Description": {"... (+487 chars omitted),+1 more (map truncated)
  IfcType = 98
  Length = 10958.8
  MoveBase = false
  MoveWithHost = false
  OffsetEnd = 0
  OffsetStart = 0
  PerimeterLength = 0
  PredefinedType = 0
  VerticalArea = 0
  WallThickness = 0
FEATURE [Part::Part2DObjectPython] Line2261  # Draft 2D object (typed FeaturePython)
  Area = 0
  ChamferSize = 0
  Closed = false
  End = (7940,525,0)
  FilletRadius = 0
  Length = 1552.99
  MakeFace = true
  Placement = pos=(6954.23,1725.01,0) rot=(0,0,1;0rad)
  Points = (2) [(0,0,0),(985.77,-1200.01,0)]
  Start = (6954.23,1725.01,0)
  Subdivisions = 0
FEATURE [Part::Part2DObjectPython] Line2262  # Draft 2D object (typed FeaturePython)
  Area = 0
  ChamferSize = 0
  Closed = false
  End = (6755,5055,0)
  FilletRadius = 0
  Length = 3335.94
  MakeFace = true
  Placement = pos=(6954.23,1725.01,0) rot=(0,0,1;0rad)
  Points = (2) [(0,0,0),(-199.23,3329.99,0)]
  Start = (6954.23,1725.01,0)
  Subdivisions = 0
FEATURE [Part::Part2DObjectPython] Line2263  # Draft 2D object (typed FeaturePython)
  Area = 0
  ChamferSize = 0
  Closed = false
  End = (7940,525,30)
  FilletRadius = 0
  Length = 30
  MakeFace = true
  Placement = pos=(7940,525,0) rot=(0,0,1;0rad)
  Points = (2) [(0,0,0),(0,0,30)]
  Start = (7940,525,0)
  Subdivisions = 0
FEATURE [Part::Part2DObjectPython] Line2264  # Draft 2D object (typed FeaturePython)
  Area = 0
  ChamferSize = 0
  Closed = false
  End = (6755,5055,70)
  FilletRadius = 0
  Length = 70
  MakeFace = true
  Placement = pos=(6755,5055,0) rot=(0,0,1;0rad)
  Points = (2) [(0,0,0),(0,0,70)]
  Start = (6755,5055,0)
  Subdivisions = 0
FEATURE [Part::Part2DObjectPython] Line2265  # Draft 2D object (typed FeaturePython)
  Area = 0
  ChamferSize = 0
  Closed = false
  End = (6755,5055,900)
  FilletRadius = 0
  Length = 900
  MakeFace = true
  Placement = pos=(6755,5055,0) rot=(0,0,1;0rad)
  Points = (2) [(0,0,0),(0,0,900)]
  Start = (6755,5055,0)
  Subdivisions = 0
FEATURE [Part::Part2DObjectPython] Line2266  # Draft 2D object (typed FeaturePython)
  Area = 0
  ChamferSize = 0
  Closed = false
  End = (7940,525,700)
  FilletRadius = 0
  Length = 700
  MakeFace = true
  Placement = pos=(7940,525,0) rot=(0,0,1;0rad)
  Points = (2) [(0,0,0),(0,0,700)]
  Start = (7940,525,0)
  Subdivisions = 0
FEATURE [App::DocumentObjectGroup] Group138  label="План канализации"
  Group = -> [Circle221,Line2241,Circle222,Line2242,Line2243,Line2245,Circle223,Circle224,Circle225,Line2246,Line2247,Circle226,Circle227,Line2251,Line2252,Line2253,Line2259,Line2248,Line2250,Line2261,Line2262,Line2263,Line2264,Line2265,Line2266]
FEATURE [Part::Part2DObjectPython] Wire1088  # Draft 2D object (typed FeaturePython)
  Area = 0
  ChamferSize = 150
  Closed = false
  End = (7940,525,700)
  FilletRadius = 0
  Length = 2163.16
  MakeFace = true
  Placement = pos=(6954.23,1725.01,0) rot=(0,0,1;0rad)
  Points = (3) [(0,0,0),(985.77,-1200.01,30),(985.77,-1200.01,700)]
  Start = (6954.23,1725.01,0)
  Subdivisions = 0
FEATURE [Part::Part2DObjectPython] Wire1089  # Draft 2D object (typed FeaturePython)
  Area = 0
  ChamferSize = 150
  Closed = false
  End = (6755,5055,900)
  FilletRadius = 0
  Length = 4106.74
  MakeFace = true
  Placement = pos=(6954.23,1725.01,0) rot=(0,0,1;0rad)
  Points = (3) [(0,0,0),(-199.23,3329.99,70),(-199.23,3329.99,900)]
  Start = (6954.23,1725.01,0)
  Subdivisions = 0
FEATURE [Part::FeaturePython] Pipe  label="Наружная канализация D110 002"  # Arch/BIM 98 (typed FeaturePython)
  Base = -> Wire1088
  Diameter = 110
  HorizontalArea = 0
  IfcData = attributes={"GlobalId": {"name": "GlobalId", "type": "IfcGloballyUniqueId", "is_enum": false, "enum_values": []}, "Description": {"... (+487 chars omitted),+1 more (map truncated)
  IfcType = 98
  Length = 2163.16
  MoveBase = false
  MoveWithHost = false
  OffsetEnd = 0
  OffsetStart = 0
  PerimeterLength = 0
  Placement = pos=(0,4.55e-13,-700) rot=(0,0,1;0rad)
  PredefinedType = 0
  VerticalArea = 0
  WallThickness = 0
FEATURE [Part::FeaturePython] Pipe032  label="Наружная канализация D110 001"  # Arch/BIM 98 (typed FeaturePython)
  Base = -> Wire1089
  Diameter = 110
  HorizontalArea = 0
  IfcData = attributes={"GlobalId": {"name": "GlobalId", "type": "IfcGloballyUniqueId", "is_enum": false, "enum_values": []}, "Description": {"... (+487 chars omitted),+1 more (map truncated)
  IfcType = 98
  Length = 4106.74
  MoveBase = false
  MoveWithHost = false
  OffsetEnd = 0
  OffsetStart = 0
  PerimeterLength = 0
  Placement = pos=(0,0,-900) rot=(0,0,1;0rad)
  PredefinedType = 0
  VerticalArea = 0
  WallThickness = 0
FEATURE [Part::Compound] Compound006042003  label="Наружная канализация и переливы 001"
  Links = -> [Pipe022,Pipe024,Pipe025,Pipe026,Pipe027,Pipe028,Pipe029,Pipe030,Pipe031,Pipe,Pipe032]
FEATURE [Part::Compound] Compound006042004  label="ЛОС из колец Д150"
  Links = -> [Structure695001,Structure695002,Structure693001,Structure695003001,Structure695003002,Structure695003003,Structure695003004,Structure695003005,Structure044001,Structure695003006,Structure695003007001,Structure695003007005,Structure695003007006,Structure695003007007,BuildingPart144]
FEATURE [Part::Cut] Cut105003022  label="ЛОС из колец Д150 001"
  Base = -> Compound006042004
  Tool = -> Compound006042003
FEATURE [App::GeometryPython] BuildingPart143  label="ЛОС 4 камеры из колец D150"  # Arch/BIM 172 (typed FeaturePython)
  Area = 0
  Group = -> [Cut105003022,Compound006042003]
  Height = 0
  HeightPropagate = true
  IfcData = attributes={"GlobalId": {"name": "GlobalId", "type": "IfcGloballyUniqueId", "is_enum": false, "enum_values": []}, "Description": {"... (+484 chars omitted),+1 more (map truncated)
  IfcType = 172
  LevelOffset = 0
  PredefinedType = 0
FEATURE [TechDraw::DrawViewImage] Image
  Height = 100
  ImageFile = <userpath>/Desktop/project_pages/90m2_plans/f1.png
  LockPosition = false
  Rotation = 0
  ScaleType = 2
  Width = 100
  X = 145.028
  Y = 145.472
FEATURE [TechDraw::DrawViewImage] Image001
  Height = 100
  ImageFile = <userpath>/Desktop/project_pages/90m2_plans/f2.png
  LockPosition = false
  Rotation = 0
  ScaleType = 2
  Width = 100
  X = 305.499
  Y = 146.082
FEATURE [TechDraw::DrawPage] Page004  label="Титульный лист"
  KeepUpdated = false
  NextBalloonIndex = 1
  ProjectionType = 0
  Template = -> Template004
  Views = -> [Annotation032,Annotation033,Annotation034,Annotation035,Image,Image001]
FEATURE [TechDraw::DrawViewAnnotation] Annotation039
  Font = osifont
  LineSpace = 80
  LockPosition = false
  MaxWidth = -1
  Rotation = 0
  ScaleType = 0
  Text = \u0420\u0430\u0441\u043a\u043b\u0430\u0434\u043a\u0430 \u043f\u043b\u0438\u0442 \u041f\u041d\u041e (160\u043c\u043c)
  TextSize = 6
  TextStyle = 0
  X = 215.783
  Y = 262.643
FEATURE [TechDraw::DrawViewAnnotation] Annotation040
  Font = osifont
  LineSpace = 80
  LockPosition = false
  MaxWidth = -1
  Rotation = 0
  ScaleType = 0
  Text = \u041a\u043b\u0430\u0434\u043e\u0447\u043d\u044b\u0439 \u043f\u043b\u0430\u043d 1-\u0433\u043e \u044d\u0442\u0430\u0436\u0430
  TextSize = 6
  TextStyle = 0
  X = 141.288
  Y = 22.9779
FEATURE [Part::Part2DObjectPython] ShapeString255  # Draft 2D object (typed FeaturePython)
  FontFile = <path>
  Placement = pos=(4416.16,5139.62,0) rot=(0,0,1;1.5708rad)
  Size = 130
  String = ПНО 55-10 
  Tracking = 0
FEATURE [Part::Part2DObjectPython] ShapeString257  # Draft 2D object (typed FeaturePython)
  FontFile = <path>
  Placement = pos=(9900,5386.25,0) rot=(0,0,1;1.5708rad)
  Size = 130
  String = ПНО 55-12
  Tracking = 0
FEATURE [Part::Part2DObjectPython] ShapeString258  # Draft 2D object (typed FeaturePython)
  FontFile = <path>
  Placement = pos=(5338.7,5139.62,0) rot=(0,0,1;1.5708rad)
  Size = 130
  String = ПНО 55-10 
  Tracking = 0
FEATURE [Part::Part2DObjectPython] ShapeString259  # Draft 2D object (typed FeaturePython)
  FontFile = <path>
  Placement = pos=(8938.7,5386.25,0) rot=(0,0,1;1.5708rad)
  Size = 130
  String = ПНО 55-12
  Tracking = 0
FEATURE [Part::Part2DObjectPython] ShapeString260  # Draft 2D object (typed FeaturePython)
  FontFile = <path>
  Placement = pos=(7838.7,5386.25,0) rot=(0,0,1;1.5708rad)
  Size = 130
  String = ПНО 55-12
  Tracking = 0
FEATURE [Part::Part2DObjectPython] ShapeString262  # Draft 2D object (typed FeaturePython)
  FontFile = <path>
  Placement = pos=(9080.83,951.82,0) rot=(0,0,1;1.5708rad)
  Size = 130
  String = ПНО 33-12
  Tracking = 0
FEATURE [Part::Part2DObjectPython] ShapeString264  # Draft 2D object (typed FeaturePython)
  FontFile = <path>
  Placement = pos=(5453.67,924.163,0) rot=(0,0,1;1.5708rad)
  Size = 130
  String = ПНО 33-12
  Tracking = 0
FEATURE [Part::Part2DObjectPython] ShapeString265  # Draft 2D object (typed FeaturePython)
  FontFile = <path>
  Placement = pos=(6643.61,1033.82,0) rot=(0,0,1;1.5708rad)
  Size = 130
  String = ПНО 33-12
  Tracking = 0
FEATURE [Part::Part2DObjectPython] ShapeString266  # Draft 2D object (typed FeaturePython)
  FontFile = <path>
  Placement = pos=(7913.2,895.292,0) rot=(0,0,1;1.5708rad)
  Size = 130
  String = ПНО 33-12
  Tracking = 0
FEATURE [Part::Part2DObjectPython] ShapeString267  # Draft 2D object (typed FeaturePython)
  FontFile = <path>
  Placement = pos=(4372.11,931.45,0) rot=(0,0,1;1.5708rad)
  Size = 130
  String = ПНО 33-10
  Tracking = 0
FEATURE [Part::Part2DObjectPython] ShapeString268  # Draft 2D object (typed FeaturePython)
  FontFile = <path>
  Placement = pos=(10174.2,976.605,0) rot=(0,0,1;1.5708rad)
  Size = 130
  String = ПНО 33-10
  Tracking = 0
FEATURE [Part::Part2DObjectPython] ShapeString269  # Draft 2D object (typed FeaturePython)
  FontFile = <path>
  Placement = pos=(1418.88,7741.21,0) rot=(0,0,1;0rad)
  Size = 130
  String = ПНО 40-12
  Tracking = 0
FEATURE [Part::Part2DObjectPython] ShapeString270  # Draft 2D object (typed FeaturePython)
  FontFile = <path>
  Placement = pos=(1418.88,6536.21,0) rot=(0,0,1;0rad)
  Size = 130
  String = ПНО 40-12
  Tracking = 0
FEATURE [Part::Part2DObjectPython] ShapeString271  # Draft 2D object (typed FeaturePython)
  FontFile = <path>
  Placement = pos=(1418.88,5331.71,0) rot=(0,0,1;0rad)
  Size = 130
  String = ПНО 40-12
  Tracking = 0
FEATURE [Part::Part2DObjectPython] ShapeString272  # Draft 2D object (typed FeaturePython)
  FontFile = <path>
  Placement = pos=(1418.88,4126.71,0) rot=(0,0,1;0rad)
  Size = 130
  String = ПНО 40-12
  Tracking = 0
FEATURE [Part::Part2DObjectPython] ShapeString273  # Draft 2D object (typed FeaturePython)
  FontFile = <path>
  Placement = pos=(1418.88,2921.71,0) rot=(0,0,1;0rad)
  Size = 130
  String = ПНО 40-12
  Tracking = 0
FEATURE [Part::Part2DObjectPython] ShapeString274  # Draft 2D object (typed FeaturePython)
  FontFile = <path>
  Placement = pos=(1418.88,1716.71,0) rot=(0,0,1;0rad)
  Size = 130
  String = ПНО 40-12
  Tracking = 0
FEATURE [Part::Part2DObjectPython] ShapeString275  # Draft 2D object (typed FeaturePython)
  FontFile = <path>
  Placement = pos=(1418.88,511.707,0) rot=(0,0,1;0rad)
  Size = 130
  String = ПНО 40-12
  Tracking = 0
FEATURE [Part::Part2DObjectPython] ShapeString276  # Draft 2D object (typed FeaturePython)
  FontFile = <path>
  Placement = pos=(6021.58,3624.02,0) rot=(0,0,1;0rad)
  Size = 130
  String = Монолитн.
  Tracking = 0
FEATURE [Part::Part2DObjectPython] Circle228  # Draft 2D object (typed FeaturePython)
  Area = 0
  FirstAngle = 0
  LastAngle = 0
  MakeFace = false
  Placement = pos=(4711.14,6652.1,0) rot=(0,0,1;0rad)
  Radius = 200
FEATURE [Part::Part2DObjectPython] ShapeString277  # Draft 2D object (typed FeaturePython)
  FontFile = <path>
  Placement = pos=(4617.79,6551.71,0) rot=(0,0,1;0rad)
  Size = 250
  String = 6
  Tracking = 0
FEATURE [Part::FeaturePython] Component241043  label="открывание двери 001"  # Arch/BIM 0 (typed FeaturePython)
  Base = -> Arc162
  HorizontalArea = 0
  IfcData = attributes={"GlobalId": {"name": "GlobalId", "type": "IfcGloballyUniqueId", "is_enum": false, "enum_values": []}, "Description": {"... (+538 chars omitted),+1 more (map truncated)
  IfcType = 0
  MoveBase = false
  MoveWithHost = false
  PerimeterLength = 0
  Placement = pos=(3535,4355,0) rot=(0,0,-1;1.5708rad)
  PredefinedType = 0
  VerticalArea = 0
FEATURE [Part::FeaturePython] Component241044  label="открывание двери 028"  # Arch/BIM 0 (typed FeaturePython)
  Base = -> Line2126
  HorizontalArea = 0
  IfcData = attributes={"GlobalId": {"name": "GlobalId", "type": "IfcGloballyUniqueId", "is_enum": false, "enum_values": []}, "Description": {"... (+538 chars omitted),+1 more (map truncated)
  IfcType = 0
  MoveBase = false
  MoveWithHost = false
  PerimeterLength = 0
  Placement = pos=(2735,4355,0) rot=(0,0,1;0rad)
  PredefinedType = 0
  VerticalArea = 0
FEATURE [Part::FeaturePython] Component241045  label="открывание двери 029"  # Arch/BIM 0 (typed FeaturePython)
  Base = -> Line2127
  HorizontalArea = 0
  IfcData = attributes={"GlobalId": {"name": "GlobalId", "type": "IfcGloballyUniqueId", "is_enum": false, "enum_values": []}, "Description": {"... (+538 chars omitted),+1 more (map truncated)
  IfcType = 0
  MoveBase = false
  MoveWithHost = false
  PerimeterLength = 0
  Placement = pos=(2735,4015,0) rot=(0,0,1;0rad)
  PredefinedType = 0
  VerticalArea = 0
FEATURE [Part::FeaturePython] Component241046  label="открывание двери 030"  # Arch/BIM 0 (typed FeaturePython)
  Base = -> Arc163
  HorizontalArea = 0
  IfcData = attributes={"GlobalId": {"name": "GlobalId", "type": "IfcGloballyUniqueId", "is_enum": false, "enum_values": []}, "Description": {"... (+538 chars omitted),+1 more (map truncated)
  IfcType = 0
  MoveBase = false
  MoveWithHost = false
  PerimeterLength = 0
  Placement = pos=(3535,4015,0) rot=(0,0,1;0rad)
  PredefinedType = 0
  VerticalArea = 0
FEATURE [Part::FeaturePython] Component241049  label="открывание двери 033"  # Arch/BIM 0 (typed FeaturePython)
  Base = -> Line2128
  HorizontalArea = 0
  IfcData = attributes={"GlobalId": {"name": "GlobalId", "type": "IfcGloballyUniqueId", "is_enum": false, "enum_values": []}, "Description": {"... (+538 chars omitted),+1 more (map truncated)
  IfcType = 0
  MoveBase = false
  MoveWithHost = false
  PerimeterLength = 0
  Placement = pos=(7035,3135,0) rot=(0,0,1;0rad)
  PredefinedType = 0
  VerticalArea = 0
FEATURE [Part::FeaturePython] Component241050  label="открывание двери 034"  # Arch/BIM 0 (typed FeaturePython)
  Base = -> Arc164
  HorizontalArea = 0
  IfcData = attributes={"GlobalId": {"name": "GlobalId", "type": "IfcGloballyUniqueId", "is_enum": false, "enum_values": []}, "Description": {"... (+538 chars omitted),+1 more (map truncated)
  IfcType = 0
  MoveBase = false
  MoveWithHost = false
  PerimeterLength = 0
  Placement = pos=(7035,3135,0) rot=(0,0,1;3.14159rad)
  PredefinedType = 0
  VerticalArea = 0
FEATURE [Part::FeaturePython] Component241051  label="открывание двери 035"  # Arch/BIM 0 (typed FeaturePython)
  Base = -> Arc166
  HorizontalArea = 0
  IfcData = attributes={"GlobalId": {"name": "GlobalId", "type": "IfcGloballyUniqueId", "is_enum": false, "enum_values": []}, "Description": {"... (+538 chars omitted),+1 more (map truncated)
  IfcType = 0
  MoveBase = false
  MoveWithHost = false
  PerimeterLength = 0
  Placement = pos=(4975,2785,0) rot=(0,0,1;1.5708rad)
  PredefinedType = 0
  VerticalArea = 0
FEATURE [Part::FeaturePython] Component241052  label="открывание двери 036"  # Arch/BIM 0 (typed FeaturePython)
  Base = -> Line2130
  HorizontalArea = 0
  IfcData = attributes={"GlobalId": {"name": "GlobalId", "type": "IfcGloballyUniqueId", "is_enum": false, "enum_values": []}, "Description": {"... (+538 chars omitted),+1 more (map truncated)
  IfcType = 0
  MoveBase = false
  MoveWithHost = false
  PerimeterLength = 0
  Placement = pos=(4975,2785,0) rot=(0,0,-1;1.5708rad)
  PredefinedType = 0
  VerticalArea = 0
FEATURE [App::FeaturePython] Dimension190  # Draft dimension (typed FeaturePython)
  Diameter = false
  Dimline = (5800,3000,0)
  Direction = (0,0,0)
  Distance = 900
  End = (5825,2885,0)
  Normal = (0,0,1)
  Start = (4925,2885,0)
FEATURE [App::GeometryPython] BuildingPart127  label="Размеры (Мансарда)"  # Arch/BIM 52 (typed FeaturePython)
  Area = 0
  GlobalId = 3_s$oy9jj54xonqTEdRA8q
  Group = -> [ShapeString209,Circle145,Circle146,Circle147,ShapeString211,Circle149,ShapeString213,Circle150,ShapeString214,Line1746,Line1747,Line1748,Line1749,Line1750,ShapeString218,ShapeString219,Dimension112,Dimension126,Dimension127,Dimension130,Dimension132,Dimension133,Dimension137,Dimension139,Dimension145,Dimension148,Dimension150,BuildingPart128,Dimension154,Dimension155,Dimension159,Dimension164,+20 more]
  Height = 0
  HeightPropagate = true
  IfcData = IfcUID=3_s$oy9jj54xonqTEdRA8q,+2 more (map truncated)
  IfcType = 52
  LevelOffset = 0
FEATURE [Sketcher::SketchObject] Sketch429
  FullyConstrained = true
  Placement = pos=(5890,3225,-70) rot=(0,0.707107,0.707107;3.14159rad)
  sketch-geometry (24):
    g0: LineSegment StartX=0 StartY=0 StartZ=0 EndX=1300 EndY=0 EndZ=0
    g1: LineSegment StartX=1300 StartY=0 StartZ=0 EndX=1300 EndY=2470 EndZ=0
    g2: LineSegment StartX=1300 StartY=2470 StartZ=0 EndX=0 EndY=2470 EndZ=0
    g3: LineSegment StartX=0 StartY=2470 StartZ=0 EndX=0 EndY=0 EndZ=0
    g4: LineSegment StartX=70 StartY=70 StartZ=0 EndX=1230 EndY=70 EndZ=0
    g5: LineSegment StartX=1230 StartY=70 StartZ=0 EndX=1230 EndY=2400 EndZ=0
    g6: LineSegment StartX=1230 StartY=2400 StartZ=0 EndX=70 EndY=2400 EndZ=0
    g7: LineSegment StartX=70 StartY=2400 StartZ=0 EndX=70 EndY=70 EndZ=0
    g8: LineSegment StartX=77 StartY=77 StartZ=0 EndX=877 EndY=77 EndZ=0
    g9: LineSegment StartX=877 StartY=77 StartZ=0 EndX=877 EndY=2393 EndZ=0
    g10: LineSegment StartX=877 StartY=2393 StartZ=0 EndX=77 EndY=2393 EndZ=0
    g11: LineSegment StartX=77 StartY=2393 StartZ=0 EndX=77 EndY=77 EndZ=0
    g12: LineSegment StartX=217 StartY=877 StartZ=0 EndX=737 EndY=877 EndZ=0
    g13: LineSegment StartX=737 StartY=877 StartZ=0 EndX=737 EndY=2253 EndZ=0
    g14: LineSegment StartX=737 StartY=2253 StartZ=0 EndX=217 EndY=2253 EndZ=0
    g15: LineSegment StartX=217 StartY=2253 StartZ=0 EndX=217 EndY=877 EndZ=0
    g16: LineSegment StartX=884 StartY=77 StartZ=0 EndX=1223 EndY=77 EndZ=0
    g17: LineSegment StartX=1223 StartY=77 StartZ=0 EndX=1223 EndY=2393 EndZ=0
    g18: LineSegment StartX=1223 StartY=2393 StartZ=0 EndX=884 EndY=2393 EndZ=0
    g19: LineSegment StartX=884 StartY=2393 StartZ=0 EndX=884 EndY=77 EndZ=0
    g20: LineSegment StartX=954 StartY=877 StartZ=0 EndX=1153 EndY=877 EndZ=0
    g21: LineSegment StartX=1153 StartY=877 StartZ=0 EndX=1153 EndY=2253 EndZ=0
    g22: LineSegment StartX=1153 StartY=2253 StartZ=0 EndX=954 EndY=2253 EndZ=0
    g23: LineSegment StartX=954 StartY=2253 StartZ=0 EndX=954 EndY=877 EndZ=0
  constraints (71):
    c: Coincident(g0,g1)
    c: Coincident(g1,g2)
    c: Coincident(g2,g3)
    c: Coincident(g3,g0)
    c: Horizontal(g0)
    c: Horizontal(g2)
    c: Vertical(g1)
    c: Vertical(g3)
    c: Coincident(g4,g5)
    c: Coincident(g5,g6)
    c: Coincident(g6,g7)
    c: Coincident(g7,g4)
    c: Horizontal(g4)
    c: Horizontal(g6)
    c: Vertical(g5)
    c: Vertical(g7)
    c: DistanceY(g1) = 2470  'Height'
    c: DistanceX(g0) = 1300  'Width'
    c: DistanceY(g6,g2) = 70  'Frame1'
    c: DistanceX(g2,g6) = 70  'Frame2'
    c: DistanceX(g4,g0) = 70  'Frame3'
    c: DistanceY(g0,g4) = 70  'Frame4'
    c: Coincident(g0,g-1)
    c: Coincident(g8,g9)
    c: Coincident(g9,g10)
    c: Coincident(g10,g11)
    c: Coincident(g11,g8)
    c: Horizontal(g8)
    c: Horizontal(g10)
    c: Vertical(g9)
    c: Vertical(g11)
    c: Coincident(g12,g13)
    c: Coincident(g13,g14)
    c: Coincident(g14,g15)
    c: Coincident(g15,g12)
    c: Horizontal(g12)
    c: Horizontal(g14)
    c: Vertical(g13)
    c: Vertical(g15)
    c: Coincident(g16,g17)
    c: Coincident(g17,g18)
    c: Coincident(g18,g19)
    c: Coincident(g19,g16)
    c: Horizontal(g16)
    c: Horizontal(g18)
    c: Vertical(g17)
    c: Vertical(g19)
    c: Coincident(g20,g21)
    c: Coincident(g21,g22)
    c: Coincident(g22,g23)
    c: Coincident(g23,g20)
    c: Horizontal(g20)
    c: Horizontal(g22)
    c: Vertical(g21)
    c: Vertical(g23)
    c: DistanceY(g8,g12) = 800
    c: DistanceX(g8,g12) = 140
    c: DistanceX(g21,g17) = 70
    c: DistanceY(g21,g17) = 140
    c: DistanceX(g16,g20) = 70
    c: DistanceX(g14,g10) = 140
    c: DistanceY(g8,g16) = 0
    c: DistanceY(g10,g18) = 0
    c: DistanceX(g4,g8) = 7
    c: DistanceY(g4,g8) = 7
    c: DistanceX(g6,g18) = -7
    c: DistanceY(g6,g18) = -7
    c: DistanceX(g9,g19) = 7
    c: PointOnObject(g13,g22)
    c: PointOnObject(g20,g12)
    c: DistanceX(g10,g10) = 800
FEATURE [Part::FeaturePython] Window115  label="Д-130-001"  # Arch/BIM 170 (typed FeaturePython)
  Area = 3211000
  Base = -> Sketch429
  Frame = 50
  Height = 2470
  HoleDepth = 0
  HoleWire = 0
  HorizontalArea = 0
  IfcData = attributes={"GlobalId": {"name": "GlobalId", "type": "IfcGloballyUniqueId", "is_enum": false, "enum_values": []}, "Description": {"... (+1231 chars omitted),+1 more (map truncated)
  IfcType = 170
  LouvreSpacing = 0
  LouvreWidth = 0
  Material = -> Material011
  MoveBase = false
  MoveWithHost = true
  Normal = (0,-1,2e-16)
  Opening = 0
  OverallHeight = 2470
  OverallWidth = 1300
  PartitioningType = 0
  PerimeterLength = 0
  Placement = pos=(9.09e-13,-30,0) rot=(0,0,1;0rad)
  PredefinedType = 0
  Preset = 3
  SymbolElevation = false
  SymbolPlan = false
  VerticalArea = 0
  Width = 1300
  WindowParts = <same value as first occurrence — deduplicated (x4 in doc)>
  expr: OverallHeight = .Height.Value
  expr: OverallWidth = .Width.Value
FEATURE [App::GeometryPython] BuildingPart011  label="Окна и двери 1этаж"  # Arch/BIM 52 (typed FeaturePython)
  Area = 37026550
  GlobalId = 2lTKOyIXPBJh5VnrrZDJsa
  Group = -> [Window020,Window021,Window026,Window052,Window068,Window069,Window070,Window071,Window073,Window074,Window077,Window090,Window091,Window108,Window109,Window110,Window115]
  Height = 0
  HeightPropagate = true
  IfcData = IfcUID=2lTKOyIXPBJh5VnrrZDJsa,attributes={"GlobalId": {"value": "2lTKOyIXPBJh5VnrrZDJsa"}},+1 more (map truncated)
  IfcType = 52
  LevelOffset = 0
FEATURE [App::FeaturePython] Section016  label="Section (перемычки)"  # WARN: FeaturePython — macro-defined, semantics opaque (R4)
  Clip = false
  Objects = -> [Wall277,Wall278,Wall281,Wall497,Wall564,Wall568,Wall569,Wall566,Wall574,Wall572,Wall573,Wall565,Wall570,Wall571]
  OnlySolids = true
  Placement = pos=(6100,3700,2000) rot=(0,0,1;0rad)
  UseMaterialColorForFill = false
FEATURE [Part::FeaturePython] Component241053  label="открывание двери 076"  # Arch/BIM 0 (typed FeaturePython)
  Base = -> Line2098
  HorizontalArea = 0
  IfcData = attributes={"GlobalId": {"name": "GlobalId", "type": "IfcGloballyUniqueId", "is_enum": false, "enum_values": []}, "Description": {"... (+538 chars omitted),+1 more (map truncated)
  IfcType = 0
  MoveBase = false
  MoveWithHost = false
  PerimeterLength = 0
  Placement = pos=(165,15525,0) rot=(0,0,1;0rad)
  PredefinedType = 0
  VerticalArea = 0
FEATURE [Part::FeaturePython] Component241054  label="открывание двери 077"  # Arch/BIM 0 (typed FeaturePython)
  Base = -> Arc160
  HorizontalArea = 0
  IfcData = attributes={"GlobalId": {"name": "GlobalId", "type": "IfcGloballyUniqueId", "is_enum": false, "enum_values": []}, "Description": {"... (+538 chars omitted),+1 more (map truncated)
  IfcType = 0
  MoveBase = false
  MoveWithHost = false
  PerimeterLength = 0
  Placement = pos=(3535,8225,0) rot=(0,0,1;0rad)
  PredefinedType = 0
  VerticalArea = 0
FEATURE [Part::FeaturePython] Component241055  label="открывание двери 078"  # Arch/BIM 0 (typed FeaturePython)
  Base = -> Arc152
  HorizontalArea = 0
  IfcData = attributes={"GlobalId": {"name": "GlobalId", "type": "IfcGloballyUniqueId", "is_enum": false, "enum_values": []}, "Description": {"... (+538 chars omitted),+1 more (map truncated)
  IfcType = 0
  MoveBase = false
  MoveWithHost = false
  PerimeterLength = 0
  Placement = pos=(3395,4525,0) rot=(0,0,1;0rad)
  PredefinedType = 0
  VerticalArea = 0
FEATURE [Part::FeaturePython] Component241056  label="открывание двери 079"  # Arch/BIM 0 (typed FeaturePython)
  Base = -> Line2056
  HorizontalArea = 0
  IfcData = attributes={"GlobalId": {"name": "GlobalId", "type": "IfcGloballyUniqueId", "is_enum": false, "enum_values": []}, "Description": {"... (+538 chars omitted),+1 more (map truncated)
  IfcType = 0
  MoveBase = false
  MoveWithHost = false
  PerimeterLength = 0
  Placement = pos=(3395,5325,0) rot=(0,0,1;0rad)
  PredefinedType = 0
  VerticalArea = 0
FEATURE [Part::FeaturePython] Component241057  label="открывание двери 080"  # Arch/BIM 0 (typed FeaturePython)
  Base = -> Arc151
  HorizontalArea = 0
  IfcData = attributes={"GlobalId": {"name": "GlobalId", "type": "IfcGloballyUniqueId", "is_enum": false, "enum_values": []}, "Description": {"... (+538 chars omitted),+1 more (map truncated)
  IfcType = 0
  MoveBase = false
  MoveWithHost = false
  PerimeterLength = 0
  Placement = pos=(3385,3115,0) rot=(0,0,1;1.5708rad)
  PredefinedType = 0
  VerticalArea = 0
FEATURE [Part::FeaturePython] Component241058  label="открывание двери 081"  # Arch/BIM 0 (typed FeaturePython)
  Base = -> Line2059
  HorizontalArea = 0
  IfcData = attributes={"GlobalId": {"name": "GlobalId", "type": "IfcGloballyUniqueId", "is_enum": false, "enum_values": []}, "Description": {"... (+538 chars omitted),+1 more (map truncated)
  IfcType = 0
  MoveBase = false
  MoveWithHost = false
  PerimeterLength = 0
  Placement = pos=(3385,3260,0) rot=(0,0,1;0rad)
  PredefinedType = 0
  VerticalArea = 0
FEATURE [Part::FeaturePython] Component241063  label="открывание двери 086"  # Arch/BIM 0 (typed FeaturePython)
  Base = -> Arc154
  HorizontalArea = 0
  IfcData = attributes={"GlobalId": {"name": "GlobalId", "type": "IfcGloballyUniqueId", "is_enum": false, "enum_values": []}, "Description": {"... (+538 chars omitted),+1 more (map truncated)
  IfcType = 0
  MoveBase = false
  MoveWithHost = false
  PerimeterLength = 0
  Placement = pos=(5010,4425,0) rot=(0,0,1;0rad)
  PredefinedType = 0
  VerticalArea = 0
FEATURE [Part::FeaturePython] Component241064  label="открывание двери 087"  # Arch/BIM 0 (typed FeaturePython)
  Base = -> Line2057
  HorizontalArea = 0
  IfcData = attributes={"GlobalId": {"name": "GlobalId", "type": "IfcGloballyUniqueId", "is_enum": false, "enum_values": []}, "Description": {"... (+538 chars omitted),+1 more (map truncated)
  IfcType = 0
  MoveBase = false
  MoveWithHost = false
  PerimeterLength = 0
  Placement = pos=(4310,3625,0) rot=(0,0,1;0rad)
  PredefinedType = 0
  VerticalArea = 0
FEATURE [Part::FeaturePython] Component241065  label="открывание двери 088"  # Arch/BIM 0 (typed FeaturePython)
  Base = -> Line2097
  HorizontalArea = 0
  IfcData = attributes={"GlobalId": {"name": "GlobalId", "type": "IfcGloballyUniqueId", "is_enum": false, "enum_values": []}, "Description": {"... (+538 chars omitted),+1 more (map truncated)
  IfcType = 0
  MoveBase = false
  MoveWithHost = false
  PerimeterLength = 0
  Placement = pos=(2735,8225,0) rot=(0,0,1;0rad)
  PredefinedType = 0
  VerticalArea = 0
FEATURE [Part::FeaturePython] Component241066  label="открывание двери 089"  # Arch/BIM 0 (typed FeaturePython)
  Base = -> Arc153
  HorizontalArea = 0
  IfcData = attributes={"GlobalId": {"name": "GlobalId", "type": "IfcGloballyUniqueId", "is_enum": false, "enum_values": []}, "Description": {"... (+538 chars omitted),+1 more (map truncated)
  IfcType = 0
  MoveBase = false
  MoveWithHost = false
  PerimeterLength = 0
  Placement = pos=(6105,925,0) rot=(0,0,1;0rad)
  PredefinedType = 0
  VerticalArea = 0
FEATURE [App::GeometryPython] BuildingPart107  label="Направление открывания дверей"  # Arch/BIM 172 (typed FeaturePython)
  Area = 0
  Group = -> [Component241065,Component241064,Component241058,Component241056,Component241054,Component241063,Component241055,Component241057,Component241066,Component241053]
  Height = 0
  HeightPropagate = true
  IfcData = attributes={"GlobalId": {"name": "GlobalId", "type": "IfcGloballyUniqueId", "is_enum": false, "enum_values": []}, "Description": {"... (+484 chars omitted),+1 more (map truncated)
  IfcType = 172
  LevelOffset = 0
  PredefinedType = 0
FEATURE [Part::Part2DObjectPython] ShapeString278  # Draft 2D object (typed FeaturePython)
  FontFile = <path>
  Placement = pos=(6387.96,6443.39,0) rot=(0,0,1;1.5708rad)
  Size = 130
  String = 17x185/260
  Tracking = 0
FEATURE [App::FeaturePython] Dimension191  # Draft dimension (typed FeaturePython)
  Diameter = false
  Dimline = (100,10400,0)
  Direction = (0,0,0)
  Distance = 3920
  End = (3680,10597.3,0)
  Normal = (0,0,1)
  Start = (-240,10597.3,0)
FEATURE [App::FeaturePython] Dimension192  # Draft dimension (typed FeaturePython)
  Diameter = false
  Dimline = (100,10400,0)
  Direction = (0,0,0)
  Distance = 3300
  End = (6980,10597.3,0)
  Normal = (0,0,1)
  Start = (3680,10597.3,0)
FEATURE [App::FeaturePython] Dimension193  # Draft dimension (typed FeaturePython)
  Diameter = false
  Dimline = (100,10400,0)
  Direction = (0,0,0)
  Distance = 250
  End = (7230,10597.3,0)
  Normal = (0,0,1)
  Start = (6980,10597.3,0)
FEATURE [App::FeaturePython] Dimension194  # Draft dimension (typed FeaturePython)
  Diameter = false
  Dimline = (100,10400,0)
  Direction = (0,0,0)
  Distance = 3580
  End = (10810,10597.3,0)
  Normal = (0,0,1)
  Start = (7230,10597.3,0)
FEATURE [Part::FeaturePython] Component241067  label="Компонент"  # Arch/BIM 0 (typed FeaturePython)
  Base = -> Axis001006
  HorizontalArea = 0
  IfcData = attributes={"GlobalId": {"name": "GlobalId", "type": "IfcGloballyUniqueId", "is_enum": false, "enum_values": []}, "Description": {"... (+538 chars omitted),+1 more (map truncated)
  IfcType = 0
  MoveBase = false
  MoveWithHost = false
  PerimeterLength = 0
  Placement = pos=(12023.1,-555,0) rot=(0,0,1;1.5708rad)
  PredefinedType = 0
  VerticalArea = 0
FEATURE [Part::FeaturePython] Component241068  label="Компонент042"  # Arch/BIM 0 (typed FeaturePython)
  Base = -> Axis001007
  HorizontalArea = 0
  IfcData = attributes={"GlobalId": {"name": "GlobalId", "type": "IfcGloballyUniqueId", "is_enum": false, "enum_values": []}, "Description": {"... (+538 chars omitted),+1 more (map truncated)
  IfcType = 0
  MoveBase = false
  MoveWithHost = false
  PerimeterLength = 0
  Placement = pos=(-560,-2295.53,0) rot=(0,0,1;0rad)
  PredefinedType = 0
  VerticalArea = 0
FEATURE [App::GeometryPython] BuildingPart090  label="Размеры (1 этаж)"  # Arch/BIM 52 (typed FeaturePython)
  Area = 0
  GlobalId = 3_s$oy9jj54xonqTEdRA8q
  Group = -> [Dimension002,Dimension003,Dimension004,Dimension006,ShapeString138,Circle088,Circle089,ShapeString139,Circle090,ShapeString140,Circle091,ShapeString141,Circle092,ShapeString142,Circle093,ShapeString143,Circle094,ShapeString144,Circle095,ShapeString145,Line1326,Line1327,Line1328,Line1329,Line1330,ShapeString189,ShapeString191,Dimension018,Dimension026,Dimension027,Circle123,ShapeString193,+62 more]
  Height = 0
  HeightPropagate = true
  IfcData = IfcUID=3_s$oy9jj54xonqTEdRA8q,+2 more (map truncated)
  IfcType = 52
  LevelOffset = 0
FEATURE [Part::FeaturePython] Component241069  label="Компонент043"  # Arch/BIM 0 (typed FeaturePython)
  Base = -> Axis001006
  HorizontalArea = 0
  IfcData = attributes={"GlobalId": {"name": "GlobalId", "type": "IfcGloballyUniqueId", "is_enum": false, "enum_values": []}, "Description": {"... (+538 chars omitted),+1 more (map truncated)
  IfcType = 0
  MoveBase = false
  MoveWithHost = false
  PerimeterLength = 0
  Placement = pos=(12023.1,-555,0) rot=(0,0,1;1.5708rad)
  PredefinedType = 0
  VerticalArea = 0
FEATURE [Part::FeaturePython] Component241070  label="Компонент044"  # Arch/BIM 0 (typed FeaturePython)
  Base = -> Axis001007
  HorizontalArea = 0
  IfcData = attributes={"GlobalId": {"name": "GlobalId", "type": "IfcGloballyUniqueId", "is_enum": false, "enum_values": []}, "Description": {"... (+538 chars omitted),+1 more (map truncated)
  IfcType = 0
  MoveBase = false
  MoveWithHost = false
  PerimeterLength = 0
  Placement = pos=(-560,-2295.53,0) rot=(0,0,1;0rad)
  PredefinedType = 0
  VerticalArea = 0
FEATURE [App::FeaturePython] Dimension195  # Draft dimension (typed FeaturePython)
  Diameter = false
  Dimline = (6200,3400,0)
  Direction = (0,0,0)
  Distance = 1160
  End = (7185,3205,0)
  Normal = (0,0,1)
  Start = (6025,3205,0)
FEATURE [App::FeaturePython] Dimension196  # Draft dimension (typed FeaturePython)
  Diameter = false
  Dimline = (7600,3400,0)
  Direction = (0,0,0)
  Distance = 2655
  End = (9840,3205,0)
  Normal = (0,0,1)
  Start = (7185,3205,0)
FEATURE [App::FeaturePython] Dimension197  # Draft dimension (typed FeaturePython)
  Diameter = false
  Dimline = (9820,3400,0)
  Direction = (0,0,0)
  Distance = 780
  End = (10620,3205,0)
  Normal = (0,0,1)
  Start = (9840,3205,0)
FEATURE [App::FeaturePython] Dimension198  # Draft dimension (typed FeaturePython)
  Diameter = false
  Dimline = (6700,5200,0)
  Direction = (0,0,0)
  Distance = 1160
  End = (6855,5675,0)
  Normal = (0,0,1)
  Start = (6855,4515,0)
FEATURE [App::FeaturePython] Dimension199  # Draft dimension (typed FeaturePython)
  Diameter = false
  Dimline = (3400,5900,0)
  Direction = (0,0,0)
  Distance = 2850
  End = (3555,7365,0)
  Normal = (0,0,1)
  Start = (3555,4515,0)
FEATURE [App::FeaturePython] Dimension200  # Draft dimension (typed FeaturePython)
  Diameter = false
  Dimline = (3400,7365,0)
  Direction = (0,0,0)
  Distance = 920
  End = (3555,8285,0)
  Normal = (0,0,1)
  Start = (3555,7365,0)
FEATURE [App::FeaturePython] Dimension201  # Draft dimension (typed FeaturePython)
  Diameter = false
  Dimline = (3400,7365,0)
  Direction = (0,0,0)
  Distance = 130
  End = (3555,8415,0)
  Normal = (0,0,1)
  Start = (3555,8285,0)
FEATURE [App::FeaturePython] Dimension202  # Draft dimension (typed FeaturePython)
  Diameter = false
  Dimline = (3680,4515,0)
  Direction = (0,0,0)
  Distance = 1310
  End = (3555,4515,0)
  Normal = (0,0,1)
  Start = (3555,3205,0)
FEATURE [App::FeaturePython] Dimension203  # Draft dimension (typed FeaturePython)
  Diameter = false
  Dimline = (6980,4166.27,0)
  Direction = (0,0,0)
  Distance = 1310
  End = (7500,4515,0)
  Normal = (0,0,1)
  Start = (7500,3205,0)
FEATURE [App::FeaturePython] Dimension204  # Draft dimension (typed FeaturePython)
  Diameter = false
  Dimline = (6980,6800,0)
  Direction = (0,0,0)
  Distance = 2740
  End = (7500,8415,0)
  Normal = (0,0,1)
  Start = (7500,5675,0)
FEATURE [App::FeaturePython] Dimension205  # Draft dimension (typed FeaturePython)
  Diameter = false
  Dimline = (4000,5200,0)
  Direction = (0,0,0)
  Distance = 920
  End = (3805,5685,0)
  Normal = (0,0,1)
  Start = (3805,4765,0)
FEATURE [App::FeaturePython] Dimension206  # Draft dimension (typed FeaturePython)
  Diameter = false
  Dimline = (4000,5685,0)
  Direction = (0,0,0)
  Distance = 1680
  End = (3805,7365,0)
  Normal = (0,0,1)
  Start = (3805,5685,0)
FEATURE [Part::Part2DObjectPython] Clone2D026  label="Circle126 (2D)"  # Draft 2D object (typed FeaturePython)
  Fuse = false
  Objects = -> [Circle125]
  Placement = pos=(-1854.18,-235,0) rot=(0,0,1;0rad)
  Scale = (1,1,1)
FEATURE [Part::Part2DObjectPython] Clone2D027  label="ShapeString195 (2D)"  # Draft 2D object (typed FeaturePython)
  Fuse = false
  Objects = -> [ShapeString195]
  Placement = pos=(-1941.5,-327.945,0) rot=(0,0,1;0rad)
  Scale = (1,1,1)
FEATURE [Part::Part2DObjectPython] Clone2D028  label="Circle125 (2D)"  # Draft 2D object (typed FeaturePython)
  Fuse = false
  Objects = -> [Circle124]
  Placement = pos=(-1854.18,3080,0) rot=(0,0,1;0rad)
  Scale = (1,1,1)
FEATURE [Part::Part2DObjectPython] Clone2D029  label="ShapeString194 (2D)"  # Draft 2D object (typed FeaturePython)
  Fuse = false
  Objects = -> [ShapeString194]
  Placement = pos=(-1933.86,2991.01,0) rot=(0,0,1;0rad)
  Scale = (1,1,1)
FEATURE [Part::Part2DObjectPython] Clone2D030  label="Circle124 (2D)"  # Draft 2D object (typed FeaturePython)
  Fuse = false
  Objects = -> [Circle123]
  Placement = pos=(-1854.18,8605,0) rot=(0,0,1;0rad)
  Scale = (1,1,1)
FEATURE [Part::Part2DObjectPython] Clone2D031  label="ShapeString193 (2D)"  # Draft 2D object (typed FeaturePython)
  Fuse = false
  Objects = -> [ShapeString193]
  Placement = pos=(-1950.61,8511.85,0) rot=(0,0,1;0rad)
  Scale = (1,1,1)
FEATURE [Part::Part2DObjectPython] Clone2D032  label="Circle127 (2D)"  # Draft 2D object (typed FeaturePython)
  Fuse = false
  Objects = -> [Circle126]
  Placement = pos=(-240,10797.3,0) rot=(0,0,1;0rad)
  Scale = (1,1,1)
FEATURE [Part::Part2DObjectPython] Clone2D033  label="ShapeString196 (2D)"  # Draft 2D object (typed FeaturePython)
  Fuse = false
  Objects = -> [ShapeString196]
  Placement = pos=(-319.076,10705,0) rot=(0,0,1;0rad)
  Scale = (1,1,1)
FEATURE [Part::Part2DObjectPython] Clone2D034  label="Circle128 (2D)"  # Draft 2D object (typed FeaturePython)
  Fuse = false
  Objects = -> [Circle127]
  Placement = pos=(3680,10797.3,0) rot=(0,0,1;0rad)
  Scale = (1,1,1)
FEATURE [Part::Part2DObjectPython] Clone2D035  label="ShapeString197 (2D)"  # Draft 2D object (typed FeaturePython)
  Fuse = false
  Objects = -> [ShapeString197]
  Placement = pos=(3597.38,10713.8,0) rot=(0,0,1;0rad)
  Scale = (1,1,1)
FEATURE [Part::Part2DObjectPython] Clone2D036  label="Circle129 (2D)"  # Draft 2D object (typed FeaturePython)
  Fuse = false
  Objects = -> [Circle128]
  Placement = pos=(6980,10797.3,0) rot=(0,0,1;0rad)
  Scale = (1,1,1)
FEATURE [Part::Part2DObjectPython] Clone2D037  label="Circle130 (2D)"  # Draft 2D object (typed FeaturePython)
  Fuse = false
  Objects = -> [Circle129]
  Placement = pos=(7230,10797.3,0) rot=(0,0,1;0rad)
  Scale = (1,1,1)
FEATURE [Part::Part2DObjectPython] Clone2D038  label="ShapeString198 (2D)"  # Draft 2D object (typed FeaturePython)
  Fuse = false
  Objects = -> [ShapeString198]
  Placement = pos=(6908.07,10701.1,0) rot=(0,0,1;0rad)
  Scale = (1,1,1)
FEATURE [Part::Part2DObjectPython] Clone2D039  label="ShapeString199 (2D)"  # Draft 2D object (typed FeaturePython)
  Fuse = false
  Objects = -> [ShapeString199]
  Placement = pos=(7144.17,10703.7,0) rot=(0,0,1;0rad)
  Scale = (1,1,1)
FEATURE [Part::Part2DObjectPython] Clone2D040  label="Circle131 (2D)"  # Draft 2D object (typed FeaturePython)
  Fuse = false
  Objects = -> [Circle130]
  Placement = pos=(10810,10797.3,0) rot=(0,0,1;0rad)
  Scale = (1,1,1)
FEATURE [Part::Part2DObjectPython] Clone2D041  label="ShapeString200 (2D)"  # Draft 2D object (typed FeaturePython)
  Fuse = false
  Objects = -> [ShapeString200]
  Placement = pos=(10740.3,10697.4,0) rot=(0,0,1;0rad)
  Scale = (1,1,1)
FEATURE [App::FeaturePython] Dimension207  # Draft dimension (typed FeaturePython)
  Diameter = false
  Dimline = (-1400,3680,0)
  Direction = (0,0,0)
  Distance = 5525
  End = (-1654.18,8605,0)
  Normal = (0,0,1)
  Start = (-1654.18,3080,0)
FEATURE [App::FeaturePython] Dimension208  # Draft dimension (typed FeaturePython)
  Diameter = false
  Dimline = (-1400,-400,0)
  Direction = (0,0,0)
  Distance = 3315
  End = (-1654.18,3080,0)
  Normal = (0,0,1)
  Start = (-1654.18,-235,0)
FEATURE [App::FeaturePython] Dimension209  # Draft dimension (typed FeaturePython)
  Diameter = false
  Dimline = (100,10400,0)
  Direction = (0,0,0)
  Distance = 3920
  End = (3680,10597.3,0)
  Normal = (0,0,1)
  Start = (-240,10597.3,0)
FEATURE [App::FeaturePython] Dimension210  # Draft dimension (typed FeaturePython)
  Diameter = false
  Dimline = (100,10400,0)
  Direction = (0,0,0)
  Distance = 3300
  End = (6980,10597.3,0)
  Normal = (0,0,1)
  Start = (3680,10597.3,0)
FEATURE [App::FeaturePython] Dimension211  # Draft dimension (typed FeaturePython)
  Diameter = false
  Dimline = (100,10400,0)
  Direction = (0,0,0)
  Distance = 250
  End = (7230,10597.3,0)
  Normal = (0,0,1)
  Start = (6980,10597.3,0)
FEATURE [App::FeaturePython] Dimension212  # Draft dimension (typed FeaturePython)
  Diameter = false
  Dimline = (100,10400,0)
  Direction = (0,0,0)
  Distance = 3580
  End = (10810,10597.3,0)
  Normal = (0,0,1)
  Start = (7230,10597.3,0)
FEATURE [Part::Part2DObjectPython] ShapeString279  # Draft 2D object (typed FeaturePython)
  FontFile = <path>
  Placement = pos=(3345.86,13049.3,0) rot=(0,0,1;0rad)
  Size = 800
  String = уклон 4%
  Tracking = 0
FEATURE [Part::Part2DObjectPython] ShapeString280  # Draft 2D object (typed FeaturePython)
  FontFile = <path>
  Placement = pos=(-7707.66,4729.12,0) rot=(0,0,1;0rad)
  Size = 800
  String = уклон 4%
  Tracking = 0
FEATURE [Part::Part2DObjectPython] ShapeString281  # Draft 2D object (typed FeaturePython)
  FontFile = <path>
  Placement = pos=(13997.3,4221.11,0) rot=(0,0,1;0rad)
  Size = 800
  String = уклон 1%
  Tracking = 0
FEATURE [Part::Part2DObjectPython] ShapeString282  # Draft 2D object (typed FeaturePython)
  FontFile = <path>
  Placement = pos=(3671.38,-4150.17,0) rot=(0,0,1;0rad)
  Size = 800
  String = уклон 1%
  Tracking = 0
FEATURE [Part::Part2DObjectPython] ShapeString283  # Draft 2D object (typed FeaturePython)
  FontFile = <path>
  Placement = pos=(19603.6,-15147.6,0) rot=(0,0,1;0rad)
  Size = 800
  String = Отметка +0.0
  Tracking = 0
FEATURE [Part::Part2DObjectPython] ShapeString284  # Draft 2D object (typed FeaturePython)
  FontFile = <path>
  Placement = pos=(2587.81,4270.53,0) rot=(0,0,1;0rad)
  Size = 800
  String = Отметка +0.13
  Tracking = 0
FEATURE [Part::Part2DObjectPython] Line2267  # Draft 2D object (typed FeaturePython)
  Area = 0
  ChamferSize = 0
  Closed = false
  End = (0,-11400,-190)
  FilletRadius = 0
  Length = 10687.4
  MakeFace = true
  Placement = pos=(0,-712.617,-190) rot=(0.57735,0.57735,0.57735;2.0944rad)
  Points = (2) [(0,0,0),(-10687.4,0,0)]
  Start = (0,-712.617,-190)
  Subdivisions = 0
FEATURE [Part::Part2DObjectPython] Line2268  # Draft 2D object (typed FeaturePython)
  Area = 0
  ChamferSize = 0
  Closed = false
  End = (0,-10600,-303.742)
  FilletRadius = 0
  Length = 778.629
  MakeFace = true
  Placement = pos=(0,-9821.37,-303.742) rot=(0.57735,0.57735,0.57735;2.0944rad)
  Points = (2) [(0,0,0),(-778.629,0,0)]
  Start = (0,-9821.37,-303.742)
  Subdivisions = 0
FEATURE [Part::Part2DObjectPython] Line2269  # Draft 2D object (typed FeaturePython)
  Area = 0
  ChamferSize = 0
  Closed = true
  End = (0,-10300,-303.742)
  FilletRadius = 0
  Length = 113.742
  MakeFace = true
  Placement = pos=(0,-10300,-100) rot=(0.57735,0.57735,0.57735;2.0944rad)
  Points = (2) [(0,-90,0),(0,-203.742,0)]
  Start = (0,-10300,-190)
  Subdivisions = 0
FEATURE [Part::Part2DObjectPython] ShapeString285  # Draft 2D object (typed FeaturePython)
  FontFile = <path>
  Placement = pos=(2450.35,2248.39,0) rot=(0,0,1;0rad)
  Size = 800
  String = 9.6м x 11.8м
  Tracking = 0
FEATURE [Part::Part2DObjectPython] Wire1090  # Draft 2D object (typed FeaturePython)
  Area = 0
  ChamferSize = 0
  Closed = true
  End = (-26667.6,35086.6,0)
  FilletRadius = 0
  Length = 51349
  MakeFace = false
  Placement = pos=(-27470.7,38929.9,0) rot=(0,0,1;0rad)
  Points = (19) [(0,0,0),(458.9,2868.14,0),(1261.98,4589.03,0),(2925.51,5793.65,0),(5770.71,6470.09,0),(7970.71,5970.09,0),(9670.71,4870.09,0),(10670.7,2070.09,0),+11 more]
  Start = (-27470.7,38929.9,0)
  Subdivisions = 0
FEATURE [Part::Part2DObjectPython] ShapeString286  # Draft 2D object (typed FeaturePython)
  FontFile = <path>
  Placement = pos=(-19382.8,34346.4,0) rot=(0,0,1;0rad)
  Size = 800
  String = пруд
  Tracking = 0
FEATURE [Part::Part2DObjectPython] Wire1091  # Draft 2D object (typed FeaturePython)
  Area = 0
  ChamferSize = 0
  Closed = true
  End = (24500,27600,0)
  FilletRadius = 0
  Length = 129212
  MakeFace = false
  Placement = pos=(23611.8,-186.05,0) rot=(0,0,1;0rad)
  Points = (6) [(-11.7695,3286.05,0),(1288.23,3286.05,0),(2188.23,28686,0),(-35611.8,38086,0),(-35511.8,36486,0),(888.23,27786,0)]
  Start = (23600,3100,0)
  Subdivisions = 0
FEATURE [Part::Part2DObjectPython] ShapeString288  # Draft 2D object (typed FeaturePython)
  FontFile = <path>
  Placement = pos=(6875.29,33593.6,0) rot=(0,0,-1;0.11726rad)
  Size = 800
  String = дренажная канава
  Tracking = 0
FEATURE [Part::Part2DObjectPython] Wire1092  # Draft 2D object (typed FeaturePython)
  Area = 0
  ChamferSize = 0
  Closed = true
  End = (-12525.4,-10333.9,0)
  FilletRadius = 0
  Length = 95695.4
  MakeFace = false
  Placement = pos=(-13915.7,-10931.5,0) rot=(0,0,1;0rad)
  Points = (8) [(0,0,0),(-5778.45,18983.7,0),(-8587.95,28078.6,0),(-12416.3,44954.3,0),(-10747.2,44728,0),(-7417.13,28315,0),(-900.395,7801.3,0),(1390.29,597.558,0)]
  Start = (-13915.7,-10931.5,0)
  Subdivisions = 0
FEATURE [Part::Part2DObjectPython] ShapeString290  # Draft 2D object (typed FeaturePython)
  FontFile = <path>
  Placement = pos=(-17021,1863.22,0) rot=(0,0,1;1.86141rad)
  Size = 800
  String = дренажная канава
  Tracking = 0
FEATURE [App::FeaturePython] Dimension213  # Draft dimension (typed FeaturePython)
  Diameter = false
  Dimline = (3555,3400,0)
  Direction = (0,0,0)
  Distance = 3605
  End = (3555,-45,0)
  Normal = (0,0,1)
  Start = (-50,-45,0)
FEATURE [App::FeaturePython] Dimension214  # Draft dimension (typed FeaturePython)
  Diameter = false
  Dimline = (-800,3215,0)
  Direction = (0,0,0)
  Distance = 5970
  End = (-560,8925,0)
  Normal = (0,0,1)
  Start = (-560,2955,0)
FEATURE [App::FeaturePython] Dimension215  # Draft dimension (typed FeaturePython)
  Diameter = false
  Dimline = (-800,3215,0)
  Direction = (0,0,0)
  Distance = 1570
  End = (-560,2955,0)
  Normal = (0,0,1)
  Start = (-560,1385,0)
FEATURE [App::FeaturePython] Dimension216  # Draft dimension (typed FeaturePython)
  Diameter = false
  Dimline = (-800,1905,0)
  Direction = (0,0,0)
  Distance = 1940
  End = (-560,1385,0)
  Normal = (0,0,1)
  Start = (-560,-555,0)
FEATURE [App::FeaturePython] Dimension217  # Draft dimension (typed FeaturePython)
  Diameter = false
  Dimline = (1700,-800,0)
  Direction = (0,0,0)
  Distance = 3370
  End = (2810,-555,0)
  Normal = (0,0,1)
  Start = (-560,-555,0)
FEATURE [App::FeaturePython] Dimension218  # Draft dimension (typed FeaturePython)
  Diameter = false
  Dimline = (3300,-800,0)
  Direction = (0,0,0)
  Distance = 530
  End = (3340,-555,0)
  Normal = (0,0,1)
  Start = (2810,-555,0)
FEATURE [App::FeaturePython] Dimension219  # Draft dimension (typed FeaturePython)
  Diameter = false
  Dimline = (4400,-800,0)
  Direction = (0,0,0)
  Distance = 1290
  End = (4630,-555,0)
  Normal = (0,0,1)
  Start = (3340,-555,0)
FEATURE [App::FeaturePython] Dimension220  # Draft dimension (typed FeaturePython)
  Diameter = false
  Dimline = (4565,-800,0)
  Direction = (0,0,0)
  Distance = 1310
  End = (5940,-555,0)
  Normal = (0,0,1)
  Start = (4630,-555,0)
FEATURE [App::FeaturePython] Dimension227  # Draft dimension (typed FeaturePython)
  Diameter = false
  Dimline = (11700,5415,0)
  Direction = (0,0,0)
  Distance = 1570
  End = (11130,5175,0)
  Normal = (0,0,1)
  Start = (11130,3605,0)
FEATURE [Part::Part2DObjectPython] Rectangle4201  label="ККФ 380х250 001"  # Draft 2D object (typed FeaturePython)
  Area = 0
  ChamferSize = 0
  Columns = 1
  FilletRadius = 0
  Height = 250
  Length = 380
  MakeFace = false
  Placement = pos=(-430,-425,0) rot=(0,0,1;0rad)
  Rows = 1
FEATURE [Part::FeaturePython] Array085  # Draft array (typed FeaturePython)
  Angle = 360
  ArrayType = 0
  Axis = (0,0,1)
  Base = -> Rectangle4201
  Center = (0,0,0)
  Fuse = false
  IntervalAxis = (0,0,0)
  IntervalX = (1,0,0)
  IntervalY = (0,252.5,0)
  IntervalZ = (0,0,50)
  NumberCircles = 3
  NumberPolar = 5
  NumberX = 1
  NumberY = 35
  NumberZ = 1
  RadialDistance = 50
  Symmetry = 1
  TangentialDistance = 25
FEATURE [Part::Part2DObjectPython] Rectangle4202  label="ККФ 380х250 002"  # Draft 2D object (typed FeaturePython)
  Area = 0
  ChamferSize = 0
  Columns = 1
  FilletRadius = 0
  Height = 380
  Length = 250
  MakeFace = false
  Placement = pos=(3670,8415,0) rot=(0,0,1;0rad)
  Rows = 1
FEATURE [Part::FeaturePython] Array086  # Draft array (typed FeaturePython)
  Angle = 360
  ArrayType = 0
  Axis = (0,0,1)
  Base = -> Rectangle4202
  Center = (0,0,0)
  Fuse = false
  IntervalAxis = (0,0,0)
  IntervalX = (250.5,0,0)
  IntervalY = (0,0,0)
  IntervalZ = (0,0,50)
  NumberCircles = 3
  NumberPolar = 5
  NumberX = 15
  NumberY = 1
  NumberZ = 1
  RadialDistance = 50
  Symmetry = 1
  TangentialDistance = 25
FEATURE [Part::Part2DObjectPython] Rectangle4203  label="ККФ 380х250 003"  # Draft 2D object (typed FeaturePython)
  Area = 0
  ChamferSize = 0
  Columns = 1
  FilletRadius = 0
  Height = 380
  Length = 250
  MakeFace = false
  Placement = pos=(-50,-425,0) rot=(0,0,1;0rad)
  Rows = 1
FEATURE [Part::FeaturePython] Array087  # Draft array (typed FeaturePython)
  Angle = 360
  ArrayType = 0
  Axis = (0,0,1)
  Base = -> Rectangle4203
  Center = (0,0,0)
  Fuse = false
  IntervalAxis = (0,0,0)
  IntervalX = (257.3,0,0)
  IntervalY = (0,0,0)
  IntervalZ = (0,0,50)
  NumberCircles = 3
  NumberPolar = 5
  NumberX = 18
  NumberY = 1
  NumberZ = 1
  RadialDistance = 50
  Symmetry = 1
  TangentialDistance = 25
FEATURE [Part::Part2DObjectPython] Rectangle4204  label="ККФ 380х250 004"  # Draft 2D object (typed FeaturePython)
  Area = 0
  ChamferSize = 0
  Columns = 1
  FilletRadius = 0
  Height = 380
  Length = 250
  MakeFace = false
  Placement = pos=(6005,-425,0) rot=(0,0,1;0rad)
  Rows = 1
FEATURE [Part::FeaturePython] Array088  # Draft array (typed FeaturePython)
  Angle = 360
  ArrayType = 0
  Axis = (0,0,1)
  Base = -> Rectangle4204
  Center = (0,0,0)
  Fuse = false
  IntervalAxis = (0,0,0)
  IntervalX = (256.5,0,0)
  IntervalY = (0,0,0)
  IntervalZ = (0,0,50)
  NumberCircles = 3
  NumberPolar = 5
  NumberX = 18
  NumberY = 1
  NumberZ = 1
  RadialDistance = 50
  Symmetry = 1
  TangentialDistance = 25
FEATURE [Part::Part2DObjectPython] Rectangle4205  label="ККФ 380х250 005"  # Draft 2D object (typed FeaturePython)
  Area = 0
  ChamferSize = 0
  Columns = 1
  FilletRadius = 0
  Height = 250
  Length = 380
  MakeFace = false
  Placement = pos=(10620,-425,0) rot=(0,0,1;0rad)
  Rows = 1
FEATURE [Part::FeaturePython] Array089  # Draft array (typed FeaturePython)
  Angle = 360
  ArrayType = 0
  Axis = (0,0,1)
  Base = -> Rectangle4205
  Center = (0,0,0)
  Fuse = false
  IntervalAxis = (0,0,0)
  IntervalX = (1,0,0)
  IntervalY = (0,252.5,0)
  IntervalZ = (0,0,50)
  NumberCircles = 3
  NumberPolar = 5
  NumberX = 1
  NumberY = 35
  NumberZ = 1
  RadialDistance = 50
  Symmetry = 1
  TangentialDistance = 25
FEATURE [Part::Part2DObjectPython] Rectangle4206  label="ККФ 380х250 006"  # Draft 2D object (typed FeaturePython)
  Area = 0
  ChamferSize = 0
  Columns = 1
  FilletRadius = 0
  Height = 380
  Length = 250
  MakeFace = false
  Placement = pos=(10750,8415,0) rot=(0,0,1;0rad)
  Rows = 1
FEATURE [Part::FeaturePython] Array090  # Draft array (typed FeaturePython)
  Angle = 360
  ArrayType = 0
  Axis = (0,0,1)
  Base = -> Rectangle4206
  Center = (0,0,0)
  Fuse = false
  IntervalAxis = (0,0,0)
  IntervalX = (-250.5,0,0)
  IntervalY = (0,0,0)
  IntervalZ = (0,0,50)
  NumberCircles = 3
  NumberPolar = 5
  NumberX = 6
  NumberY = 1
  NumberZ = 1
  RadialDistance = 50
  Symmetry = 1
  TangentialDistance = 25
FEATURE [Part::Part2DObjectPython] Rectangle4207  label="ККФ 380х250 007"  # Draft 2D object (typed FeaturePython)
  Area = 0
  ChamferSize = 0
  Columns = 1
  FilletRadius = 0
  Height = 380
  Length = 250
  MakeFace = false
  Placement = pos=(3415,8415,0) rot=(0,0,1;0rad)
  Rows = 1
FEATURE [Part::FeaturePython] Array091  # Draft array (typed FeaturePython)
  Angle = 360
  ArrayType = 0
  Axis = (0,0,1)
  Base = -> Rectangle4207
  Center = (0,0,0)
  Fuse = false
  IntervalAxis = (0,0,0)
  IntervalX = (-256,0,0)
  IntervalY = (0,0,0)
  IntervalZ = (0,0,50)
  NumberCircles = 3
  NumberPolar = 5
  NumberX = 16
  NumberY = 1
  NumberZ = 1
  RadialDistance = 50
  Symmetry = 1
  TangentialDistance = 25
FEATURE [App::GeometryPython] BuildingPart141  label="1й этаж кладочный план"  # Arch/BIM 172 (typed FeaturePython)
  Area = 0
  Group = -> [Dimension084,Dimension080,Dimension092,Dimension053,Dimension081,Dimension082,Dimension083,Dimension095,Dimension097,Dimension099,Dimension085,Dimension096,Dimension094,Dimension024,Dimension012,Dimension056,Dimension184,Component241069,Component241070,Dimension195,Dimension196,Dimension197,Dimension198,Dimension199,Dimension200,Dimension201,Dimension202,Dimension203,Dimension204,Dimension205,+39 more]
  Height = 0
  HeightPropagate = true
  IfcData = attributes={"GlobalId": {"name": "GlobalId", "type": "IfcGloballyUniqueId", "is_enum": false, "enum_values": []}, "Description": {"... (+484 chars omitted),+1 more (map truncated)
  IfcType = 172
  LevelOffset = 0
  PredefinedType = 0
FEATURE [App::FeaturePython] Section010  label="Section 1st floor plan (кладочный)"  # WARN: FeaturePython — macro-defined, semantics opaque (R4)
  Clip = true
  Objects = -> [Wall004,Wall579,Wall567,Wall562,BuildingPart141,BuildingPart088,Wall298,Wall299,Wall300,Wall305,Wall309,Wall308,Wall307,Wall306]
  OnlySolids = true
  Placement = pos=(6100,3700,1400) rot=(0,0,1;0rad)
  UseMaterialColorForFill = true
FEATURE [TechDraw::DrawViewArch] ArchView010  label="Кладочный план 001"
  AllOn = true
  CutLineWidth = 0.1
  FillSpaces = false
  FontSize = 8
  JoinArch = false
  LineWidth = 0.1
  LockPosition = true
  RenderMode = 0
  Rotation = 0
  Scale = 0.02
  ScaleType = 2
  ShowFill = true
  ShowHidden = true
  Source = -> Section010
  Symbol = <blob: 469625 chars omitted>
  X = 210
  Y = 150
FEATURE [TechDraw::DrawPage] Page008  label="Кладочный план"
  KeepUpdated = false
  NextBalloonIndex = 1
  ProjectionType = 0
  Template = -> Template008
  Views = -> [ArchView010,Annotation040]
FEATURE [Part::Part2DObjectPython] Rectangle4208  # Draft 2D object (typed FeaturePython)
  Area = 2.0128e+08
  ChamferSize = 0
  Columns = 1
  FilletRadius = 0
  Height = 13600
  Length = 14800
  MakeFace = true
  Placement = pos=(-1914.5,-2700,0) rot=(0,0,1;0rad)
  Rows = 1
FEATURE [Part::Extrusion] Extrude099005024  label="грунт в пятне застройки 001"
  Base = -> Rectangle4208
  Dir = (0,0,1)
  DirMode = 2
  FaceMakerClass = Part::FaceMakerBullseye
  LengthFwd = 0
  LengthRev = 700
  Solid = false
  Symmetric = false
FEATURE [Part::MultiCommon] Common105  label="грунт в пятне застройки (для фасадов) 001"
  Shapes = -> [Common104,Extrude099005024]
FEATURE [Part::Part2DObjectPython] Line2270  label="облицовка_стены_036"  # Draft 2D object (typed FeaturePython)
  ChamferSize = 0
  Closed = true
  End = (11050,8955,0)
  FilletRadius = 0
  Length = 11640
  MakeFace = false
  Placement = pos=(-480,9475,0) rot=(0,0,1;0rad)
  Points = (2) [(-110,-520,0),(11530,-520,0)]
  Start = (-590,8955,0)
  Subdivisions = 0
FEATURE [Part::Part2DObjectPython] Line2271  label="облицовка_стены_037"  # Draft 2D object (typed FeaturePython)
  ChamferSize = 0
  Closed = true
  End = (-480,-585,0)
  FilletRadius = 0
  Length = 11530
  MakeFace = false
  Placement = pos=(12780,-555,0) rot=(0,0,1;0rad)
  Points = (2) [(-1730,-30,0),(-13260,-30,0)]
  Start = (11050,-585,0)
  Subdivisions = 0
FEATURE [Part::Part2DObjectPython] Line2272  label="облицовка_стены_038"  # Draft 2D object (typed FeaturePython)
  ChamferSize = 0
  Closed = true
  End = (-590,-585,0)
  FilletRadius = 0
  Length = 9430
  MakeFace = false
  Placement = pos=(-545,-765,0) rot=(0,0,1;0rad)
  Points = (2) [(-45,9610,0),(-45,180,0)]
  Start = (-590,8845,0)
  Subdivisions = 0
FEATURE [Part::FeaturePython] Wall628  label="Облицовка цоколя (камень бетонный СКЦ2Л-24) 001"  # Arch/BIM 166 (typed FeaturePython)
  Align = 1
  Area = 2829000
  Base = -> Line2272
  BlockHeight = 75
  BlockLength = 210
  CountBroken = 6
  CountEntire = 176
  Face = 0
  GlobalId = 1E5ZyhmSr7guLYcvr8Y9qj
  Height = 300
  HorizontalArea = 0
  IfcData = IfcUID=1E5ZyhmSr7guLYcvr8Y9qj; attributes={"GlobalId": {"value": "1E5ZyhmSr7guLYcvr8Y9qj"}}
  IfcType = 166
  Joint = 0
  Length = 9430
  MakeBlocks = true
  Material = -> Material018
  MoveBase = false
  MoveWithHost = false
  Normal = (0,0,0)
  OffsetFirst = 0
  OffsetSecond = 105
  PerimeterLength = 0
  Placement = pos=(0,0,-200) rot=(0,0,1;0rad)
  PredefinedType = 0
  VerticalArea = 0
  Width = 110
FEATURE [Part::Part2DObjectPython] Line2273  label="облицовка_стены_039"  # Draft 2D object (typed FeaturePython)
  ChamferSize = 0
  Closed = true
  End = (11160,8955,0)
  FilletRadius = 0
  Length = 9540
  MakeFace = false
  Placement = pos=(12865,4225,0) rot=(0,0,1;0rad)
  Points = (2) [(-1705,-4810,0),(-1705,4730,0)]
  Start = (11160,-585,0)
  Subdivisions = 0
FEATURE [Part::FeaturePython] Wall630  label="Облицовка цоколя (камень бетонный СКЦ2Л-24) 033"  # Arch/BIM 166 (typed FeaturePython)
  Align = 1
  Area = 2862000
  Base = -> Line2273
  BlockHeight = 75
  BlockLength = 210
  CountBroken = 6
  CountEntire = 178
  Face = 0
  GlobalId = 0Qqq80WcDAy9cO4W0cQ$pL
  Height = 300
  HorizontalArea = 0
  IfcData = IfcUID=0Qqq80WcDAy9cO4W0cQ$pL; attributes={"GlobalId": {"value": "0Qqq80WcDAy9cO4W0cQ$pL"}}
  IfcType = 166
  Joint = 0
  Length = 9540
  MakeBlocks = true
  Material = -> Material018
  MoveBase = false
  MoveWithHost = false
  Normal = (0,0,0)
  OffsetFirst = 0
  OffsetSecond = 105
  PerimeterLength = 0
  Placement = pos=(0,0,-200) rot=(0,0,1;0rad)
  PredefinedType = 0
  VerticalArea = 0
  Width = 110
FEATURE [Part::Part2DObjectPython] Rectangle4217  label="четверть_183-008"  # Draft 2D object (typed FeaturePython)
  ChamferSize = 0
  Columns = 1
  FilletRadius = 0
  Height = 200
  Length = 1310
  MakeFace = true
  Placement = pos=(5940,-425,0) rot=(0,0,1;3.14159rad)
  Rows = 1
FEATURE [Part::FeaturePython] Structure695003007008  label="Проём_входн_060"  # Arch/BIM 52 (typed FeaturePython)
  Base = -> Rectangle4217
  FaceMaker = 0
  Height = 2535
  HorizontalArea = 262000
  IfcData = complex_attributes={"OwnerHistory": {}, "IsNestedBy": {}, "IsDecomposedBy": {}, "IsDefinedBy": {}, "ObjectPlacement": {}, "Representation":... (+4 chars omitted)
  IfcType = 52
  Length = 0
  MoveBase = false
  MoveWithHost = false
  Nodes = (2) [(5775,-395,0),(5775,-395,2335)]
  NodesOffset = 0
  Normal = (0,0,0)
  PerimeterLength = 3020
  Placement = pos=(0,0,-40) rot=(0,0,1;0rad)
  VerticalArea = 7655700
  Width = 100
FEATURE [Part::FeaturePython] Wall629  label="Облицовка цоколя (камень бетонный СКЦ2Л-24) 032"  # Arch/BIM 166 (typed FeaturePython)
  Align = 0
  Area = 3459000
  Base = -> Line2271
  BlockHeight = 75
  BlockLength = 210
  CountBroken = 15
  CountEntire = 201
  Face = 0
  GlobalId = 1TP$vjbOv5ffUx0fDKfugP
  Height = 300
  HorizontalArea = 0
  IfcData = IfcUID=1TP$vjbOv5ffUx0fDKfugP; attributes={"GlobalId": {"value": "1TP$vjbOv5ffUx0fDKfugP"}}
  IfcType = 166
  Joint = 0
  Length = 11530
  MakeBlocks = true
  Material = -> Material018
  MoveBase = false
  MoveWithHost = false
  Normal = (0,0,0)
  OffsetFirst = 0
  OffsetSecond = 105
  PerimeterLength = 0
  Placement = pos=(0,0,-200) rot=(0,0,1;0rad)
  PredefinedType = 0
  Subtractions = -> [Structure695003007008]
  VerticalArea = 0
  Width = 110
FEATURE [Part::Part2DObjectPython] Rectangle4218  label="четверть_790-012"  # Draft 2D object (typed FeaturePython)
  ChamferSize = 0
  Columns = 1
  FilletRadius = 0
  Height = 200
  Length = 1830
  MakeFace = true
  Placement = pos=(7490,8795,0) rot=(0,0,1;0rad)
  Rows = 1
FEATURE [Part::FeaturePython] Structure695003007009  label="Проём_терасс._061"  # Arch/BIM 52 (typed FeaturePython)
  Base = -> Rectangle4218
  FaceMaker = 0
  Height = 2535
  HorizontalArea = 366000
  IfcData = complex_attributes={"OwnerHistory": {}, "IsNestedBy": {}, "IsDecomposedBy": {}, "IsDefinedBy": {}, "ObjectPlacement": {}, "Representation":... (+4 chars omitted)
  IfcType = 52
  Length = 0
  MoveBase = false
  MoveWithHost = false
  Nodes = (2) [(5775,-395,0),(5775,-395,2335)]
  NodesOffset = 0
  Normal = (0,0,0)
  PerimeterLength = 4060
  Placement = pos=(0,0,-40) rot=(0,0,1;0rad)
  VerticalArea = 1.02921e+07
  Width = 100
FEATURE [Part::FeaturePython] Wall310  label="Отлив (вибропресс. бордюрный камень 1000х200х80мм)"  # Arch/BIM 166 (typed FeaturePython)
  Align = 1
  Area = 3304000
  Base = -> Wire890
  BlockHeight = 80
  BlockLength = 1000
  CountBroken = 4
  CountEntire = 39
  Face = 0
  Height = 80
  HorizontalArea = 7.792e+06
  IfcData = attributes={"GlobalId": {"name": "GlobalId", "type": "IfcGloballyUniqueId", "is_enum": false, "enum_values": []}, "Description": {"... (+533 chars omitted),+1 more (map truncated)
  IfcType = 166
  Joint = 0
  Length = 41300
  MakeBlocks = false
  Material = -> Material018
  MoveBase = false
  MoveWithHost = false
  Normal = (0,0,0)
  OffsetFirst = 0
  OffsetSecond = 0
  PerimeterLength = 80940
  Placement = pos=(0,0,100) rot=(0,0,1;0rad)
  PredefinedType = 0
  Subtractions = -> [Structure695003007009,Structure695003007008]
  VerticalArea = 6297600
  Width = 200
FEATURE [Part::FeaturePython] Wall311  label="Утепление цоколя XPS 50mm"  # Arch/BIM 166 (typed FeaturePython)
  Align = 1
  Area = 11977000
  Base = -> Wire890
  BlockHeight = 80
  BlockLength = 1000
  CountBroken = 4
  CountEntire = 39
  Face = 0
  Height = 290
  HorizontalArea = 2075000
  IfcData = attributes={"GlobalId": {"name": "GlobalId", "type": "IfcGloballyUniqueId", "is_enum": false, "enum_values": []}, "Description": {"... (+533 chars omitted),+1 more (map truncated)
  IfcType = 166
  Joint = 0
  Length = 41300
  MakeBlocks = false
  Material = -> Material002
  MoveBase = false
  MoveWithHost = false
  Normal = (0,0,1)
  OffsetFirst = 0
  OffsetSecond = 0
  PerimeterLength = 41700
  Placement = pos=(0,0,-200) rot=(0,0,1;0rad)
  PredefinedType = 0
  Subtractions = -> [Structure695003007009,Structure695003007008]
  VerticalArea = 23279600
  Width = 50
FEATURE [Part::FeaturePython] Wall631  label="Облицовка цоколя (камень бетонный СКЦ2Л-24) 034"  # Arch/BIM 166 (typed FeaturePython)
  Align = 0
  Area = 3492000
  Base = -> Line2270
  BlockHeight = 75
  BlockLength = 210
  CountBroken = 18
  CountEntire = 198
  Face = 0
  GlobalId = 0a9Ful3VXDtwee5LreBW$T
  Height = 300
  HorizontalArea = 0
  IfcData = IfcUID=0a9Ful3VXDtwee5LreBW$T; attributes={"GlobalId": {"value": "0a9Ful3VXDtwee5LreBW$T"}}
  IfcType = 166
  Joint = 0
  Length = 11640
  MakeBlocks = true
  Material = -> Material018
  MoveBase = false
  MoveWithHost = false
  Normal = (0,0,0)
  OffsetFirst = 0
  OffsetSecond = 105
  PerimeterLength = 0
  Placement = pos=(0,0,-200) rot=(0,0,1;0rad)
  PredefinedType = 0
  Subtractions = -> [Structure695003007009]
  VerticalArea = 0
  Width = 110
FEATURE [Part::Part2DObjectPython] Rectangle4219  # Draft 2D object (typed FeaturePython)
  Area = 0
  ChamferSize = 0
  Columns = 1
  FilletRadius = 0
  Height = 1000
  Length = 260
  MakeFace = false
  Placement = pos=(7095,7395,0) rot=(0,0,1;0rad)
  Rows = 1
FEATURE [Part::Part2DObjectPython] Wire1095  # Draft 2D object (typed FeaturePython)
  Area = 0
  ChamferSize = 0
  Closed = true
  End = (6835,7135,0)
  FilletRadius = 0
  Length = 2533.86
  MakeFace = false
  Placement = pos=(5835,7135,0) rot=(0,0,1;0rad)
  Points = (4) [(0,0,0),(0,343.39,0),(1000,176.672,0),(1000,0,0)]
  Start = (5835,7135,0)
  Subdivisions = 0
FEATURE [Part::FeaturePython] Structure695003007012  label="Структура064"  # Arch/BIM 172 (typed FeaturePython)
  Base = -> Wire1095
  FaceMaker = 0
  Height = 1110
  HorizontalArea = 260031
  IfcData = attributes={"GlobalId": {"name": "GlobalId", "type": "IfcGloballyUniqueId", "is_enum": false, "enum_values": []}, "Description": {"... (+484 chars omitted),+1 more (map truncated)
  IfcType = 172
  Length = 0
  MoveBase = false
  MoveWithHost = false
  Nodes = (2) [(6281.57,7269.47,0),(6281.57,7269.47,1110)]
  NodesOffset = 0
  Normal = (0,0,1)
  PerimeterLength = 2533.86
  PredefinedType = 0
  VerticalArea = 2.81259e+06
  Width = 100
FEATURE [Part::FeaturePython] Stairs001  # Arch/BIM 128 (typed FeaturePython)
  AbsTop = (0,0,2220)
  Align = 0
  BlondelRatio = 0
  Flight = 0
  Height = 3000
  HorizontalArea = 0
  IfcData = attributes={"GlobalId": {"name": "GlobalId", "type": "IfcGloballyUniqueId", "is_enum": false, "enum_values": []}, "Description": {"... (+760 chars omitted),+1 more (map truncated)
  IfcType = 128
  LandingDepth = 0
  Landings = 0
  Length = 4500
  MoveBase = false
  MoveWithHost = false
  Nosing = 0
  NumberOfSteps = 12
  OutlineLeft = (2) [(0,-60,1085),(2860,-60,3120)]
  OutlineLeftAll = (2) [(0,-60,1085),(2860,-60,3120)]
  OutlineRight = (2) [(2860,-940,3120),(0,-940,1085)]
  OutlineRightAll = (2) [(2860,-940,3120),(0,-940,1085)]
  PerimeterLength = 0
  Placement = pos=(6835,7135,1110) rot=(0,0,-1;1.5708rad)
  PredefinedType = 0
  RailingHeightLeft = 900
  RailingHeightRight = 900
  RailingLeft = Rail
  RailingOffsetLeft = 60
  RailingOffsetRight = 60
  RailingRight = Rail001
  RiserHeight = 185
  RiserHeightEnforce = 185
  RiserThickness = 0
  StringerOverlap = 0
  StringerWidth = 0
  Structure = 1
  StructureOffset = 0
  StructureThickness = 150
  TreadDepth = 260
  TreadDepthEnforce = 260
  TreadThickness = 0
  VerticalArea = 0
  Width = 1000
  Winders = 0
FEATURE [Part::Part2DObjectPython] Wire1097  # Draft 2D object (typed FeaturePython)
  Area = 0
  ChamferSize = 0
  Closed = true
  End = (6918.33,7395,0)
  FilletRadius = 0
  Length = 2800.12
  MakeFace = false
  Placement = pos=(6869.22,7395,0) rot=(0,0,1;0rad)
  Points = (4) [(0,0,0),(-657.835,1000,0),(-117.607,1000,0),(49.1116,0,0)]
  Start = (6869.22,7395,0)
  Subdivisions = 0
FEATURE [Part::Part2DObjectPython] Wire1098  # Draft 2D object (typed FeaturePython)
  Area = 0
  ChamferSize = 0
  Closed = true
  End = (7095,7395,0)
  FilletRadius = 0
  Length = 2533.86
  MakeFace = false
  Placement = pos=(6918.33,7395,0) rot=(0,0,1;0rad)
  Points = (4) [(0,0,0),(-166.718,1000,0),(176.672,1000,0),(176.672,0,0)]
  Start = (6918.33,7395,0)
  Subdivisions = 0
FEATURE [Part::FeaturePython] Structure695003007013  label="Структура065"  # Arch/BIM 172 (typed FeaturePython)
  Base = -> Wire1098
  FaceMaker = 0
  Height = 370
  HorizontalArea = 260031
  IfcData = attributes={"GlobalId": {"name": "GlobalId", "type": "IfcGloballyUniqueId", "is_enum": false, "enum_values": []}, "Description": {"... (+484 chars omitted),+1 more (map truncated)
  IfcType = 172
  Length = 0
  MoveBase = false
  MoveWithHost = false
  Nodes = (2) [(6960.53,7948.43,0),(6960.53,7948.43,370)]
  NodesOffset = 0
  Normal = (0,0,1)
  PerimeterLength = 2533.86
  PredefinedType = 0
  VerticalArea = 937530
  Width = 100
FEATURE [Part::Part2DObjectPython] Wire1099  # Draft 2D object (typed FeaturePython)
  Area = 0
  ChamferSize = 0
  Closed = true
  End = (6835,7360.78,0)
  FilletRadius = 0
  Length = 3195.1
  MakeFace = false
  Placement = pos=(5835,8018.62,0) rot=(0,0,1;0rad)
  Points = (5) [(0,0,0),(0,376.382,0),(376.382,376.382,0),(1034.22,-623.618,0),(1000,-657.835,0)]
  Start = (5835,8018.62,0)
  Subdivisions = 0
FEATURE [Part::FeaturePython] Structure695003007011  label="Структура063"  # Arch/BIM 172 (typed FeaturePython)
  Base = -> Wire1099
  FaceMaker = 0
  Height = 740
  HorizontalArea = 411184
  IfcData = attributes={"GlobalId": {"name": "GlobalId", "type": "IfcGloballyUniqueId", "is_enum": false, "enum_values": []}, "Description": {"... (+484 chars omitted),+1 more (map truncated)
  IfcType = 172
  Length = 0
  MoveBase = false
  MoveWithHost = false
  Nodes = (2) [(6260.15,7969.85,0),(6260.15,7969.85,740)]
  NodesOffset = 0
  Normal = (0,0,1)
  PerimeterLength = 3195.1
  PredefinedType = 0
  VerticalArea = 2.36437e+06
  Width = 100
FEATURE [Part::FeaturePython] Structure695003007017  label="Структура069"  # Arch/BIM 172 (typed FeaturePython)
  Base = -> Wire1097
  FaceMaker = 0
  Height = 555
  HorizontalArea = 294670
  IfcData = attributes={"GlobalId": {"name": "GlobalId", "type": "IfcGloballyUniqueId", "is_enum": false, "enum_values": []}, "Description": {"... (+484 chars omitted),+1 more (map truncated)
  IfcType = 172
  Length = 0
  MoveBase = false
  MoveWithHost = false
  Nodes = (2) [(6630.37,8033.89,0),(6630.37,8033.89,555)]
  NodesOffset = 0
  Normal = (0,0,1)
  PerimeterLength = 2800.12
  PredefinedType = 0
  VerticalArea = 1.55406e+06
  Width = 100
FEATURE [Part::Part2DObjectPython] Wire1100  # Draft 2D object (typed FeaturePython)
  Area = 0
  ChamferSize = 0
  Closed = true
  End = (6835,7311.67,0)
  FilletRadius = 0
  Length = 2800.12
  MakeFace = false
  Placement = pos=(5835,7478.39,0) rot=(0,0,1;0rad)
  Points = (4) [(0,0,0),(0,540.228,0),(1000,-117.607,0),(1000,-166.718,0)]
  Start = (5835,7478.39,0)
  Subdivisions = 0
FEATURE [Part::FeaturePython] Structure695003007018  label="Структура070"  # Arch/BIM 172 (typed FeaturePython)
  Base = -> Wire1100
  FaceMaker = 0
  Height = 925
  HorizontalArea = 294670
  IfcData = attributes={"GlobalId": {"name": "GlobalId", "type": "IfcGloballyUniqueId", "is_enum": false, "enum_values": []}, "Description": {"... (+484 chars omitted),+1 more (map truncated)
  IfcType = 172
  Length = 0
  MoveBase = false
  MoveWithHost = false
  Nodes = (2) [(6196.11,7599.63,0),(6196.11,7599.63,925)]
  NodesOffset = 0
  Normal = (0,0,1)
  PerimeterLength = 2800.12
  PredefinedType = 0
  VerticalArea = 2.59011e+06
  Width = 100
FEATURE [Part::Part2DObjectPython] Rectangle4221  # Draft 2D object (typed FeaturePython)
  Area = 0
  ChamferSize = 0
  Columns = 1
  FilletRadius = 0
  Height = 260
  Length = 1000
  MakeFace = false
  Placement = pos=(5835,6875,0) rot=(0,0,1;0rad)
  Rows = 1
FEATURE [Part::FeaturePython] Structure695003007014  label="Структура066"  # Arch/BIM 172 (typed FeaturePython)
  Base = -> Rectangle4221
  FaceMaker = 0
  Height = 1295
  HorizontalArea = 260000
  IfcData = attributes={"GlobalId": {"name": "GlobalId", "type": "IfcGloballyUniqueId", "is_enum": false, "enum_values": []}, "Description": {"... (+484 chars omitted),+1 more (map truncated)
  IfcType = 172
  Length = 0
  MoveBase = false
  MoveWithHost = false
  Nodes = (2) [(6335,7005,0),(6335,7005,1295)]
  NodesOffset = 0
  Normal = (0,0,0)
  PerimeterLength = 2520
  PredefinedType = 0
  VerticalArea = 3.2634e+06
  Width = 100
FEATURE [Part::FeaturePython] Structure695003007024  label="Структура076"  # Arch/BIM 172 (typed FeaturePython)
  Base = -> Rectangle4219
  FaceMaker = 0
  Height = 185
  HorizontalArea = 260000
  IfcData = attributes={"GlobalId": {"name": "GlobalId", "type": "IfcGloballyUniqueId", "is_enum": false, "enum_values": []}, "Description": {"... (+484 chars omitted),+1 more (map truncated)
  IfcType = 172
  Length = 0
  MoveBase = false
  MoveWithHost = false
  Nodes = (2) [(7225,7895,0),(7225,7895,185)]
  NodesOffset = 0
  Normal = (0,0,0)
  PerimeterLength = 2520
  PredefinedType = 0
  VerticalArea = 466200
  Width = 100
FEATURE [Part::Compound] Compound006042005  label="Лестница вар.#2 001"
  Links = -> [Structure695003007011,Structure695003007012,Structure695003007013,Structure695003007014,Structure695003007017,Structure695003007018,Structure695003007024,Stairs001]
FEATURE [Part::Feature] Compound006042005001  label="Лестница вар.#2 002"
  shape: bbox 1520 x 4120 x 3145 mm, 70 faces, 8 solids (baked)
FEATURE [Part::FeaturePython] Component241071  label="Лестница вар.#2 003"  # Arch/BIM 0 (typed FeaturePython)
  Base = -> Compound006042005001
  HorizontalArea = 0
  IfcData = attributes={"GlobalId": {"name": "GlobalId", "type": "IfcGloballyUniqueId", "is_enum": false, "enum_values": []}, "Description": {"... (+538 chars omitted),+1 more (map truncated)
  IfcType = 0
  Material = -> Material018
  MoveBase = false
  MoveWithHost = false
  PerimeterLength = 0
  PredefinedType = 0
  VerticalArea = 0
FEATURE [App::GeometryPython] BuildingPart131  label="Лестница забежная"  # Arch/BIM 172 (typed FeaturePython)
  Area = 0
  Group = -> [Component241071]
  Height = 0
  HeightPropagate = true
  IfcData = attributes={"GlobalId": {"name": "GlobalId", "type": "IfcGloballyUniqueId", "is_enum": false, "enum_values": []}, "Description": {"... (+484 chars omitted),+1 more (map truncated)
  IfcType = 172
  LevelOffset = 0
  PredefinedType = 0
FEATURE [Part::FeaturePython] Structure695003007025  label="Проём-инсталляция-003"  # Arch/BIM 52 (typed FeaturePython)
  Base = -> Rectangle3999
  FaceMaker = 0
  Height = 1200
  HorizontalArea = 51600
  IfcData = complex_attributes={"OwnerHistory": {}, "IsNestedBy": {}, "IsDecomposedBy": {}, "IsDefinedBy": {}, "ObjectPlacement": {}, "Representation":... (+4 chars omitted)
  IfcType = 52
  Length = 0
  MoveBase = false
  MoveWithHost = false
  Nodes = (2) [(13000,6050,0),(13000,6050,2180)]
  NodesOffset = 0
  Normal = (0,0,0)
  PerimeterLength = 1450
  Placement = pos=(0,0,-20) rot=(0,0,1;0rad)
  VerticalArea = 1740000
  Width = 100
FEATURE [App::GeometryPython] BuildingPart001  label="проёмы"  # Arch/BIM 52 (typed FeaturePython)
  Area = 0
  Group = -> [Structure020,Structure021,Structure023,Structure024,Structure026,Structure148,Structure317,Structure350,Structure421,Structure422,Structure432,Structure431,Structure430,Structure426,Structure428,Structure489,Structure360,Structure543,Structure550,Structure560,Structure564,Structure559,Structure558,Structure576,Structure578,Structure577,Structure651,Structure650,Structure649,Structure647,+12 more]
  Height = 0
  HeightPropagate = true
  IfcData = complex_attributes={"OwnerHistory": {}, "IsNestedBy": {}, "IsDecomposedBy": {}, "IsDefinedBy": {}, "ObjectPlacement": {}, "Representation":... (+4 chars omitted)
  IfcType = 52
  LevelOffset = 0
FEATURE [Part::FeaturePython] Wall419  label="перегородка (сил.блок 500х250х80) 012"  # Arch/BIM 166 (typed FeaturePython)
  Align = 2
  Area = 8.46e+06
  Base = -> Line1906
  BlockHeight = 250
  BlockLength = 0
  CountBroken = 0
  CountEntire = 0
  Face = 0
  GlobalId = 1OB118XG9DJPL5jtZdDHzR
  Height = 3000
  HorizontalArea = 277200
  IfcData = IfcUID=1OB118XG9DJPL5jtZdDHzR; attributes={"GlobalId": {"value": "1OB118XG9DJPL5jtZdDHzR"}}
  IfcType = 166
  Joint = 0
  Length = 2820
  MakeBlocks = false
  Material = -> Material009
  MoveBase = false
  MoveWithHost = false
  Normal = (0,0,0)
  OffsetFirst = 300
  OffsetSecond = 50
  PerimeterLength = 5800
  Placement = pos=(0,0,-200) rot=(0,0,1;0rad)
  PredefinedType = 0
  Subtractions = -> [Structure695003007025]
  VerticalArea = 1.6044e+07
  Width = 80
FEATURE [App::GeometryPython] BuildingPart005  label="Перегородки"  # Arch/BIM 52 (typed FeaturePython)
  Area = 6.53766e+07
  GlobalId = 2hzWGr02f4ewnrclJv7BWz
  Group = -> [Wall186,Wall128,Wall223,Wall231,Wall230,Wall225,Wall187,Wall188,Wall162,Wall402,Wall222,Wall416,Wall417,Wall419,Wall420]
  Height = 0
  HeightPropagate = true
  IfcData = IfcUID=2hzWGr02f4ewnrclJv7BWz,attributes={"GlobalId": {"value": "2hzWGr02f4ewnrclJv7BWz"}},+1 more (map truncated)
  IfcType = 52
  LevelOffset = 0
FEATURE [Part::FeaturePython] Wall  label="Штукатурка 20мм 008"  # Arch/BIM 166 (typed FeaturePython)
  Align = 1
  Area = 8.1704e+07
  Base = -> Wire1066
  BlockHeight = 0
  BlockLength = 0
  CountBroken = 0
  CountEntire = 0
  Face = 0
  GlobalId = 0h0Qmcrjb7bRq5SNTtGOK3
  Height = 2800
  HorizontalArea = 0
  IfcData = IfcUID=0h0Qmcrjb7bRq5SNTtGOK3,+2 more (map truncated)
  IfcType = 166
  Joint = 0
  Length = 29180
  MakeBlocks = false
  Material = -> Material008
  MoveBase = false
  MoveWithHost = false
  Normal = (0,0,0)
  OffsetFirst = 0
  OffsetSecond = 0
  PerimeterLength = 0
  PredefinedType = 0
  Subtractions = -> [Structure317,Structure649,Structure666,Structure026,Structure021,Structure024,Wall564,Wall402,Wall186,Wall222,Structure647,Structure546,Wall420,Wall419]
  VerticalArea = 0
  Width = 20
FEATURE [Part::Part2DObjectPython] Line2274  # Draft 2D object (typed FeaturePython)
  ChamferSize = 0
  Closed = true
  End = (5780,5575,0)
  FilletRadius = 0
  Length = 1040
  MakeFace = false
  Placement = pos=(6660,5505,0) rot=(0,0,1;0rad)
  Points = (2) [(-880,-970,0),(-880,70,0)]
  Start = (5780,4535,0)
  Subdivisions = 0
FEATURE [Part::FeaturePython] Wall587002  label="Отделка над проёмом"  # Arch/BIM 166 (typed FeaturePython)
  Align = 2
  Area = 728000
  Base = -> Line2274
  BlockHeight = 250
  BlockLength = 0
  CountBroken = 0
  CountEntire = 0
  Face = 0
  Height = 700
  HorizontalArea = 114400
  IfcType = 166
  Joint = 0
  Length = 1040
  MakeBlocks = false
  Material = -> Material005
  MoveBase = false
  MoveWithHost = false
  Normal = (0,0,0)
  OffsetFirst = 0
  OffsetSecond = 300
  PerimeterLength = 2300
  Placement = pos=(0,0,2100) rot=(0,0,1;0rad)
  PredefinedType = 0
  VerticalArea = 1.61e+06
  Width = 110
FEATURE [Part::FeaturePython] Wall403  label="Покрытие ванная плиткой 20мм001"  # Arch/BIM 166 (typed FeaturePython)
  Additions = -> [Wall587002]
  Align = 1
  Area = 4.2952e+07
  Base = -> Wire1062
  BlockHeight = 0
  BlockLength = 0
  CountBroken = 0
  CountEntire = 0
  Face = 0
  GlobalId = 0fSn5rz2v1yx1CM9t4dxRk
  Height = 2800
  HorizontalArea = 0
  IfcData = IfcUID=0fSn5rz2v1yx1CM9t4dxRk,+2 more (map truncated)
  IfcType = 166
  Joint = 0
  Length = 15340
  MakeBlocks = false
  Material = -> Material005
  MoveBase = false
  MoveWithHost = false
  Normal = (0,0,0)
  OffsetFirst = 0
  OffsetSecond = 0
  PerimeterLength = 0
  PredefinedType = 0
  Subtractions = -> [Structure546,Structure026,Structure023,Structure643,Structure650]
  VerticalArea = 0
  Width = 20
FEATURE [Part::Part2DObjectPython] Wire1101  # Draft 2D object (typed FeaturePython)
  Area = 1.44e+06
  ChamferSize = 0
  Closed = true
  End = (4925,8395,0)
  FilletRadius = 0
  Length = 5200
  MakeFace = true
  Placement = pos=(5595,9270,0) rot=(0,0,1;3.14159rad)
  Points = (4) [(-130,875,0),(-130,2675,0),(670,2675,0),(670,875,0)]
  Start = (5725,8395,0)
  Subdivisions = 0
FEATURE [Part::Part2DObjectPython] Rectangle4222  # Draft 2D object (typed FeaturePython)
  Area = 0
  ChamferSize = 0
  Columns = 1
  FilletRadius = 75
  Height = 620
  Length = 235
  MakeFace = false
  Placement = pos=(6935,1132.5,0) rot=(0,0,1;1.5708rad)
  Rows = 1
FEATURE [Part::Part2DObjectPython] Rectangle4223  label="Раковина «Cersanit» Moduo 80 Slim_004"  # Draft 2D object (typed FeaturePython)
  Area = 312000
  ChamferSize = 0
  Columns = 1
  FilletRadius = 0
  Height = 390
  Length = 800
  MakeFace = true
  Placement = pos=(7025,1465,0) rot=(0,0,1;3.14159rad)
  Rows = 1
FEATURE [Part::FeaturePython] Structure695003007026  label="Структура077"  # Arch/BIM 52 (typed FeaturePython)
  Base = -> Rectangle4222
  FaceMaker = 0
  Height = 100
  HorizontalArea = 140871
  IfcData = attributes={"GlobalId": {"name": "GlobalId", "type": "IfcGloballyUniqueId", "is_enum": false, "enum_values": []}, "Description": {"... (+484 chars omitted),+1 more (map truncated)
  IfcType = 52
  Length = 0
  MoveBase = false
  MoveWithHost = false
  Nodes = (2) [(6380,5325,0),(6380,5325,100)]
  NodesOffset = 0
  Normal = (0,0,1)
  PerimeterLength = 1581.24
  Placement = pos=(0,0,800) rot=(0,0,1;0rad)
  VerticalArea = 158124
  Width = 100
FEATURE [Part::FeaturePython] Structure695003007027  label="Раковина Cersanit Moduo 80 S-UM-MOD80SL/1 002"  # Arch/BIM 52 (typed FeaturePython)
  Base = -> Rectangle4223
  FaceMaker = 0
  GlobalId = 2d5W_OQQf2Fxkoe6wMEOb9
  Height = 55
  HorizontalArea = 171129
  IfcData = IfcUID=2d5W_OQQf2Fxkoe6wMEOb9,+2 more (map truncated)
  IfcType = 52
  Length = 0
  Material = -> Material013
  MoveBase = false
  MoveWithHost = false
  Nodes = (2) [(-2856.79,7112.64,0),(-2856.79,7112.64,600)]
  NodesOffset = 0
  Normal = (0,0,1)
  PerimeterLength = 2380
  Placement = pos=(0,0,845) rot=(0,0,1;0rad)
  Subtractions = -> [Structure695003007026]
  VerticalArea = 217868
  Width = 100
FEATURE [Part::FeaturePython] Structure695003007028  label="Раковина «Cersanit» Moduo 80 Slim (тумба)002"  # Arch/BIM 52 (typed FeaturePython)
  Base = -> Rectangle4223
  FaceMaker = 0
  GlobalId = 2d5W_OQQf2Fxkoe6wMEOb9
  Height = 570
  HorizontalArea = 312000
  IfcData = IfcUID=2d5W_OQQf2Fxkoe6wMEOb9,+2 more (map truncated)
  IfcType = 52
  Length = 0
  Material = -> Material013
  MoveBase = false
  MoveWithHost = false
  Nodes = (2) [(-2856.79,7112.64,0),(-2856.79,7112.64,600)]
  NodesOffset = 0
  Normal = (0,0,-1)
  PerimeterLength = 2380
  Placement = pos=(0,0,845) rot=(0,0,1;0rad)
  VerticalArea = 1356600
  Width = 100
FEATURE [App::GeometryPython] BuildingPart048  label="Сантехника и мебель в ванной"  # Arch/BIM 52 (typed FeaturePython)
  Area = 2.964e+06
  GlobalId = 2oHchfV$vBmBbFkTdd7Thp
  Group = -> [Structure343,Wall240,Component170,Structure477,Structure478,Structure483,Structure484,Component183,Structure663,Structure664,Structure665,Structure695003007027,Structure695003007028]
  Height = 0
  HeightPropagate = true
  IfcData = IfcUID=2oHchfV$vBmBbFkTdd7Thp,attributes={"GlobalId": {"value": "2oHchfV$vBmBbFkTdd7Thp"}},+1 more (map truncated)
  IfcType = 52
  LevelOffset = 0
FEATURE [App::GeometryPython] BuildingPart049  label="Обстановка"  # Arch/BIM 52 (typed FeaturePython)
  Area = 2.964e+06
  GlobalId = 01a0HsyVr7nurh2jl2zfI$
  Group = -> [BuildingPart047,BuildingPart048,BuildingPart045]
  Height = 0
  HeightPropagate = true
  IfcData = IfcUID=01a0HsyVr7nurh2jl2zfI$,attributes={"GlobalId": {"value": "01a0HsyVr7nurh2jl2zfI$"}},+1 more (map truncated)
  IfcType = 52
  LevelOffset = 0
FEATURE [Part::Cut] Cut105003010  label="roof_2_side_005"
  Base = -> Cut105003004
  Tool = -> Roof035
FEATURE [App::GeometryPython] BuildingPart019  label="Ненужное"  # Arch/BIM 52 (typed FeaturePython)
  Area = 14455000
  Group = -> [Structure044,BuildingPart138,Structure133,Structure695003,Structure695,Structure693,Wall312,Component241023,Compound006042005,Cut105003010,Component241033,Component241032,Component241039]
  Height = 0
  HeightPropagate = true
  IfcData = complex_attributes={"OwnerHistory": {}, "IsNestedBy": {}, "IsDecomposedBy": {}, "IsDefinedBy": {}, "ObjectPlacement": {}, "Representation":... (+4 chars omitted)
  IfcType = 52
  LevelOffset = 0
FEATURE [Part::Cut] Cut105003022002  label="roof_4_side_004"
  Base = -> Cut105003003
  Tool = -> Extrude099005015
FEATURE [Part::Part2DObjectPython] Line2275  # Draft 2D object (typed FeaturePython)
  Area = 0
  ChamferSize = 0
  Closed = false
  End = (7589.53,4185,0)
  FilletRadius = 0
  Length = 4609.06
  MakeFace = false
  Placement = pos=(2980.47,4185,0) rot=(0,0,1;0rad)
  Points = (2) [(0,0,0),(4609.06,9.09495e-13,0)]
  Start = (2980.47,4185,0)
  Subdivisions = 0
FEATURE [Part::Part2DObjectPython] Line2276  # Draft 2D object (typed FeaturePython)
  Area = 0
  ChamferSize = 0
  Closed = false
  End = (5285,7000,0)
  FilletRadius = 0
  Length = 2815
  MakeFace = false
  Placement = pos=(5285,4185,0) rot=(0,0,1;0rad)
  Points = (2) [(0,0,0),(0,2815,0)]
  Start = (5285,4185,0)
  Subdivisions = 0
FEATURE [App::DocumentObjectGroup] Draft_Construction  label="Construction"
  Group = -> [Rectangle3159,Line1465,Rectangle3284,Line1478,Line1626,Rectangle3463,Line2230,Line2231,Line2232,Line2233,Line2234,Line2276,Line2275]
FEATURE [Sketcher::SketchObject] Sketch430
  FullyConstrained = true
  Placement = pos=(10155.1,4585,5307) rot=(0,1,0;0.785398rad)
  sketch-geometry (8):
    g0: LineSegment StartX=0 StartY=0 StartZ=0 EndX=1180 EndY=0 EndZ=0
    g1: LineSegment StartX=1180 StartY=0 StartZ=0 EndX=1180 EndY=660 EndZ=0
    g2: LineSegment StartX=1180 StartY=660 StartZ=0 EndX=0 EndY=660 EndZ=0
    g3: LineSegment StartX=0 StartY=660 StartZ=0 EndX=0 EndY=0 EndZ=0
    g4: LineSegment StartX=70 StartY=70 StartZ=0 EndX=1110 EndY=70 EndZ=0
    g5: LineSegment StartX=1110 StartY=70 StartZ=0 EndX=1110 EndY=590 EndZ=0
    g6: LineSegment StartX=1110 StartY=590 StartZ=0 EndX=70 EndY=590 EndZ=0
    g7: LineSegment StartX=70 StartY=590 StartZ=0 EndX=70 EndY=70 EndZ=0
  constraints (23):
    c: Coincident(g0,g1)
    c: Coincident(g1,g2)
    c: Coincident(g2,g3)
    c: Coincident(g3,g0)
    c: Horizontal(g0)
    c: Horizontal(g2)
    c: Vertical(g1)
    c: Vertical(g3)
    c: Coincident(g4,g5)
    c: Coincident(g5,g6)
    c: Coincident(g6,g7)
    c: Coincident(g7,g4)
    c: Horizontal(g4)
    c: Horizontal(g6)
    c: Vertical(g5)
    c: Vertical(g7)
    c: DistanceY(g1) = 660  'Height'
    c: DistanceX(g0) = 1180  'Width'
    c: DistanceY(g6,g2) = 70  'Frame1'
    c: DistanceX(g2,g6) = 70  'Frame2'
    c: DistanceX(g4,g0) = 70  'Frame3'
    c: DistanceY(g0,g4) = 70  'Frame4'
    c: Coincident(g0,g-1)
FEATURE [Part::FeaturePython] Window  label="Мансардное окно VELUX WhiteLine Дизайн GGU 0068, 660*1180 001"  # Arch/BIM 170 (typed FeaturePython)
  Area = 778800
  Base = -> Sketch430
  Frame = 70
  Height = 660
  HoleDepth = 0
  HoleWire = 0
  HorizontalArea = 0
  IfcData = attributes={"GlobalId": {"name": "GlobalId", "type": "IfcGloballyUniqueId", "is_enum": false, "enum_values": []}, "Description": {"... (+1230 chars omitted),+1 more (map truncated)
  IfcType = 170
  LouvreSpacing = 0
  LouvreWidth = 0
  Material = -> Material011
  MoveBase = false
  MoveWithHost = true
  Normal = (-0.669131,0,-0.743145)
  Opening = 0
  OverallHeight = 660
  OverallWidth = 1180
  PartitioningType = 0
  PerimeterLength = 0
  PredefinedType = 0
  Preset = 1
  SymbolElevation = false
  SymbolPlan = false
  VerticalArea = 0
  Width = 1180
  WindowParts = OuterFrame | Frame | Wire0,Wire1 | 115.0+V | 0.00+V | Glass | Glass panel | Wire1 | 15.0 | 75.0+V
  expr: OverallWidth = .Width.Value
  expr: OverallHeight = .Height.Value
FEATURE [Part::FeaturePython] Window116  label="Мансардное окно VELUX WhiteLine Дизайн GGU 0068, 660*1180 002"  # Arch/BIM 170 (typed FeaturePython)
  Area = 778800
  Base = -> Sketch430
  Frame = 70
  Height = 660
  HoleDepth = 0
  HoleWire = 0
  HorizontalArea = 0
  IfcData = attributes={"GlobalId": {"name": "GlobalId", "type": "IfcGloballyUniqueId", "is_enum": false, "enum_values": []}, "Description": {"... (+1230 chars omitted),+1 more (map truncated)
  IfcType = 170
  LouvreSpacing = 0
  LouvreWidth = 0
  Material = -> Material011
  MoveBase = false
  MoveWithHost = true
  Normal = (-0.669131,0,-0.743145)
  Opening = 0
  OverallHeight = 660
  OverallWidth = 1180
  PartitioningType = 0
  PerimeterLength = 0
  Placement = pos=(0,-1460,-9.09e-13) rot=(0,0,1;0rad)
  PredefinedType = 0
  Preset = 1
  SymbolElevation = false
  SymbolPlan = false
  VerticalArea = 0
  Width = 1180
  WindowParts = OuterFrame | Frame | Wire0,Wire1 | 115.0+V | 0.00+V | Glass | Glass panel | Wire1 | 15.0 | 75.0+V
  expr: OverallHeight = .Height.Value
  expr: OverallWidth = .Width.Value
FEATURE [Part::Extrusion] Extrude099005026  label="Габарит человека 007"
  Base = -> Sketch250
  Dir = (0,-1,2e-16)
  DirMode = 2
  FaceMakerClass = Part::FaceMakerBullseye
  LengthFwd = 290
  LengthRev = 0
  Placement = pos=(9541.38,3561.82,3145) rot=(0,0,1;1.5708rad)
  Solid = true
  Symmetric = false
FEATURE [App::GeometryPython] BuildingPart036  label="Эргономика"  # Arch/BIM 52 (typed FeaturePython)
  Area = 0
  GlobalId = 1U0bveIaj1buNClxqFBVzz
  Group = -> [Extrude007,Extrude008,Extrude012,Extrude022,Extrude099005019,Extrude099005026]
  Height = 0
  HeightPropagate = true
  IfcData = IfcUID=1U0bveIaj1buNClxqFBVzz,attributes={"GlobalId": {"value": "1U0bveIaj1buNClxqFBVzz"}},+1 more (map truncated)
  IfcType = 52
  LevelOffset = 0
FEATURE [Part::Part2DObjectPython] Rectangle4225  # Draft 2D object (typed FeaturePython)
  Area = 0
  ChamferSize = 0
  Columns = 1
  FilletRadius = 0
  Height = 3425
  Length = 5000
  MakeFace = false
  Placement = pos=(2785,-25,0) rot=(0,0,1;0rad)
  Rows = 1
FEATURE [Part::FeaturePython] Wall489  label="отделка кукушки 003"  # Arch/BIM 166 (typed FeaturePython)
  Align = 0
  Area = 58975000
  Base = -> Rectangle4225
  BlockHeight = 160
  BlockLength = 0
  CountBroken = 0
  CountEntire = 0
  Face = 0
  Height = 3500
  HorizontalArea = 0
  IfcData = attributes={"GlobalId": {"name": "GlobalId", "type": "IfcGloballyUniqueId", "is_enum": false, "enum_values": []}, "Description": {"... (+533 chars omitted),+1 more (map truncated)
  IfcType = 166
  Joint = 0
  Length = 16850
  MakeBlocks = true
  Material = -> Material007
  MoveBase = false
  MoveWithHost = false
  Normal = (0,0,0)
  Offset = 250
  OffsetFirst = 0
  OffsetSecond = 0
  PerimeterLength = 0
  Placement = pos=(0,0,3250) rot=(0,0,1;0rad)
  PredefinedType = 0
  Subtractions = -> [Structure577]
  VerticalArea = 0
  Width = 25
FEATURE [Part::FeaturePython] Wall490  label="утепление кукушки 004"  # Arch/BIM 166 (typed FeaturePython)
  Align = 0
  Area = 58975000
  Base = -> Rectangle4225
  BlockHeight = 0
  BlockLength = 0
  CountBroken = 0
  CountEntire = 0
  Face = 0
  Height = 3500
  HorizontalArea = 3.075e+06
  IfcData = attributes={"GlobalId": {"name": "GlobalId", "type": "IfcGloballyUniqueId", "is_enum": false, "enum_values": []}, "Description": {"... (+533 chars omitted),+1 more (map truncated)
  IfcType = 166
  Joint = 0
  Length = 16850
  MakeBlocks = false
  Material = -> Material020
  MoveBase = false
  MoveWithHost = false
  Normal = (0,0,0)
  Offset = 100
  OffsetFirst = 0
  OffsetSecond = 0
  PerimeterLength = 5580
  Placement = pos=(0,0,3150) rot=(0,0,1;0rad)
  PredefinedType = 0
  Subtractions = -> [Structure577,Structure578]
  VerticalArea = 1.24401e+08
  Width = 150
FEATURE [Part::MultiCommon] Common093  label="отделка кукушки 007"
  Shapes = -> [Roof036,Wall489]
FEATURE [Part::MultiCommon] Common094  label="утепление кукушки 005"
  Shapes = -> [Roof036,Wall490]
FEATURE [Part::Cut] Cut105003015  label="отделка кукушки 013"
  Base = -> Common093
  Tool = -> Extrude099005017
FEATURE [Part::Cut] Cut105003016  label="утепление кукушки 011"
  Base = -> Common094
  Tool = -> Extrude099005017
FEATURE [Part::FeaturePython] Component  label="отделка кукушки север 014"  # Arch/BIM 0 (typed FeaturePython)
  Base = -> Cut105003015
  HorizontalArea = 0
  IfcData = attributes={"GlobalId": {"name": "GlobalId", "type": "IfcGloballyUniqueId", "is_enum": false, "enum_values": []}, "Description": {"... (+538 chars omitted),+1 more (map truncated)
  IfcType = 0
  Material = -> Material007
  MoveBase = false
  MoveWithHost = false
  PerimeterLength = 0
  PredefinedType = 0
  VerticalArea = 0
FEATURE [Part::FeaturePython] Component241037  label="утепление кукушки север 012"  # Arch/BIM 0 (typed FeaturePython)
  Base = -> Cut105003016
  HorizontalArea = 0
  IfcData = attributes={"GlobalId": {"name": "GlobalId", "type": "IfcGloballyUniqueId", "is_enum": false, "enum_values": []}, "Description": {"... (+538 chars omitted),+1 more (map truncated)
  IfcType = 0
  Material = -> Material020
  MoveBase = false
  MoveWithHost = false
  PerimeterLength = 0
  PredefinedType = 0
  VerticalArea = 0
FEATURE [Part::Part2DObjectPython] Line2277  # Draft 2D object (typed FeaturePython)
  ChamferSize = 0
  Closed = true
  End = (4135,955,0)
  FilletRadius = 0
  Length = 1830
  MakeFace = false
  Placement = pos=(4205,2655,0) rot=(0,0,1;1.5708rad)
  Points = (2) [(130,70,0),(-1700,70,0)]
  Start = (4135,2785,0)
  Subdivisions = 0
FEATURE [Part::FeaturePython] Wall587003  label="перегородка 087"  # Arch/BIM 166 (typed FeaturePython)
  Align = 1
  Area = 6130500
  Base = -> Line2277
  BlockHeight = 250
  BlockLength = 0
  CountBroken = 0
  CountEntire = 0
  Face = 0
  Height = 3350
  HorizontalArea = 183000
  IfcType = 166
  Joint = 0
  Length = 1830
  MakeBlocks = false
  Material = -> Material008
  MoveBase = false
  MoveWithHost = false
  Normal = (0,0,0)
  OffsetFirst = 0
  OffsetSecond = 300
  PerimeterLength = 3860
  Placement = pos=(0,0,3145) rot=(0,0,1;0rad)
  PredefinedType = 0
  VerticalArea = 12931000
  Width = 100
FEATURE [Part::Part2DObjectPython] Line2278  # Draft 2D object (typed FeaturePython)
  ChamferSize = 0
  Closed = true
  End = (4235,855,0)
  FilletRadius = 0
  Length = 400
  MakeFace = false
  Placement = pos=(3355,925,0) rot=(0,0,1;3.14159rad)
  Points = (2) [(-480,70,0),(-880,70,0)]
  Start = (3835,855,0)
  Subdivisions = 0
FEATURE [Part::FeaturePython] Wall587004  label="перегородка 088"  # Arch/BIM 166 (typed FeaturePython)
  Align = 1
  Area = 1.34e+06
  Base = -> Line2278
  BlockHeight = 250
  BlockLength = 0
  CountBroken = 0
  CountEntire = 0
  Face = 0
  Height = 3350
  HorizontalArea = 40000
  IfcType = 166
  Joint = 0
  Length = 400
  MakeBlocks = false
  Material = -> Material008
  MoveBase = false
  MoveWithHost = false
  Normal = (0,0,0)
  OffsetFirst = 0
  OffsetSecond = 300
  PerimeterLength = 1000
  Placement = pos=(0,0,3145) rot=(0,0,1;0rad)
  PredefinedType = 0
  VerticalArea = 3.35e+06
  Width = 100
FEATURE [Part::Part2DObjectPython] Line2279  # Draft 2D object (typed FeaturePython)
  ChamferSize = 0
  Closed = true
  End = (4685,855,0)
  FilletRadius = 0
  Length = 450
  MakeFace = false
  Placement = pos=(5845,925,0) rot=(0,0,1;3.14159rad)
  Points = (2) [(1610,70,0),(1160,70,0)]
  Start = (4235,855,0)
  Subdivisions = 0
FEATURE [Part::FeaturePython] Wall587005  label="перегородка 089"  # Arch/BIM 166 (typed FeaturePython)
  Align = 1
  Area = 1507500
  Base = -> Line2279
  BlockHeight = 250
  BlockLength = 0
  CountBroken = 0
  CountEntire = 0
  Face = 0
  Height = 3350
  HorizontalArea = 54000
  IfcType = 166
  Joint = 0
  Length = 450
  MakeBlocks = false
  Material = -> Material008
  MoveBase = false
  MoveWithHost = false
  Normal = (0,0,0)
  OffsetFirst = 0
  OffsetSecond = 300
  PerimeterLength = 1140
  Placement = pos=(0,0,3145) rot=(0,0,1;0rad)
  PredefinedType = 0
  VerticalArea = 3.819e+06
  Width = 120
FEATURE [Part::Part2DObjectPython] Line2280  # Draft 2D object (typed FeaturePython)
  ChamferSize = 0
  Closed = true
  End = (6725,855,0)
  FilletRadius = 0
  Length = 710
  MakeFace = false
  Placement = pos=(5565,925,0) rot=(0,0,1;3.14159rad)
  Points = (2) [(-450,70,0),(-1160,70,0)]
  Start = (6015,855,0)
  Subdivisions = 0
FEATURE [Part::FeaturePython] Wall587006  label="перегородка 090"  # Arch/BIM 166 (typed FeaturePython)
  Align = 1
  Area = 2378500
  Base = -> Line2280
  BlockHeight = 250
  BlockLength = 0
  CountBroken = 0
  CountEntire = 0
  Face = 0
  Height = 3350
  HorizontalArea = 85200
  IfcType = 166
  Joint = 0
  Length = 710
  MakeBlocks = false
  Material = -> Material008
  MoveBase = false
  MoveWithHost = false
  Normal = (0,0,0)
  OffsetFirst = 0
  OffsetSecond = 300
  PerimeterLength = 1660
  Placement = pos=(0,0,3145) rot=(0,0,1;0rad)
  PredefinedType = 0
  VerticalArea = 5561000
  Width = 120
FEATURE [Part::MultiFuse] Fusion011003002002005003024  label="перегородка_север_005"
  Shapes = -> [Wall587003,Wall587004,Wall587005,Wall587006]
FEATURE [Part::Cut] Cut105003022006  label="перегородка_север_006"
  Base = -> Fusion011003002002005003024
  Tool = -> Extrude099005017
FEATURE [Part::FeaturePython] Component241073  label="перегородка_север_007"  # Arch/BIM 0 (typed FeaturePython)
  Base = -> Cut105003022006
  HorizontalArea = 0
  IfcData = attributes={"GlobalId": {"name": "GlobalId", "type": "IfcGloballyUniqueId", "is_enum": false, "enum_values": []}, "Description": {"... (+538 chars omitted),+1 more (map truncated)
  IfcType = 0
  Material = -> Material008
  MoveBase = false
  MoveWithHost = false
  PerimeterLength = 0
  PredefinedType = 0
  VerticalArea = 0
FEATURE [App::GeometryPython] BuildingPart136  label="Перегородки мансарды"  # Arch/BIM 172 (typed FeaturePython)
  Area = 11720500
  Group = -> [Component241040,Component241042,Wall603,Wall614,Component241073]
  Height = 0
  HeightPropagate = true
  IfcData = attributes={"GlobalId": {"name": "GlobalId", "type": "IfcGloballyUniqueId", "is_enum": false, "enum_values": []}, "Description": {"... (+484 chars omitted),+1 more (map truncated)
  IfcType = 172
  LevelOffset = 0
  PredefinedType = 0
FEATURE [Part::Part2DObjectPython] Rectangle4226  # Draft 2D object (typed FeaturePython)
  Area = 85200
  ChamferSize = 0
  Columns = 1
  FilletRadius = 0
  Height = 120
  Length = 710
  MakeFace = true
  Placement = pos=(6725,975,0) rot=(0,0,1;3.14159rad)
  Rows = 1
FEATURE [Part::Part2DObjectPython] Rectangle4227  # Draft 2D object (typed FeaturePython)
  Area = 88000
  ChamferSize = 0
  Columns = 1
  FilletRadius = 0
  Height = 880
  Length = 100
  MakeFace = true
  Placement = pos=(3735,-25,0) rot=(0,0,1;0rad)
  Rows = 1
FEATURE [Part::Part2DObjectPython] Rectangle4228  # Draft 2D object (typed FeaturePython)
  Area = 40000
  ChamferSize = 0
  Columns = 1
  FilletRadius = 0
  Height = 100
  Length = 400
  MakeFace = true
  Placement = pos=(4135,955,0) rot=(0,0,1;3.14159rad)
  Rows = 1
FEATURE [Part::Part2DObjectPython] Rectangle4230  # Draft 2D object (typed FeaturePython)
  ChamferSize = 0
  Columns = 1
  FilletRadius = 0
  Height = 880
  Length = 850
  MakeFace = true
  Placement = pos=(4685,855,0) rot=(0,0,1;3.14159rad)
  Rows = 1
FEATURE [Part::Part2DObjectPython] Line2283  # Draft 2D object (typed FeaturePython)
  Area = 0
  ChamferSize = 0
  Closed = false
  End = (3835,415,0)
  FilletRadius = 0
  Length = 330
  MakeFace = false
  Placement = pos=(4165,385,0) rot=(0,0,1;3.14159rad)
  Points = (2) [(0,-30,0),(330,-30,0)]
  Start = (4165,415,0)
  Subdivisions = 0
FEATURE [Part::Part2DObjectPython] Circle231  # Draft 2D object (typed FeaturePython)
  Area = 0
  FirstAngle = 0
  LastAngle = 0
  MakeFace = false
  Placement = pos=(4165,415,0) rot=(0,0,1;0rad)
  Radius = 100
FEATURE [Part::Part2DObjectPython] Wire1102  # Draft 2D object (typed FeaturePython)
  Area = 1.134e+06
  ChamferSize = 0
  Closed = true
  End = (3535,775,0)
  FilletRadius = 0
  Length = 5220
  MakeFace = true
  Placement = pos=(3535,2785,0) rot=(0,0,1;0rad)
  Points = (6) [(0,0,0),(600,4.54747e-13,0),(600,-1830,0),(200,-1830,0),(200,-2010,0),(0,-2010,0)]
  Start = (3535,2785,0)
  Subdivisions = 0
FEATURE [Part::FeaturePython] Structure584  label="стеллаж встроенный 014"  # Arch/BIM 172 (typed FeaturePython)
  Base = -> Wire1102
  FaceMaker = 0
  Height = 3500
  HorizontalArea = 1.134e+06
  IfcData = attributes={"GlobalId": {"name": "GlobalId", "type": "IfcGloballyUniqueId", "is_enum": false, "enum_values": []}, "Description": {"... (+484 chars omitted),+1 more (map truncated)
  IfcType = 172
  Length = 0
  MoveBase = false
  MoveWithHost = false
  Nodes = (2) [(3835,1780,0),(3835,1780,3500)]
  NodesOffset = 0
  Normal = (0,0,1)
  PerimeterLength = 5220
  Placement = pos=(0,0,3145) rot=(0,0,1;0rad)
  PredefinedType = 0
  Subtractions = -> [Component241035]
  VerticalArea = 1.15272e+07
  Width = 100
FEATURE [Part::Part2DObjectPython] Rectangle4231  # Draft 2D object (typed FeaturePython)
  Area = 100000
  ChamferSize = 0
  Columns = 1
  FilletRadius = 0
  Height = 1000
  Length = 100
  MakeFace = true
  Placement = pos=(6725,-25,0) rot=(0,0,1;0rad)
  Rows = 1
FEATURE [Part::Part2DObjectPython] Line2284  # Draft 2D object (typed FeaturePython)
  Area = 0
  ChamferSize = 0
  Closed = true
  End = (2562.62,4185,0)
  FilletRadius = 0
  Length = 6643.01
  MakeFace = true
  Placement = pos=(-1249.99,9625,0) rot=(0,0,1;0rad)
  Points = (2) [(0,0,0),(3812.61,-5440,0)]
  Start = (-1249.99,9625,0)
  Subdivisions = 0
FEATURE [Part::Part2DObjectPython] Line2285  # Draft 2D object (typed FeaturePython)
  Area = 0
  ChamferSize = 0
  Closed = true
  End = (2562.62,4185,0)
  FilletRadius = 0
  Length = 6643.01
  MakeFace = true
  Placement = pos=(-1249.99,-1255,0) rot=(0,0,1;0rad)
  Points = (2) [(0,0,0),(3812.61,5440,0)]
  Start = (-1249.99,-1255,0)
  Subdivisions = 0
FEATURE [Part::Part2DObjectPython] Line2286  # Draft 2D object (typed FeaturePython)
  Area = 0
  ChamferSize = 0
  Closed = true
  End = (8007.38,4185,0)
  FilletRadius = 0
  Length = 6643.01
  MakeFace = true
  Placement = pos=(11820,-1255,0) rot=(0,0,1;0rad)
  Points = (2) [(0,0,0),(-3812.61,5440,0)]
  Start = (11820,-1255,0)
  Subdivisions = 0
FEATURE [Part::Part2DObjectPython] Line2287  # Draft 2D object (typed FeaturePython)
  Area = 0
  ChamferSize = 0
  Closed = true
  End = (8007.38,4185,0)
  FilletRadius = 0
  Length = 6643.01
  MakeFace = true
  Placement = pos=(11820,9625,0) rot=(0,0,1;0rad)
  Points = (2) [(0,0,0),(-3812.61,-5440,0)]
  Start = (11820,9625,0)
  Subdivisions = 0
FEATURE [Part::Part2DObjectPython] Rectangle4232  # Draft 2D object (typed FeaturePython)
  Area = 0
  ChamferSize = 0
  Columns = 1
  FilletRadius = 0
  Height = 660
  Length = 876.911
  MakeFace = false
  Placement = pos=(10070.1,4435,0) rot=(0,0,1;0rad)
  Rows = 1
FEATURE [Part::Part2DObjectPython] Rectangle4233  # Draft 2D object (typed FeaturePython)
  Area = 0
  ChamferSize = 0
  Columns = 1
  FilletRadius = 0
  Height = 660
  Length = 876.911
  MakeFace = false
  Placement = pos=(10070.1,3275,0) rot=(0,0,1;0rad)
  Rows = 1
FEATURE [Part::Part2DObjectPython] Rectangle4234  # Draft 2D object (typed FeaturePython)
  Area = 0
  ChamferSize = 0
  Columns = 1
  FilletRadius = 0
  Height = 660
  Length = 876.911
  MakeFace = false
  Placement = pos=(-377.029,4435,0) rot=(0,0,1;0rad)
  Rows = 1
FEATURE [Part::Part2DObjectPython] Rectangle4235  # Draft 2D object (typed FeaturePython)
  Area = 0
  ChamferSize = 0
  Columns = 1
  FilletRadius = 0
  Height = 660
  Length = 876.911
  MakeFace = false
  Placement = pos=(-377.029,3275,0) rot=(0,0,1;0rad)
  Rows = 1
FEATURE [Part::Part2DObjectPython] Wire1103  # Draft 2D object (typed FeaturePython)
  Area = 0
  ChamferSize = 0
  Closed = true
  End = (8028.9,-450,0)
  FilletRadius = 0
  Length = 15604.9
  MakeFace = false
  Placement = pos=(2531.1,-450,0) rot=(0,0,1;0rad)
  Points = (4) [(0,0,0),(1114.01,3232.06,0),(4383.8,3232.06,0),(5497.8,1.7053e-13,0)]
  Start = (2531.1,-450,0)
  Subdivisions = 0
FEATURE [Part::Part2DObjectPython] Line2288  # Draft 2D object (typed FeaturePython)
  Area = 0
  ChamferSize = 0
  Closed = false
  End = (3645.11,-450,0)
  FilletRadius = 0
  Length = 3232.06
  MakeFace = true
  Placement = pos=(3645.11,2782.06,0) rot=(0,0,1;0rad)
  Points = (2) [(0,0,0),(0,-3232.06,0)]
  Start = (3645.11,2782.06,0)
  Subdivisions = 0
FEATURE [Part::Part2DObjectPython] Line2289  # Draft 2D object (typed FeaturePython)
  Area = 0
  ChamferSize = 0
  Closed = false
  End = (6914.89,-450,0)
  FilletRadius = 0
  Length = 3232.06
  MakeFace = true
  Placement = pos=(6914.89,2782.06,0) rot=(0,0,1;0rad)
  Points = (2) [(0,0,0),(0,-3232.06,0)]
  Start = (6914.89,2782.06,0)
  Subdivisions = 0
FEATURE [Part::Part2DObjectPython] Rectangle4236  # Draft 2D object (typed FeaturePython)
  Area = 15000
  ChamferSize = 0
  Columns = 1
  FilletRadius = 0
  Height = 150
  Length = 100
  MakeFace = true
  Placement = pos=(6105,1575,0) rot=(0,0,1;0rad)
  Rows = 1
FEATURE [App::DocumentObjectGroup] Group136  label="План 1й этаж тест"
  Group = -> [Rectangle3854,Rectangle3879,Rectangle3870,Rectangle3895,Rectangle3896,Rectangle3897,Rectangle3898,Rectangle3899,Rectangle3900,Rectangle3901,Rectangle3902,Rectangle3903,Rectangle3904,Rectangle3905,Rectangle3906,Rectangle3907,Rectangle3908,Wire1023,Wire1024,Rectangle3885,Sketch413,Rectangle3851,Arc153,Rectangle3875,Rectangle3881,Rectangle3883,Rectangle3873,Rectangle3861,Rectangle3839,Rectangle3837,+197 more]
FEATURE [Part::Part2DObjectPython] Wire1104  # Draft 2D object (typed FeaturePython)
  Area = 0
  ChamferSize = 0
  Closed = true
  End = (3825,-25,0)
  FilletRadius = 0
  Length = 12660
  MakeFace = false
  Placement = pos=(3825,2935,0) rot=(0,0,1;0rad)
  Points = (8) [(0,0,0),(3220,4.54747e-13,0),(3220,-1360,0),(2380,-1360,0),(2380,-1210,0),(2280,-1210,0),(2280,-2960,0),(0,-2960,0)]
  Start = (3825,2935,0)
  Subdivisions = 0
FEATURE [Part::FeaturePython] Wall235  label="Штукатурка 20мм 003"  # Arch/BIM 166 (typed FeaturePython)
  Align = 1
  Area = 3.5448e+07
  Base = -> Wire1104
  BlockHeight = 0
  BlockLength = 0
  CountBroken = 0
  CountEntire = 0
  Face = 0
  GlobalId = 0Elsg4vQ59AghdVdDj5fjs
  Height = 2800
  HorizontalArea = 0
  IfcData = IfcUID=0Elsg4vQ59AghdVdDj5fjs,+2 more (map truncated)
  IfcType = 166
  Joint = 0
  Length = 12660
  MakeBlocks = false
  Material = -> Material008
  MoveBase = false
  MoveWithHost = false
  Normal = (0,0,0)
  OffsetFirst = 0
  OffsetSecond = 0
  PerimeterLength = 0
  PredefinedType = 0
  Subtractions = -> [Structure020,Structure543,Structure646,Wall128,Wall223,Wall187,Structure360,Structure677]
  VerticalArea = 0
  Width = 20
FEATURE [Part::Part2DObjectPython] Rectangle4237  # Draft 2D object (typed FeaturePython)
  Area = 0
  ChamferSize = 0
  Columns = 1
  FilletRadius = 0
  Height = 660
  Length = 1180
  MakeFace = false
  Placement = pos=(10154,4585,5308.13) rot=(0,1,0;0.785398rad)
  Rows = 1
FEATURE [Part::Extrusion] Extrude099005025  label="проёмы мансардных окон 004"
  Base = -> Rectangle4237
  Dir = (0.707107,0,0.707107)
  DirMode = 2
  FaceMakerClass = Part::FaceMakerBullseye
  LengthFwd = 400
  LengthRev = 0
  Reversed = true
  Solid = true
  Symmetric = false
FEATURE [Part::Mirroring] mirror016002019  label="Extrude099005025 (mirrored)"
  Base = (2980.47,4185,0)
  Normal = (4e-16,-1,0)
  Source = -> Extrude099005025
FEATURE [Part::Mirroring] mirror016002020  label="проёмы мансардных окон 002"
  Base = (5285,7000,0)
  Normal = (-1,0,0)
  Source = -> Extrude099005025
FEATURE [Part::Mirroring] mirror016002021  label="проёмы мансардных окон 003"
  Base = (5285,7000,0)
  Normal = (-1,0,0)
  Source = -> mirror016002019
FEATURE [Part::MultiFuse] Fusion011003002002005003022  label="проёмы мансардных окон 001"
  Shapes = -> [mirror016002020,mirror016002021,Extrude099005025,mirror016002019]
FEATURE [Part::FeaturePython] Window117  label="Мансардное окно VELUX WhiteLine Дизайн GGU 0068, 660*1180 003"  # Arch/BIM 170 (typed FeaturePython)
  Area = 778800
  Base = -> Sketch430
  Frame = 70
  Height = 660
  HoleDepth = 0
  HoleWire = 0
  HorizontalArea = 0
  IfcData = attributes={"GlobalId": {"name": "GlobalId", "type": "IfcGloballyUniqueId", "is_enum": false, "enum_values": []}, "Description": {"... (+1230 chars omitted),+1 more (map truncated)
  IfcType = 170
  LouvreSpacing = 0
  LouvreWidth = 0
  Material = -> Material011
  MoveBase = false
  MoveWithHost = true
  Normal = (-0.669131,0,-0.743145)
  Opening = 0
  OverallHeight = 660
  OverallWidth = 1180
  PartitioningType = 0
  PerimeterLength = 0
  Placement = pos=(10570,9830,-9.09e-13) rot=(0,0,1;3.14159rad)
  PredefinedType = 0
  Preset = 1
  SymbolElevation = false
  SymbolPlan = false
  VerticalArea = 0
  Width = 1180
  WindowParts = OuterFrame | Frame | Wire0,Wire1 | 115.0+V | 0.00+V | Glass | Glass panel | Wire1 | 15.0 | 75.0+V
  expr: OverallWidth = .Width.Value
  expr: OverallHeight = .Height.Value
FEATURE [Part::FeaturePython] Window118  label="Мансардное окно VELUX WhiteLine Дизайн GGU 0068, 660*1180 004"  # Arch/BIM 170 (typed FeaturePython)
  Area = 778800
  Base = -> Sketch430
  Frame = 70
  Height = 660
  HoleDepth = 0
  HoleWire = 0
  HorizontalArea = 0
  IfcData = attributes={"GlobalId": {"name": "GlobalId", "type": "IfcGloballyUniqueId", "is_enum": false, "enum_values": []}, "Description": {"... (+1230 chars omitted),+1 more (map truncated)
  IfcType = 170
  LouvreSpacing = 0
  LouvreWidth = 0
  Material = -> Material011
  MoveBase = false
  MoveWithHost = true
  Normal = (-0.669131,0,-0.743145)
  Opening = 0
  OverallHeight = 660
  OverallWidth = 1180
  PartitioningType = 0
  PerimeterLength = 0
  Placement = pos=(10570,8370,0) rot=(0,0,1;3.14159rad)
  PredefinedType = 0
  Preset = 1
  SymbolElevation = false
  SymbolPlan = false
  VerticalArea = 0
  Width = 1180
  WindowParts = OuterFrame | Frame | Wire0,Wire1 | 115.0+V | 0.00+V | Glass | Glass panel | Wire1 | 15.0 | 75.0+V
  expr: OverallHeight = .Height.Value
  expr: OverallWidth = .Width.Value
FEATURE [App::GeometryPython] BuildingPart137  label="Окна кукушек"  # Arch/BIM 172 (typed FeaturePython)
  Area = 6139700
  Group = -> [Window101,Window100,Window,Window116,Window118,Window117]
  Height = 0
  HeightPropagate = true
  IfcData = attributes={"GlobalId": {"name": "GlobalId", "type": "IfcGloballyUniqueId", "is_enum": false, "enum_values": []}, "Description": {"... (+484 chars omitted),+1 more (map truncated)
  IfcType = 172
  LevelOffset = 0
  PredefinedType = 0
FEATURE [Part::Part2DObjectPython] Wire1105  label="Детская #1"  # Draft 2D object (typed FeaturePython)
  Area = 1.26836e+07
  ChamferSize = 0
  Closed = true
  End = (-30,2890,0)
  FilletRadius = 0
  Length = 15050
  MakeFace = true
  Placement = pos=(-30,4135,0) rot=(0,0,1;0rad)
  Points = (10) [(0,0,0),(3565,0,0),(3565,-1350,0),(4165,-1350,0),(4165,-3180,0),(3765,-3180,0),(3765,-3360,0),(202.727,-3360,0),(202.727,-1245,0),+1 more]
  Start = (-30,4135,0)
  Subdivisions = 0
FEATURE [Part::Part2DObjectPython] Wire1106  label="СУ мансарды"  # Draft 2D object (typed FeaturePython)
  Area = 7.5174e+06
  ChamferSize = 0
  Closed = true
  End = (4685,855,0)
  FilletRadius = 0
  Length = 14060
  MakeFace = true
  Placement = pos=(4235,2785,0) rot=(0,0,1;0rad)
  Points = (14) [(450,-1810,0),(1.81899e-12,-1810,0),(1.81899e-12,-4.54747e-13,0),(2660,-4.54747e-13,0),(2660,-1810,0),(1780,-1810,0),(1780,-1930,0),(2490,-1930,0),+6 more]
  Start = (4685,975,0)
  Subdivisions = 0
FEATURE [App::DocumentObjectGroup] Group134  label="Площади помещений"
  Group = -> [Wire985,Wire989,Wire990,Wire992,Rectangle3074,Wire1016,Wire1053,Wire1054,Wire1055,Wire1056,Wire1057,Wire1058,Rectangle4186,Rectangle4187,Wire1069,Wire1105,Wire1106]
FEATURE [Part::Part2DObjectPython] Line1744  # Draft 2D object (typed FeaturePython)
  ChamferSize = 0
  Closed = true
  End = (5725,4535,0)
  FilletRadius = 0
  Length = 1040
  MakeFace = false
  Placement = pos=(2215,6995,0) rot=(0,0,-1;0rad)
  Points = (2) [(3510,-1420,0),(3510,-2460,0)]
  Start = (5725,5575,0)
  Subdivisions = 0
FEATURE [Part::FeaturePython] Wall401  label="перегородка стекло 10мм матовое"  # Arch/BIM 166 (typed FeaturePython)
  Align = 1
  Area = 2184000
  Base = -> Line1744
  BlockHeight = 250
  BlockLength = 0
  CountBroken = 0
  CountEntire = 0
  Face = 0
  Height = 2100
  HorizontalArea = 10400
  IfcType = 166
  Joint = 0
  Length = 1040
  MakeBlocks = false
  Material = -> Material006
  MoveBase = false
  MoveWithHost = false
  Normal = (0,0,0)
  Offset = 10
  OffsetFirst = 300
  OffsetSecond = 50
  PerimeterLength = 2100
  PredefinedType = 0
  VerticalArea = 4.41e+06
  Width = 10
FEATURE [App::GeometryPython] BuildingPart081  label="Отделка"  # Arch/BIM 52 (typed FeaturePython)
  Area = 3.0032e+08
  GlobalId = 3k8znIZGb8Sep8PACCMQ9v
  Group = -> [Wall232,Wall233,Wall234,Wall235,Wall236,Wall,Wall403,Wall401]
  Height = 0
  HeightPropagate = true
  IfcData = IfcUID=3k8znIZGb8Sep8PACCMQ9v,+2 more (map truncated)
  IfcType = 52
  LevelOffset = 0
FEATURE [Part::Part2DObjectPython] Rectangle  label="Плитный ростверк"  # Draft 2D object (typed FeaturePython)
  Area = 0
  ChamferSize = 0
  Columns = 1
  FilletRadius = 0
  Height = 9540
  Length = 11750
  MakeFace = false
  Placement = pos=(-590,-585,0) rot=(0,0,1;0rad)
  Rows = 1
FEATURE [Part::FeaturePython] Wall587007  label="Ребро ростверка 013"  # Arch/BIM 166 (typed FeaturePython)
  Align = 0
  Area = 12774000
  Base = -> Rectangle
  BlockHeight = 0
  BlockLength = 0
  CountBroken = 0
  CountEntire = 0
  Face = 0
  Height = 300
  HorizontalArea = 19707800
  IfcData = attributes={"GlobalId": {"name": "GlobalId", "type": "IfcGloballyUniqueId", "is_enum": false, "enum_values": []}, "Description": {"... (+533 chars omitted),+1 more (map truncated)
  IfcType = 166
  Joint = 0
  Length = 42580
  MakeBlocks = false
  MoveBase = false
  MoveWithHost = false
  Normal = (0,0,-1)
  Offset = 50
  OffsetFirst = 0
  OffsetSecond = 0
  PerimeterLength = 42180
  Placement = pos=(0,0,-200) rot=(0,0,1;0rad)
  PredefinedType = 0
  VerticalArea = 24132000
  Width = 490
FEATURE [Part::Part2DObjectPython] Line  # Draft 2D object (typed FeaturePython)
  Area = 0
  ChamferSize = 0
  Closed = true
  End = (3680,-235,-200)
  FilletRadius = 0
  Length = 8840
  MakeFace = true
  Placement = pos=(3680,8415,-200) rot=(0,0,1;0rad)
  Points = (2) [(0,190,0),(0,-8650,0)]
  Start = (3680,8605,-200)
  Subdivisions = 0
FEATURE [Part::Part2DObjectPython] Line2290  # Draft 2D object (typed FeaturePython)
  Area = 0
  ChamferSize = 0
  Closed = true
  End = (10810,3080,0)
  FilletRadius = 0
  Length = 7130
  MakeFace = true
  Placement = pos=(3680,3080,0) rot=(0,0,1;0rad)
  Points = (2) [(0,0,0),(7130,0,0)]
  Start = (3680,3080,0)
  Subdivisions = 0
FEATURE [Part::FeaturePython] Wall587008  label="Ребро ростверка 014"  # Arch/BIM 166 (typed FeaturePython)
  Align = 2
  Area = 2652000
  Base = -> Line
  BlockHeight = 0
  BlockLength = 0
  CountBroken = 0
  CountEntire = 0
  Face = 0
  Height = 300
  HorizontalArea = 3094000
  IfcData = attributes={"GlobalId": {"name": "GlobalId", "type": "IfcGloballyUniqueId", "is_enum": false, "enum_values": []}, "Description": {"... (+533 chars omitted),+1 more (map truncated)
  IfcType = 166
  Joint = 0
  Length = 8840
  MakeBlocks = false
  MoveBase = false
  MoveWithHost = false
  Normal = (0,0,-1)
  OffsetFirst = 0
  OffsetSecond = 0
  PerimeterLength = 18380
  PredefinedType = 0
  VerticalArea = 5514000
  Width = 350
FEATURE [Part::FeaturePython] Wall587009  label="Ребро ростверка 015"  # Arch/BIM 166 (typed FeaturePython)
  Align = 2
  Area = 2139000
  Base = -> Line2290
  BlockHeight = 0
  BlockLength = 0
  CountBroken = 0
  CountEntire = 0
  Face = 0
  Height = 300
  HorizontalArea = 2495500
  IfcData = attributes={"GlobalId": {"name": "GlobalId", "type": "IfcGloballyUniqueId", "is_enum": false, "enum_values": []}, "Description": {"... (+533 chars omitted),+1 more (map truncated)
  IfcType = 166
  Joint = 0
  Length = 7130
  MakeBlocks = false
  MoveBase = false
  MoveWithHost = false
  Normal = (0,0,-1)
  OffsetFirst = 0
  OffsetSecond = 0
  PerimeterLength = 14960
  Placement = pos=(0,0,-200) rot=(0,0,1;0rad)
  PredefinedType = 0
  VerticalArea = 4488000
  Width = 350
FEATURE [Part::Part2DObjectPython] Line2291  # Draft 2D object (typed FeaturePython)
  Area = 0
  ChamferSize = 0
  Closed = false
  End = (6980,3080,0)
  FilletRadius = 0
  Length = 5525
  MakeFace = true
  Placement = pos=(6980,8605,0) rot=(0,0,1;0rad)
  Points = (2) [(0,0,0),(0,-5525,0)]
  Start = (6980,8605,0)
  Subdivisions = 0
FEATURE [Part::Part2DObjectPython] Line2292  # Draft 2D object (typed FeaturePython)
  Area = 0
  ChamferSize = 0
  Closed = false
  End = (7230,-235,0)
  FilletRadius = 0
  Length = 3315
  MakeFace = true
  Placement = pos=(7230,3080,0) rot=(0,0,1;0rad)
  Points = (2) [(0,0,0),(0,-3315,0)]
  Start = (7230,3080,0)
  Subdivisions = 0
FEATURE [Part::FeaturePython] Wall587010  label="Ребро ростверка 016"  # Arch/BIM 166 (typed FeaturePython)
  Align = 2
  Area = 1.6575e+06
  Base = -> Line2291
  BlockHeight = 0
  BlockLength = 0
  CountBroken = 0
  CountEntire = 0
  Face = 0
  Height = 300
  HorizontalArea = 1.93375e+06
  IfcData = attributes={"GlobalId": {"name": "GlobalId", "type": "IfcGloballyUniqueId", "is_enum": false, "enum_values": []}, "Description": {"... (+533 chars omitted),+1 more (map truncated)
  IfcType = 166
  Joint = 0
  Length = 5525
  MakeBlocks = false
  MoveBase = false
  MoveWithHost = false
  Normal = (0,0,-1)
  OffsetFirst = 0
  OffsetSecond = 0
  PerimeterLength = 11750
  Placement = pos=(0,0,-200) rot=(0,0,1;0rad)
  PredefinedType = 0
  VerticalArea = 3525000
  Width = 350
FEATURE [Part::FeaturePython] Wall587011  label="Ребро ростверка 001"  # Arch/BIM 166 (typed FeaturePython)
  Align = 2
  Area = 994500
  Base = -> Line2292
  BlockHeight = 0
  BlockLength = 0
  CountBroken = 0
  CountEntire = 0
  Face = 0
  Height = 300
  HorizontalArea = 1160250
  IfcData = attributes={"GlobalId": {"name": "GlobalId", "type": "IfcGloballyUniqueId", "is_enum": false, "enum_values": []}, "Description": {"... (+533 chars omitted),+1 more (map truncated)
  IfcType = 166
  Joint = 0
  Length = 3315
  MakeBlocks = false
  MoveBase = false
  MoveWithHost = false
  Normal = (0,0,-1)
  OffsetFirst = 0
  OffsetSecond = 0
  PerimeterLength = 7330
  Placement = pos=(0,0,-200) rot=(0,0,1;0rad)
  PredefinedType = 0
  VerticalArea = 2199000
  Width = 350
FEATURE [Part::FeaturePython] Wall587012  label="утепление ростверка XPS 50mm 001"  # Arch/BIM 166 (typed FeaturePython)
  Align = 0
  Area = 9580500
  Base = -> Rectangle
  BlockHeight = 0
  BlockLength = 0
  CountBroken = 0
  CountEntire = 0
  Face = 0
  Height = 225
  HorizontalArea = 2119000
  IfcData = attributes={"GlobalId": {"name": "GlobalId", "type": "IfcGloballyUniqueId", "is_enum": false, "enum_values": []}, "Description": {"... (+533 chars omitted),+1 more (map truncated)
  IfcType = 166
  Joint = 0
  Length = 42580
  MakeBlocks = false
  Material = -> Material002
  MoveBase = false
  MoveWithHost = false
  Normal = (0,0,-1)
  OffsetFirst = 0
  OffsetSecond = 0
  PerimeterLength = 42580
  Placement = pos=(0,0,-275) rot=(0,0,1;0rad)
  PredefinedType = 0
  VerticalArea = 19071000
  Width = 50
FEATURE [Part::Chamfer] Chamfer  label="утепление ростверка XPS 50mm 002"
  Base = -> Wall587012
  Edges = 4 edges r=45: [Edge15,Edge18,Edge21,Edge23]
FEATURE [Part::FeaturePython] Structure695003007029  label="Плита ростверка 001"  # Arch/BIM 118 (typed FeaturePython)
  Additions = -> [Wall587007,Wall587008,Wall587009,Wall587010,Wall587011]
  Base = -> Rectangle
  FaceMaker = 0
  Height = 150
  HorizontalArea = 0
  IfcData = attributes={"GlobalId": {"name": "GlobalId", "type": "IfcGloballyUniqueId", "is_enum": false, "enum_values": []}, "Description": {"... (+453 chars omitted),+1 more (map truncated)
  IfcType = 118
  Length = 9540
  Material = -> Material001
  MoveBase = false
  MoveWithHost = false
  Nodes = (4) [(-590,-585,0),(11160,-585,0),(11160,8955,0),(-590,8955,0)]
  NodesOffset = 0
  Normal = (0,0,-1)
  PerimeterLength = 0
  Placement = pos=(0,0,-200) rot=(0,0,1;0rad)
  PredefinedType = 0
  Subtractions = -> [Chamfer]
  VerticalArea = 0
  Width = 11750
FEATURE [Part::FeaturePython] Component241074  label="утепление торца ростверка XPS 50mm"  # Arch/BIM 0 (typed FeaturePython)
  Base = -> Chamfer
  HorizontalArea = 0
  IfcData = attributes={"GlobalId": {"name": "GlobalId", "type": "IfcGloballyUniqueId", "is_enum": false, "enum_values": []}, "Description": {"... (+538 chars omitted),+1 more (map truncated)
  IfcType = 0
  Material = -> Material002
  MoveBase = false
  MoveWithHost = false
  PerimeterLength = 0
  PredefinedType = 0
  VerticalArea = 0
FEATURE [App::MaterialObjectPython] Material022  label="PPS"  # material (typed FeaturePython)
  Description = PPS
  Material = AuthorAndLicense=ABS-Generic,CardName=ABS-Generic,Color=(0.9490196078431372, 0.8901960784313725, 0.8901960784313725, 1.0),Density=1060 kg/m^3,+15 more (map truncated)
  Transparency = 0
FEATURE [Part::FeaturePython] Structure695003007030  label="Деформационная подкладка PPS 017"  # Arch/BIM 118 (typed FeaturePython)
  Base = -> Rectangle
  FaceMaker = 0
  Height = 50
  HorizontalArea = 109976000
  IfcData = attributes={"GlobalId": {"name": "GlobalId", "type": "IfcGloballyUniqueId", "is_enum": false, "enum_values": []}, "Description": {"... (+453 chars omitted),+1 more (map truncated)
  IfcType = 118
  Length = 9540
  Material = -> Material022
  MoveBase = false
  MoveWithHost = false
  Nodes = (4) [(-590,-585,0),(11160,-585,0),(11160,8955,0),(-590,8955,0)]
  NodesOffset = 0
  Normal = (0,0,-1)
  PerimeterLength = 42180
  Placement = pos=(0,0,-350) rot=(0,0,1;0rad)
  PredefinedType = 0
  Subtractions = -> [Chamfer]
  VerticalArea = 2109000
  Width = 11750
FEATURE [Part::FeaturePython] Wall587014  label="Деформационная подкладка PPS 013"  # Arch/BIM 166 (typed FeaturePython)
  Align = 2
  Area = 1.38125e+06
  Base = -> Line2291
  BlockHeight = 0
  BlockLength = 0
  CountBroken = 0
  CountEntire = 0
  Face = 0
  Height = 250
  HorizontalArea = 3.03875e+06
  IfcData = attributes={"GlobalId": {"name": "GlobalId", "type": "IfcGloballyUniqueId", "is_enum": false, "enum_values": []}, "Description": {"... (+533 chars omitted),+1 more (map truncated)
  IfcType = 166
  Joint = 0
  Length = 5525
  MakeBlocks = false
  MoveBase = false
  MoveWithHost = false
  Normal = (0,0,-1)
  OffsetFirst = 0
  OffsetSecond = 0
  PerimeterLength = 12150
  Placement = pos=(0,0,-350) rot=(0,0,1;0rad)
  PredefinedType = 0
  VerticalArea = 3037500
  Width = 550
FEATURE [Part::FeaturePython] Wall587015  label="Деформационная подкладка PPS 014"  # Arch/BIM 166 (typed FeaturePython)
  Align = 2
  Area = 1782500
  Base = -> Line2290
  BlockHeight = 0
  BlockLength = 0
  CountBroken = 0
  CountEntire = 0
  Face = 0
  Height = 250
  HorizontalArea = 3921500
  IfcData = attributes={"GlobalId": {"name": "GlobalId", "type": "IfcGloballyUniqueId", "is_enum": false, "enum_values": []}, "Description": {"... (+533 chars omitted),+1 more (map truncated)
  IfcType = 166
  Joint = 0
  Length = 7130
  MakeBlocks = false
  MoveBase = false
  MoveWithHost = false
  Normal = (0,0,-1)
  OffsetFirst = 0
  OffsetSecond = 0
  PerimeterLength = 15360
  Placement = pos=(0,0,-350) rot=(0,0,1;0rad)
  PredefinedType = 0
  VerticalArea = 3840000
  Width = 550
FEATURE [Part::FeaturePython] Wall587016  label="Деформационная подкладка PPS 015"  # Arch/BIM 166 (typed FeaturePython)
  Align = 2
  Area = 2210000
  Base = -> Line
  BlockHeight = 0
  BlockLength = 0
  CountBroken = 0
  CountEntire = 0
  Face = 0
  Height = 250
  HorizontalArea = 4862000
  IfcData = attributes={"GlobalId": {"name": "GlobalId", "type": "IfcGloballyUniqueId", "is_enum": false, "enum_values": []}, "Description": {"... (+533 chars omitted),+1 more (map truncated)
  IfcType = 166
  Joint = 0
  Length = 8840
  MakeBlocks = false
  MoveBase = false
  MoveWithHost = false
  Normal = (0,0,1)
  OffsetFirst = 0
  OffsetSecond = 0
  PerimeterLength = 18780
  Placement = pos=(0,0,-400) rot=(0,0,1;0rad)
  PredefinedType = 0
  VerticalArea = 4695000
  Width = 550
FEATURE [Part::FeaturePython] Wall587017  label="Деформационная подкладка PPS 016"  # Arch/BIM 166 (typed FeaturePython)
  Align = 2
  Area = 828750
  Base = -> Line2292
  BlockHeight = 0
  BlockLength = 0
  CountBroken = 0
  CountEntire = 0
  Face = 0
  Height = 250
  HorizontalArea = 1823250
  IfcData = attributes={"GlobalId": {"name": "GlobalId", "type": "IfcGloballyUniqueId", "is_enum": false, "enum_values": []}, "Description": {"... (+533 chars omitted),+1 more (map truncated)
  IfcType = 166
  Joint = 0
  Length = 3315
  MakeBlocks = false
  MoveBase = false
  MoveWithHost = false
  Normal = (0,0,-1)
  OffsetFirst = 0
  OffsetSecond = 0
  PerimeterLength = 7730
  Placement = pos=(0,0,-350) rot=(0,0,1;0rad)
  PredefinedType = 0
  VerticalArea = 1932500
  Width = 550
FEATURE [Part::FeaturePython] Wall587013  label="Деформационная подкладка и утепление PPS 50-100mm"  # Arch/BIM 166 (typed FeaturePython)
  Additions = -> [Wall587014,Wall587015,Wall587016,Wall587017,Structure695003007030]
  Align = 0
  Area = 10645000
  Base = -> Rectangle
  BlockHeight = 0
  BlockLength = 0
  CountBroken = 0
  CountEntire = 0
  Face = 0
  Height = 250
  HorizontalArea = 0
  IfcData = attributes={"GlobalId": {"name": "GlobalId", "type": "IfcGloballyUniqueId", "is_enum": false, "enum_values": []}, "Description": {"... (+533 chars omitted),+1 more (map truncated)
  IfcType = 166
  Joint = 0
  Length = 42580
  MakeBlocks = false
  Material = -> Material022
  MoveBase = false
  MoveWithHost = false
  Normal = (0,0,-1)
  OffsetFirst = 0
  OffsetSecond = 0
  PerimeterLength = 0
  Placement = pos=(0,0,-350) rot=(0,0,1;0rad)
  PredefinedType = 0
  Subtractions = -> [Wall587007,Wall587008,Wall587009,Wall587010,Wall587011,Chamfer]
  VerticalArea = 0
  Width = 650
FEATURE [Part::FeaturePython] Structure695003007031  label="Плита ростверка 002"  # Arch/BIM 172 (typed FeaturePython)
  CloneOf = -> Structure695003007029
  FaceMaker = 0
  Height = 150
  HorizontalArea = 0
  IfcData = attributes={"GlobalId": {"name": "GlobalId", "type": "IfcGloballyUniqueId", "is_enum": false, "enum_values": []}, "Description": {"... (+484 chars omitted),+1 more (map truncated)
  IfcType = 172
  Length = 9540
  Material = -> Material001
  MoveBase = false
  MoveWithHost = false
  Nodes = (2) [(5285,4185,0),(5285,4185,-150)]
  NodesOffset = 0
  Normal = (0,0,0)
  PerimeterLength = 0
  Placement = pos=(-1.0232e-12,0,-200) rot=(0,0,1;0rad)
  PredefinedType = 0
  VerticalArea = 0
  Width = 11750
FEATURE [Part::FeaturePython] Component241075  label="утепление торца ростверка XPS 50mm 004"  # Arch/BIM 0 (typed FeaturePython)
  CloneOf = -> Component241074
  HorizontalArea = 0
  IfcData = attributes={"GlobalId": {"name": "GlobalId", "type": "IfcGloballyUniqueId", "is_enum": false, "enum_values": []}, "Description": {"... (+538 chars omitted),+1 more (map truncated)
  IfcType = 0
  Material = -> Material002
  MoveBase = false
  MoveWithHost = false
  PerimeterLength = 0
  Placement = pos=(-1.0232e-12,0,0) rot=(0,0,1;0rad)
  PredefinedType = 0
  VerticalArea = 0
FEATURE [Part::FeaturePython] Wall587018  label="Деформационная подкладка и утепление PPS 002"  # Arch/BIM 166 (typed FeaturePython)
  Align = 2
  Area = 10645000
  BlockHeight = 0
  BlockLength = 0
  CloneOf = -> Wall587013
  CountBroken = 0
  CountEntire = 0
  Face = 0
  Height = 250
  HorizontalArea = 0
  IfcData = attributes={"GlobalId": {"name": "GlobalId", "type": "IfcGloballyUniqueId", "is_enum": false, "enum_values": []}, "Description": {"... (+533 chars omitted),+1 more (map truncated)
  IfcType = 166
  Joint = 0
  Length = 42580
  MakeBlocks = false
  MoveBase = false
  MoveWithHost = false
  Normal = (0,0,0)
  OffsetFirst = 0
  OffsetSecond = 0
  PerimeterLength = 0
  Placement = pos=(-1.0232e-12,0,-350) rot=(0,0,1;0rad)
  PredefinedType = 0
  VerticalArea = 0
  Width = 650
FEATURE [Part::FeaturePython] Structure695003007032  label="вычет"  # Arch/BIM 118 (typed FeaturePython)
  Base = -> Rectangle
  FaceMaker = 0
  Height = 200
  HorizontalArea = 112095000
  IfcData = attributes={"GlobalId": {"name": "GlobalId", "type": "IfcGloballyUniqueId", "is_enum": false, "enum_values": []}, "Description": {"... (+453 chars omitted),+1 more (map truncated)
  IfcType = 118
  Length = 9540
  MoveBase = false
  MoveWithHost = false
  Nodes = (4) [(-590,-585,0),(11160,-585,0),(11160,8955,0),(-590,8955,0)]
  NodesOffset = 0
  Normal = (0,0,-1)
  PerimeterLength = 42580
  PredefinedType = 0
  VerticalArea = 8516000
  Width = 11750
FEATURE [Part::MultiFuse] Fusion011003002002005003025  label="Вычет фундамента (ростверк)"
  Shapes = -> [Structure695003007031,Component241075,Wall587018,Structure695003007032]
FEATURE [Part::Cut] Cut105003022007  label="грунт в пятне застройки (для фасадов) 002"
  Base = -> Common105
  Tool = -> Fusion011003002002005003025
FEATURE [App::MaterialObjectPython] Material023  label="Sand"  # material (typed FeaturePython)
  Material = Color=(0.9254901960784314, 0.9215686274509803, 0.7137254901960784, 1.0),+5 more (map truncated)
  Transparency = 0
FEATURE [App::DocumentObjectGroupPython] MaterialContainer  label="Materials"  # scripted group (container) (typed FeaturePython)
  Group = -> [Material004,Material001,Material006,Material011,Material003,Material009,Material010,Material007,Material008,Material005,Material,Material002,Material012,Material013,Material014,Material015,Material016,Material017,Material018,Material019,Material020,Material021,Material022,Material023]
FEATURE [Part::FeaturePython] Component241076  label="грунт в пятне застройки (для фасадов)"  # Arch/BIM 0 (typed FeaturePython)
  Base = -> Cut105003022007
  HorizontalArea = 0
  IfcData = attributes={"GlobalId": {"name": "GlobalId", "type": "IfcGloballyUniqueId", "is_enum": false, "enum_values": []}, "Description": {"... (+538 chars omitted),+1 more (map truncated)
  IfcType = 0
  Material = -> Material023
  MoveBase = false
  MoveWithHost = false
  PerimeterLength = 0
  PredefinedType = 0
  Subtractions = -> [Structure140,Structure692]
  VerticalArea = 0
FEATURE [App::GeometryPython] BuildingPart145  label="Фундамент (ростверк по забивным сваям)"  # Arch/BIM 172 (typed FeaturePython)
  Area = 10645000
  Group = -> [Structure695003007029,Component241074,Wall587013,Component241076]
  Height = 0
  HeightPropagate = true
  IfcData = attributes={"GlobalId": {"name": "GlobalId", "type": "IfcGloballyUniqueId", "is_enum": false, "enum_values": []}, "Description": {"... (+484 chars omitted),+1 more (map truncated)
  IfcType = 172
  LevelOffset = 0
  Placement = pos=(0,0,-200) rot=(0,0,1;0rad)
  PredefinedType = 0
FEATURE [Part::Part2DObjectPython] Wire1107  # Draft 2D object (typed FeaturePython)
  Area = 7.5377e+06
  ChamferSize = 0
  Closed = true
  End = (6725,-25,5458.14)
  FilletRadius = 0
  Length = 13346.5
  MakeFace = true
  Placement = pos=(3835,-25,5458.14) rot=(1,0,0;0.279253rad)
  Points = (14) [(0,0,0),(0,915.464,-9.09495e-13),(400,915.464,0),(400,2923.24,-9.09495e-13),(2890,2923.24,0),(2890,1830.93,-9.09495e-13),(2460,1830.93,-9.09495e-13),+7 more]
  Start = (3835,-25,5458.14)
  Subdivisions = 0
FEATURE [Part::Extrusion] Extrude099005027
  Base = -> Wire1107
  Dir = (0,0,1)
  DirMode = 0
  FaceMakerClass = Part::FaceMakerBullseye
  LengthFwd = 100
  LengthRev = 0
  Reversed = true
  Solid = false
  Symmetric = false
FEATURE [Part::MultiFuse] Fusion011003002002005003026  label="roof_4_all_001"
  Shapes = -> [Extrude099005027,Common098,Cut105003022002]
FEATURE [Part::Cut] Cut105003022009  label="roof_4_all_002"
  Base = -> Fusion011003002002005003026
  Tool = -> Structure560
FEATURE [Part::Cut] Cut105003022010  label="roof_4_all_003"
  Base = -> Cut105003022009
  Tool = -> Fusion011003002002005003022
FEATURE [Part::FeaturePython] Component241077  label="Габарит кровли"  # Arch/BIM 0 (typed FeaturePython)
  Base = -> Cut105003022010
  HorizontalArea = 0
  IfcData = attributes={"GlobalId": {"name": "GlobalId", "type": "IfcGloballyUniqueId", "is_enum": false, "enum_values": []}, "Description": {"... (+538 chars omitted),+1 more (map truncated)
  IfcType = 0
  Material = -> Material007
  MoveBase = false
  MoveWithHost = false
  PerimeterLength = 0
  PredefinedType = 0
  VerticalArea = 0
FEATURE [Part::Part2DObjectPython] Wire1108  # Draft 2D object (typed FeaturePython)
  Area = 5.31276e+07
  ChamferSize = 0
  Closed = true
  End = (6355,9625,0)
  FilletRadius = 0
  Length = 33150.8
  MakeFace = true
  Placement = pos=(-1249.99,9625,0) rot=(0,0,1;0rad)
  Points = (8) [(0,0,0),(3812.61,-5440,0),(9257.38,-5440,0),(13070,0,0),(11705,0,0),(11705,675,0),(7604.99,675,0),(7604.99,0,0)]
  Start = (-1249.99,9625,0)
  Subdivisions = 0
FEATURE [Part::FeaturePython] Structure050  label="вычитаемый объём 004"  # Arch/BIM 52 (typed FeaturePython)
  Base = -> Wire1108
  FaceMaker = 0
  Height = 5000
  HorizontalArea = 5.31276e+07
  IfcData = complex_attributes={"OwnerHistory": {}, "IsNestedBy": {}, "IsDecomposedBy": {}, "IsDefinedBy": {}, "ObjectPlacement": {}, "Representation":... (+4 chars omitted)
  IfcType = 52
  Length = 0
  MoveBase = false
  MoveWithHost = false
  Nodes = (2) [(6040,886.738,0),(6040,886.738,4000)]
  NodesOffset = 0
  Normal = (0,0,1)
  PerimeterLength = 33150.8
  Placement = pos=(0,0,2500) rot=(0,0,1;0rad)
  VerticalArea = 1.65754e+08
  Width = 100
FEATURE [Part::Part2DObjectPython] Wire1109  # Draft 2D object (typed FeaturePython)
  Area = 2.08495e+07
  ChamferSize = 0
  Closed = true
  End = (11820,-1255,0)
  FilletRadius = 0
  Length = 24186
  MakeFace = true
  Placement = pos=(8007.38,4185,0) rot=(0,0,1;0rad)
  Points = (5) [(0,0,0),(3812.61,5440,0),(3822.62,5440,0),(3822.62,-5440,0),(3812.61,-5440,0)]
  Start = (8007.38,4185,0)
  Subdivisions = 0
FEATURE [Part::FeaturePython] Structure695003007033  label="Плоскость стропила002"  # Arch/BIM 7 (typed FeaturePython)
  FaceMaker = 0
  Height = 6000
  HorizontalArea = 650000
  IfcType = 7
  Length = 13000
  Material = -> Material001
  MoveBase = false
  MoveWithHost = false
  Nodes = (2) [(0,1.81899e-16,-8.88178e-15),(0,1.81899e-16,14000)]
  NodesOffset = 0
  Normal = (0,0,0)
  PerimeterLength = 26100
  Placement = pos=(-1375,-2493.54,4500) rot=(0,0,1;1.5708rad)
  PredefinedType = 0
  VerticalArea = 156600000
  Width = 50
FEATURE [Part::FeaturePython] Array092  # Draft array (typed FeaturePython)
  Angle = 360
  ArrayType = 0
  Axis = (0,0,1)
  Base = -> Structure695003007033
  Center = (0,0,0)
  Fuse = false
  IntervalAxis = (0,0,0)
  IntervalX = (640,0,0)
  IntervalY = (0,1,0)
  IntervalZ = (0,0,1)
  NumberPolar = 1
  NumberX = 22
  NumberY = 1
  NumberZ = 1
  Placement = pos=(-60,-5.457e-12,0) rot=(0,0,1;0rad)
FEATURE [Part::MultiCommon] Common  label="Stropilka_001"
  Shapes = -> [Structure050,Array092]
FEATURE [Part::FeaturePython] Roof041  label="roof_4_side_cut_stropile_001"  # Arch/BIM 113 (typed FeaturePython)
  Angles = [35,45,35,45]
  Base = -> Wire1003
  BorderLength = 0
  Face = 0
  Flip = false
  Heights = [3777.62,5500,3777.62,5500]
  HorizontalArea = 184176000
  IdRel = [-1,-1,-1,-1]
  IfcData = attributes={"GlobalId": {"name": "GlobalId", "type": "IfcGloballyUniqueId", "is_enum": false, "enum_values": []}, "Description": {"... (+613 chars omitted),+1 more (map truncated)
  IfcType = 113
  Material = -> Material007
  MoveBase = false
  MoveWithHost = false
  Overhang = [1000,700,1000,700]
  PerimeterLength = 0
  Placement = pos=(0,0,3250) rot=(0,0,1;0rad)
  PredefinedType = 0
  RidgeLength = 0
  Runs = [5500,5500,5500,5500]
  Thickness = [200,200,200,200]
  VerticalArea = 1.54748e+07
FEATURE [Part::MultiCommon] Common106  label="Stropilka_002"
  Placement = pos=(0,0,50) rot=(0,0,1;0rad)
  Shapes = -> [Common,Roof041]
FEATURE [Part::Part2DObjectPython] Wire1110  # Draft 2D object (typed FeaturePython)
  Area = 5.27766e+07
  ChamferSize = 0
  Closed = true
  End = (3495,-1255,0)
  FilletRadius = 0
  Length = 33150.8
  MakeFace = true
  Placement = pos=(-1249.99,-1255,0) rot=(0,0,1;0rad)
  Points = (8) [(0,0,0),(3812.61,5440,0),(9257.38,5440,0),(13070,9.09495e-13,0),(8324.99,2.27374e-13,0),(8324.99,-675,0),(4744.99,-675,0),(4744.99,9.09495e-13,0)]
  Start = (-1249.99,-1255,0)
  Subdivisions = 0
FEATURE [Part::FeaturePython] Structure695003007034  label="вычитаемый объём 005"  # Arch/BIM 52 (typed FeaturePython)
  Base = -> Wire1110
  FaceMaker = 0
  Height = 5000
  HorizontalArea = 5.27766e+07
  IfcData = complex_attributes={"OwnerHistory": {}, "IsNestedBy": {}, "IsDecomposedBy": {}, "IsDefinedBy": {}, "ObjectPlacement": {}, "Representation":... (+4 chars omitted)
  IfcType = 52
  Length = 0
  MoveBase = false
  MoveWithHost = false
  Nodes = (2) [(6040,886.738,0),(6040,886.738,4000)]
  NodesOffset = 0
  Normal = (0,0,1)
  PerimeterLength = 33150.8
  Placement = pos=(0,0,2500) rot=(0,0,1;0rad)
  VerticalArea = 1.65754e+08
  Width = 100
FEATURE [Part::MultiCommon] Common107  label="Stropilka_003"
  Shapes = -> [Array092,Structure695003007034]
FEATURE [Part::MultiCommon] Common108  label="Stropilka_004"
  Shapes = -> [Common107,Roof041]
FEATURE [Part::Cut] Cut105003022011  label="Stropilka_005"
  Base = -> Common108
  Placement = pos=(0,0,50) rot=(0,0,1;0rad)
  Tool = -> Extrude099005015
FEATURE [Part::FeaturePython] Structure695003007035  label="вычитаемый объём 006"  # Arch/BIM 52 (typed FeaturePython)
  Base = -> Wire1109
  FaceMaker = 0
  Height = 5000
  HorizontalArea = 2.08495e+07
  IfcData = complex_attributes={"OwnerHistory": {}, "IsNestedBy": {}, "IsDecomposedBy": {}, "IsDefinedBy": {}, "ObjectPlacement": {}, "Representation":... (+4 chars omitted)
  IfcType = 52
  Length = 0
  MoveBase = false
  MoveWithHost = false
  Nodes = (2) [(6040,886.738,0),(6040,886.738,4000)]
  NodesOffset = 0
  Normal = (0,0,1)
  PerimeterLength = 24186
  Placement = pos=(0,0,2500) rot=(0,0,1;0rad)
  VerticalArea = 1.2093e+08
  Width = 100
FEATURE [Part::FeaturePython] Structure695003007036  label="Плоскость стропила003"  # Arch/BIM 7 (typed FeaturePython)
  FaceMaker = 0
  Height = 6000
  HorizontalArea = 700000
  IfcType = 7
  Length = 14000
  Material = -> Material001
  MoveBase = false
  MoveWithHost = false
  Nodes = (2) [(0,1.81899e-16,-8.88178e-15),(0,1.81899e-16,17000)]
  NodesOffset = 0
  Normal = (0,0,0)
  PerimeterLength = 28100
  Placement = pos=(-1700,25,4500) rot=(0,0,1;0rad)
  PredefinedType = 0
  VerticalArea = 168600000
  Width = 50
FEATURE [Part::FeaturePython] Array093  # Draft array (typed FeaturePython)
  Angle = 360
  ArrayType = 0
  Axis = (0,0,1)
  Base = -> Structure695003007036
  Center = (0,0,0)
  Fuse = false
  IntervalAxis = (0,0,0)
  IntervalX = (1,0,0)
  IntervalY = (0,640,0)
  IntervalZ = (0,0,1)
  NumberPolar = 1
  NumberX = 1
  NumberY = 15
  NumberZ = 1
  Placement = pos=(0,-320,0) rot=(0,0,1;0rad)
FEATURE [Part::Mirroring] mirror016002022  label="вычитаемый объём 006 (mirrored)"
  Base = (5285,2800,0)
  Normal = (-1,0,0)
  Source = -> Structure695003007035
FEATURE [Part::MultiFuse] Fusion011003002002005003027  label="вычитаемый объём 007"
  Shapes = -> [mirror016002022,Structure695003007035]
FEATURE [Part::MultiCommon] Common109  label="Stropilka_006"
  Shapes = -> [Fusion011003002002005003027,Array093]
FEATURE [Part::MultiCommon] Common110  label="Stropilka_007"
  Placement = pos=(0,0,15) rot=(0,0,1;0rad)
  Shapes = -> [Roof041,Common109]
FEATURE [Part::Part2DObjectPython] Rectangle4238  # Draft 2D object (typed FeaturePython)
  Area = 0
  ChamferSize = 0
  Columns = 1
  FilletRadius = 0
  Height = 3485
  Length = 3269.79
  MakeFace = false
  Placement = pos=(3645.1,-400,0) rot=(0,0,1;0rad)
  Rows = 1
FEATURE [Part::Extrusion] Extrude099005028  label="cut_contour001"
  Base = -> Rectangle4238
  Dir = (0,0,1)
  DirMode = 2
  FaceMakerClass = Part::FaceMakerBullseye
  LengthFwd = 7500
  LengthRev = 0
  Solid = true
  Symmetric = false
FEATURE [Part::MultiCommon] Common111  label="Stropilka_008"
  Shapes = -> [Array092,Extrude099005028]
FEATURE [Part::MultiCommon] Common112  label="Stropilka_009"
  Shapes = -> [Common111,Extrude099005016]
FEATURE [Part::Cut] Cut105003022012  label="Stropilka_010"
  Base = -> Common112
  Placement = pos=(0,0,-50) rot=(0,0,1;0rad)
  Tool = -> Roof041
FEATURE [Part::Part2DObjectPython] Wire1111  # Draft 2D object (typed FeaturePython)
  Area = 1.71718e+06
  ChamferSize = 0
  Closed = true
  End = (11491.8,9156.7,3558.21)
  FilletRadius = 0
  Length = 14565.7
  MakeFace = true
  Placement = pos=(11491.8,9156.7,3841.05) rot=(-0.805454,-0.419073,0.419073;1.78548rad)
  Points = (4) [(0,0,0),(-6071.15,-3484.41,0),(-6071.15,-3201.56,1.36424e-11),(1.81899e-11,282.843,1.36424e-11)]
  Start = (11491.8,9156.7,3841.05)
  Subdivisions = 0
FEATURE [Part::FeaturePython] Structure695003007037  label="Плита"  # Arch/BIM 118 (typed FeaturePython)
  Base = -> Wire1111
  FaceMaker = 0
  Height = 75
  HorizontalArea = 0
  IfcData = attributes={"GlobalId": {"name": "GlobalId", "type": "IfcGloballyUniqueId", "is_enum": false, "enum_values": []}, "Description": {"... (+453 chars omitted),+1 more (map truncated)
  IfcType = 118
  Length = 0
  MoveBase = false
  MoveWithHost = false
  Nodes = (4) [(14111.5,5722.51,-5441.84),(7773.64,5722.51,-8413.74),(8005.27,5722.51,-8576.07),(14343.1,5722.51,-5604.17)]
  NodesOffset = 0
  Normal = (0,0,0)
  PerimeterLength = 12217.3
  PredefinedType = 0
  VerticalArea = 3.47679e+06
  Width = 70
FEATURE [Part::FeaturePython] Structure695003007038  label="Плита001"  # Arch/BIM 118 (typed FeaturePython)
  Base = -> Wire1111
  FaceMaker = 0
  Height = 75
  HorizontalArea = 0
  IfcData = attributes={"GlobalId": {"name": "GlobalId", "type": "IfcGloballyUniqueId", "is_enum": false, "enum_values": []}, "Description": {"... (+453 chars omitted),+1 more (map truncated)
  IfcType = 118
  Length = 0
  MoveBase = false
  MoveWithHost = false
  Nodes = (4) [(14111.5,5722.51,-5441.84),(7773.64,5722.51,-8413.74),(8005.27,5722.51,-8576.07),(14343.1,5722.51,-5604.17)]
  NodesOffset = 0
  Normal = (0,0,0)
  PerimeterLength = 12217.3
  Placement = pos=(-61.4179,43.0446,0) rot=(0,0,1;0rad)
  PredefinedType = 0
  VerticalArea = 3.47679e+06
  Width = 70
FEATURE [Part::MultiFuse] Fusion011003002002005003028  label="диагональное стропило"
  Shapes = -> [Structure695003007038,Structure695003007037]
FEATURE [Part::Mirroring] mirror016002023  label="диагональное стропило (mirrored)"
  Base = (-560,4185,0)
  Normal = (1e-16,-1,0)
  Source = -> Fusion011003002002005003028
FEATURE [Part::Mirroring] mirror016002024  label="диагональное стропило (mirrored)001"
  Base = (5285,2800,0)
  Normal = (-1,0,0)
  Source = -> Fusion011003002002005003028
FEATURE [Part::Mirroring] mirror016002025  label="диагональное стропило (mirrored) (mirrored)"
  Base = (5285,2800,0)
  Normal = (-1,0,0)
  Source = -> mirror016002023
FEATURE [Part::MultiFuse] Fusion011003002002005003029  label="диагональное стропило all"
  Shapes = -> [mirror016002024,Fusion011003002002005003028,mirror016002025,mirror016002023]
FEATURE [Part::FeaturePython] Structure695003007039  label="Структура078"  # Arch/BIM 172 (typed FeaturePython)
  Base = -> Wire817
  FaceMaker = 0
  Height = 1000
  HorizontalArea = 147603200
  IfcData = attributes={"GlobalId": {"name": "GlobalId", "type": "IfcGloballyUniqueId", "is_enum": false, "enum_values": []}, "Description": {"... (+484 chars omitted),+1 more (map truncated)
  IfcType = 172
  Length = 0
  MoveBase = false
  MoveWithHost = false
  Nodes = (2) [(1146.63,4298.06,0),(1146.63,4298.06,1000)]
  NodesOffset = 0
  Normal = (0,0,1)
  PerimeterLength = 50640
  Placement = pos=(0,0,4350) rot=(0,0,1;0rad)
  PredefinedType = 0
  VerticalArea = 50640000
  Width = 100
FEATURE [Part::Cut] Cut105003022015  label="Stropilka_011"
  Base = -> Cut105003022012
  Tool = -> Structure695003007039
FEATURE [Part::MultiFuse] Fusion011003002002005003030  label="Stropilka_all_001"
  Shapes = -> [Fusion011003002002005003029,Common106,Cut105003022011,Common110,Cut105003022015]
FEATURE [Part::Cut] Cut105003022013  label="Stropilka_all_002"
  Base = -> Fusion011003002002005003030
  Tool = -> Fusion011003002002005003022
FEATURE [Part::Part2DObjectPython] ShapeString291  # Draft 2D object (typed FeaturePython)
  FontFile = <path>
  Placement = pos=(3071.38,19849.8,0) rot=(0,0,1;0rad)
  Size = 800
  String = уклон 7%
  Tracking = 0
FEATURE [Part::Part2DObjectPython] ShapeString292  # Draft 2D object (typed FeaturePython)
  FontFile = <path>
  Placement = pos=(-10391.1,34212.9,0) rot=(0,0,-1;0.11726rad)
  Size = 800
  String = дренажная канава
  Tracking = 0
FEATURE [App::DocumentObjectGroup] Group139  label="Работы по планировке участка"
  Group = -> [ShapeString288,ShapeString286,Wire1090,ShapeString285,Line2269,Line2268,Line2267,ShapeString284,ShapeString283,ShapeString281,ShapeString280,ShapeString279,Wire1091,ShapeString290,ShapeString282,Wire1092,ShapeString291,ShapeString292]
FEATURE [Part::Part2DObjectPython] Line2293  # Draft 2D object (typed FeaturePython)
  Area = 0
  ChamferSize = 0
  Closed = true
  End = (8085,4185,0)
  FilletRadius = 0
  Length = 6000
  MakeFace = true
  Placement = pos=(144.138,-1520,0) rot=(0,0,1;0rad)
  Points = (2) [(7940.86,5705,0),(7940.86,5705,0)]
  Start = (8085,4185,0)
  Subdivisions = 0
FEATURE [Part::FeaturePython] Wall587019  label="прогон коньковый"  # Arch/BIM 166 (typed FeaturePython)
  Align = 2
  Area = 1120000
  Base = -> Line2293
  BlockHeight = 0
  BlockLength = 0
  CountBroken = 0
  CountEntire = 0
  Face = 0
  GlobalId = 1B71KP0Y9AOfuyJlUXW0eC
  Height = 200
  HorizontalArea = 840000
  IfcData = IfcUID=1B71KP0Y9AOfuyJlUXW0eC; attributes={"GlobalId": {"value": "1B71KP0Y9AOfuyJlUXW0eC"}}
  IfcType = 166
  Joint = 0
  Length = 5600
  MakeBlocks = false
  Material = -> Material
  MoveBase = false
  MoveWithHost = false
  Normal = (0,0,0)
  Offset = 15
  OffsetFirst = 0
  OffsetSecond = 0
  PerimeterLength = 11500
  Placement = pos=(0,0,6900) rot=(0,0,1;0rad)
  PredefinedType = 0
  VerticalArea = 2300000
  Width = 150
FEATURE [Part::Part2DObjectPython] Rectangle4239  # Draft 2D object (typed FeaturePython)
  Area = 22500
  ChamferSize = 0
  Columns = 1
  FilletRadius = 0
  Height = 150
  Length = 150
  MakeFace = true
  Placement = pos=(3535,4110,0) rot=(0,0,1;0rad)
  Rows = 1
FEATURE [Part::FeaturePython] Structure695003007040  label="Стойка под конёк 013"  # Arch/BIM 172 (typed FeaturePython)
  Base = -> Rectangle4239
  FaceMaker = 0
  Height = 3765
  HorizontalArea = 22500
  IfcData = attributes={"GlobalId": {"name": "GlobalId", "type": "IfcGloballyUniqueId", "is_enum": false, "enum_values": []}, "Description": {"... (+484 chars omitted),+1 more (map truncated)
  IfcType = 172
  Length = 0
  Material = -> Material
  MoveBase = false
  MoveWithHost = false
  Nodes = (2) [(3610,3010,0),(3610,3010,2935)]
  NodesOffset = 0
  Normal = (0,0,0)
  PerimeterLength = 600
  Placement = pos=(0,0,3135) rot=(0,0,1;0rad)
  PredefinedType = 0
  VerticalArea = 2259000
  Width = 100
FEATURE [Part::Part2DObjectPython] Rectangle4240  # Draft 2D object (typed FeaturePython)
  Area = 22500
  ChamferSize = 0
  Columns = 1
  FilletRadius = 0
  Height = 150
  Length = 150
  MakeFace = true
  Placement = pos=(6910,4600,0) rot=(0,0,1;0rad)
  Rows = 1
FEATURE [Part::FeaturePython] Structure695003007041  label="Стойка 014"  # Arch/BIM 172 (typed FeaturePython)
  Base = -> Rectangle4240
  FaceMaker = 0
  Height = 3085
  HorizontalArea = 22500
  IfcData = attributes={"GlobalId": {"name": "GlobalId", "type": "IfcGloballyUniqueId", "is_enum": false, "enum_values": []}, "Description": {"... (+484 chars omitted),+1 more (map truncated)
  IfcType = 172
  Length = 0
  Material = -> Material
  MoveBase = false
  MoveWithHost = false
  Nodes = (2) [(3610,3010,0),(3610,3010,2935)]
  NodesOffset = 0
  Normal = (0,0,0)
  PerimeterLength = 600
  Placement = pos=(0,0,3135) rot=(0,0,1;0rad)
  PredefinedType = 0
  VerticalArea = 1851000
  Width = 100
FEATURE [Part::Part2DObjectPython] Rectangle4241  # Draft 2D object (typed FeaturePython)
  Area = 22500
  ChamferSize = 0
  Columns = 1
  FilletRadius = 0
  Height = 150
  Length = 150
  MakeFace = true
  Placement = pos=(6910,4110,0) rot=(0,0,1;0rad)
  Rows = 1
FEATURE [Part::FeaturePython] Structure695003007042  label="Стойка под конёк 015"  # Arch/BIM 172 (typed FeaturePython)
  Base = -> Rectangle4241
  FaceMaker = 0
  Height = 530
  HorizontalArea = 22500
  IfcData = attributes={"GlobalId": {"name": "GlobalId", "type": "IfcGloballyUniqueId", "is_enum": false, "enum_values": []}, "Description": {"... (+484 chars omitted),+1 more (map truncated)
  IfcType = 172
  Length = 0
  Material = -> Material
  MoveBase = false
  MoveWithHost = false
  Nodes = (2) [(3610,3010,0),(3610,3010,2935)]
  NodesOffset = 0
  Normal = (0,0,0)
  PerimeterLength = 600
  Placement = pos=(0,-9.09e-13,6370) rot=(0,0,1;0rad)
  PredefinedType = 0
  VerticalArea = 318000
  Width = 100
FEATURE [App::GeometryPython] BuildingPart112  label="Стойки конька"  # Arch/BIM 172 (typed FeaturePython)
  Area = 0
  Group = -> [Structure440,Structure441,Structure442,Structure443,Structure695003007040,Structure695003007041,Structure695003007042]
  Height = 0
  HeightPropagate = true
  IfcData = attributes={"GlobalId": {"name": "GlobalId", "type": "IfcGloballyUniqueId", "is_enum": false, "enum_values": []}, "Description": {"... (+484 chars omitted),+1 more (map truncated)
  IfcType = 172
  LevelOffset = 0
  Placement = pos=(0,0,3130) rot=(0,0,1;0rad)
  PredefinedType = 0
FEATURE [Part::Part2DObjectPython] Line2294  # Draft 2D object (typed FeaturePython)
  Area = 0
  ChamferSize = 0
  Closed = false
  End = (3735,4185,0)
  FilletRadius = 0
  Length = 250
  MakeFace = true
  Placement = pos=(3485,4185,0) rot=(0,0,1;0rad)
  Points = (2) [(0,0,0),(250,0,0)]
  Start = (3485,4185,0)
  Subdivisions = 0
FEATURE [Part::FeaturePython] Wall587020  label="Кладка под стойки 005"  # Arch/BIM 166 (typed FeaturePython)
  Align = 2
  Area = 37500
  Base = -> Line2294
  BlockHeight = 65
  BlockLength = 250
  CountBroken = 1
  CountEntire = 0
  Face = 0
  Height = 150
  HorizontalArea = 62500
  IfcData = attributes={"GlobalId": {"name": "GlobalId", "type": "IfcGloballyUniqueId", "is_enum": false, "enum_values": []}, "Description": {"... (+533 chars omitted),+1 more (map truncated)
  IfcType = 166
  Joint = 12000
  Length = 250
  MakeBlocks = false
  Material = -> Material008
  MoveBase = false
  MoveWithHost = false
  Normal = (0,0,0)
  OffsetFirst = 120
  OffsetSecond = 200
  PerimeterLength = 1000
  Placement = pos=(0,0,2960) rot=(0,0,1;0rad)
  PredefinedType = 0
  VerticalArea = 150000
  Width = 250
FEATURE [App::GeometryPython] BuildingPart110  label="Кладка под стойки"  # Arch/BIM 172 (typed FeaturePython)
  Area = 509600
  Group = -> [Wall336,Wall337,Wall338,Wall339,Wall587020]
  Height = 170
  HeightPropagate = true
  IfcData = attributes={"GlobalId": {"name": "GlobalId", "type": "IfcGloballyUniqueId", "is_enum": false, "enum_values": []}, "Description": {"... (+484 chars omitted),+1 more (map truncated)
  IfcType = 172
  LevelOffset = 0
  Placement = pos=(0,0,2965) rot=(0,0,1;0rad)
  PredefinedType = 0
FEATURE [Part::Part2DObjectPython] Wire1047  # Draft 2D object (typed FeaturePython)
  Area = 0
  ChamferSize = 0
  Closed = true
  End = (5835,5055,0)
  FilletRadius = 0
  Length = 9410
  MakeFace = false
  Placement = pos=(5575,5315,0) rot=(0,0,1;0rad)
  Points = (9) [(260,-520,0),(260,-780,0),(1260,-780,0),(1260,370,0),(1335,370,0),(1335,2850,0),(260,2850,0),(260,83.3281,0),(260,-260,0)]
  Start = (5835,4795,0)
  Subdivisions = 0
FEATURE [Part::Feature] Compound006042005002  label="шкаф 60х60 секция 024"
  Placement = pos=(-16615,4565,0) rot=(0,0,1;0rad)
  shape: bbox 600 x 600 x 2e-07 mm, 0 faces, 0 solids (baked)
FEATURE [Part::Feature] Compound006042005003  label="шкаф 60х60 секция 025"
  Placement = pos=(-16615,5165,0) rot=(0,0,1;0rad)
  shape: bbox 600 x 600 x 2e-07 mm, 0 faces, 0 solids (baked)
FEATURE [Part::Feature] Compound006042005004  label="шкаф 60х60 секция 026"
  Placement = pos=(-16615,5765,0) rot=(0,0,1;0rad)
  shape: bbox 600 x 600 x 2e-07 mm, 0 faces, 0 solids (baked)
FEATURE [Part::Feature] Compound006042005005  label="шкаф 60х60 секция 027"
  Placement = pos=(-17465,5975,0) rot=(0,0,1;0rad)
  shape: bbox 600 x 600 x 2e-07 mm, 0 faces, 0 solids (baked)
FEATURE [App::DocumentObjectGroup] Group137  label="План мансарда тест"
  Group = -> [Clone2D011,Clone2D012,Clone2D013,Rectangle4046,Clone2D015,Clone2D016,Clone2D017,Clone2D018,Clone2D019,Clone005,Line2124,Rectangle4051,Rectangle4052,Clone006,Clone007,Clone008,Clone009,Rectangle4054,Rectangle4055,Rectangle4056,Rectangle4057,Line2125,Wire1047,Rectangle4059,Arc162,Line2126,Line2127,Arc163,Rectangle4060,Rectangle4061,Arc164,Line2128,Rectangle4063,Rectangle4064,Rectangle4066,+107 more]
FEATURE [App::DocumentObjectGroup] Group131  label="Draft"
  Group = -> [Group134,Group136,Group137]
FEATURE [Part::Part2DObjectPython] Rectangle4242  label="монолитный участок 002"  # Draft 2D object (typed FeaturePython)
  Area = 0
  ChamferSize = 0
  Columns = 1
  FilletRadius = 0
  Height = 250
  Length = 1130
  MakeFace = false
  Placement = pos=(5815,8165,0) rot=(0,0,1;0rad)
  Rows = 1
FEATURE [Part::FeaturePython] Structure695003007044  label="монолитный участок001"  # Arch/BIM 172 (typed FeaturePython)
  Base = -> Rectangle4242
  FaceMaker = 0
  Height = 160
  HorizontalArea = 282500
  IfcData = attributes={"GlobalId": {"name": "GlobalId", "type": "IfcGloballyUniqueId", "is_enum": false, "enum_values": []}, "Description": {"... (+484 chars omitted),+1 more (map truncated)
  IfcType = 172
  Length = 0
  Material = -> Material018
  MoveBase = false
  MoveWithHost = false
  Nodes = (2) [(6380,8290,0),(6380,8290,160)]
  NodesOffset = 0
  Normal = (0,0,0)
  PerimeterLength = 2760
  Placement = pos=(0,0,2800) rot=(0,0,1;0rad)
  PredefinedType = 0
  VerticalArea = 441600
  Width = 100
FEATURE [App::GeometryPython] BuildingPart006  label="Перекрытие плитами ПНО"  # Arch/BIM 52 (typed FeaturePython)
  Area = 13216000
  GlobalId = 29arHl4sD0PxQq1DVpDEyo
  Group = -> [Component197,Component241026,Component241027,Component241028,Component241029,Structure551,Wall583,Wall242,Structure695003007044]
  Height = 0
  HeightPropagate = true
  IfcData = IfcUID=29arHl4sD0PxQq1DVpDEyo,attributes={"GlobalId": {"value": "29arHl4sD0PxQq1DVpDEyo"}},+1 more (map truncated)
  IfcType = 52
  LevelOffset = 0
  Placement = pos=(0,0,5) rot=(0,0,1;0rad)
FEATURE [App::GeometryPython] BuildingPart016  label="Конструкции перекрытия"  # Arch/BIM 52 (typed FeaturePython)
  Area = 338807100
  GlobalId = 3lFo00xcPACR0FdWtYITp1
  Group = -> [BuildingPart006,BuildingPart097,BuildingPart099,BuildingPart110,Wall584]
  Height = 0
  HeightPropagate = true
  IfcData = IfcUID=3lFo00xcPACR0FdWtYITp1,attributes={"GlobalId": {"value": "3lFo00xcPACR0FdWtYITp1"}},+1 more (map truncated)
  IfcType = 52
  LevelOffset = 0
  Placement = pos=(0,0,5) rot=(0,0,1;0rad)
FEATURE [Part::FeaturePython] Wall587021  label="Стена"  # Arch/BIM 166 (typed FeaturePython)
  Align = 2
  Area = 188200
  Base = -> Wire1047
  BlockHeight = 0
  BlockLength = 0
  CountBroken = 0
  CountEntire = 0
  Face = 0
  Height = 20
  HorizontalArea = 564600
  IfcData = attributes={"GlobalId": {"name": "GlobalId", "type": "IfcGloballyUniqueId", "is_enum": false, "enum_values": []}, "Description": {"... (+533 chars omitted),+1 more (map truncated)
  IfcType = 166
  Joint = 0
  Length = 9410
  MakeBlocks = false
  MoveBase = false
  MoveWithHost = false
  Normal = (0,0,-1)
  OffsetFirst = 0
  OffsetSecond = 0
  PerimeterLength = 9650
  Placement = pos=(0,0,3165) rot=(0,0,1;0rad)
  PredefinedType = 0
  VerticalArea = 376400
  Width = 60
FEATURE [Part::FeaturePython] Structure695003007043  label="Люк на мансарду (закр.)"  # Arch/BIM 118 (typed FeaturePython)
  Additions = -> [Wall587021]
  Base = -> Wire1047
  FaceMaker = 0
  Height = 170
  HorizontalArea = 4101900
  IfcData = attributes={"GlobalId": {"name": "GlobalId", "type": "IfcGloballyUniqueId", "is_enum": false, "enum_values": []}, "Description": {"... (+453 chars omitted),+1 more (map truncated)
  IfcType = 118
  Length = 0
  MoveBase = false
  MoveWithHost = false
  Nodes = (9) [(5835,4795,0),(5835,4535,0),(6835,4535,0),(6835,5685,0),(6910,5685,0),(6910,8165,0),(5835,8165,0),(5835,5398.33,0),(5835,5055,0)]
  NodesOffset = 0
  Normal = (0,0,-1)
  PerimeterLength = 9650
  Placement = pos=(0,0,3165) rot=(0,0,1;0rad)
  PredefinedType = 0
  VerticalArea = 1.6045e+06
  Width = 70
FEATURE [Part::FeaturePython] Component241079  label="Люк на мансарду (откр.)"  # Arch/BIM 0 (typed FeaturePython)
  Base = -> Structure695003007043
  HorizontalArea = 0
  IfcData = attributes={"GlobalId": {"name": "GlobalId", "type": "IfcGloballyUniqueId", "is_enum": false, "enum_values": []}, "Description": {"... (+538 chars omitted),+1 more (map truncated)
  IfcType = 0
  Material = -> Material008
  MoveBase = false
  MoveWithHost = false
  PerimeterLength = 0
  Placement = pos=(0,2414.4,8953.88) rot=(-1,0,0;0.785398rad)
  PredefinedType = 0
  VerticalArea = 0
FEATURE [Part::Part2DObjectPython] ShapeString293  # Draft 2D object (typed FeaturePython)
  FontFile = <path>
  Placement = pos=(6021.58,8208.14,0) rot=(0,0,1;0rad)
  Size = 130
  String = Монолитн.
  Tracking = 0
FEATURE [App::GeometryPython] BuildingPart142  label="Перекрытие (план раскладки плит)"  # Arch/BIM 172 (typed FeaturePython)
  Area = 0
  Group = -> [ShapeString255,ShapeString257,ShapeString258,ShapeString259,ShapeString260,ShapeString262,ShapeString264,ShapeString265,ShapeString266,ShapeString267,ShapeString268,ShapeString269,ShapeString270,ShapeString271,ShapeString272,ShapeString273,ShapeString274,ShapeString275,ShapeString276,ShapeString293]
  Height = 0
  HeightPropagate = true
  IfcData = attributes={"GlobalId": {"name": "GlobalId", "type": "IfcGloballyUniqueId", "is_enum": false, "enum_values": []}, "Description": {"... (+484 chars omitted),+1 more (map truncated)
  IfcType = 172
  LevelOffset = 0
  PredefinedType = 0
FEATURE [App::FeaturePython] Section011  label="Section (план раскладки плит)"  # WARN: FeaturePython — macro-defined, semantics opaque (R4)
  Clip = false
  Objects = -> [BuildingPart006,BuildingPart142]
  OnlySolids = true
  Placement = pos=(6370.85,4338.46,3000) rot=(0,0,1;0rad)
  UseMaterialColorForFill = true
FEATURE [TechDraw::DrawViewArch] ArchView011  label="Раскладка плит 001"
  AllOn = true
  CutLineWidth = 0.1
  FillSpaces = false
  FontSize = 12
  JoinArch = false
  LineWidth = 0.25
  LockPosition = true
  RenderMode = 0
  Rotation = 0
  Scale = 0.02
  ScaleType = 2
  ShowFill = true
  ShowHidden = false
  Source = -> Section011
  Symbol = <blob: 365265 chars omitted>
  X = 210
  Y = 150
FEATURE [TechDraw::DrawPage] Page009  label="План раскладки плит"
  KeepUpdated = false
  NextBalloonIndex = 1
  ProjectionType = 0
  Template = -> Template009
  Views = -> [ArchView011,Annotation039]
FEATURE [Part::Box] Box3305  label="Монитор 32" 003"
  AttacherType = Attacher::AttachEngine3D
  Height = 450
  Length = 750
  Placement = pos=(10447.3,4560,4000) rot=(0,0,-1;1.5708rad)
  Width = 50
FEATURE [App::GeometryPython] BuildingPart126  label="Мебель (мансарда)"  # Arch/BIM 172 (typed FeaturePython)
  Area = 0
  Group = -> [Component167,Component169,Fusion011003002002002,Box3265,Box3266,Fusion011003002002003,Fusion011003002002005001,Fusion011003002002005002,Structure580,Structure581,Structure582,Structure583,Structure584,Compound006041001,Compound006042001,Compound006041002,Box3305]
  Height = 0
  HeightPropagate = true
  IfcData = attributes={"GlobalId": {"name": "GlobalId", "type": "IfcGloballyUniqueId", "is_enum": false, "enum_values": []}, "Description": {"... (+484 chars omitted),+1 more (map truncated)
  IfcType = 172
  LevelOffset = 0
  Placement = pos=(0,0,5) rot=(0,0,1;0rad)
  PredefinedType = 0
FEATURE [App::GeometryPython] BuildingPart125  label="Обстановка (мансарда)"  # Arch/BIM 172 (typed FeaturePython)
  Area = 3.228e+06
  Group = -> [BuildingPart124,BuildingPart126]
  Height = 0
  HeightPropagate = true
  IfcData = attributes={"GlobalId": {"name": "GlobalId", "type": "IfcGloballyUniqueId", "is_enum": false, "enum_values": []}, "Description": {"... (+484 chars omitted),+1 more (map truncated)
  IfcType = 172
  LevelOffset = 0
  Placement = pos=(0,0,3135) rot=(0,0,1;0rad)
  PredefinedType = 0
FEATURE [Part::Part2DObjectPython] Rectangle4243  label="Контур по блоку ЛСР38 внешний002"  # Draft 2D object (typed FeaturePython)
  Area = 0
  ChamferSize = 0
  Columns = 1
  FilletRadius = 0
  Height = 9220
  Length = 11430
  MakeFace = false
  Placement = pos=(-430,-425,0) rot=(0,0,1;0rad)
  Rows = 1
FEATURE [Part::FeaturePython] Structure451  label="Балка крыльца 002"  # Arch/BIM 7 (typed FeaturePython)
  FaceMaker = 0
  Height = 100
  HorizontalArea = 0
  IfcData = attributes={"GlobalId": {"name": "GlobalId", "type": "IfcGloballyUniqueId", "is_enum": false, "enum_values": []}, "Description": {"... (+475 chars omitted),+1 more (map truncated)
  IfcType = 7
  Length = 3280
  Material = -> Material
  MoveBase = false
  MoveWithHost = false
  Nodes = (2) [(0,-1.42109e-15,-1.94289e-16),(3280,-1.42109e-15,7.28112e-13)]
  NodesOffset = 0
  Normal = (0,0,0)
  PerimeterLength = 0
  Placement = pos=(3645,-1456.07,3060.87) rot=(1,0,0;0.610865rad)
  PredefinedType = 0
  VerticalArea = 30000
  Width = 150
FEATURE [Part::FeaturePython] Structure452  label="Балка крыльца 001"  # Arch/BIM 7 (typed FeaturePython)
  FaceMaker = 0
  Height = 100
  HorizontalArea = 0
  IfcData = attributes={"GlobalId": {"name": "GlobalId", "type": "IfcGloballyUniqueId", "is_enum": false, "enum_values": []}, "Description": {"... (+475 chars omitted),+1 more (map truncated)
  IfcType = 7
  Length = 3800
  Material = -> Material
  MoveBase = false
  MoveWithHost = false
  Nodes = (2) [(0,-1.42109e-15,-1.94289e-16),(3800,-1.42109e-15,8.43575e-13)]
  NodesOffset = 0
  Normal = (0,0,0)
  PerimeterLength = 0
  Placement = pos=(10305,9826.07,3060.87) rot=(0,0.300706,0.953717;3.14159rad)
  PredefinedType = 0
  VerticalArea = 30000
  Width = 150
FEATURE [App::GeometryPython] BuildingPart101  label="Элементы арх.декора"  # Arch/BIM 52 (typed FeaturePython)
  Area = 0
  GlobalId = 1dA3$MPA5FehwTwOMwm9Bl
  Group = -> [Extrude099002,Extrude099003,Extrude099004,Extrude099005,Structure452,Structure451]
  Height = 0
  HeightPropagate = true
  IfcData = IfcUID=1dA3$MPA5FehwTwOMwm9Bl,+2 more (map truncated)
  IfcType = 52
  LevelOffset = 0
FEATURE [Part::FeaturePython] Wall057  label="мауэрлат 001"  # Arch/BIM 166 (typed FeaturePython)
  Align = 1
  Area = 4130000
  Base = -> Rectangle4243
  BlockHeight = 0
  BlockLength = 0
  CountBroken = 0
  CountEntire = 0
  Face = 0
  GlobalId = 1B71KP0Y9AOfuyJlUXW0eC
  Height = 100
  HorizontalArea = 5979000
  IfcData = IfcUID=1B71KP0Y9AOfuyJlUXW0eC; attributes={"GlobalId": {"value": "1B71KP0Y9AOfuyJlUXW0eC"}}
  IfcType = 166
  Joint = 0
  Length = 41300
  MakeBlocks = false
  Material = -> Material
  MoveBase = false
  MoveWithHost = false
  Normal = (0,0,0)
  Offset = 105
  OffsetFirst = 0
  OffsetSecond = 0
  PerimeterLength = 40460
  Placement = pos=(0,0,3875) rot=(0,0,1;0rad)
  PredefinedType = 0
  VerticalArea = 7972000
  Width = 150
FEATURE [App::GeometryPython] BuildingPart113  label="Стойки и прогоны"  # Arch/BIM 172 (typed FeaturePython)
  Area = 12134000
  Group = -> [BuildingPart112,Wall556,Wall557,Wall558,Wall559,Wall625,Wall624,Wall587019,Wall057]
  Height = 0
  HeightPropagate = true
  IfcData = attributes={"GlobalId": {"name": "GlobalId", "type": "IfcGloballyUniqueId", "is_enum": false, "enum_values": []}, "Description": {"... (+484 chars omitted),+1 more (map truncated)
  IfcType = 172
  LevelOffset = 0
  PredefinedType = 0
FEATURE [App::GeometryPython] BuildingPart104  label="Уровень  мансарды"  # Arch/BIM 14 (typed FeaturePython)
  Area = 399065300
  CompositionType = 0
  Elevation = 3135
  GlobalId = 2Sd2b8p9H2Ff7iaZY3OzqZ
  Group = -> [BuildingPart016,BuildingPart,BuildingPart125,BuildingPart133,BuildingPart136,BuildingPart113,BuildingPart137,Component241079]
  Height = 3135
  HeightPropagate = true
  IfcData = IfcUID=2Sd2b8p9H2Ff7iaZY3OzqZ,+2 more (map truncated)
  IfcType = 14
  LevelOffset = 0
  LongName = Floor
  Placement = pos=(-560,-540,3135) rot=(0,0,1;0rad)
  expr: Elevation = .Placement.Base.z
FEATURE [Part::MultiFuse] Fusion  label="cut_stropilka_001"
  Shapes = -> [Wall057,Wall557,Wall559,Wall587019]
FEATURE [Part::MultiFuse] Fusion011003002002005003031  label="Fusion011"
  Shapes = -> [Structure681,Structure560,Fusion,Fusion076]
FEATURE [Part::Cut] Cut105003022014  label="Stropilka_all_003"
  Base = -> Cut105003022013
  Tool = -> Fusion011003002002005003031
FEATURE [Part::FeaturePython] Component241078  label="Стропилка (доска 50х200 сухая антисептированная)"  # Arch/BIM 0 (typed FeaturePython)
  Base = -> Cut105003022014
  HorizontalArea = 0
  IfcData = attributes={"GlobalId": {"name": "GlobalId", "type": "IfcGloballyUniqueId", "is_enum": false, "enum_values": []}, "Description": {"... (+538 chars omitted),+1 more (map truncated)
  IfcType = 0
  Material = -> Material
  MoveBase = false
  MoveWithHost = false
  PerimeterLength = 0
  PredefinedType = 0
  VerticalArea = 0
FEATURE [App::GeometryPython] BuildingPart106  label="Кровля"  # Arch/BIM 52 (typed FeaturePython)
  Area = 0
  GlobalId = 3O6XTUJY1FTBF6rjo3DaEi
  Group = -> [Component,Component241037,Component241077,Component241078]
  Height = 0
  HeightPropagate = true
  IfcData = IfcUID=3O6XTUJY1FTBF6rjo3DaEi,+2 more (map truncated)
  IfcType = 52
  LevelOffset = 0
FEATURE [App::FeaturePython] Section007  label="Section 2nd floor plan"  # WARN: FeaturePython — macro-defined, semantics opaque (R4)
  Clip = false
  Objects = -> [BuildingPart104,BuildingPart087,BuildingPart106,BuildingPart137,Wall305,Wall300,BuildingPart127,BuildingPart131]
  OnlySolids = true
  Placement = pos=(6260,3730,4600) rot=(0,0,1;0rad)
  UseMaterialColorForFill = true
FEATURE [TechDraw::DrawViewArch] ArchView008
  AllOn = true
  CutLineWidth = 0.1
  FillSpaces = false
  FontSize = 7
  JoinArch = false
  LineWidth = 0.1
  LockPosition = true
  RenderMode = 0
  Rotation = 0
  Scale = 0.02
  ScaleType = 2
  ShowFill = true
  ShowHidden = true
  Source = -> Section007
  Symbol = <blob: 584225 chars omitted>
  X = 210
  Y = 150
FEATURE [TechDraw::DrawPage] Page003  label="План мансарда"
  KeepUpdated = false
  NextBalloonIndex = 1
  ProjectionType = 0
  Template = -> Template003
  Views = -> [ArchView008,Annotation031]
FEATURE [TechDraw::DrawSVGTemplate] Template010
  EditableTexts = Лист=10; Номер=ИЖС-2022.0003
  Height = 297
  Orientation = 1
  Width = 420
FEATURE [Part::Part2DObjectPython] Clone2D  label="Circle124 (2D) (2D)"  # Draft 2D object (typed FeaturePython)
  Fuse = false
  Objects = -> [Clone2D030]
  Placement = pos=(-1854.18,8605,0) rot=(0,0,1;0rad)
  Scale = (1,1,1)
FEATURE [Part::Part2DObjectPython] Clone2D042  label="ShapeString193 (2D) (2D)"  # Draft 2D object (typed FeaturePython)
  Fuse = false
  Objects = -> [Clone2D031]
  Placement = pos=(-1950.61,8511.85,0) rot=(0,0,1;0rad)
  Scale = (1,1,1)
FEATURE [Part::Part2DObjectPython] Clone2D043  label="Circle125 (2D) (2D)"  # Draft 2D object (typed FeaturePython)
  Fuse = false
  Objects = -> [Clone2D028]
  Placement = pos=(-1854.18,3080,0) rot=(0,0,1;0rad)
  Scale = (1,1,1)
FEATURE [Part::Part2DObjectPython] Clone2D044  label="ShapeString194 (2D) (2D)"  # Draft 2D object (typed FeaturePython)
  Fuse = false
  Objects = -> [Clone2D029]
  Placement = pos=(-1933.86,2991.01,0) rot=(0,0,1;0rad)
  Scale = (1,1,1)
FEATURE [Part::Part2DObjectPython] Clone2D045  label="Circle126 (2D) (2D)"  # Draft 2D object (typed FeaturePython)
  Fuse = false
  Objects = -> [Clone2D026]
  Placement = pos=(-1854.18,-235,0) rot=(0,0,1;0rad)
  Scale = (1,1,1)
FEATURE [Part::Part2DObjectPython] Clone2D046  label="ShapeString195 (2D) (2D)"  # Draft 2D object (typed FeaturePython)
  Fuse = false
  Objects = -> [Clone2D027]
  Placement = pos=(-1941.5,-327.945,0) rot=(0,0,1;0rad)
  Scale = (1,1,1)
FEATURE [Part::FeaturePython] Component241080  label="Компонент045"  # Arch/BIM 0 (typed FeaturePython)
  CloneOf = -> Component241069
  HorizontalArea = 0
  IfcData = attributes={"GlobalId": {"name": "GlobalId", "type": "IfcGloballyUniqueId", "is_enum": false, "enum_values": []}, "Description": {"... (+538 chars omitted),+1 more (map truncated)
  IfcType = 0
  MoveBase = false
  MoveWithHost = false
  PerimeterLength = 0
  Placement = pos=(12023.1,-555,0) rot=(0,0,1;1.5708rad)
  PredefinedType = 0
  VerticalArea = 0
FEATURE [Part::Part2DObjectPython] Clone2D047  label="Circle127 (2D) (2D)"  # Draft 2D object (typed FeaturePython)
  Fuse = false
  Objects = -> [Clone2D032]
  Placement = pos=(-240,10797.3,0) rot=(0,0,1;0rad)
  Scale = (1,1,1)
FEATURE [Part::Part2DObjectPython] Clone2D048  label="ShapeString196 (2D) (2D)"  # Draft 2D object (typed FeaturePython)
  Fuse = false
  Objects = -> [Clone2D033]
  Placement = pos=(-319.076,10705,0) rot=(0,0,1;0rad)
  Scale = (1,1,1)
FEATURE [Part::FeaturePython] Component241081  label="Компонент046"  # Arch/BIM 0 (typed FeaturePython)
  CloneOf = -> Component241070
  HorizontalArea = 0
  IfcData = attributes={"GlobalId": {"name": "GlobalId", "type": "IfcGloballyUniqueId", "is_enum": false, "enum_values": []}, "Description": {"... (+538 chars omitted),+1 more (map truncated)
  IfcType = 0
  MoveBase = false
  MoveWithHost = false
  PerimeterLength = 0
  Placement = pos=(-560,-2295.53,0) rot=(0,0,1;0rad)
  PredefinedType = 0
  VerticalArea = 0
FEATURE [Part::Part2DObjectPython] Clone2D049  label="Circle128 (2D) (2D)"  # Draft 2D object (typed FeaturePython)
  Fuse = false
  Objects = -> [Clone2D034]
  Placement = pos=(3680,10797.3,0) rot=(0,0,1;0rad)
  Scale = (1,1,1)
FEATURE [Part::Part2DObjectPython] Clone2D050  label="ShapeString197 (2D) (2D)"  # Draft 2D object (typed FeaturePython)
  Fuse = false
  Objects = -> [Clone2D035]
  Placement = pos=(3597.38,10713.8,0) rot=(0,0,1;0rad)
  Scale = (1,1,1)
FEATURE [Part::Part2DObjectPython] Clone2D051  label="Circle129 (2D) (2D)"  # Draft 2D object (typed FeaturePython)
  Fuse = false
  Objects = -> [Clone2D036]
  Placement = pos=(6980,10797.3,0) rot=(0,0,1;0rad)
  Scale = (1,1,1)
FEATURE [Part::Part2DObjectPython] Clone2D052  label="ShapeString198 (2D) (2D)"  # Draft 2D object (typed FeaturePython)
  Fuse = false
  Objects = -> [Clone2D038]
  Placement = pos=(6908.07,10701.1,0) rot=(0,0,1;0rad)
  Scale = (1,1,1)
FEATURE [Part::Part2DObjectPython] Clone2D053  label="Circle130 (2D) (2D)"  # Draft 2D object (typed FeaturePython)
  Fuse = false
  Objects = -> [Clone2D037]
  Placement = pos=(7230,10797.3,0) rot=(0,0,1;0rad)
  Scale = (1,1,1)
FEATURE [Part::Part2DObjectPython] Clone2D054  label="ShapeString199 (2D) (2D)"  # Draft 2D object (typed FeaturePython)
  Fuse = false
  Objects = -> [Clone2D039]
  Placement = pos=(7144.17,10703.7,0) rot=(0,0,1;0rad)
  Scale = (1,1,1)
FEATURE [Part::Part2DObjectPython] Clone2D055  label="Circle131 (2D) (2D)"  # Draft 2D object (typed FeaturePython)
  Fuse = false
  Objects = -> [Clone2D040]
  Placement = pos=(10810,10797.3,0) rot=(0,0,1;0rad)
  Scale = (1,1,1)
FEATURE [Part::Part2DObjectPython] Clone2D056  label="ShapeString200 (2D) (2D)"  # Draft 2D object (typed FeaturePython)
  Fuse = false
  Objects = -> [Clone2D041]
  Placement = pos=(10740.3,10697.4,0) rot=(0,0,1;0rad)
  Scale = (1,1,1)
FEATURE [App::FeaturePython] Dimension228  # Draft dimension (typed FeaturePython)
  Diameter = false
  Dimline = (100,10400,0)
  Direction = (0,0,0)
  Distance = 3920
  End = (3680,10597.3,0)
  Normal = (0,0,1)
  Start = (-240,10597.3,0)
FEATURE [App::FeaturePython] Dimension229  # Draft dimension (typed FeaturePython)
  Diameter = false
  Dimline = (100,10400,0)
  Direction = (0,0,0)
  Distance = 3300
  End = (6980,10597.3,0)
  Normal = (0,0,1)
  Start = (3680,10597.3,0)
FEATURE [App::FeaturePython] Dimension230  # Draft dimension (typed FeaturePython)
  Diameter = false
  Dimline = (100,10400,0)
  Direction = (0,0,0)
  Distance = 3580
  End = (10810,10597.3,0)
  Normal = (0,0,1)
  Start = (7230,10597.3,0)
FEATURE [App::FeaturePython] Dimension231  # Draft dimension (typed FeaturePython)
  Diameter = false
  Dimline = (-1400,3680,0)
  Direction = (0,0,0)
  Distance = 5525
  End = (-1654.18,8605,0)
  Normal = (0,0,1)
  Start = (-1654.18,3080,0)
FEATURE [App::FeaturePython] Dimension232  # Draft dimension (typed FeaturePython)
  Diameter = false
  Dimline = (-1400,-400,0)
  Direction = (0,0,0)
  Distance = 3315
  End = (-1654.18,3080,0)
  Normal = (0,0,1)
  Start = (-1654.18,-235,0)
FEATURE [App::FeaturePython] Dimension233  # Draft dimension (typed FeaturePython)
  Diameter = false
  Dimline = (100,10400,0)
  Direction = (0,0,0)
  Distance = 250
  End = (7230,10597.3,0)
  Normal = (0,0,1)
  Start = (6980,10597.3,0)
FEATURE [App::FeaturePython] Dimension234  # Draft dimension (typed FeaturePython)
  Diameter = false
  Dimline = (3200,8100,0)
  Direction = (0,0,0)
  Distance = 350
  End = (3855,8605,0)
  Normal = (0,0,1)
  Start = (3505,8605,0)
FEATURE [App::FeaturePython] Dimension235  # Draft dimension (typed FeaturePython)
  Diameter = false
  Dimline = (6805,8100,0)
  Direction = (0,0,0)
  Distance = 350
  End = (7155,8605,0)
  Normal = (0,0,1)
  Start = (6805,8605,0)
FEATURE [App::FeaturePython] Dimension236  # Draft dimension (typed FeaturePython)
  Diameter = false
  Dimline = (4400,3600,0)
  Direction = (0,0,0)
  Distance = 350
  End = (3680,3255,0)
  Normal = (0,0,1)
  Start = (3680,2905,0)
FEATURE [App::FeaturePython] Dimension237  # Draft dimension (typed FeaturePython)
  Diameter = false
  Dimline = (7500,2200,0)
  Direction = (0,0,0)
  Distance = 350
  End = (7405,3080,0)
  Normal = (0,0,1)
  Start = (7055,3080,0)
FEATURE [App::FeaturePython] Dimension238  # Draft dimension (typed FeaturePython)
  Diameter = false
  Dimline = (200,7700,0)
  Direction = (0,0,0)
  Distance = 490
  End = (-50,8905,0)
  Normal = (0,0,1)
  Start = (-540,8905,0)
FEATURE [App::FeaturePython] Dimension239  # Draft dimension (typed FeaturePython)
  Diameter = false
  Dimline = (-800,8300,0)
  Direction = (0,0,0)
  Distance = 300
  End = (-240,8905,0)
  Normal = (0,0,1)
  Start = (-540,8905,0)
FEATURE [App::FeaturePython] Dimension240  # Draft dimension (typed FeaturePython)
  Diameter = false
  Dimline = (900,8000,0)
  Direction = (0,0,0)
  Distance = 190
  End = (0,8605,0)
  Normal = (0,0,1)
  Start = (0,8415,0)
FEATURE [App::FeaturePython] Dimension241  # Draft dimension (typed FeaturePython)
  Diameter = false
  Dimline = (-800,9200,0)
  Direction = (0,0,0)
  Distance = 50
  End = (-540,8905,0)
  Normal = (0,0,1)
  Start = (-590,8905,0)
FEATURE [App::GeometryPython] BuildingPart146  label="Ростверк (план)"  # Arch/BIM 172 (typed FeaturePython)
  Area = 0
  Group = -> [Clone2D,Clone2D042,Clone2D043,Clone2D044,Clone2D045,Clone2D046,Component241080,Clone2D047,Clone2D048,Component241081,Clone2D049,Clone2D050,Clone2D051,Clone2D052,Clone2D053,Clone2D054,Clone2D055,Clone2D056,Dimension228,Dimension229,Dimension230,Dimension231,Dimension232,Dimension233,Dimension234,Dimension235,Dimension236,Dimension237,Dimension238,Dimension239,Dimension240,Dimension241]
  Height = 0
  HeightPropagate = true
  IfcData = attributes={"GlobalId": {"name": "GlobalId", "type": "IfcGloballyUniqueId", "is_enum": false, "enum_values": []}, "Description": {"... (+484 chars omitted),+1 more (map truncated)
  IfcType = 172
  LevelOffset = 0
  PredefinedType = 0
FEATURE [App::GeometryPython] BuildingPart140  label="Размеры (для печати)"  # Arch/BIM 172 (typed FeaturePython)
  Area = 0
  Group = -> [BuildingPart127,BuildingPart090,BuildingPart100,BuildingPart141,BuildingPart142,BuildingPart146]
  Height = 0
  HeightPropagate = true
  IfcData = attributes={"GlobalId": {"name": "GlobalId", "type": "IfcGloballyUniqueId", "is_enum": false, "enum_values": []}, "Description": {"... (+484 chars omitted),+1 more (map truncated)
  IfcType = 172
  LevelOffset = 0
  PredefinedType = 0
FEATURE [App::FeaturePython] Section018  label="Section_top_fundament_001"  # WARN: FeaturePython — macro-defined, semantics opaque (R4)
  Clip = false
  Objects = -> [Structure695003007029,AxisSystem002,BuildingPart146]
  OnlySolids = true
  Placement = pos=(5285,4185,-400) rot=(0,0,1;0rad)
  UseMaterialColorForFill = true
FEATURE [TechDraw::DrawViewArch] ArchView016  label="Section_top_fundament_002"
  AllOn = false
  CutLineWidth = 0.5
  FillSpaces = false
  FontSize = 12
  JoinArch = false
  LineWidth = 0.25
  LockPosition = false
  RenderMode = 0
  Rotation = 0
  Scale = 0.02
  ScaleType = 2
  ShowFill = false
  ShowHidden = false
  Source = -> Section018
  X = 210
  Y = 148.5
FEATURE [TechDraw::DrawViewArch] ArchView017  label="Section_top_fundament_003"
  AllOn = true
  CutLineWidth = 0.1
  FillSpaces = false
  FontSize = 8
  JoinArch = false
  LineWidth = 0.1
  LockPosition = true
  RenderMode = 0
  Rotation = 0
  Scale = 0.02
  ScaleType = 2
  ShowFill = false
  ShowHidden = true
  Source = -> Section018
  Symbol = <blob: 59001 chars omitted>
  X = 210
  Y = 150
FEATURE [TechDraw::DrawViewAnnotation] Annotation041
  Font = osifont
  LineSpace = 80
  LockPosition = false
  MaxWidth = -1
  Rotation = 0
  ScaleType = 0
  Text = \u041f\u043b\u0430\u043d \u0440\u043e\u0441\u0442\u0432\u0435\u0440\u043a\u0430
  TextSize = 6
  TextStyle = 0
  X = 213.766
  Y = 37.602
FEATURE [TechDraw::DrawRichAnno] RichTextAnnotation
  AnnoText = <!DOCTYPE HTML PUBLIC "-//W3C//DTD HTML 4.0//EN" "http://www.w3.org/TR/REC-html40/strict.dtd">\n<html><head><meta name="qrichtext" content="1" /><style type="text/css">\np, li { white-space: pre-wrap; }\n</style></head><body style=" font-family:'Ubuntu'; font-size:11pt; font-weight:400; font-style:normal;">\n<p style=" margin-top:0px; margin-bottom:0px; margin-left:0px; margin-right:0px; -qt-block-indent:0; text-indent:0px;"><span style=" font-size:8pt;">Плитный ростверк выполняется рёбрами</span></p>\n<p style=" margin-top:0px; margin-bottom:0px; margin-left:0px; margin-right:0px; -qt-block-indent:0; text-indent:0px;"><span style=" font-size:8pt;">вниз, h ростверка 0.3м,h плиты 0.15м. </span></p>\n<p style=" margin-top:0px; margin-bottom:0px; margin-left:0px; margin-right:0px; -qt-block-indent:0; text-indent:0px;"><span style=" font-size:8pt;">Под ребрами ростверка ПСБ-10 100мм, </span></p>\n<p style=" margin-top:0px; margin-bottom:0px; margin-left:0px; margin-right:0px; -qt-block-indent:0; text-indent:0px;"><span style=" font-size:8pt;">под плитой ПСБ-10 50мм. Консоль под облицовку</span></p>\n<p style=" margin-top:0px; margin-bottom:0px; margin-left:0px; margin-right:0px; -qt-block-indent:0; text-indent:0px;"><span style=" font-size:8pt;">50мм, периметр ростверка утепляется 50мм ЭППС.</span></p></body></html>
  LockPosition = false
  MaxWidth = -1
  Rotation = 0
  ScaleType = 0
  ShowFrame = false
  X = 304.603
  Y = 36.8512
FEATURE [TechDraw::DrawPage] Page010  label="P10 план ростверка"
  KeepUpdated = false
  NextBalloonIndex = 1
  ProjectionType = 0
  Template = -> Template010
  Views = -> [ArchView017,Annotation041,RichTextAnnotation]
FEATURE [Part::Feature] Component241082  label="отделка кукушки север 015"
  shape: bbox 4952 x 25 x 1077 mm, 80 faces, 12 solids (baked)
FEATURE [Part::Feature] Component241037001  label="утепление кукушки север 013"
  shape: bbox 4934 x 150 x 1103 mm, 14 faces (baked)
FEATURE [Part::Feature] Component241077001  label="Габарит кровли001"
  shape: bbox 13090 x 12230 x 4432 mm, 87 faces (baked)
FEATURE [Part::Feature] Component241078001  label="Стропилка001"
  shape: bbox 13090 x 12230 x 4302 mm, 920 faces, 19 solids (baked)
FEATURE [Part::Feature] BuildingPart113001  label="Стойки и прогоны001"
  shape: bbox 11220 x 9010 x 3965 mm, 94 faces, 15 solids (baked)
FEATURE [Part::Feature] BuildingPart137001  label="Окна кукушек001"
  shape: bbox 11410 x 5420 x 971.9 mm, 122 faces, 15 solids (baked)
FEATURE [Part::Feature] BuildingPart136001  label="Перегородки мансарды001"
  shape: bbox 10610 x 8520 x 3119 mm, 176 faces, 8 solids (baked)
FEATURE [Part::Feature] BuildingPart133001  label="облицовка дымохода шидель001"
  shape: bbox 740 x 1910 x 4676 mm, 36 faces, 5 solids (baked)
FEATURE [Part::Feature] BuildingPart124001  label="Сантехника и мебель в ванной (мансарда)001"
  shape: bbox 2660 x 2510 x 1150 mm, 68 faces, 6 solids (baked)
FEATURE [Part::Feature] BuildingPart126001  label="Мебель (мансарда)001"
  shape: bbox 10610 x 6820 x 2902 mm, 489 faces, 26 solids (baked)
FEATURE [Part::Feature] Component241079001  label="Люк на мансарду (откр.)001"
  Placement = pos=(0,2414.4,8953.88) rot=(-1,0,0;0.785398rad)
  shape: bbox 1135 x 2708 x 2708 mm, 15 faces (baked)
FEATURE [Part::Feature] BuildingPart137002  label="Окна и двери (мансарда)001"
  shape: bbox 3480 x 2395 x 2400 mm, 64 faces, 8 solids (baked)
FEATURE [Part::Feature] Wall585001  label="Армпояс под мауэрлат001"
  Placement = pos=(5.68e-14,0,3875) rot=(0,0,1;0rad)
  shape: bbox 11230 x 9020 x 225 mm, 10 faces (baked)
FEATURE [Part::Feature] Wall586001  label="Утепление армпояса XPS 100mm001"
  Placement = pos=(0,0,3875) rot=(0,0,1;0rad)
  shape: bbox 11430 x 9220 x 225 mm, 10 faces (baked)
FEATURE [Part::Feature] Wall587022  label="Кладка в уровне армпояса 2.1нф001"
  Placement = pos=(5.68e-14,0,3875) rot=(0,0,1;0rad)
  shape: bbox 10910 x 8700 x 225 mm, 10 faces (baked)
FEATURE [Part::Feature] BuildingPart110001  label="Кладка под стойки001"
  shape: bbox 3625 x 2790 x 310 mm, 30 faces, 5 solids (baked)
FEATURE [Part::Feature] Wall584001  label="Аттиковая стена Поротерм 38Т 380мм001"
  Placement = pos=(0,0,2960) rot=(0,0,1;0rad)
  shape: bbox 11430 x 9220 x 690 mm, 30 faces, 3 solids (baked)
FEATURE [Part::Feature] Wall583001  label="Утепление в уровне перекрытия XPS 100mm001"
  Placement = pos=(0,0,2960) rot=(0,0,1;0rad)
  shape: bbox 11430 x 9220 x 160 mm, 10 faces (baked)
FEATURE [Part::Feature] Wall242001  label="Армпояс в уровне перекрытия 002"
  Placement = pos=(5.68e-14,0,2960) rot=(0,0,1;0rad)
  shape: bbox 11230 x 9020 x 160 mm, 20 faces (baked)
FEATURE [Part::Feature] Structure551001  label="монолитный участок002"
  Placement = pos=(0,0,2800) rot=(0,0,1;0rad)
  shape: bbox 1130 x 1200 x 160 mm, 6 faces (baked)
FEATURE [Part::Feature] Structure695003007044001  label="монолитный участок003"
  Placement = pos=(0,0,2800) rot=(0,0,1;0rad)
  shape: bbox 1130 x 250 x 160 mm, 6 faces (baked)
FEATURE [Part::Feature] Component197001  label="ПНО 55-12-8 3шт.001"
  Placement = pos=(-9.09e-13,4.55e-13,0) rot=(0,0,1;0rad)
  shape: bbox 3650 x 5480 x 160 mm, 47 faces, 3 solids (baked)
FEATURE [Part::Feature] Component241026001  label="ПНО 40-12-8 7шт.001"
  Placement = pos=(0,1.364e-12,0) rot=(0,0,1;0rad)
  shape: bbox 3980 x 8420 x 160 mm, 98 faces, 7 solids (baked)
FEATURE [Part::Feature] Component241027001  label="ПНО 55-10-8 2шт.001"
  Placement = pos=(0,-9.09e-13,0) rot=(0,0,1;0rad)
  shape: bbox 1990 x 5480 x 160 mm, 24 faces, 2 solids (baked)
FEATURE [Part::Feature] Component241028001  label="ПНО 33-10-8 2шт.002"
  Placement = pos=(0,-9.09e-13,0) rot=(0,0,1;0rad)
  shape: bbox 6790 x 3280 x 160 mm, 24 faces, 2 solids (baked)
FEATURE [Part::Feature] Component241029001  label="ПНО 33-12-8 4шт.002"
  Placement = pos=(0,9.1e-13,0) rot=(0,0,1;0rad)
  shape: bbox 4790 x 3280 x 160 mm, 68 faces, 4 solids (baked)
FEATURE [Part::Feature] BuildingPart099001  label="Пол мансарды001"
  shape: bbox 10670 x 8460 x 185 mm, 84 faces, 3 solids (baked)
FEATURE [Part::Feature] BuildingPart038001  label="Перемычки облицовки 1nf001"
  shape: bbox 11720 x 9510 x 375 mm, 2304 faces, 384 solids (baked)
FEATURE [Part::Feature] BuildingPart102001  label="Облицовка 1nf кирпич002"
  shape: bbox 11830 x 9640 x 4080 mm, 6045 faces, 997 solids (baked)
FEATURE [Part::Feature] BuildingPart101001  label="Элементы арх.декора002"
  shape: bbox 6660 x 11460 x 1680 mm, 60 faces, 6 solids (baked)
FEATURE [Part::Feature] BuildingPart088001  label="Перемычки по ГОСТ 948-2017"
  shape: bbox 11170 x 8960 x 682 mm, 84 faces, 14 solids (baked)
FEATURE [Part::Feature] BuildingPart089001  label="Утепление перемычек XPS 100+30mm001"
  shape: bbox 11430 x 9220 x 228 mm, 54 faces, 9 solids (baked)
FEATURE [Part::Feature] Wall004001  label="Несущая стена 2.1нф 250мм внутренняя 004"
  Placement = pos=(0,0,-200) rot=(0,0,1;0rad)
  shape: bbox 6815 x 250 x 3000 mm, 242 faces, 39 solids (baked)
FEATURE [Part::Feature] Wall562001  label="Несущая стена 2.1нф 250мм внутренняя003"
  Placement = pos=(0,0,-200) rot=(0,0,1;0rad)
  shape: bbox 250 x 8460 x 3000 mm, 281 faces, 37 solids (baked)
FEATURE [Part::Feature] Wall579001  label="Несущая стена 2.1нф 250мм внутренняя004"
  Placement = pos=(0,0,-200) rot=(0,0,1;0rad)
  shape: bbox 250 x 1160 x 3000 mm, 78 faces, 13 solids (baked)
FEATURE [Part::Feature] Wall567001  label="Внешняя стена Поротерм 38Т 380мм001"
  Placement = pos=(0,0,-200) rot=(0,0,1;0rad)
  shape: bbox 11430 x 9220 x 3000 mm, 596 faces, 82 solids (baked)
FEATURE [Part::Feature] BuildingPart005001  label="Перегородки001"
  shape: bbox 8075 x 8460 x 2800 mm, 125 faces, 15 solids (baked)
FEATURE [Part::Feature] BuildingPart081001  label="Отделка001"
  shape: bbox 10670 x 8460 x 2800 mm, 248 faces, 8 solids (baked)
FEATURE [Part::Feature] BuildingPart014001  label="Пол первого этажа001"
  shape: bbox 10670 x 9240 x 200 mm, 120 faces, 3 solids (baked)
FEATURE [Part::Feature] BuildingPart011001  label="Окна и двери 1этаж001"
  shape: bbox 11450 x 9240 x 2630 mm, 472 faces, 56 solids (baked)
FEATURE [Part::Feature] BuildingPart087001  label="Инженерные системы001"
  shape: bbox 4360 x 2130 x 7200 mm, 187 faces, 27 solids (baked)
FEATURE [Part::Feature] BuildingPart047001  label="Мебель другая001"
  shape: bbox 10600 x 8269 x 2700 mm, 344 faces, 26 solids (baked)
FEATURE [Part::Feature] BuildingPart048001  label="Сантехника и мебель в ванной001"
  shape: bbox 4330 x 8420 x 1875 mm, 126 faces, 13 solids (baked)
FEATURE [Part::Feature] BuildingPart045001  label="Мебель кухонная001"
  shape: bbox 3165 x 5175 x 2750 mm, 325 faces, 28 solids (baked)
FEATURE [Part::Feature] BuildingPart131001  label="Лестница забежная001"
  shape: bbox 1520 x 4120 x 3145 mm, 70 faces, 8 solids (baked)
FEATURE [Part::Feature] BuildingPart035001  label="Внешние элементы001"
  shape: bbox 6460 x 11730 x 180 mm, 12 faces, 2 solids (baked)
FEATURE [Part::Feature] Structure695003007029001  label="Плита ростверка 003"
  Placement = pos=(0,0,-200) rot=(0,0,1;0rad)
  shape: bbox 11750 x 9540 x 300 mm, 40 faces (baked)
FEATURE [Part::Feature] Component241074001  label="утепление торца ростверка XPS 50mm001"
  shape: bbox 11750 x 9540 x 225 mm, 14 faces (baked)
FEATURE [Part::Feature] Wall587013001  label="Деформационная подкладка и утепление PPS 50-100mm001"
  Placement = pos=(0,0,-350) rot=(0,0,1;0rad)
  shape: bbox 11750 x 9540 x 250 mm, 56 faces (baked)
FEATURE [Part::Feature] Component241076001  label="грунт в пятне застройки (для фасадов)001"
  shape: bbox 14800 x 13600 x 510 mm, 56 faces (baked)
FEATURE [App::GeometryPython] BuildingPart096  label="IFC_export"  # Arch/BIM 111 (typed FeaturePython)
  Area = 0
  GlobalId = 0M_P_ho1jD6Ar$JhrFI58w
  Group = -> [Component241082,Component241037001,Component241077001,Component241078001,BuildingPart113001,BuildingPart137001,BuildingPart136001,BuildingPart133001,BuildingPart124001,BuildingPart126001,Component241079001,BuildingPart137002,Wall585001,Wall586001,Wall587022,BuildingPart110001,Wall584001,Wall583001,Wall242001,Structure551001,Structure695003007044001,Component197001,Component241026001,+27 more]
  Height = 0
  HeightPropagate = true
  IfcData = IfcUID=0M_P_ho1jD6Ar$JhrFI58w,+2 more (map truncated)
  IfcType = 111
  LevelOffset = 0
FEATURE [App::GeometryPython] BuildingPart137003  label="Отделка цоколя"  # Arch/BIM 172 (typed FeaturePython)
  Area = 12642000
  Group = -> [Wall629,Wall628,Wall631,Wall630]
  Height = 0
  HeightPropagate = true
  IfcData = attributes={"GlobalId": {"name": "GlobalId", "type": "IfcGloballyUniqueId", "is_enum": false, "enum_values": []}, "Description": {"... (+484 chars omitted),+1 more (map truncated)
  IfcType = 172
  LevelOffset = 0
  PredefinedType = 0
FEATURE [App::GeometryPython] BuildingPart137004  label="Цоколь"  # Arch/BIM 172 (typed FeaturePython)
  Area = 27923000
  Group = -> [BuildingPart137003,Wall311,Wall310]
  Height = 0
  HeightPropagate = true
  IfcData = attributes={"GlobalId": {"name": "GlobalId", "type": "IfcGloballyUniqueId", "is_enum": false, "enum_values": []}, "Description": {"... (+484 chars omitted),+1 more (map truncated)
  IfcType = 172
  LevelOffset = 0
  PredefinedType = 0
FEATURE [Part::MultiFuse] Fusion011003002002005003032  label="перегородки вычет 001"
  Shapes = -> [Wall186,Wall128,Wall223,Wall231,Wall230,Wall225,Wall187,Wall188,Wall162,Wall402,Wall222,Wall416,Wall417,Wall419,Wall420]
FEATURE [Part::FeaturePython] Component241079002  label="перегородки вычет 002"  # Arch/BIM 0 (typed FeaturePython)
  Base = -> Fusion011003002002005003032
  HorizontalArea = 0
  IfcData = attributes={"GlobalId": {"name": "GlobalId", "type": "IfcGloballyUniqueId", "is_enum": false, "enum_values": []}, "Description": {"... (+538 chars omitted),+1 more (map truncated)
  IfcType = 0
  MoveBase = false
  MoveWithHost = false
  PerimeterLength = 0
  PredefinedType = 0
  VerticalArea = 0
FEATURE [Part::FeaturePython] Structure  label="Утепление пола XPS 100mm"  # Arch/BIM 118 (typed FeaturePython)
  Additions = -> [Structure066,Structure069]
  Base = -> Rectangle3870
  FaceMaker = 0
  GlobalId = 12HaZCeTXDOvnd1ysX9j$x
  Height = 100
  HorizontalArea = 0
  IfcData = IfcUID=12HaZCeTXDOvnd1ysX9j$x,+2 more (map truncated)
  IfcType = 118
  Length = 7520
  Material = -> Material002
  MoveBase = false
  MoveWithHost = false
  Nodes = (4) [(-50,-45,0),(10620,-45,0),(10620,8415,0),(-50,8415,0)]
  NodesOffset = 0
  Normal = (0,0,0)
  PerimeterLength = 0
  Placement = pos=(0,0,-200) rot=(0,0,1;0rad)
  PredefinedType = 0
  Subtractions = -> [Wall560,Wall579,Wall562,Component241079002]
  VerticalArea = 0
  Width = 12620
FEATURE [App::GeometryPython] BuildingPart020  label="Утепление пола 100мм XPS"  # Arch/BIM 52 (typed FeaturePython)
  Area = 0
  GlobalId = 3yH_rZ_TXC4Rf1NqFztroU
  Group = -> [Structure]
  Height = 0
  HeightPropagate = true
  IfcData = IfcUID=3yH_rZ_TXC4Rf1NqFztroU,attributes={"GlobalId": {"value": "3yH_rZ_TXC4Rf1NqFztroU"}},+1 more (map truncated)
  IfcType = 52
  LevelOffset = 0
FEATURE [Part::FeaturePython] Structure434  label="Стяжка тёплого пола 80mm"  # Arch/BIM 118 (typed FeaturePython)
  Additions = -> [Structure368,Structure371]
  Base = -> Rectangle3870
  FaceMaker = 0
  GlobalId = 3i06NLwF5739lSL_IHGmf1
  Height = 80
  HorizontalArea = 0
  IfcData = IfcUID=3i06NLwF5739lSL_IHGmf1,+2 more (map truncated)
  IfcType = 118
  Length = 7520
  Material = -> Material018
  MoveBase = false
  MoveWithHost = false
  Nodes = (4) [(-50,-45,0),(10620,-45,0),(10620,8415,0),(-50,8415,0)]
  NodesOffset = 0
  Normal = (0,0,0)
  PerimeterLength = 0
  Placement = pos=(0,0,-100) rot=(0,0,1;0rad)
  PredefinedType = 0
  Subtractions = -> [Wall560,Wall579,Wall562,Component241079002]
  VerticalArea = 0
  Width = 12620
FEATURE [App::GeometryPython] BuildingPart085  label="Стяжка тёплого пола 80мм"  # Arch/BIM 52 (typed FeaturePython)
  Area = 0
  GlobalId = 0paGEjjH988O$uNBI5I7u1
  Group = -> [Structure434]
  Height = 0
  HeightPropagate = true
  IfcData = IfcUID=0paGEjjH988O$uNBI5I7u1,+2 more (map truncated)
  IfcType = 52
  LevelOffset = 0
FEATURE [Part::FeaturePython] Structure435  label="Покрытие пола 20мм001"  # Arch/BIM 118 (typed FeaturePython)
  Additions = -> [Structure374,Structure377]
  Base = -> Rectangle3870
  FaceMaker = 0
  GlobalId = 069jleHXv70OyIjGnnOFdt
  Height = 20
  HorizontalArea = 0
  IfcData = IfcUID=069jleHXv70OyIjGnnOFdt,+2 more (map truncated)
  IfcType = 118
  Length = 7520
  Material = -> Material018
  MoveBase = false
  MoveWithHost = false
  Nodes = (4) [(-50,-45,0),(10620,-45,0),(10620,8415,0),(-50,8415,0)]
  NodesOffset = 0
  Normal = (0,0,0)
  PerimeterLength = 0
  Placement = pos=(0,0,-20) rot=(0,0,1;0rad)
  PredefinedType = 0
  Subtractions = -> [Wall560,Wall562,Wall579,Component241079002]
  VerticalArea = 0
  Width = 12620
FEATURE [App::GeometryPython] BuildingPart086  label="Покрытие пола 20мм"  # Arch/BIM 52 (typed FeaturePython)
  Area = 0
  GlobalId = 1v2dx_MFP8whu6FdM2ihDU
  Group = -> [Structure435]
  Height = 0
  HeightPropagate = true
  IfcData = IfcUID=1v2dx_MFP8whu6FdM2ihDU,+2 more (map truncated)
  IfcType = 52
  LevelOffset = 0
FEATURE [App::GeometryPython] BuildingPart014  label="Пол первого этажа"  # Arch/BIM 52 (typed FeaturePython)
  Area = 0
  GlobalId = 1N3QY958b6OO8VUwpY7Wbc
  Group = -> [BuildingPart020,BuildingPart085,BuildingPart086]
  Height = 0
  HeightPropagate = true
  IfcData = IfcUID=1N3QY958b6OO8VUwpY7Wbc,attributes={"GlobalId": {"value": "1N3QY958b6OO8VUwpY7Wbc"}},+1 more (map truncated)
  IfcType = 52
  LevelOffset = 0
FEATURE [App::GeometryPython] BuildingPart103  label="Уровень первого этажа"  # Arch/BIM 14 (typed FeaturePython)
  Area = 7.70058e+08
  CompositionType = 0
  Elevation = 0
  GlobalId = 377tEiMTb6celHDz_UVksa
  Group = -> [BuildingPart101,BuildingPart102,BuildingPart002,BuildingPart005,BuildingPart081,BuildingPart038,BuildingPart014,BuildingPart011,BuildingPart087,BuildingPart049,BuildingPart131,BuildingPart137004]
  Height = 3130
  HeightPropagate = true
  IfcData = IfcUID=377tEiMTb6celHDz_UVksa,+2 more (map truncated)
  IfcType = 14
  LevelOffset = 0
  LongName = Floor
  Placement = pos=(-560,-540,0) rot=(0,0,1;0rad)
  expr: Elevation = .Placement.Base.z
FEATURE [App::GeometryPython] BuildingPart105  label="Индивидуальный жилой дом"  # Arch/BIM 10 (typed FeaturePython)
  Area = 1.17977e+09
  BuildingType = 36
  CompositionType = 0
  ElevationOfRefHeight = 0
  ElevationOfTerrain = 0
  GlobalId = 1wNqu2gmH0$Q5UGcgb9xOg
  Group = -> [App__DocumentObjectGroup,BuildingPart103,BuildingPart104,BuildingPart106,BuildingPart035,BuildingPart145]
  Height = 0
  HeightPropagate = true
  IfcData = IfcUID=1wNqu2gmH0$Q5UGcgb9xOg,+2 more (map truncated)
  IfcType = 10
  LevelOffset = 0
  LongName = Building
  Placement = pos=(-560,-540,0) rot=(0,0,1;0rad)
FEATURE [Part::FeaturePython] Site001  label="Участок ИЖС"  # Arch/BIM 117 (typed FeaturePython)
  AdditionVolume = 0
  CompositionType = 0
  Declination = 0
  Elevation = 0
  ExtrusionVector = (0,0,-100000)
  GlobalId = 0q3YkvPDD0KRQl3VYghQdF
  Group = -> [BuildingPart105,BuildingPart067,BuildingPart143]
  IfcData = IfcUID=0q3YkvPDD0KRQl3VYghQdF,+2 more (map truncated)
  IfcType = 117
  Latitude = 0
  LongName = Site
  Longitude = 0
  OriginOffset = (0,0,0)
  Perimeter = 0
  ProjectedArea = 0
  RefElevation = 0
  RemoveSplitter = false
  SubtractionVolume = 0
  TimeZone = 0
  expr: RefElevation = .Elevation.Value
FEATURE [App::FeaturePython] Section006  label="Section 1st floor plan"  # WARN: FeaturePython — macro-defined, semantics opaque (R4)
  Clip = true
  Objects = -> [BuildingPart103,BuildingPart090]
  OnlySolids = true
  Placement = pos=(6260,3730,1500) rot=(0,0,1;0rad)
  UseMaterialColorForFill = true
FEATURE [TechDraw::DrawViewArch] ArchView007
  AllOn = true
  CutLineWidth = 0.1
  FillSpaces = false
  FontSize = 7
  JoinArch = false
  LineWidth = 0.1
  LockPosition = true
  RenderMode = 0
  Rotation = 0
  Scale = 0.02
  ScaleType = 2
  ShowFill = true
  ShowHidden = true
  Source = -> Section006
  Symbol = <blob: 879922 chars omitted>
  X = 210
  Y = 150
FEATURE [TechDraw::DrawPage] Page002  label="План 1 этаж"
  KeepUpdated = false
  NextBalloonIndex = 1
  ProjectionType = 0
  Template = -> Template002
  Views = -> [Annotation007,ArchView007]
FEATURE [App::FeaturePython] Section  label="Section A-A"  # WARN: FeaturePython — macro-defined, semantics opaque (R4)
  Clip = true
  Objects = -> [BuildingPart103,BuildingPart104,BuildingPart106,BuildingPart131,BuildingPart145,BuildingPart035]
  OnlySolids = true
  Placement = pos=(9000,3730,3690.5) rot=(0.57735,0.57735,0.57735;2.0944rad)
  UseMaterialColorForFill = true
FEATURE [TechDraw::DrawViewArch] ArchView
  AllOn = true
  CutLineWidth = 0.1
  FillSpaces = false
  FontSize = 8
  JoinArch = false
  LineWidth = 0.1
  LockPosition = true
  RenderMode = 0
  Rotation = 90
  Scale = 0.02
  ScaleType = 2
  ShowFill = true
  ShowHidden = false
  Source = -> Section
  Symbol = <blob: 993368 chars omitted>
  X = 224.182
  Y = 160.176
FEATURE [TechDraw::DrawPage] Page001  label="Разрез по А-А"
  KeepUpdated = false
  NextBalloonIndex = 1
  ProjectionType = 0
  Scale = 0.02
  Template = -> Template001
  Views = -> [Annotation008,ArchView,Annotation009,Annotation010,Annotation011,Annotation012,LeaderLine,LeaderLine001,LeaderLine002,LeaderLine003,Annotation013,Annotation014,Annotation015,Annotation016,LeaderLine004,Annotation017,Annotation018,Annotation019,Annotation020,Annotation021,Annotation022,Annotation023,Annotation024,Annotation025,Annotation026,LeaderLine005,LeaderLine006,LeaderLine007,LeaderLine008,+13 more]
FEATURE [App::FeaturePython] Section008  label="Section B-B"  # WARN: FeaturePython — macro-defined, semantics opaque (R4)
  Clip = true
  Objects = -> [BuildingPart103,BuildingPart104,BuildingPart106,BuildingPart131,BuildingPart145,BuildingPart035]
  OnlySolids = true
  Placement = pos=(5900,3730,3630.5) rot=(0.57735,0.57735,0.57735;2.0944rad)
  UseMaterialColorForFill = true
FEATURE [TechDraw::DrawViewArch] ArchView009
  AllOn = true
  CutLineWidth = 0.1
  FillSpaces = false
  FontSize = 8
  JoinArch = false
  LineWidth = 0.1
  LockPosition = true
  RenderMode = 0
  Rotation = 90
  Scale = 0.02
  ScaleType = 2
  ShowFill = true
  ShowHidden = false
  Source = -> Section008
  Symbol = <blob: 982284 chars omitted>
  X = 224.18
  Y = 160.18
FEATURE [TechDraw::DrawPage] Page005  label="Разрез по B-B"
  KeepUpdated = false
  NextBalloonIndex = 1
  ProjectionType = 0
  Scale = 0.02
  Template = -> Template005
  Views = -> [ArchView009,Annotation037]
FEATURE [App::FeaturePython] Section009  label="Section С-С"  # WARN: FeaturePython — macro-defined, semantics opaque (R4)
  Clip = true
  Objects = -> [BuildingPart105]
  OnlySolids = true
  Placement = pos=(6116.78,2400,3679.8) rot=(1,0,0;1.5708rad)
  UseMaterialColorForFill = true
FEATURE [App::FeaturePython] Section012  label="Section_F_north"  # WARN: FeaturePython — macro-defined, semantics opaque (R4)
  Clip = false
  Objects = -> [BuildingPart105,Common105]
  OnlySolids = true
  Placement = pos=(5285,-3000,3583.14) rot=(1,0,0;1.5708rad)
  UseMaterialColorForFill = false
FEATURE [App::FeaturePython] Section013  label="Section_F_south"  # WARN: FeaturePython — macro-defined, semantics opaque (R4)
  Clip = false
  Objects = -> [BuildingPart105,Common105]
  OnlySolids = true
  Placement = pos=(5285,12000,3583.14) rot=(0,0.707107,0.707107;3.14159rad)
  UseMaterialColorForFill = false
FEATURE [App::FeaturePython] Section014  label="Section_F_east"  # WARN: FeaturePython — macro-defined, semantics opaque (R4)
  Clip = false
  Objects = -> [BuildingPart105,Common105]
  OnlySolids = true
  Placement = pos=(-2000,4185,3583.14) rot=(-0.57735,0.57735,0.57735;4.18879rad)
  UseMaterialColorForFill = false
FEATURE [App::FeaturePython] Section015  label="Section_F_west"  # WARN: FeaturePython — macro-defined, semantics opaque (R4)
  Clip = false
  Objects = -> [BuildingPart105,Common105]
  OnlySolids = true
  Placement = pos=(13000,4185,3583.14) rot=(0.57735,0.57735,0.57735;2.0944rad)
  UseMaterialColorForFill = false
FEATURE [TechDraw::DrawViewArch] ArchView012  label="Section_F_north001"
  AllOn = false
  Caption = Север
  CutLineWidth = 0.1
  FillSpaces = false
  FontSize = 12
  JoinArch = false
  LineWidth = 0.1
  LockPosition = true
  RenderMode = 0
  Rotation = 270
  Scale = 0.01
  ScaleType = 2
  ShowFill = true
  ShowHidden = false
  Source = -> Section012
  Symbol = <blob: 97009 chars omitted>
  X = 130
  Y = 200
FEATURE [TechDraw::DrawViewArch] ArchView013  label="Section_F_south001"
  AllOn = false
  Caption = Юг
  CutLineWidth = 0.1
  FillSpaces = false
  FontSize = 12
  JoinArch = false
  LineWidth = 0.1
  LockPosition = true
  RenderMode = 0
  Rotation = 180
  Scale = 0.01
  ScaleType = 2
  ShowFill = true
  ShowHidden = false
  Source = -> Section013
  Symbol = <blob: 103232 chars omitted>
  X = 130
  Y = 100
FEATURE [TechDraw::DrawViewArch] ArchView014  label="Section_F_east001"
  AllOn = false
  Caption = Восток
  CutLineWidth = 0.1
  FillSpaces = false
  FontSize = 12
  JoinArch = false
  LineWidth = 0.1
  LockPosition = true
  RenderMode = 0
  Rotation = 270
  Scale = 0.01
  ScaleType = 2
  ShowFill = true
  ShowHidden = false
  Source = -> Section014
  Symbol = <blob: 66057 chars omitted>
  X = 300
  Y = 100
FEATURE [TechDraw::DrawViewArch] ArchView015  label="Section_F_west001"
  AllOn = false
  Caption = запад
  CutLineWidth = 0.1
  FillSpaces = false
  FontSize = 12
  JoinArch = false
  LineWidth = 0.1
  LockPosition = true
  RenderMode = 0
  Rotation = 90
  Scale = 0.01
  ScaleType = 2
  ShowFill = true
  ShowHidden = false
  Source = -> Section015
  Symbol = <blob: 79465 chars omitted>
  X = 300
  Y = 200
FEATURE [TechDraw::DrawPage] Page006  label="Фасады"
  KeepUpdated = false
  NextBalloonIndex = 1
  ProjectionType = 0
  Template = -> Template006
  Views = -> [Annotation036,ArchView012,ArchView013,ArchView014,ArchView015]
FEATURE [App::FeaturePython] Section017  label="Section Front"  # WARN: FeaturePython — macro-defined, semantics opaque (R4)
  Clip = false
  Objects = -> [BuildingPart105]
  OnlySolids = true
  Placement = pos=(5285,4185,3703.14) rot=(1,0,0;1.5708rad)
  UseMaterialColorForFill = false
FEATURE [App::DocumentObjectGroup] Group129  label="Sections"
  Group = -> [Section006,Section,Section008,Section007,Section009,Section010,Section011,Section012,Section013,Section014,Section015,Section016,Section017,Section018]
FEATURE [App::DocumentObjectGroup] Group130  label="Листы проекта для печати"
  Group = -> [Group127,Group129,Page004,Page006,Page,Page002,Page003,Page001,Page005,Page008,Page009,Page010]
FEATURE [Part::Part2DObjectPython] Wire  label="Wire1115"  # Draft 2D object (typed FeaturePython)
  Area = 6.48337e+07
  ChamferSize = 0
  Closed = true
  End = (10455,9625,3645.76)
  FilletRadius = 0
  Length = 35467.6
  MakeFace = true
  Placement = pos=(11816.5,9625,3645.76) rot=(-1,0,0;0.610865rad)
  Points = (8) [(0,0,0),(-3809.13,-6641.01,0),(-9253.89,-6641.01,0),(-13063,0,0),(-5461.51,0,0),(-5461.51,824.023,0),(-1361.51,824.023,0),(-1361.51,0,0)]
  Start = (11816.5,9625,3645.76)
  Subdivisions = 0
FEATURE [Part::Part2DObjectPython] Wire1112  # Draft 2D object (typed FeaturePython)
  Area = 0
  ChamferSize = 0
  Closed = true
  End = (-1260,9625,3632.09)
  FilletRadius = 0
  Length = 26230.2
  MakeFace = true
  Placement = pos=(-1246.51,9625,3645.76) rot=(-1,0,0;0.610865rad)
  Points = (5) [(0,0,0),(3809.13,-6641.01,0),(-9.09495e-13,-8912.37,-6240.51),(-13.4907,-8904.53,-6251.71),(-13.4907,7.84037,-11.1972)]
  Start = (-1246.51,9625,3645.76)
  Subdivisions = 0
FEATURE [Part::Part2DObjectPython] Wire1113  # Draft 2D object (typed FeaturePython)
  Area = 0
  ChamferSize = 0
  Closed = true
  End = (11816.5,-1255,3645.76)
  FilletRadius = 0
  Length = 26230.2
  MakeFace = true
  Placement = pos=(8007.38,4185,7454.89) rot=(-1,0,0;0.610865rad)
  Points = (5) [(0,0,0),(3809.13,6641.01,0),(3822.62,6648.85,-11.1972),(3822.62,-2263.52,-6251.71),(3809.13,-2271.36,-6240.51)]
  Start = (8007.38,4185,7454.89)
  Subdivisions = 0
FEATURE [Part::Part2DObjectPython] Wire1114  # Draft 2D object (typed FeaturePython)
  Area = 6.44052e+07
  ChamferSize = 0
  Closed = true
  End = (3495,-1255,3645.76)
  FilletRadius = 0
  Length = 35467.6
  MakeFace = true
  Placement = pos=(-1246.51,-1255,3645.76) rot=(1,0,0;0.610865rad)
  Points = (8) [(0,0,0),(3809.13,6641.01,1.81899e-12),(9253.89,6641.01,1.81899e-12),(13063,0,-4.54747e-13),(8321.51,-4.54747e-13,-4.54747e-13),+3 more]
  Start = (-1246.51,-1255,3645.76)
  Subdivisions = 0
FEATURE [App::DocumentObjectGroup] Group132  label="разное"
  Group = -> [Dimension072,Dimension073,Dimension074,Dimension075,Dimension076,Dimension077,Dimension078,Rectangle3389,Line1687,Line1688,Line1689,Line1690,Line1692,Line1693,Line1694,Line1695,Rectangle3390,Rectangle3392,Rectangle3393,Rectangle3395,Circle135,Line1697,Line1699,Circle136,Line1702,Rectangle3400,Line1704,Circle140,Circle141,Line1705,Circle142,Rectangle3401,Line1706,Line1710,Line1711,Line1712,+27 more]
note: 75 file-system paths scrubbed to <path> (originals preserved in the JSON sidecar)
